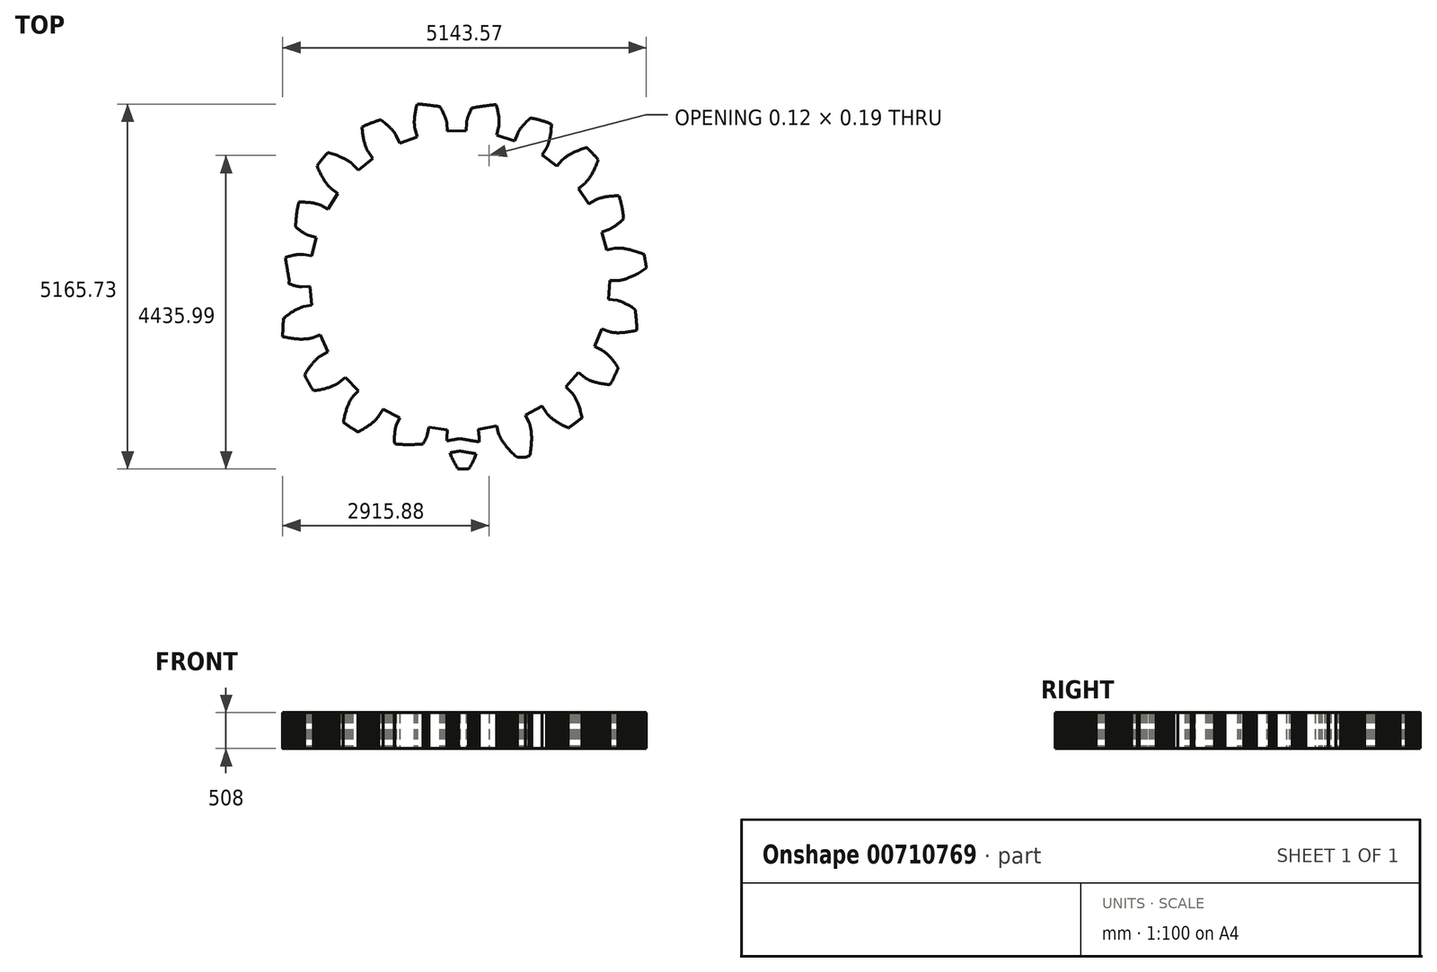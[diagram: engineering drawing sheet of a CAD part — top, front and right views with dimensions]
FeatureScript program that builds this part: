
annotation { "Feature Type Name" : "Feature", "Feature Type Description" : "" }
export const myFeature = defineFeature(function(context is Context, id is Id, definition is map)
    precondition{}
    {
        {
            var Q0;
            Q0=qCreatedBy(makeId("Top.planeOp"),FACE);
            var sketch = newSketch(context, id + "F0", { "sketchPlane" : qUnion([Q0])});
            skLineSegment(sketch, "E0", {"start": v(-9485.18, 1999.38) * mm, "end": v(-9483.34, 1999.46) * mm});
            skLineSegment(sketch, "E1", {"start": v(-9483.34, 1999.46) * mm, "end": v(-9480.74, 1999.63) * mm});
            skLineSegment(sketch, "E2", {"start": v(-9480.74, 1999.63) * mm, "end": v(-9477.39, 1999.9) * mm});
            skLineSegment(sketch, "E3", {"start": v(-9477.39, 1999.9) * mm, "end": v(-9473.3, 2000.32) * mm});
            skLineSegment(sketch, "E4", {"start": v(-9473.3, 2000.32) * mm, "end": v(-9468.45, 2000.9) * mm});
            skLineSegment(sketch, "E5", {"start": v(-9468.45, 2000.9) * mm, "end": v(-9462.88, 2001.66) * mm});
            skLineSegment(sketch, "E6", {"start": v(-9462.88, 2001.66) * mm, "end": v(-9456.58, 2002.65) * mm});
            skLineSegment(sketch, "E7", {"start": v(-9456.58, 2002.65) * mm, "end": v(-9449.55, 2003.88) * mm});
            skLineSegment(sketch, "E8", {"start": v(-9449.55, 2003.88) * mm, "end": v(-9441.8, 2005.4) * mm});
            skLineSegment(sketch, "E9", {"start": v(-9441.8, 2005.4) * mm, "end": v(-9433.35, 2007.2) * mm});
            skLineSegment(sketch, "E10", {"start": v(-9433.35, 2007.2) * mm, "end": v(-9424.2, 2009.33) * mm});
            skLineSegment(sketch, "E11", {"start": v(-9424.2, 2009.33) * mm, "end": v(-9414.34, 2011.82) * mm});
            skLineSegment(sketch, "E12", {"start": v(-9414.34, 2011.82) * mm, "end": v(-9403.81, 2014.68) * mm});
            skLineSegment(sketch, "E13", {"start": v(-9403.81, 2014.68) * mm, "end": v(-9392.62, 2017.95) * mm});
            skLineSegment(sketch, "E14", {"start": v(-9392.62, 2017.95) * mm, "end": v(-9380.76, 2021.65) * mm});
            skLineSegment(sketch, "E15", {"start": v(-9380.76, 2021.65) * mm, "end": v(-9368.25, 2025.8) * mm});
            skLineSegment(sketch, "E16", {"start": v(-9368.25, 2025.8) * mm, "end": v(-9355.11, 2030.43) * mm});
            skLineSegment(sketch, "E17", {"start": v(-9355.11, 2030.43) * mm, "end": v(-9341.35, 2035.57) * mm});
            skLineSegment(sketch, "E18", {"start": v(-9341.35, 2035.57) * mm, "end": v(-9326.99, 2041.24) * mm});
            skLineSegment(sketch, "E19", {"start": v(-9326.99, 2041.24) * mm, "end": v(-9312.03, 2047.46) * mm});
            skLineSegment(sketch, "E20", {"start": v(-9312.03, 2047.46) * mm, "end": v(-9296.5, 2054.26) * mm});
            skLineSegment(sketch, "E21", {"start": v(-9296.5, 2054.26) * mm, "end": v(-9280.41, 2061.65) * mm});
            skLineSegment(sketch, "E22", {"start": v(-9280.41, 2061.65) * mm, "end": v(-9263.78, 2069.67) * mm});
            skLineSegment(sketch, "E23", {"start": v(-9263.78, 2069.67) * mm, "end": v(-9246.63, 2078.33) * mm});
            skLineSegment(sketch, "E24", {"start": v(-9246.63, 2078.33) * mm, "end": v(-9228.97, 2087.66) * mm});
            skLineSegment(sketch, "E25", {"start": v(-9228.97, 2087.66) * mm, "end": v(-9210.82, 2097.68) * mm});
            skLineSegment(sketch, "E26", {"start": v(-9210.82, 2097.68) * mm, "end": v(-9192.2, 2108.4) * mm});
            skLineSegment(sketch, "E27", {"start": v(-9192.2, 2108.4) * mm, "end": v(-9173.14, 2119.86) * mm});
            skLineSegment(sketch, "E28", {"start": v(-9173.14, 2119.86) * mm, "end": v(-9153.66, 2132.06) * mm});
            skLineSegment(sketch, "E29", {"start": v(-9153.66, 2132.06) * mm, "end": v(-9133.76, 2145.04) * mm});
            skLineSegment(sketch, "E30", {"start": v(-9133.76, 2145.04) * mm, "end": v(-9113.48, 2158.8) * mm});
            skLineSegment(sketch, "E31", {"start": v(-9113.48, 2158.8) * mm, "end": v(-9092.85, 2173.36) * mm});
            skLineSegment(sketch, "E32", {"start": v(-9092.85, 2173.36) * mm, "end": v(-9071.87, 2188.75) * mm});
            skLineSegment(sketch, "E33", {"start": v(-9071.87, 2188.75) * mm, "end": v(-9064.77, 2203.89) * mm});
            skLineSegment(sketch, "E34", {"start": v(-9064.77, 2203.89) * mm, "end": v(-9078.9, 2341.03) * mm});
            skLineSegment(sketch, "E35", {"start": v(-9078.9, 2341.03) * mm, "end": v(-9088.93, 2354.4) * mm});
            skLineSegment(sketch, "E36", {"start": v(-9088.93, 2354.4) * mm, "end": v(-9112.6, 2365.2) * mm});
            skLineSegment(sketch, "E37", {"start": v(-9112.6, 2365.2) * mm, "end": v(-9135.78, 2375.25) * mm});
            skLineSegment(sketch, "E38", {"start": v(-9135.78, 2375.25) * mm, "end": v(-9158.43, 2384.59) * mm});
            skLineSegment(sketch, "E39", {"start": v(-9158.43, 2384.59) * mm, "end": v(-9180.55, 2393.23) * mm});
            skLineSegment(sketch, "E40", {"start": v(-9180.55, 2393.23) * mm, "end": v(-9202.12, 2401.2) * mm});
            skLineSegment(sketch, "E41", {"start": v(-9202.12, 2401.2) * mm, "end": v(-9223.11, 2408.54) * mm});
            skLineSegment(sketch, "E42", {"start": v(-9223.11, 2408.54) * mm, "end": v(-9243.52, 2415.25) * mm});
            skLineSegment(sketch, "E43", {"start": v(-9243.52, 2415.25) * mm, "end": v(-9263.33, 2421.35) * mm});
            skLineSegment(sketch, "E44", {"start": v(-9263.33, 2421.35) * mm, "end": v(-9282.52, 2426.89) * mm});
            skLineSegment(sketch, "E45", {"start": v(-9282.52, 2426.89) * mm, "end": v(-9301.08, 2431.87) * mm});
            skLineSegment(sketch, "E46", {"start": v(-9301.08, 2431.87) * mm, "end": v(-9319, 2436.33) * mm});
            skLineSegment(sketch, "E47", {"start": v(-9319, 2436.33) * mm, "end": v(-9336.26, 2440.3) * mm});
            skLineSegment(sketch, "E48", {"start": v(-9336.26, 2440.3) * mm, "end": v(-9352.85, 2443.79) * mm});
            skLineSegment(sketch, "E49", {"start": v(-9352.85, 2443.79) * mm, "end": v(-9368.76, 2446.83) * mm});
            skLineSegment(sketch, "E50", {"start": v(-9368.76, 2446.83) * mm, "end": v(-9383.98, 2449.45) * mm});
            skLineSegment(sketch, "E51", {"start": v(-9383.98, 2449.45) * mm, "end": v(-9398.5, 2451.67) * mm});
            skLineSegment(sketch, "E52", {"start": v(-9398.5, 2451.67) * mm, "end": v(-9412.3, 2453.53) * mm});
            skLineSegment(sketch, "E53", {"start": v(-9412.3, 2453.53) * mm, "end": v(-9425.4, 2455.05) * mm});
            skLineSegment(sketch, "E54", {"start": v(-9425.4, 2455.05) * mm, "end": v(-9437.75, 2456.25) * mm});
            skLineSegment(sketch, "E55", {"start": v(-9437.75, 2456.25) * mm, "end": v(-9449.38, 2457.17) * mm});
            skLineSegment(sketch, "E56", {"start": v(-9449.38, 2457.17) * mm, "end": v(-9460.28, 2457.83) * mm});
            skLineSegment(sketch, "E57", {"start": v(-9460.28, 2457.83) * mm, "end": v(-9470.42, 2458.26) * mm});
            skLineSegment(sketch, "E58", {"start": v(-9470.42, 2458.26) * mm, "end": v(-9479.82, 2458.48) * mm});
            skLineSegment(sketch, "E59", {"start": v(-9479.82, 2458.48) * mm, "end": v(-9488.47, 2458.52) * mm});
            skLineSegment(sketch, "E60", {"start": v(-9488.47, 2458.52) * mm, "end": v(-9496.36, 2458.42) * mm});
            skLineSegment(sketch, "E61", {"start": v(-9496.36, 2458.42) * mm, "end": v(-9503.5, 2458.2) * mm});
            skLineSegment(sketch, "E62", {"start": v(-9503.5, 2458.2) * mm, "end": v(-9509.86, 2457.88) * mm});
            skLineSegment(sketch, "E63", {"start": v(-9509.86, 2457.88) * mm, "end": v(-9515.48, 2457.5) * mm});
            skLineSegment(sketch, "E64", {"start": v(-9515.48, 2457.5) * mm, "end": v(-9520.33, 2457.07) * mm});
            skLineSegment(sketch, "E65", {"start": v(-9520.33, 2457.07) * mm, "end": v(-9524.42, 2456.64) * mm});
            skLineSegment(sketch, "E66", {"start": v(-9524.42, 2456.64) * mm, "end": v(-9527.76, 2456.23) * mm});
            skLineSegment(sketch, "E67", {"start": v(-9527.76, 2456.23) * mm, "end": v(-9530.34, 2455.86) * mm});
            skLineSegment(sketch, "E68", {"start": v(-9530.34, 2455.86) * mm, "end": v(-9532.16, 2455.57) * mm});
            skLineSegment(sketch, "E69", {"start": v(-9532.16, 2455.57) * mm, "end": v(-9533.24, 2455.37) * mm});
            skLineSegment(sketch, "E70", {"start": v(-9533.24, 2455.37) * mm, "end": v(-9647.53, 2431.59) * mm});
            skLineSegment(sketch, "E71", {"start": v(-9647.53, 2431.59) * mm, "end": v(-9717.93, 2688) * mm});
            skLineSegment(sketch, "E72", {"start": v(-9717.93, 2688) * mm, "end": v(-9607.52, 2725.9) * mm});
            skLineSegment(sketch, "E73", {"start": v(-9607.52, 2725.9) * mm, "end": v(-9606.5, 2726.29) * mm});
            skLineSegment(sketch, "E74", {"start": v(-9606.5, 2726.29) * mm, "end": v(-9604.78, 2726.97) * mm});
            skLineSegment(sketch, "E75", {"start": v(-9604.78, 2726.97) * mm, "end": v(-9602.37, 2727.97) * mm});
            skLineSegment(sketch, "E76", {"start": v(-9602.37, 2727.97) * mm, "end": v(-9599.3, 2729.32) * mm});
            skLineSegment(sketch, "E77", {"start": v(-9599.3, 2729.32) * mm, "end": v(-9595.55, 2731.04) * mm});
            skLineSegment(sketch, "E78", {"start": v(-9595.55, 2731.04) * mm, "end": v(-9591.17, 2733.15) * mm});
            skLineSegment(sketch, "E79", {"start": v(-9591.17, 2733.15) * mm, "end": v(-9586.14, 2735.7) * mm});
            skLineSegment(sketch, "E80", {"start": v(-9586.14, 2735.7) * mm, "end": v(-9580.5, 2738.67) * mm});
            skLineSegment(sketch, "E81", {"start": v(-9580.5, 2738.67) * mm, "end": v(-9574.25, 2742.12) * mm});
            skLineSegment(sketch, "E82", {"start": v(-9574.25, 2742.12) * mm, "end": v(-9567.42, 2746.06) * mm});
            skLineSegment(sketch, "E83", {"start": v(-9567.42, 2746.06) * mm, "end": v(-9560, 2750.52) * mm});
            skLineSegment(sketch, "E84", {"start": v(-9560, 2750.52) * mm, "end": v(-9552.04, 2755.5) * mm});
            skLineSegment(sketch, "E85", {"start": v(-9552.04, 2755.5) * mm, "end": v(-9543.53, 2761.05) * mm});
            skLineSegment(sketch, "E86", {"start": v(-9543.53, 2761.05) * mm, "end": v(-9534.5, 2767.18) * mm});
            skLineSegment(sketch, "E87", {"start": v(-9534.5, 2767.18) * mm, "end": v(-9524.97, 2773.91) * mm});
            skLineSegment(sketch, "E88", {"start": v(-9524.97, 2773.91) * mm, "end": v(-9514.96, 2781.26) * mm});
            skLineSegment(sketch, "E89", {"start": v(-9514.96, 2781.26) * mm, "end": v(-9504.48, 2789.25) * mm});
            skLineSegment(sketch, "E90", {"start": v(-9504.48, 2789.25) * mm, "end": v(-9493.56, 2797.9) * mm});
            skLineSegment(sketch, "E91", {"start": v(-9493.56, 2797.9) * mm, "end": v(-9482.21, 2807.22) * mm});
            skLineSegment(sketch, "E92", {"start": v(-9482.21, 2807.22) * mm, "end": v(-9470.46, 2817.25) * mm});
            skLineSegment(sketch, "E93", {"start": v(-9470.46, 2817.25) * mm, "end": v(-9458.34, 2827.99) * mm});
            skLineSegment(sketch, "E94", {"start": v(-9458.34, 2827.99) * mm, "end": v(-9445.86, 2839.46) * mm});
            skLineSegment(sketch, "E95", {"start": v(-9445.86, 2839.46) * mm, "end": v(-9433.04, 2851.68) * mm});
            skLineSegment(sketch, "E96", {"start": v(-9433.04, 2851.68) * mm, "end": v(-9419.91, 2864.66) * mm});
            skLineSegment(sketch, "E97", {"start": v(-9419.91, 2864.66) * mm, "end": v(-9406.5, 2878.43) * mm});
            skLineSegment(sketch, "E98", {"start": v(-9406.5, 2878.43) * mm, "end": v(-9392.83, 2892.98) * mm});
            skLineSegment(sketch, "E99", {"start": v(-9392.83, 2892.98) * mm, "end": v(-9378.91, 2908.35) * mm});
            skLineSegment(sketch, "E100", {"start": v(-9378.91, 2908.35) * mm, "end": v(-9364.8, 2924.54) * mm});
            skLineSegment(sketch, "E101", {"start": v(-9364.8, 2924.54) * mm, "end": v(-9350.48, 2941.56) * mm});
            skLineSegment(sketch, "E102", {"start": v(-9350.48, 2941.56) * mm, "end": v(-9336.01, 2959.43) * mm});
            skLineSegment(sketch, "E103", {"start": v(-9336.01, 2959.43) * mm, "end": v(-9321.4, 2978.16) * mm});
            skLineSegment(sketch, "E104", {"start": v(-9321.4, 2978.16) * mm, "end": v(-9306.7, 2997.76) * mm});
            skLineSegment(sketch, "E105", {"start": v(-9306.7, 2997.76) * mm, "end": v(-9291.91, 3018.24) * mm});
            skLineSegment(sketch, "E106", {"start": v(-9291.91, 3018.24) * mm, "end": v(-9277.07, 3039.6) * mm});
            skLineSegment(sketch, "E107", {"start": v(-9277.07, 3039.6) * mm, "end": v(-9275.26, 3056.23) * mm});
            skLineSegment(sketch, "E108", {"start": v(-9275.26, 3056.23) * mm, "end": v(-9333.15, 3181.36) * mm});
            skLineSegment(sketch, "E109", {"start": v(-9333.15, 3181.36) * mm, "end": v(-9347, 3190.75) * mm});
            skLineSegment(sketch, "E110", {"start": v(-9347, 3190.75) * mm, "end": v(-9372.88, 3193.26) * mm});
            skLineSegment(sketch, "E111", {"start": v(-9372.88, 3193.26) * mm, "end": v(-9398.07, 3195.25) * mm});
            skLineSegment(sketch, "E112", {"start": v(-9398.07, 3195.25) * mm, "end": v(-9422.53, 3196.73) * mm});
            skLineSegment(sketch, "E113", {"start": v(-9422.53, 3196.73) * mm, "end": v(-9446.25, 3197.72) * mm});
            skLineSegment(sketch, "E114", {"start": v(-9446.25, 3197.72) * mm, "end": v(-9469.24, 3198.26) * mm});
            skLineSegment(sketch, "E115", {"start": v(-9469.24, 3198.26) * mm, "end": v(-9491.48, 3198.38) * mm});
            skLineSegment(sketch, "E116", {"start": v(-9491.48, 3198.38) * mm, "end": v(-9512.96, 3198.1) * mm});
            skLineSegment(sketch, "E117", {"start": v(-9512.96, 3198.1) * mm, "end": v(-9533.68, 3197.44) * mm});
            skLineSegment(sketch, "E118", {"start": v(-9533.68, 3197.44) * mm, "end": v(-9553.63, 3196.44) * mm});
            skLineSegment(sketch, "E119", {"start": v(-9553.63, 3196.44) * mm, "end": v(-9572.8, 3195.13) * mm});
            skLineSegment(sketch, "E120", {"start": v(-9572.8, 3195.13) * mm, "end": v(-9591.2, 3193.53) * mm});
            skLineSegment(sketch, "E121", {"start": v(-9591.2, 3193.53) * mm, "end": v(-9608.8, 3191.68) * mm});
            skLineSegment(sketch, "E122", {"start": v(-9608.8, 3191.68) * mm, "end": v(-9625.63, 3189.59) * mm});
            skLineSegment(sketch, "E123", {"start": v(-9625.63, 3189.59) * mm, "end": v(-9641.66, 3187.3) * mm});
            skLineSegment(sketch, "E124", {"start": v(-9641.66, 3187.3) * mm, "end": v(-9656.9, 3184.84) * mm});
            skLineSegment(sketch, "E125", {"start": v(-9656.9, 3184.84) * mm, "end": v(-9671.36, 3182.23) * mm});
            skLineSegment(sketch, "E126", {"start": v(-9671.36, 3182.23) * mm, "end": v(-9685.03, 3179.5) * mm});
            skLineSegment(sketch, "E127", {"start": v(-9685.03, 3179.5) * mm, "end": v(-9697.9, 3176.69) * mm});
            skLineSegment(sketch, "E128", {"start": v(-9697.9, 3176.69) * mm, "end": v(-9709.98, 3173.81) * mm});
            skLineSegment(sketch, "E129", {"start": v(-9709.98, 3173.81) * mm, "end": v(-9721.28, 3170.9) * mm});
            skLineSegment(sketch, "E130", {"start": v(-9721.28, 3170.9) * mm, "end": v(-9731.8, 3167.99) * mm});
            skLineSegment(sketch, "E131", {"start": v(-9731.8, 3167.99) * mm, "end": v(-9741.53, 3165.1) * mm});
            skLineSegment(sketch, "E132", {"start": v(-9741.53, 3165.1) * mm, "end": v(-9750.5, 3162.26) * mm});
            skLineSegment(sketch, "E133", {"start": v(-9750.5, 3162.26) * mm, "end": v(-9758.69, 3159.5) * mm});
            skLineSegment(sketch, "E134", {"start": v(-9758.69, 3159.5) * mm, "end": v(-9766.12, 3156.83) * mm});
            skLineSegment(sketch, "E135", {"start": v(-9766.12, 3156.83) * mm, "end": v(-9772.79, 3154.3) * mm});
            skLineSegment(sketch, "E136", {"start": v(-9772.79, 3154.3) * mm, "end": v(-9778.71, 3151.93) * mm});
            skLineSegment(sketch, "E137", {"start": v(-9778.71, 3151.93) * mm, "end": v(-9783.9, 3149.75) * mm});
            skLineSegment(sketch, "E138", {"start": v(-9783.9, 3149.75) * mm, "end": v(-9788.35, 3147.77) * mm});
            skLineSegment(sketch, "E139", {"start": v(-9788.35, 3147.77) * mm, "end": v(-9792.08, 3146.04) * mm});
            skLineSegment(sketch, "E140", {"start": v(-9792.08, 3146.04) * mm, "end": v(-9795.1, 3144.57) * mm});
            skLineSegment(sketch, "E141", {"start": v(-9795.1, 3144.57) * mm, "end": v(-9797.42, 3143.38) * mm});
            skLineSegment(sketch, "E142", {"start": v(-9797.42, 3143.38) * mm, "end": v(-9799.06, 3142.5) * mm});
            skLineSegment(sketch, "E143", {"start": v(-9799.06, 3142.5) * mm, "end": v(-9800.01, 3141.98) * mm});
            skLineSegment(sketch, "E144", {"start": v(-9800.01, 3141.98) * mm, "end": v(-9900.38, 3082.37) * mm});
            skLineSegment(sketch, "E145", {"start": v(-9900.38, 3082.37) * mm, "end": v(-10050.23, 3302.03) * mm});
            skLineSegment(sketch, "E146", {"start": v(-10050.23, 3302.03) * mm, "end": v(-9958.1, 3373.73) * mm});
            skLineSegment(sketch, "E147", {"start": v(-9958.1, 3373.73) * mm, "end": v(-9957.26, 3374.43) * mm});
            skLineSegment(sketch, "E148", {"start": v(-9957.26, 3374.43) * mm, "end": v(-9955.86, 3375.63) * mm});
            skLineSegment(sketch, "E149", {"start": v(-9955.86, 3375.63) * mm, "end": v(-9953.9, 3377.36) * mm});
            skLineSegment(sketch, "E150", {"start": v(-9953.9, 3377.36) * mm, "end": v(-9951.43, 3379.63) * mm});
            skLineSegment(sketch, "E151", {"start": v(-9951.43, 3379.63) * mm, "end": v(-9948.45, 3382.47) * mm});
            skLineSegment(sketch, "E152", {"start": v(-9948.45, 3382.47) * mm, "end": v(-9945, 3385.9) * mm});
            skLineSegment(sketch, "E153", {"start": v(-9945, 3385.9) * mm, "end": v(-9941.07, 3389.93) * mm});
            skLineSegment(sketch, "E154", {"start": v(-9941.07, 3389.93) * mm, "end": v(-9936.7, 3394.58) * mm});
            skLineSegment(sketch, "E155", {"start": v(-9936.7, 3394.58) * mm, "end": v(-9931.9, 3399.87) * mm});
            skLineSegment(sketch, "E156", {"start": v(-9931.9, 3399.87) * mm, "end": v(-9926.72, 3405.82) * mm});
            skLineSegment(sketch, "E157", {"start": v(-9926.72, 3405.82) * mm, "end": v(-9921.16, 3412.43) * mm});
            skLineSegment(sketch, "E158", {"start": v(-9921.16, 3412.43) * mm, "end": v(-9915.24, 3419.74) * mm});
            skLineSegment(sketch, "E159", {"start": v(-9915.24, 3419.74) * mm, "end": v(-9909, 3427.75) * mm});
            skLineSegment(sketch, "E160", {"start": v(-9909, 3427.75) * mm, "end": v(-9902.45, 3436.48) * mm});
            skLineSegment(sketch, "E161", {"start": v(-9902.45, 3436.48) * mm, "end": v(-9895.62, 3445.94) * mm});
            skLineSegment(sketch, "E162", {"start": v(-9895.62, 3445.94) * mm, "end": v(-9888.53, 3456.14) * mm});
            skLineSegment(sketch, "E163", {"start": v(-9888.53, 3456.14) * mm, "end": v(-9881.21, 3467.1) * mm});
            skLineSegment(sketch, "E164", {"start": v(-9881.21, 3467.1) * mm, "end": v(-9873.7, 3478.83) * mm});
            skLineSegment(sketch, "E165", {"start": v(-9873.7, 3478.83) * mm, "end": v(-9866, 3491.33) * mm});
            skLineSegment(sketch, "E166", {"start": v(-9866, 3491.33) * mm, "end": v(-9858.14, 3504.63) * mm});
            skLineSegment(sketch, "E167", {"start": v(-9858.14, 3504.63) * mm, "end": v(-9850.15, 3518.72) * mm});
            skLineSegment(sketch, "E168", {"start": v(-9850.15, 3518.72) * mm, "end": v(-9842.07, 3533.62) * mm});
            skLineSegment(sketch, "E169", {"start": v(-9842.07, 3533.62) * mm, "end": v(-9833.92, 3549.34) * mm});
            skLineSegment(sketch, "E170", {"start": v(-9833.92, 3549.34) * mm, "end": v(-9825.72, 3565.88) * mm});
            skLineSegment(sketch, "E171", {"start": v(-9825.72, 3565.88) * mm, "end": v(-9817.5, 3583.26) * mm});
            skLineSegment(sketch, "E172", {"start": v(-9817.5, 3583.26) * mm, "end": v(-9809.3, 3601.47) * mm});
            skLineSegment(sketch, "E173", {"start": v(-9809.3, 3601.47) * mm, "end": v(-9801.13, 3620.52) * mm});
            skLineSegment(sketch, "E174", {"start": v(-9801.13, 3620.52) * mm, "end": v(-9793.03, 3640.42) * mm});
            skLineSegment(sketch, "E175", {"start": v(-9793.03, 3640.42) * mm, "end": v(-9785.02, 3661.16) * mm});
            skLineSegment(sketch, "E176", {"start": v(-9785.02, 3661.16) * mm, "end": v(-9777.14, 3682.76) * mm});
            skLineSegment(sketch, "E177", {"start": v(-9777.14, 3682.76) * mm, "end": v(-9769.4, 3705.22) * mm});
            skLineSegment(sketch, "E178", {"start": v(-9769.4, 3705.22) * mm, "end": v(-9761.86, 3728.53) * mm});
            skLineSegment(sketch, "E179", {"start": v(-9761.86, 3728.53) * mm, "end": v(-9754.52, 3752.7) * mm});
            skLineSegment(sketch, "E180", {"start": v(-9754.52, 3752.7) * mm, "end": v(-9747.42, 3777.73) * mm});
            skLineSegment(sketch, "E181", {"start": v(-9747.42, 3777.73) * mm, "end": v(-9751.1, 3794.04) * mm});
            skLineSegment(sketch, "E182", {"start": v(-9751.1, 3794.04) * mm, "end": v(-9846.5, 3893.6) * mm});
            skLineSegment(sketch, "E183", {"start": v(-9846.5, 3893.6) * mm, "end": v(-9862.63, 3897.98) * mm});
            skLineSegment(sketch, "E184", {"start": v(-9862.63, 3897.98) * mm, "end": v(-9887.93, 3891.95) * mm});
            skLineSegment(sketch, "E185", {"start": v(-9887.93, 3891.95) * mm, "end": v(-9912.4, 3885.65) * mm});
            skLineSegment(sketch, "E186", {"start": v(-9912.4, 3885.65) * mm, "end": v(-9936, 3879.1) * mm});
            skLineSegment(sketch, "E187", {"start": v(-9936, 3879.1) * mm, "end": v(-9958.78, 3872.34) * mm});
            skLineSegment(sketch, "E188", {"start": v(-9958.78, 3872.34) * mm, "end": v(-9980.7, 3865.4) * mm});
            skLineSegment(sketch, "E189", {"start": v(-9980.7, 3865.4) * mm, "end": v(-10001.76, 3858.28) * mm});
            skLineSegment(sketch, "E190", {"start": v(-10001.76, 3858.28) * mm, "end": v(-10021.99, 3851.04) * mm});
            skLineSegment(sketch, "E191", {"start": v(-10021.99, 3851.04) * mm, "end": v(-10041.37, 3843.7) * mm});
            skLineSegment(sketch, "E192", {"start": v(-10041.37, 3843.7) * mm, "end": v(-10059.92, 3836.27) * mm});
            skLineSegment(sketch, "E193", {"start": v(-10059.92, 3836.27) * mm, "end": v(-10077.63, 3828.8) * mm});
            skLineSegment(sketch, "E194", {"start": v(-10077.63, 3828.8) * mm, "end": v(-10094.5, 3821.32) * mm});
            skLineSegment(sketch, "E195", {"start": v(-10094.5, 3821.32) * mm, "end": v(-10110.56, 3813.85) * mm});
            skLineSegment(sketch, "E196", {"start": v(-10110.56, 3813.85) * mm, "end": v(-10125.8, 3806.4) * mm});
            skLineSegment(sketch, "E197", {"start": v(-10125.8, 3806.4) * mm, "end": v(-10140.21, 3799.04) * mm});
            skLineSegment(sketch, "E198", {"start": v(-10140.21, 3799.04) * mm, "end": v(-10153.83, 3791.76) * mm});
            skLineSegment(sketch, "E199", {"start": v(-10153.83, 3791.76) * mm, "end": v(-10166.66, 3784.6) * mm});
            skLineSegment(sketch, "E200", {"start": v(-10166.66, 3784.6) * mm, "end": v(-10178.7, 3777.58) * mm});
            skLineSegment(sketch, "E201", {"start": v(-10178.7, 3777.58) * mm, "end": v(-10189.96, 3770.74) * mm});
            skLineSegment(sketch, "E202", {"start": v(-10189.96, 3770.74) * mm, "end": v(-10200.45, 3764.1) * mm});
            skLineSegment(sketch, "E203", {"start": v(-10200.45, 3764.1) * mm, "end": v(-10210.2, 3757.68) * mm});
            skLineSegment(sketch, "E204", {"start": v(-10210.2, 3757.68) * mm, "end": v(-10219.2, 3751.5) * mm});
            skLineSegment(sketch, "E205", {"start": v(-10219.2, 3751.5) * mm, "end": v(-10227.46, 3745.61) * mm});
            skLineSegment(sketch, "E206", {"start": v(-10227.46, 3745.61) * mm, "end": v(-10235.02, 3740.01) * mm});
            skLineSegment(sketch, "E207", {"start": v(-10235.02, 3740.01) * mm, "end": v(-10241.87, 3734.74) * mm});
            skLineSegment(sketch, "E208", {"start": v(-10241.87, 3734.74) * mm, "end": v(-10248.03, 3729.81) * mm});
            skLineSegment(sketch, "E209", {"start": v(-10248.03, 3729.81) * mm, "end": v(-10253.52, 3725.25) * mm});
            skLineSegment(sketch, "E210", {"start": v(-10253.52, 3725.25) * mm, "end": v(-10258.36, 3721.09) * mm});
            skLineSegment(sketch, "E211", {"start": v(-10258.36, 3721.09) * mm, "end": v(-10262.55, 3717.34) * mm});
            skLineSegment(sketch, "E212", {"start": v(-10262.55, 3717.34) * mm, "end": v(-10266.12, 3714.03) * mm});
            skLineSegment(sketch, "E213", {"start": v(-10266.12, 3714.03) * mm, "end": v(-10269.09, 3711.17) * mm});
            skLineSegment(sketch, "E214", {"start": v(-10269.09, 3711.17) * mm, "end": v(-10271.46, 3708.8) * mm});
            skLineSegment(sketch, "E215", {"start": v(-10271.46, 3708.8) * mm, "end": v(-10273.27, 3706.92) * mm});
            skLineSegment(sketch, "E216", {"start": v(-10273.27, 3706.92) * mm, "end": v(-10274.54, 3705.57) * mm});
            skLineSegment(sketch, "E217", {"start": v(-10274.54, 3705.57) * mm, "end": v(-10275.27, 3704.76) * mm});
            skLineSegment(sketch, "E218", {"start": v(-10275.27, 3704.76) * mm, "end": v(-10350.84, 3615.79) * mm});
            skLineSegment(sketch, "E219", {"start": v(-10350.84, 3615.79) * mm, "end": v(-10563.9, 3774.9) * mm});
            skLineSegment(sketch, "E220", {"start": v(-10563.9, 3774.9) * mm, "end": v(-10500.05, 3872.62) * mm});
            skLineSegment(sketch, "E221", {"start": v(-10500.05, 3872.62) * mm, "end": v(-10499.47, 3873.55) * mm});
            skLineSegment(sketch, "E222", {"start": v(-10499.47, 3873.55) * mm, "end": v(-10498.53, 3875.15) * mm});
            skLineSegment(sketch, "E223", {"start": v(-10498.53, 3875.15) * mm, "end": v(-10497.25, 3877.41) * mm});
            skLineSegment(sketch, "E224", {"start": v(-10497.25, 3877.41) * mm, "end": v(-10495.65, 3880.37) * mm});
            skLineSegment(sketch, "E225", {"start": v(-10495.65, 3880.37) * mm, "end": v(-10493.76, 3884.02) * mm});
            skLineSegment(sketch, "E226", {"start": v(-10493.76, 3884.02) * mm, "end": v(-10491.6, 3888.38) * mm});
            skLineSegment(sketch, "E227", {"start": v(-10491.6, 3888.38) * mm, "end": v(-10489.19, 3893.47) * mm});
            skLineSegment(sketch, "E228", {"start": v(-10489.19, 3893.47) * mm, "end": v(-10486.57, 3899.29) * mm});
            skLineSegment(sketch, "E229", {"start": v(-10486.57, 3899.29) * mm, "end": v(-10483.76, 3905.85) * mm});
            skLineSegment(sketch, "E230", {"start": v(-10483.76, 3905.85) * mm, "end": v(-10480.78, 3913.16) * mm});
            skLineSegment(sketch, "E231", {"start": v(-10480.78, 3913.16) * mm, "end": v(-10477.67, 3921.22) * mm});
            skLineSegment(sketch, "E232", {"start": v(-10477.67, 3921.22) * mm, "end": v(-10474.45, 3930.05) * mm});
            skLineSegment(sketch, "E233", {"start": v(-10474.45, 3930.05) * mm, "end": v(-10471.14, 3939.66) * mm});
            skLineSegment(sketch, "E234", {"start": v(-10471.14, 3939.66) * mm, "end": v(-10467.78, 3950.04) * mm});
            skLineSegment(sketch, "E235", {"start": v(-10467.78, 3950.04) * mm, "end": v(-10464.39, 3961.2) * mm});
            skLineSegment(sketch, "E236", {"start": v(-10464.39, 3961.2) * mm, "end": v(-10461, 3973.15) * mm});
            skLineSegment(sketch, "E237", {"start": v(-10461, 3973.15) * mm, "end": v(-10457.64, 3985.9) * mm});
            skLineSegment(sketch, "E238", {"start": v(-10457.64, 3985.9) * mm, "end": v(-10454.33, 3999.43) * mm});
            skLineSegment(sketch, "E239", {"start": v(-10454.33, 3999.43) * mm, "end": v(-10451.1, 4013.76) * mm});
            skLineSegment(sketch, "E240", {"start": v(-10451.1, 4013.76) * mm, "end": v(-10448, 4028.88) * mm});
            skLineSegment(sketch, "E241", {"start": v(-10448, 4028.88) * mm, "end": v(-10445.02, 4044.8) * mm});
            skLineSegment(sketch, "E242", {"start": v(-10445.02, 4044.8) * mm, "end": v(-10442.22, 4061.52) * mm});
            skLineSegment(sketch, "E243", {"start": v(-10442.22, 4061.52) * mm, "end": v(-10439.6, 4079.04) * mm});
            skLineSegment(sketch, "E244", {"start": v(-10439.6, 4079.04) * mm, "end": v(-10437.23, 4097.35) * mm});
            skLineSegment(sketch, "E245", {"start": v(-10437.23, 4097.35) * mm, "end": v(-10435.1, 4116.45) * mm});
            skLineSegment(sketch, "E246", {"start": v(-10435.1, 4116.45) * mm, "end": v(-10433.24, 4136.34) * mm});
            skLineSegment(sketch, "E247", {"start": v(-10433.24, 4136.34) * mm, "end": v(-10431.7, 4157) * mm});
            skLineSegment(sketch, "E248", {"start": v(-10431.7, 4157) * mm, "end": v(-10430.5, 4178.46) * mm});
            skLineSegment(sketch, "E249", {"start": v(-10430.5, 4178.46) * mm, "end": v(-10429.67, 4200.68) * mm});
            skLineSegment(sketch, "E250", {"start": v(-10429.67, 4200.68) * mm, "end": v(-10429.23, 4223.67) * mm});
            skLineSegment(sketch, "E251", {"start": v(-10429.23, 4223.67) * mm, "end": v(-10429.2, 4247.42) * mm});
            skLineSegment(sketch, "E252", {"start": v(-10429.2, 4247.42) * mm, "end": v(-10429.63, 4271.92) * mm});
            skLineSegment(sketch, "E253", {"start": v(-10429.63, 4271.92) * mm, "end": v(-10430.54, 4297.16) * mm});
            skLineSegment(sketch, "E254", {"start": v(-10430.54, 4297.16) * mm, "end": v(-10431.95, 4323.14) * mm});
            skLineSegment(sketch, "E255", {"start": v(-10431.95, 4323.14) * mm, "end": v(-10440.74, 4337.36) * mm});
            skLineSegment(sketch, "E256", {"start": v(-10440.74, 4337.36) * mm, "end": v(-10563.28, 4400.55) * mm});
            skLineSegment(sketch, "E257", {"start": v(-10563.28, 4400.55) * mm, "end": v(-10579.96, 4399.46) * mm});
            skLineSegment(sketch, "E258", {"start": v(-10579.96, 4399.46) * mm, "end": v(-10601.94, 4385.55) * mm});
            skLineSegment(sketch, "E259", {"start": v(-10601.94, 4385.55) * mm, "end": v(-10623.03, 4371.65) * mm});
            skLineSegment(sketch, "E260", {"start": v(-10623.03, 4371.65) * mm, "end": v(-10643.24, 4357.79) * mm});
            skLineSegment(sketch, "E261", {"start": v(-10643.24, 4357.79) * mm, "end": v(-10662.58, 4344) * mm});
            skLineSegment(sketch, "E262", {"start": v(-10662.58, 4344) * mm, "end": v(-10681.05, 4330.3) * mm});
            skLineSegment(sketch, "E263", {"start": v(-10681.05, 4330.3) * mm, "end": v(-10698.67, 4316.74) * mm});
            skLineSegment(sketch, "E264", {"start": v(-10698.67, 4316.74) * mm, "end": v(-10715.45, 4303.32) * mm});
            skLineSegment(sketch, "E265", {"start": v(-10715.45, 4303.32) * mm, "end": v(-10731.4, 4290.08) * mm});
            skLineSegment(sketch, "E266", {"start": v(-10731.4, 4290.08) * mm, "end": v(-10746.53, 4277.04) * mm});
            skLineSegment(sketch, "E267", {"start": v(-10746.53, 4277.04) * mm, "end": v(-10760.85, 4264.23) * mm});
            skLineSegment(sketch, "E268", {"start": v(-10760.85, 4264.23) * mm, "end": v(-10774.38, 4251.67) * mm});
            skLineSegment(sketch, "E269", {"start": v(-10774.38, 4251.67) * mm, "end": v(-10787.14, 4239.39) * mm});
            skLineSegment(sketch, "E270", {"start": v(-10787.14, 4239.39) * mm, "end": v(-10799.14, 4227.4) * mm});
            skLineSegment(sketch, "E271", {"start": v(-10799.14, 4227.4) * mm, "end": v(-10810.38, 4215.75) * mm});
            skLineSegment(sketch, "E272", {"start": v(-10810.38, 4215.75) * mm, "end": v(-10820.9, 4204.44) * mm});
            skLineSegment(sketch, "E273", {"start": v(-10820.9, 4204.44) * mm, "end": v(-10830.7, 4193.5) * mm});
            skLineSegment(sketch, "E274", {"start": v(-10830.7, 4193.5) * mm, "end": v(-10839.81, 4182.97) * mm});
            skLineSegment(sketch, "E275", {"start": v(-10839.81, 4182.97) * mm, "end": v(-10848.24, 4172.84) * mm});
            skLineSegment(sketch, "E276", {"start": v(-10848.24, 4172.84) * mm, "end": v(-10856.01, 4163.15) * mm});
            skLineSegment(sketch, "E277", {"start": v(-10856.01, 4163.15) * mm, "end": v(-10863.14, 4153.91) * mm});
            skLineSegment(sketch, "E278", {"start": v(-10863.14, 4153.91) * mm, "end": v(-10869.65, 4145.15) * mm});
            skLineSegment(sketch, "E279", {"start": v(-10869.65, 4145.15) * mm, "end": v(-10875.56, 4136.9) * mm});
            skLineSegment(sketch, "E280", {"start": v(-10875.56, 4136.9) * mm, "end": v(-10880.88, 4129.14) * mm});
            skLineSegment(sketch, "E281", {"start": v(-10880.88, 4129.14) * mm, "end": v(-10885.65, 4121.93) * mm});
            skLineSegment(sketch, "E282", {"start": v(-10885.65, 4121.93) * mm, "end": v(-10889.88, 4115.27) * mm});
            skLineSegment(sketch, "E283", {"start": v(-10889.88, 4115.27) * mm, "end": v(-10893.6, 4109.17) * mm});
            skLineSegment(sketch, "E284", {"start": v(-10893.6, 4109.17) * mm, "end": v(-10896.81, 4103.67) * mm});
            skLineSegment(sketch, "E285", {"start": v(-10896.81, 4103.67) * mm, "end": v(-10899.56, 4098.76) * mm});
            skLineSegment(sketch, "E286", {"start": v(-10899.56, 4098.76) * mm, "end": v(-10901.86, 4094.46) * mm});
            skLineSegment(sketch, "E287", {"start": v(-10901.86, 4094.46) * mm, "end": v(-10903.74, 4090.8) * mm});
            skLineSegment(sketch, "E288", {"start": v(-10903.74, 4090.8) * mm, "end": v(-10905.22, 4087.78) * mm});
            skLineSegment(sketch, "E289", {"start": v(-10905.22, 4087.78) * mm, "end": v(-10906.32, 4085.42) * mm});
            skLineSegment(sketch, "E290", {"start": v(-10906.32, 4085.42) * mm, "end": v(-10907.08, 4083.73) * mm});
            skLineSegment(sketch, "E291", {"start": v(-10907.08, 4083.73) * mm, "end": v(-10907.5, 4082.73) * mm});
            skLineSegment(sketch, "E292", {"start": v(-10907.5, 4082.73) * mm, "end": v(-10950.1, 3974.04) * mm});
            skLineSegment(sketch, "E293", {"start": v(-10950.1, 3974.04) * mm, "end": v(-11203.26, 4055.34) * mm});
            skLineSegment(sketch, "E294", {"start": v(-11203.26, 4055.34) * mm, "end": v(-11174.61, 4168.5) * mm});
            skLineSegment(sketch, "E295", {"start": v(-11174.61, 4168.5) * mm, "end": v(-11174.37, 4169.58) * mm});
            skLineSegment(sketch, "E296", {"start": v(-11174.37, 4169.58) * mm, "end": v(-11174, 4171.39) * mm});
            skLineSegment(sketch, "E297", {"start": v(-11174, 4171.39) * mm, "end": v(-11173.52, 4173.95) * mm});
            skLineSegment(sketch, "E298", {"start": v(-11173.52, 4173.95) * mm, "end": v(-11172.97, 4177.26) * mm});
            skLineSegment(sketch, "E299", {"start": v(-11172.97, 4177.26) * mm, "end": v(-11172.36, 4181.33) * mm});
            skLineSegment(sketch, "E300", {"start": v(-11172.36, 4181.33) * mm, "end": v(-11171.73, 4186.16) * mm});
            skLineSegment(sketch, "E301", {"start": v(-11171.73, 4186.16) * mm, "end": v(-11171.11, 4191.76) * mm});
            skLineSegment(sketch, "E302", {"start": v(-11171.11, 4191.76) * mm, "end": v(-11170.52, 4198.1) * mm});
            skLineSegment(sketch, "E303", {"start": v(-11170.52, 4198.1) * mm, "end": v(-11170, 4205.23) * mm});
            skLineSegment(sketch, "E304", {"start": v(-11170, 4205.23) * mm, "end": v(-11169.55, 4213.1) * mm});
            skLineSegment(sketch, "E305", {"start": v(-11169.55, 4213.1) * mm, "end": v(-11169.23, 4221.75) * mm});
            skLineSegment(sketch, "E306", {"start": v(-11169.23, 4221.75) * mm, "end": v(-11169.05, 4231.15) * mm});
            skLineSegment(sketch, "E307", {"start": v(-11169.05, 4231.15) * mm, "end": v(-11169.04, 4241.3) * mm});
            skLineSegment(sketch, "E308", {"start": v(-11169.04, 4241.3) * mm, "end": v(-11169.23, 4252.21) * mm});
            skLineSegment(sketch, "E309", {"start": v(-11169.23, 4252.21) * mm, "end": v(-11169.65, 4263.87) * mm});
            skLineSegment(sketch, "E310", {"start": v(-11169.65, 4263.87) * mm, "end": v(-11170.32, 4276.27) * mm});
            skLineSegment(sketch, "E311", {"start": v(-11170.32, 4276.27) * mm, "end": v(-11171.28, 4289.42) * mm});
            skLineSegment(sketch, "E312", {"start": v(-11171.28, 4289.42) * mm, "end": v(-11172.55, 4303.3) * mm});
            skLineSegment(sketch, "E313", {"start": v(-11172.55, 4303.3) * mm, "end": v(-11174.15, 4317.9) * mm});
            skLineSegment(sketch, "E314", {"start": v(-11174.15, 4317.9) * mm, "end": v(-11176.12, 4333.2) * mm});
            skLineSegment(sketch, "E315", {"start": v(-11176.12, 4333.2) * mm, "end": v(-11178.48, 4349.23) * mm});
            skLineSegment(sketch, "E316", {"start": v(-11178.48, 4349.23) * mm, "end": v(-11181.25, 4365.96) * mm});
            skLineSegment(sketch, "E317", {"start": v(-11181.25, 4365.96) * mm, "end": v(-11184.47, 4383.37) * mm});
            skLineSegment(sketch, "E318", {"start": v(-11184.47, 4383.37) * mm, "end": v(-11188.16, 4401.46) * mm});
            skLineSegment(sketch, "E319", {"start": v(-11188.16, 4401.46) * mm, "end": v(-11192.35, 4420.22) * mm});
            skLineSegment(sketch, "E320", {"start": v(-11192.35, 4420.22) * mm, "end": v(-11197.06, 4439.63) * mm});
            skLineSegment(sketch, "E321", {"start": v(-11197.06, 4439.63) * mm, "end": v(-11202.31, 4459.68) * mm});
            skLineSegment(sketch, "E322", {"start": v(-11202.31, 4459.68) * mm, "end": v(-11208.14, 4480.36) * mm});
            skLineSegment(sketch, "E323", {"start": v(-11208.14, 4480.36) * mm, "end": v(-11214.56, 4501.65) * mm});
            skLineSegment(sketch, "E324", {"start": v(-11214.56, 4501.65) * mm, "end": v(-11221.61, 4523.53) * mm});
            skLineSegment(sketch, "E325", {"start": v(-11221.61, 4523.53) * mm, "end": v(-11229.3, 4546) * mm});
            skLineSegment(sketch, "E326", {"start": v(-11229.3, 4546) * mm, "end": v(-11237.66, 4569.04) * mm});
            skLineSegment(sketch, "E327", {"start": v(-11237.66, 4569.04) * mm, "end": v(-11246.72, 4592.62) * mm});
            skLineSegment(sketch, "E328", {"start": v(-11246.72, 4592.62) * mm, "end": v(-11256.49, 4616.73) * mm});
            skLineSegment(sketch, "E329", {"start": v(-11256.49, 4616.73) * mm, "end": v(-11269.42, 4627.33) * mm});
            skLineSegment(sketch, "E330", {"start": v(-11269.42, 4627.33) * mm, "end": v(-11405.83, 4647.3) * mm});
            skLineSegment(sketch, "E331", {"start": v(-11405.83, 4647.3) * mm, "end": v(-11421.26, 4640.86) * mm});
            skLineSegment(sketch, "E332", {"start": v(-11421.26, 4640.86) * mm, "end": v(-11437.53, 4620.56) * mm});
            skLineSegment(sketch, "E333", {"start": v(-11437.53, 4620.56) * mm, "end": v(-11452.97, 4600.56) * mm});
            skLineSegment(sketch, "E334", {"start": v(-11452.97, 4600.56) * mm, "end": v(-11467.58, 4580.9) * mm});
            skLineSegment(sketch, "E335", {"start": v(-11467.58, 4580.9) * mm, "end": v(-11481.4, 4561.57) * mm});
            skLineSegment(sketch, "E336", {"start": v(-11481.4, 4561.57) * mm, "end": v(-11494.42, 4542.63) * mm});
            skLineSegment(sketch, "E337", {"start": v(-11494.42, 4542.63) * mm, "end": v(-11506.68, 4524.07) * mm});
            skLineSegment(sketch, "E338", {"start": v(-11506.68, 4524.07) * mm, "end": v(-11518.2, 4505.93) * mm});
            skLineSegment(sketch, "E339", {"start": v(-11518.2, 4505.93) * mm, "end": v(-11528.97, 4488.23) * mm});
            skLineSegment(sketch, "E340", {"start": v(-11528.97, 4488.23) * mm, "end": v(-11539.05, 4470.98) * mm});
            skLineSegment(sketch, "E341", {"start": v(-11539.05, 4470.98) * mm, "end": v(-11548.44, 4454.22) * mm});
            skLineSegment(sketch, "E342", {"start": v(-11548.44, 4454.22) * mm, "end": v(-11557.16, 4437.94) * mm});
            skLineSegment(sketch, "E343", {"start": v(-11557.16, 4437.94) * mm, "end": v(-11565.24, 4422.19) * mm});
            skLineSegment(sketch, "E344", {"start": v(-11565.24, 4422.19) * mm, "end": v(-11572.7, 4406.96) * mm});
            skLineSegment(sketch, "E345", {"start": v(-11572.7, 4406.96) * mm, "end": v(-11579.55, 4392.28) * mm});
            skLineSegment(sketch, "E346", {"start": v(-11579.55, 4392.28) * mm, "end": v(-11585.83, 4378.17) * mm});
            skLineSegment(sketch, "E347", {"start": v(-11585.83, 4378.17) * mm, "end": v(-11591.55, 4364.65) * mm});
            skLineSegment(sketch, "E348", {"start": v(-11591.55, 4364.65) * mm, "end": v(-11596.74, 4351.72) * mm});
            skLineSegment(sketch, "E349", {"start": v(-11596.74, 4351.72) * mm, "end": v(-11601.42, 4339.4) * mm});
            skLineSegment(sketch, "E350", {"start": v(-11601.42, 4339.4) * mm, "end": v(-11605.63, 4327.71) * mm});
            skLineSegment(sketch, "E351", {"start": v(-11605.63, 4327.71) * mm, "end": v(-11609.37, 4316.66) * mm});
            skLineSegment(sketch, "E352", {"start": v(-11609.37, 4316.66) * mm, "end": v(-11612.68, 4306.27) * mm});
            skLineSegment(sketch, "E353", {"start": v(-11612.68, 4306.27) * mm, "end": v(-11615.59, 4296.53) * mm});
            skLineSegment(sketch, "E354", {"start": v(-11615.59, 4296.53) * mm, "end": v(-11618.1, 4287.48) * mm});
            skLineSegment(sketch, "E355", {"start": v(-11618.1, 4287.48) * mm, "end": v(-11620.27, 4279.1) * mm});
            skLineSegment(sketch, "E356", {"start": v(-11620.27, 4279.1) * mm, "end": v(-11622.11, 4271.43) * mm});
            skLineSegment(sketch, "E357", {"start": v(-11622.11, 4271.43) * mm, "end": v(-11623.64, 4264.46) * mm});
            skLineSegment(sketch, "E358", {"start": v(-11623.64, 4264.46) * mm, "end": v(-11624.9, 4258.2) * mm});
            skLineSegment(sketch, "E359", {"start": v(-11624.9, 4258.2) * mm, "end": v(-11625.9, 4252.67) * mm});
            skLineSegment(sketch, "E360", {"start": v(-11625.9, 4252.67) * mm, "end": v(-11626.7, 4247.86) * mm});
            skLineSegment(sketch, "E361", {"start": v(-11626.7, 4247.86) * mm, "end": v(-11627.28, 4243.8) * mm});
            skLineSegment(sketch, "E362", {"start": v(-11627.28, 4243.8) * mm, "end": v(-11627.7, 4240.46) * mm});
            skLineSegment(sketch, "E363", {"start": v(-11627.7, 4240.46) * mm, "end": v(-11627.97, 4237.87) * mm});
            skLineSegment(sketch, "E364", {"start": v(-11627.97, 4237.87) * mm, "end": v(-11628.14, 4236.02) * mm});
            skLineSegment(sketch, "E365", {"start": v(-11628.14, 4236.02) * mm, "end": v(-11628.21, 4234.93) * mm});
            skLineSegment(sketch, "E366", {"start": v(-11628.21, 4234.93) * mm, "end": v(-11633.2, 4118.3) * mm});
            skLineSegment(sketch, "E367", {"start": v(-11633.2, 4118.3) * mm, "end": v(-11899.06, 4113) * mm});
            skLineSegment(sketch, "E368", {"start": v(-11899.06, 4113) * mm, "end": v(-11908.7, 4229.33) * mm});
            skLineSegment(sketch, "E369", {"start": v(-11908.7, 4229.33) * mm, "end": v(-11908.82, 4230.42) * mm});
            skLineSegment(sketch, "E370", {"start": v(-11908.82, 4230.42) * mm, "end": v(-11909.06, 4232.26) * mm});
            skLineSegment(sketch, "E371", {"start": v(-11909.06, 4232.26) * mm, "end": v(-11909.44, 4234.84) * mm});
            skLineSegment(sketch, "E372", {"start": v(-11909.44, 4234.84) * mm, "end": v(-11909.99, 4238.15) * mm});
            skLineSegment(sketch, "E373", {"start": v(-11909.99, 4238.15) * mm, "end": v(-11910.74, 4242.2) * mm});
            skLineSegment(sketch, "E374", {"start": v(-11910.74, 4242.2) * mm, "end": v(-11911.71, 4246.97) * mm});
            skLineSegment(sketch, "E375", {"start": v(-11911.71, 4246.97) * mm, "end": v(-11912.94, 4252.46) * mm});
            skLineSegment(sketch, "E376", {"start": v(-11912.94, 4252.46) * mm, "end": v(-11914.44, 4258.66) * mm});
            skLineSegment(sketch, "E377", {"start": v(-11914.44, 4258.66) * mm, "end": v(-11916.25, 4265.56) * mm});
            skLineSegment(sketch, "E378", {"start": v(-11916.25, 4265.56) * mm, "end": v(-11918.4, 4273.16) * mm});
            skLineSegment(sketch, "E379", {"start": v(-11918.4, 4273.16) * mm, "end": v(-11920.9, 4281.44) * mm});
            skLineSegment(sketch, "E380", {"start": v(-11920.9, 4281.44) * mm, "end": v(-11923.78, 4290.38) * mm});
            skLineSegment(sketch, "E381", {"start": v(-11923.78, 4290.38) * mm, "end": v(-11927.07, 4300) * mm});
            skLineSegment(sketch, "E382", {"start": v(-11927.07, 4300) * mm, "end": v(-11930.79, 4310.25) * mm});
            skLineSegment(sketch, "E383", {"start": v(-11930.79, 4310.25) * mm, "end": v(-11934.97, 4321.14) * mm});
            skLineSegment(sketch, "E384", {"start": v(-11934.97, 4321.14) * mm, "end": v(-11939.64, 4332.65) * mm});
            skLineSegment(sketch, "E385", {"start": v(-11939.64, 4332.65) * mm, "end": v(-11944.8, 4344.77) * mm});
            skLineSegment(sketch, "E386", {"start": v(-11944.8, 4344.77) * mm, "end": v(-11950.51, 4357.48) * mm});
            skLineSegment(sketch, "E387", {"start": v(-11950.51, 4357.48) * mm, "end": v(-11956.77, 4370.77) * mm});
            skLineSegment(sketch, "E388", {"start": v(-11956.77, 4370.77) * mm, "end": v(-11963.6, 4384.62) * mm});
            skLineSegment(sketch, "E389", {"start": v(-11963.6, 4384.62) * mm, "end": v(-11971.04, 4399.01) * mm});
            skLineSegment(sketch, "E390", {"start": v(-11971.04, 4399.01) * mm, "end": v(-11979.1, 4413.93) * mm});
            skLineSegment(sketch, "E391", {"start": v(-11979.1, 4413.93) * mm, "end": v(-11987.8, 4429.35) * mm});
            skLineSegment(sketch, "E392", {"start": v(-11987.8, 4429.35) * mm, "end": v(-11997.16, 4445.27) * mm});
            skLineSegment(sketch, "E393", {"start": v(-11997.16, 4445.27) * mm, "end": v(-12007.2, 4461.65) * mm});
            skLineSegment(sketch, "E394", {"start": v(-12007.2, 4461.65) * mm, "end": v(-12017.96, 4478.48) * mm});
            skLineSegment(sketch, "E395", {"start": v(-12017.96, 4478.48) * mm, "end": v(-12029.44, 4495.73) * mm});
            skLineSegment(sketch, "E396", {"start": v(-12029.44, 4495.73) * mm, "end": v(-12041.67, 4513.4) * mm});
            skLineSegment(sketch, "E397", {"start": v(-12041.67, 4513.4) * mm, "end": v(-12054.66, 4531.45) * mm});
            skLineSegment(sketch, "E398", {"start": v(-12054.66, 4531.45) * mm, "end": v(-12068.43, 4549.86) * mm});
            skLineSegment(sketch, "E399", {"start": v(-12068.43, 4549.86) * mm, "end": v(-12083, 4568.62) * mm});
            skLineSegment(sketch, "E400", {"start": v(-12083, 4568.62) * mm, "end": v(-12098.39, 4587.69) * mm});
            skLineSegment(sketch, "E401", {"start": v(-12098.39, 4587.69) * mm, "end": v(-12114.6, 4607.05) * mm});
            skLineSegment(sketch, "E402", {"start": v(-12114.6, 4607.05) * mm, "end": v(-12131.68, 4626.68) * mm});
            skLineSegment(sketch, "E403", {"start": v(-12131.68, 4626.68) * mm, "end": v(-12147.35, 4632.51) * mm});
            skLineSegment(sketch, "E404", {"start": v(-12147.35, 4632.51) * mm, "end": v(-12282.86, 4607.11) * mm});
            skLineSegment(sketch, "E405", {"start": v(-12282.86, 4607.11) * mm, "end": v(-12295.36, 4596) * mm});
            skLineSegment(sketch, "E406", {"start": v(-12295.36, 4596) * mm, "end": v(-12304.16, 4571.52) * mm});
            skLineSegment(sketch, "E407", {"start": v(-12304.16, 4571.52) * mm, "end": v(-12312.26, 4547.6) * mm});
            skLineSegment(sketch, "E408", {"start": v(-12312.26, 4547.6) * mm, "end": v(-12319.7, 4524.25) * mm});
            skLineSegment(sketch, "E409", {"start": v(-12319.7, 4524.25) * mm, "end": v(-12326.49, 4501.5) * mm});
            skLineSegment(sketch, "E410", {"start": v(-12326.49, 4501.5) * mm, "end": v(-12332.66, 4479.34) * mm});
            skLineSegment(sketch, "E411", {"start": v(-12332.66, 4479.34) * mm, "end": v(-12338.23, 4457.81) * mm});
            skLineSegment(sketch, "E412", {"start": v(-12338.23, 4457.81) * mm, "end": v(-12343.22, 4436.92) * mm});
            skLineSegment(sketch, "E413", {"start": v(-12343.22, 4436.92) * mm, "end": v(-12347.68, 4416.67) * mm});
            skLineSegment(sketch, "E414", {"start": v(-12347.68, 4416.67) * mm, "end": v(-12351.6, 4397.09) * mm});
            skLineSegment(sketch, "E415", {"start": v(-12351.6, 4397.09) * mm, "end": v(-12355.04, 4378.18) * mm});
            skLineSegment(sketch, "E416", {"start": v(-12355.04, 4378.18) * mm, "end": v(-12358, 4359.96) * mm});
            skLineSegment(sketch, "E417", {"start": v(-12358, 4359.96) * mm, "end": v(-12360.53, 4342.43) * mm});
            skLineSegment(sketch, "E418", {"start": v(-12360.53, 4342.43) * mm, "end": v(-12362.64, 4325.6) * mm});
            skLineSegment(sketch, "E419", {"start": v(-12362.64, 4325.6) * mm, "end": v(-12364.36, 4309.5) * mm});
            skLineSegment(sketch, "E420", {"start": v(-12364.36, 4309.5) * mm, "end": v(-12365.71, 4294.12) * mm});
            skLineSegment(sketch, "E421", {"start": v(-12365.71, 4294.12) * mm, "end": v(-12366.73, 4279.47) * mm});
            skLineSegment(sketch, "E422", {"start": v(-12366.73, 4279.47) * mm, "end": v(-12367.44, 4265.55) * mm});
            skLineSegment(sketch, "E423", {"start": v(-12367.44, 4265.55) * mm, "end": v(-12367.87, 4252.38) * mm});
            skLineSegment(sketch, "E424", {"start": v(-12367.87, 4252.38) * mm, "end": v(-12368.05, 4239.96) * mm});
            skLineSegment(sketch, "E425", {"start": v(-12368.05, 4239.96) * mm, "end": v(-12368, 4228.3) * mm});
            skLineSegment(sketch, "E426", {"start": v(-12368, 4228.3) * mm, "end": v(-12367.76, 4217.39) * mm});
            skLineSegment(sketch, "E427", {"start": v(-12367.76, 4217.39) * mm, "end": v(-12367.35, 4207.24) * mm});
            skLineSegment(sketch, "E428", {"start": v(-12367.35, 4207.24) * mm, "end": v(-12366.8, 4197.86) * mm});
            skLineSegment(sketch, "E429", {"start": v(-12366.8, 4197.86) * mm, "end": v(-12366.13, 4189.23) * mm});
            skLineSegment(sketch, "E430", {"start": v(-12366.13, 4189.23) * mm, "end": v(-12365.37, 4181.38) * mm});
            skLineSegment(sketch, "E431", {"start": v(-12365.37, 4181.38) * mm, "end": v(-12364.56, 4174.29) * mm});
            skLineSegment(sketch, "E432", {"start": v(-12364.56, 4174.29) * mm, "end": v(-12363.72, 4167.96) * mm});
            skLineSegment(sketch, "E433", {"start": v(-12363.72, 4167.96) * mm, "end": v(-12362.87, 4162.4) * mm});
            skLineSegment(sketch, "E434", {"start": v(-12362.87, 4162.4) * mm, "end": v(-12362.05, 4157.6) * mm});
            skLineSegment(sketch, "E435", {"start": v(-12362.05, 4157.6) * mm, "end": v(-12361.29, 4153.56) * mm});
            skLineSegment(sketch, "E436", {"start": v(-12361.29, 4153.56) * mm, "end": v(-12360.6, 4150.27) * mm});
            skLineSegment(sketch, "E437", {"start": v(-12360.6, 4150.27) * mm, "end": v(-12360.02, 4147.73) * mm});
            skLineSegment(sketch, "E438", {"start": v(-12360.02, 4147.73) * mm, "end": v(-12359.57, 4145.93) * mm});
            skLineSegment(sketch, "E439", {"start": v(-12359.57, 4145.93) * mm, "end": v(-12359.3, 4144.87) * mm});
            skLineSegment(sketch, "E440", {"start": v(-12359.3, 4144.87) * mm, "end": v(-12326.15, 4032.94) * mm});
            skLineSegment(sketch, "E441", {"start": v(-12326.15, 4032.94) * mm, "end": v(-12575.87, 3941.6) * mm});
            skLineSegment(sketch, "E442", {"start": v(-12575.87, 3941.6) * mm, "end": v(-12622.77, 4048.5) * mm});
            skLineSegment(sketch, "E443", {"start": v(-12622.77, 4048.5) * mm, "end": v(-12623.23, 4049.5) * mm});
            skLineSegment(sketch, "E444", {"start": v(-12623.23, 4049.5) * mm, "end": v(-12624.05, 4051.16) * mm});
            skLineSegment(sketch, "E445", {"start": v(-12624.05, 4051.16) * mm, "end": v(-12625.25, 4053.47) * mm});
            skLineSegment(sketch, "E446", {"start": v(-12625.25, 4053.47) * mm, "end": v(-12626.85, 4056.43) * mm});
            skLineSegment(sketch, "E447", {"start": v(-12626.85, 4056.43) * mm, "end": v(-12628.87, 4060.01) * mm});
            skLineSegment(sketch, "E448", {"start": v(-12628.87, 4060.01) * mm, "end": v(-12631.34, 4064.2) * mm});
            skLineSegment(sketch, "E449", {"start": v(-12631.34, 4064.2) * mm, "end": v(-12634.28, 4069) * mm});
            skLineSegment(sketch, "E450", {"start": v(-12634.28, 4069) * mm, "end": v(-12637.72, 4074.38) * mm});
            skLineSegment(sketch, "E451", {"start": v(-12637.72, 4074.38) * mm, "end": v(-12641.67, 4080.32) * mm});
            skLineSegment(sketch, "E452", {"start": v(-12641.67, 4080.32) * mm, "end": v(-12646.17, 4086.8) * mm});
            skLineSegment(sketch, "E453", {"start": v(-12646.17, 4086.8) * mm, "end": v(-12651.22, 4093.83) * mm});
            skLineSegment(sketch, "E454", {"start": v(-12651.22, 4093.83) * mm, "end": v(-12656.85, 4101.36) * mm});
            skLineSegment(sketch, "E455", {"start": v(-12656.85, 4101.36) * mm, "end": v(-12663.08, 4109.38) * mm});
            skLineSegment(sketch, "E456", {"start": v(-12663.08, 4109.38) * mm, "end": v(-12669.93, 4117.87) * mm});
            skLineSegment(sketch, "E457", {"start": v(-12669.93, 4117.87) * mm, "end": v(-12677.42, 4126.81) * mm});
            skLineSegment(sketch, "E458", {"start": v(-12677.42, 4126.81) * mm, "end": v(-12685.57, 4136.18) * mm});
            skLineSegment(sketch, "E459", {"start": v(-12685.57, 4136.18) * mm, "end": v(-12694.4, 4145.97) * mm});
            skLineSegment(sketch, "E460", {"start": v(-12694.4, 4145.97) * mm, "end": v(-12703.92, 4156.14) * mm});
            skLineSegment(sketch, "E461", {"start": v(-12703.92, 4156.14) * mm, "end": v(-12714.15, 4166.68) * mm});
            skLineSegment(sketch, "E462", {"start": v(-12714.15, 4166.68) * mm, "end": v(-12725.11, 4177.55) * mm});
            skLineSegment(sketch, "E463", {"start": v(-12725.11, 4177.55) * mm, "end": v(-12736.82, 4188.75) * mm});
            skLineSegment(sketch, "E464", {"start": v(-12736.82, 4188.75) * mm, "end": v(-12749.28, 4200.24) * mm});
            skLineSegment(sketch, "E465", {"start": v(-12749.28, 4200.24) * mm, "end": v(-12762.52, 4212) * mm});
            skLineSegment(sketch, "E466", {"start": v(-12762.52, 4212) * mm, "end": v(-12776.54, 4224.02) * mm});
            skLineSegment(sketch, "E467", {"start": v(-12776.54, 4224.02) * mm, "end": v(-12791.37, 4236.25) * mm});
            skLineSegment(sketch, "E468", {"start": v(-12791.37, 4236.25) * mm, "end": v(-12807, 4248.67) * mm});
            skLineSegment(sketch, "E469", {"start": v(-12807, 4248.67) * mm, "end": v(-12823.47, 4261.27) * mm});
            skLineSegment(sketch, "E470", {"start": v(-12823.47, 4261.27) * mm, "end": v(-12840.77, 4274) * mm});
            skLineSegment(sketch, "E471", {"start": v(-12840.77, 4274) * mm, "end": v(-12858.91, 4286.86) * mm});
            skLineSegment(sketch, "E472", {"start": v(-12858.91, 4286.86) * mm, "end": v(-12877.92, 4299.8) * mm});
            skLineSegment(sketch, "E473", {"start": v(-12877.92, 4299.8) * mm, "end": v(-12897.79, 4312.81) * mm});
            skLineSegment(sketch, "E474", {"start": v(-12897.79, 4312.81) * mm, "end": v(-12918.53, 4325.85) * mm});
            skLineSegment(sketch, "E475", {"start": v(-12918.53, 4325.85) * mm, "end": v(-12940.16, 4338.9) * mm});
            skLineSegment(sketch, "E476", {"start": v(-12940.16, 4338.9) * mm, "end": v(-12962.68, 4351.93) * mm});
            skLineSegment(sketch, "E477", {"start": v(-12962.68, 4351.93) * mm, "end": v(-12979.4, 4352.35) * mm});
            skLineSegment(sketch, "E478", {"start": v(-12979.4, 4352.35) * mm, "end": v(-13099.32, 4284.33) * mm});
            skLineSegment(sketch, "E479", {"start": v(-13099.32, 4284.33) * mm, "end": v(-13107.53, 4269.76) * mm});
            skLineSegment(sketch, "E480", {"start": v(-13107.53, 4269.76) * mm, "end": v(-13107.9, 4243.75) * mm});
            skLineSegment(sketch, "E481", {"start": v(-13107.9, 4243.75) * mm, "end": v(-13107.8, 4218.5) * mm});
            skLineSegment(sketch, "E482", {"start": v(-13107.8, 4218.5) * mm, "end": v(-13107.25, 4194) * mm});
            skLineSegment(sketch, "E483", {"start": v(-13107.25, 4194) * mm, "end": v(-13106.29, 4170.26) * mm});
            skLineSegment(sketch, "E484", {"start": v(-13106.29, 4170.26) * mm, "end": v(-13104.93, 4147.3) * mm});
            skLineSegment(sketch, "E485", {"start": v(-13104.93, 4147.3) * mm, "end": v(-13103.2, 4125.14) * mm});
            skLineSegment(sketch, "E486", {"start": v(-13103.2, 4125.14) * mm, "end": v(-13101.15, 4103.75) * mm});
            skLineSegment(sketch, "E487", {"start": v(-13101.15, 4103.75) * mm, "end": v(-13098.79, 4083.16) * mm});
            skLineSegment(sketch, "E488", {"start": v(-13098.79, 4083.16) * mm, "end": v(-13096.15, 4063.36) * mm});
            skLineSegment(sketch, "E489", {"start": v(-13096.15, 4063.36) * mm, "end": v(-13093.25, 4044.36) * mm});
            skLineSegment(sketch, "E490", {"start": v(-13093.25, 4044.36) * mm, "end": v(-13090.14, 4026.16) * mm});
            skLineSegment(sketch, "E491", {"start": v(-13090.14, 4026.16) * mm, "end": v(-13086.84, 4008.77) * mm});
            skLineSegment(sketch, "E492", {"start": v(-13086.84, 4008.77) * mm, "end": v(-13083.37, 3992.17) * mm});
            skLineSegment(sketch, "E493", {"start": v(-13083.37, 3992.17) * mm, "end": v(-13079.76, 3976.38) * mm});
            skLineSegment(sketch, "E494", {"start": v(-13079.76, 3976.38) * mm, "end": v(-13076.05, 3961.4) * mm});
            skLineSegment(sketch, "E495", {"start": v(-13076.05, 3961.4) * mm, "end": v(-13072.26, 3947.2) * mm});
            skLineSegment(sketch, "E496", {"start": v(-13072.26, 3947.2) * mm, "end": v(-13068.41, 3933.81) * mm});
            skLineSegment(sketch, "E497", {"start": v(-13068.41, 3933.81) * mm, "end": v(-13064.54, 3921.21) * mm});
            skLineSegment(sketch, "E498", {"start": v(-13064.54, 3921.21) * mm, "end": v(-13060.68, 3909.4) * mm});
            skLineSegment(sketch, "E499", {"start": v(-13060.68, 3909.4) * mm, "end": v(-13056.85, 3898.39) * mm});
            skLineSegment(sketch, "E500", {"start": v(-13056.85, 3898.39) * mm, "end": v(-13053.08, 3888.15) * mm});
            skLineSegment(sketch, "E501", {"start": v(-13053.08, 3888.15) * mm, "end": v(-13049.4, 3878.68) * mm});
            skLineSegment(sketch, "E502", {"start": v(-13049.4, 3878.68) * mm, "end": v(-13045.82, 3869.99) * mm});
            skLineSegment(sketch, "E503", {"start": v(-13045.82, 3869.99) * mm, "end": v(-13042.39, 3862.05) * mm});
            skLineSegment(sketch, "E504", {"start": v(-13042.39, 3862.05) * mm, "end": v(-13039.12, 3854.87) * mm});
            skLineSegment(sketch, "E505", {"start": v(-13039.12, 3854.87) * mm, "end": v(-13036.05, 3848.43) * mm});
            skLineSegment(sketch, "E506", {"start": v(-13036.05, 3848.43) * mm, "end": v(-13033.2, 3842.72) * mm});
            skLineSegment(sketch, "E507", {"start": v(-13033.2, 3842.72) * mm, "end": v(-13030.6, 3837.73) * mm});
            skLineSegment(sketch, "E508", {"start": v(-13030.6, 3837.73) * mm, "end": v(-13028.26, 3833.46) * mm});
            skLineSegment(sketch, "E509", {"start": v(-13028.26, 3833.46) * mm, "end": v(-13026.22, 3829.88) * mm});
            skLineSegment(sketch, "E510", {"start": v(-13026.22, 3829.88) * mm, "end": v(-13024.5, 3827) * mm});
            skLineSegment(sketch, "E511", {"start": v(-13024.5, 3827) * mm, "end": v(-13023.13, 3824.78) * mm});
            skLineSegment(sketch, "E512", {"start": v(-13023.13, 3824.78) * mm, "end": v(-13022.13, 3823.23) * mm});
            skLineSegment(sketch, "E513", {"start": v(-13022.13, 3823.23) * mm, "end": v(-13021.52, 3822.32) * mm});
            skLineSegment(sketch, "E514", {"start": v(-13021.52, 3822.32) * mm, "end": v(-12953.83, 3727.21) * mm});
            skLineSegment(sketch, "E515", {"start": v(-12953.83, 3727.21) * mm, "end": v(-13160.36, 3559.74) * mm});
            skLineSegment(sketch, "E516", {"start": v(-13160.36, 3559.74) * mm, "end": v(-13239.43, 3645.62) * mm});
            skLineSegment(sketch, "E517", {"start": v(-13239.43, 3645.62) * mm, "end": v(-13240.2, 3646.4) * mm});
            skLineSegment(sketch, "E518", {"start": v(-13240.2, 3646.4) * mm, "end": v(-13241.5, 3647.7) * mm});
            skLineSegment(sketch, "E519", {"start": v(-13241.5, 3647.7) * mm, "end": v(-13243.39, 3649.5) * mm});
            skLineSegment(sketch, "E520", {"start": v(-13243.39, 3649.5) * mm, "end": v(-13245.86, 3651.79) * mm});
            skLineSegment(sketch, "E521", {"start": v(-13245.86, 3651.79) * mm, "end": v(-13248.93, 3654.52) * mm});
            skLineSegment(sketch, "E522", {"start": v(-13248.93, 3654.52) * mm, "end": v(-13252.63, 3657.69) * mm});
            skLineSegment(sketch, "E523", {"start": v(-13252.63, 3657.69) * mm, "end": v(-13256.97, 3661.27) * mm});
            skLineSegment(sketch, "E524", {"start": v(-13256.97, 3661.27) * mm, "end": v(-13261.97, 3665.24) * mm});
            skLineSegment(sketch, "E525", {"start": v(-13261.97, 3665.24) * mm, "end": v(-13267.64, 3669.57) * mm});
            skLineSegment(sketch, "E526", {"start": v(-13267.64, 3669.57) * mm, "end": v(-13274, 3674.25) * mm});
            skLineSegment(sketch, "E527", {"start": v(-13274, 3674.25) * mm, "end": v(-13281.05, 3679.25) * mm});
            skLineSegment(sketch, "E528", {"start": v(-13281.05, 3679.25) * mm, "end": v(-13288.82, 3684.54) * mm});
            skLineSegment(sketch, "E529", {"start": v(-13288.82, 3684.54) * mm, "end": v(-13297.32, 3690.1) * mm});
            skLineSegment(sketch, "E530", {"start": v(-13297.32, 3690.1) * mm, "end": v(-13306.56, 3695.9) * mm});
            skLineSegment(sketch, "E531", {"start": v(-13306.56, 3695.9) * mm, "end": v(-13316.55, 3701.93) * mm});
            skLineSegment(sketch, "E532", {"start": v(-13316.55, 3701.93) * mm, "end": v(-13327.3, 3708.15) * mm});
            skLineSegment(sketch, "E533", {"start": v(-13327.3, 3708.15) * mm, "end": v(-13338.83, 3714.54) * mm});
            skLineSegment(sketch, "E534", {"start": v(-13338.83, 3714.54) * mm, "end": v(-13351.13, 3721.07) * mm});
            skLineSegment(sketch, "E535", {"start": v(-13351.13, 3721.07) * mm, "end": v(-13364.23, 3727.71) * mm});
            skLineSegment(sketch, "E536", {"start": v(-13364.23, 3727.71) * mm, "end": v(-13378.13, 3734.44) * mm});
            skLineSegment(sketch, "E537", {"start": v(-13378.13, 3734.44) * mm, "end": v(-13392.84, 3741.23) * mm});
            skLineSegment(sketch, "E538", {"start": v(-13392.84, 3741.23) * mm, "end": v(-13408.35, 3748.06) * mm});
            skLineSegment(sketch, "E539", {"start": v(-13408.35, 3748.06) * mm, "end": v(-13424.7, 3754.89) * mm});
            skLineSegment(sketch, "E540", {"start": v(-13424.7, 3754.89) * mm, "end": v(-13441.86, 3761.7) * mm});
            skLineSegment(sketch, "E541", {"start": v(-13441.86, 3761.7) * mm, "end": v(-13459.85, 3768.44) * mm});
            skLineSegment(sketch, "E542", {"start": v(-13459.85, 3768.44) * mm, "end": v(-13478.67, 3775.12) * mm});
            skLineSegment(sketch, "E543", {"start": v(-13478.67, 3775.12) * mm, "end": v(-13498.34, 3781.69) * mm});
            skLineSegment(sketch, "E544", {"start": v(-13498.34, 3781.69) * mm, "end": v(-13518.83, 3788.12) * mm});
            skLineSegment(sketch, "E545", {"start": v(-13518.83, 3788.12) * mm, "end": v(-13540.17, 3794.38) * mm});
            skLineSegment(sketch, "E546", {"start": v(-13540.17, 3794.38) * mm, "end": v(-13562.35, 3800.45) * mm});
            skLineSegment(sketch, "E547", {"start": v(-13562.35, 3800.45) * mm, "end": v(-13585.37, 3806.3) * mm});
            skLineSegment(sketch, "E548", {"start": v(-13585.37, 3806.3) * mm, "end": v(-13609.22, 3811.9) * mm});
            skLineSegment(sketch, "E549", {"start": v(-13609.22, 3811.9) * mm, "end": v(-13633.91, 3817.22) * mm});
            skLineSegment(sketch, "E550", {"start": v(-13633.91, 3817.22) * mm, "end": v(-13659.44, 3822.23) * mm});
            skLineSegment(sketch, "E551", {"start": v(-13659.44, 3822.23) * mm, "end": v(-13675.4, 3817.2) * mm});
            skLineSegment(sketch, "E552", {"start": v(-13675.4, 3817.2) * mm, "end": v(-13766.73, 3713.93) * mm});
            skLineSegment(sketch, "E553", {"start": v(-13766.73, 3713.93) * mm, "end": v(-13769.77, 3697.48) * mm});
            skLineSegment(sketch, "E554", {"start": v(-13769.77, 3697.48) * mm, "end": v(-13761.67, 3672.76) * mm});
            skLineSegment(sketch, "E555", {"start": v(-13761.67, 3672.76) * mm, "end": v(-13753.38, 3648.9) * mm});
            skLineSegment(sketch, "E556", {"start": v(-13753.38, 3648.9) * mm, "end": v(-13744.9, 3625.91) * mm});
            skLineSegment(sketch, "E557", {"start": v(-13744.9, 3625.91) * mm, "end": v(-13736.28, 3603.78) * mm});
            skLineSegment(sketch, "E558", {"start": v(-13736.28, 3603.78) * mm, "end": v(-13727.54, 3582.51) * mm});
            skLineSegment(sketch, "E559", {"start": v(-13727.54, 3582.51) * mm, "end": v(-13718.72, 3562.1) * mm});
            skLineSegment(sketch, "E560", {"start": v(-13718.72, 3562.1) * mm, "end": v(-13709.83, 3542.54) * mm});
            skLineSegment(sketch, "E561", {"start": v(-13709.83, 3542.54) * mm, "end": v(-13700.9, 3523.83) * mm});
            skLineSegment(sketch, "E562", {"start": v(-13700.9, 3523.83) * mm, "end": v(-13691.98, 3505.97) * mm});
            skLineSegment(sketch, "E563", {"start": v(-13691.98, 3505.97) * mm, "end": v(-13683.08, 3488.93) * mm});
            skLineSegment(sketch, "E564", {"start": v(-13683.08, 3488.93) * mm, "end": v(-13674.22, 3472.73) * mm});
            skLineSegment(sketch, "E565", {"start": v(-13674.22, 3472.73) * mm, "end": v(-13665.45, 3457.35) * mm});
            skLineSegment(sketch, "E566", {"start": v(-13665.45, 3457.35) * mm, "end": v(-13656.78, 3442.78) * mm});
            skLineSegment(sketch, "E567", {"start": v(-13656.78, 3442.78) * mm, "end": v(-13648.24, 3429.02) * mm});
            skLineSegment(sketch, "E568", {"start": v(-13648.24, 3429.02) * mm, "end": v(-13639.86, 3416.04) * mm});
            skLineSegment(sketch, "E569", {"start": v(-13639.86, 3416.04) * mm, "end": v(-13631.67, 3403.86) * mm});
            skLineSegment(sketch, "E570", {"start": v(-13631.67, 3403.86) * mm, "end": v(-13623.69, 3392.44) * mm});
            skLineSegment(sketch, "E571", {"start": v(-13623.69, 3392.44) * mm, "end": v(-13615.94, 3381.78) * mm});
            skLineSegment(sketch, "E572", {"start": v(-13615.94, 3381.78) * mm, "end": v(-13608.45, 3371.87) * mm});
            skLineSegment(sketch, "E573", {"start": v(-13608.45, 3371.87) * mm, "end": v(-13601.25, 3362.69) * mm});
            skLineSegment(sketch, "E574", {"start": v(-13601.25, 3362.69) * mm, "end": v(-13594.35, 3354.23) * mm});
            skLineSegment(sketch, "E575", {"start": v(-13594.35, 3354.23) * mm, "end": v(-13587.8, 3346.48) * mm});
            skLineSegment(sketch, "E576", {"start": v(-13587.8, 3346.48) * mm, "end": v(-13581.6, 3339.41) * mm});
            skLineSegment(sketch, "E577", {"start": v(-13581.6, 3339.41) * mm, "end": v(-13575.77, 3333.02) * mm});
            skLineSegment(sketch, "E578", {"start": v(-13575.77, 3333.02) * mm, "end": v(-13570.35, 3327.28) * mm});
            skLineSegment(sketch, "E579", {"start": v(-13570.35, 3327.28) * mm, "end": v(-13565.35, 3322.19) * mm});
            skLineSegment(sketch, "E580", {"start": v(-13565.35, 3322.19) * mm, "end": v(-13560.8, 3317.71) * mm});
            skLineSegment(sketch, "E581", {"start": v(-13560.8, 3317.71) * mm, "end": v(-13556.72, 3313.85) * mm});
            skLineSegment(sketch, "E582", {"start": v(-13556.72, 3313.85) * mm, "end": v(-13553.12, 3310.56) * mm});
            skLineSegment(sketch, "E583", {"start": v(-13553.12, 3310.56) * mm, "end": v(-13550.04, 3307.84) * mm});
            skLineSegment(sketch, "E584", {"start": v(-13550.04, 3307.84) * mm, "end": v(-13547.47, 3305.67) * mm});
            skLineSegment(sketch, "E585", {"start": v(-13547.47, 3305.67) * mm, "end": v(-13545.46, 3304.02) * mm});
            skLineSegment(sketch, "E586", {"start": v(-13545.46, 3304.02) * mm, "end": v(-13544, 3302.87) * mm});
            skLineSegment(sketch, "E587", {"start": v(-13544, 3302.87) * mm, "end": v(-13543.13, 3302.21) * mm});
            skLineSegment(sketch, "E588", {"start": v(-13543.13, 3302.21) * mm, "end": v(-13448.23, 3234.24) * mm});
            skLineSegment(sketch, "E589", {"start": v(-13448.23, 3234.24) * mm, "end": v(-13589.2, 3008.78) * mm});
            skLineSegment(sketch, "E590", {"start": v(-13589.2, 3008.78) * mm, "end": v(-13691.86, 3064.34) * mm});
            skLineSegment(sketch, "E591", {"start": v(-13691.86, 3064.34) * mm, "end": v(-13692.83, 3064.83) * mm});
            skLineSegment(sketch, "E592", {"start": v(-13692.83, 3064.83) * mm, "end": v(-13694.5, 3065.63) * mm});
            skLineSegment(sketch, "E593", {"start": v(-13694.5, 3065.63) * mm, "end": v(-13696.87, 3066.73) * mm});
            skLineSegment(sketch, "E594", {"start": v(-13696.87, 3066.73) * mm, "end": v(-13699.94, 3068.08) * mm});
            skLineSegment(sketch, "E595", {"start": v(-13699.94, 3068.08) * mm, "end": v(-13703.74, 3069.66) * mm});
            skLineSegment(sketch, "E596", {"start": v(-13703.74, 3069.66) * mm, "end": v(-13708.27, 3071.46) * mm});
            skLineSegment(sketch, "E597", {"start": v(-13708.27, 3071.46) * mm, "end": v(-13713.53, 3073.44) * mm});
            skLineSegment(sketch, "E598", {"start": v(-13713.53, 3073.44) * mm, "end": v(-13719.55, 3075.57) * mm});
            skLineSegment(sketch, "E599", {"start": v(-13719.55, 3075.57) * mm, "end": v(-13726.32, 3077.83) * mm});
            skLineSegment(sketch, "E600", {"start": v(-13726.32, 3077.83) * mm, "end": v(-13733.85, 3080.19) * mm});
            skLineSegment(sketch, "E601", {"start": v(-13733.85, 3080.19) * mm, "end": v(-13742.14, 3082.62) * mm});
            skLineSegment(sketch, "E602", {"start": v(-13742.14, 3082.62) * mm, "end": v(-13751.21, 3085.1) * mm});
            skLineSegment(sketch, "E603", {"start": v(-13751.21, 3085.1) * mm, "end": v(-13761.05, 3087.6) * mm});
            skLineSegment(sketch, "E604", {"start": v(-13761.05, 3087.6) * mm, "end": v(-13771.68, 3090.1) * mm});
            skLineSegment(sketch, "E605", {"start": v(-13771.68, 3090.1) * mm, "end": v(-13783.08, 3092.56) * mm});
            skLineSegment(sketch, "E606", {"start": v(-13783.08, 3092.56) * mm, "end": v(-13795.27, 3094.95) * mm});
            skLineSegment(sketch, "E607", {"start": v(-13795.27, 3094.95) * mm, "end": v(-13808.25, 3097.25) * mm});
            skLineSegment(sketch, "E608", {"start": v(-13808.25, 3097.25) * mm, "end": v(-13822, 3099.42) * mm});
            skLineSegment(sketch, "E609", {"start": v(-13822, 3099.42) * mm, "end": v(-13836.56, 3101.45) * mm});
            skLineSegment(sketch, "E610", {"start": v(-13836.56, 3101.45) * mm, "end": v(-13851.89, 3103.3) * mm});
            skLineSegment(sketch, "E611", {"start": v(-13851.89, 3103.3) * mm, "end": v(-13868, 3104.95) * mm});
            skLineSegment(sketch, "E612", {"start": v(-13868, 3104.95) * mm, "end": v(-13884.9, 3106.37) * mm});
            skLineSegment(sketch, "E613", {"start": v(-13884.9, 3106.37) * mm, "end": v(-13902.57, 3107.52) * mm});
            skLineSegment(sketch, "E614", {"start": v(-13902.57, 3107.52) * mm, "end": v(-13921, 3108.39) * mm});
            skLineSegment(sketch, "E615", {"start": v(-13921, 3108.39) * mm, "end": v(-13940.22, 3108.93) * mm});
            skLineSegment(sketch, "E616", {"start": v(-13940.22, 3108.93) * mm, "end": v(-13960.2, 3109.13) * mm});
            skLineSegment(sketch, "E617", {"start": v(-13960.2, 3109.13) * mm, "end": v(-13980.92, 3108.96) * mm});
            skLineSegment(sketch, "E618", {"start": v(-13980.92, 3108.96) * mm, "end": v(-14002.4, 3108.39) * mm});
            skLineSegment(sketch, "E619", {"start": v(-14002.4, 3108.39) * mm, "end": v(-14024.6, 3107.38) * mm});
            skLineSegment(sketch, "E620", {"start": v(-14024.6, 3107.38) * mm, "end": v(-14047.56, 3105.93) * mm});
            skLineSegment(sketch, "E621", {"start": v(-14047.56, 3105.93) * mm, "end": v(-14071.23, 3103.99) * mm});
            skLineSegment(sketch, "E622", {"start": v(-14071.23, 3103.99) * mm, "end": v(-14095.6, 3101.54) * mm});
            skLineSegment(sketch, "E623", {"start": v(-14095.6, 3101.54) * mm, "end": v(-14120.7, 3098.55) * mm});
            skLineSegment(sketch, "E624", {"start": v(-14120.7, 3098.55) * mm, "end": v(-14146.46, 3095) * mm});
            skLineSegment(sketch, "E625", {"start": v(-14146.46, 3095) * mm, "end": v(-14159.91, 3085.06) * mm});
            skLineSegment(sketch, "E626", {"start": v(-14159.91, 3085.06) * mm, "end": v(-14212.77, 2957.73) * mm});
            skLineSegment(sketch, "E627", {"start": v(-14212.77, 2957.73) * mm, "end": v(-14210.3, 2941.19) * mm});
            skLineSegment(sketch, "E628", {"start": v(-14210.3, 2941.19) * mm, "end": v(-14194.62, 2920.43) * mm});
            skLineSegment(sketch, "E629", {"start": v(-14194.62, 2920.43) * mm, "end": v(-14179.03, 2900.56) * mm});
            skLineSegment(sketch, "E630", {"start": v(-14179.03, 2900.56) * mm, "end": v(-14163.55, 2881.56) * mm});
            skLineSegment(sketch, "E631", {"start": v(-14163.55, 2881.56) * mm, "end": v(-14148.2, 2863.43) * mm});
            skLineSegment(sketch, "E632", {"start": v(-14148.2, 2863.43) * mm, "end": v(-14133.04, 2846.15) * mm});
            skLineSegment(sketch, "E633", {"start": v(-14133.04, 2846.15) * mm, "end": v(-14118.06, 2829.72) * mm});
            skLineSegment(sketch, "E634", {"start": v(-14118.06, 2829.72) * mm, "end": v(-14103.3, 2814.1) * mm});
            skLineSegment(sketch, "E635", {"start": v(-14103.3, 2814.1) * mm, "end": v(-14088.79, 2799.3) * mm});
            skLineSegment(sketch, "E636", {"start": v(-14088.79, 2799.3) * mm, "end": v(-14074.54, 2785.3) * mm});
            skLineSegment(sketch, "E637", {"start": v(-14074.54, 2785.3) * mm, "end": v(-14060.6, 2772.08) * mm});
            skLineSegment(sketch, "E638", {"start": v(-14060.6, 2772.08) * mm, "end": v(-14046.96, 2759.63) * mm});
            skLineSegment(sketch, "E639", {"start": v(-14046.96, 2759.63) * mm, "end": v(-14033.67, 2747.94) * mm});
            skLineSegment(sketch, "E640", {"start": v(-14033.67, 2747.94) * mm, "end": v(-14020.74, 2736.97) * mm});
            skLineSegment(sketch, "E641", {"start": v(-14020.74, 2736.97) * mm, "end": v(-14008.2, 2726.72) * mm});
            skLineSegment(sketch, "E642", {"start": v(-14008.2, 2726.72) * mm, "end": v(-13996.05, 2717.18) * mm});
            skLineSegment(sketch, "E643", {"start": v(-13996.05, 2717.18) * mm, "end": v(-13984.35, 2708.3) * mm});
            skLineSegment(sketch, "E644", {"start": v(-13984.35, 2708.3) * mm, "end": v(-13973.09, 2700.1) * mm});
            skLineSegment(sketch, "E645", {"start": v(-13973.09, 2700.1) * mm, "end": v(-13962.3, 2692.54) * mm});
            skLineSegment(sketch, "E646", {"start": v(-13962.3, 2692.54) * mm, "end": v(-13952, 2685.6) * mm});
            skLineSegment(sketch, "E647", {"start": v(-13952, 2685.6) * mm, "end": v(-13942.2, 2679.25) * mm});
            skLineSegment(sketch, "E648", {"start": v(-13942.2, 2679.25) * mm, "end": v(-13932.94, 2673.49) * mm});
            skLineSegment(sketch, "E649", {"start": v(-13932.94, 2673.49) * mm, "end": v(-13924.22, 2668.28) * mm});
            skLineSegment(sketch, "E650", {"start": v(-13924.22, 2668.28) * mm, "end": v(-13916.06, 2663.62) * mm});
            skLineSegment(sketch, "E651", {"start": v(-13916.06, 2663.62) * mm, "end": v(-13908.47, 2659.46) * mm});
            skLineSegment(sketch, "E652", {"start": v(-13908.47, 2659.46) * mm, "end": v(-13901.49, 2655.8) * mm});
            skLineSegment(sketch, "E653", {"start": v(-13901.49, 2655.8) * mm, "end": v(-13895.1, 2652.6) * mm});
            skLineSegment(sketch, "E654", {"start": v(-13895.1, 2652.6) * mm, "end": v(-13889.35, 2649.84) * mm});
            skLineSegment(sketch, "E655", {"start": v(-13889.35, 2649.84) * mm, "end": v(-13884.23, 2647.51) * mm});
            skLineSegment(sketch, "E656", {"start": v(-13884.23, 2647.51) * mm, "end": v(-13879.76, 2645.57) * mm});
            skLineSegment(sketch, "E657", {"start": v(-13879.76, 2645.57) * mm, "end": v(-13875.96, 2644) * mm});
            skLineSegment(sketch, "E658", {"start": v(-13875.96, 2644) * mm, "end": v(-13872.83, 2642.78) * mm});
            skLineSegment(sketch, "E659", {"start": v(-13872.83, 2642.78) * mm, "end": v(-13870.39, 2641.87) * mm});
            skLineSegment(sketch, "E660", {"start": v(-13870.39, 2641.87) * mm, "end": v(-13868.64, 2641.26) * mm});
            skLineSegment(sketch, "E661", {"start": v(-13868.64, 2641.26) * mm, "end": v(-13867.6, 2640.92) * mm});
            skLineSegment(sketch, "E662", {"start": v(-13867.6, 2640.92) * mm, "end": v(-13755.77, 2607.45) * mm});
            skLineSegment(sketch, "E663", {"start": v(-13755.77, 2607.45) * mm, "end": v(-13815.89, 2348.43) * mm});
            skLineSegment(sketch, "E664", {"start": v(-13815.89, 2348.43) * mm, "end": v(-13931.03, 2367.64) * mm});
            skLineSegment(sketch, "E665", {"start": v(-13931.03, 2367.64) * mm, "end": v(-13932.12, 2367.8) * mm});
            skLineSegment(sketch, "E666", {"start": v(-13932.12, 2367.8) * mm, "end": v(-13933.95, 2368.01) * mm});
            skLineSegment(sketch, "E667", {"start": v(-13933.95, 2368.01) * mm, "end": v(-13936.54, 2368.28) * mm});
            skLineSegment(sketch, "E668", {"start": v(-13936.54, 2368.28) * mm, "end": v(-13939.9, 2368.56) * mm});
            skLineSegment(sketch, "E669", {"start": v(-13939.9, 2368.56) * mm, "end": v(-13944, 2368.82) * mm});
            skLineSegment(sketch, "E670", {"start": v(-13944, 2368.82) * mm, "end": v(-13948.87, 2369.05) * mm});
            skLineSegment(sketch, "E671", {"start": v(-13948.87, 2369.05) * mm, "end": v(-13954.49, 2369.2) * mm});
            skLineSegment(sketch, "E672", {"start": v(-13954.49, 2369.2) * mm, "end": v(-13960.87, 2369.27) * mm});
            skLineSegment(sketch, "E673", {"start": v(-13960.87, 2369.27) * mm, "end": v(-13968, 2369.21) * mm});
            skLineSegment(sketch, "E674", {"start": v(-13968, 2369.21) * mm, "end": v(-13975.9, 2369) * mm});
            skLineSegment(sketch, "E675", {"start": v(-13975.9, 2369) * mm, "end": v(-13984.53, 2368.61) * mm});
            skLineSegment(sketch, "E676", {"start": v(-13984.53, 2368.61) * mm, "end": v(-13993.91, 2368.01) * mm});
            skLineSegment(sketch, "E677", {"start": v(-13993.91, 2368.01) * mm, "end": v(-14004.04, 2367.18) * mm});
            skLineSegment(sketch, "E678", {"start": v(-14004.04, 2367.18) * mm, "end": v(-14014.9, 2366.1) * mm});
            skLineSegment(sketch, "E679", {"start": v(-14014.9, 2366.1) * mm, "end": v(-14026.48, 2364.71) * mm});
            skLineSegment(sketch, "E680", {"start": v(-14026.48, 2364.71) * mm, "end": v(-14038.78, 2363.02) * mm});
            skLineSegment(sketch, "E681", {"start": v(-14038.78, 2363.02) * mm, "end": v(-14051.8, 2360.98) * mm});
            skLineSegment(sketch, "E682", {"start": v(-14051.8, 2360.98) * mm, "end": v(-14065.53, 2358.57) * mm});
            skLineSegment(sketch, "E683", {"start": v(-14065.53, 2358.57) * mm, "end": v(-14079.94, 2355.77) * mm});
            skLineSegment(sketch, "E684", {"start": v(-14079.94, 2355.77) * mm, "end": v(-14095.04, 2352.54) * mm});
            skLineSegment(sketch, "E685", {"start": v(-14095.04, 2352.54) * mm, "end": v(-14110.82, 2348.87) * mm});
            skLineSegment(sketch, "E686", {"start": v(-14110.82, 2348.87) * mm, "end": v(-14127.26, 2344.72) * mm});
            skLineSegment(sketch, "E687", {"start": v(-14127.26, 2344.72) * mm, "end": v(-14144.34, 2340.07) * mm});
            skLineSegment(sketch, "E688", {"start": v(-14144.34, 2340.07) * mm, "end": v(-14162.07, 2334.9) * mm});
            skLineSegment(sketch, "E689", {"start": v(-14162.07, 2334.9) * mm, "end": v(-14180.41, 2329.18) * mm});
            skLineSegment(sketch, "E690", {"start": v(-14180.41, 2329.18) * mm, "end": v(-14199.37, 2322.88) * mm});
            skLineSegment(sketch, "E691", {"start": v(-14199.37, 2322.88) * mm, "end": v(-14218.92, 2315.99) * mm});
            skLineSegment(sketch, "E692", {"start": v(-14218.92, 2315.99) * mm, "end": v(-14239.04, 2308.47) * mm});
            skLineSegment(sketch, "E693", {"start": v(-14239.04, 2308.47) * mm, "end": v(-14259.73, 2300.31) * mm});
            skLineSegment(sketch, "E694", {"start": v(-14259.73, 2300.31) * mm, "end": v(-14280.96, 2291.48) * mm});
            skLineSegment(sketch, "E695", {"start": v(-14280.96, 2291.48) * mm, "end": v(-14302.72, 2281.96) * mm});
            skLineSegment(sketch, "E696", {"start": v(-14302.72, 2281.96) * mm, "end": v(-14324.99, 2271.73) * mm});
            skLineSegment(sketch, "E697", {"start": v(-14324.99, 2271.73) * mm, "end": v(-14347.74, 2260.76) * mm});
            skLineSegment(sketch, "E698", {"start": v(-14347.74, 2260.76) * mm, "end": v(-14370.96, 2249.03) * mm});
            skLineSegment(sketch, "E699", {"start": v(-14370.96, 2249.03) * mm, "end": v(-14380.46, 2235.27) * mm});
            skLineSegment(sketch, "E700", {"start": v(-14380.46, 2235.27) * mm, "end": v(-14389.1, 2097.67) * mm});
            skLineSegment(sketch, "E701", {"start": v(-14389.1, 2097.67) * mm, "end": v(-14381.4, 2082.83) * mm});
            skLineSegment(sketch, "E702", {"start": v(-14381.4, 2082.83) * mm, "end": v(-14359.83, 2068.29) * mm});
            skLineSegment(sketch, "E703", {"start": v(-14359.83, 2068.29) * mm, "end": v(-14338.62, 2054.56) * mm});
            skLineSegment(sketch, "E704", {"start": v(-14338.62, 2054.56) * mm, "end": v(-14317.82, 2041.62) * mm});
            skLineSegment(sketch, "E705", {"start": v(-14317.82, 2041.62) * mm, "end": v(-14297.42, 2029.45) * mm});
            skLineSegment(sketch, "E706", {"start": v(-14297.42, 2029.45) * mm, "end": v(-14277.46, 2018.03) * mm});
            skLineSegment(sketch, "E707", {"start": v(-14277.46, 2018.03) * mm, "end": v(-14257.96, 2007.34) * mm});
            skLineSegment(sketch, "E708", {"start": v(-14257.96, 2007.34) * mm, "end": v(-14238.93, 1997.37) * mm});
            skLineSegment(sketch, "E709", {"start": v(-14238.93, 1997.37) * mm, "end": v(-14220.4, 1988.09) * mm});
            skLineSegment(sketch, "E710", {"start": v(-14220.4, 1988.09) * mm, "end": v(-14202.38, 1979.47) * mm});
            skLineSegment(sketch, "E711", {"start": v(-14202.38, 1979.47) * mm, "end": v(-14184.9, 1971.5) * mm});
            skLineSegment(sketch, "E712", {"start": v(-14184.9, 1971.5) * mm, "end": v(-14167.95, 1964.15) * mm});
            skLineSegment(sketch, "E713", {"start": v(-14167.95, 1964.15) * mm, "end": v(-14151.58, 1957.4) * mm});
            skLineSegment(sketch, "E714", {"start": v(-14151.58, 1957.4) * mm, "end": v(-14135.8, 1951.23) * mm});
            skLineSegment(sketch, "E715", {"start": v(-14135.8, 1951.23) * mm, "end": v(-14120.6, 1945.6) * mm});
            skLineSegment(sketch, "E716", {"start": v(-14120.6, 1945.6) * mm, "end": v(-14106.02, 1940.52) * mm});
            skLineSegment(sketch, "E717", {"start": v(-14106.02, 1940.52) * mm, "end": v(-14092.07, 1935.93) * mm});
            skLineSegment(sketch, "E718", {"start": v(-14092.07, 1935.93) * mm, "end": v(-14078.76, 1931.83) * mm});
            skLineSegment(sketch, "E719", {"start": v(-14078.76, 1931.83) * mm, "end": v(-14066.1, 1928.18) * mm});
            skLineSegment(sketch, "E720", {"start": v(-14066.1, 1928.18) * mm, "end": v(-14054.1, 1924.95) * mm});
            skLineSegment(sketch, "E721", {"start": v(-14054.1, 1924.95) * mm, "end": v(-14042.78, 1922.13) * mm});
            skLineSegment(sketch, "E722", {"start": v(-14042.78, 1922.13) * mm, "end": v(-14032.14, 1919.7) * mm});
            skLineSegment(sketch, "E723", {"start": v(-14032.14, 1919.7) * mm, "end": v(-14022.2, 1917.6) * mm});
            skLineSegment(sketch, "E724", {"start": v(-14022.2, 1917.6) * mm, "end": v(-14012.97, 1915.84) * mm});
            skLineSegment(sketch, "E725", {"start": v(-14012.97, 1915.84) * mm, "end": v(-14004.45, 1914.37) * mm});
            skLineSegment(sketch, "E726", {"start": v(-14004.45, 1914.37) * mm, "end": v(-13996.65, 1913.17) * mm});
            skLineSegment(sketch, "E727", {"start": v(-13996.65, 1913.17) * mm, "end": v(-13989.58, 1912.22) * mm});
            skLineSegment(sketch, "E728", {"start": v(-13989.58, 1912.22) * mm, "end": v(-13983.24, 1911.48) * mm});
            skLineSegment(sketch, "E729", {"start": v(-13983.24, 1911.48) * mm, "end": v(-13977.64, 1910.94) * mm});
            skLineSegment(sketch, "E730", {"start": v(-13977.64, 1910.94) * mm, "end": v(-13972.78, 1910.55) * mm});
            skLineSegment(sketch, "E731", {"start": v(-13972.78, 1910.55) * mm, "end": v(-13968.68, 1910.3) * mm});
            skLineSegment(sketch, "E732", {"start": v(-13968.68, 1910.3) * mm, "end": v(-13965.32, 1910.16) * mm});
            skLineSegment(sketch, "E733", {"start": v(-13965.32, 1910.16) * mm, "end": v(-13962.71, 1910.1) * mm});
            skLineSegment(sketch, "E734", {"start": v(-13962.71, 1910.1) * mm, "end": v(-13960.86, 1910.09) * mm});
            skLineSegment(sketch, "E735", {"start": v(-13960.86, 1910.09) * mm, "end": v(-13959.77, 1910.1) * mm});
            skLineSegment(sketch, "E736", {"start": v(-13959.77, 1910.1) * mm, "end": v(-13843.13, 1914.75) * mm});
            skLineSegment(sketch, "E737", {"start": v(-13843.13, 1914.75) * mm, "end": v(-13815.89, 1650.25) * mm});
            skLineSegment(sketch, "E738", {"start": v(-13815.89, 1650.25) * mm, "end": v(-13931.03, 1631.04) * mm});
            skLineSegment(sketch, "E739", {"start": v(-13931.03, 1631.04) * mm, "end": v(-13932.1, 1630.83) * mm});
            skLineSegment(sketch, "E740", {"start": v(-13932.1, 1630.83) * mm, "end": v(-13933.91, 1630.44) * mm});
            skLineSegment(sketch, "E741", {"start": v(-13933.91, 1630.44) * mm, "end": v(-13936.45, 1629.85) * mm});
            skLineSegment(sketch, "E742", {"start": v(-13936.45, 1629.85) * mm, "end": v(-13939.7, 1629.02) * mm});
            skLineSegment(sketch, "E743", {"start": v(-13939.7, 1629.02) * mm, "end": v(-13943.68, 1627.94) * mm});
            skLineSegment(sketch, "E744", {"start": v(-13943.68, 1627.94) * mm, "end": v(-13948.35, 1626.58) * mm});
            skLineSegment(sketch, "E745", {"start": v(-13948.35, 1626.58) * mm, "end": v(-13953.73, 1624.9) * mm});
            skLineSegment(sketch, "E746", {"start": v(-13953.73, 1624.9) * mm, "end": v(-13959.78, 1622.9) * mm});
            skLineSegment(sketch, "E747", {"start": v(-13959.78, 1622.9) * mm, "end": v(-13966.51, 1620.52) * mm});
            skLineSegment(sketch, "E748", {"start": v(-13966.51, 1620.52) * mm, "end": v(-13973.9, 1617.76) * mm});
            skLineSegment(sketch, "E749", {"start": v(-13973.9, 1617.76) * mm, "end": v(-13981.95, 1614.58) * mm});
            skLineSegment(sketch, "E750", {"start": v(-13981.95, 1614.58) * mm, "end": v(-13990.63, 1610.97) * mm});
            skLineSegment(sketch, "E751", {"start": v(-13990.63, 1610.97) * mm, "end": v(-13999.93, 1606.9) * mm});
            skLineSegment(sketch, "E752", {"start": v(-13999.93, 1606.9) * mm, "end": v(-14009.84, 1602.34) * mm});
            skLineSegment(sketch, "E753", {"start": v(-14009.84, 1602.34) * mm, "end": v(-14020.35, 1597.27) * mm});
            skLineSegment(sketch, "E754", {"start": v(-14020.35, 1597.27) * mm, "end": v(-14031.44, 1591.67) * mm});
            skLineSegment(sketch, "E755", {"start": v(-14031.44, 1591.67) * mm, "end": v(-14043.1, 1585.52) * mm});
            skLineSegment(sketch, "E756", {"start": v(-14043.1, 1585.52) * mm, "end": v(-14055.3, 1578.79) * mm});
            skLineSegment(sketch, "E757", {"start": v(-14055.3, 1578.79) * mm, "end": v(-14068.02, 1571.45) * mm});
            skLineSegment(sketch, "E758", {"start": v(-14068.02, 1571.45) * mm, "end": v(-14081.25, 1563.5) * mm});
            skLineSegment(sketch, "E759", {"start": v(-14081.25, 1563.5) * mm, "end": v(-14094.98, 1554.9) * mm});
            skLineSegment(sketch, "E760", {"start": v(-14094.98, 1554.9) * mm, "end": v(-14109.18, 1545.64) * mm});
            skLineSegment(sketch, "E761", {"start": v(-14109.18, 1545.64) * mm, "end": v(-14123.83, 1535.7) * mm});
            skLineSegment(sketch, "E762", {"start": v(-14123.83, 1535.7) * mm, "end": v(-14138.92, 1525.05) * mm});
            skLineSegment(sketch, "E763", {"start": v(-14138.92, 1525.05) * mm, "end": v(-14154.41, 1513.68) * mm});
            skLineSegment(sketch, "E764", {"start": v(-14154.41, 1513.68) * mm, "end": v(-14170.3, 1501.57) * mm});
            skLineSegment(sketch, "E765", {"start": v(-14170.3, 1501.57) * mm, "end": v(-14186.55, 1488.7) * mm});
            skLineSegment(sketch, "E766", {"start": v(-14186.55, 1488.7) * mm, "end": v(-14203.14, 1475.06) * mm});
            skLineSegment(sketch, "E767", {"start": v(-14203.14, 1475.06) * mm, "end": v(-14220.06, 1460.63) * mm});
            skLineSegment(sketch, "E768", {"start": v(-14220.06, 1460.63) * mm, "end": v(-14237.27, 1445.38) * mm});
            skLineSegment(sketch, "E769", {"start": v(-14237.27, 1445.38) * mm, "end": v(-14254.76, 1429.31) * mm});
            skLineSegment(sketch, "E770", {"start": v(-14254.76, 1429.31) * mm, "end": v(-14272.5, 1412.4) * mm});
            skLineSegment(sketch, "E771", {"start": v(-14272.5, 1412.4) * mm, "end": v(-14290.45, 1394.64) * mm});
            skLineSegment(sketch, "E772", {"start": v(-14290.45, 1394.64) * mm, "end": v(-14308.6, 1376) * mm});
            skLineSegment(sketch, "E773", {"start": v(-14308.6, 1376) * mm, "end": v(-14313.12, 1359.9) * mm});
            skLineSegment(sketch, "E774", {"start": v(-14313.12, 1359.9) * mm, "end": v(-14276.62, 1226.96) * mm});
            skLineSegment(sketch, "E775", {"start": v(-14276.62, 1226.96) * mm, "end": v(-14264.52, 1215.42) * mm});
            skLineSegment(sketch, "E776", {"start": v(-14264.52, 1215.42) * mm, "end": v(-14239.4, 1208.67) * mm});
            skLineSegment(sketch, "E777", {"start": v(-14239.4, 1208.67) * mm, "end": v(-14214.88, 1202.57) * mm});
            skLineSegment(sketch, "E778", {"start": v(-14214.88, 1202.57) * mm, "end": v(-14191, 1197.09) * mm});
            skLineSegment(sketch, "E779", {"start": v(-14191, 1197.09) * mm, "end": v(-14167.76, 1192.2) * mm});
            skLineSegment(sketch, "E780", {"start": v(-14167.76, 1192.2) * mm, "end": v(-14145.17, 1187.88) * mm});
            skLineSegment(sketch, "E781", {"start": v(-14145.17, 1187.88) * mm, "end": v(-14123.25, 1184.1) * mm});
            skLineSegment(sketch, "E782", {"start": v(-14123.25, 1184.1) * mm, "end": v(-14102.02, 1180.85) * mm});
            skLineSegment(sketch, "E783", {"start": v(-14102.02, 1180.85) * mm, "end": v(-14081.48, 1178.09) * mm});
            skLineSegment(sketch, "E784", {"start": v(-14081.48, 1178.09) * mm, "end": v(-14061.64, 1175.79) * mm});
            skLineSegment(sketch, "E785", {"start": v(-14061.64, 1175.79) * mm, "end": v(-14042.5, 1173.93) * mm});
            skLineSegment(sketch, "E786", {"start": v(-14042.5, 1173.93) * mm, "end": v(-14024.1, 1172.48) * mm});
            skLineSegment(sketch, "E787", {"start": v(-14024.1, 1172.48) * mm, "end": v(-14006.43, 1171.4) * mm});
            skLineSegment(sketch, "E788", {"start": v(-14006.43, 1171.4) * mm, "end": v(-13989.5, 1170.7) * mm});
            skLineSegment(sketch, "E789", {"start": v(-13989.5, 1170.7) * mm, "end": v(-13973.3, 1170.32) * mm});
            skLineSegment(sketch, "E790", {"start": v(-13973.3, 1170.32) * mm, "end": v(-13957.85, 1170.24) * mm});
            skLineSegment(sketch, "E791", {"start": v(-13957.85, 1170.24) * mm, "end": v(-13943.17, 1170.43) * mm});
            skLineSegment(sketch, "E792", {"start": v(-13943.17, 1170.43) * mm, "end": v(-13929.24, 1170.87) * mm});
            skLineSegment(sketch, "E793", {"start": v(-13929.24, 1170.87) * mm, "end": v(-13916.08, 1171.53) * mm});
            skLineSegment(sketch, "E794", {"start": v(-13916.08, 1171.53) * mm, "end": v(-13903.69, 1172.37) * mm});
            skLineSegment(sketch, "E795", {"start": v(-13903.69, 1172.37) * mm, "end": v(-13892.07, 1173.38) * mm});
            skLineSegment(sketch, "E796", {"start": v(-13892.07, 1173.38) * mm, "end": v(-13881.21, 1174.53) * mm});
            skLineSegment(sketch, "E797", {"start": v(-13881.21, 1174.53) * mm, "end": v(-13871.13, 1175.78) * mm});
            skLineSegment(sketch, "E798", {"start": v(-13871.13, 1175.78) * mm, "end": v(-13861.83, 1177.1) * mm});
            skLineSegment(sketch, "E799", {"start": v(-13861.83, 1177.1) * mm, "end": v(-13853.3, 1178.48) * mm});
            skLineSegment(sketch, "E800", {"start": v(-13853.3, 1178.48) * mm, "end": v(-13845.53, 1179.88) * mm});
            skLineSegment(sketch, "E801", {"start": v(-13845.53, 1179.88) * mm, "end": v(-13838.53, 1181.28) * mm});
            skLineSegment(sketch, "E802", {"start": v(-13838.53, 1181.28) * mm, "end": v(-13832.3, 1182.64) * mm});
            skLineSegment(sketch, "E803", {"start": v(-13832.3, 1182.64) * mm, "end": v(-13826.82, 1183.94) * mm});
            skLineSegment(sketch, "E804", {"start": v(-13826.82, 1183.94) * mm, "end": v(-13822.1, 1185.16) * mm});
            skLineSegment(sketch, "E805", {"start": v(-13822.1, 1185.16) * mm, "end": v(-13818.14, 1186.26) * mm});
            skLineSegment(sketch, "E806", {"start": v(-13818.14, 1186.26) * mm, "end": v(-13814.92, 1187.21) * mm});
            skLineSegment(sketch, "E807", {"start": v(-13814.92, 1187.21) * mm, "end": v(-13812.43, 1188) * mm});
            skLineSegment(sketch, "E808", {"start": v(-13812.43, 1188) * mm, "end": v(-13810.68, 1188.59) * mm});
            skLineSegment(sketch, "E809", {"start": v(-13810.68, 1188.59) * mm, "end": v(-13809.65, 1188.96) * mm});
            skLineSegment(sketch, "E810", {"start": v(-13809.65, 1188.96) * mm, "end": v(-13700.84, 1231.23) * mm});
            skLineSegment(sketch, "E811", {"start": v(-13700.84, 1231.23) * mm, "end": v(-13589.2, 989.9) * mm});
            skLineSegment(sketch, "E812", {"start": v(-13589.2, 989.9) * mm, "end": v(-13691.85, 934.34) * mm});
            skLineSegment(sketch, "E813", {"start": v(-13691.85, 934.34) * mm, "end": v(-13692.8, 933.8) * mm});
            skLineSegment(sketch, "E814", {"start": v(-13692.8, 933.8) * mm, "end": v(-13694.39, 932.84) * mm});
            skLineSegment(sketch, "E815", {"start": v(-13694.39, 932.84) * mm, "end": v(-13696.6, 931.46) * mm});
            skLineSegment(sketch, "E816", {"start": v(-13696.6, 931.46) * mm, "end": v(-13699.4, 929.62) * mm});
            skLineSegment(sketch, "E817", {"start": v(-13699.4, 929.62) * mm, "end": v(-13702.81, 927.31) * mm});
            skLineSegment(sketch, "E818", {"start": v(-13702.81, 927.31) * mm, "end": v(-13706.8, 924.5) * mm});
            skLineSegment(sketch, "E819", {"start": v(-13706.8, 924.5) * mm, "end": v(-13711.33, 921.17) * mm});
            skLineSegment(sketch, "E820", {"start": v(-13711.33, 921.17) * mm, "end": v(-13716.4, 917.3) * mm});
            skLineSegment(sketch, "E821", {"start": v(-13716.4, 917.3) * mm, "end": v(-13722, 912.87) * mm});
            skLineSegment(sketch, "E822", {"start": v(-13722, 912.87) * mm, "end": v(-13728.1, 907.86) * mm});
            skLineSegment(sketch, "E823", {"start": v(-13728.1, 907.86) * mm, "end": v(-13734.67, 902.25) * mm});
            skLineSegment(sketch, "E824", {"start": v(-13734.67, 902.25) * mm, "end": v(-13741.7, 896.01) * mm});
            skLineSegment(sketch, "E825", {"start": v(-13741.7, 896.01) * mm, "end": v(-13749.18, 889.14) * mm});
            skLineSegment(sketch, "E826", {"start": v(-13749.18, 889.14) * mm, "end": v(-13757.08, 881.61) * mm});
            skLineSegment(sketch, "E827", {"start": v(-13757.08, 881.61) * mm, "end": v(-13765.37, 873.4) * mm});
            skLineSegment(sketch, "E828", {"start": v(-13765.37, 873.4) * mm, "end": v(-13774.04, 864.5) * mm});
            skLineSegment(sketch, "E829", {"start": v(-13774.04, 864.5) * mm, "end": v(-13783.07, 854.9) * mm});
            skLineSegment(sketch, "E830", {"start": v(-13783.07, 854.9) * mm, "end": v(-13792.41, 844.58) * mm});
            skLineSegment(sketch, "E831", {"start": v(-13792.41, 844.58) * mm, "end": v(-13802.07, 833.5) * mm});
            skLineSegment(sketch, "E832", {"start": v(-13802.07, 833.5) * mm, "end": v(-13812, 821.69) * mm});
            skLineSegment(sketch, "E833", {"start": v(-13812, 821.69) * mm, "end": v(-13822.2, 809.1) * mm});
            skLineSegment(sketch, "E834", {"start": v(-13822.2, 809.1) * mm, "end": v(-13832.62, 795.73) * mm});
            skLineSegment(sketch, "E835", {"start": v(-13832.62, 795.73) * mm, "end": v(-13843.25, 781.57) * mm});
            skLineSegment(sketch, "E836", {"start": v(-13843.25, 781.57) * mm, "end": v(-13854.06, 766.6) * mm});
            skLineSegment(sketch, "E837", {"start": v(-13854.06, 766.6) * mm, "end": v(-13865.03, 750.81) * mm});
            skLineSegment(sketch, "E838", {"start": v(-13865.03, 750.81) * mm, "end": v(-13876.12, 734.2) * mm});
            skLineSegment(sketch, "E839", {"start": v(-13876.12, 734.2) * mm, "end": v(-13887.31, 716.76) * mm});
            skLineSegment(sketch, "E840", {"start": v(-13887.31, 716.76) * mm, "end": v(-13898.58, 698.46) * mm});
            skLineSegment(sketch, "E841", {"start": v(-13898.58, 698.46) * mm, "end": v(-13909.9, 679.32) * mm});
            skLineSegment(sketch, "E842", {"start": v(-13909.9, 679.32) * mm, "end": v(-13921.22, 659.3) * mm});
            skLineSegment(sketch, "E843", {"start": v(-13921.22, 659.3) * mm, "end": v(-13932.54, 638.43) * mm});
            skLineSegment(sketch, "E844", {"start": v(-13932.54, 638.43) * mm, "end": v(-13943.83, 616.68) * mm});
            skLineSegment(sketch, "E845", {"start": v(-13943.83, 616.68) * mm, "end": v(-13955.04, 594.05) * mm});
            skLineSegment(sketch, "E846", {"start": v(-13955.04, 594.05) * mm, "end": v(-13966.17, 570.53) * mm});
            skLineSegment(sketch, "E847", {"start": v(-13966.17, 570.53) * mm, "end": v(-13965.2, 553.84) * mm});
            skLineSegment(sketch, "E848", {"start": v(-13965.2, 553.84) * mm, "end": v(-13887.51, 439.94) * mm});
            skLineSegment(sketch, "E849", {"start": v(-13887.51, 439.94) * mm, "end": v(-13872.32, 432.96) * mm});
            skLineSegment(sketch, "E850", {"start": v(-13872.32, 432.96) * mm, "end": v(-13846.37, 434.74) * mm});
            skLineSegment(sketch, "E851", {"start": v(-13846.37, 434.74) * mm, "end": v(-13821.2, 436.93) * mm});
            skLineSegment(sketch, "E852", {"start": v(-13821.2, 436.93) * mm, "end": v(-13796.83, 439.5) * mm});
            skLineSegment(sketch, "E853", {"start": v(-13796.83, 439.5) * mm, "end": v(-13773.26, 442.42) * mm});
            skLineSegment(sketch, "E854", {"start": v(-13773.26, 442.42) * mm, "end": v(-13750.5, 445.67) * mm});
            skLineSegment(sketch, "E855", {"start": v(-13750.5, 445.67) * mm, "end": v(-13728.55, 449.22) * mm});
            skLineSegment(sketch, "E856", {"start": v(-13728.55, 449.22) * mm, "end": v(-13707.4, 453.03) * mm});
            skLineSegment(sketch, "E857", {"start": v(-13707.4, 453.03) * mm, "end": v(-13687.08, 457.09) * mm});
            skLineSegment(sketch, "E858", {"start": v(-13687.08, 457.09) * mm, "end": v(-13667.56, 461.35) * mm});
            skLineSegment(sketch, "E859", {"start": v(-13667.56, 461.35) * mm, "end": v(-13648.87, 465.8) * mm});
            skLineSegment(sketch, "E860", {"start": v(-13648.87, 465.8) * mm, "end": v(-13630.99, 470.4) * mm});
            skLineSegment(sketch, "E861", {"start": v(-13630.99, 470.4) * mm, "end": v(-13613.92, 475.14) * mm});
            skLineSegment(sketch, "E862", {"start": v(-13613.92, 475.14) * mm, "end": v(-13597.67, 479.97) * mm});
            skLineSegment(sketch, "E863", {"start": v(-13597.67, 479.97) * mm, "end": v(-13582.23, 484.86) * mm});
            skLineSegment(sketch, "E864", {"start": v(-13582.23, 484.86) * mm, "end": v(-13567.6, 489.8) * mm});
            skLineSegment(sketch, "E865", {"start": v(-13567.6, 489.8) * mm, "end": v(-13553.77, 494.75) * mm});
            skLineSegment(sketch, "E866", {"start": v(-13553.77, 494.75) * mm, "end": v(-13540.75, 499.69) * mm});
            skLineSegment(sketch, "E867", {"start": v(-13540.75, 499.69) * mm, "end": v(-13528.51, 504.58) * mm});
            skLineSegment(sketch, "E868", {"start": v(-13528.51, 504.58) * mm, "end": v(-13517.07, 509.4) * mm});
            skLineSegment(sketch, "E869", {"start": v(-13517.07, 509.4) * mm, "end": v(-13506.4, 514.14) * mm});
            skLineSegment(sketch, "E870", {"start": v(-13506.4, 514.14) * mm, "end": v(-13496.5, 518.74) * mm});
            skLineSegment(sketch, "E871", {"start": v(-13496.5, 518.74) * mm, "end": v(-13487.38, 523.2) * mm});
            skLineSegment(sketch, "E872", {"start": v(-13487.38, 523.2) * mm, "end": v(-13479, 527.48) * mm});
            skLineSegment(sketch, "E873", {"start": v(-13479, 527.48) * mm, "end": v(-13471.38, 531.55) * mm});
            skLineSegment(sketch, "E874", {"start": v(-13471.38, 531.55) * mm, "end": v(-13464.5, 535.4) * mm});
            skLineSegment(sketch, "E875", {"start": v(-13464.5, 535.4) * mm, "end": v(-13458.33, 539) * mm});
            skLineSegment(sketch, "E876", {"start": v(-13458.33, 539) * mm, "end": v(-13452.87, 542.3) * mm});
            skLineSegment(sketch, "E877", {"start": v(-13452.87, 542.3) * mm, "end": v(-13448.12, 545.31) * mm});
            skLineSegment(sketch, "E878", {"start": v(-13448.12, 545.31) * mm, "end": v(-13444.05, 548) * mm});
            skLineSegment(sketch, "E879", {"start": v(-13444.05, 548) * mm, "end": v(-13440.66, 550.32) * mm});
            skLineSegment(sketch, "E880", {"start": v(-13440.66, 550.32) * mm, "end": v(-13437.92, 552.27) * mm});
            skLineSegment(sketch, "E881", {"start": v(-13437.92, 552.27) * mm, "end": v(-13435.83, 553.82) * mm});
            skLineSegment(sketch, "E882", {"start": v(-13435.83, 553.82) * mm, "end": v(-13434.36, 554.95) * mm});
            skLineSegment(sketch, "E883", {"start": v(-13434.36, 554.95) * mm, "end": v(-13433.5, 555.63) * mm});
            skLineSegment(sketch, "E884", {"start": v(-13433.5, 555.63) * mm, "end": v(-13344.32, 630.94) * mm});
            skLineSegment(sketch, "E885", {"start": v(-13344.32, 630.94) * mm, "end": v(-13160.36, 438.95) * mm});
            skLineSegment(sketch, "E886", {"start": v(-13160.36, 438.95) * mm, "end": v(-13239.42, 353.06) * mm});
            skLineSegment(sketch, "E887", {"start": v(-13239.42, 353.06) * mm, "end": v(-13240.14, 352.23) * mm});
            skLineSegment(sketch, "E888", {"start": v(-13240.14, 352.23) * mm, "end": v(-13241.33, 350.82) * mm});
            skLineSegment(sketch, "E889", {"start": v(-13241.33, 350.82) * mm, "end": v(-13242.97, 348.79) * mm});
            skLineSegment(sketch, "E890", {"start": v(-13242.97, 348.79) * mm, "end": v(-13245.03, 346.14) * mm});
            skLineSegment(sketch, "E891", {"start": v(-13245.03, 346.14) * mm, "end": v(-13247.5, 342.85) * mm});
            skLineSegment(sketch, "E892", {"start": v(-13247.5, 342.85) * mm, "end": v(-13250.35, 338.9) * mm});
            skLineSegment(sketch, "E893", {"start": v(-13250.35, 338.9) * mm, "end": v(-13253.56, 334.28) * mm});
            skLineSegment(sketch, "E894", {"start": v(-13253.56, 334.28) * mm, "end": v(-13257.1, 328.97) * mm});
            skLineSegment(sketch, "E895", {"start": v(-13257.1, 328.97) * mm, "end": v(-13260.96, 322.96) * mm});
            skLineSegment(sketch, "E896", {"start": v(-13260.96, 322.96) * mm, "end": v(-13265.1, 316.25) * mm});
            skLineSegment(sketch, "E897", {"start": v(-13265.1, 316.25) * mm, "end": v(-13269.5, 308.8) * mm});
            skLineSegment(sketch, "E898", {"start": v(-13269.5, 308.8) * mm, "end": v(-13274.12, 300.62) * mm});
            skLineSegment(sketch, "E899", {"start": v(-13274.12, 300.62) * mm, "end": v(-13278.97, 291.7) * mm});
            skLineSegment(sketch, "E900", {"start": v(-13278.97, 291.7) * mm, "end": v(-13283.99, 282) * mm});
            skLineSegment(sketch, "E901", {"start": v(-13283.99, 282) * mm, "end": v(-13289.17, 271.55) * mm});
            skLineSegment(sketch, "E902", {"start": v(-13289.17, 271.55) * mm, "end": v(-13294.48, 260.32) * mm});
            skLineSegment(sketch, "E903", {"start": v(-13294.48, 260.32) * mm, "end": v(-13299.9, 248.3) * mm});
            skLineSegment(sketch, "E904", {"start": v(-13299.9, 248.3) * mm, "end": v(-13305.38, 235.5) * mm});
            skLineSegment(sketch, "E905", {"start": v(-13305.38, 235.5) * mm, "end": v(-13310.92, 221.9) * mm});
            skLineSegment(sketch, "E906", {"start": v(-13310.92, 221.9) * mm, "end": v(-13316.48, 207.5) * mm});
            skLineSegment(sketch, "E907", {"start": v(-13316.48, 207.5) * mm, "end": v(-13322.04, 192.28) * mm});
            skLineSegment(sketch, "E908", {"start": v(-13322.04, 192.28) * mm, "end": v(-13327.55, 176.25) * mm});
            skLineSegment(sketch, "E909", {"start": v(-13327.55, 176.25) * mm, "end": v(-13333, 159.4) * mm});
            skLineSegment(sketch, "E910", {"start": v(-13333, 159.4) * mm, "end": v(-13338.37, 141.73) * mm});
            skLineSegment(sketch, "E911", {"start": v(-13338.37, 141.73) * mm, "end": v(-13343.62, 123.25) * mm});
            skLineSegment(sketch, "E912", {"start": v(-13343.62, 123.25) * mm, "end": v(-13348.72, 103.93) * mm});
            skLineSegment(sketch, "E913", {"start": v(-13348.72, 103.93) * mm, "end": v(-13353.64, 83.8) * mm});
            skLineSegment(sketch, "E914", {"start": v(-13353.64, 83.8) * mm, "end": v(-13358.36, 62.84) * mm});
            skLineSegment(sketch, "E915", {"start": v(-13358.36, 62.84) * mm, "end": v(-13362.84, 41.06) * mm});
            skLineSegment(sketch, "E916", {"start": v(-13362.84, 41.06) * mm, "end": v(-13367.06, 18.45) * mm});
            skLineSegment(sketch, "E917", {"start": v(-13367.06, 18.45) * mm, "end": v(-13370.99, -4.97) * mm});
            skLineSegment(sketch, "E918", {"start": v(-13370.99, -4.97) * mm, "end": v(-13374.6, -29.2) * mm});
            skLineSegment(sketch, "E919", {"start": v(-13374.6, -29.2) * mm, "end": v(-13377.86, -54.25) * mm});
            skLineSegment(sketch, "E920", {"start": v(-13377.86, -54.25) * mm, "end": v(-13380.74, -80.1) * mm});
            skLineSegment(sketch, "E921", {"start": v(-13380.74, -80.1) * mm, "end": v(-13374.42, -95.59) * mm});
            skLineSegment(sketch, "E922", {"start": v(-13374.42, -95.59) * mm, "end": v(-13263.95, -178.08) * mm});
            skLineSegment(sketch, "E923", {"start": v(-13263.95, -178.08) * mm, "end": v(-13247.31, -179.75) * mm});
            skLineSegment(sketch, "E924", {"start": v(-13247.31, -179.75) * mm, "end": v(-13223.34, -169.65) * mm});
            skLineSegment(sketch, "E925", {"start": v(-13223.34, -169.65) * mm, "end": v(-13200.25, -159.4) * mm});
            skLineSegment(sketch, "E926", {"start": v(-13200.25, -159.4) * mm, "end": v(-13178.03, -149.06) * mm});
            skLineSegment(sketch, "E927", {"start": v(-13178.03, -149.06) * mm, "end": v(-13156.7, -138.65) * mm});
            skLineSegment(sketch, "E928", {"start": v(-13156.7, -138.65) * mm, "end": v(-13136.22, -128.18) * mm});
            skLineSegment(sketch, "E929", {"start": v(-13136.22, -128.18) * mm, "end": v(-13116.6, -117.7) * mm});
            skLineSegment(sketch, "E930", {"start": v(-13116.6, -117.7) * mm, "end": v(-13097.85, -107.22) * mm});
            skLineSegment(sketch, "E931", {"start": v(-13097.85, -107.22) * mm, "end": v(-13079.94, -96.79) * mm});
            skLineSegment(sketch, "E932", {"start": v(-13079.94, -96.79) * mm, "end": v(-13062.87, -86.42) * mm});
            skLineSegment(sketch, "E933", {"start": v(-13062.87, -86.42) * mm, "end": v(-13046.63, -76.14) * mm});
            skLineSegment(sketch, "E934", {"start": v(-13046.63, -76.14) * mm, "end": v(-13031.21, -65.98) * mm});
            skLineSegment(sketch, "E935", {"start": v(-13031.21, -65.98) * mm, "end": v(-13016.6, -55.96) * mm});
            skLineSegment(sketch, "E936", {"start": v(-13016.6, -55.96) * mm, "end": v(-13002.8, -46.12) * mm});
            skLineSegment(sketch, "E937", {"start": v(-13002.8, -46.12) * mm, "end": v(-12989.8, -36.48) * mm});
            skLineSegment(sketch, "E938", {"start": v(-12989.8, -36.48) * mm, "end": v(-12977.56, -27.05) * mm});
            skLineSegment(sketch, "E939", {"start": v(-12977.56, -27.05) * mm, "end": v(-12966.09, -17.88) * mm});
            skLineSegment(sketch, "E940", {"start": v(-12966.09, -17.88) * mm, "end": v(-12955.37, -8.98) * mm});
            skLineSegment(sketch, "E941", {"start": v(-12955.37, -8.98) * mm, "end": v(-12945.39, -0.38) * mm});
            skLineSegment(sketch, "E942", {"start": v(-12945.39, -0.38) * mm, "end": v(-12936.13, 7.9) * mm});
            skLineSegment(sketch, "E943", {"start": v(-12936.13, 7.9) * mm, "end": v(-12927.58, 15.84) * mm});
            skLineSegment(sketch, "E944", {"start": v(-12927.58, 15.84) * mm, "end": v(-12919.71, 23.4) * mm});
            skLineSegment(sketch, "E945", {"start": v(-12919.71, 23.4) * mm, "end": v(-12912.53, 30.58) * mm});
            skLineSegment(sketch, "E946", {"start": v(-12912.53, 30.58) * mm, "end": v(-12906, 37.35) * mm});
            skLineSegment(sketch, "E947", {"start": v(-12906, 37.35) * mm, "end": v(-12900.11, 43.68) * mm});
            skLineSegment(sketch, "E948", {"start": v(-12900.11, 43.68) * mm, "end": v(-12894.84, 49.55) * mm});
            skLineSegment(sketch, "E949", {"start": v(-12894.84, 49.55) * mm, "end": v(-12890.18, 54.95) * mm});
            skLineSegment(sketch, "E950", {"start": v(-12890.18, 54.95) * mm, "end": v(-12886.1, 59.86) * mm});
            skLineSegment(sketch, "E951", {"start": v(-12886.1, 59.86) * mm, "end": v(-12882.57, 64.25) * mm});
            skLineSegment(sketch, "E952", {"start": v(-12882.57, 64.25) * mm, "end": v(-12879.6, 68.1) * mm});
            skLineSegment(sketch, "E953", {"start": v(-12879.6, 68.1) * mm, "end": v(-12877.14, 71.4) * mm});
            skLineSegment(sketch, "E954", {"start": v(-12877.14, 71.4) * mm, "end": v(-12875.19, 74.14) * mm});
            skLineSegment(sketch, "E955", {"start": v(-12875.19, 74.14) * mm, "end": v(-12873.71, 76.28) * mm});
            skLineSegment(sketch, "E956", {"start": v(-12873.71, 76.28) * mm, "end": v(-12872.69, 77.83) * mm});
            skLineSegment(sketch, "E957", {"start": v(-12872.69, 77.83) * mm, "end": v(-12872.1, 78.75) * mm});
            skLineSegment(sketch, "E958", {"start": v(-12872.1, 78.75) * mm, "end": v(-12812.2, 178.94) * mm});
            skLineSegment(sketch, "E959", {"start": v(-12812.2, 178.94) * mm, "end": v(-12575.87, 57.08) * mm});
            skLineSegment(sketch, "E960", {"start": v(-12575.87, 57.08) * mm, "end": v(-12622.76, -49.83) * mm});
            skLineSegment(sketch, "E961", {"start": v(-12622.76, -49.83) * mm, "end": v(-12623.17, -50.84) * mm});
            skLineSegment(sketch, "E962", {"start": v(-12623.17, -50.84) * mm, "end": v(-12623.84, -52.57) * mm});
            skLineSegment(sketch, "E963", {"start": v(-12623.84, -52.57) * mm, "end": v(-12624.73, -55.01) * mm});
            skLineSegment(sketch, "E964", {"start": v(-12624.73, -55.01) * mm, "end": v(-12625.82, -58.2) * mm});
            skLineSegment(sketch, "E965", {"start": v(-12625.82, -58.2) * mm, "end": v(-12627.09, -62.1) * mm});
            skLineSegment(sketch, "E966", {"start": v(-12627.09, -62.1) * mm, "end": v(-12628.5, -66.77) * mm});
            skLineSegment(sketch, "E967", {"start": v(-12628.5, -66.77) * mm, "end": v(-12630.04, -72.18) * mm});
            skLineSegment(sketch, "E968", {"start": v(-12630.04, -72.18) * mm, "end": v(-12631.66, -78.35) * mm});
            skLineSegment(sketch, "E969", {"start": v(-12631.66, -78.35) * mm, "end": v(-12633.36, -85.28) * mm});
            skLineSegment(sketch, "E970", {"start": v(-12633.36, -85.28) * mm, "end": v(-12635.09, -92.98) * mm});
            skLineSegment(sketch, "E971", {"start": v(-12635.09, -92.98) * mm, "end": v(-12636.83, -101.45) * mm});
            skLineSegment(sketch, "E972", {"start": v(-12636.83, -101.45) * mm, "end": v(-12638.56, -110.7) * mm});
            skLineSegment(sketch, "E973", {"start": v(-12638.56, -110.7) * mm, "end": v(-12640.24, -120.7) * mm});
            skLineSegment(sketch, "E974", {"start": v(-12640.24, -120.7) * mm, "end": v(-12641.84, -131.5) * mm});
            skLineSegment(sketch, "E975", {"start": v(-12641.84, -131.5) * mm, "end": v(-12643.35, -143.07) * mm});
            skLineSegment(sketch, "E976", {"start": v(-12643.35, -143.07) * mm, "end": v(-12644.72, -155.42) * mm});
            skLineSegment(sketch, "E977", {"start": v(-12644.72, -155.42) * mm, "end": v(-12645.94, -168.54) * mm});
            skLineSegment(sketch, "E978", {"start": v(-12645.94, -168.54) * mm, "end": v(-12646.98, -182.43) * mm});
            skLineSegment(sketch, "E979", {"start": v(-12646.98, -182.43) * mm, "end": v(-12647.8, -197.1) * mm});
            skLineSegment(sketch, "E980", {"start": v(-12647.8, -197.1) * mm, "end": v(-12648.38, -212.53) * mm});
            skLineSegment(sketch, "E981", {"start": v(-12648.38, -212.53) * mm, "end": v(-12648.7, -228.72) * mm});
            skLineSegment(sketch, "E982", {"start": v(-12648.7, -228.72) * mm, "end": v(-12648.7, -245.67) * mm});
            skLineSegment(sketch, "E983", {"start": v(-12648.7, -245.67) * mm, "end": v(-12648.4, -263.38) * mm});
            skLineSegment(sketch, "E984", {"start": v(-12648.4, -263.38) * mm, "end": v(-12647.73, -281.83) * mm});
            skLineSegment(sketch, "E985", {"start": v(-12647.73, -281.83) * mm, "end": v(-12646.7, -301.02) * mm});
            skLineSegment(sketch, "E986", {"start": v(-12646.7, -301.02) * mm, "end": v(-12645.24, -320.94) * mm});
            skLineSegment(sketch, "E987", {"start": v(-12645.24, -320.94) * mm, "end": v(-12643.36, -341.58) * mm});
            skLineSegment(sketch, "E988", {"start": v(-12643.36, -341.58) * mm, "end": v(-12641.01, -362.94) * mm});
            skLineSegment(sketch, "E989", {"start": v(-12641.01, -362.94) * mm, "end": v(-12638.18, -385) * mm});
            skLineSegment(sketch, "E990", {"start": v(-12638.18, -385) * mm, "end": v(-12634.83, -407.75) * mm});
            skLineSegment(sketch, "E991", {"start": v(-12634.83, -407.75) * mm, "end": v(-12630.94, -431.17) * mm});
            skLineSegment(sketch, "E992", {"start": v(-12630.94, -431.17) * mm, "end": v(-12626.49, -455.27) * mm});
            skLineSegment(sketch, "E993", {"start": v(-12626.49, -455.27) * mm, "end": v(-12621.44, -480.02) * mm});
            skLineSegment(sketch, "E994", {"start": v(-12621.44, -480.02) * mm, "end": v(-12615.77, -505.4) * mm});
            skLineSegment(sketch, "E995", {"start": v(-12615.77, -505.4) * mm, "end": v(-12604.77, -518) * mm});
            skLineSegment(sketch, "E996", {"start": v(-12604.77, -518) * mm, "end": v(-12473.5, -560.15) * mm});
            skLineSegment(sketch, "E997", {"start": v(-12473.5, -560.15) * mm, "end": v(-12457.22, -556.33) * mm});
            skLineSegment(sketch, "E998", {"start": v(-12457.22, -556.33) * mm, "end": v(-12437.83, -538.99) * mm});
            skLineSegment(sketch, "E999", {"start": v(-12437.83, -538.99) * mm, "end": v(-12419.31, -521.8) * mm});
            skLineSegment(sketch, "E1000", {"start": v(-12419.31, -521.8) * mm, "end": v(-12401.66, -504.8) * mm});
            skLineSegment(sketch, "E1001", {"start": v(-12401.66, -504.8) * mm, "end": v(-12384.86, -488.03) * mm});
            skLineSegment(sketch, "E1002", {"start": v(-12384.86, -488.03) * mm, "end": v(-12368.89, -471.48) * mm});
            skLineSegment(sketch, "E1003", {"start": v(-12368.89, -471.48) * mm, "end": v(-12353.74, -455.2) * mm});
            skLineSegment(sketch, "E1004", {"start": v(-12353.74, -455.2) * mm, "end": v(-12339.4, -439.2) * mm});
            skLineSegment(sketch, "E1005", {"start": v(-12339.4, -439.2) * mm, "end": v(-12325.85, -423.51) * mm});
            skLineSegment(sketch, "E1006", {"start": v(-12325.85, -423.51) * mm, "end": v(-12313.07, -408.16) * mm});
            skLineSegment(sketch, "E1007", {"start": v(-12313.07, -408.16) * mm, "end": v(-12301.05, -393.17) * mm});
            skLineSegment(sketch, "E1008", {"start": v(-12301.05, -393.17) * mm, "end": v(-12289.77, -378.55) * mm});
            skLineSegment(sketch, "E1009", {"start": v(-12289.77, -378.55) * mm, "end": v(-12279.21, -364.34) * mm});
            skLineSegment(sketch, "E1010", {"start": v(-12279.21, -364.34) * mm, "end": v(-12269.35, -350.55) * mm});
            skLineSegment(sketch, "E1011", {"start": v(-12269.35, -350.55) * mm, "end": v(-12260.17, -337.2) * mm});
            skLineSegment(sketch, "E1012", {"start": v(-12260.17, -337.2) * mm, "end": v(-12251.66, -324.32) * mm});
            skLineSegment(sketch, "E1013", {"start": v(-12251.66, -324.32) * mm, "end": v(-12243.8, -311.91) * mm});
            skLineSegment(sketch, "E1014", {"start": v(-12243.8, -311.91) * mm, "end": v(-12236.54, -300.02) * mm});
            skLineSegment(sketch, "E1015", {"start": v(-12236.54, -300.02) * mm, "end": v(-12229.9, -288.64) * mm});
            skLineSegment(sketch, "E1016", {"start": v(-12229.9, -288.64) * mm, "end": v(-12223.83, -277.8) * mm});
            skLineSegment(sketch, "E1017", {"start": v(-12223.83, -277.8) * mm, "end": v(-12218.32, -267.52) * mm});
            skLineSegment(sketch, "E1018", {"start": v(-12218.32, -267.52) * mm, "end": v(-12213.34, -257.8) * mm});
            skLineSegment(sketch, "E1019", {"start": v(-12213.34, -257.8) * mm, "end": v(-12208.87, -248.69) * mm});
            skLineSegment(sketch, "E1020", {"start": v(-12208.87, -248.69) * mm, "end": v(-12204.9, -240.17) * mm});
            skLineSegment(sketch, "E1021", {"start": v(-12204.9, -240.17) * mm, "end": v(-12201.38, -232.27) * mm});
            skLineSegment(sketch, "E1022", {"start": v(-12201.38, -232.27) * mm, "end": v(-12198.3, -225) * mm});
            skLineSegment(sketch, "E1023", {"start": v(-12198.3, -225) * mm, "end": v(-12195.64, -218.38) * mm});
            skLineSegment(sketch, "E1024", {"start": v(-12195.64, -218.38) * mm, "end": v(-12193.37, -212.42) * mm});
            skLineSegment(sketch, "E1025", {"start": v(-12193.37, -212.42) * mm, "end": v(-12191.47, -207.12) * mm});
            skLineSegment(sketch, "E1026", {"start": v(-12191.47, -207.12) * mm, "end": v(-12189.9, -202.5) * mm});
            skLineSegment(sketch, "E1027", {"start": v(-12189.9, -202.5) * mm, "end": v(-12188.66, -198.59) * mm});
            skLineSegment(sketch, "E1028", {"start": v(-12188.66, -198.59) * mm, "end": v(-12187.7, -195.37) * mm});
            skLineSegment(sketch, "E1029", {"start": v(-12187.7, -195.37) * mm, "end": v(-12187, -192.86) * mm});
            skLineSegment(sketch, "E1030", {"start": v(-12187, -192.86) * mm, "end": v(-12186.53, -191.07) * mm});
            skLineSegment(sketch, "E1031", {"start": v(-12186.53, -191.07) * mm, "end": v(-12186.28, -190) * mm});
            skLineSegment(sketch, "E1032", {"start": v(-12186.28, -190) * mm, "end": v(-12162.15, -75.79) * mm});
            skLineSegment(sketch, "E1033", {"start": v(-12162.15, -75.79) * mm, "end": v(-11899.06, -114.31) * mm});
            skLineSegment(sketch, "E1034", {"start": v(-11899.06, -114.31) * mm, "end": v(-11908.7, -230.65) * mm});
            skLineSegment(sketch, "E1035", {"start": v(-11908.7, -230.65) * mm, "end": v(-11908.75, -231.74) * mm});
            skLineSegment(sketch, "E1036", {"start": v(-11908.75, -231.74) * mm, "end": v(-11908.82, -233.6) * mm});
            skLineSegment(sketch, "E1037", {"start": v(-11908.82, -233.6) * mm, "end": v(-11908.87, -236.2) * mm});
            skLineSegment(sketch, "E1038", {"start": v(-11908.87, -236.2) * mm, "end": v(-11908.87, -239.56) * mm});
            skLineSegment(sketch, "E1039", {"start": v(-11908.87, -239.56) * mm, "end": v(-11908.8, -243.67) * mm});
            skLineSegment(sketch, "E1040", {"start": v(-11908.8, -243.67) * mm, "end": v(-11908.62, -248.54) * mm});
            skLineSegment(sketch, "E1041", {"start": v(-11908.62, -248.54) * mm, "end": v(-11908.32, -254.16) * mm});
            skLineSegment(sketch, "E1042", {"start": v(-11908.32, -254.16) * mm, "end": v(-11907.85, -260.52) * mm});
            skLineSegment(sketch, "E1043", {"start": v(-11907.85, -260.52) * mm, "end": v(-11907.2, -267.63) * mm});
            skLineSegment(sketch, "E1044", {"start": v(-11907.2, -267.63) * mm, "end": v(-11906.34, -275.47) * mm});
            skLineSegment(sketch, "E1045", {"start": v(-11906.34, -275.47) * mm, "end": v(-11905.24, -284.05) * mm});
            skLineSegment(sketch, "E1046", {"start": v(-11905.24, -284.05) * mm, "end": v(-11903.87, -293.35) * mm});
            skLineSegment(sketch, "E1047", {"start": v(-11903.87, -293.35) * mm, "end": v(-11902.2, -303.37) * mm});
            skLineSegment(sketch, "E1048", {"start": v(-11902.2, -303.37) * mm, "end": v(-11900.22, -314.1) * mm});
            skLineSegment(sketch, "E1049", {"start": v(-11900.22, -314.1) * mm, "end": v(-11897.89, -325.53) * mm});
            skLineSegment(sketch, "E1050", {"start": v(-11897.89, -325.53) * mm, "end": v(-11895.18, -337.65) * mm});
            skLineSegment(sketch, "E1051", {"start": v(-11895.18, -337.65) * mm, "end": v(-11892.08, -350.46) * mm});
            skLineSegment(sketch, "E1052", {"start": v(-11892.08, -350.46) * mm, "end": v(-11888.54, -363.93) * mm});
            skLineSegment(sketch, "E1053", {"start": v(-11888.54, -363.93) * mm, "end": v(-11884.56, -378.07) * mm});
            skLineSegment(sketch, "E1054", {"start": v(-11884.56, -378.07) * mm, "end": v(-11880.1, -392.86) * mm});
            skLineSegment(sketch, "E1055", {"start": v(-11880.1, -392.86) * mm, "end": v(-11875.13, -408.27) * mm});
            skLineSegment(sketch, "E1056", {"start": v(-11875.13, -408.27) * mm, "end": v(-11869.64, -424.31) * mm});
            skLineSegment(sketch, "E1057", {"start": v(-11869.64, -424.31) * mm, "end": v(-11863.6, -440.96) * mm});
            skLineSegment(sketch, "E1058", {"start": v(-11863.6, -440.96) * mm, "end": v(-11856.98, -458.2) * mm});
            skLineSegment(sketch, "E1059", {"start": v(-11856.98, -458.2) * mm, "end": v(-11849.77, -476) * mm});
            skLineSegment(sketch, "E1060", {"start": v(-11849.77, -476) * mm, "end": v(-11841.93, -494.38) * mm});
            skLineSegment(sketch, "E1061", {"start": v(-11841.93, -494.38) * mm, "end": v(-11833.44, -513.29) * mm});
            skLineSegment(sketch, "E1062", {"start": v(-11833.44, -513.29) * mm, "end": v(-11824.3, -532.73) * mm});
            skLineSegment(sketch, "E1063", {"start": v(-11824.3, -532.73) * mm, "end": v(-11814.45, -552.67) * mm});
            skLineSegment(sketch, "E1064", {"start": v(-11814.45, -552.67) * mm, "end": v(-11803.9, -573.1) * mm});
            skLineSegment(sketch, "E1065", {"start": v(-11803.9, -573.1) * mm, "end": v(-11792.61, -594) * mm});
            skLineSegment(sketch, "E1066", {"start": v(-11792.61, -594) * mm, "end": v(-11780.57, -615.34) * mm});
            skLineSegment(sketch, "E1067", {"start": v(-11780.57, -615.34) * mm, "end": v(-11767.76, -637.1) * mm});
            skLineSegment(sketch, "E1068", {"start": v(-11767.76, -637.1) * mm, "end": v(-11754.16, -659.28) * mm});
            skLineSegment(sketch, "E1069", {"start": v(-11754.16, -659.28) * mm, "end": v(-11739.66, -667.61) * mm});
            skLineSegment(sketch, "E1070", {"start": v(-11739.66, -667.61) * mm, "end": v(-11601.82, -664.86) * mm});
            skLineSegment(sketch, "E1071", {"start": v(-11601.82, -664.86) * mm, "end": v(-11587.66, -655.96) * mm});
            skLineSegment(sketch, "E1072", {"start": v(-11587.66, -655.96) * mm, "end": v(-11574.95, -633.26) * mm});
            skLineSegment(sketch, "E1073", {"start": v(-11574.95, -633.26) * mm, "end": v(-11563.02, -611) * mm});
            skLineSegment(sketch, "E1074", {"start": v(-11563.02, -611) * mm, "end": v(-11551.84, -589.2) * mm});
            skLineSegment(sketch, "E1075", {"start": v(-11551.84, -589.2) * mm, "end": v(-11541.4, -567.86) * mm});
            skLineSegment(sketch, "E1076", {"start": v(-11541.4, -567.86) * mm, "end": v(-11531.67, -547.03) * mm});
            skLineSegment(sketch, "E1077", {"start": v(-11531.67, -547.03) * mm, "end": v(-11522.63, -526.7) * mm});
            skLineSegment(sketch, "E1078", {"start": v(-11522.63, -526.7) * mm, "end": v(-11514.26, -506.92) * mm});
            skLineSegment(sketch, "E1079", {"start": v(-11514.26, -506.92) * mm, "end": v(-11506.54, -487.68) * mm});
            skLineSegment(sketch, "E1080", {"start": v(-11506.54, -487.68) * mm, "end": v(-11499.44, -469.02) * mm});
            skLineSegment(sketch, "E1081", {"start": v(-11499.44, -469.02) * mm, "end": v(-11492.94, -450.93) * mm});
            skLineSegment(sketch, "E1082", {"start": v(-11492.94, -450.93) * mm, "end": v(-11487.01, -433.44) * mm});
            skLineSegment(sketch, "E1083", {"start": v(-11487.01, -433.44) * mm, "end": v(-11481.64, -416.57) * mm});
            skLineSegment(sketch, "E1084", {"start": v(-11481.64, -416.57) * mm, "end": v(-11476.8, -400.33) * mm});
            skLineSegment(sketch, "E1085", {"start": v(-11476.8, -400.33) * mm, "end": v(-11472.45, -384.72) * mm});
            skLineSegment(sketch, "E1086", {"start": v(-11472.45, -384.72) * mm, "end": v(-11468.58, -369.77) * mm});
            skLineSegment(sketch, "E1087", {"start": v(-11468.58, -369.77) * mm, "end": v(-11465.16, -355.49) * mm});
            skLineSegment(sketch, "E1088", {"start": v(-11465.16, -355.49) * mm, "end": v(-11462.17, -341.88) * mm});
            skLineSegment(sketch, "E1089", {"start": v(-11462.17, -341.88) * mm, "end": v(-11459.57, -328.96) * mm});
            skLineSegment(sketch, "E1090", {"start": v(-11459.57, -328.96) * mm, "end": v(-11457.35, -316.74) * mm});
            skLineSegment(sketch, "E1091", {"start": v(-11457.35, -316.74) * mm, "end": v(-11455.48, -305.23) * mm});
            skLineSegment(sketch, "E1092", {"start": v(-11455.48, -305.23) * mm, "end": v(-11453.92, -294.43) * mm});
            skLineSegment(sketch, "E1093", {"start": v(-11453.92, -294.43) * mm, "end": v(-11452.66, -284.35) * mm});
            skLineSegment(sketch, "E1094", {"start": v(-11452.66, -284.35) * mm, "end": v(-11451.66, -275) * mm});
            skLineSegment(sketch, "E1095", {"start": v(-11451.66, -275) * mm, "end": v(-11450.9, -266.39) * mm});
            skLineSegment(sketch, "E1096", {"start": v(-11450.9, -266.39) * mm, "end": v(-11450.36, -258.51) * mm});
            skLineSegment(sketch, "E1097", {"start": v(-11450.36, -258.51) * mm, "end": v(-11450, -251.39) * mm});
            skLineSegment(sketch, "E1098", {"start": v(-11450, -251.39) * mm, "end": v(-11449.78, -245) * mm});
            skLineSegment(sketch, "E1099", {"start": v(-11449.78, -245) * mm, "end": v(-11449.7, -239.38) * mm});
            skLineSegment(sketch, "E1100", {"start": v(-11449.7, -239.38) * mm, "end": v(-11449.72, -234.51) * mm});
            skLineSegment(sketch, "E1101", {"start": v(-11449.72, -234.51) * mm, "end": v(-11449.8, -230.4) * mm});
            skLineSegment(sketch, "E1102", {"start": v(-11449.8, -230.4) * mm, "end": v(-11449.95, -227.04) * mm});
            skLineSegment(sketch, "E1103", {"start": v(-11449.95, -227.04) * mm, "end": v(-11450.1, -224.44) * mm});
            skLineSegment(sketch, "E1104", {"start": v(-11450.1, -224.44) * mm, "end": v(-11450.24, -222.6) * mm});
            skLineSegment(sketch, "E1105", {"start": v(-11450.24, -222.6) * mm, "end": v(-11450.34, -221.5) * mm});
            skLineSegment(sketch, "E1106", {"start": v(-11450.34, -221.5) * mm, "end": v(-11464.61, -105.65) * mm});
            skLineSegment(sketch, "E1107", {"start": v(-11464.61, -105.65) * mm, "end": v(-11203.26, -56.66) * mm});
            skLineSegment(sketch, "E1108", {"start": v(-11203.26, -56.66) * mm, "end": v(-11174.6, -169.82) * mm});
            skLineSegment(sketch, "E1109", {"start": v(-11174.6, -169.82) * mm, "end": v(-11174.3, -170.87) * mm});
            skLineSegment(sketch, "E1110", {"start": v(-11174.3, -170.87) * mm, "end": v(-11173.77, -172.65) * mm});
            skLineSegment(sketch, "E1111", {"start": v(-11173.77, -172.65) * mm, "end": v(-11172.97, -175.12) * mm});
            skLineSegment(sketch, "E1112", {"start": v(-11172.97, -175.12) * mm, "end": v(-11171.88, -178.3) * mm});
            skLineSegment(sketch, "E1113", {"start": v(-11171.88, -178.3) * mm, "end": v(-11170.48, -182.17) * mm});
            skLineSegment(sketch, "E1114", {"start": v(-11170.48, -182.17) * mm, "end": v(-11168.73, -186.72) * mm});
            skLineSegment(sketch, "E1115", {"start": v(-11168.73, -186.72) * mm, "end": v(-11166.62, -191.93) * mm});
            skLineSegment(sketch, "E1116", {"start": v(-11166.62, -191.93) * mm, "end": v(-11164.11, -197.8) * mm});
            skLineSegment(sketch, "E1117", {"start": v(-11164.11, -197.8) * mm, "end": v(-11161.2, -204.31) * mm});
            skLineSegment(sketch, "E1118", {"start": v(-11161.2, -204.31) * mm, "end": v(-11157.83, -211.45) * mm});
            skLineSegment(sketch, "E1119", {"start": v(-11157.83, -211.45) * mm, "end": v(-11154, -219.2) * mm});
            skLineSegment(sketch, "E1120", {"start": v(-11154, -219.2) * mm, "end": v(-11149.68, -227.56) * mm});
            skLineSegment(sketch, "E1121", {"start": v(-11149.68, -227.56) * mm, "end": v(-11144.86, -236.5) * mm});
            skLineSegment(sketch, "E1122", {"start": v(-11144.86, -236.5) * mm, "end": v(-11139.5, -246) * mm});
            skLineSegment(sketch, "E1123", {"start": v(-11139.5, -246) * mm, "end": v(-11133.58, -256.05) * mm});
            skLineSegment(sketch, "E1124", {"start": v(-11133.58, -256.05) * mm, "end": v(-11127.08, -266.64) * mm});
            skLineSegment(sketch, "E1125", {"start": v(-11127.08, -266.64) * mm, "end": v(-11119.99, -277.74) * mm});
            skLineSegment(sketch, "E1126", {"start": v(-11119.99, -277.74) * mm, "end": v(-11112.27, -289.34) * mm});
            skLineSegment(sketch, "E1127", {"start": v(-11112.27, -289.34) * mm, "end": v(-11103.91, -301.42) * mm});
            skLineSegment(sketch, "E1128", {"start": v(-11103.91, -301.42) * mm, "end": v(-11094.89, -313.95) * mm});
            skLineSegment(sketch, "E1129", {"start": v(-11094.89, -313.95) * mm, "end": v(-11085.19, -326.92) * mm});
            skLineSegment(sketch, "E1130", {"start": v(-11085.19, -326.92) * mm, "end": v(-11074.79, -340.31) * mm});
            skLineSegment(sketch, "E1131", {"start": v(-11074.79, -340.31) * mm, "end": v(-11063.67, -354.1) * mm});
            skLineSegment(sketch, "E1132", {"start": v(-11063.67, -354.1) * mm, "end": v(-11051.81, -368.25) * mm});
            skLineSegment(sketch, "E1133", {"start": v(-11051.81, -368.25) * mm, "end": v(-11039.2, -382.75) * mm});
            skLineSegment(sketch, "E1134", {"start": v(-11039.2, -382.75) * mm, "end": v(-11025.82, -397.58) * mm});
            skLineSegment(sketch, "E1135", {"start": v(-11025.82, -397.58) * mm, "end": v(-11011.66, -412.71) * mm});
            skLineSegment(sketch, "E1136", {"start": v(-11011.66, -412.71) * mm, "end": v(-10996.7, -428.12) * mm});
            skLineSegment(sketch, "E1137", {"start": v(-10996.7, -428.12) * mm, "end": v(-10980.9, -443.79) * mm});
            skLineSegment(sketch, "E1138", {"start": v(-10980.9, -443.79) * mm, "end": v(-10964.3, -459.69) * mm});
            skLineSegment(sketch, "E1139", {"start": v(-10964.3, -459.69) * mm, "end": v(-10946.83, -475.79) * mm});
            skLineSegment(sketch, "E1140", {"start": v(-10946.83, -475.79) * mm, "end": v(-10928.52, -492.06) * mm});
            skLineSegment(sketch, "E1141", {"start": v(-10928.52, -492.06) * mm, "end": v(-10909.33, -508.5) * mm});
            skLineSegment(sketch, "E1142", {"start": v(-10909.33, -508.5) * mm, "end": v(-10889.27, -525.05) * mm});
            skLineSegment(sketch, "E1143", {"start": v(-10889.27, -525.05) * mm, "end": v(-10872.85, -528.22) * mm});
            skLineSegment(sketch, "E1144", {"start": v(-10872.85, -528.22) * mm, "end": v(-10743.36, -480.86) * mm});
            skLineSegment(sketch, "E1145", {"start": v(-10743.36, -480.86) * mm, "end": v(-10732.87, -467.85) * mm});
            skLineSegment(sketch, "E1146", {"start": v(-10732.87, -467.85) * mm, "end": v(-10728.22, -442.25) * mm});
            skLineSegment(sketch, "E1147", {"start": v(-10728.22, -442.25) * mm, "end": v(-10724.16, -417.32) * mm});
            skLineSegment(sketch, "E1148", {"start": v(-10724.16, -417.32) * mm, "end": v(-10720.67, -393.06) * mm});
            skLineSegment(sketch, "E1149", {"start": v(-10720.67, -393.06) * mm, "end": v(-10717.72, -369.5) * mm});
            skLineSegment(sketch, "E1150", {"start": v(-10717.72, -369.5) * mm, "end": v(-10715.28, -346.64) * mm});
            skLineSegment(sketch, "E1151", {"start": v(-10715.28, -346.64) * mm, "end": v(-10713.33, -324.48) * mm});
            skLineSegment(sketch, "E1152", {"start": v(-10713.33, -324.48) * mm, "end": v(-10711.84, -303.05) * mm});
            skLineSegment(sketch, "E1153", {"start": v(-10711.84, -303.05) * mm, "end": v(-10710.78, -282.35) * mm});
            skLineSegment(sketch, "E1154", {"start": v(-10710.78, -282.35) * mm, "end": v(-10710.12, -262.39) * mm});
            skLineSegment(sketch, "E1155", {"start": v(-10710.12, -262.39) * mm, "end": v(-10709.85, -243.17) * mm});
            skLineSegment(sketch, "E1156", {"start": v(-10709.85, -243.17) * mm, "end": v(-10709.92, -224.7) * mm});
            skLineSegment(sketch, "E1157", {"start": v(-10709.92, -224.7) * mm, "end": v(-10710.32, -207) * mm});
            skLineSegment(sketch, "E1158", {"start": v(-10710.32, -207) * mm, "end": v(-10711, -190.07) * mm});
            skLineSegment(sketch, "E1159", {"start": v(-10711, -190.07) * mm, "end": v(-10711.97, -173.9) * mm});
            skLineSegment(sketch, "E1160", {"start": v(-10711.97, -173.9) * mm, "end": v(-10713.16, -158.5) * mm});
            skLineSegment(sketch, "E1161", {"start": v(-10713.16, -158.5) * mm, "end": v(-10714.57, -143.88) * mm});
            skLineSegment(sketch, "E1162", {"start": v(-10714.57, -143.88) * mm, "end": v(-10716.16, -130.04) * mm});
            skLineSegment(sketch, "E1163", {"start": v(-10716.16, -130.04) * mm, "end": v(-10717.9, -116.98) * mm});
            skLineSegment(sketch, "E1164", {"start": v(-10717.9, -116.98) * mm, "end": v(-10719.76, -104.7) * mm});
            skLineSegment(sketch, "E1165", {"start": v(-10719.76, -104.7) * mm, "end": v(-10721.73, -93.2) * mm});
            skLineSegment(sketch, "E1166", {"start": v(-10721.73, -93.2) * mm, "end": v(-10723.77, -82.48) * mm});
            skLineSegment(sketch, "E1167", {"start": v(-10723.77, -82.48) * mm, "end": v(-10725.84, -72.54) * mm});
            skLineSegment(sketch, "E1168", {"start": v(-10725.84, -72.54) * mm, "end": v(-10727.94, -63.37) * mm});
            skLineSegment(sketch, "E1169", {"start": v(-10727.94, -63.37) * mm, "end": v(-10730.02, -54.98) * mm});
            skLineSegment(sketch, "E1170", {"start": v(-10730.02, -54.98) * mm, "end": v(-10732.05, -47.35) * mm});
            skLineSegment(sketch, "E1171", {"start": v(-10732.05, -47.35) * mm, "end": v(-10734.02, -40.5) * mm});
            skLineSegment(sketch, "E1172", {"start": v(-10734.02, -40.5) * mm, "end": v(-10735.9, -34.4) * mm});
            skLineSegment(sketch, "E1173", {"start": v(-10735.9, -34.4) * mm, "end": v(-10737.64, -29.05) * mm});
            skLineSegment(sketch, "E1174", {"start": v(-10737.64, -29.05) * mm, "end": v(-10739.24, -24.45) * mm});
            skLineSegment(sketch, "E1175", {"start": v(-10739.24, -24.45) * mm, "end": v(-10740.66, -20.58) * mm});
            skLineSegment(sketch, "E1176", {"start": v(-10740.66, -20.58) * mm, "end": v(-10741.88, -17.45) * mm});
            skLineSegment(sketch, "E1177", {"start": v(-10741.88, -17.45) * mm, "end": v(-10742.87, -15.04) * mm});
            skLineSegment(sketch, "E1178", {"start": v(-10742.87, -15.04) * mm, "end": v(-10743.6, -13.34) * mm});
            skLineSegment(sketch, "E1179", {"start": v(-10743.6, -13.34) * mm, "end": v(-10744.06, -12.35) * mm});
            skLineSegment(sketch, "E1180", {"start": v(-10744.06, -12.35) * mm, "end": v(-10795.17, 92.6) * mm});
            skLineSegment(sketch, "E1181", {"start": v(-10795.17, 92.6) * mm, "end": v(-10563.9, 223.8) * mm});
            skLineSegment(sketch, "E1182", {"start": v(-10563.9, 223.8) * mm, "end": v(-10500.04, 126.07) * mm});
            skLineSegment(sketch, "E1183", {"start": v(-10500.04, 126.07) * mm, "end": v(-10499.42, 125.17) * mm});
            skLineSegment(sketch, "E1184", {"start": v(-10499.42, 125.17) * mm, "end": v(-10498.34, 123.67) * mm});
            skLineSegment(sketch, "E1185", {"start": v(-10498.34, 123.67) * mm, "end": v(-10496.77, 121.59) * mm});
            skLineSegment(sketch, "E1186", {"start": v(-10496.77, 121.59) * mm, "end": v(-10494.71, 118.93) * mm});
            skLineSegment(sketch, "E1187", {"start": v(-10494.71, 118.93) * mm, "end": v(-10492.13, 115.73) * mm});
            skLineSegment(sketch, "E1188", {"start": v(-10492.13, 115.73) * mm, "end": v(-10489, 112) * mm});
            skLineSegment(sketch, "E1189", {"start": v(-10489, 112) * mm, "end": v(-10485.3, 107.75) * mm});
            skLineSegment(sketch, "E1190", {"start": v(-10485.3, 107.75) * mm, "end": v(-10481.03, 103.01) * mm});
            skLineSegment(sketch, "E1191", {"start": v(-10481.03, 103.01) * mm, "end": v(-10476.15, 97.8) * mm});
            skLineSegment(sketch, "E1192", {"start": v(-10476.15, 97.8) * mm, "end": v(-10470.66, 92.14) * mm});
            skLineSegment(sketch, "E1193", {"start": v(-10470.66, 92.14) * mm, "end": v(-10464.52, 86.05) * mm});
            skLineSegment(sketch, "E1194", {"start": v(-10464.52, 86.05) * mm, "end": v(-10457.73, 79.56) * mm});
            skLineSegment(sketch, "E1195", {"start": v(-10457.73, 79.56) * mm, "end": v(-10450.26, 72.67) * mm});
            skLineSegment(sketch, "E1196", {"start": v(-10450.26, 72.67) * mm, "end": v(-10442.1, 65.42) * mm});
            skLineSegment(sketch, "E1197", {"start": v(-10442.1, 65.42) * mm, "end": v(-10433.24, 57.83) * mm});
            skLineSegment(sketch, "E1198", {"start": v(-10433.24, 57.83) * mm, "end": v(-10423.66, 49.93) * mm});
            skLineSegment(sketch, "E1199", {"start": v(-10423.66, 49.93) * mm, "end": v(-10413.34, 41.73) * mm});
            skLineSegment(sketch, "E1200", {"start": v(-10413.34, 41.73) * mm, "end": v(-10402.27, 33.27) * mm});
            skLineSegment(sketch, "E1201", {"start": v(-10402.27, 33.27) * mm, "end": v(-10390.45, 24.56) * mm});
            skLineSegment(sketch, "E1202", {"start": v(-10390.45, 24.56) * mm, "end": v(-10377.85, 15.63) * mm});
            skLineSegment(sketch, "E1203", {"start": v(-10377.85, 15.63) * mm, "end": v(-10364.46, 6.51) * mm});
            skLineSegment(sketch, "E1204", {"start": v(-10364.46, 6.51) * mm, "end": v(-10350.27, -2.77) * mm});
            skLineSegment(sketch, "E1205", {"start": v(-10350.27, -2.77) * mm, "end": v(-10335.28, -12.2) * mm});
            skLineSegment(sketch, "E1206", {"start": v(-10335.28, -12.2) * mm, "end": v(-10319.47, -21.73) * mm});
            skLineSegment(sketch, "E1207", {"start": v(-10319.47, -21.73) * mm, "end": v(-10302.84, -31.35) * mm});
            skLineSegment(sketch, "E1208", {"start": v(-10302.84, -31.35) * mm, "end": v(-10285.37, -41.04) * mm});
            skLineSegment(sketch, "E1209", {"start": v(-10285.37, -41.04) * mm, "end": v(-10267.06, -50.75) * mm});
            skLineSegment(sketch, "E1210", {"start": v(-10267.06, -50.75) * mm, "end": v(-10247.9, -60.47) * mm});
            skLineSegment(sketch, "E1211", {"start": v(-10247.9, -60.47) * mm, "end": v(-10227.88, -70.16) * mm});
            skLineSegment(sketch, "E1212", {"start": v(-10227.88, -70.16) * mm, "end": v(-10207, -79.8) * mm});
            skLineSegment(sketch, "E1213", {"start": v(-10207, -79.8) * mm, "end": v(-10185.27, -89.36) * mm});
            skLineSegment(sketch, "E1214", {"start": v(-10185.27, -89.36) * mm, "end": v(-10162.66, -98.8) * mm});
            skLineSegment(sketch, "E1215", {"start": v(-10162.66, -98.8) * mm, "end": v(-10139.18, -108.12) * mm});
            skLineSegment(sketch, "E1216", {"start": v(-10139.18, -108.12) * mm, "end": v(-10114.82, -117.26) * mm});
            skLineSegment(sketch, "E1217", {"start": v(-10114.82, -117.26) * mm, "end": v(-10098.26, -114.93) * mm});
            skLineSegment(sketch, "E1218", {"start": v(-10098.26, -114.93) * mm, "end": v(-9991.17, -28.1) * mm});
            skLineSegment(sketch, "E1219", {"start": v(-9991.17, -28.1) * mm, "end": v(-9985.47, -12.37) * mm});
            skLineSegment(sketch, "E1220", {"start": v(-9985.47, -12.37) * mm, "end": v(-9989.38, 13.35) * mm});
            skLineSegment(sketch, "E1221", {"start": v(-9989.38, 13.35) * mm, "end": v(-9993.64, 38.24) * mm});
            skLineSegment(sketch, "E1222", {"start": v(-9993.64, 38.24) * mm, "end": v(-9998.21, 62.32) * mm});
            skLineSegment(sketch, "E1223", {"start": v(-9998.21, 62.32) * mm, "end": v(-10003.07, 85.56) * mm});
            skLineSegment(sketch, "E1224", {"start": v(-10003.07, 85.56) * mm, "end": v(-10008.2, 107.98) * mm});
            skLineSegment(sketch, "E1225", {"start": v(-10008.2, 107.98) * mm, "end": v(-10013.54, 129.57) * mm});
            skLineSegment(sketch, "E1226", {"start": v(-10013.54, 129.57) * mm, "end": v(-10019.09, 150.32) * mm});
            skLineSegment(sketch, "E1227", {"start": v(-10019.09, 150.32) * mm, "end": v(-10024.8, 170.24) * mm});
            skLineSegment(sketch, "E1228", {"start": v(-10024.8, 170.24) * mm, "end": v(-10030.67, 189.34) * mm});
            skLineSegment(sketch, "E1229", {"start": v(-10030.67, 189.34) * mm, "end": v(-10036.65, 207.6) * mm});
            skLineSegment(sketch, "E1230", {"start": v(-10036.65, 207.6) * mm, "end": v(-10042.71, 225.04) * mm});
            skLineSegment(sketch, "E1231", {"start": v(-10042.71, 225.04) * mm, "end": v(-10048.84, 241.65) * mm});
            skLineSegment(sketch, "E1232", {"start": v(-10048.84, 241.65) * mm, "end": v(-10055, 257.45) * mm});
            skLineSegment(sketch, "E1233", {"start": v(-10055, 257.45) * mm, "end": v(-10061.15, 272.44) * mm});
            skLineSegment(sketch, "E1234", {"start": v(-10061.15, 272.44) * mm, "end": v(-10067.28, 286.6) * mm});
            skLineSegment(sketch, "E1235", {"start": v(-10067.28, 286.6) * mm, "end": v(-10073.35, 299.98) * mm});
            skLineSegment(sketch, "E1236", {"start": v(-10073.35, 299.98) * mm, "end": v(-10079.35, 312.56) * mm});
            skLineSegment(sketch, "E1237", {"start": v(-10079.35, 312.56) * mm, "end": v(-10085.24, 324.34) * mm});
            skLineSegment(sketch, "E1238", {"start": v(-10085.24, 324.34) * mm, "end": v(-10091, 335.35) * mm});
            skLineSegment(sketch, "E1239", {"start": v(-10091, 335.35) * mm, "end": v(-10096.58, 345.6) * mm});
            skLineSegment(sketch, "E1240", {"start": v(-10096.58, 345.6) * mm, "end": v(-10102, 355.07) * mm});
            skLineSegment(sketch, "E1241", {"start": v(-10102, 355.07) * mm, "end": v(-10107.19, 363.8) * mm});
            skLineSegment(sketch, "E1242", {"start": v(-10107.19, 363.8) * mm, "end": v(-10112.14, 371.79) * mm});
            skLineSegment(sketch, "E1243", {"start": v(-10112.14, 371.79) * mm, "end": v(-10116.83, 379.05) * mm});
            skLineSegment(sketch, "E1244", {"start": v(-10116.83, 379.05) * mm, "end": v(-10121.23, 385.6) * mm});
            skLineSegment(sketch, "E1245", {"start": v(-10121.23, 385.6) * mm, "end": v(-10125.32, 391.45) * mm});
            skLineSegment(sketch, "E1246", {"start": v(-10125.32, 391.45) * mm, "end": v(-10129.07, 396.6) * mm});
            skLineSegment(sketch, "E1247", {"start": v(-10129.07, 396.6) * mm, "end": v(-10132.47, 401.1) * mm});
            skLineSegment(sketch, "E1248", {"start": v(-10132.47, 401.1) * mm, "end": v(-10135.47, 404.93) * mm});
            skLineSegment(sketch, "E1249", {"start": v(-10135.47, 404.93) * mm, "end": v(-10138.07, 408.12) * mm});
            skLineSegment(sketch, "E1250", {"start": v(-10138.07, 408.12) * mm, "end": v(-10140.24, 410.69) * mm});
            skLineSegment(sketch, "E1251", {"start": v(-10140.24, 410.69) * mm, "end": v(-10141.96, 412.65) * mm});
            skLineSegment(sketch, "E1252", {"start": v(-10141.96, 412.65) * mm, "end": v(-10143.2, 414.02) * mm});
            skLineSegment(sketch, "E1253", {"start": v(-10143.2, 414.02) * mm, "end": v(-10143.95, 414.81) * mm});
            skLineSegment(sketch, "E1254", {"start": v(-10143.95, 414.81) * mm, "end": v(-10226.38, 497.48) * mm});
            skLineSegment(sketch, "E1255", {"start": v(-10226.38, 497.48) * mm, "end": v(-10050.23, 696.66) * mm});
            skLineSegment(sketch, "E1256", {"start": v(-10050.23, 696.66) * mm, "end": v(-9958.1, 624.96) * mm});
            skLineSegment(sketch, "E1257", {"start": v(-9958.1, 624.96) * mm, "end": v(-9957.22, 624.31) * mm});
            skLineSegment(sketch, "E1258", {"start": v(-9957.22, 624.31) * mm, "end": v(-9955.71, 623.24) * mm});
            skLineSegment(sketch, "E1259", {"start": v(-9955.71, 623.24) * mm, "end": v(-9953.56, 621.78) * mm});
            skLineSegment(sketch, "E1260", {"start": v(-9953.56, 621.78) * mm, "end": v(-9950.74, 619.94) * mm});
            skLineSegment(sketch, "E1261", {"start": v(-9950.74, 619.94) * mm, "end": v(-9947.26, 617.75) * mm});
            skLineSegment(sketch, "E1262", {"start": v(-9947.26, 617.75) * mm, "end": v(-9943.09, 615.24) * mm});
            skLineSegment(sketch, "E1263", {"start": v(-9943.09, 615.24) * mm, "end": v(-9938.22, 612.42) * mm});
            skLineSegment(sketch, "E1264", {"start": v(-9938.22, 612.42) * mm, "end": v(-9932.64, 609.33) * mm});
            skLineSegment(sketch, "E1265", {"start": v(-9932.64, 609.33) * mm, "end": v(-9926.33, 605.98) * mm});
            skLineSegment(sketch, "E1266", {"start": v(-9926.33, 605.98) * mm, "end": v(-9919.3, 602.41) * mm});
            skLineSegment(sketch, "E1267", {"start": v(-9919.3, 602.41) * mm, "end": v(-9911.51, 598.65) * mm});
            skLineSegment(sketch, "E1268", {"start": v(-9911.51, 598.65) * mm, "end": v(-9902.98, 594.7) * mm});
            skLineSegment(sketch, "E1269", {"start": v(-9902.98, 594.7) * mm, "end": v(-9893.68, 590.62) * mm});
            skLineSegment(sketch, "E1270", {"start": v(-9893.68, 590.62) * mm, "end": v(-9883.61, 586.41) * mm});
            skLineSegment(sketch, "E1271", {"start": v(-9883.61, 586.41) * mm, "end": v(-9872.77, 582.11) * mm});
            skLineSegment(sketch, "E1272", {"start": v(-9872.77, 582.11) * mm, "end": v(-9861.13, 577.75) * mm});
            skLineSegment(sketch, "E1273", {"start": v(-9861.13, 577.75) * mm, "end": v(-9848.72, 573.34) * mm});
            skLineSegment(sketch, "E1274", {"start": v(-9848.72, 573.34) * mm, "end": v(-9835.5, 568.93) * mm});
            skLineSegment(sketch, "E1275", {"start": v(-9835.5, 568.93) * mm, "end": v(-9821.49, 564.53) * mm});
            skLineSegment(sketch, "E1276", {"start": v(-9821.49, 564.53) * mm, "end": v(-9806.67, 560.18) * mm});
            skLineSegment(sketch, "E1277", {"start": v(-9806.67, 560.18) * mm, "end": v(-9791.05, 555.9) * mm});
            skLineSegment(sketch, "E1278", {"start": v(-9791.05, 555.9) * mm, "end": v(-9774.62, 551.73) * mm});
            skLineSegment(sketch, "E1279", {"start": v(-9774.62, 551.73) * mm, "end": v(-9757.38, 547.68) * mm});
            skLineSegment(sketch, "E1280", {"start": v(-9757.38, 547.68) * mm, "end": v(-9739.33, 543.8) * mm});
            skLineSegment(sketch, "E1281", {"start": v(-9739.33, 543.8) * mm, "end": v(-9720.47, 540.1) * mm});
            skLineSegment(sketch, "E1282", {"start": v(-9720.47, 540.1) * mm, "end": v(-9700.8, 536.6) * mm});
            skLineSegment(sketch, "E1283", {"start": v(-9700.8, 536.6) * mm, "end": v(-9680.33, 533.37) * mm});
            skLineSegment(sketch, "E1284", {"start": v(-9680.33, 533.37) * mm, "end": v(-9659.05, 530.4) * mm});
            skLineSegment(sketch, "E1285", {"start": v(-9659.05, 530.4) * mm, "end": v(-9636.97, 527.73) * mm});
            skLineSegment(sketch, "E1286", {"start": v(-9636.97, 527.73) * mm, "end": v(-9614.1, 525.4) * mm});
            skLineSegment(sketch, "E1287", {"start": v(-9614.1, 525.4) * mm, "end": v(-9590.43, 523.4) * mm});
            skLineSegment(sketch, "E1288", {"start": v(-9590.43, 523.4) * mm, "end": v(-9565.98, 521.81) * mm});
            skLineSegment(sketch, "E1289", {"start": v(-9565.98, 521.81) * mm, "end": v(-9540.75, 520.63) * mm});
            skLineSegment(sketch, "E1290", {"start": v(-9540.75, 520.63) * mm, "end": v(-9514.75, 519.9) * mm});
            skLineSegment(sketch, "E1291", {"start": v(-9514.75, 519.9) * mm, "end": v(-9499.84, 527.48) * mm});
            skLineSegment(sketch, "E1292", {"start": v(-9499.84, 527.48) * mm, "end": v(-9426.75, 644.38) * mm});
            skLineSegment(sketch, "E1293", {"start": v(-9426.75, 644.38) * mm, "end": v(-9426.46, 661.1) * mm});
            skLineSegment(sketch, "E1294", {"start": v(-9426.46, 661.1) * mm, "end": v(-9438.51, 684.15) * mm});
            skLineSegment(sketch, "E1295", {"start": v(-9438.51, 684.15) * mm, "end": v(-9450.62, 706.32) * mm});
            skLineSegment(sketch, "E1296", {"start": v(-9450.62, 706.32) * mm, "end": v(-9462.77, 727.6) * mm});
            skLineSegment(sketch, "E1297", {"start": v(-9462.77, 727.6) * mm, "end": v(-9474.91, 748.01) * mm});
            skLineSegment(sketch, "E1298", {"start": v(-9474.91, 748.01) * mm, "end": v(-9487.03, 767.55) * mm});
            skLineSegment(sketch, "E1299", {"start": v(-9487.03, 767.55) * mm, "end": v(-9499.1, 786.23) * mm});
            skLineSegment(sketch, "E1300", {"start": v(-9499.1, 786.23) * mm, "end": v(-9511.08, 804.06) * mm});
            skLineSegment(sketch, "E1301", {"start": v(-9511.08, 804.06) * mm, "end": v(-9522.96, 821.05) * mm});
            skLineSegment(sketch, "E1302", {"start": v(-9522.96, 821.05) * mm, "end": v(-9534.7, 837.2) * mm});
            skLineSegment(sketch, "E1303", {"start": v(-9534.7, 837.2) * mm, "end": v(-9546.3, 852.54) * mm});
            skLineSegment(sketch, "E1304", {"start": v(-9546.3, 852.54) * mm, "end": v(-9557.7, 867.06) * mm});
            skLineSegment(sketch, "E1305", {"start": v(-9557.7, 867.06) * mm, "end": v(-9568.88, 880.79) * mm});
            skLineSegment(sketch, "E1306", {"start": v(-9568.88, 880.79) * mm, "end": v(-9579.83, 893.73) * mm});
            skLineSegment(sketch, "E1307", {"start": v(-9579.83, 893.73) * mm, "end": v(-9590.51, 905.9) * mm});
            skLineSegment(sketch, "E1308", {"start": v(-9590.51, 905.9) * mm, "end": v(-9600.91, 917.32) * mm});
            skLineSegment(sketch, "E1309", {"start": v(-9600.91, 917.32) * mm, "end": v(-9611, 928) * mm});
            skLineSegment(sketch, "E1310", {"start": v(-9611, 928) * mm, "end": v(-9620.76, 937.94) * mm});
            skLineSegment(sketch, "E1311", {"start": v(-9620.76, 937.94) * mm, "end": v(-9630.16, 947.18) * mm});
            skLineSegment(sketch, "E1312", {"start": v(-9630.16, 947.18) * mm, "end": v(-9639.17, 955.72) * mm});
            skLineSegment(sketch, "E1313", {"start": v(-9639.17, 955.72) * mm, "end": v(-9647.79, 963.59) * mm});
            skLineSegment(sketch, "E1314", {"start": v(-9647.79, 963.59) * mm, "end": v(-9655.98, 970.8) * mm});
            skLineSegment(sketch, "E1315", {"start": v(-9655.98, 970.8) * mm, "end": v(-9663.72, 977.37) * mm});
            skLineSegment(sketch, "E1316", {"start": v(-9663.72, 977.37) * mm, "end": v(-9671, 983.31) * mm});
            skLineSegment(sketch, "E1317", {"start": v(-9671, 983.31) * mm, "end": v(-9677.8, 988.66) * mm});
            skLineSegment(sketch, "E1318", {"start": v(-9677.8, 988.66) * mm, "end": v(-9684.09, 993.43) * mm});
            skLineSegment(sketch, "E1319", {"start": v(-9684.09, 993.43) * mm, "end": v(-9689.86, 997.63) * mm});
            skLineSegment(sketch, "E1320", {"start": v(-9689.86, 997.63) * mm, "end": v(-9695.08, 1001.3) * mm});
            skLineSegment(sketch, "E1321", {"start": v(-9695.08, 1001.3) * mm, "end": v(-9699.75, 1004.44) * mm});
            skLineSegment(sketch, "E1322", {"start": v(-9699.75, 1004.44) * mm, "end": v(-9703.83, 1007.09) * mm});
            skLineSegment(sketch, "E1323", {"start": v(-9703.83, 1007.09) * mm, "end": v(-9707.33, 1009.26) * mm});
            skLineSegment(sketch, "E1324", {"start": v(-9707.33, 1009.26) * mm, "end": v(-9710.21, 1010.98) * mm});
            skLineSegment(sketch, "E1325", {"start": v(-9710.21, 1010.98) * mm, "end": v(-9712.47, 1012.28) * mm});
            skLineSegment(sketch, "E1326", {"start": v(-9712.47, 1012.28) * mm, "end": v(-9714.1, 1013.17) * mm});
            skLineSegment(sketch, "E1327", {"start": v(-9714.1, 1013.17) * mm, "end": v(-9715.06, 1013.68) * mm});
            skLineSegment(sketch, "E1328", {"start": v(-9715.06, 1013.68) * mm, "end": v(-9819.86, 1065.1) * mm});
            skLineSegment(sketch, "E1329", {"start": v(-9819.86, 1065.1) * mm, "end": v(-9717.93, 1310.69) * mm});
            skLineSegment(sketch, "E1330", {"start": v(-9717.93, 1310.69) * mm, "end": v(-9607.52, 1272.79) * mm});
            skLineSegment(sketch, "E1331", {"start": v(-9607.52, 1272.79) * mm, "end": v(-9606.47, 1272.46) * mm});
            skLineSegment(sketch, "E1332", {"start": v(-9606.47, 1272.46) * mm, "end": v(-9604.7, 1271.94) * mm});
            skLineSegment(sketch, "E1333", {"start": v(-9604.7, 1271.94) * mm, "end": v(-9602.18, 1271.25) * mm});
            skLineSegment(sketch, "E1334", {"start": v(-9602.18, 1271.25) * mm, "end": v(-9598.93, 1270.43) * mm});
            skLineSegment(sketch, "E1335", {"start": v(-9598.93, 1270.43) * mm, "end": v(-9594.92, 1269.49) * mm});
            skLineSegment(sketch, "E1336", {"start": v(-9594.92, 1269.49) * mm, "end": v(-9590.16, 1268.46) * mm});
            skLineSegment(sketch, "E1337", {"start": v(-9590.16, 1268.46) * mm, "end": v(-9584.64, 1267.38) * mm});
            skLineSegment(sketch, "E1338", {"start": v(-9584.64, 1267.38) * mm, "end": v(-9578.36, 1266.27) * mm});
            skLineSegment(sketch, "E1339", {"start": v(-9578.36, 1266.27) * mm, "end": v(-9571.3, 1265.15) * mm});
            skLineSegment(sketch, "E1340", {"start": v(-9571.3, 1265.15) * mm, "end": v(-9563.5, 1264.06) * mm});
            skLineSegment(sketch, "E1341", {"start": v(-9563.5, 1264.06) * mm, "end": v(-9554.9, 1263.03) * mm});
            skLineSegment(sketch, "E1342", {"start": v(-9554.9, 1263.03) * mm, "end": v(-9545.56, 1262.07) * mm});
            skLineSegment(sketch, "E1343", {"start": v(-9545.56, 1262.07) * mm, "end": v(-9535.43, 1261.22) * mm});
            skLineSegment(sketch, "E1344", {"start": v(-9535.43, 1261.22) * mm, "end": v(-9524.55, 1260.51) * mm});
            skLineSegment(sketch, "E1345", {"start": v(-9524.55, 1260.51) * mm, "end": v(-9512.9, 1259.97) * mm});
            skLineSegment(sketch, "E1346", {"start": v(-9512.9, 1259.97) * mm, "end": v(-9500.48, 1259.62) * mm});
            skLineSegment(sketch, "E1347", {"start": v(-9500.48, 1259.62) * mm, "end": v(-9487.3, 1259.48) * mm});
            skLineSegment(sketch, "E1348", {"start": v(-9487.3, 1259.48) * mm, "end": v(-9473.37, 1259.6) * mm});
            skLineSegment(sketch, "E1349", {"start": v(-9473.37, 1259.6) * mm, "end": v(-9458.68, 1260) * mm});
            skLineSegment(sketch, "E1350", {"start": v(-9458.68, 1260) * mm, "end": v(-9443.26, 1260.69) * mm});
            skLineSegment(sketch, "E1351", {"start": v(-9443.26, 1260.69) * mm, "end": v(-9427.1, 1261.71) * mm});
            skLineSegment(sketch, "E1352", {"start": v(-9427.1, 1261.71) * mm, "end": v(-9410.2, 1263.1) * mm});
            skLineSegment(sketch, "E1353", {"start": v(-9410.2, 1263.1) * mm, "end": v(-9392.58, 1264.87) * mm});
            skLineSegment(sketch, "E1354", {"start": v(-9392.58, 1264.87) * mm, "end": v(-9374.24, 1267.06) * mm});
            skLineSegment(sketch, "E1355", {"start": v(-9374.24, 1267.06) * mm, "end": v(-9355.2, 1269.68) * mm});
            skLineSegment(sketch, "E1356", {"start": v(-9355.2, 1269.68) * mm, "end": v(-9335.47, 1272.77) * mm});
            skLineSegment(sketch, "E1357", {"start": v(-9335.47, 1272.77) * mm, "end": v(-9315.06, 1276.35) * mm});
            skLineSegment(sketch, "E1358", {"start": v(-9315.06, 1276.35) * mm, "end": v(-9293.97, 1280.45) * mm});
            skLineSegment(sketch, "E1359", {"start": v(-9293.97, 1280.45) * mm, "end": v(-9272.22, 1285.1) * mm});
            skLineSegment(sketch, "E1360", {"start": v(-9272.22, 1285.1) * mm, "end": v(-9249.82, 1290.31) * mm});
            skLineSegment(sketch, "E1361", {"start": v(-9249.82, 1290.31) * mm, "end": v(-9226.8, 1296.12) * mm});
            skLineSegment(sketch, "E1362", {"start": v(-9226.8, 1296.12) * mm, "end": v(-9203.15, 1302.55) * mm});
            skLineSegment(sketch, "E1363", {"start": v(-9203.15, 1302.55) * mm, "end": v(-9178.9, 1309.63) * mm});
            skLineSegment(sketch, "E1364", {"start": v(-9178.9, 1309.63) * mm, "end": v(-9154.07, 1317.37) * mm});
            skLineSegment(sketch, "E1365", {"start": v(-9154.07, 1317.37) * mm, "end": v(-9142.43, 1329.38) * mm});
            skLineSegment(sketch, "E1366", {"start": v(-9142.43, 1329.38) * mm, "end": v(-9111.26, 1463.68) * mm});
            skLineSegment(sketch, "E1367", {"start": v(-9111.26, 1463.68) * mm, "end": v(-9116.41, 1479.59) * mm});
            skLineSegment(sketch, "E1368", {"start": v(-9116.41, 1479.59) * mm, "end": v(-9135.3, 1497.48) * mm});
            skLineSegment(sketch, "E1369", {"start": v(-9135.3, 1497.48) * mm, "end": v(-9153.95, 1514.52) * mm});
            skLineSegment(sketch, "E1370", {"start": v(-9153.95, 1514.52) * mm, "end": v(-9172.35, 1530.7) * mm});
            skLineSegment(sketch, "E1371", {"start": v(-9172.35, 1530.7) * mm, "end": v(-9190.46, 1546.06) * mm});
            skLineSegment(sketch, "E1372", {"start": v(-9190.46, 1546.06) * mm, "end": v(-9208.27, 1560.6) * mm});
            skLineSegment(sketch, "E1373", {"start": v(-9208.27, 1560.6) * mm, "end": v(-9225.75, 1574.36) * mm});
            skLineSegment(sketch, "E1374", {"start": v(-9225.75, 1574.36) * mm, "end": v(-9242.87, 1587.33) * mm});
            skLineSegment(sketch, "E1375", {"start": v(-9242.87, 1587.33) * mm, "end": v(-9259.62, 1599.54) * mm});
            skLineSegment(sketch, "E1376", {"start": v(-9259.62, 1599.54) * mm, "end": v(-9275.98, 1611) * mm});
            skLineSegment(sketch, "E1377", {"start": v(-9275.98, 1611) * mm, "end": v(-9291.91, 1621.75) * mm});
            skLineSegment(sketch, "E1378", {"start": v(-9291.91, 1621.75) * mm, "end": v(-9307.41, 1631.78) * mm});
            skLineSegment(sketch, "E1379", {"start": v(-9307.41, 1631.78) * mm, "end": v(-9322.45, 1641.13) * mm});
            skLineSegment(sketch, "E1380", {"start": v(-9322.45, 1641.13) * mm, "end": v(-9337, 1649.82) * mm});
            skLineSegment(sketch, "E1381", {"start": v(-9337, 1649.82) * mm, "end": v(-9351.07, 1657.86) * mm});
            skLineSegment(sketch, "E1382", {"start": v(-9351.07, 1657.86) * mm, "end": v(-9364.61, 1665.28) * mm});
            skLineSegment(sketch, "E1383", {"start": v(-9364.61, 1665.28) * mm, "end": v(-9377.62, 1672.1) * mm});
            skLineSegment(sketch, "E1384", {"start": v(-9377.62, 1672.1) * mm, "end": v(-9390.07, 1678.34) * mm});
            skLineSegment(sketch, "E1385", {"start": v(-9390.07, 1678.34) * mm, "end": v(-9401.96, 1684.03) * mm});
            skLineSegment(sketch, "E1386", {"start": v(-9401.96, 1684.03) * mm, "end": v(-9413.27, 1689.18) * mm});
            skLineSegment(sketch, "E1387", {"start": v(-9413.27, 1689.18) * mm, "end": v(-9423.97, 1693.83) * mm});
            skLineSegment(sketch, "E1388", {"start": v(-9423.97, 1693.83) * mm, "end": v(-9434.06, 1697.99) * mm});
            skLineSegment(sketch, "E1389", {"start": v(-9434.06, 1697.99) * mm, "end": v(-9443.52, 1701.68) * mm});
            skLineSegment(sketch, "E1390", {"start": v(-9443.52, 1701.68) * mm, "end": v(-9452.33, 1704.94) * mm});
            skLineSegment(sketch, "E1391", {"start": v(-9452.33, 1704.94) * mm, "end": v(-9460.5, 1707.8) * mm});
            skLineSegment(sketch, "E1392", {"start": v(-9460.5, 1707.8) * mm, "end": v(-9468, 1710.26) * mm});
            skLineSegment(sketch, "E1393", {"start": v(-9468, 1710.26) * mm, "end": v(-9474.81, 1712.36) * mm});
            skLineSegment(sketch, "E1394", {"start": v(-9474.81, 1712.36) * mm, "end": v(-9480.94, 1714.13) * mm});
            skLineSegment(sketch, "E1395", {"start": v(-9480.94, 1714.13) * mm, "end": v(-9486.38, 1715.6) * mm});
            skLineSegment(sketch, "E1396", {"start": v(-9486.38, 1715.6) * mm, "end": v(-9491.1, 1716.77) * mm});
            skLineSegment(sketch, "E1397", {"start": v(-9491.1, 1716.77) * mm, "end": v(-9495.11, 1717.7) * mm});
            skLineSegment(sketch, "E1398", {"start": v(-9495.11, 1717.7) * mm, "end": v(-9498.4, 1718.38) * mm});
            skLineSegment(sketch, "E1399", {"start": v(-9498.4, 1718.38) * mm, "end": v(-9500.96, 1718.87) * mm});
            skLineSegment(sketch, "E1400", {"start": v(-9500.96, 1718.87) * mm, "end": v(-9502.78, 1719.19) * mm});
            skLineSegment(sketch, "E1401", {"start": v(-9502.78, 1719.19) * mm, "end": v(-9503.86, 1719.36) * mm});
            skLineSegment(sketch, "E1402", {"start": v(-9503.86, 1719.36) * mm, "end": v(-9619.68, 1733.97) * mm});
            skLineSegment(sketch, "E1403", {"start": v(-9619.68, 1733.97) * mm, "end": v(-9603.01, 1999.34) * mm});
            skLineSegment(sketch, "E1404", {"start": v(-9603.01, 1999.34) * mm, "end": v(-9486.28, 1999.35) * mm});
            skLineSegment(sketch, "E1405", {"start": v(-9486.28, 1999.35) * mm, "end": v(-9485.18, 1999.38) * mm});
            skLineSegment(sketch, "E1406", {"start": v(-11520.71, 1999.34) * mm, "end": v(-11927.11, 1999.34) * mm});
            skFitSpline(sketch, "E1407", {"points": [v(-9223.91, 2246.53) * mm, v(-9223.91, 2191.47) * mm, v(-9268.55, 2146.84) * mm, v(-9323.6, 2146.84) * mm]});
            skFitSpline(sketch, "E1408", {"points": [v(-9323.6, 2146.84) * mm, v(-9378.67, 2146.84) * mm, v(-9423.3, 2191.47) * mm, v(-9423.3, 2246.53) * mm]});
            skFitSpline(sketch, "E1409", {"points": [v(-9423.3, 2246.53) * mm, v(-9423.3, 2301.6) * mm, v(-9378.67, 2346.23) * mm, v(-9323.6, 2346.23) * mm]});
            skFitSpline(sketch, "E1410", {"points": [v(-9323.6, 2346.23) * mm, v(-9268.55, 2346.23) * mm, v(-9223.91, 2301.6) * mm, v(-9223.91, 2246.53) * mm]});
            skLineSegment(sketch, "E1411", {"start": v(-11723.91, 1796.14) * mm, "end": v(-11723.91, 2202.54) * mm});
            skLineSegment(sketch, "E1412", {"start": v(-11254.12, 3753.57) * mm, "end": v(-11283.58, 3761.3) * mm});
            skLineSegment(sketch, "E1413", {"start": v(-11283.58, 3761.3) * mm, "end": v(-11313.25, 3768.4) * mm});
            skLineSegment(sketch, "E1414", {"start": v(-11313.25, 3768.4) * mm, "end": v(-11342.91, 3775.1) * mm});
            skLineSegment(sketch, "E1415", {"start": v(-11342.91, 3775.1) * mm, "end": v(-11372.78, 3781.2) * mm});
            skLineSegment(sketch, "E1416", {"start": v(-11326.86, 3709.07) * mm, "end": v(-11299.43, 3827.74) * mm});
            skLineSegment(sketch, "E1417", {"start": v(-11238.27, 3812.5) * mm, "end": v(-11276.06, 3790.75) * mm});
            skLineSegment(sketch, "E1418", {"start": v(-11276.06, 3790.75) * mm, "end": v(-11313.25, 3768.4) * mm});
            skLineSegment(sketch, "E1419", {"start": v(-11313.25, 3768.4) * mm, "end": v(-11349.42, 3745.24) * mm});
            skLineSegment(sketch, "E1420", {"start": v(-11349.42, 3745.24) * mm, "end": v(-11384.57, 3721.46) * mm});
            skLineSegment(sketch, "E1421", {"start": v(-11269.76, 3694.64) * mm, "end": v(-11290.9, 3731.62) * mm});
            skLineSegment(sketch, "E1422", {"start": v(-11290.9, 3731.62) * mm, "end": v(-11313.25, 3768.4) * mm});
            skLineSegment(sketch, "E1423", {"start": v(-11313.25, 3768.4) * mm, "end": v(-11336.61, 3804.77) * mm});
            skLineSegment(sketch, "E1424", {"start": v(-11336.61, 3804.77) * mm, "end": v(-11361, 3840.94) * mm});
            skLineSegment(sketch, "E1425", {"start": v(-11168.77, 3824.28) * mm, "end": v(-11138.3, 3814.73) * mm});
            skLineSegment(sketch, "E1426", {"start": v(-11138.3, 3814.73) * mm, "end": v(-11107.81, 3804.77) * mm});
            skLineSegment(sketch, "E1427", {"start": v(-11107.81, 3804.77) * mm, "end": v(-11077.74, 3794) * mm});
            skLineSegment(sketch, "E1428", {"start": v(-11077.74, 3794) * mm, "end": v(-11047.66, 3783.03) * mm});
            skLineSegment(sketch, "E1429", {"start": v(-11047.66, 3783.03) * mm, "end": v(-11108.62, 3708.05) * mm});
            skLineSegment(sketch, "E1430", {"start": v(-11108.62, 3708.05) * mm, "end": v(-11166.94, 3631.65) * mm});
            skLineSegment(sketch, "E1431", {"start": v(-10731.69, 3628.6) * mm, "end": v(-10826.79, 3472.34) * mm});
            skLineSegment(sketch, "E1432", {"start": v(-10826.79, 3472.34) * mm, "end": v(-10828.61, 3526.6) * mm});
            skLineSegment(sketch, "E1433", {"start": v(-10828.61, 3526.6) * mm, "end": v(-10831.87, 3581.25) * mm});
            skLineSegment(sketch, "E1434", {"start": v(-10831.87, 3581.25) * mm, "end": v(-10836.74, 3636.12) * mm});
            skLineSegment(sketch, "E1435", {"start": v(-10836.74, 3636.12) * mm, "end": v(-10843.25, 3691.39) * mm});
            skLineSegment(sketch, "E1436", {"start": v(-10843.25, 3691.39) * mm, "end": v(-10927.57, 3529.24) * mm});
            skLineSegment(sketch, "E1437", {"start": v(-10609.77, 3471.93) * mm, "end": v(-10634.56, 3490.42) * mm});
            skLineSegment(sketch, "E1438", {"start": v(-10634.56, 3490.42) * mm, "end": v(-10659.76, 3508.5) * mm});
            skLineSegment(sketch, "E1439", {"start": v(-10659.76, 3508.5) * mm, "end": v(-10685.36, 3526.19) * mm});
            skLineSegment(sketch, "E1440", {"start": v(-10685.36, 3526.19) * mm, "end": v(-10710.96, 3543.26) * mm});
            skLineSegment(sketch, "E1441", {"start": v(-10646.55, 3423.37) * mm, "end": v(-10670.53, 3441.25) * mm});
            skLineSegment(sketch, "E1442", {"start": v(-10670.53, 3441.25) * mm, "end": v(-10694.9, 3458.73) * mm});
            skLineSegment(sketch, "E1443", {"start": v(-10694.9, 3458.73) * mm, "end": v(-10719.5, 3475.8) * mm});
            skLineSegment(sketch, "E1444", {"start": v(-10719.5, 3475.8) * mm, "end": v(-10744.49, 3492.46) * mm});
            skLineSegment(sketch, "E1445", {"start": v(-10541.7, 3457.3) * mm, "end": v(-10497.8, 3460.76) * mm});
            skLineSegment(sketch, "E1446", {"start": v(-10497.8, 3460.76) * mm, "end": v(-10615.46, 3320.55) * mm});
            skLineSegment(sketch, "E1447", {"start": v(-10593.3, 3301.85) * mm, "end": v(-10615.46, 3320.55) * mm});
            skLineSegment(sketch, "E1448", {"start": v(-10615.46, 3320.55) * mm, "end": v(-10637.8, 3339.04) * mm});
            skLineSegment(sketch, "E1449", {"start": v(-10401.7, 3244.15) * mm, "end": v(-10422.62, 3266.3) * mm});
            skLineSegment(sketch, "E1450", {"start": v(-10422.62, 3266.3) * mm, "end": v(-10444.16, 3287.83) * mm});
            skLineSegment(sketch, "E1451", {"start": v(-10444.16, 3287.83) * mm, "end": v(-10465.9, 3309.17) * mm});
            skLineSegment(sketch, "E1452", {"start": v(-10465.9, 3309.17) * mm, "end": v(-10467.33, 3352.45) * mm});
            skLineSegment(sketch, "E1453", {"start": v(-10467.33, 3352.45) * mm, "end": v(-10446.6, 3374.8) * mm});
            skLineSegment(sketch, "E1454", {"start": v(-10446.6, 3374.8) * mm, "end": v(-10402.5, 3375.21) * mm});
            skLineSegment(sketch, "E1455", {"start": v(-10402.5, 3375.21) * mm, "end": v(-10379.75, 3352.86) * mm});
            skLineSegment(sketch, "E1456", {"start": v(-10379.75, 3352.86) * mm, "end": v(-10357.2, 3330.1) * mm});
            skLineSegment(sketch, "E1457", {"start": v(-10357.2, 3330.1) * mm, "end": v(-10357.2, 3286) * mm});
            skLineSegment(sketch, "E1458", {"start": v(-10357.2, 3286) * mm, "end": v(-10423.84, 3223.42) * mm});
            skLineSegment(sketch, "E1459", {"start": v(-10423.84, 3223.42) * mm, "end": v(-10466.3, 3223.62) * mm});
            skLineSegment(sketch, "E1460", {"start": v(-10466.3, 3223.62) * mm, "end": v(-10508.57, 3223.01) * mm});
            skLineSegment(sketch, "E1461", {"start": v(-10508.57, 3223.01) * mm, "end": v(-10529.3, 3243.33) * mm});
            skLineSegment(sketch, "E1462", {"start": v(-10264.73, 3080.57) * mm, "end": v(-10246.85, 3055.98) * mm});
            skLineSegment(sketch, "E1463", {"start": v(-10246.85, 3055.98) * mm, "end": v(-10229.38, 3030.99) * mm});
            skLineSegment(sketch, "E1464", {"start": v(-10229.38, 3030.99) * mm, "end": v(-10212.3, 3005.8) * mm});
            skLineSegment(sketch, "E1465", {"start": v(-10212.3, 3005.8) * mm, "end": v(-10169.84, 2996.85) * mm});
            skLineSegment(sketch, "E1466", {"start": v(-10169.84, 2996.85) * mm, "end": v(-10144.24, 3013.31) * mm});
            skLineSegment(sketch, "E1467", {"start": v(-10144.24, 3013.31) * mm, "end": v(-10136.1, 3056.6) * mm});
            skLineSegment(sketch, "E1468", {"start": v(-10136.1, 3056.6) * mm, "end": v(-10154, 3083) * mm});
            skLineSegment(sketch, "E1469", {"start": v(-10154, 3083) * mm, "end": v(-10172.48, 3109.22) * mm});
            skLineSegment(sketch, "E1470", {"start": v(-10172.48, 3109.22) * mm, "end": v(-10191.38, 3135.03) * mm});
            skLineSegment(sketch, "E1471", {"start": v(-10191.38, 3135.03) * mm, "end": v(-10338.3, 3026.11) * mm});
            skLineSegment(sketch, "E1472", {"start": v(-10241.98, 2881.64) * mm, "end": v(-10137.33, 2944.02) * mm});
            skLineSegment(sketch, "E1473", {"start": v(-10111.12, 2959.67) * mm, "end": v(-10084.9, 2975.31) * mm});
            skLineSegment(sketch, "E1474", {"start": v(-10133.26, 2741.23) * mm, "end": v(-10173.3, 2754.43) * mm});
            skLineSegment(sketch, "E1475", {"start": v(-10173.3, 2754.43) * mm, "end": v(-10159.07, 2794.06) * mm});
            skLineSegment(sketch, "E1476", {"start": v(-10159.07, 2794.06) * mm, "end": v(-10023.13, 2863.15) * mm});
            skLineSegment(sketch, "E1477", {"start": v(-10050.36, 2779.83) * mm, "end": v(-10063.77, 2807.67) * mm});
            skLineSegment(sketch, "E1478", {"start": v(-10063.77, 2807.67) * mm, "end": v(-10077.59, 2835.51) * mm});
            skLineSegment(sketch, "E1479", {"start": v(-10077.59, 2835.51) * mm, "end": v(-10091.81, 2862.94) * mm});
            skLineSegment(sketch, "E1480", {"start": v(-10091.81, 2862.94) * mm, "end": v(-10106.44, 2890.37) * mm});
            skLineSegment(sketch, "E1481", {"start": v(-10095.47, 2567.5) * mm, "end": v(-10105.22, 2594.72) * mm});
            skLineSegment(sketch, "E1482", {"start": v(-10105.22, 2594.72) * mm, "end": v(-10115.59, 2621.74) * mm});
            skLineSegment(sketch, "E1483", {"start": v(-10115.59, 2621.74) * mm, "end": v(-10126.15, 2648.77) * mm});
            skLineSegment(sketch, "E1484", {"start": v(-10126.15, 2648.77) * mm, "end": v(-10109.29, 2687.38) * mm});
            skLineSegment(sketch, "E1485", {"start": v(-10109.29, 2687.38) * mm, "end": v(-10053.2, 2711.15) * mm});
            skLineSegment(sketch, "E1486", {"start": v(-10053.2, 2711.15) * mm, "end": v(-10013.17, 2694.5) * mm});
            skLineSegment(sketch, "E1487", {"start": v(-10013.17, 2694.5) * mm, "end": v(-10001.8, 2665.84) * mm});
            skLineSegment(sketch, "E1488", {"start": v(-10001.8, 2665.84) * mm, "end": v(-9990.82, 2636.78) * mm});
            skLineSegment(sketch, "E1489", {"start": v(-9990.82, 2636.78) * mm, "end": v(-9980.46, 2607.52) * mm});
            skLineSegment(sketch, "E1490", {"start": v(-10019.07, 2530.5) * mm, "end": v(-9981.27, 2510.6) * mm});
            skLineSegment(sketch, "E1491", {"start": v(-9981.27, 2510.6) * mm, "end": v(-9943.48, 2489.26) * mm});
            skLineSegment(sketch, "E1492", {"start": v(-9943.48, 2489.26) * mm, "end": v(-9935.55, 2459.39) * mm});
            skLineSegment(sketch, "E1493", {"start": v(-9935.55, 2459.39) * mm, "end": v(-9957.7, 2422.2) * mm});
            skLineSegment(sketch, "E1494", {"start": v(-9957.7, 2422.2) * mm, "end": v(-10046.7, 2400.87) * mm});
            skLineSegment(sketch, "E1495", {"start": v(-10077.38, 2512.42) * mm, "end": v(-9902.84, 2566.88) * mm});
            skLineSegment(sketch, "E1496", {"start": v(-10011.14, 2201.53) * mm, "end": v(-10007.89, 2172.67) * mm});
            skLineSegment(sketch, "E1497", {"start": v(-10007.89, 2172.67) * mm, "end": v(-10005.25, 2143.82) * mm});
            skLineSegment(sketch, "E1498", {"start": v(-10005.25, 2143.82) * mm, "end": v(-10003.22, 2114.96) * mm});
            skLineSegment(sketch, "E1499", {"start": v(-10003.22, 2114.96) * mm, "end": v(-9970.9, 2087.73) * mm});
            skLineSegment(sketch, "E1500", {"start": v(-9970.9, 2087.73) * mm, "end": v(-9849.2, 2093.83) * mm});
            skLineSegment(sketch, "E1501", {"start": v(-9849.2, 2093.83) * mm, "end": v(-9820.74, 2127.36) * mm});
            skLineSegment(sketch, "E1502", {"start": v(-9820.74, 2127.36) * mm, "end": v(-9823.18, 2159.26) * mm});
            skLineSegment(sketch, "E1503", {"start": v(-9823.18, 2159.26) * mm, "end": v(-9826.03, 2191.16) * mm});
            skLineSegment(sketch, "E1504", {"start": v(-9826.03, 2191.16) * mm, "end": v(-9829.48, 2222.86) * mm});
            skLineSegment(sketch, "E1505", {"start": v(-9826.03, 2191.16) * mm, "end": v(-10007.89, 2172.67) * mm});
            skLineSegment(sketch, "E1506", {"start": v(-9879.67, 1906.48) * mm, "end": v(-9878.45, 1937.37) * mm});
            skLineSegment(sketch, "E1507", {"start": v(-9878.45, 1937.37) * mm, "end": v(-9877.64, 1968.25) * mm});
            skLineSegment(sketch, "E1508", {"start": v(-9877.64, 1968.25) * mm, "end": v(-9877.23, 1999.34) * mm});
            skLineSegment(sketch, "E1509", {"start": v(-9877.23, 1999.34) * mm, "end": v(-9877.64, 2030.43) * mm});
            skLineSegment(sketch, "E1510", {"start": v(-9940.63, 1909.53) * mm, "end": v(-9939.2, 1939.4) * mm});
            skLineSegment(sketch, "E1511", {"start": v(-9939.2, 1939.4) * mm, "end": v(-9938.6, 1969.47) * mm});
            skLineSegment(sketch, "E1512", {"start": v(-9938.6, 1969.47) * mm, "end": v(-9938.4, 1999.34) * mm});
            skLineSegment(sketch, "E1513", {"start": v(-9938.4, 1999.34) * mm, "end": v(-9938.6, 2029.21) * mm});
            skLineSegment(sketch, "E1514", {"start": v(-9958.72, 1730.71) * mm, "end": v(-9954.45, 1760.38) * mm});
            skLineSegment(sketch, "E1515", {"start": v(-9954.45, 1760.38) * mm, "end": v(-9950.59, 1790.05) * mm});
            skLineSegment(sketch, "E1516", {"start": v(-9950.59, 1790.05) * mm, "end": v(-9947.34, 1819.92) * mm});
            skLineSegment(sketch, "E1517", {"start": v(-9947.34, 1819.92) * mm, "end": v(-9944.5, 1849.58) * mm});
            skLineSegment(sketch, "E1518", {"start": v(-9944.5, 1849.58) * mm, "end": v(-9906.9, 1815.65) * mm});
            skLineSegment(sketch, "E1519", {"start": v(-9906.9, 1815.65) * mm, "end": v(-9869.92, 1780.5) * mm});
            skLineSegment(sketch, "E1520", {"start": v(-9869.92, 1780.5) * mm, "end": v(-9833.54, 1743.92) * mm});
            skLineSegment(sketch, "E1521", {"start": v(-9833.54, 1743.92) * mm, "end": v(-10014.8, 1768.5) * mm});
            skLineSegment(sketch, "E1522", {"start": v(-9998.54, 1677.07) * mm, "end": v(-10028.62, 1682.76) * mm});
            skLineSegment(sketch, "E1523", {"start": v(-9861.59, 1586.44) * mm, "end": v(-9868.7, 1555.35) * mm});
            skLineSegment(sketch, "E1524", {"start": v(-9868.7, 1555.35) * mm, "end": v(-9876.42, 1524.26) * mm});
            skLineSegment(sketch, "E1525", {"start": v(-9876.42, 1524.26) * mm, "end": v(-9884.75, 1493.17) * mm});
            skLineSegment(sketch, "E1526", {"start": v(-9884.75, 1493.17) * mm, "end": v(-9893.49, 1462.49) * mm});
            skLineSegment(sketch, "E1527", {"start": v(-9893.49, 1462.49) * mm, "end": v(-9972.94, 1517.56) * mm});
            skLineSegment(sketch, "E1528", {"start": v(-9972.94, 1517.56) * mm, "end": v(-10053.6, 1569.78) * mm});
            skLineSegment(sketch, "E1529", {"start": v(-9956.68, 1281.23) * mm, "end": v(-9944.9, 1310.9) * mm});
            skLineSegment(sketch, "E1530", {"start": v(-9944.9, 1310.9) * mm, "end": v(-9933.72, 1340.77) * mm});
            skLineSegment(sketch, "E1531", {"start": v(-9933.72, 1340.77) * mm, "end": v(-9922.75, 1371.05) * mm});
            skLineSegment(sketch, "E1532", {"start": v(-9922.75, 1371.05) * mm, "end": v(-9912.59, 1401.33) * mm});
            skLineSegment(sketch, "E1533", {"start": v(-9912.59, 1401.33) * mm, "end": v(-9970.5, 1420.43) * mm});
            skLineSegment(sketch, "E1534", {"start": v(-9970.5, 1420.43) * mm, "end": v(-9980.46, 1391.17) * mm});
            skLineSegment(sketch, "E1535", {"start": v(-9980.46, 1391.17) * mm, "end": v(-9990.82, 1361.9) * mm});
            skLineSegment(sketch, "E1536", {"start": v(-9990.82, 1361.9) * mm, "end": v(-10001.8, 1332.85) * mm});
            skLineSegment(sketch, "E1537", {"start": v(-10001.8, 1332.85) * mm, "end": v(-10041.42, 1315.57) * mm});
            skLineSegment(sketch, "E1538", {"start": v(-10041.42, 1315.57) * mm, "end": v(-10097.9, 1338.54) * mm});
            skLineSegment(sketch, "E1539", {"start": v(-10097.9, 1338.54) * mm, "end": v(-10115.59, 1376.94) * mm});
            skLineSegment(sketch, "E1540", {"start": v(-10115.59, 1376.94) * mm, "end": v(-10105.22, 1403.97) * mm});
            skLineSegment(sketch, "E1541", {"start": v(-10105.22, 1403.97) * mm, "end": v(-10095.47, 1431.2) * mm});
            skLineSegment(sketch, "E1542", {"start": v(-10095.47, 1431.2) * mm, "end": v(-10057.27, 1449.08) * mm});
            skLineSegment(sketch, "E1543", {"start": v(-10133.26, 1123.14) * mm, "end": v(-10148.1, 1096.53) * mm});
            skLineSegment(sketch, "E1544", {"start": v(-10148.1, 1096.53) * mm, "end": v(-10163.54, 1070.1) * mm});
            skLineSegment(sketch, "E1545", {"start": v(-10163.54, 1070.1) * mm, "end": v(-10179.4, 1044.1) * mm});
            skLineSegment(sketch, "E1546", {"start": v(-10179.4, 1044.1) * mm, "end": v(-10169.84, 1001.83) * mm});
            skLineSegment(sketch, "E1547", {"start": v(-10169.84, 1001.83) * mm, "end": v(-10144.24, 985.37) * mm});
            skLineSegment(sketch, "E1548", {"start": v(-10144.24, 985.37) * mm, "end": v(-10101.57, 996.14) * mm});
            skLineSegment(sketch, "E1549", {"start": v(-10101.57, 996.14) * mm, "end": v(-10084.9, 1023.37) * mm});
            skLineSegment(sketch, "E1550", {"start": v(-10084.9, 1023.37) * mm, "end": v(-10068.85, 1051) * mm});
            skLineSegment(sketch, "E1551", {"start": v(-10068.85, 1051) * mm, "end": v(-10053, 1079.05) * mm});
            skLineSegment(sketch, "E1552", {"start": v(-10053, 1079.05) * mm, "end": v(-10213.33, 1167.24) * mm});
            skLineSegment(sketch, "E1553", {"start": v(-10278.15, 850.65) * mm, "end": v(-10259.05, 875.24) * mm});
            skLineSegment(sketch, "E1554", {"start": v(-10259.05, 875.24) * mm, "end": v(-10240.35, 899.83) * mm});
            skLineSegment(sketch, "E1555", {"start": v(-10240.35, 899.83) * mm, "end": v(-10222.06, 925.02) * mm});
            skLineSegment(sketch, "E1556", {"start": v(-10222.06, 925.02) * mm, "end": v(-10204.18, 950.22) * mm});
            skLineSegment(sketch, "E1557", {"start": v(-10325.7, 888.65) * mm, "end": v(-10307.4, 912.22) * mm});
            skLineSegment(sketch, "E1558", {"start": v(-10307.4, 912.22) * mm, "end": v(-10289.32, 936.2) * mm});
            skLineSegment(sketch, "E1559", {"start": v(-10289.32, 936.2) * mm, "end": v(-10271.64, 960.38) * mm});
            skLineSegment(sketch, "E1560", {"start": v(-10271.64, 960.38) * mm, "end": v(-10254.37, 984.97) * mm});
            skLineSegment(sketch, "E1561", {"start": v(-10444.57, 753.73) * mm, "end": v(-10423.84, 775.27) * mm});
            skLineSegment(sketch, "E1562", {"start": v(-10423.84, 775.27) * mm, "end": v(-10403.52, 797.41) * mm});
            skLineSegment(sketch, "E1563", {"start": v(-10403.52, 797.41) * mm, "end": v(-10383.4, 819.77) * mm});
            skLineSegment(sketch, "E1564", {"start": v(-10383.4, 819.77) * mm, "end": v(-10363.9, 842.32) * mm});
            skLineSegment(sketch, "E1565", {"start": v(-10363.9, 842.32) * mm, "end": v(-10352.92, 792.74) * mm});
            skLineSegment(sketch, "E1566", {"start": v(-10352.92, 792.74) * mm, "end": v(-10343.37, 742.55) * mm});
            skLineSegment(sketch, "E1567", {"start": v(-10343.37, 742.55) * mm, "end": v(-10335.04, 691.75) * mm});
            skLineSegment(sketch, "E1568", {"start": v(-10335.04, 691.75) * mm, "end": v(-10468.14, 817.13) * mm});
            skLineSegment(sketch, "E1569", {"start": v(-10580.1, 588.73) * mm, "end": v(-10604.08, 569.63) * mm});
            skLineSegment(sketch, "E1570", {"start": v(-10604.08, 569.63) * mm, "end": v(-10628.06, 551.14) * mm});
            skLineSegment(sketch, "E1571", {"start": v(-10628.06, 551.14) * mm, "end": v(-10652.64, 532.85) * mm});
            skLineSegment(sketch, "E1572", {"start": v(-10652.64, 532.85) * mm, "end": v(-10659.76, 490.18) * mm});
            skLineSegment(sketch, "E1573", {"start": v(-10659.76, 490.18) * mm, "end": v(-10642.28, 465.39) * mm});
            skLineSegment(sketch, "E1574", {"start": v(-10642.28, 465.39) * mm, "end": v(-10598.6, 459.09) * mm});
            skLineSegment(sketch, "E1575", {"start": v(-10598.6, 459.09) * mm, "end": v(-10572.99, 478.19) * mm});
            skLineSegment(sketch, "E1576", {"start": v(-10572.99, 478.19) * mm, "end": v(-10547.59, 497.7) * mm});
            skLineSegment(sketch, "E1577", {"start": v(-10547.59, 497.7) * mm, "end": v(-10522.6, 517.6) * mm});
            skLineSegment(sketch, "E1578", {"start": v(-10522.6, 517.6) * mm, "end": v(-10637.8, 659.65) * mm});
            skLineSegment(sketch, "E1579", {"start": v(-10777.81, 557.23) * mm, "end": v(-10744.49, 506.23) * mm});
            skLineSegment(sketch, "E1580", {"start": v(-10744.49, 506.23) * mm, "end": v(-10737.17, 438.56) * mm});
            skLineSegment(sketch, "E1581", {"start": v(-10737.17, 438.56) * mm, "end": v(-10731.69, 370.09) * mm});
            skLineSegment(sketch, "E1582", {"start": v(-10731.69, 370.09) * mm, "end": v(-10790, 406.25) * mm});
            skLineSegment(sketch, "E1583", {"start": v(-10790, 406.25) * mm, "end": v(-10846.9, 444.05) * mm});
            skLineSegment(sketch, "E1584", {"start": v(-10846.9, 444.05) * mm, "end": v(-10876.77, 497.09) * mm});
            skLineSegment(sketch, "E1585", {"start": v(-10744.49, 506.23) * mm, "end": v(-10769.69, 490.18) * mm});
            skLineSegment(sketch, "E1586", {"start": v(-10769.69, 490.18) * mm, "end": v(-10795.09, 474.33) * mm});
            skLineSegment(sketch, "E1587", {"start": v(-10795.09, 474.33) * mm, "end": v(-10820.9, 458.88) * mm});
            skLineSegment(sketch, "E1588", {"start": v(-10820.9, 458.88) * mm, "end": v(-10846.9, 444.05) * mm});
            skLineSegment(sketch, "E1589", {"start": v(-10983.25, 307.9) * mm, "end": v(-10955, 320.5) * mm});
            skLineSegment(sketch, "E1590", {"start": v(-10955, 320.5) * mm, "end": v(-10926.76, 333.71) * mm});
            skLineSegment(sketch, "E1591", {"start": v(-10926.76, 333.71) * mm, "end": v(-10898.92, 347.33) * mm});
            skLineSegment(sketch, "E1592", {"start": v(-10898.92, 347.33) * mm, "end": v(-10871.29, 361.35) * mm});
            skLineSegment(sketch, "E1593", {"start": v(-11007.63, 363.58) * mm, "end": v(-10980.2, 375.98) * mm});
            skLineSegment(sketch, "E1594", {"start": v(-10980.2, 375.98) * mm, "end": v(-10953.18, 388.58) * mm});
            skLineSegment(sketch, "E1595", {"start": v(-10953.18, 388.58) * mm, "end": v(-10926.15, 401.78) * mm});
            skLineSegment(sketch, "E1596", {"start": v(-10926.15, 401.78) * mm, "end": v(-10899.53, 415.4) * mm});
            skLineSegment(sketch, "E1597", {"start": v(-11194.37, 357.9) * mm, "end": v(-11166.94, 367.04) * mm});
            skLineSegment(sketch, "E1598", {"start": v(-11166.94, 367.04) * mm, "end": v(-11139.71, 376.59) * mm});
            skLineSegment(sketch, "E1599", {"start": v(-11139.71, 376.59) * mm, "end": v(-11112.49, 386.75) * mm});
            skLineSegment(sketch, "E1600", {"start": v(-11112.49, 386.75) * mm, "end": v(-11085.46, 397.11) * mm});
            skLineSegment(sketch, "E1601", {"start": v(-11085.46, 397.11) * mm, "end": v(-11062.9, 340.62) * mm});
            skLineSegment(sketch, "E1602", {"start": v(-11062.9, 340.62) * mm, "end": v(-11079.97, 301.2) * mm});
            skLineSegment(sketch, "E1603", {"start": v(-11079.97, 301.2) * mm, "end": v(-11108.62, 290.63) * mm});
            skLineSegment(sketch, "E1604", {"start": v(-11108.62, 290.63) * mm, "end": v(-11137.48, 280.47) * mm});
            skLineSegment(sketch, "E1605", {"start": v(-11137.48, 280.47) * mm, "end": v(-11156.99, 241.87) * mm});
            skLineSegment(sketch, "E1606", {"start": v(-11156.99, 241.87) * mm, "end": v(-11147.64, 213.01) * mm});
            skLineSegment(sketch, "E1607", {"start": v(-11147.64, 213.01) * mm, "end": v(-11107.81, 193.91) * mm});
            skLineSegment(sketch, "E1608", {"start": v(-11107.81, 193.91) * mm, "end": v(-11077.74, 204.68) * mm});
            skLineSegment(sketch, "E1609", {"start": v(-11077.74, 204.68) * mm, "end": v(-11047.66, 215.65) * mm});
            skLineSegment(sketch, "E1610", {"start": v(-11047.66, 215.65) * mm, "end": v(-11029.17, 255.68) * mm});
            skFitSpline(sketch, "E1611", {"points": [v(-9310.91, 1999.34) * mm, v(-9310.91, 666.68) * mm, v(-10391.25, -413.66) * mm, v(-11723.91, -413.66) * mm]});
            skFitSpline(sketch, "E1612", {"points": [v(-11723.91, -413.66) * mm, v(-13056.58, -413.66) * mm, v(-14136.91, 666.68) * mm, v(-14136.91, 1999.34) * mm]});
            skFitSpline(sketch, "E1613", {"points": [v(-14136.91, 1999.34) * mm, v(-14136.91, 3332) * mm, v(-13056.58, 4412.34) * mm, v(-11723.91, 4412.34) * mm]});
            skFitSpline(sketch, "E1614", {"points": [v(-11723.91, 4412.34) * mm, v(-10391.25, 4412.34) * mm, v(-9310.91, 3332) * mm, v(-9310.91, 1999.34) * mm]});
            skLineSegment(sketch, "E1615", {"start": v(-11362.01, 312.99) * mm, "end": v(-11333.77, 319.29) * mm});
            skLineSegment(sketch, "E1616", {"start": v(-11333.77, 319.29) * mm, "end": v(-11305.73, 326.2) * mm});
            skLineSegment(sketch, "E1617", {"start": v(-11305.73, 326.2) * mm, "end": v(-11277.69, 333.3) * mm});
            skLineSegment(sketch, "E1618", {"start": v(-11277.69, 333.3) * mm, "end": v(-11249.85, 341.23) * mm});
            skLineSegment(sketch, "E1619", {"start": v(-11249.85, 341.23) * mm, "end": v(-11232.98, 282.5) * mm});
            skLineSegment(sketch, "E1620", {"start": v(-11232.98, 282.5) * mm, "end": v(-11254.12, 245.12) * mm});
            skLineSegment(sketch, "E1621", {"start": v(-11254.12, 245.12) * mm, "end": v(-11283.58, 237.4) * mm});
            skLineSegment(sketch, "E1622", {"start": v(-11283.58, 237.4) * mm, "end": v(-11313.25, 230.28) * mm});
            skLineSegment(sketch, "E1623", {"start": v(-11313.25, 230.28) * mm, "end": v(-11336.61, 193.91) * mm});
            skLineSegment(sketch, "E1624", {"start": v(-11336.61, 193.91) * mm, "end": v(-11330.11, 164.04) * mm});
            skLineSegment(sketch, "E1625", {"start": v(-11330.11, 164.04) * mm, "end": v(-11292.52, 141.28) * mm});
            skLineSegment(sketch, "E1626", {"start": v(-11292.52, 141.28) * mm, "end": v(-11261.43, 148.8) * mm});
            skLineSegment(sketch, "E1627", {"start": v(-11261.43, 148.8) * mm, "end": v(-11230.34, 156.73) * mm});
            skLineSegment(sketch, "E1628", {"start": v(-11230.34, 156.73) * mm, "end": v(-11207.99, 194.52) * mm});
            skFitSpline(sketch, "E1629", {"points": [v(-9056.91, 1999.34) * mm, v(-9056.91, 526.4) * mm, v(-10250.97, -667.66) * mm, v(-11723.91, -667.66) * mm]});
            skFitSpline(sketch, "E1630", {"points": [v(-11723.91, -667.66) * mm, v(-13196.86, -667.66) * mm, v(-14390.91, 526.4) * mm, v(-14390.91, 1999.34) * mm]});
            skFitSpline(sketch, "E1631", {"points": [v(-14390.91, 1999.34) * mm, v(-14390.91, 3472.29) * mm, v(-13196.86, 4666.34) * mm, v(-11723.91, 4666.34) * mm]});
            skFitSpline(sketch, "E1632", {"points": [v(-11723.91, 4666.34) * mm, v(-10250.97, 4666.34) * mm, v(-9056.91, 3472.29) * mm, v(-9056.91, 1999.34) * mm]});
            skFitSpline(sketch, "E1633", {"points": [v(-9486.68, 1999.34) * mm, v(-9486.68, 763.75) * mm, v(-10488.32, -237.89) * mm, v(-11723.91, -237.89) * mm]});
            skFitSpline(sketch, "E1634", {"points": [v(-11723.91, -237.89) * mm, v(-12959.5, -237.89) * mm, v(-13961.15, 763.75) * mm, v(-13961.15, 1999.34) * mm]});
            skFitSpline(sketch, "E1635", {"points": [v(-13961.15, 1999.34) * mm, v(-13961.15, 3234.93) * mm, v(-12959.5, 4236.57) * mm, v(-11723.91, 4236.57) * mm]});
            skFitSpline(sketch, "E1636", {"points": [v(-11723.91, 4236.57) * mm, v(-10488.32, 4236.57) * mm, v(-9486.68, 3234.93) * mm, v(-9486.68, 1999.34) * mm]});
            skLineSegment(sketch, "E1637", {"start": v(-5135.27, 2057.55) * mm, "end": v(-5132.17, 2057.8) * mm});
            skLineSegment(sketch, "E1638", {"start": v(-5132.17, 2057.8) * mm, "end": v(-5128.13, 2058.2) * mm});
            skLineSegment(sketch, "E1639", {"start": v(-5128.13, 2058.2) * mm, "end": v(-5123.14, 2058.8) * mm});
            skLineSegment(sketch, "E1640", {"start": v(-5123.14, 2058.8) * mm, "end": v(-5117.23, 2059.68) * mm});
            skLineSegment(sketch, "E1641", {"start": v(-5117.23, 2059.68) * mm, "end": v(-5110.4, 2060.84) * mm});
            skLineSegment(sketch, "E1642", {"start": v(-5110.4, 2060.84) * mm, "end": v(-5102.65, 2062.35) * mm});
            skLineSegment(sketch, "E1643", {"start": v(-5102.65, 2062.35) * mm, "end": v(-5094, 2064.24) * mm});
            skLineSegment(sketch, "E1644", {"start": v(-5094, 2064.24) * mm, "end": v(-5084.48, 2066.56) * mm});
            skLineSegment(sketch, "E1645", {"start": v(-5084.48, 2066.56) * mm, "end": v(-5074.09, 2069.35) * mm});
            skLineSegment(sketch, "E1646", {"start": v(-5074.09, 2069.35) * mm, "end": v(-5062.84, 2072.64) * mm});
            skLineSegment(sketch, "E1647", {"start": v(-5062.84, 2072.64) * mm, "end": v(-5050.77, 2076.5) * mm});
            skLineSegment(sketch, "E1648", {"start": v(-5050.77, 2076.5) * mm, "end": v(-5037.88, 2080.93) * mm});
            skLineSegment(sketch, "E1649", {"start": v(-5037.88, 2080.93) * mm, "end": v(-5024.2, 2086) * mm});
            skLineSegment(sketch, "E1650", {"start": v(-5024.2, 2086) * mm, "end": v(-5009.76, 2091.74) * mm});
            skLineSegment(sketch, "E1651", {"start": v(-5009.76, 2091.74) * mm, "end": v(-4994.57, 2098.2) * mm});
            skLineSegment(sketch, "E1652", {"start": v(-4994.57, 2098.2) * mm, "end": v(-4978.67, 2105.38) * mm});
            skLineSegment(sketch, "E1653", {"start": v(-4978.67, 2105.38) * mm, "end": v(-4962.07, 2113.36) * mm});
            skLineSegment(sketch, "E1654", {"start": v(-4962.07, 2113.36) * mm, "end": v(-4944.82, 2122.16) * mm});
            skLineSegment(sketch, "E1655", {"start": v(-4944.82, 2122.16) * mm, "end": v(-4926.93, 2131.8) * mm});
            skLineSegment(sketch, "E1656", {"start": v(-4926.93, 2131.8) * mm, "end": v(-4908.43, 2142.34) * mm});
            skLineSegment(sketch, "E1657", {"start": v(-4908.43, 2142.34) * mm, "end": v(-4889.37, 2153.8) * mm});
            skLineSegment(sketch, "E1658", {"start": v(-4889.37, 2153.8) * mm, "end": v(-4869.77, 2166.2) * mm});
            skLineSegment(sketch, "E1659", {"start": v(-4869.77, 2166.2) * mm, "end": v(-4849.68, 2179.6) * mm});
            skLineSegment(sketch, "E1660", {"start": v(-4849.68, 2179.6) * mm, "end": v(-4829.1, 2194) * mm});
            skLineSegment(sketch, "E1661", {"start": v(-4829.1, 2194) * mm, "end": v(-4808.11, 2209.44) * mm});
            skLineSegment(sketch, "E1662", {"start": v(-4808.11, 2209.44) * mm, "end": v(-4786.72, 2225.95) * mm});
            skLineSegment(sketch, "E1663", {"start": v(-4786.72, 2225.95) * mm, "end": v(-4764.98, 2243.56) * mm});
            skLineSegment(sketch, "E1664", {"start": v(-4764.98, 2243.56) * mm, "end": v(-4755.8, 2261.07) * mm});
            skLineSegment(sketch, "E1665", {"start": v(-4755.8, 2261.07) * mm, "end": v(-4770.8, 2382.6) * mm});
            skLineSegment(sketch, "E1666", {"start": v(-4770.8, 2382.6) * mm, "end": v(-4783.97, 2397.34) * mm});
            skLineSegment(sketch, "E1667", {"start": v(-4783.97, 2397.34) * mm, "end": v(-4809.34, 2409.13) * mm});
            skLineSegment(sketch, "E1668", {"start": v(-4809.34, 2409.13) * mm, "end": v(-4834.1, 2419.95) * mm});
            skLineSegment(sketch, "E1669", {"start": v(-4834.1, 2419.95) * mm, "end": v(-4858.22, 2429.82) * mm});
            skLineSegment(sketch, "E1670", {"start": v(-4858.22, 2429.82) * mm, "end": v(-4881.68, 2438.8) * mm});
            skLineSegment(sketch, "E1671", {"start": v(-4881.68, 2438.8) * mm, "end": v(-4904.43, 2446.89) * mm});
            skLineSegment(sketch, "E1672", {"start": v(-4904.43, 2446.89) * mm, "end": v(-4926.45, 2454.16) * mm});
            skLineSegment(sketch, "E1673", {"start": v(-4926.45, 2454.16) * mm, "end": v(-4947.73, 2460.63) * mm});
            skLineSegment(sketch, "E1674", {"start": v(-4947.73, 2460.63) * mm, "end": v(-4968.23, 2466.36) * mm});
            skLineSegment(sketch, "E1675", {"start": v(-4968.23, 2466.36) * mm, "end": v(-4987.93, 2471.36) * mm});
            skLineSegment(sketch, "E1676", {"start": v(-4987.93, 2471.36) * mm, "end": v(-5006.8, 2475.7) * mm});
            skLineSegment(sketch, "E1677", {"start": v(-5006.8, 2475.7) * mm, "end": v(-5024.84, 2479.4) * mm});
            skLineSegment(sketch, "E1678", {"start": v(-5024.84, 2479.4) * mm, "end": v(-5042.02, 2482.5) * mm});
            skLineSegment(sketch, "E1679", {"start": v(-5042.02, 2482.5) * mm, "end": v(-5058.32, 2485.07) * mm});
            skLineSegment(sketch, "E1680", {"start": v(-5058.32, 2485.07) * mm, "end": v(-5073.72, 2487.13) * mm});
            skLineSegment(sketch, "E1681", {"start": v(-5073.72, 2487.13) * mm, "end": v(-5088.22, 2488.72) * mm});
            skLineSegment(sketch, "E1682", {"start": v(-5088.22, 2488.72) * mm, "end": v(-5101.8, 2489.89) * mm});
            skLineSegment(sketch, "E1683", {"start": v(-5101.8, 2489.89) * mm, "end": v(-5114.45, 2490.68) * mm});
            skLineSegment(sketch, "E1684", {"start": v(-5114.45, 2490.68) * mm, "end": v(-5126.16, 2491.15) * mm});
            skLineSegment(sketch, "E1685", {"start": v(-5126.16, 2491.15) * mm, "end": v(-5136.92, 2491.32) * mm});
            skLineSegment(sketch, "E1686", {"start": v(-5136.92, 2491.32) * mm, "end": v(-5146.72, 2491.25) * mm});
            skLineSegment(sketch, "E1687", {"start": v(-5146.72, 2491.25) * mm, "end": v(-5155.57, 2490.99) * mm});
            skLineSegment(sketch, "E1688", {"start": v(-5155.57, 2490.99) * mm, "end": v(-5163.45, 2490.57) * mm});
            skLineSegment(sketch, "E1689", {"start": v(-5163.45, 2490.57) * mm, "end": v(-5170.36, 2490.03) * mm});
            skLineSegment(sketch, "E1690", {"start": v(-5170.36, 2490.03) * mm, "end": v(-5176.3, 2489.44) * mm});
            skLineSegment(sketch, "E1691", {"start": v(-5176.3, 2489.44) * mm, "end": v(-5181.3, 2488.82) * mm});
            skLineSegment(sketch, "E1692", {"start": v(-5181.3, 2488.82) * mm, "end": v(-5185.31, 2488.23) * mm});
            skLineSegment(sketch, "E1693", {"start": v(-5185.31, 2488.23) * mm, "end": v(-5188.38, 2487.7) * mm});
            skLineSegment(sketch, "E1694", {"start": v(-5188.38, 2487.7) * mm, "end": v(-5190.5, 2487.3) * mm});
            skLineSegment(sketch, "E1695", {"start": v(-5190.5, 2487.3) * mm, "end": v(-5191.66, 2487.04) * mm});
            skLineSegment(sketch, "E1696", {"start": v(-5191.66, 2487.04) * mm, "end": v(-5340.7, 2449.67) * mm});
            skLineSegment(sketch, "E1697", {"start": v(-5340.7, 2449.67) * mm, "end": v(-5431.71, 2713.43) * mm});
            skLineSegment(sketch, "E1698", {"start": v(-5431.71, 2713.43) * mm, "end": v(-5291.34, 2775.93) * mm});
            skLineSegment(sketch, "E1699", {"start": v(-5291.34, 2775.93) * mm, "end": v(-5290.27, 2776.45) * mm});
            skLineSegment(sketch, "E1700", {"start": v(-5290.27, 2776.45) * mm, "end": v(-5288.35, 2777.42) * mm});
            skLineSegment(sketch, "E1701", {"start": v(-5288.35, 2777.42) * mm, "end": v(-5285.62, 2778.9) * mm});
            skLineSegment(sketch, "E1702", {"start": v(-5285.62, 2778.9) * mm, "end": v(-5282.08, 2780.91) * mm});
            skLineSegment(sketch, "E1703", {"start": v(-5282.08, 2780.91) * mm, "end": v(-5277.78, 2783.5) * mm});
            skLineSegment(sketch, "E1704", {"start": v(-5277.78, 2783.5) * mm, "end": v(-5272.73, 2786.7) * mm});
            skLineSegment(sketch, "E1705", {"start": v(-5272.73, 2786.7) * mm, "end": v(-5266.96, 2790.55) * mm});
            skLineSegment(sketch, "E1706", {"start": v(-5266.96, 2790.55) * mm, "end": v(-5260.5, 2795.07) * mm});
            skLineSegment(sketch, "E1707", {"start": v(-5260.5, 2795.07) * mm, "end": v(-5253.37, 2800.32) * mm});
            skLineSegment(sketch, "E1708", {"start": v(-5253.37, 2800.32) * mm, "end": v(-5245.61, 2806.3) * mm});
            skLineSegment(sketch, "E1709", {"start": v(-5245.61, 2806.3) * mm, "end": v(-5237.25, 2813.08) * mm});
            skLineSegment(sketch, "E1710", {"start": v(-5237.25, 2813.08) * mm, "end": v(-5228.32, 2820.67) * mm});
            skLineSegment(sketch, "E1711", {"start": v(-5228.32, 2820.67) * mm, "end": v(-5218.85, 2829.1) * mm});
            skLineSegment(sketch, "E1712", {"start": v(-5218.85, 2829.1) * mm, "end": v(-5208.89, 2838.4) * mm});
            skLineSegment(sketch, "E1713", {"start": v(-5208.89, 2838.4) * mm, "end": v(-5198.45, 2848.59) * mm});
            skLineSegment(sketch, "E1714", {"start": v(-5198.45, 2848.59) * mm, "end": v(-5187.6, 2859.7) * mm});
            skLineSegment(sketch, "E1715", {"start": v(-5187.6, 2859.7) * mm, "end": v(-5176.34, 2871.77) * mm});
            skLineSegment(sketch, "E1716", {"start": v(-5176.34, 2871.77) * mm, "end": v(-5164.74, 2884.82) * mm});
            skLineSegment(sketch, "E1717", {"start": v(-5164.74, 2884.82) * mm, "end": v(-5152.82, 2898.85) * mm});
            skLineSegment(sketch, "E1718", {"start": v(-5152.82, 2898.85) * mm, "end": v(-5140.64, 2913.9) * mm});
            skLineSegment(sketch, "E1719", {"start": v(-5140.64, 2913.9) * mm, "end": v(-5128.22, 2930) * mm});
            skLineSegment(sketch, "E1720", {"start": v(-5128.22, 2930) * mm, "end": v(-5115.6, 2947.14) * mm});
            skLineSegment(sketch, "E1721", {"start": v(-5115.6, 2947.14) * mm, "end": v(-5102.85, 2965.36) * mm});
            skLineSegment(sketch, "E1722", {"start": v(-5102.85, 2965.36) * mm, "end": v(-5090, 2984.67) * mm});
            skLineSegment(sketch, "E1723", {"start": v(-5090, 2984.67) * mm, "end": v(-5077.08, 3005.07) * mm});
            skLineSegment(sketch, "E1724", {"start": v(-5077.08, 3005.07) * mm, "end": v(-5064.15, 3026.6) * mm});
            skLineSegment(sketch, "E1725", {"start": v(-5064.15, 3026.6) * mm, "end": v(-5051.25, 3049.25) * mm});
            skLineSegment(sketch, "E1726", {"start": v(-5051.25, 3049.25) * mm, "end": v(-5038.43, 3073.03) * mm});
            skLineSegment(sketch, "E1727", {"start": v(-5038.43, 3073.03) * mm, "end": v(-5025.73, 3097.96) * mm});
            skLineSegment(sketch, "E1728", {"start": v(-5025.73, 3097.96) * mm, "end": v(-5024.46, 3117.69) * mm});
            skLineSegment(sketch, "E1729", {"start": v(-5024.46, 3117.69) * mm, "end": v(-5087.6, 3222.6) * mm});
            skLineSegment(sketch, "E1730", {"start": v(-5087.6, 3222.6) * mm, "end": v(-5105.62, 3230.72) * mm});
            skLineSegment(sketch, "E1731", {"start": v(-5105.62, 3230.72) * mm, "end": v(-5133.6, 3231.17) * mm});
            skLineSegment(sketch, "E1732", {"start": v(-5133.6, 3231.17) * mm, "end": v(-5160.62, 3230.98) * mm});
            skLineSegment(sketch, "E1733", {"start": v(-5160.62, 3230.98) * mm, "end": v(-5186.67, 3230.2) * mm});
            skLineSegment(sketch, "E1734", {"start": v(-5186.67, 3230.2) * mm, "end": v(-5211.74, 3228.85) * mm});
            skLineSegment(sketch, "E1735", {"start": v(-5211.74, 3228.85) * mm, "end": v(-5235.82, 3227) * mm});
            skLineSegment(sketch, "E1736", {"start": v(-5235.82, 3227) * mm, "end": v(-5258.9, 3224.67) * mm});
            skLineSegment(sketch, "E1737", {"start": v(-5258.9, 3224.67) * mm, "end": v(-5280.97, 3221.94) * mm});
            skLineSegment(sketch, "E1738", {"start": v(-5280.97, 3221.94) * mm, "end": v(-5302.02, 3218.83) * mm});
            skLineSegment(sketch, "E1739", {"start": v(-5302.02, 3218.83) * mm, "end": v(-5322.05, 3215.39) * mm});
            skLineSegment(sketch, "E1740", {"start": v(-5322.05, 3215.39) * mm, "end": v(-5341.06, 3211.67) * mm});
            skLineSegment(sketch, "E1741", {"start": v(-5341.06, 3211.67) * mm, "end": v(-5359.05, 3207.71) * mm});
            skLineSegment(sketch, "E1742", {"start": v(-5359.05, 3207.71) * mm, "end": v(-5376, 3203.57) * mm});
            skLineSegment(sketch, "E1743", {"start": v(-5376, 3203.57) * mm, "end": v(-5391.93, 3199.28) * mm});
            skLineSegment(sketch, "E1744", {"start": v(-5391.93, 3199.28) * mm, "end": v(-5406.85, 3194.89) * mm});
            skLineSegment(sketch, "E1745", {"start": v(-5406.85, 3194.89) * mm, "end": v(-5420.74, 3190.45) * mm});
            skLineSegment(sketch, "E1746", {"start": v(-5420.74, 3190.45) * mm, "end": v(-5433.62, 3186) * mm});
            skLineSegment(sketch, "E1747", {"start": v(-5433.62, 3186) * mm, "end": v(-5445.5, 3181.58) * mm});
            skLineSegment(sketch, "E1748", {"start": v(-5445.5, 3181.58) * mm, "end": v(-5456.38, 3177.24) * mm});
            skLineSegment(sketch, "E1749", {"start": v(-5456.38, 3177.24) * mm, "end": v(-5466.29, 3173.02) * mm});
            skLineSegment(sketch, "E1750", {"start": v(-5466.29, 3173.02) * mm, "end": v(-5475.21, 3168.97) * mm});
            skLineSegment(sketch, "E1751", {"start": v(-5475.21, 3168.97) * mm, "end": v(-5483.18, 3165.13) * mm});
            skLineSegment(sketch, "E1752", {"start": v(-5483.18, 3165.13) * mm, "end": v(-5490.21, 3161.54) * mm});
            skLineSegment(sketch, "E1753", {"start": v(-5490.21, 3161.54) * mm, "end": v(-5496.31, 3158.24) * mm});
            skLineSegment(sketch, "E1754", {"start": v(-5496.31, 3158.24) * mm, "end": v(-5501.5, 3155.28) * mm});
            skLineSegment(sketch, "E1755", {"start": v(-5501.5, 3155.28) * mm, "end": v(-5505.8, 3152.69) * mm});
            skLineSegment(sketch, "E1756", {"start": v(-5505.8, 3152.69) * mm, "end": v(-5509.24, 3150.51) * mm});
            skLineSegment(sketch, "E1757", {"start": v(-5509.24, 3150.51) * mm, "end": v(-5511.82, 3148.79) * mm});
            skLineSegment(sketch, "E1758", {"start": v(-5511.82, 3148.79) * mm, "end": v(-5513.59, 3147.55) * mm});
            skLineSegment(sketch, "E1759", {"start": v(-5513.59, 3147.55) * mm, "end": v(-5514.55, 3146.84) * mm});
            skLineSegment(sketch, "E1760", {"start": v(-5514.55, 3146.84) * mm, "end": v(-5635.5, 3052.08) * mm});
            skLineSegment(sketch, "E1761", {"start": v(-5635.5, 3052.08) * mm, "end": v(-5825.93, 3256.02) * mm});
            skLineSegment(sketch, "E1762", {"start": v(-5825.93, 3256.02) * mm, "end": v(-5723.12, 3370.2) * mm});
            skLineSegment(sketch, "E1763", {"start": v(-5723.12, 3370.2) * mm, "end": v(-5722.35, 3371.12) * mm});
            skLineSegment(sketch, "E1764", {"start": v(-5722.35, 3371.12) * mm, "end": v(-5721, 3372.8) * mm});
            skLineSegment(sketch, "E1765", {"start": v(-5721, 3372.8) * mm, "end": v(-5719.1, 3375.26) * mm});
            skLineSegment(sketch, "E1766", {"start": v(-5719.1, 3375.26) * mm, "end": v(-5716.69, 3378.53) * mm});
            skLineSegment(sketch, "E1767", {"start": v(-5716.69, 3378.53) * mm, "end": v(-5713.8, 3382.65) * mm});
            skLineSegment(sketch, "E1768", {"start": v(-5713.8, 3382.65) * mm, "end": v(-5710.5, 3387.62) * mm});
            skLineSegment(sketch, "E1769", {"start": v(-5710.5, 3387.62) * mm, "end": v(-5706.79, 3393.48) * mm});
            skLineSegment(sketch, "E1770", {"start": v(-5706.79, 3393.48) * mm, "end": v(-5702.73, 3400.25) * mm});
            skLineSegment(sketch, "E1771", {"start": v(-5702.73, 3400.25) * mm, "end": v(-5698.35, 3407.94) * mm});
            skLineSegment(sketch, "E1772", {"start": v(-5698.35, 3407.94) * mm, "end": v(-5693.7, 3416.57) * mm});
            skLineSegment(sketch, "E1773", {"start": v(-5693.7, 3416.57) * mm, "end": v(-5688.81, 3426.16) * mm});
            skLineSegment(sketch, "E1774", {"start": v(-5688.81, 3426.16) * mm, "end": v(-5683.74, 3436.72) * mm});
            skLineSegment(sketch, "E1775", {"start": v(-5683.74, 3436.72) * mm, "end": v(-5678.52, 3448.27) * mm});
            skLineSegment(sketch, "E1776", {"start": v(-5678.52, 3448.27) * mm, "end": v(-5673.2, 3460.81) * mm});
            skLineSegment(sketch, "E1777", {"start": v(-5673.2, 3460.81) * mm, "end": v(-5667.81, 3474.37) * mm});
            skLineSegment(sketch, "E1778", {"start": v(-5667.81, 3474.37) * mm, "end": v(-5662.41, 3488.95) * mm});
            skLineSegment(sketch, "E1779", {"start": v(-5662.41, 3488.95) * mm, "end": v(-5657.04, 3504.55) * mm});
            skLineSegment(sketch, "E1780", {"start": v(-5657.04, 3504.55) * mm, "end": v(-5651.75, 3521.18) * mm});
            skLineSegment(sketch, "E1781", {"start": v(-5651.75, 3521.18) * mm, "end": v(-5646.57, 3538.85) * mm});
            skLineSegment(sketch, "E1782", {"start": v(-5646.57, 3538.85) * mm, "end": v(-5641.56, 3557.56) * mm});
            skLineSegment(sketch, "E1783", {"start": v(-5641.56, 3557.56) * mm, "end": v(-5636.76, 3577.3) * mm});
            skLineSegment(sketch, "E1784", {"start": v(-5636.76, 3577.3) * mm, "end": v(-5632.21, 3598.1) * mm});
            skLineSegment(sketch, "E1785", {"start": v(-5632.21, 3598.1) * mm, "end": v(-5627.97, 3619.93) * mm});
            skLineSegment(sketch, "E1786", {"start": v(-5627.97, 3619.93) * mm, "end": v(-5624.08, 3642.8) * mm});
            skLineSegment(sketch, "E1787", {"start": v(-5624.08, 3642.8) * mm, "end": v(-5620.58, 3666.7) * mm});
            skLineSegment(sketch, "E1788", {"start": v(-5620.58, 3666.7) * mm, "end": v(-5617.52, 3691.62) * mm});
            skLineSegment(sketch, "E1789", {"start": v(-5617.52, 3691.62) * mm, "end": v(-5614.95, 3717.55) * mm});
            skLineSegment(sketch, "E1790", {"start": v(-5614.95, 3717.55) * mm, "end": v(-5612.91, 3744.5) * mm});
            skLineSegment(sketch, "E1791", {"start": v(-5612.91, 3744.5) * mm, "end": v(-5611.45, 3772.44) * mm});
            skLineSegment(sketch, "E1792", {"start": v(-5611.45, 3772.44) * mm, "end": v(-5618.32, 3790.98) * mm});
            skLineSegment(sketch, "E1793", {"start": v(-5618.32, 3790.98) * mm, "end": v(-5718.66, 3861.14) * mm});
            skLineSegment(sketch, "E1794", {"start": v(-5718.66, 3861.14) * mm, "end": v(-5738.43, 3861.22) * mm});
            skLineSegment(sketch, "E1795", {"start": v(-5738.43, 3861.22) * mm, "end": v(-5764.17, 3850.26) * mm});
            skLineSegment(sketch, "E1796", {"start": v(-5764.17, 3850.26) * mm, "end": v(-5788.78, 3839.1) * mm});
            skLineSegment(sketch, "E1797", {"start": v(-5788.78, 3839.1) * mm, "end": v(-5812.26, 3827.78) * mm});
            skLineSegment(sketch, "E1798", {"start": v(-5812.26, 3827.78) * mm, "end": v(-5834.62, 3816.35) * mm});
            skLineSegment(sketch, "E1799", {"start": v(-5834.62, 3816.35) * mm, "end": v(-5855.86, 3804.86) * mm});
            skLineSegment(sketch, "E1800", {"start": v(-5855.86, 3804.86) * mm, "end": v(-5876, 3793.36) * mm});
            skLineSegment(sketch, "E1801", {"start": v(-5876, 3793.36) * mm, "end": v(-5895.05, 3781.88) * mm});
            skLineSegment(sketch, "E1802", {"start": v(-5895.05, 3781.88) * mm, "end": v(-5913.02, 3770.47) * mm});
            skLineSegment(sketch, "E1803", {"start": v(-5913.02, 3770.47) * mm, "end": v(-5929.92, 3759.19) * mm});
            skLineSegment(sketch, "E1804", {"start": v(-5929.92, 3759.19) * mm, "end": v(-5945.77, 3748.06) * mm});
            skLineSegment(sketch, "E1805", {"start": v(-5945.77, 3748.06) * mm, "end": v(-5960.59, 3737.13) * mm});
            skLineSegment(sketch, "E1806", {"start": v(-5960.59, 3737.13) * mm, "end": v(-5974.4, 3726.45) * mm});
            skLineSegment(sketch, "E1807", {"start": v(-5974.4, 3726.45) * mm, "end": v(-5987.2, 3716.05) * mm});
            skLineSegment(sketch, "E1808", {"start": v(-5987.2, 3716.05) * mm, "end": v(-5999.04, 3705.97) * mm});
            skLineSegment(sketch, "E1809", {"start": v(-5999.04, 3705.97) * mm, "end": v(-6009.93, 3696.26) * mm});
            skLineSegment(sketch, "E1810", {"start": v(-6009.93, 3696.26) * mm, "end": v(-6019.88, 3686.95) * mm});
            skLineSegment(sketch, "E1811", {"start": v(-6019.88, 3686.95) * mm, "end": v(-6028.94, 3678.09) * mm});
            skLineSegment(sketch, "E1812", {"start": v(-6028.94, 3678.09) * mm, "end": v(-6037.12, 3669.7) * mm});
            skLineSegment(sketch, "E1813", {"start": v(-6037.12, 3669.7) * mm, "end": v(-6044.45, 3661.82) * mm});
            skLineSegment(sketch, "E1814", {"start": v(-6044.45, 3661.82) * mm, "end": v(-6050.96, 3654.49) * mm});
            skLineSegment(sketch, "E1815", {"start": v(-6050.96, 3654.49) * mm, "end": v(-6056.68, 3647.74) * mm});
            skLineSegment(sketch, "E1816", {"start": v(-6056.68, 3647.74) * mm, "end": v(-6061.64, 3641.6) * mm});
            skLineSegment(sketch, "E1817", {"start": v(-6061.64, 3641.6) * mm, "end": v(-6065.87, 3636.1) * mm});
            skLineSegment(sketch, "E1818", {"start": v(-6065.87, 3636.1) * mm, "end": v(-6069.4, 3631.29) * mm});
            skLineSegment(sketch, "E1819", {"start": v(-6069.4, 3631.29) * mm, "end": v(-6072.28, 3627.17) * mm});
            skLineSegment(sketch, "E1820", {"start": v(-6072.28, 3627.17) * mm, "end": v(-6074.53, 3623.78) * mm});
            skLineSegment(sketch, "E1821", {"start": v(-6074.53, 3623.78) * mm, "end": v(-6076.2, 3621.16) * mm});
            skLineSegment(sketch, "E1822", {"start": v(-6076.2, 3621.16) * mm, "end": v(-6077.3, 3619.31) * mm});
            skLineSegment(sketch, "E1823", {"start": v(-6077.3, 3619.31) * mm, "end": v(-6077.9, 3618.27) * mm});
            skLineSegment(sketch, "E1824", {"start": v(-6077.9, 3618.27) * mm, "end": v(-6149.85, 3482.5) * mm});
            skLineSegment(sketch, "E1825", {"start": v(-6149.85, 3482.5) * mm, "end": v(-6406.76, 3591.36) * mm});
            skLineSegment(sketch, "E1826", {"start": v(-6406.76, 3591.36) * mm, "end": v(-6359.28, 3737.5) * mm});
            skLineSegment(sketch, "E1827", {"start": v(-6359.28, 3737.5) * mm, "end": v(-6358.95, 3738.64) * mm});
            skLineSegment(sketch, "E1828", {"start": v(-6358.95, 3738.64) * mm, "end": v(-6358.39, 3740.72) * mm});
            skLineSegment(sketch, "E1829", {"start": v(-6358.39, 3740.72) * mm, "end": v(-6357.66, 3743.74) * mm});
            skLineSegment(sketch, "E1830", {"start": v(-6357.66, 3743.74) * mm, "end": v(-6356.79, 3747.71) * mm});
            skLineSegment(sketch, "E1831", {"start": v(-6356.79, 3747.71) * mm, "end": v(-6355.83, 3752.64) * mm});
            skLineSegment(sketch, "E1832", {"start": v(-6355.83, 3752.64) * mm, "end": v(-6354.83, 3758.54) * mm});
            skLineSegment(sketch, "E1833", {"start": v(-6354.83, 3758.54) * mm, "end": v(-6353.83, 3765.4) * mm});
            skLineSegment(sketch, "E1834", {"start": v(-6353.83, 3765.4) * mm, "end": v(-6352.87, 3773.23) * mm});
            skLineSegment(sketch, "E1835", {"start": v(-6352.87, 3773.23) * mm, "end": v(-6352, 3782.04) * mm});
            skLineSegment(sketch, "E1836", {"start": v(-6352, 3782.04) * mm, "end": v(-6351.26, 3791.81) * mm});
            skLineSegment(sketch, "E1837", {"start": v(-6351.26, 3791.81) * mm, "end": v(-6350.7, 3802.56) * mm});
            skLineSegment(sketch, "E1838", {"start": v(-6350.7, 3802.56) * mm, "end": v(-6350.36, 3814.27) * mm});
            skLineSegment(sketch, "E1839", {"start": v(-6350.36, 3814.27) * mm, "end": v(-6350.28, 3826.94) * mm});
            skLineSegment(sketch, "E1840", {"start": v(-6350.28, 3826.94) * mm, "end": v(-6350.52, 3840.57) * mm});
            skLineSegment(sketch, "E1841", {"start": v(-6350.52, 3840.57) * mm, "end": v(-6351.12, 3855.14) * mm});
            skLineSegment(sketch, "E1842", {"start": v(-6351.12, 3855.14) * mm, "end": v(-6352.12, 3870.66) * mm});
            skLineSegment(sketch, "E1843", {"start": v(-6352.12, 3870.66) * mm, "end": v(-6353.56, 3887.1) * mm});
            skLineSegment(sketch, "E1844", {"start": v(-6353.56, 3887.1) * mm, "end": v(-6355.48, 3904.44) * mm});
            skLineSegment(sketch, "E1845", {"start": v(-6355.48, 3904.44) * mm, "end": v(-6357.94, 3922.7) * mm});
            skLineSegment(sketch, "E1846", {"start": v(-6357.94, 3922.7) * mm, "end": v(-6360.98, 3941.82) * mm});
            skLineSegment(sketch, "E1847", {"start": v(-6360.98, 3941.82) * mm, "end": v(-6364.62, 3961.82) * mm});
            skLineSegment(sketch, "E1848", {"start": v(-6364.62, 3961.82) * mm, "end": v(-6368.93, 3982.66) * mm});
            skLineSegment(sketch, "E1849", {"start": v(-6368.93, 3982.66) * mm, "end": v(-6373.93, 4004.33) * mm});
            skLineSegment(sketch, "E1850", {"start": v(-6373.93, 4004.33) * mm, "end": v(-6379.68, 4026.8) * mm});
            skLineSegment(sketch, "E1851", {"start": v(-6379.68, 4026.8) * mm, "end": v(-6386.2, 4050.05) * mm});
            skLineSegment(sketch, "E1852", {"start": v(-6386.2, 4050.05) * mm, "end": v(-6393.54, 4074.06) * mm});
            skLineSegment(sketch, "E1853", {"start": v(-6393.54, 4074.06) * mm, "end": v(-6401.74, 4098.8) * mm});
            skLineSegment(sketch, "E1854", {"start": v(-6401.74, 4098.8) * mm, "end": v(-6410.84, 4124.25) * mm});
            skLineSegment(sketch, "E1855", {"start": v(-6410.84, 4124.25) * mm, "end": v(-6420.87, 4150.37) * mm});
            skLineSegment(sketch, "E1856", {"start": v(-6420.87, 4150.37) * mm, "end": v(-6434.68, 4164.51) * mm});
            skLineSegment(sketch, "E1857", {"start": v(-6434.68, 4164.51) * mm, "end": v(-6554.89, 4187.8) * mm});
            skLineSegment(sketch, "E1858", {"start": v(-6554.89, 4187.8) * mm, "end": v(-6572.99, 4179.83) * mm});
            skLineSegment(sketch, "E1859", {"start": v(-6572.99, 4179.83) * mm, "end": v(-6592.04, 4159.35) * mm});
            skLineSegment(sketch, "E1860", {"start": v(-6592.04, 4159.35) * mm, "end": v(-6609.98, 4139.14) * mm});
            skLineSegment(sketch, "E1861", {"start": v(-6609.98, 4139.14) * mm, "end": v(-6626.82, 4119.25) * mm});
            skLineSegment(sketch, "E1862", {"start": v(-6626.82, 4119.25) * mm, "end": v(-6642.6, 4099.72) * mm});
            skLineSegment(sketch, "E1863", {"start": v(-6642.6, 4099.72) * mm, "end": v(-6657.33, 4080.58) * mm});
            skLineSegment(sketch, "E1864", {"start": v(-6657.33, 4080.58) * mm, "end": v(-6671.05, 4061.88) * mm});
            skLineSegment(sketch, "E1865", {"start": v(-6671.05, 4061.88) * mm, "end": v(-6683.79, 4043.64) * mm});
            skLineSegment(sketch, "E1866", {"start": v(-6683.79, 4043.64) * mm, "end": v(-6695.56, 4025.92) * mm});
            skLineSegment(sketch, "E1867", {"start": v(-6695.56, 4025.92) * mm, "end": v(-6706.41, 4008.73) * mm});
            skLineSegment(sketch, "E1868", {"start": v(-6706.41, 4008.73) * mm, "end": v(-6716.37, 3992.11) * mm});
            skLineSegment(sketch, "E1869", {"start": v(-6716.37, 3992.11) * mm, "end": v(-6725.46, 3976.1) * mm});
            skLineSegment(sketch, "E1870", {"start": v(-6725.46, 3976.1) * mm, "end": v(-6733.73, 3960.73) * mm});
            skLineSegment(sketch, "E1871", {"start": v(-6733.73, 3960.73) * mm, "end": v(-6741.2, 3946.02) * mm});
            skLineSegment(sketch, "E1872", {"start": v(-6741.2, 3946.02) * mm, "end": v(-6747.91, 3932) * mm});
            skLineSegment(sketch, "E1873", {"start": v(-6747.91, 3932) * mm, "end": v(-6753.9, 3918.7) * mm});
            skLineSegment(sketch, "E1874", {"start": v(-6753.9, 3918.7) * mm, "end": v(-6759.22, 3906.15) * mm});
            skLineSegment(sketch, "E1875", {"start": v(-6759.22, 3906.15) * mm, "end": v(-6763.89, 3894.37) * mm});
            skLineSegment(sketch, "E1876", {"start": v(-6763.89, 3894.37) * mm, "end": v(-6767.94, 3883.38) * mm});
            skLineSegment(sketch, "E1877", {"start": v(-6767.94, 3883.38) * mm, "end": v(-6771.44, 3873.2) * mm});
            skLineSegment(sketch, "E1878", {"start": v(-6771.44, 3873.2) * mm, "end": v(-6774.4, 3863.85) * mm});
            skLineSegment(sketch, "E1879", {"start": v(-6774.4, 3863.85) * mm, "end": v(-6776.88, 3855.36) * mm});
            skLineSegment(sketch, "E1880", {"start": v(-6776.88, 3855.36) * mm, "end": v(-6778.91, 3847.73) * mm});
            skLineSegment(sketch, "E1881", {"start": v(-6778.91, 3847.73) * mm, "end": v(-6780.54, 3841) * mm});
            skLineSegment(sketch, "E1882", {"start": v(-6780.54, 3841) * mm, "end": v(-6781.82, 3835.15) * mm});
            skLineSegment(sketch, "E1883", {"start": v(-6781.82, 3835.15) * mm, "end": v(-6782.77, 3830.22) * mm});
            skLineSegment(sketch, "E1884", {"start": v(-6782.77, 3830.22) * mm, "end": v(-6783.45, 3826.22) * mm});
            skLineSegment(sketch, "E1885", {"start": v(-6783.45, 3826.22) * mm, "end": v(-6783.9, 3823.14) * mm});
            skLineSegment(sketch, "E1886", {"start": v(-6783.9, 3823.14) * mm, "end": v(-6784.16, 3821) * mm});
            skLineSegment(sketch, "E1887", {"start": v(-6784.16, 3821) * mm, "end": v(-6784.28, 3819.81) * mm});
            skLineSegment(sketch, "E1888", {"start": v(-6784.28, 3819.81) * mm, "end": v(-6794.8, 3666.52) * mm});
            skLineSegment(sketch, "E1889", {"start": v(-6794.8, 3666.52) * mm, "end": v(-7073.76, 3661.46) * mm});
            skLineSegment(sketch, "E1890", {"start": v(-7073.76, 3661.46) * mm, "end": v(-7089.83, 3814.28) * mm});
            skLineSegment(sketch, "E1891", {"start": v(-7089.83, 3814.28) * mm, "end": v(-7090, 3815.46) * mm});
            skLineSegment(sketch, "E1892", {"start": v(-7090, 3815.46) * mm, "end": v(-7090.33, 3817.59) * mm});
            skLineSegment(sketch, "E1893", {"start": v(-7090.33, 3817.59) * mm, "end": v(-7090.89, 3820.64) * mm});
            skLineSegment(sketch, "E1894", {"start": v(-7090.89, 3820.64) * mm, "end": v(-7091.71, 3824.62) * mm});
            skLineSegment(sketch, "E1895", {"start": v(-7091.71, 3824.62) * mm, "end": v(-7092.84, 3829.52) * mm});
            skLineSegment(sketch, "E1896", {"start": v(-7092.84, 3829.52) * mm, "end": v(-7094.33, 3835.3) * mm});
            skLineSegment(sketch, "E1897", {"start": v(-7094.33, 3835.3) * mm, "end": v(-7096.2, 3841.99) * mm});
            skLineSegment(sketch, "E1898", {"start": v(-7096.2, 3841.99) * mm, "end": v(-7098.5, 3849.53) * mm});
            skLineSegment(sketch, "E1899", {"start": v(-7098.5, 3849.53) * mm, "end": v(-7101.3, 3857.93) * mm});
            skLineSegment(sketch, "E1900", {"start": v(-7101.3, 3857.93) * mm, "end": v(-7104.6, 3867.16) * mm});
            skLineSegment(sketch, "E1901", {"start": v(-7104.6, 3867.16) * mm, "end": v(-7108.45, 3877.2) * mm});
            skLineSegment(sketch, "E1902", {"start": v(-7108.45, 3877.2) * mm, "end": v(-7112.9, 3888.04) * mm});
            skLineSegment(sketch, "E1903", {"start": v(-7112.9, 3888.04) * mm, "end": v(-7118, 3899.65) * mm});
            skLineSegment(sketch, "E1904", {"start": v(-7118, 3899.65) * mm, "end": v(-7123.76, 3912) * mm});
            skLineSegment(sketch, "E1905", {"start": v(-7123.76, 3912) * mm, "end": v(-7130.23, 3925.07) * mm});
            skLineSegment(sketch, "E1906", {"start": v(-7130.23, 3925.07) * mm, "end": v(-7137.45, 3938.84) * mm});
            skLineSegment(sketch, "E1907", {"start": v(-7137.45, 3938.84) * mm, "end": v(-7145.45, 3953.27) * mm});
            skLineSegment(sketch, "E1908", {"start": v(-7145.45, 3953.27) * mm, "end": v(-7154.27, 3968.34) * mm});
            skLineSegment(sketch, "E1909", {"start": v(-7154.27, 3968.34) * mm, "end": v(-7163.93, 3984) * mm});
            skLineSegment(sketch, "E1910", {"start": v(-7163.93, 3984) * mm, "end": v(-7174.49, 4000.25) * mm});
            skLineSegment(sketch, "E1911", {"start": v(-7174.49, 4000.25) * mm, "end": v(-7185.95, 4017.03) * mm});
            skLineSegment(sketch, "E1912", {"start": v(-7185.95, 4017.03) * mm, "end": v(-7198.36, 4034.32) * mm});
            skLineSegment(sketch, "E1913", {"start": v(-7198.36, 4034.32) * mm, "end": v(-7211.75, 4052.08) * mm});
            skLineSegment(sketch, "E1914", {"start": v(-7211.75, 4052.08) * mm, "end": v(-7226.13, 4070.27) * mm});
            skLineSegment(sketch, "E1915", {"start": v(-7226.13, 4070.27) * mm, "end": v(-7241.55, 4088.86) * mm});
            skLineSegment(sketch, "E1916", {"start": v(-7241.55, 4088.86) * mm, "end": v(-7258.03, 4107.81) * mm});
            skLineSegment(sketch, "E1917", {"start": v(-7258.03, 4107.81) * mm, "end": v(-7275.58, 4127.08) * mm});
            skLineSegment(sketch, "E1918", {"start": v(-7275.58, 4127.08) * mm, "end": v(-7294.24, 4146.62) * mm});
            skLineSegment(sketch, "E1919", {"start": v(-7294.24, 4146.62) * mm, "end": v(-7314.02, 4166.4) * mm});
            skLineSegment(sketch, "E1920", {"start": v(-7314.02, 4166.4) * mm, "end": v(-7332.4, 4173.7) * mm});
            skLineSegment(sketch, "E1921", {"start": v(-7332.4, 4173.7) * mm, "end": v(-7451.68, 4146.08) * mm});
            skLineSegment(sketch, "E1922", {"start": v(-7451.68, 4146.08) * mm, "end": v(-7464.97, 4131.45) * mm});
            skLineSegment(sketch, "E1923", {"start": v(-7464.97, 4131.45) * mm, "end": v(-7474.05, 4104.99) * mm});
            skLineSegment(sketch, "E1924", {"start": v(-7474.05, 4104.99) * mm, "end": v(-7482.22, 4079.23) * mm});
            skLineSegment(sketch, "E1925", {"start": v(-7482.22, 4079.23) * mm, "end": v(-7489.52, 4054.2) * mm});
            skLineSegment(sketch, "E1926", {"start": v(-7489.52, 4054.2) * mm, "end": v(-7495.99, 4029.95) * mm});
            skLineSegment(sketch, "E1927", {"start": v(-7495.99, 4029.95) * mm, "end": v(-7501.66, 4006.47) * mm});
            skLineSegment(sketch, "E1928", {"start": v(-7501.66, 4006.47) * mm, "end": v(-7506.59, 3983.8) * mm});
            skLineSegment(sketch, "E1929", {"start": v(-7506.59, 3983.8) * mm, "end": v(-7510.8, 3961.97) * mm});
            skLineSegment(sketch, "E1930", {"start": v(-7510.8, 3961.97) * mm, "end": v(-7514.35, 3940.98) * mm});
            skLineSegment(sketch, "E1931", {"start": v(-7514.35, 3940.98) * mm, "end": v(-7517.27, 3920.87) * mm});
            skLineSegment(sketch, "E1932", {"start": v(-7517.27, 3920.87) * mm, "end": v(-7519.6, 3901.64) * mm});
            skLineSegment(sketch, "E1933", {"start": v(-7519.6, 3901.64) * mm, "end": v(-7521.4, 3883.32) * mm});
            skLineSegment(sketch, "E1934", {"start": v(-7521.4, 3883.32) * mm, "end": v(-7522.7, 3865.91) * mm});
            skLineSegment(sketch, "E1935", {"start": v(-7522.7, 3865.91) * mm, "end": v(-7523.55, 3849.43) * mm});
            skLineSegment(sketch, "E1936", {"start": v(-7523.55, 3849.43) * mm, "end": v(-7523.98, 3833.9) * mm});
            skLineSegment(sketch, "E1937", {"start": v(-7523.98, 3833.9) * mm, "end": v(-7524.05, 3819.3) * mm});
            skLineSegment(sketch, "E1938", {"start": v(-7524.05, 3819.3) * mm, "end": v(-7523.8, 3805.68) * mm});
            skLineSegment(sketch, "E1939", {"start": v(-7523.8, 3805.68) * mm, "end": v(-7523.26, 3793.02) * mm});
            skLineSegment(sketch, "E1940", {"start": v(-7523.26, 3793.02) * mm, "end": v(-7522.5, 3781.33) * mm});
            skLineSegment(sketch, "E1941", {"start": v(-7522.5, 3781.33) * mm, "end": v(-7521.55, 3770.6) * mm});
            skLineSegment(sketch, "E1942", {"start": v(-7521.55, 3770.6) * mm, "end": v(-7520.46, 3760.87) * mm});
            skLineSegment(sketch, "E1943", {"start": v(-7520.46, 3760.87) * mm, "end": v(-7519.27, 3752.1) * mm});
            skLineSegment(sketch, "E1944", {"start": v(-7519.27, 3752.1) * mm, "end": v(-7518.02, 3744.3) * mm});
            skLineSegment(sketch, "E1945", {"start": v(-7518.02, 3744.3) * mm, "end": v(-7516.77, 3737.48) * mm});
            skLineSegment(sketch, "E1946", {"start": v(-7516.77, 3737.48) * mm, "end": v(-7515.56, 3731.63) * mm});
            skLineSegment(sketch, "E1947", {"start": v(-7515.56, 3731.63) * mm, "end": v(-7514.42, 3726.74) * mm});
            skLineSegment(sketch, "E1948", {"start": v(-7514.42, 3726.74) * mm, "end": v(-7513.41, 3722.8) * mm});
            skLineSegment(sketch, "E1949", {"start": v(-7513.41, 3722.8) * mm, "end": v(-7512.57, 3719.8) * mm});
            skLineSegment(sketch, "E1950", {"start": v(-7512.57, 3719.8) * mm, "end": v(-7511.94, 3717.75) * mm});
            skLineSegment(sketch, "E1951", {"start": v(-7511.94, 3717.75) * mm, "end": v(-7511.57, 3716.62) * mm});
            skLineSegment(sketch, "E1952", {"start": v(-7511.57, 3716.62) * mm, "end": v(-7458.82, 3572.3) * mm});
            skLineSegment(sketch, "E1953", {"start": v(-7458.82, 3572.3) * mm, "end": v(-7711.62, 3454.21) * mm});
            skLineSegment(sketch, "E1954", {"start": v(-7711.62, 3454.21) * mm, "end": v(-7788.45, 3587.28) * mm});
            skLineSegment(sketch, "E1955", {"start": v(-7788.45, 3587.28) * mm, "end": v(-7789.08, 3588.3) * mm});
            skLineSegment(sketch, "E1956", {"start": v(-7789.08, 3588.3) * mm, "end": v(-7790.25, 3590.1) * mm});
            skLineSegment(sketch, "E1957", {"start": v(-7790.25, 3590.1) * mm, "end": v(-7792, 3592.67) * mm});
            skLineSegment(sketch, "E1958", {"start": v(-7792, 3592.67) * mm, "end": v(-7794.38, 3595.97) * mm});
            skLineSegment(sketch, "E1959", {"start": v(-7794.38, 3595.97) * mm, "end": v(-7797.4, 3599.98) * mm});
            skLineSegment(sketch, "E1960", {"start": v(-7797.4, 3599.98) * mm, "end": v(-7801.11, 3604.66) * mm});
            skLineSegment(sketch, "E1961", {"start": v(-7801.11, 3604.66) * mm, "end": v(-7805.54, 3610) * mm});
            skLineSegment(sketch, "E1962", {"start": v(-7805.54, 3610) * mm, "end": v(-7810.72, 3615.96) * mm});
            skLineSegment(sketch, "E1963", {"start": v(-7810.72, 3615.96) * mm, "end": v(-7816.68, 3622.5) * mm});
            skLineSegment(sketch, "E1964", {"start": v(-7816.68, 3622.5) * mm, "end": v(-7823.45, 3629.59) * mm});
            skLineSegment(sketch, "E1965", {"start": v(-7823.45, 3629.59) * mm, "end": v(-7831.06, 3637.2) * mm});
            skLineSegment(sketch, "E1966", {"start": v(-7831.06, 3637.2) * mm, "end": v(-7839.54, 3645.28) * mm});
            skLineSegment(sketch, "E1967", {"start": v(-7839.54, 3645.28) * mm, "end": v(-7848.9, 3653.82) * mm});
            skLineSegment(sketch, "E1968", {"start": v(-7848.9, 3653.82) * mm, "end": v(-7859.2, 3662.76) * mm});
            skLineSegment(sketch, "E1969", {"start": v(-7859.2, 3662.76) * mm, "end": v(-7870.42, 3672.07) * mm});
            skLineSegment(sketch, "E1970", {"start": v(-7870.42, 3672.07) * mm, "end": v(-7882.62, 3681.7) * mm});
            skLineSegment(sketch, "E1971", {"start": v(-7882.62, 3681.7) * mm, "end": v(-7895.8, 3691.63) * mm});
            skLineSegment(sketch, "E1972", {"start": v(-7895.8, 3691.63) * mm, "end": v(-7909.98, 3701.81) * mm});
            skLineSegment(sketch, "E1973", {"start": v(-7909.98, 3701.81) * mm, "end": v(-7925.18, 3712.2) * mm});
            skLineSegment(sketch, "E1974", {"start": v(-7925.18, 3712.2) * mm, "end": v(-7941.43, 3722.74) * mm});
            skLineSegment(sketch, "E1975", {"start": v(-7941.43, 3722.74) * mm, "end": v(-7958.73, 3733.4) * mm});
            skLineSegment(sketch, "E1976", {"start": v(-7958.73, 3733.4) * mm, "end": v(-7977.1, 3744.15) * mm});
            skLineSegment(sketch, "E1977", {"start": v(-7977.1, 3744.15) * mm, "end": v(-7996.55, 3754.93) * mm});
            skLineSegment(sketch, "E1978", {"start": v(-7996.55, 3754.93) * mm, "end": v(-8017.1, 3765.7) * mm});
            skLineSegment(sketch, "E1979", {"start": v(-8017.1, 3765.7) * mm, "end": v(-8038.74, 3776.42) * mm});
            skLineSegment(sketch, "E1980", {"start": v(-8038.74, 3776.42) * mm, "end": v(-8061.5, 3787.03) * mm});
            skLineSegment(sketch, "E1981", {"start": v(-8061.5, 3787.03) * mm, "end": v(-8085.37, 3797.49) * mm});
            skLineSegment(sketch, "E1982", {"start": v(-8085.37, 3797.49) * mm, "end": v(-8110.36, 3807.75) * mm});
            skLineSegment(sketch, "E1983", {"start": v(-8110.36, 3807.75) * mm, "end": v(-8136.49, 3817.78) * mm});
            skLineSegment(sketch, "E1984", {"start": v(-8136.49, 3817.78) * mm, "end": v(-8156.24, 3816.98) * mm});
            skLineSegment(sketch, "E1985", {"start": v(-8156.24, 3816.98) * mm, "end": v(-8253.98, 3743.22) * mm});
            skLineSegment(sketch, "E1986", {"start": v(-8253.98, 3743.22) * mm, "end": v(-8260.17, 3724.45) * mm});
            skLineSegment(sketch, "E1987", {"start": v(-8260.17, 3724.45) * mm, "end": v(-8257.7, 3696.58) * mm});
            skLineSegment(sketch, "E1988", {"start": v(-8257.7, 3696.58) * mm, "end": v(-8254.68, 3669.72) * mm});
            skLineSegment(sketch, "E1989", {"start": v(-8254.68, 3669.72) * mm, "end": v(-8251.17, 3643.9) * mm});
            skLineSegment(sketch, "E1990", {"start": v(-8251.17, 3643.9) * mm, "end": v(-8247.21, 3619.1) * mm});
            skLineSegment(sketch, "E1991", {"start": v(-8247.21, 3619.1) * mm, "end": v(-8242.85, 3595.35) * mm});
            skLineSegment(sketch, "E1992", {"start": v(-8242.85, 3595.35) * mm, "end": v(-8238.13, 3572.64) * mm});
            skLineSegment(sketch, "E1993", {"start": v(-8238.13, 3572.64) * mm, "end": v(-8233.1, 3550.98) * mm});
            skLineSegment(sketch, "E1994", {"start": v(-8233.1, 3550.98) * mm, "end": v(-8227.8, 3530.36) * mm});
            skLineSegment(sketch, "E1995", {"start": v(-8227.8, 3530.36) * mm, "end": v(-8222.3, 3510.8) * mm});
            skLineSegment(sketch, "E1996", {"start": v(-8222.3, 3510.8) * mm, "end": v(-8216.6, 3492.28) * mm});
            skLineSegment(sketch, "E1997", {"start": v(-8216.6, 3492.28) * mm, "end": v(-8210.8, 3474.81) * mm});
            skLineSegment(sketch, "E1998", {"start": v(-8210.8, 3474.81) * mm, "end": v(-8204.9, 3458.38) * mm});
            skLineSegment(sketch, "E1999", {"start": v(-8204.9, 3458.38) * mm, "end": v(-8198.97, 3442.99) * mm});
            skLineSegment(sketch, "E2000", {"start": v(-8198.97, 3442.99) * mm, "end": v(-8193.05, 3428.62) * mm});
            skLineSegment(sketch, "E2001", {"start": v(-8193.05, 3428.62) * mm, "end": v(-8187.18, 3415.26) * mm});
            skLineSegment(sketch, "E2002", {"start": v(-8187.18, 3415.26) * mm, "end": v(-8181.4, 3402.92) * mm});
            skLineSegment(sketch, "E2003", {"start": v(-8181.4, 3402.92) * mm, "end": v(-8175.76, 3391.57) * mm});
            skLineSegment(sketch, "E2004", {"start": v(-8175.76, 3391.57) * mm, "end": v(-8170.31, 3381.2) * mm});
            skLineSegment(sketch, "E2005", {"start": v(-8170.31, 3381.2) * mm, "end": v(-8165.08, 3371.8) * mm});
            skLineSegment(sketch, "E2006", {"start": v(-8165.08, 3371.8) * mm, "end": v(-8160.12, 3363.33) * mm});
            skLineSegment(sketch, "E2007", {"start": v(-8160.12, 3363.33) * mm, "end": v(-8155.47, 3355.8) * mm});
            skLineSegment(sketch, "E2008", {"start": v(-8155.47, 3355.8) * mm, "end": v(-8151.17, 3349.2) * mm});
            skLineSegment(sketch, "E2009", {"start": v(-8151.17, 3349.2) * mm, "end": v(-8147.25, 3343.47) * mm});
            skLineSegment(sketch, "E2010", {"start": v(-8147.25, 3343.47) * mm, "end": v(-8143.76, 3338.62) * mm});
            skLineSegment(sketch, "E2011", {"start": v(-8143.76, 3338.62) * mm, "end": v(-8140.73, 3334.61) * mm});
            skLineSegment(sketch, "E2012", {"start": v(-8140.73, 3334.61) * mm, "end": v(-8138.2, 3331.43) * mm});
            skLineSegment(sketch, "E2013", {"start": v(-8138.2, 3331.43) * mm, "end": v(-8136.22, 3329.03) * mm});
            skLineSegment(sketch, "E2014", {"start": v(-8136.22, 3329.03) * mm, "end": v(-8134.8, 3327.41) * mm});
            skLineSegment(sketch, "E2015", {"start": v(-8134.8, 3327.41) * mm, "end": v(-8134, 3326.53) * mm});
            skLineSegment(sketch, "E2016", {"start": v(-8134, 3326.53) * mm, "end": v(-8027.12, 3216.14) * mm});
            skLineSegment(sketch, "E2017", {"start": v(-8027.12, 3216.14) * mm, "end": v(-8210.03, 3005.44) * mm});
            skLineSegment(sketch, "E2018", {"start": v(-8210.03, 3005.44) * mm, "end": v(-8334.35, 3095.75) * mm});
            skLineSegment(sketch, "E2019", {"start": v(-8334.35, 3095.75) * mm, "end": v(-8335.33, 3096.42) * mm});
            skLineSegment(sketch, "E2020", {"start": v(-8335.33, 3096.42) * mm, "end": v(-8337.14, 3097.6) * mm});
            skLineSegment(sketch, "E2021", {"start": v(-8337.14, 3097.6) * mm, "end": v(-8339.79, 3099.23) * mm});
            skLineSegment(sketch, "E2022", {"start": v(-8339.79, 3099.23) * mm, "end": v(-8343.3, 3101.28) * mm});
            skLineSegment(sketch, "E2023", {"start": v(-8343.3, 3101.28) * mm, "end": v(-8347.69, 3103.7) * mm});
            skLineSegment(sketch, "E2024", {"start": v(-8347.69, 3103.7) * mm, "end": v(-8352.98, 3106.48) * mm});
            skLineSegment(sketch, "E2025", {"start": v(-8352.98, 3106.48) * mm, "end": v(-8359.2, 3109.56) * mm});
            skLineSegment(sketch, "E2026", {"start": v(-8359.2, 3109.56) * mm, "end": v(-8366.35, 3112.9) * mm});
            skLineSegment(sketch, "E2027", {"start": v(-8366.35, 3112.9) * mm, "end": v(-8374.46, 3116.44) * mm});
            skLineSegment(sketch, "E2028", {"start": v(-8374.46, 3116.44) * mm, "end": v(-8383.53, 3120.17) * mm});
            skLineSegment(sketch, "E2029", {"start": v(-8383.53, 3120.17) * mm, "end": v(-8393.57, 3124.02) * mm});
            skLineSegment(sketch, "E2030", {"start": v(-8393.57, 3124.02) * mm, "end": v(-8404.6, 3127.96) * mm});
            skLineSegment(sketch, "E2031", {"start": v(-8404.6, 3127.96) * mm, "end": v(-8416.64, 3131.95) * mm});
            skLineSegment(sketch, "E2032", {"start": v(-8416.64, 3131.95) * mm, "end": v(-8429.67, 3135.93) * mm});
            skLineSegment(sketch, "E2033", {"start": v(-8429.67, 3135.93) * mm, "end": v(-8443.72, 3139.87) * mm});
            skLineSegment(sketch, "E2034", {"start": v(-8443.72, 3139.87) * mm, "end": v(-8458.78, 3143.71) * mm});
            skLineSegment(sketch, "E2035", {"start": v(-8458.78, 3143.71) * mm, "end": v(-8474.85, 3147.42) * mm});
            skLineSegment(sketch, "E2036", {"start": v(-8474.85, 3147.42) * mm, "end": v(-8491.95, 3150.95) * mm});
            skLineSegment(sketch, "E2037", {"start": v(-8491.95, 3150.95) * mm, "end": v(-8510.07, 3154.25) * mm});
            skLineSegment(sketch, "E2038", {"start": v(-8510.07, 3154.25) * mm, "end": v(-8529.2, 3157.28) * mm});
            skLineSegment(sketch, "E2039", {"start": v(-8529.2, 3157.28) * mm, "end": v(-8549.34, 3159.99) * mm});
            skLineSegment(sketch, "E2040", {"start": v(-8549.34, 3159.99) * mm, "end": v(-8570.5, 3162.33) * mm});
            skLineSegment(sketch, "E2041", {"start": v(-8570.5, 3162.33) * mm, "end": v(-8592.65, 3164.27) * mm});
            skLineSegment(sketch, "E2042", {"start": v(-8592.65, 3164.27) * mm, "end": v(-8615.8, 3165.75) * mm});
            skLineSegment(sketch, "E2043", {"start": v(-8615.8, 3165.75) * mm, "end": v(-8639.93, 3166.73) * mm});
            skLineSegment(sketch, "E2044", {"start": v(-8639.93, 3166.73) * mm, "end": v(-8665.03, 3167.17) * mm});
            skLineSegment(sketch, "E2045", {"start": v(-8665.03, 3167.17) * mm, "end": v(-8691.1, 3167.02) * mm});
            skLineSegment(sketch, "E2046", {"start": v(-8691.1, 3167.02) * mm, "end": v(-8718.1, 3166.23) * mm});
            skLineSegment(sketch, "E2047", {"start": v(-8718.1, 3166.23) * mm, "end": v(-8746.04, 3164.76) * mm});
            skLineSegment(sketch, "E2048", {"start": v(-8746.04, 3164.76) * mm, "end": v(-8763.76, 3156) * mm});
            skLineSegment(sketch, "E2049", {"start": v(-8763.76, 3156) * mm, "end": v(-8823.05, 3048.87) * mm});
            skLineSegment(sketch, "E2050", {"start": v(-8823.05, 3048.87) * mm, "end": v(-8821.07, 3029.2) * mm});
            skLineSegment(sketch, "E2051", {"start": v(-8821.07, 3029.2) * mm, "end": v(-8807.48, 3004.74) * mm});
            skLineSegment(sketch, "E2052", {"start": v(-8807.48, 3004.74) * mm, "end": v(-8793.8, 2981.44) * mm});
            skLineSegment(sketch, "E2053", {"start": v(-8793.8, 2981.44) * mm, "end": v(-8780.1, 2959.27) * mm});
            skLineSegment(sketch, "E2054", {"start": v(-8780.1, 2959.27) * mm, "end": v(-8766.39, 2938.23) * mm});
            skLineSegment(sketch, "E2055", {"start": v(-8766.39, 2938.23) * mm, "end": v(-8752.74, 2918.3) * mm});
            skLineSegment(sketch, "E2056", {"start": v(-8752.74, 2918.3) * mm, "end": v(-8739.2, 2899.48) * mm});
            skLineSegment(sketch, "E2057", {"start": v(-8739.2, 2899.48) * mm, "end": v(-8725.8, 2881.73) * mm});
            skLineSegment(sketch, "E2058", {"start": v(-8725.8, 2881.73) * mm, "end": v(-8712.57, 2865.05) * mm});
            skLineSegment(sketch, "E2059", {"start": v(-8712.57, 2865.05) * mm, "end": v(-8699.58, 2849.42) * mm});
            skLineSegment(sketch, "E2060", {"start": v(-8699.58, 2849.42) * mm, "end": v(-8686.85, 2834.82) * mm});
            skLineSegment(sketch, "E2061", {"start": v(-8686.85, 2834.82) * mm, "end": v(-8674.43, 2821.23) * mm});
            skLineSegment(sketch, "E2062", {"start": v(-8674.43, 2821.23) * mm, "end": v(-8662.37, 2808.61) * mm});
            skLineSegment(sketch, "E2063", {"start": v(-8662.37, 2808.61) * mm, "end": v(-8650.69, 2796.96) * mm});
            skLineSegment(sketch, "E2064", {"start": v(-8650.69, 2796.96) * mm, "end": v(-8639.43, 2786.24) * mm});
            skLineSegment(sketch, "E2065", {"start": v(-8639.43, 2786.24) * mm, "end": v(-8628.63, 2776.43) * mm});
            skLineSegment(sketch, "E2066", {"start": v(-8628.63, 2776.43) * mm, "end": v(-8618.34, 2767.5) * mm});
            skLineSegment(sketch, "E2067", {"start": v(-8618.34, 2767.5) * mm, "end": v(-8608.57, 2759.43) * mm});
            skLineSegment(sketch, "E2068", {"start": v(-8608.57, 2759.43) * mm, "end": v(-8599.37, 2752.17) * mm});
            skLineSegment(sketch, "E2069", {"start": v(-8599.37, 2752.17) * mm, "end": v(-8590.77, 2745.7) * mm});
            skLineSegment(sketch, "E2070", {"start": v(-8590.77, 2745.7) * mm, "end": v(-8582.8, 2740) * mm});
            skLineSegment(sketch, "E2071", {"start": v(-8582.8, 2740) * mm, "end": v(-8575.49, 2735.01) * mm});
            skLineSegment(sketch, "E2072", {"start": v(-8575.49, 2735.01) * mm, "end": v(-8568.87, 2730.72) * mm});
            skLineSegment(sketch, "E2073", {"start": v(-8568.87, 2730.72) * mm, "end": v(-8562.96, 2727.09) * mm});
            skLineSegment(sketch, "E2074", {"start": v(-8562.96, 2727.09) * mm, "end": v(-8557.8, 2724.07) * mm});
            skLineSegment(sketch, "E2075", {"start": v(-8557.8, 2724.07) * mm, "end": v(-8553.4, 2721.64) * mm});
            skLineSegment(sketch, "E2076", {"start": v(-8553.4, 2721.64) * mm, "end": v(-8549.8, 2719.76) * mm});
            skLineSegment(sketch, "E2077", {"start": v(-8549.8, 2719.76) * mm, "end": v(-8547.01, 2718.38) * mm});
            skLineSegment(sketch, "E2078", {"start": v(-8547.01, 2718.38) * mm, "end": v(-8545.06, 2717.47) * mm});
            skLineSegment(sketch, "E2079", {"start": v(-8545.06, 2717.47) * mm, "end": v(-8543.97, 2717) * mm});
            skLineSegment(sketch, "E2080", {"start": v(-8543.97, 2717) * mm, "end": v(-8401.43, 2659.62) * mm});
            skLineSegment(sketch, "E2081", {"start": v(-8401.43, 2659.62) * mm, "end": v(-8482.83, 2392.74) * mm});
            skLineSegment(sketch, "E2082", {"start": v(-8482.83, 2392.74) * mm, "end": v(-8633.12, 2424.68) * mm});
            skLineSegment(sketch, "E2083", {"start": v(-8633.12, 2424.68) * mm, "end": v(-8634.3, 2424.9) * mm});
            skLineSegment(sketch, "E2084", {"start": v(-8634.3, 2424.9) * mm, "end": v(-8636.42, 2425.23) * mm});
            skLineSegment(sketch, "E2085", {"start": v(-8636.42, 2425.23) * mm, "end": v(-8639.5, 2425.65) * mm});
            skLineSegment(sketch, "E2086", {"start": v(-8639.5, 2425.65) * mm, "end": v(-8643.55, 2426.1) * mm});
            skLineSegment(sketch, "E2087", {"start": v(-8643.55, 2426.1) * mm, "end": v(-8648.55, 2426.53) * mm});
            skLineSegment(sketch, "E2088", {"start": v(-8648.55, 2426.53) * mm, "end": v(-8654.52, 2426.9) * mm});
            skLineSegment(sketch, "E2089", {"start": v(-8654.52, 2426.9) * mm, "end": v(-8661.45, 2427.19) * mm});
            skLineSegment(sketch, "E2090", {"start": v(-8661.45, 2427.19) * mm, "end": v(-8669.33, 2427.32) * mm});
            skLineSegment(sketch, "E2091", {"start": v(-8669.33, 2427.32) * mm, "end": v(-8678.18, 2427.27) * mm});
            skLineSegment(sketch, "E2092", {"start": v(-8678.18, 2427.27) * mm, "end": v(-8687.98, 2426.98) * mm});
            skLineSegment(sketch, "E2093", {"start": v(-8687.98, 2426.98) * mm, "end": v(-8698.73, 2426.42) * mm});
            skLineSegment(sketch, "E2094", {"start": v(-8698.73, 2426.42) * mm, "end": v(-8710.41, 2425.53) * mm});
            skLineSegment(sketch, "E2095", {"start": v(-8710.41, 2425.53) * mm, "end": v(-8723.02, 2424.28) * mm});
            skLineSegment(sketch, "E2096", {"start": v(-8723.02, 2424.28) * mm, "end": v(-8736.55, 2422.62) * mm});
            skLineSegment(sketch, "E2097", {"start": v(-8736.55, 2422.62) * mm, "end": v(-8750.98, 2420.5) * mm});
            skLineSegment(sketch, "E2098", {"start": v(-8750.98, 2420.5) * mm, "end": v(-8766.3, 2417.89) * mm});
            skLineSegment(sketch, "E2099", {"start": v(-8766.3, 2417.89) * mm, "end": v(-8782.5, 2414.74) * mm});
            skLineSegment(sketch, "E2100", {"start": v(-8782.5, 2414.74) * mm, "end": v(-8799.55, 2411) * mm});
            skLineSegment(sketch, "E2101", {"start": v(-8799.55, 2411) * mm, "end": v(-8817.44, 2406.65) * mm});
            skLineSegment(sketch, "E2102", {"start": v(-8817.44, 2406.65) * mm, "end": v(-8836.15, 2401.64) * mm});
            skLineSegment(sketch, "E2103", {"start": v(-8836.15, 2401.64) * mm, "end": v(-8855.66, 2395.92) * mm});
            skLineSegment(sketch, "E2104", {"start": v(-8855.66, 2395.92) * mm, "end": v(-8875.93, 2389.46) * mm});
            skLineSegment(sketch, "E2105", {"start": v(-8875.93, 2389.46) * mm, "end": v(-8896.96, 2382.22) * mm});
            skLineSegment(sketch, "E2106", {"start": v(-8896.96, 2382.22) * mm, "end": v(-8918.71, 2374.16) * mm});
            skLineSegment(sketch, "E2107", {"start": v(-8918.71, 2374.16) * mm, "end": v(-8941.16, 2365.24) * mm});
            skLineSegment(sketch, "E2108", {"start": v(-8941.16, 2365.24) * mm, "end": v(-8964.27, 2355.43) * mm});
            skLineSegment(sketch, "E2109", {"start": v(-8964.27, 2355.43) * mm, "end": v(-8988.02, 2344.69) * mm});
            skLineSegment(sketch, "E2110", {"start": v(-8988.02, 2344.69) * mm, "end": v(-9012.37, 2332.98) * mm});
            skLineSegment(sketch, "E2111", {"start": v(-9012.37, 2332.98) * mm, "end": v(-9037.3, 2320.28) * mm});
            skLineSegment(sketch, "E2112", {"start": v(-9037.3, 2320.28) * mm, "end": v(-9049.92, 2305.06) * mm});
            skLineSegment(sketch, "E2113", {"start": v(-9049.92, 2305.06) * mm, "end": v(-9060.5, 2183.08) * mm});
            skLineSegment(sketch, "E2114", {"start": v(-9060.5, 2183.08) * mm, "end": v(-9050.7, 2165.91) * mm});
            skLineSegment(sketch, "E2115", {"start": v(-9050.7, 2165.91) * mm, "end": v(-9028.33, 2149.1) * mm});
            skLineSegment(sketch, "E2116", {"start": v(-9028.33, 2149.1) * mm, "end": v(-9006.36, 2133.37) * mm});
            skLineSegment(sketch, "E2117", {"start": v(-9006.36, 2133.37) * mm, "end": v(-8984.82, 2118.7) * mm});
            skLineSegment(sketch, "E2118", {"start": v(-8984.82, 2118.7) * mm, "end": v(-8963.75, 2105.05) * mm});
            skLineSegment(sketch, "E2119", {"start": v(-8963.75, 2105.05) * mm, "end": v(-8943.17, 2092.4) * mm});
            skLineSegment(sketch, "E2120", {"start": v(-8943.17, 2092.4) * mm, "end": v(-8923.14, 2080.71) * mm});
            skLineSegment(sketch, "E2121", {"start": v(-8923.14, 2080.71) * mm, "end": v(-8903.68, 2069.95) * mm});
            skLineSegment(sketch, "E2122", {"start": v(-8903.68, 2069.95) * mm, "end": v(-8884.81, 2060.1) * mm});
            skLineSegment(sketch, "E2123", {"start": v(-8884.81, 2060.1) * mm, "end": v(-8866.59, 2051.1) * mm});
            skLineSegment(sketch, "E2124", {"start": v(-8866.59, 2051.1) * mm, "end": v(-8849.02, 2042.94) * mm});
            skLineSegment(sketch, "E2125", {"start": v(-8849.02, 2042.94) * mm, "end": v(-8832.15, 2035.57) * mm});
            skLineSegment(sketch, "E2126", {"start": v(-8832.15, 2035.57) * mm, "end": v(-8816, 2028.95) * mm});
            skLineSegment(sketch, "E2127", {"start": v(-8816, 2028.95) * mm, "end": v(-8800.58, 2023.06) * mm});
            skLineSegment(sketch, "E2128", {"start": v(-8800.58, 2023.06) * mm, "end": v(-8785.94, 2017.84) * mm});
            skLineSegment(sketch, "E2129", {"start": v(-8785.94, 2017.84) * mm, "end": v(-8772.09, 2013.27) * mm});
            skLineSegment(sketch, "E2130", {"start": v(-8772.09, 2013.27) * mm, "end": v(-8759.05, 2009.3) * mm});
            skLineSegment(sketch, "E2131", {"start": v(-8759.05, 2009.3) * mm, "end": v(-8746.84, 2005.9) * mm});
            skLineSegment(sketch, "E2132", {"start": v(-8746.84, 2005.9) * mm, "end": v(-8735.49, 2003) * mm});
            skLineSegment(sketch, "E2133", {"start": v(-8735.49, 2003) * mm, "end": v(-8725, 2000.6) * mm});
            skLineSegment(sketch, "E2134", {"start": v(-8725, 2000.6) * mm, "end": v(-8715.4, 1998.63) * mm});
            skLineSegment(sketch, "E2135", {"start": v(-8715.4, 1998.63) * mm, "end": v(-8706.7, 1997.05) * mm});
            skLineSegment(sketch, "E2136", {"start": v(-8706.7, 1997.05) * mm, "end": v(-8698.9, 1995.82) * mm});
            skLineSegment(sketch, "E2137", {"start": v(-8698.9, 1995.82) * mm, "end": v(-8692.02, 1994.9) * mm});
            skLineSegment(sketch, "E2138", {"start": v(-8692.02, 1994.9) * mm, "end": v(-8686.08, 1994.25) * mm});
            skLineSegment(sketch, "E2139", {"start": v(-8686.08, 1994.25) * mm, "end": v(-8681.08, 1993.82) * mm});
            skLineSegment(sketch, "E2140", {"start": v(-8681.08, 1993.82) * mm, "end": v(-8677.02, 1993.56) * mm});
            skLineSegment(sketch, "E2141", {"start": v(-8677.02, 1993.56) * mm, "end": v(-8673.91, 1993.44) * mm});
            skLineSegment(sketch, "E2142", {"start": v(-8673.91, 1993.44) * mm, "end": v(-8671.76, 1993.4) * mm});
            skLineSegment(sketch, "E2143", {"start": v(-8671.76, 1993.4) * mm, "end": v(-8670.57, 1993.41) * mm});
            skLineSegment(sketch, "E2144", {"start": v(-8670.57, 1993.41) * mm, "end": v(-8517.01, 1998.97) * mm});
            skLineSegment(sketch, "E2145", {"start": v(-8517.01, 1998.97) * mm, "end": v(-8482.83, 1722.06) * mm});
            skLineSegment(sketch, "E2146", {"start": v(-8482.83, 1722.06) * mm, "end": v(-8633.12, 1690.1) * mm});
            skLineSegment(sketch, "E2147", {"start": v(-8633.12, 1690.1) * mm, "end": v(-8634.28, 1689.83) * mm});
            skLineSegment(sketch, "E2148", {"start": v(-8634.28, 1689.83) * mm, "end": v(-8636.36, 1689.27) * mm});
            skLineSegment(sketch, "E2149", {"start": v(-8636.36, 1689.27) * mm, "end": v(-8639.34, 1688.4) * mm});
            skLineSegment(sketch, "E2150", {"start": v(-8639.34, 1688.4) * mm, "end": v(-8643.22, 1687.16) * mm});
            skLineSegment(sketch, "E2151", {"start": v(-8643.22, 1687.16) * mm, "end": v(-8647.96, 1685.52) * mm});
            skLineSegment(sketch, "E2152", {"start": v(-8647.96, 1685.52) * mm, "end": v(-8653.57, 1683.44) * mm});
            skLineSegment(sketch, "E2153", {"start": v(-8653.57, 1683.44) * mm, "end": v(-8660.01, 1680.88) * mm});
            skLineSegment(sketch, "E2154", {"start": v(-8660.01, 1680.88) * mm, "end": v(-8667.27, 1677.8) * mm});
            skLineSegment(sketch, "E2155", {"start": v(-8667.27, 1677.8) * mm, "end": v(-8675.34, 1674.14) * mm});
            skLineSegment(sketch, "E2156", {"start": v(-8675.34, 1674.14) * mm, "end": v(-8684.17, 1669.9) * mm});
            skLineSegment(sketch, "E2157", {"start": v(-8684.17, 1669.9) * mm, "end": v(-8693.76, 1665.01) * mm});
            skLineSegment(sketch, "E2158", {"start": v(-8693.76, 1665.01) * mm, "end": v(-8704.07, 1659.45) * mm});
            skLineSegment(sketch, "E2159", {"start": v(-8704.07, 1659.45) * mm, "end": v(-8715.08, 1653.17) * mm});
            skLineSegment(sketch, "E2160", {"start": v(-8715.08, 1653.17) * mm, "end": v(-8726.77, 1646.15) * mm});
            skLineSegment(sketch, "E2161", {"start": v(-8726.77, 1646.15) * mm, "end": v(-8739.09, 1638.35) * mm});
            skLineSegment(sketch, "E2162", {"start": v(-8739.09, 1638.35) * mm, "end": v(-8752.03, 1629.73) * mm});
            skLineSegment(sketch, "E2163", {"start": v(-8752.03, 1629.73) * mm, "end": v(-8765.54, 1620.27) * mm});
            skLineSegment(sketch, "E2164", {"start": v(-8765.54, 1620.27) * mm, "end": v(-8779.6, 1609.92) * mm});
            skLineSegment(sketch, "E2165", {"start": v(-8779.6, 1609.92) * mm, "end": v(-8794.18, 1598.67) * mm});
            skLineSegment(sketch, "E2166", {"start": v(-8794.18, 1598.67) * mm, "end": v(-8809.23, 1586.48) * mm});
            skLineSegment(sketch, "E2167", {"start": v(-8809.23, 1586.48) * mm, "end": v(-8824.72, 1573.32) * mm});
            skLineSegment(sketch, "E2168", {"start": v(-8824.72, 1573.32) * mm, "end": v(-8840.61, 1559.17) * mm});
            skLineSegment(sketch, "E2169", {"start": v(-8840.61, 1559.17) * mm, "end": v(-8856.88, 1544) * mm});
            skLineSegment(sketch, "E2170", {"start": v(-8856.88, 1544) * mm, "end": v(-8873.47, 1527.8) * mm});
            skLineSegment(sketch, "E2171", {"start": v(-8873.47, 1527.8) * mm, "end": v(-8890.35, 1510.52) * mm});
            skLineSegment(sketch, "E2172", {"start": v(-8890.35, 1510.52) * mm, "end": v(-8907.47, 1492.15) * mm});
            skLineSegment(sketch, "E2173", {"start": v(-8907.47, 1492.15) * mm, "end": v(-8924.8, 1472.68) * mm});
            skLineSegment(sketch, "E2174", {"start": v(-8924.8, 1472.68) * mm, "end": v(-8942.28, 1452.08) * mm});
            skLineSegment(sketch, "E2175", {"start": v(-8942.28, 1452.08) * mm, "end": v(-8959.89, 1430.34) * mm});
            skLineSegment(sketch, "E2176", {"start": v(-8959.89, 1430.34) * mm, "end": v(-8965.23, 1411.3) * mm});
            skLineSegment(sketch, "E2177", {"start": v(-8965.23, 1411.3) * mm, "end": v(-8925.29, 1295.55) * mm});
            skLineSegment(sketch, "E2178", {"start": v(-8925.29, 1295.55) * mm, "end": v(-8909.34, 1283.87) * mm});
            skLineSegment(sketch, "E2179", {"start": v(-8909.34, 1283.87) * mm, "end": v(-8882.08, 1277.6) * mm});
            skLineSegment(sketch, "E2180", {"start": v(-8882.08, 1277.6) * mm, "end": v(-8855.6, 1272.18) * mm});
            skLineSegment(sketch, "E2181", {"start": v(-8855.6, 1272.18) * mm, "end": v(-8829.96, 1267.53) * mm});
            skLineSegment(sketch, "E2182", {"start": v(-8829.96, 1267.53) * mm, "end": v(-8805.15, 1263.64) * mm});
            skLineSegment(sketch, "E2183", {"start": v(-8805.15, 1263.64) * mm, "end": v(-8781.22, 1260.44) * mm});
            skLineSegment(sketch, "E2184", {"start": v(-8781.22, 1260.44) * mm, "end": v(-8758.16, 1257.91) * mm});
            skLineSegment(sketch, "E2185", {"start": v(-8758.16, 1257.91) * mm, "end": v(-8736, 1256) * mm});
            skLineSegment(sketch, "E2186", {"start": v(-8736, 1256) * mm, "end": v(-8714.76, 1254.67) * mm});
            skLineSegment(sketch, "E2187", {"start": v(-8714.76, 1254.67) * mm, "end": v(-8694.45, 1253.87) * mm});
            skLineSegment(sketch, "E2188", {"start": v(-8694.45, 1253.87) * mm, "end": v(-8675.09, 1253.55) * mm});
            skLineSegment(sketch, "E2189", {"start": v(-8675.09, 1253.55) * mm, "end": v(-8656.67, 1253.68) * mm});
            skLineSegment(sketch, "E2190", {"start": v(-8656.67, 1253.68) * mm, "end": v(-8639.23, 1254.2) * mm});
            skLineSegment(sketch, "E2191", {"start": v(-8639.23, 1254.2) * mm, "end": v(-8622.75, 1255.1) * mm});
            skLineSegment(sketch, "E2192", {"start": v(-8622.75, 1255.1) * mm, "end": v(-8607.25, 1256.29) * mm});
            skLineSegment(sketch, "E2193", {"start": v(-8607.25, 1256.29) * mm, "end": v(-8592.74, 1257.74) * mm});
            skLineSegment(sketch, "E2194", {"start": v(-8592.74, 1257.74) * mm, "end": v(-8579.21, 1259.42) * mm});
            skLineSegment(sketch, "E2195", {"start": v(-8579.21, 1259.42) * mm, "end": v(-8566.67, 1261.27) * mm});
            skLineSegment(sketch, "E2196", {"start": v(-8566.67, 1261.27) * mm, "end": v(-8555.13, 1263.25) * mm});
            skLineSegment(sketch, "E2197", {"start": v(-8555.13, 1263.25) * mm, "end": v(-8544.56, 1265.32) * mm});
            skLineSegment(sketch, "E2198", {"start": v(-8544.56, 1265.32) * mm, "end": v(-8534.99, 1267.43) * mm});
            skLineSegment(sketch, "E2199", {"start": v(-8534.99, 1267.43) * mm, "end": v(-8526.4, 1269.52) * mm});
            skLineSegment(sketch, "E2200", {"start": v(-8526.4, 1269.52) * mm, "end": v(-8518.77, 1271.57) * mm});
            skLineSegment(sketch, "E2201", {"start": v(-8518.77, 1271.57) * mm, "end": v(-8512.12, 1273.53) * mm});
            skLineSegment(sketch, "E2202", {"start": v(-8512.12, 1273.53) * mm, "end": v(-8506.43, 1275.35) * mm});
            skLineSegment(sketch, "E2203", {"start": v(-8506.43, 1275.35) * mm, "end": v(-8501.68, 1277) * mm});
            skLineSegment(sketch, "E2204", {"start": v(-8501.68, 1277) * mm, "end": v(-8497.87, 1278.4) * mm});
            skLineSegment(sketch, "E2205", {"start": v(-8497.87, 1278.4) * mm, "end": v(-8494.98, 1279.56) * mm});
            skLineSegment(sketch, "E2206", {"start": v(-8494.98, 1279.56) * mm, "end": v(-8493, 1280.4) * mm});
            skLineSegment(sketch, "E2207", {"start": v(-8493, 1280.4) * mm, "end": v(-8491.91, 1280.9) * mm});
            skLineSegment(sketch, "E2208", {"start": v(-8491.91, 1280.9) * mm, "end": v(-8353.9, 1348.43) * mm});
            skLineSegment(sketch, "E2209", {"start": v(-8353.9, 1348.43) * mm, "end": v(-8210.03, 1109.36) * mm});
            skLineSegment(sketch, "E2210", {"start": v(-8210.03, 1109.36) * mm, "end": v(-8334.34, 1019.04) * mm});
            skLineSegment(sketch, "E2211", {"start": v(-8334.34, 1019.04) * mm, "end": v(-8335.29, 1018.31) * mm});
            skLineSegment(sketch, "E2212", {"start": v(-8335.29, 1018.31) * mm, "end": v(-8336.96, 1016.95) * mm});
            skLineSegment(sketch, "E2213", {"start": v(-8336.96, 1016.95) * mm, "end": v(-8339.33, 1014.94) * mm});
            skLineSegment(sketch, "E2214", {"start": v(-8339.33, 1014.94) * mm, "end": v(-8342.36, 1012.24) * mm});
            skLineSegment(sketch, "E2215", {"start": v(-8342.36, 1012.24) * mm, "end": v(-8346.03, 1008.81) * mm});
            skLineSegment(sketch, "E2216", {"start": v(-8346.03, 1008.81) * mm, "end": v(-8350.3, 1004.63) * mm});
            skLineSegment(sketch, "E2217", {"start": v(-8350.3, 1004.63) * mm, "end": v(-8355.15, 999.67) * mm});
            skLineSegment(sketch, "E2218", {"start": v(-8355.15, 999.67) * mm, "end": v(-8360.53, 993.9) * mm});
            skLineSegment(sketch, "E2219", {"start": v(-8360.53, 993.9) * mm, "end": v(-8366.41, 987.29) * mm});
            skLineSegment(sketch, "E2220", {"start": v(-8366.41, 987.29) * mm, "end": v(-8372.76, 979.81) * mm});
            skLineSegment(sketch, "E2221", {"start": v(-8372.76, 979.81) * mm, "end": v(-8379.53, 971.45) * mm});
            skLineSegment(sketch, "E2222", {"start": v(-8379.53, 971.45) * mm, "end": v(-8386.69, 962.17) * mm});
            skLineSegment(sketch, "E2223", {"start": v(-8386.69, 962.17) * mm, "end": v(-8394.2, 951.96) * mm});
            skLineSegment(sketch, "E2224", {"start": v(-8394.2, 951.96) * mm, "end": v(-8402.01, 940.8) * mm});
            skLineSegment(sketch, "E2225", {"start": v(-8402.01, 940.8) * mm, "end": v(-8410.1, 928.66) * mm});
            skLineSegment(sketch, "E2226", {"start": v(-8410.1, 928.66) * mm, "end": v(-8418.4, 915.52) * mm});
            skLineSegment(sketch, "E2227", {"start": v(-8418.4, 915.52) * mm, "end": v(-8426.9, 901.38) * mm});
            skLineSegment(sketch, "E2228", {"start": v(-8426.9, 901.38) * mm, "end": v(-8435.54, 886.2) * mm});
            skLineSegment(sketch, "E2229", {"start": v(-8435.54, 886.2) * mm, "end": v(-8444.28, 870) * mm});
            skLineSegment(sketch, "E2230", {"start": v(-8444.28, 870) * mm, "end": v(-8453.07, 852.74) * mm});
            skLineSegment(sketch, "E2231", {"start": v(-8453.07, 852.74) * mm, "end": v(-8461.87, 834.42) * mm});
            skLineSegment(sketch, "E2232", {"start": v(-8461.87, 834.42) * mm, "end": v(-8470.64, 815.03) * mm});
            skLineSegment(sketch, "E2233", {"start": v(-8470.64, 815.03) * mm, "end": v(-8479.33, 794.56) * mm});
            skLineSegment(sketch, "E2234", {"start": v(-8479.33, 794.56) * mm, "end": v(-8487.89, 773) * mm});
            skLineSegment(sketch, "E2235", {"start": v(-8487.89, 773) * mm, "end": v(-8496.28, 750.35) * mm});
            skLineSegment(sketch, "E2236", {"start": v(-8496.28, 750.35) * mm, "end": v(-8504.45, 726.61) * mm});
            skLineSegment(sketch, "E2237", {"start": v(-8504.45, 726.61) * mm, "end": v(-8512.36, 701.78) * mm});
            skLineSegment(sketch, "E2238", {"start": v(-8512.36, 701.78) * mm, "end": v(-8519.96, 675.85) * mm});
            skLineSegment(sketch, "E2239", {"start": v(-8519.96, 675.85) * mm, "end": v(-8527.2, 648.82) * mm});
            skLineSegment(sketch, "E2240", {"start": v(-8527.2, 648.82) * mm, "end": v(-8524.34, 629.26) * mm});
            skLineSegment(sketch, "E2241", {"start": v(-8524.34, 629.26) * mm, "end": v(-8440.77, 539.76) * mm});
            skLineSegment(sketch, "E2242", {"start": v(-8440.77, 539.76) * mm, "end": v(-8421.45, 535.57) * mm});
            skLineSegment(sketch, "E2243", {"start": v(-8421.45, 535.57) * mm, "end": v(-8394, 540.94) * mm});
            skLineSegment(sketch, "E2244", {"start": v(-8394, 540.94) * mm, "end": v(-8367.6, 546.75) * mm});
            skLineSegment(sketch, "E2245", {"start": v(-8367.6, 546.75) * mm, "end": v(-8342.28, 552.94) * mm});
            skLineSegment(sketch, "E2246", {"start": v(-8342.28, 552.94) * mm, "end": v(-8318.04, 559.47) * mm});
            skLineSegment(sketch, "E2247", {"start": v(-8318.04, 559.47) * mm, "end": v(-8294.87, 566.29) * mm});
            skLineSegment(sketch, "E2248", {"start": v(-8294.87, 566.29) * mm, "end": v(-8272.78, 573.36) * mm});
            skLineSegment(sketch, "E2249", {"start": v(-8272.78, 573.36) * mm, "end": v(-8251.76, 580.62) * mm});
            skLineSegment(sketch, "E2250", {"start": v(-8251.76, 580.62) * mm, "end": v(-8231.81, 588.04) * mm});
            skLineSegment(sketch, "E2251", {"start": v(-8231.81, 588.04) * mm, "end": v(-8212.93, 595.57) * mm});
            skLineSegment(sketch, "E2252", {"start": v(-8212.93, 595.57) * mm, "end": v(-8195.11, 603.16) * mm});
            skLineSegment(sketch, "E2253", {"start": v(-8195.11, 603.16) * mm, "end": v(-8178.35, 610.77) * mm});
            skLineSegment(sketch, "E2254", {"start": v(-8178.35, 610.77) * mm, "end": v(-8162.62, 618.35) * mm});
            skLineSegment(sketch, "E2255", {"start": v(-8162.62, 618.35) * mm, "end": v(-8147.93, 625.85) * mm});
            skLineSegment(sketch, "E2256", {"start": v(-8147.93, 625.85) * mm, "end": v(-8134.26, 633.25) * mm});
            skLineSegment(sketch, "E2257", {"start": v(-8134.26, 633.25) * mm, "end": v(-8121.6, 640.48) * mm});
            skLineSegment(sketch, "E2258", {"start": v(-8121.6, 640.48) * mm, "end": v(-8109.92, 647.52) * mm});
            skLineSegment(sketch, "E2259", {"start": v(-8109.92, 647.52) * mm, "end": v(-8099.21, 654.3) * mm});
            skLineSegment(sketch, "E2260", {"start": v(-8099.21, 654.3) * mm, "end": v(-8089.47, 660.81) * mm});
            skLineSegment(sketch, "E2261", {"start": v(-8089.47, 660.81) * mm, "end": v(-8080.66, 667) * mm});
            skLineSegment(sketch, "E2262", {"start": v(-8080.66, 667) * mm, "end": v(-8072.77, 672.82) * mm});
            skLineSegment(sketch, "E2263", {"start": v(-8072.77, 672.82) * mm, "end": v(-8065.77, 678.23) * mm});
            skLineSegment(sketch, "E2264", {"start": v(-8065.77, 678.23) * mm, "end": v(-8059.65, 683.2) * mm});
            skLineSegment(sketch, "E2265", {"start": v(-8059.65, 683.2) * mm, "end": v(-8054.37, 687.7) * mm});
            skLineSegment(sketch, "E2266", {"start": v(-8054.37, 687.7) * mm, "end": v(-8049.9, 691.67) * mm});
            skLineSegment(sketch, "E2267", {"start": v(-8049.9, 691.67) * mm, "end": v(-8046.23, 695.1) * mm});
            skLineSegment(sketch, "E2268", {"start": v(-8046.23, 695.1) * mm, "end": v(-8043.33, 697.95) * mm});
            skLineSegment(sketch, "E2269", {"start": v(-8043.33, 697.95) * mm, "end": v(-8041.16, 700.17) * mm});
            skLineSegment(sketch, "E2270", {"start": v(-8041.16, 700.17) * mm, "end": v(-8039.7, 701.75) * mm});
            skLineSegment(sketch, "E2271", {"start": v(-8039.7, 701.75) * mm, "end": v(-8038.9, 702.64) * mm});
            skLineSegment(sketch, "E2272", {"start": v(-8038.9, 702.64) * mm, "end": v(-7940.28, 820.47) * mm});
            skLineSegment(sketch, "E2273", {"start": v(-7940.28, 820.47) * mm, "end": v(-7711.62, 660.59) * mm});
            skLineSegment(sketch, "E2274", {"start": v(-7711.62, 660.59) * mm, "end": v(-7788.44, 527.52) * mm});
            skLineSegment(sketch, "E2275", {"start": v(-7788.44, 527.52) * mm, "end": v(-7789.01, 526.46) * mm});
            skLineSegment(sketch, "E2276", {"start": v(-7789.01, 526.46) * mm, "end": v(-7789.99, 524.55) * mm});
            skLineSegment(sketch, "E2277", {"start": v(-7789.99, 524.55) * mm, "end": v(-7791.33, 521.74) * mm});
            skLineSegment(sketch, "E2278", {"start": v(-7791.33, 521.74) * mm, "end": v(-7793, 518.04) * mm});
            skLineSegment(sketch, "E2279", {"start": v(-7793, 518.04) * mm, "end": v(-7794.97, 513.42) * mm});
            skLineSegment(sketch, "E2280", {"start": v(-7794.97, 513.42) * mm, "end": v(-7797.17, 507.86) * mm});
            skLineSegment(sketch, "E2281", {"start": v(-7797.17, 507.86) * mm, "end": v(-7799.58, 501.36) * mm});
            skLineSegment(sketch, "E2282", {"start": v(-7799.58, 501.36) * mm, "end": v(-7802.15, 493.9) * mm});
            skLineSegment(sketch, "E2283", {"start": v(-7802.15, 493.9) * mm, "end": v(-7804.83, 485.46) * mm});
            skLineSegment(sketch, "E2284", {"start": v(-7804.83, 485.46) * mm, "end": v(-7807.58, 476.05) * mm});
            skLineSegment(sketch, "E2285", {"start": v(-7807.58, 476.05) * mm, "end": v(-7810.37, 465.66) * mm});
            skLineSegment(sketch, "E2286", {"start": v(-7810.37, 465.66) * mm, "end": v(-7813.13, 454.27) * mm});
            skLineSegment(sketch, "E2287", {"start": v(-7813.13, 454.27) * mm, "end": v(-7815.84, 441.9) * mm});
            skLineSegment(sketch, "E2288", {"start": v(-7815.84, 441.9) * mm, "end": v(-7818.44, 428.51) * mm});
            skLineSegment(sketch, "E2289", {"start": v(-7818.44, 428.51) * mm, "end": v(-7820.89, 414.13) * mm});
            skLineSegment(sketch, "E2290", {"start": v(-7820.89, 414.13) * mm, "end": v(-7823.14, 398.75) * mm});
            skLineSegment(sketch, "E2291", {"start": v(-7823.14, 398.75) * mm, "end": v(-7825.14, 382.38) * mm});
            skLineSegment(sketch, "E2292", {"start": v(-7825.14, 382.38) * mm, "end": v(-7826.87, 365) * mm});
            skLineSegment(sketch, "E2293", {"start": v(-7826.87, 365) * mm, "end": v(-7828.26, 346.64) * mm});
            skLineSegment(sketch, "E2294", {"start": v(-7828.26, 346.64) * mm, "end": v(-7829.27, 327.3) * mm});
            skLineSegment(sketch, "E2295", {"start": v(-7829.27, 327.3) * mm, "end": v(-7829.86, 306.99) * mm});
            skLineSegment(sketch, "E2296", {"start": v(-7829.86, 306.99) * mm, "end": v(-7829.98, 285.7) * mm});
            skLineSegment(sketch, "E2297", {"start": v(-7829.98, 285.7) * mm, "end": v(-7829.6, 263.47) * mm});
            skLineSegment(sketch, "E2298", {"start": v(-7829.6, 263.47) * mm, "end": v(-7828.64, 240.3) * mm});
            skLineSegment(sketch, "E2299", {"start": v(-7828.64, 240.3) * mm, "end": v(-7827.1, 216.2) * mm});
            skLineSegment(sketch, "E2300", {"start": v(-7827.1, 216.2) * mm, "end": v(-7824.9, 191.18) * mm});
            skLineSegment(sketch, "E2301", {"start": v(-7824.9, 191.18) * mm, "end": v(-7822.03, 165.27) * mm});
            skLineSegment(sketch, "E2302", {"start": v(-7822.03, 165.27) * mm, "end": v(-7818.42, 138.5) * mm});
            skLineSegment(sketch, "E2303", {"start": v(-7818.42, 138.5) * mm, "end": v(-7814.05, 110.86) * mm});
            skLineSegment(sketch, "E2304", {"start": v(-7814.05, 110.86) * mm, "end": v(-7803.47, 94.15) * mm});
            skLineSegment(sketch, "E2305", {"start": v(-7803.47, 94.15) * mm, "end": v(-7690.73, 46.39) * mm});
            skLineSegment(sketch, "E2306", {"start": v(-7690.73, 46.39) * mm, "end": v(-7671.38, 50.41) * mm});
            skLineSegment(sketch, "E2307", {"start": v(-7671.38, 50.41) * mm, "end": v(-7648.48, 66.5) * mm});
            skLineSegment(sketch, "E2308", {"start": v(-7648.48, 66.5) * mm, "end": v(-7626.73, 82.53) * mm});
            skLineSegment(sketch, "E2309", {"start": v(-7626.73, 82.53) * mm, "end": v(-7606.12, 98.48) * mm});
            skLineSegment(sketch, "E2310", {"start": v(-7606.12, 98.48) * mm, "end": v(-7586.63, 114.3) * mm});
            skLineSegment(sketch, "E2311", {"start": v(-7586.63, 114.3) * mm, "end": v(-7568.24, 129.96) * mm});
            skLineSegment(sketch, "E2312", {"start": v(-7568.24, 129.96) * mm, "end": v(-7550.93, 145.4) * mm});
            skLineSegment(sketch, "E2313", {"start": v(-7550.93, 145.4) * mm, "end": v(-7534.68, 160.59) * mm});
            skLineSegment(sketch, "E2314", {"start": v(-7534.68, 160.59) * mm, "end": v(-7519.48, 175.48) * mm});
            skLineSegment(sketch, "E2315", {"start": v(-7519.48, 175.48) * mm, "end": v(-7505.3, 190.04) * mm});
            skLineSegment(sketch, "E2316", {"start": v(-7505.3, 190.04) * mm, "end": v(-7492.1, 204.22) * mm});
            skLineSegment(sketch, "E2317", {"start": v(-7492.1, 204.22) * mm, "end": v(-7479.88, 217.99) * mm});
            skLineSegment(sketch, "E2318", {"start": v(-7479.88, 217.99) * mm, "end": v(-7468.6, 231.3) * mm});
            skLineSegment(sketch, "E2319", {"start": v(-7468.6, 231.3) * mm, "end": v(-7458.22, 244.14) * mm});
            skLineSegment(sketch, "E2320", {"start": v(-7458.22, 244.14) * mm, "end": v(-7448.74, 256.46) * mm});
            skLineSegment(sketch, "E2321", {"start": v(-7448.74, 256.46) * mm, "end": v(-7440.11, 268.22) * mm});
            skLineSegment(sketch, "E2322", {"start": v(-7440.11, 268.22) * mm, "end": v(-7432.3, 279.4) * mm});
            skLineSegment(sketch, "E2323", {"start": v(-7432.3, 279.4) * mm, "end": v(-7425.3, 289.95) * mm});
            skLineSegment(sketch, "E2324", {"start": v(-7425.3, 289.95) * mm, "end": v(-7419.04, 299.86) * mm});
            skLineSegment(sketch, "E2325", {"start": v(-7419.04, 299.86) * mm, "end": v(-7413.5, 309.09) * mm});
            skLineSegment(sketch, "E2326", {"start": v(-7413.5, 309.09) * mm, "end": v(-7408.67, 317.61) * mm});
            skLineSegment(sketch, "E2327", {"start": v(-7408.67, 317.61) * mm, "end": v(-7404.48, 325.4) * mm});
            skLineSegment(sketch, "E2328", {"start": v(-7404.48, 325.4) * mm, "end": v(-7400.9, 332.44) * mm});
            skLineSegment(sketch, "E2329", {"start": v(-7400.9, 332.44) * mm, "end": v(-7397.9, 338.7) * mm});
            skLineSegment(sketch, "E2330", {"start": v(-7397.9, 338.7) * mm, "end": v(-7395.45, 344.14) * mm});
            skLineSegment(sketch, "E2331", {"start": v(-7395.45, 344.14) * mm, "end": v(-7393.49, 348.77) * mm});
            skLineSegment(sketch, "E2332", {"start": v(-7393.49, 348.77) * mm, "end": v(-7392, 352.55) * mm});
            skLineSegment(sketch, "E2333", {"start": v(-7392, 352.55) * mm, "end": v(-7390.91, 355.46) * mm});
            skLineSegment(sketch, "E2334", {"start": v(-7390.91, 355.46) * mm, "end": v(-7390.21, 357.5) * mm});
            skLineSegment(sketch, "E2335", {"start": v(-7390.21, 357.5) * mm, "end": v(-7389.85, 358.64) * mm});
            skLineSegment(sketch, "E2336", {"start": v(-7389.85, 358.64) * mm, "end": v(-7347.69, 506.4) * mm});
            skLineSegment(sketch, "E2337", {"start": v(-7347.69, 506.4) * mm, "end": v(-7073.76, 453.34) * mm});
            skLineSegment(sketch, "E2338", {"start": v(-7073.76, 453.34) * mm, "end": v(-7089.82, 300.52) * mm});
            skLineSegment(sketch, "E2339", {"start": v(-7089.82, 300.52) * mm, "end": v(-7089.91, 299.33) * mm});
            skLineSegment(sketch, "E2340", {"start": v(-7089.91, 299.33) * mm, "end": v(-7090.02, 297.18) * mm});
            skLineSegment(sketch, "E2341", {"start": v(-7090.02, 297.18) * mm, "end": v(-7090.11, 294.07) * mm});
            skLineSegment(sketch, "E2342", {"start": v(-7090.11, 294.07) * mm, "end": v(-7090.13, 290) * mm});
            skLineSegment(sketch, "E2343", {"start": v(-7090.13, 290) * mm, "end": v(-7090.04, 284.99) * mm});
            skLineSegment(sketch, "E2344", {"start": v(-7090.04, 284.99) * mm, "end": v(-7089.8, 279.01) * mm});
            skLineSegment(sketch, "E2345", {"start": v(-7089.8, 279.01) * mm, "end": v(-7089.35, 272.1) * mm});
            skLineSegment(sketch, "E2346", {"start": v(-7089.35, 272.1) * mm, "end": v(-7088.66, 264.23) * mm});
            skLineSegment(sketch, "E2347", {"start": v(-7088.66, 264.23) * mm, "end": v(-7087.69, 255.44) * mm});
            skLineSegment(sketch, "E2348", {"start": v(-7087.69, 255.44) * mm, "end": v(-7086.37, 245.72) * mm});
            skLineSegment(sketch, "E2349", {"start": v(-7086.37, 245.72) * mm, "end": v(-7084.7, 235.1) * mm});
            skLineSegment(sketch, "E2350", {"start": v(-7084.7, 235.1) * mm, "end": v(-7082.59, 223.57) * mm});
            skLineSegment(sketch, "E2351", {"start": v(-7082.59, 223.57) * mm, "end": v(-7080.02, 211.16) * mm});
            skLineSegment(sketch, "E2352", {"start": v(-7080.02, 211.16) * mm, "end": v(-7076.95, 197.88) * mm});
            skLineSegment(sketch, "E2353", {"start": v(-7076.95, 197.88) * mm, "end": v(-7073.34, 183.75) * mm});
            skLineSegment(sketch, "E2354", {"start": v(-7073.34, 183.75) * mm, "end": v(-7069.14, 168.78) * mm});
            skLineSegment(sketch, "E2355", {"start": v(-7069.14, 168.78) * mm, "end": v(-7064.32, 153) * mm});
            skLineSegment(sketch, "E2356", {"start": v(-7064.32, 153) * mm, "end": v(-7058.82, 136.43) * mm});
            skLineSegment(sketch, "E2357", {"start": v(-7058.82, 136.43) * mm, "end": v(-7052.63, 119.1) * mm});
            skLineSegment(sketch, "E2358", {"start": v(-7052.63, 119.1) * mm, "end": v(-7045.68, 101.01) * mm});
            skLineSegment(sketch, "E2359", {"start": v(-7045.68, 101.01) * mm, "end": v(-7037.96, 82.21) * mm});
            skLineSegment(sketch, "E2360", {"start": v(-7037.96, 82.21) * mm, "end": v(-7029.41, 62.72) * mm});
            skLineSegment(sketch, "E2361", {"start": v(-7029.41, 62.72) * mm, "end": v(-7020.01, 42.57) * mm});
            skLineSegment(sketch, "E2362", {"start": v(-7020.01, 42.57) * mm, "end": v(-7009.72, 21.78) * mm});
            skLineSegment(sketch, "E2363", {"start": v(-7009.72, 21.78) * mm, "end": v(-6998.5, 0.4) * mm});
            skLineSegment(sketch, "E2364", {"start": v(-6998.5, 0.4) * mm, "end": v(-6986.33, -21.57) * mm});
            skLineSegment(sketch, "E2365", {"start": v(-6986.33, -21.57) * mm, "end": v(-6973.17, -44.06) * mm});
            skLineSegment(sketch, "E2366", {"start": v(-6973.17, -44.06) * mm, "end": v(-6958.98, -67.06) * mm});
            skLineSegment(sketch, "E2367", {"start": v(-6958.98, -67.06) * mm, "end": v(-6943.74, -90.52) * mm});
            skLineSegment(sketch, "E2368", {"start": v(-6943.74, -90.52) * mm, "end": v(-6927.29, -101.49) * mm});
            skLineSegment(sketch, "E2369", {"start": v(-6927.29, -101.49) * mm, "end": v(-6804.86, -99.27) * mm});
            skLineSegment(sketch, "E2370", {"start": v(-6804.86, -99.27) * mm, "end": v(-6788.82, -87.72) * mm});
            skLineSegment(sketch, "E2371", {"start": v(-6788.82, -87.72) * mm, "end": v(-6774.44, -63.72) * mm});
            skLineSegment(sketch, "E2372", {"start": v(-6774.44, -63.72) * mm, "end": v(-6761.1, -40.22) * mm});
            skLineSegment(sketch, "E2373", {"start": v(-6761.1, -40.22) * mm, "end": v(-6748.75, -17.26) * mm});
            skLineSegment(sketch, "E2374", {"start": v(-6748.75, -17.26) * mm, "end": v(-6737.38, 5.12) * mm});
            skLineSegment(sketch, "E2375", {"start": v(-6737.38, 5.12) * mm, "end": v(-6726.95, 26.9) * mm});
            skLineSegment(sketch, "E2376", {"start": v(-6726.95, 26.9) * mm, "end": v(-6717.42, 48.05) * mm});
            skLineSegment(sketch, "E2377", {"start": v(-6717.42, 48.05) * mm, "end": v(-6708.75, 68.53) * mm});
            skLineSegment(sketch, "E2378", {"start": v(-6708.75, 68.53) * mm, "end": v(-6700.92, 88.32) * mm});
            skLineSegment(sketch, "E2379", {"start": v(-6700.92, 88.32) * mm, "end": v(-6693.88, 107.39) * mm});
            skLineSegment(sketch, "E2380", {"start": v(-6693.88, 107.39) * mm, "end": v(-6687.6, 125.7) * mm});
            skLineSegment(sketch, "E2381", {"start": v(-6687.6, 125.7) * mm, "end": v(-6682.03, 143.26) * mm});
            skLineSegment(sketch, "E2382", {"start": v(-6682.03, 143.26) * mm, "end": v(-6677.14, 160.02) * mm});
            skLineSegment(sketch, "E2383", {"start": v(-6677.14, 160.02) * mm, "end": v(-6672.9, 175.96) * mm});
            skLineSegment(sketch, "E2384", {"start": v(-6672.9, 175.96) * mm, "end": v(-6669.24, 191.07) * mm});
            skLineSegment(sketch, "E2385", {"start": v(-6669.24, 191.07) * mm, "end": v(-6666.14, 205.32) * mm});
            skLineSegment(sketch, "E2386", {"start": v(-6666.14, 205.32) * mm, "end": v(-6663.56, 218.7) * mm});
            skLineSegment(sketch, "E2387", {"start": v(-6663.56, 218.7) * mm, "end": v(-6661.44, 231.2) * mm});
            skLineSegment(sketch, "E2388", {"start": v(-6661.44, 231.2) * mm, "end": v(-6659.76, 242.8) * mm});
            skLineSegment(sketch, "E2389", {"start": v(-6659.76, 242.8) * mm, "end": v(-6658.46, 253.48) * mm});
            skLineSegment(sketch, "E2390", {"start": v(-6658.46, 253.48) * mm, "end": v(-6657.5, 263.24) * mm});
            skLineSegment(sketch, "E2391", {"start": v(-6657.5, 263.24) * mm, "end": v(-6656.84, 272.06) * mm});
            skLineSegment(sketch, "E2392", {"start": v(-6656.84, 272.06) * mm, "end": v(-6656.44, 279.94) * mm});
            skLineSegment(sketch, "E2393", {"start": v(-6656.44, 279.94) * mm, "end": v(-6656.25, 286.87) * mm});
            skLineSegment(sketch, "E2394", {"start": v(-6656.25, 286.87) * mm, "end": v(-6656.21, 292.85) * mm});
            skLineSegment(sketch, "E2395", {"start": v(-6656.21, 292.85) * mm, "end": v(-6656.3, 297.87) * mm});
            skLineSegment(sketch, "E2396", {"start": v(-6656.3, 297.87) * mm, "end": v(-6656.48, 301.93) * mm});
            skLineSegment(sketch, "E2397", {"start": v(-6656.48, 301.93) * mm, "end": v(-6656.68, 305.03) * mm});
            skLineSegment(sketch, "E2398", {"start": v(-6656.68, 305.03) * mm, "end": v(-6656.87, 307.18) * mm});
            skLineSegment(sketch, "E2399", {"start": v(-6656.87, 307.18) * mm, "end": v(-6657, 308.36) * mm});
            skLineSegment(sketch, "E2400", {"start": v(-6657, 308.36) * mm, "end": v(-6678.58, 460.5) * mm});
            skLineSegment(sketch, "E2401", {"start": v(-6678.58, 460.5) * mm, "end": v(-6406.76, 523.44) * mm});
            skLineSegment(sketch, "E2402", {"start": v(-6406.76, 523.44) * mm, "end": v(-6359.27, 377.3) * mm});
            skLineSegment(sketch, "E2403", {"start": v(-6359.27, 377.3) * mm, "end": v(-6358.87, 376.18) * mm});
            skLineSegment(sketch, "E2404", {"start": v(-6358.87, 376.18) * mm, "end": v(-6358.1, 374.17) * mm});
            skLineSegment(sketch, "E2405", {"start": v(-6358.1, 374.17) * mm, "end": v(-6356.91, 371.3) * mm});
            skLineSegment(sketch, "E2406", {"start": v(-6356.91, 371.3) * mm, "end": v(-6355.28, 367.58) * mm});
            skLineSegment(sketch, "E2407", {"start": v(-6355.28, 367.58) * mm, "end": v(-6353.16, 363.03) * mm});
            skLineSegment(sketch, "E2408", {"start": v(-6353.16, 363.03) * mm, "end": v(-6350.5, 357.67) * mm});
            skLineSegment(sketch, "E2409", {"start": v(-6350.5, 357.67) * mm, "end": v(-6347.28, 351.53) * mm});
            skLineSegment(sketch, "E2410", {"start": v(-6347.28, 351.53) * mm, "end": v(-6343.45, 344.63) * mm});
            skLineSegment(sketch, "E2411", {"start": v(-6343.45, 344.63) * mm, "end": v(-6338.98, 337) * mm});
            skLineSegment(sketch, "E2412", {"start": v(-6338.98, 337) * mm, "end": v(-6333.83, 328.65) * mm});
            skLineSegment(sketch, "E2413", {"start": v(-6333.83, 328.65) * mm, "end": v(-6327.97, 319.63) * mm});
            skLineSegment(sketch, "E2414", {"start": v(-6327.97, 319.63) * mm, "end": v(-6321.36, 309.95) * mm});
            skLineSegment(sketch, "E2415", {"start": v(-6321.36, 309.95) * mm, "end": v(-6313.97, 299.65) * mm});
            skLineSegment(sketch, "E2416", {"start": v(-6313.97, 299.65) * mm, "end": v(-6305.77, 288.77) * mm});
            skLineSegment(sketch, "E2417", {"start": v(-6305.77, 288.77) * mm, "end": v(-6296.72, 277.33) * mm});
            skLineSegment(sketch, "E2418", {"start": v(-6296.72, 277.33) * mm, "end": v(-6286.8, 265.37) * mm});
            skLineSegment(sketch, "E2419", {"start": v(-6286.8, 265.37) * mm, "end": v(-6275.97, 252.92) * mm});
            skLineSegment(sketch, "E2420", {"start": v(-6275.97, 252.92) * mm, "end": v(-6264.21, 240.01) * mm});
            skLineSegment(sketch, "E2421", {"start": v(-6264.21, 240.01) * mm, "end": v(-6251.5, 226.7) * mm});
            skLineSegment(sketch, "E2422", {"start": v(-6251.5, 226.7) * mm, "end": v(-6237.8, 213) * mm});
            skLineSegment(sketch, "E2423", {"start": v(-6237.8, 213) * mm, "end": v(-6223.1, 198.97) * mm});
            skLineSegment(sketch, "E2424", {"start": v(-6223.1, 198.97) * mm, "end": v(-6207.36, 184.64) * mm});
            skLineSegment(sketch, "E2425", {"start": v(-6207.36, 184.64) * mm, "end": v(-6190.58, 170.05) * mm});
            skLineSegment(sketch, "E2426", {"start": v(-6190.58, 170.05) * mm, "end": v(-6172.72, 155.24) * mm});
            skLineSegment(sketch, "E2427", {"start": v(-6172.72, 155.24) * mm, "end": v(-6153.78, 140.27) * mm});
            skLineSegment(sketch, "E2428", {"start": v(-6153.78, 140.27) * mm, "end": v(-6133.72, 125.16) * mm});
            skLineSegment(sketch, "E2429", {"start": v(-6133.72, 125.16) * mm, "end": v(-6112.55, 109.96) * mm});
            skLineSegment(sketch, "E2430", {"start": v(-6112.55, 109.96) * mm, "end": v(-6090.23, 94.72) * mm});
            skLineSegment(sketch, "E2431", {"start": v(-6090.23, 94.72) * mm, "end": v(-6066.77, 79.49) * mm});
            skLineSegment(sketch, "E2432", {"start": v(-6066.77, 79.49) * mm, "end": v(-6047.28, 76.16) * mm});
            skLineSegment(sketch, "E2433", {"start": v(-6047.28, 76.16) * mm, "end": v(-5936.34, 127.98) * mm});
            skLineSegment(sketch, "E2434", {"start": v(-5936.34, 127.98) * mm, "end": v(-5926.38, 145.06) * mm});
            skLineSegment(sketch, "E2435", {"start": v(-5926.38, 145.06) * mm, "end": v(-5923, 172.84) * mm});
            skLineSegment(sketch, "E2436", {"start": v(-5923, 172.84) * mm, "end": v(-5920.37, 199.73) * mm});
            skLineSegment(sketch, "E2437", {"start": v(-5920.37, 199.73) * mm, "end": v(-5918.44, 225.72) * mm});
            skLineSegment(sketch, "E2438", {"start": v(-5918.44, 225.72) * mm, "end": v(-5917.15, 250.8) * mm});
            skLineSegment(sketch, "E2439", {"start": v(-5917.15, 250.8) * mm, "end": v(-5916.48, 274.94) * mm});
            skLineSegment(sketch, "E2440", {"start": v(-5916.48, 274.94) * mm, "end": v(-5916.37, 298.13) * mm});
            skLineSegment(sketch, "E2441", {"start": v(-5916.37, 298.13) * mm, "end": v(-5916.8, 320.37) * mm});
            skLineSegment(sketch, "E2442", {"start": v(-5916.8, 320.37) * mm, "end": v(-5917.68, 341.63) * mm});
            skLineSegment(sketch, "E2443", {"start": v(-5917.68, 341.63) * mm, "end": v(-5919, 361.91) * mm});
            skLineSegment(sketch, "E2444", {"start": v(-5919, 361.91) * mm, "end": v(-5920.72, 381.2) * mm});
            skLineSegment(sketch, "E2445", {"start": v(-5920.72, 381.2) * mm, "end": v(-5922.77, 399.5) * mm});
            skLineSegment(sketch, "E2446", {"start": v(-5922.77, 399.5) * mm, "end": v(-5925.12, 416.8) * mm});
            skLineSegment(sketch, "E2447", {"start": v(-5925.12, 416.8) * mm, "end": v(-5927.72, 433.1) * mm});
            skLineSegment(sketch, "E2448", {"start": v(-5927.72, 433.1) * mm, "end": v(-5930.53, 448.38) * mm});
            skLineSegment(sketch, "E2449", {"start": v(-5930.53, 448.38) * mm, "end": v(-5933.5, 462.66) * mm});
            skLineSegment(sketch, "E2450", {"start": v(-5933.5, 462.66) * mm, "end": v(-5936.58, 475.94) * mm});
            skLineSegment(sketch, "E2451", {"start": v(-5936.58, 475.94) * mm, "end": v(-5939.73, 488.22) * mm});
            skLineSegment(sketch, "E2452", {"start": v(-5939.73, 488.22) * mm, "end": v(-5942.9, 499.5) * mm});
            skLineSegment(sketch, "E2453", {"start": v(-5942.9, 499.5) * mm, "end": v(-5946.07, 509.78) * mm});
            skLineSegment(sketch, "E2454", {"start": v(-5946.07, 509.78) * mm, "end": v(-5949.16, 519.08) * mm});
            skLineSegment(sketch, "E2455", {"start": v(-5949.16, 519.08) * mm, "end": v(-5952.15, 527.41) * mm});
            skLineSegment(sketch, "E2456", {"start": v(-5952.15, 527.41) * mm, "end": v(-5954.98, 534.78) * mm});
            skLineSegment(sketch, "E2457", {"start": v(-5954.98, 534.78) * mm, "end": v(-5957.63, 541.19) * mm});
            skLineSegment(sketch, "E2458", {"start": v(-5957.63, 541.19) * mm, "end": v(-5960.03, 546.66) * mm});
            skLineSegment(sketch, "E2459", {"start": v(-5960.03, 546.66) * mm, "end": v(-5962.16, 551.21) * mm});
            skLineSegment(sketch, "E2460", {"start": v(-5962.16, 551.21) * mm, "end": v(-5963.96, 554.85) * mm});
            skLineSegment(sketch, "E2461", {"start": v(-5963.96, 554.85) * mm, "end": v(-5965.4, 557.6) * mm});
            skLineSegment(sketch, "E2462", {"start": v(-5965.4, 557.6) * mm, "end": v(-5966.45, 559.49) * mm});
            skLineSegment(sketch, "E2463", {"start": v(-5966.45, 559.49) * mm, "end": v(-5967.06, 560.52) * mm});
            skLineSegment(sketch, "E2464", {"start": v(-5967.06, 560.52) * mm, "end": v(-6048.65, 690.72) * mm});
            skLineSegment(sketch, "E2465", {"start": v(-6048.65, 690.72) * mm, "end": v(-5825.93, 858.78) * mm});
            skLineSegment(sketch, "E2466", {"start": v(-5825.93, 858.78) * mm, "end": v(-5723.11, 744.6) * mm});
            skLineSegment(sketch, "E2467", {"start": v(-5723.11, 744.6) * mm, "end": v(-5722.29, 743.73) * mm});
            skLineSegment(sketch, "E2468", {"start": v(-5722.29, 743.73) * mm, "end": v(-5720.76, 742.21) * mm});
            skLineSegment(sketch, "E2469", {"start": v(-5720.76, 742.21) * mm, "end": v(-5718.51, 740.07) * mm});
            skLineSegment(sketch, "E2470", {"start": v(-5718.51, 740.07) * mm, "end": v(-5715.5, 737.33) * mm});
            skLineSegment(sketch, "E2471", {"start": v(-5715.5, 737.33) * mm, "end": v(-5711.72, 734.04) * mm});
            skLineSegment(sketch, "E2472", {"start": v(-5711.72, 734.04) * mm, "end": v(-5707.11, 730.22) * mm});
            skLineSegment(sketch, "E2473", {"start": v(-5707.11, 730.22) * mm, "end": v(-5701.67, 725.92) * mm});
            skLineSegment(sketch, "E2474", {"start": v(-5701.67, 725.92) * mm, "end": v(-5695.37, 721.18) * mm});
            skLineSegment(sketch, "E2475", {"start": v(-5695.37, 721.18) * mm, "end": v(-5688.18, 716.02) * mm});
            skLineSegment(sketch, "E2476", {"start": v(-5688.18, 716.02) * mm, "end": v(-5680.08, 710.5) * mm});
            skLineSegment(sketch, "E2477", {"start": v(-5680.08, 710.5) * mm, "end": v(-5671.06, 704.63) * mm});
            skLineSegment(sketch, "E2478", {"start": v(-5671.06, 704.63) * mm, "end": v(-5661.08, 698.48) * mm});
            skLineSegment(sketch, "E2479", {"start": v(-5661.08, 698.48) * mm, "end": v(-5650.14, 692.08) * mm});
            skLineSegment(sketch, "E2480", {"start": v(-5650.14, 692.08) * mm, "end": v(-5638.22, 685.48) * mm});
            skLineSegment(sketch, "E2481", {"start": v(-5638.22, 685.48) * mm, "end": v(-5625.3, 678.7) * mm});
            skLineSegment(sketch, "E2482", {"start": v(-5625.3, 678.7) * mm, "end": v(-5611.37, 671.81) * mm});
            skLineSegment(sketch, "E2483", {"start": v(-5611.37, 671.81) * mm, "end": v(-5596.42, 664.84) * mm});
            skLineSegment(sketch, "E2484", {"start": v(-5596.42, 664.84) * mm, "end": v(-5580.43, 657.84) * mm});
            skLineSegment(sketch, "E2485", {"start": v(-5580.43, 657.84) * mm, "end": v(-5563.4, 650.84) * mm});
            skLineSegment(sketch, "E2486", {"start": v(-5563.4, 650.84) * mm, "end": v(-5545.31, 643.9) * mm});
            skLineSegment(sketch, "E2487", {"start": v(-5545.31, 643.9) * mm, "end": v(-5526.17, 637.06) * mm});
            skLineSegment(sketch, "E2488", {"start": v(-5526.17, 637.06) * mm, "end": v(-5505.97, 630.37) * mm});
            skLineSegment(sketch, "E2489", {"start": v(-5505.97, 630.37) * mm, "end": v(-5484.7, 623.87) * mm});
            skLineSegment(sketch, "E2490", {"start": v(-5484.7, 623.87) * mm, "end": v(-5462.37, 617.6) * mm});
            skLineSegment(sketch, "E2491", {"start": v(-5462.37, 617.6) * mm, "end": v(-5438.97, 611.63) * mm});
            skLineSegment(sketch, "E2492", {"start": v(-5438.97, 611.63) * mm, "end": v(-5414.5, 605.98) * mm});
            skLineSegment(sketch, "E2493", {"start": v(-5414.5, 605.98) * mm, "end": v(-5388.98, 600.72) * mm});
            skLineSegment(sketch, "E2494", {"start": v(-5388.98, 600.72) * mm, "end": v(-5362.4, 595.87) * mm});
            skLineSegment(sketch, "E2495", {"start": v(-5362.4, 595.87) * mm, "end": v(-5334.76, 591.5) * mm});
            skLineSegment(sketch, "E2496", {"start": v(-5334.76, 591.5) * mm, "end": v(-5315.6, 596.39) * mm});
            skLineSegment(sketch, "E2497", {"start": v(-5315.6, 596.39) * mm, "end": v(-5235.34, 688.85) * mm});
            skLineSegment(sketch, "E2498", {"start": v(-5235.34, 688.85) * mm, "end": v(-5233.18, 708.5) * mm});
            skLineSegment(sketch, "E2499", {"start": v(-5233.18, 708.5) * mm, "end": v(-5241.4, 735.25) * mm});
            skLineSegment(sketch, "E2500", {"start": v(-5241.4, 735.25) * mm, "end": v(-5249.93, 760.89) * mm});
            skLineSegment(sketch, "E2501", {"start": v(-5249.93, 760.89) * mm, "end": v(-5258.73, 785.42) * mm});
            skLineSegment(sketch, "E2502", {"start": v(-5258.73, 785.42) * mm, "end": v(-5267.76, 808.85) * mm});
            skLineSegment(sketch, "E2503", {"start": v(-5267.76, 808.85) * mm, "end": v(-5276.96, 831.18) * mm});
            skLineSegment(sketch, "E2504", {"start": v(-5276.96, 831.18) * mm, "end": v(-5286.3, 852.4) * mm});
            skLineSegment(sketch, "E2505", {"start": v(-5286.3, 852.4) * mm, "end": v(-5295.73, 872.55) * mm});
            skLineSegment(sketch, "E2506", {"start": v(-5295.73, 872.55) * mm, "end": v(-5305.2, 891.62) * mm});
            skLineSegment(sketch, "E2507", {"start": v(-5305.2, 891.62) * mm, "end": v(-5314.65, 909.6) * mm});
            skLineSegment(sketch, "E2508", {"start": v(-5314.65, 909.6) * mm, "end": v(-5324.06, 926.53) * mm});
            skLineSegment(sketch, "E2509", {"start": v(-5324.06, 926.53) * mm, "end": v(-5333.38, 942.42) * mm});
            skLineSegment(sketch, "E2510", {"start": v(-5333.38, 942.42) * mm, "end": v(-5342.56, 957.26) * mm});
            skLineSegment(sketch, "E2511", {"start": v(-5342.56, 957.26) * mm, "end": v(-5351.56, 971.09) * mm});
            skLineSegment(sketch, "E2512", {"start": v(-5351.56, 971.09) * mm, "end": v(-5360.35, 983.91) * mm});
            skLineSegment(sketch, "E2513", {"start": v(-5360.35, 983.91) * mm, "end": v(-5368.87, 995.75) * mm});
            skLineSegment(sketch, "E2514", {"start": v(-5368.87, 995.75) * mm, "end": v(-5377.08, 1006.63) * mm});
            skLineSegment(sketch, "E2515", {"start": v(-5377.08, 1006.63) * mm, "end": v(-5384.95, 1016.56) * mm});
            skLineSegment(sketch, "E2516", {"start": v(-5384.95, 1016.56) * mm, "end": v(-5392.44, 1025.57) * mm});
            skLineSegment(sketch, "E2517", {"start": v(-5392.44, 1025.57) * mm, "end": v(-5399.51, 1033.68) * mm});
            skLineSegment(sketch, "E2518", {"start": v(-5399.51, 1033.68) * mm, "end": v(-5406.12, 1040.92) * mm});
            skLineSegment(sketch, "E2519", {"start": v(-5406.12, 1040.92) * mm, "end": v(-5412.24, 1047.32) * mm});
            skLineSegment(sketch, "E2520", {"start": v(-5412.24, 1047.32) * mm, "end": v(-5417.82, 1052.9) * mm});
            skLineSegment(sketch, "E2521", {"start": v(-5417.82, 1052.9) * mm, "end": v(-5422.85, 1057.67) * mm});
            skLineSegment(sketch, "E2522", {"start": v(-5422.85, 1057.67) * mm, "end": v(-5427.27, 1061.7) * mm});
            skLineSegment(sketch, "E2523", {"start": v(-5427.27, 1061.7) * mm, "end": v(-5431.06, 1064.99) * mm});
            skLineSegment(sketch, "E2524", {"start": v(-5431.06, 1064.99) * mm, "end": v(-5434.2, 1067.58) * mm});
            skLineSegment(sketch, "E2525", {"start": v(-5434.2, 1067.58) * mm, "end": v(-5436.63, 1069.5) * mm});
            skLineSegment(sketch, "E2526", {"start": v(-5436.63, 1069.5) * mm, "end": v(-5438.35, 1070.8) * mm});
            skLineSegment(sketch, "E2527", {"start": v(-5438.35, 1070.8) * mm, "end": v(-5439.32, 1071.5) * mm});
            skLineSegment(sketch, "E2528", {"start": v(-5439.32, 1071.5) * mm, "end": v(-5566.82, 1157.25) * mm});
            skLineSegment(sketch, "E2529", {"start": v(-5566.82, 1157.25) * mm, "end": v(-5431.71, 1401.37) * mm});
            skLineSegment(sketch, "E2530", {"start": v(-5431.71, 1401.37) * mm, "end": v(-5291.34, 1338.88) * mm});
            skLineSegment(sketch, "E2531", {"start": v(-5291.34, 1338.88) * mm, "end": v(-5290.24, 1338.43) * mm});
            skLineSegment(sketch, "E2532", {"start": v(-5290.24, 1338.43) * mm, "end": v(-5288.23, 1337.66) * mm});
            skLineSegment(sketch, "E2533", {"start": v(-5288.23, 1337.66) * mm, "end": v(-5285.3, 1336.61) * mm});
            skLineSegment(sketch, "E2534", {"start": v(-5285.3, 1336.61) * mm, "end": v(-5281.44, 1335.34) * mm});
            skLineSegment(sketch, "E2535", {"start": v(-5281.44, 1335.34) * mm, "end": v(-5276.63, 1333.87) * mm});
            skLineSegment(sketch, "E2536", {"start": v(-5276.63, 1333.87) * mm, "end": v(-5270.88, 1332.26) * mm});
            skLineSegment(sketch, "E2537", {"start": v(-5270.88, 1332.26) * mm, "end": v(-5264.16, 1330.54) * mm});
            skLineSegment(sketch, "E2538", {"start": v(-5264.16, 1330.54) * mm, "end": v(-5256.47, 1328.77) * mm});
            skLineSegment(sketch, "E2539", {"start": v(-5256.47, 1328.77) * mm, "end": v(-5247.8, 1326.98) * mm});
            skLineSegment(sketch, "E2540", {"start": v(-5247.8, 1326.98) * mm, "end": v(-5238.16, 1325.23) * mm});
            skLineSegment(sketch, "E2541", {"start": v(-5238.16, 1325.23) * mm, "end": v(-5227.53, 1323.55) * mm});
            skLineSegment(sketch, "E2542", {"start": v(-5227.53, 1323.55) * mm, "end": v(-5215.92, 1321.98) * mm});
            skLineSegment(sketch, "E2543", {"start": v(-5215.92, 1321.98) * mm, "end": v(-5203.32, 1320.59) * mm});
            skLineSegment(sketch, "E2544", {"start": v(-5203.32, 1320.59) * mm, "end": v(-5189.74, 1319.4) * mm});
            skLineSegment(sketch, "E2545", {"start": v(-5189.74, 1319.4) * mm, "end": v(-5175.19, 1318.47) * mm});
            skLineSegment(sketch, "E2546", {"start": v(-5175.19, 1318.47) * mm, "end": v(-5159.66, 1317.84) * mm});
            skLineSegment(sketch, "E2547", {"start": v(-5159.66, 1317.84) * mm, "end": v(-5143.16, 1317.55) * mm});
            skLineSegment(sketch, "E2548", {"start": v(-5143.16, 1317.55) * mm, "end": v(-5125.7, 1317.66) * mm});
            skLineSegment(sketch, "E2549", {"start": v(-5125.7, 1317.66) * mm, "end": v(-5107.3, 1318.2) * mm});
            skLineSegment(sketch, "E2550", {"start": v(-5107.3, 1318.2) * mm, "end": v(-5087.96, 1319.2) * mm});
            skLineSegment(sketch, "E2551", {"start": v(-5087.96, 1319.2) * mm, "end": v(-5067.7, 1320.75) * mm});
            skLineSegment(sketch, "E2552", {"start": v(-5067.7, 1320.75) * mm, "end": v(-5046.51, 1322.85) * mm});
            skLineSegment(sketch, "E2553", {"start": v(-5046.51, 1322.85) * mm, "end": v(-5024.44, 1325.56) * mm});
            skLineSegment(sketch, "E2554", {"start": v(-5024.44, 1325.56) * mm, "end": v(-5001.49, 1328.93) * mm});
            skLineSegment(sketch, "E2555", {"start": v(-5001.49, 1328.93) * mm, "end": v(-4977.68, 1332.98) * mm});
            skLineSegment(sketch, "E2556", {"start": v(-4977.68, 1332.98) * mm, "end": v(-4953.03, 1337.78) * mm});
            skLineSegment(sketch, "E2557", {"start": v(-4953.03, 1337.78) * mm, "end": v(-4927.57, 1343.34) * mm});
            skLineSegment(sketch, "E2558", {"start": v(-4927.57, 1343.34) * mm, "end": v(-4901.32, 1349.73) * mm});
            skLineSegment(sketch, "E2559", {"start": v(-4901.32, 1349.73) * mm, "end": v(-4874.3, 1356.97) * mm});
            skLineSegment(sketch, "E2560", {"start": v(-4874.3, 1356.97) * mm, "end": v(-4858.78, 1369.23) * mm});
            skLineSegment(sketch, "E2561", {"start": v(-4858.78, 1369.23) * mm, "end": v(-4823.06, 1486.35) * mm});
            skLineSegment(sketch, "E2562", {"start": v(-4823.06, 1486.35) * mm, "end": v(-4829.09, 1505.18) * mm});
            skLineSegment(sketch, "E2563", {"start": v(-4829.09, 1505.18) * mm, "end": v(-4847.47, 1526.27) * mm});
            skLineSegment(sketch, "E2564", {"start": v(-4847.47, 1526.27) * mm, "end": v(-4865.7, 1546.22) * mm});
            skLineSegment(sketch, "E2565", {"start": v(-4865.7, 1546.22) * mm, "end": v(-4883.71, 1565.05) * mm});
            skLineSegment(sketch, "E2566", {"start": v(-4883.71, 1565.05) * mm, "end": v(-4901.49, 1582.79) * mm});
            skLineSegment(sketch, "E2567", {"start": v(-4901.49, 1582.79) * mm, "end": v(-4918.98, 1599.44) * mm});
            skLineSegment(sketch, "E2568", {"start": v(-4918.98, 1599.44) * mm, "end": v(-4936.15, 1615.04) * mm});
            skLineSegment(sketch, "E2569", {"start": v(-4936.15, 1615.04) * mm, "end": v(-4952.95, 1629.6) * mm});
            skLineSegment(sketch, "E2570", {"start": v(-4952.95, 1629.6) * mm, "end": v(-4969.35, 1643.17) * mm});
            skLineSegment(sketch, "E2571", {"start": v(-4969.35, 1643.17) * mm, "end": v(-4985.3, 1655.76) * mm});
            skLineSegment(sketch, "E2572", {"start": v(-4985.3, 1655.76) * mm, "end": v(-5000.8, 1667.4) * mm});
            skLineSegment(sketch, "E2573", {"start": v(-5000.8, 1667.4) * mm, "end": v(-5015.76, 1678.11) * mm});
            skLineSegment(sketch, "E2574", {"start": v(-5015.76, 1678.11) * mm, "end": v(-5030.19, 1687.94) * mm});
            skLineSegment(sketch, "E2575", {"start": v(-5030.19, 1687.94) * mm, "end": v(-5044.04, 1696.91) * mm});
            skLineSegment(sketch, "E2576", {"start": v(-5044.04, 1696.91) * mm, "end": v(-5057.28, 1705.06) * mm});
            skLineSegment(sketch, "E2577", {"start": v(-5057.28, 1705.06) * mm, "end": v(-5069.87, 1712.4) * mm});
            skLineSegment(sketch, "E2578", {"start": v(-5069.87, 1712.4) * mm, "end": v(-5081.8, 1719) * mm});
            skLineSegment(sketch, "E2579", {"start": v(-5081.8, 1719) * mm, "end": v(-5093.04, 1724.87) * mm});
            skLineSegment(sketch, "E2580", {"start": v(-5093.04, 1724.87) * mm, "end": v(-5103.54, 1730.06) * mm});
            skLineSegment(sketch, "E2581", {"start": v(-5103.54, 1730.06) * mm, "end": v(-5113.3, 1734.6) * mm});
            skLineSegment(sketch, "E2582", {"start": v(-5113.3, 1734.6) * mm, "end": v(-5122.28, 1738.52) * mm});
            skLineSegment(sketch, "E2583", {"start": v(-5122.28, 1738.52) * mm, "end": v(-5130.47, 1741.87) * mm});
            skLineSegment(sketch, "E2584", {"start": v(-5130.47, 1741.87) * mm, "end": v(-5137.84, 1744.7) * mm});
            skLineSegment(sketch, "E2585", {"start": v(-5137.84, 1744.7) * mm, "end": v(-5144.37, 1747.02) * mm});
            skLineSegment(sketch, "E2586", {"start": v(-5144.37, 1747.02) * mm, "end": v(-5150.05, 1748.9) * mm});
            skLineSegment(sketch, "E2587", {"start": v(-5150.05, 1748.9) * mm, "end": v(-5154.86, 1750.36) * mm});
            skLineSegment(sketch, "E2588", {"start": v(-5154.86, 1750.36) * mm, "end": v(-5158.77, 1751.45) * mm});
            skLineSegment(sketch, "E2589", {"start": v(-5158.77, 1751.45) * mm, "end": v(-5161.78, 1752.22) * mm});
            skLineSegment(sketch, "E2590", {"start": v(-5161.78, 1752.22) * mm, "end": v(-5163.88, 1752.7) * mm});
            skLineSegment(sketch, "E2591", {"start": v(-5163.88, 1752.7) * mm, "end": v(-5165.05, 1752.95) * mm});
            skLineSegment(sketch, "E2592", {"start": v(-5165.05, 1752.95) * mm, "end": v(-5316.4, 1779.43) * mm});
            skLineSegment(sketch, "E2593", {"start": v(-5316.4, 1779.43) * mm, "end": v(-5292.27, 2057.4) * mm});
            skLineSegment(sketch, "E2594", {"start": v(-5292.27, 2057.4) * mm, "end": v(-5138.62, 2057.4) * mm});
            skLineSegment(sketch, "E2595", {"start": v(-5138.62, 2057.4) * mm, "end": v(-5137.42, 2057.44) * mm});
            skLineSegment(sketch, "E2596", {"start": v(-5137.42, 2057.44) * mm, "end": v(-5135.27, 2057.55) * mm});
            skLineSegment(sketch, "E2597", {"start": v(-6701.97, 2057.4) * mm, "end": v(-7108.37, 2057.4) * mm});
            skFitSpline(sketch, "E2598", {"points": [v(-4914.83, 2290.81) * mm, v(-4914.83, 2235.75) * mm, v(-4959.46, 2191.12) * mm, v(-5014.53, 2191.12) * mm]});
            skFitSpline(sketch, "E2599", {"points": [v(-5014.53, 2191.12) * mm, v(-5069.59, 2191.12) * mm, v(-5114.22, 2235.75) * mm, v(-5114.22, 2290.81) * mm]});
            skFitSpline(sketch, "E2600", {"points": [v(-5114.22, 2290.81) * mm, v(-5114.22, 2345.87) * mm, v(-5069.59, 2390.5) * mm, v(-5014.53, 2390.5) * mm]});
            skFitSpline(sketch, "E2601", {"points": [v(-5014.53, 2390.5) * mm, v(-4959.46, 2390.5) * mm, v(-4914.83, 2345.87) * mm, v(-4914.83, 2290.81) * mm]});
            skLineSegment(sketch, "E2602", {"start": v(-6905.17, 1854.2) * mm, "end": v(-6905.17, 2260.6) * mm});
            skLineSegment(sketch, "E2603", {"start": v(-7224.6, 3325.98) * mm, "end": v(-7254.07, 3318.05) * mm});
            skLineSegment(sketch, "E2604", {"start": v(-7254.07, 3318.05) * mm, "end": v(-7283.33, 3309.72) * mm});
            skLineSegment(sketch, "E2605", {"start": v(-7283.33, 3309.72) * mm, "end": v(-7312.38, 3300.58) * mm});
            skLineSegment(sketch, "E2606", {"start": v(-7312.38, 3300.58) * mm, "end": v(-7341.24, 3290.62) * mm});
            skLineSegment(sketch, "E2607", {"start": v(-7265.65, 3251.2) * mm, "end": v(-7301, 3368.04) * mm});
            skLineSegment(sketch, "E2608", {"start": v(-7239.44, 3385.1) * mm, "end": v(-7262.2, 3347.52) * mm});
            skLineSegment(sketch, "E2609", {"start": v(-7262.2, 3347.52) * mm, "end": v(-7283.33, 3309.72) * mm});
            skLineSegment(sketch, "E2610", {"start": v(-7283.33, 3309.72) * mm, "end": v(-7302.83, 3271.52) * mm});
            skLineSegment(sketch, "E2611", {"start": v(-7302.83, 3271.52) * mm, "end": v(-7320.92, 3233.12) * mm});
            skLineSegment(sketch, "E2612", {"start": v(-7209.77, 3266.85) * mm, "end": v(-7245.94, 3288.8) * mm});
            skLineSegment(sketch, "E2613", {"start": v(-7245.94, 3288.8) * mm, "end": v(-7283.33, 3309.72) * mm});
            skLineSegment(sketch, "E2614", {"start": v(-7283.33, 3309.72) * mm, "end": v(-7321.93, 3329.43) * mm});
            skLineSegment(sketch, "E2615", {"start": v(-7321.93, 3329.43) * mm, "end": v(-7361.56, 3348.13) * mm});
            skLineSegment(sketch, "E2616", {"start": v(-7165.06, 3339.39) * mm, "end": v(-7135.2, 3345.08) * mm});
            skLineSegment(sketch, "E2617", {"start": v(-7135.2, 3345.08) * mm, "end": v(-7105.12, 3350.16) * mm});
            skLineSegment(sketch, "E2618", {"start": v(-7105.12, 3350.16) * mm, "end": v(-7075.05, 3354.43) * mm});
            skLineSegment(sketch, "E2619", {"start": v(-7075.05, 3354.43) * mm, "end": v(-7041.52, 3327.8) * mm});
            skLineSegment(sketch, "E2620", {"start": v(-7041.52, 3327.8) * mm, "end": v(-7038.27, 3297.33) * mm});
            skLineSegment(sketch, "E2621", {"start": v(-7038.27, 3297.33) * mm, "end": v(-7063.06, 3263.8) * mm});
            skLineSegment(sketch, "E2622", {"start": v(-7063.06, 3263.8) * mm, "end": v(-7091.1, 3259.73) * mm});
            skLineSegment(sketch, "E2623", {"start": v(-7091.1, 3259.73) * mm, "end": v(-7119.14, 3255.06) * mm});
            skLineSegment(sketch, "E2624", {"start": v(-7119.14, 3255.06) * mm, "end": v(-7153.08, 3279.65) * mm});
            skLineSegment(sketch, "E2625", {"start": v(-7153.08, 3279.65) * mm, "end": v(-7171.16, 3369.26) * mm});
            skLineSegment(sketch, "E2626", {"start": v(-7171.16, 3369.26) * mm, "end": v(-7145.96, 3405.23) * mm});
            skLineSegment(sketch, "E2627", {"start": v(-7145.96, 3405.23) * mm, "end": v(-7119.14, 3440.58) * mm});
            skLineSegment(sketch, "E2628", {"start": v(-7119.14, 3440.58) * mm, "end": v(-7086.83, 3445.05) * mm});
            skLineSegment(sketch, "E2629", {"start": v(-6696.9, 3441.4) * mm, "end": v(-6724.12, 3260.55) * mm});
            skLineSegment(sketch, "E2630", {"start": v(-6724.12, 3260.55) * mm, "end": v(-6746.27, 3309.72) * mm});
            skLineSegment(sketch, "E2631", {"start": v(-6746.27, 3309.72) * mm, "end": v(-6770.86, 3358.49) * mm});
            skLineSegment(sketch, "E2632", {"start": v(-6770.86, 3358.49) * mm, "end": v(-6797.68, 3406.85) * mm});
            skLineSegment(sketch, "E2633", {"start": v(-6797.68, 3406.85) * mm, "end": v(-6826.53, 3454.8) * mm});
            skLineSegment(sketch, "E2634", {"start": v(-6826.53, 3454.8) * mm, "end": v(-6836.7, 3272.13) * mm});
            skLineSegment(sketch, "E2635", {"start": v(-6523.36, 3340.4) * mm, "end": v(-6553.43, 3348.94) * mm});
            skLineSegment(sketch, "E2636", {"start": v(-6553.43, 3348.94) * mm, "end": v(-6583.5, 3356.86) * mm});
            skLineSegment(sketch, "E2637", {"start": v(-6583.5, 3356.86) * mm, "end": v(-6613.99, 3363.98) * mm});
            skLineSegment(sketch, "E2638", {"start": v(-6613.99, 3363.98) * mm, "end": v(-6644.47, 3370.28) * mm});
            skLineSegment(sketch, "E2639", {"start": v(-6540.83, 3281.88) * mm, "end": v(-6569.48, 3290.01) * mm});
            skLineSegment(sketch, "E2640", {"start": v(-6569.48, 3290.01) * mm, "end": v(-6598.14, 3297.53) * mm});
            skLineSegment(sketch, "E2641", {"start": v(-6598.14, 3297.53) * mm, "end": v(-6627.2, 3304.44) * mm});
            skLineSegment(sketch, "E2642", {"start": v(-6627.2, 3304.44) * mm, "end": v(-6656.25, 3310.53) * mm});
            skLineSegment(sketch, "E2643", {"start": v(-6454.07, 3349.96) * mm, "end": v(-6413.22, 3367.63) * mm});
            skLineSegment(sketch, "E2644", {"start": v(-6413.22, 3367.63) * mm, "end": v(-6477.64, 3196.34) * mm});
            skLineSegment(sketch, "E2645", {"start": v(-6451.22, 3186.18) * mm, "end": v(-6477.64, 3196.34) * mm});
            skLineSegment(sketch, "E2646", {"start": v(-6477.64, 3196.34) * mm, "end": v(-6504.26, 3206.09) * mm});
            skLineSegment(sketch, "E2647", {"start": v(-6206.98, 3270.3) * mm, "end": v(-6235.42, 3286.35) * mm});
            skLineSegment(sketch, "E2648", {"start": v(-6235.42, 3286.35) * mm, "end": v(-6264.28, 3301.6) * mm});
            skLineSegment(sketch, "E2649", {"start": v(-6264.28, 3301.6) * mm, "end": v(-6293.54, 3316.22) * mm});
            skLineSegment(sketch, "E2650", {"start": v(-6293.54, 3316.22) * mm, "end": v(-6323, 3330.04) * mm});
            skLineSegment(sketch, "E2651", {"start": v(-6323, 3330.04) * mm, "end": v(-6348.4, 3274.57) * mm});
            skLineSegment(sketch, "E2652", {"start": v(-6348.4, 3274.57) * mm, "end": v(-6320.16, 3261.36) * mm});
            skLineSegment(sketch, "E2653", {"start": v(-6320.16, 3261.36) * mm, "end": v(-6292.12, 3247.34) * mm});
            skLineSegment(sketch, "E2654", {"start": v(-6292.12, 3247.34) * mm, "end": v(-6264.68, 3232.7) * mm});
            skLineSegment(sketch, "E2655", {"start": v(-6264.68, 3232.7) * mm, "end": v(-6252.7, 3191.05) * mm});
            skLineSegment(sketch, "E2656", {"start": v(-6252.7, 3191.05) * mm, "end": v(-6282.97, 3138.22) * mm});
            skLineSegment(sketch, "E2657", {"start": v(-6282.97, 3138.22) * mm, "end": v(-6323, 3125.83) * mm});
            skLineSegment(sketch, "E2658", {"start": v(-6323, 3125.83) * mm, "end": v(-6348, 3139.03) * mm});
            skLineSegment(sketch, "E2659", {"start": v(-6348, 3139.03) * mm, "end": v(-6373.4, 3151.63) * mm});
            skLineSegment(sketch, "E2660", {"start": v(-6373.4, 3151.63) * mm, "end": v(-6386.4, 3191.46) * mm});
            skLineSegment(sketch, "E2661", {"start": v(-6077.13, 3070.15) * mm, "end": v(-6053.76, 3050.64) * mm});
            skLineSegment(sketch, "E2662", {"start": v(-6053.76, 3050.64) * mm, "end": v(-6031, 3030.52) * mm});
            skLineSegment(sketch, "E2663", {"start": v(-6031, 3030.52) * mm, "end": v(-6008.45, 3009.8) * mm});
            skLineSegment(sketch, "E2664", {"start": v(-6008.45, 3009.8) * mm, "end": v(-5965.17, 3010.4) * mm});
            skLineSegment(sketch, "E2665", {"start": v(-5965.17, 3010.4) * mm, "end": v(-5943.83, 3032.15) * mm});
            skLineSegment(sketch, "E2666", {"start": v(-5943.83, 3032.15) * mm, "end": v(-5945.86, 3076.45) * mm});
            skLineSegment(sketch, "E2667", {"start": v(-5945.86, 3076.45) * mm, "end": v(-5969.84, 3098.4) * mm});
            skLineSegment(sketch, "E2668", {"start": v(-5969.84, 3098.4) * mm, "end": v(-5994.23, 3119.93) * mm});
            skLineSegment(sketch, "E2669", {"start": v(-5994.23, 3119.93) * mm, "end": v(-6019.42, 3140.86) * mm});
            skLineSegment(sketch, "E2670", {"start": v(-6019.42, 3140.86) * mm, "end": v(-6135.04, 2999.23) * mm});
            skLineSegment(sketch, "E2671", {"start": v(-6011.3, 2882.8) * mm, "end": v(-5921.68, 2965.5) * mm});
            skLineSegment(sketch, "E2672", {"start": v(-5899.33, 2986.23) * mm, "end": v(-5876.98, 3006.95) * mm});
            skLineSegment(sketch, "E2673", {"start": v(-5880.03, 2767.58) * mm, "end": v(-5921.48, 2773.27) * mm});
            skLineSegment(sketch, "E2674", {"start": v(-5921.48, 2773.27) * mm, "end": v(-5914.16, 2814.52) * mm});
            skLineSegment(sketch, "E2675", {"start": v(-5914.16, 2814.52) * mm, "end": v(-5793.06, 2907.18) * mm});
            skLineSegment(sketch, "E2676", {"start": v(-5804.84, 2819.6) * mm, "end": v(-5822.93, 2845) * mm});
            skLineSegment(sketch, "E2677", {"start": v(-5822.93, 2845) * mm, "end": v(-5841.42, 2870) * mm});
            skLineSegment(sketch, "E2678", {"start": v(-5841.42, 2870) * mm, "end": v(-5860.72, 2894.58) * mm});
            skLineSegment(sketch, "E2679", {"start": v(-5860.72, 2894.58) * mm, "end": v(-5880.43, 2918.76) * mm});
            skLineSegment(sketch, "E2680", {"start": v(-5818.25, 2604) * mm, "end": v(-5831.26, 2629.2) * mm});
            skLineSegment(sketch, "E2681", {"start": v(-5831.26, 2629.2) * mm, "end": v(-5844.87, 2654.2) * mm});
            skLineSegment(sketch, "E2682", {"start": v(-5844.87, 2654.2) * mm, "end": v(-5859.1, 2678.58) * mm});
            skLineSegment(sketch, "E2683", {"start": v(-5859.1, 2678.58) * mm, "end": v(-5847.92, 2719.02) * mm});
            skLineSegment(sketch, "E2684", {"start": v(-5847.92, 2719.02) * mm, "end": v(-5796.3, 2751.33) * mm});
            skLineSegment(sketch, "E2685", {"start": v(-5796.3, 2751.33) * mm, "end": v(-5754.25, 2740.96) * mm});
            skLineSegment(sketch, "E2686", {"start": v(-5754.25, 2740.96) * mm, "end": v(-5738.6, 2713.94) * mm});
            skLineSegment(sketch, "E2687", {"start": v(-5738.6, 2713.94) * mm, "end": v(-5723.77, 2686.5) * mm});
            skLineSegment(sketch, "E2688", {"start": v(-5723.77, 2686.5) * mm, "end": v(-5709.34, 2658.87) * mm});
            skLineSegment(sketch, "E2689", {"start": v(-5738.2, 2577.6) * mm, "end": v(-5698.37, 2562.15) * mm});
            skLineSegment(sketch, "E2690", {"start": v(-5698.37, 2562.15) * mm, "end": v(-5658.54, 2544.88) * mm});
            skLineSegment(sketch, "E2691", {"start": v(-5658.54, 2544.88) * mm, "end": v(-5647.57, 2515.82) * mm});
            skLineSegment(sketch, "E2692", {"start": v(-5647.57, 2515.82) * mm, "end": v(-5666.06, 2476.6) * mm});
            skLineSegment(sketch, "E2693", {"start": v(-5666.06, 2476.6) * mm, "end": v(-5752.62, 2447.34) * mm});
            skLineSegment(sketch, "E2694", {"start": v(-5793.87, 2552.8) * mm, "end": v(-5626.84, 2627.38) * mm});
            skLineSegment(sketch, "E2695", {"start": v(-5704.67, 2254.91) * mm, "end": v(-5700.4, 2226.87) * mm});
            skLineSegment(sketch, "E2696", {"start": v(-5700.4, 2226.87) * mm, "end": v(-5696.74, 2198.83) * mm});
            skLineSegment(sketch, "E2697", {"start": v(-5696.74, 2198.83) * mm, "end": v(-5693.7, 2170.58) * mm});
            skLineSegment(sketch, "E2698", {"start": v(-5693.7, 2170.58) * mm, "end": v(-5660.98, 2144.57) * mm});
            skLineSegment(sketch, "E2699", {"start": v(-5660.98, 2144.57) * mm, "end": v(-5539.46, 2153.1) * mm});
            skLineSegment(sketch, "E2700", {"start": v(-5539.46, 2153.1) * mm, "end": v(-5511.63, 2187.65) * mm});
            skLineSegment(sketch, "E2701", {"start": v(-5511.63, 2187.65) * mm, "end": v(-5515.08, 2220.16) * mm});
            skLineSegment(sketch, "E2702", {"start": v(-5515.08, 2220.16) * mm, "end": v(-5519.35, 2252.47) * mm});
            skLineSegment(sketch, "E2703", {"start": v(-5519.35, 2252.47) * mm, "end": v(-5524.22, 2284.58) * mm});
            skLineSegment(sketch, "E2704", {"start": v(-5519.35, 2252.47) * mm, "end": v(-5700.4, 2226.87) * mm});
            skLineSegment(sketch, "E2705", {"start": v(-5569.94, 1963.93) * mm, "end": v(-5568.12, 1995.02) * mm});
            skLineSegment(sketch, "E2706", {"start": v(-5568.12, 1995.02) * mm, "end": v(-5566.9, 2026.31) * mm});
            skLineSegment(sketch, "E2707", {"start": v(-5566.9, 2026.31) * mm, "end": v(-5566.49, 2057.4) * mm});
            skLineSegment(sketch, "E2708", {"start": v(-5566.49, 2057.4) * mm, "end": v(-5566.9, 2088.49) * mm});
            skLineSegment(sketch, "E2709", {"start": v(-5630.7, 1968.2) * mm, "end": v(-5628.87, 1997.86) * mm});
            skLineSegment(sketch, "E2710", {"start": v(-5628.87, 1997.86) * mm, "end": v(-5627.86, 2027.73) * mm});
            skLineSegment(sketch, "E2711", {"start": v(-5627.86, 2027.73) * mm, "end": v(-5627.65, 2057.4) * mm});
            skLineSegment(sketch, "E2712", {"start": v(-5627.65, 2057.4) * mm, "end": v(-5627.86, 2087.07) * mm});
            skLineSegment(sketch, "E2713", {"start": v(-5545.36, 1898.3) * mm, "end": v(-5519.35, 1862.33) * mm});
            skLineSegment(sketch, "E2714", {"start": v(-5519.35, 1862.33) * mm, "end": v(-5524.22, 1830.22) * mm});
            skLineSegment(sketch, "E2715", {"start": v(-5524.22, 1830.22) * mm, "end": v(-5529.91, 1798.12) * mm});
            skLineSegment(sketch, "E2716", {"start": v(-5529.91, 1798.12) * mm, "end": v(-5566.08, 1772.31) * mm});
            skLineSegment(sketch, "E2717", {"start": v(-5566.08, 1772.31) * mm, "end": v(-5595.95, 1778.81) * mm});
            skLineSegment(sketch, "E2718", {"start": v(-5595.95, 1778.81) * mm, "end": v(-5619.73, 1814.98) * mm});
            skLineSegment(sketch, "E2719", {"start": v(-5619.73, 1814.98) * mm, "end": v(-5655.5, 1791.41) * mm});
            skLineSegment(sketch, "E2720", {"start": v(-5655.5, 1791.41) * mm, "end": v(-5685.36, 1797.71) * mm});
            skLineSegment(sketch, "E2721", {"start": v(-5685.36, 1797.71) * mm, "end": v(-5709.54, 1831.85) * mm});
            skLineSegment(sketch, "E2722", {"start": v(-5709.54, 1831.85) * mm, "end": v(-5704.67, 1859.89) * mm});
            skLineSegment(sketch, "E2723", {"start": v(-5704.67, 1859.89) * mm, "end": v(-5700.4, 1887.93) * mm});
            skLineSegment(sketch, "E2724", {"start": v(-5700.4, 1887.93) * mm, "end": v(-5666.46, 1912.52) * mm});
            skLineSegment(sketch, "E2725", {"start": v(-5614.44, 1845.06) * mm, "end": v(-5619.73, 1814.98) * mm});
            skLineSegment(sketch, "E2726", {"start": v(-5698.77, 1741.22) * mm, "end": v(-5728.24, 1748.94) * mm});
            skLineSegment(sketch, "E2727", {"start": v(-5569.33, 1639.82) * mm, "end": v(-5579.5, 1608.94) * mm});
            skLineSegment(sketch, "E2728", {"start": v(-5579.5, 1608.94) * mm, "end": v(-5590.26, 1578.05) * mm});
            skLineSegment(sketch, "E2729", {"start": v(-5590.26, 1578.05) * mm, "end": v(-5601.85, 1547.57) * mm});
            skLineSegment(sketch, "E2730", {"start": v(-5601.85, 1547.57) * mm, "end": v(-5614.04, 1517.5) * mm});
            skLineSegment(sketch, "E2731", {"start": v(-5614.04, 1517.5) * mm, "end": v(-5686.99, 1580.9) * mm});
            skLineSegment(sketch, "E2732", {"start": v(-5686.99, 1580.9) * mm, "end": v(-5762.17, 1640.84) * mm});
            skLineSegment(sketch, "E2733", {"start": v(-5701.82, 1342.75) * mm, "end": v(-5685.56, 1371) * mm});
            skLineSegment(sketch, "E2734", {"start": v(-5685.56, 1371) * mm, "end": v(-5669.92, 1399.64) * mm});
            skLineSegment(sketch, "E2735", {"start": v(-5669.92, 1399.64) * mm, "end": v(-5654.88, 1428.5) * mm});
            skLineSegment(sketch, "E2736", {"start": v(-5654.88, 1428.5) * mm, "end": v(-5640.66, 1457.76) * mm});
            skLineSegment(sketch, "E2737", {"start": v(-5640.66, 1457.76) * mm, "end": v(-5695.72, 1483.97) * mm});
            skLineSegment(sketch, "E2738", {"start": v(-5695.72, 1483.97) * mm, "end": v(-5709.34, 1455.93) * mm});
            skLineSegment(sketch, "E2739", {"start": v(-5709.34, 1455.93) * mm, "end": v(-5723.77, 1428.3) * mm});
            skLineSegment(sketch, "E2740", {"start": v(-5723.77, 1428.3) * mm, "end": v(-5738.6, 1400.86) * mm});
            skLineSegment(sketch, "E2741", {"start": v(-5738.6, 1400.86) * mm, "end": v(-5780.46, 1389.48) * mm});
            skLineSegment(sketch, "E2742", {"start": v(-5780.46, 1389.48) * mm, "end": v(-5832.88, 1420.57) * mm});
            skLineSegment(sketch, "E2743", {"start": v(-5832.88, 1420.57) * mm, "end": v(-5844.87, 1460.6) * mm});
            skLineSegment(sketch, "E2744", {"start": v(-5844.87, 1460.6) * mm, "end": v(-5831.26, 1485.6) * mm});
            skLineSegment(sketch, "E2745", {"start": v(-5831.26, 1485.6) * mm, "end": v(-5818.25, 1510.8) * mm});
            skLineSegment(sketch, "E2746", {"start": v(-5818.25, 1510.8) * mm, "end": v(-5778.22, 1523.19) * mm});
            skLineSegment(sketch, "E2747", {"start": v(-5903.8, 1215.75) * mm, "end": v(-5923.72, 1192.58) * mm});
            skLineSegment(sketch, "E2748", {"start": v(-5923.72, 1192.58) * mm, "end": v(-5944.24, 1170.03) * mm});
            skLineSegment(sketch, "E2749", {"start": v(-5944.24, 1170.03) * mm, "end": v(-5965.17, 1147.88) * mm});
            skLineSegment(sketch, "E2750", {"start": v(-5965.17, 1147.88) * mm, "end": v(-5965.17, 1104.4) * mm});
            skLineSegment(sketch, "E2751", {"start": v(-5965.17, 1104.4) * mm, "end": v(-5943.83, 1082.65) * mm});
            skLineSegment(sketch, "E2752", {"start": v(-5943.83, 1082.65) * mm, "end": v(-5899.33, 1084.28) * mm});
            skLineSegment(sketch, "E2753", {"start": v(-5899.33, 1084.28) * mm, "end": v(-5876.98, 1107.85) * mm});
            skLineSegment(sketch, "E2754", {"start": v(-5876.98, 1107.85) * mm, "end": v(-5855.24, 1132.03) * mm});
            skLineSegment(sketch, "E2755", {"start": v(-5855.24, 1132.03) * mm, "end": v(-5833.9, 1156.82) * mm});
            skLineSegment(sketch, "E2756", {"start": v(-5833.9, 1156.82) * mm, "end": v(-5973.9, 1274.47) * mm});
            skLineSegment(sketch, "E2757", {"start": v(-6107.2, 982.68) * mm, "end": v(-6082.21, 1001.57) * mm});
            skLineSegment(sketch, "E2758", {"start": v(-6082.21, 1001.57) * mm, "end": v(-6057.83, 1021.08) * mm});
            skLineSegment(sketch, "E2759", {"start": v(-6057.83, 1021.08) * mm, "end": v(-6034.05, 1041.2) * mm});
            skLineSegment(sketch, "E2760", {"start": v(-6034.05, 1041.2) * mm, "end": v(-6010.48, 1061.72) * mm});
            skLineSegment(sketch, "E2761", {"start": v(-6143.37, 1031.65) * mm, "end": v(-6119.8, 1049.73) * mm});
            skLineSegment(sketch, "E2762", {"start": v(-6119.8, 1049.73) * mm, "end": v(-6096.44, 1068.22) * mm});
            skLineSegment(sketch, "E2763", {"start": v(-6096.44, 1068.22) * mm, "end": v(-6073.68, 1087.32) * mm});
            skLineSegment(sketch, "E2764", {"start": v(-6073.68, 1087.32) * mm, "end": v(-6051.32, 1107.03) * mm});
            skLineSegment(sketch, "E2765", {"start": v(-6293.74, 935.53) * mm, "end": v(-6267.94, 950.16) * mm});
            skLineSegment(sketch, "E2766", {"start": v(-6267.94, 950.16) * mm, "end": v(-6242.13, 965.2) * mm});
            skLineSegment(sketch, "E2767", {"start": v(-6242.13, 965.2) * mm, "end": v(-6216.93, 981.05) * mm});
            skLineSegment(sketch, "E2768", {"start": v(-6216.93, 981.05) * mm, "end": v(-6192.14, 997.3) * mm});
            skLineSegment(sketch, "E2769", {"start": v(-6192.14, 997.3) * mm, "end": v(-6194.99, 946.7) * mm});
            skLineSegment(sketch, "E2770", {"start": v(-6194.99, 946.7) * mm, "end": v(-6200.07, 895.7) * mm});
            skLineSegment(sketch, "E2771", {"start": v(-6200.07, 895.7) * mm, "end": v(-6206.98, 844.5) * mm});
            skLineSegment(sketch, "E2772", {"start": v(-6206.98, 844.5) * mm, "end": v(-6298.21, 1003) * mm});
            skLineSegment(sketch, "E2773", {"start": v(-6473.98, 822.35) * mm, "end": v(-6503.04, 812.6) * mm});
            skLineSegment(sketch, "E2774", {"start": v(-6503.04, 812.6) * mm, "end": v(-6532.1, 803.66) * mm});
            skLineSegment(sketch, "E2775", {"start": v(-6532.1, 803.66) * mm, "end": v(-6561.36, 795.32) * mm});
            skLineSegment(sketch, "E2776", {"start": v(-6561.36, 795.32) * mm, "end": v(-6583.5, 757.94) * mm});
            skLineSegment(sketch, "E2777", {"start": v(-6583.5, 757.94) * mm, "end": v(-6576.2, 728.47) * mm});
            skLineSegment(sketch, "E2778", {"start": v(-6576.2, 728.47) * mm, "end": v(-6537.38, 707.14) * mm});
            skLineSegment(sketch, "E2779", {"start": v(-6537.38, 707.14) * mm, "end": v(-6506.09, 716.08) * mm});
            skLineSegment(sketch, "E2780", {"start": v(-6506.09, 716.08) * mm, "end": v(-6474.8, 725.63) * mm});
            skLineSegment(sketch, "E2781", {"start": v(-6474.8, 725.63) * mm, "end": v(-6443.9, 736) * mm});
            skLineSegment(sketch, "E2782", {"start": v(-6443.9, 736) * mm, "end": v(-6504.26, 908.71) * mm});
            skLineSegment(sketch, "E2783", {"start": v(-6668.24, 864) * mm, "end": v(-6656.25, 804.27) * mm});
            skLineSegment(sketch, "E2784", {"start": v(-6656.25, 804.27) * mm, "end": v(-6675.15, 738.84) * mm});
            skLineSegment(sketch, "E2785", {"start": v(-6675.15, 738.84) * mm, "end": v(-6696.9, 673.4) * mm});
            skLineSegment(sketch, "E2786", {"start": v(-6696.9, 673.4) * mm, "end": v(-6736.72, 729.49) * mm});
            skLineSegment(sketch, "E2787", {"start": v(-6736.72, 729.49) * mm, "end": v(-6774.1, 786.59) * mm});
            skLineSegment(sketch, "E2788", {"start": v(-6774.1, 786.59) * mm, "end": v(-6780.2, 847.14) * mm});
            skLineSegment(sketch, "E2789", {"start": v(-6656.25, 804.27) * mm, "end": v(-6685.51, 798.78) * mm});
            skLineSegment(sketch, "E2790", {"start": v(-6685.51, 798.78) * mm, "end": v(-6714.98, 794.1) * mm});
            skLineSegment(sketch, "E2791", {"start": v(-6714.98, 794.1) * mm, "end": v(-6744.44, 789.84) * mm});
            skLineSegment(sketch, "E2792", {"start": v(-6744.44, 789.84) * mm, "end": v(-6774.1, 786.59) * mm});
            skLineSegment(sketch, "E2793", {"start": v(-6954.55, 719.73) * mm, "end": v(-6923.46, 718.92) * mm});
            skLineSegment(sketch, "E2794", {"start": v(-6923.46, 718.92) * mm, "end": v(-6892.37, 718.92) * mm});
            skLineSegment(sketch, "E2795", {"start": v(-6892.37, 718.92) * mm, "end": v(-6861.08, 719.53) * mm});
            skLineSegment(sketch, "E2796", {"start": v(-6861.08, 719.53) * mm, "end": v(-6829.99, 720.95) * mm});
            skLineSegment(sketch, "E2797", {"start": v(-6952.31, 780.7) * mm, "end": v(-6922.65, 779.88) * mm});
            skLineSegment(sketch, "E2798", {"start": v(-6922.65, 779.88) * mm, "end": v(-6892.78, 779.88) * mm});
            skLineSegment(sketch, "E2799", {"start": v(-6892.78, 779.88) * mm, "end": v(-6863.1, 780.5) * mm});
            skLineSegment(sketch, "E2800", {"start": v(-6863.1, 780.5) * mm, "end": v(-6833.44, 781.71) * mm});
            skLineSegment(sketch, "E2801", {"start": v(-7119.14, 859.74) * mm, "end": v(-7091.1, 855.07) * mm});
            skLineSegment(sketch, "E2802", {"start": v(-7091.1, 855.07) * mm, "end": v(-7063.06, 851) * mm});
            skLineSegment(sketch, "E2803", {"start": v(-7063.06, 851) * mm, "end": v(-7035.02, 847.75) * mm});
            skLineSegment(sketch, "E2804", {"start": v(-7035.02, 847.75) * mm, "end": v(-7006.77, 844.9) * mm});
            skLineSegment(sketch, "E2805", {"start": v(-7006.77, 844.9) * mm, "end": v(-7011.85, 784.15) * mm});
            skLineSegment(sketch, "E2806", {"start": v(-7011.85, 784.15) * mm, "end": v(-7044.77, 756.72) * mm});
            skLineSegment(sketch, "E2807", {"start": v(-7044.77, 756.72) * mm, "end": v(-7075.05, 760.37) * mm});
            skLineSegment(sketch, "E2808", {"start": v(-7075.05, 760.37) * mm, "end": v(-7105.12, 764.64) * mm});
            skLineSegment(sketch, "E2809", {"start": v(-7105.12, 764.64) * mm, "end": v(-7140.48, 739.65) * mm});
            skLineSegment(sketch, "E2810", {"start": v(-7140.48, 739.65) * mm, "end": v(-7145.96, 709.57) * mm});
            skLineSegment(sketch, "E2811", {"start": v(-7145.96, 709.57) * mm, "end": v(-7119.14, 674.22) * mm});
            skLineSegment(sketch, "E2812", {"start": v(-7119.14, 674.22) * mm, "end": v(-7086.83, 669.75) * mm});
            skLineSegment(sketch, "E2813", {"start": v(-7086.83, 669.75) * mm, "end": v(-7054.52, 665.89) * mm});
            skLineSegment(sketch, "E2814", {"start": v(-7054.52, 665.89) * mm, "end": v(-7019.37, 693.12) * mm});
            skFitSpline(sketch, "E2815", {"points": [v(-5000.17, 2057.4) * mm, v(-5000.17, 1005.3) * mm, v(-5853.07, 152.4) * mm, v(-6905.17, 152.4) * mm]});
            skFitSpline(sketch, "E2816", {"points": [v(-6905.17, 152.4) * mm, v(-7957.27, 152.4) * mm, v(-8810.17, 1005.3) * mm, v(-8810.17, 2057.4) * mm]});
            skFitSpline(sketch, "E2817", {"points": [v(-8810.17, 2057.4) * mm, v(-8810.17, 3109.5) * mm, v(-7957.27, 3962.4) * mm, v(-6905.17, 3962.4) * mm]});
            skFitSpline(sketch, "E2818", {"points": [v(-6905.17, 3962.4) * mm, v(-5853.07, 3962.4) * mm, v(-5000.17, 3109.5) * mm, v(-5000.17, 2057.4) * mm]});
            skLineSegment(sketch, "E2819", {"start": v(-7283.94, 901.2) * mm, "end": v(-7256.91, 892.66) * mm});
            skLineSegment(sketch, "E2820", {"start": v(-7256.91, 892.66) * mm, "end": v(-7229.68, 884.73) * mm});
            skLineSegment(sketch, "E2821", {"start": v(-7229.68, 884.73) * mm, "end": v(-7202.25, 877.62) * mm});
            skLineSegment(sketch, "E2822", {"start": v(-7202.25, 877.62) * mm, "end": v(-7174.61, 870.92) * mm});
            skLineSegment(sketch, "E2823", {"start": v(-7174.61, 870.92) * mm, "end": v(-7188.23, 811.58) * mm});
            skLineSegment(sketch, "E2824", {"start": v(-7188.23, 811.58) * mm, "end": v(-7224.6, 788.82) * mm});
            skLineSegment(sketch, "E2825", {"start": v(-7224.6, 788.82) * mm, "end": v(-7254.07, 796.75) * mm});
            skLineSegment(sketch, "E2826", {"start": v(-7254.07, 796.75) * mm, "end": v(-7283.33, 805.08) * mm});
            skLineSegment(sketch, "E2827", {"start": v(-7283.33, 805.08) * mm, "end": v(-7321.93, 785.37) * mm});
            skLineSegment(sketch, "E2828", {"start": v(-7321.93, 785.37) * mm, "end": v(-7331.48, 756.31) * mm});
            skLineSegment(sketch, "E2829", {"start": v(-7331.48, 756.31) * mm, "end": v(-7309.74, 717.7) * mm});
            skLineSegment(sketch, "E2830", {"start": v(-7309.74, 717.7) * mm, "end": v(-7278.45, 708.56) * mm});
            skLineSegment(sketch, "E2831", {"start": v(-7278.45, 708.56) * mm, "end": v(-7246.95, 700.23) * mm});
            skLineSegment(sketch, "E2832", {"start": v(-7246.95, 700.23) * mm, "end": v(-7208.55, 722.38) * mm});
            skFitSpline(sketch, "E2833", {"points": [v(-4746.17, 2057.4) * mm, v(-4746.17, 865.02) * mm, v(-5712.79, -101.6) * mm, v(-6905.17, -101.6) * mm]});
            skFitSpline(sketch, "E2834", {"points": [v(-6905.17, -101.6) * mm, v(-8097.55, -101.6) * mm, v(-9064.17, 865.02) * mm, v(-9064.17, 2057.4) * mm]});
            skFitSpline(sketch, "E2835", {"points": [v(-9064.17, 2057.4) * mm, v(-9064.17, 3249.78) * mm, v(-8097.55, 4216.4) * mm, v(-6905.17, 4216.4) * mm]});
            skFitSpline(sketch, "E2836", {"points": [v(-6905.17, 4216.4) * mm, v(-5712.79, 4216.4) * mm, v(-4746.17, 3249.78) * mm, v(-4746.17, 2057.4) * mm]});
            skFitSpline(sketch, "E2837", {"points": [v(-5138.96, 2057.4) * mm, v(-5138.96, 1081.95) * mm, v(-5929.72, 291.19) * mm, v(-6905.17, 291.19) * mm]});
            skFitSpline(sketch, "E2838", {"points": [v(-6905.17, 291.19) * mm, v(-7880.62, 291.19) * mm, v(-8671.39, 1081.95) * mm, v(-8671.39, 2057.4) * mm]});
            skFitSpline(sketch, "E2839", {"points": [v(-8671.39, 2057.4) * mm, v(-8671.39, 3032.85) * mm, v(-7880.62, 3823.61) * mm, v(-6905.17, 3823.61) * mm]});
            skFitSpline(sketch, "E2840", {"points": [v(-6905.17, 3823.61) * mm, v(-5929.72, 3823.61) * mm, v(-5138.96, 3032.85) * mm, v(-5138.96, 2057.4) * mm]});
            skLineSegment(sketch, "E2841", {"start": v(-1190.4, 2231.75) * mm, "end": v(-1186.94, 2232.05) * mm});
            skLineSegment(sketch, "E2842", {"start": v(-1186.94, 2232.05) * mm, "end": v(-1182.4, 2232.56) * mm});
            skLineSegment(sketch, "E2843", {"start": v(-1182.4, 2232.56) * mm, "end": v(-1176.76, 2233.35) * mm});
            skLineSegment(sketch, "E2844", {"start": v(-1176.76, 2233.35) * mm, "end": v(-1170.07, 2234.47) * mm});
            skLineSegment(sketch, "E2845", {"start": v(-1170.07, 2234.47) * mm, "end": v(-1162.32, 2235.97) * mm});
            skLineSegment(sketch, "E2846", {"start": v(-1162.32, 2235.97) * mm, "end": v(-1153.54, 2237.93) * mm});
            skLineSegment(sketch, "E2847", {"start": v(-1153.54, 2237.93) * mm, "end": v(-1143.75, 2240.39) * mm});
            skLineSegment(sketch, "E2848", {"start": v(-1143.75, 2240.39) * mm, "end": v(-1132.96, 2243.4) * mm});
            skLineSegment(sketch, "E2849", {"start": v(-1132.96, 2243.4) * mm, "end": v(-1121.2, 2247.04) * mm});
            skLineSegment(sketch, "E2850", {"start": v(-1121.2, 2247.04) * mm, "end": v(-1108.5, 2251.34) * mm});
            skLineSegment(sketch, "E2851", {"start": v(-1108.5, 2251.34) * mm, "end": v(-1094.88, 2256.36) * mm});
            skLineSegment(sketch, "E2852", {"start": v(-1094.88, 2256.36) * mm, "end": v(-1080.38, 2262.15) * mm});
            skLineSegment(sketch, "E2853", {"start": v(-1080.38, 2262.15) * mm, "end": v(-1065.03, 2268.77) * mm});
            skLineSegment(sketch, "E2854", {"start": v(-1065.03, 2268.77) * mm, "end": v(-1048.85, 2276.26) * mm});
            skLineSegment(sketch, "E2855", {"start": v(-1048.85, 2276.26) * mm, "end": v(-1031.9, 2284.68) * mm});
            skLineSegment(sketch, "E2856", {"start": v(-1031.9, 2284.68) * mm, "end": v(-1014.2, 2294.06) * mm});
            skLineSegment(sketch, "E2857", {"start": v(-1014.2, 2294.06) * mm, "end": v(-995.8, 2304.46) * mm});
            skLineSegment(sketch, "E2858", {"start": v(-995.8, 2304.46) * mm, "end": v(-976.74, 2315.91) * mm});
            skLineSegment(sketch, "E2859", {"start": v(-976.74, 2315.91) * mm, "end": v(-957.06, 2328.47) * mm});
            skLineSegment(sketch, "E2860", {"start": v(-957.06, 2328.47) * mm, "end": v(-936.82, 2342.17) * mm});
            skLineSegment(sketch, "E2861", {"start": v(-936.82, 2342.17) * mm, "end": v(-916.05, 2357.05) * mm});
            skLineSegment(sketch, "E2862", {"start": v(-916.05, 2357.05) * mm, "end": v(-894.8, 2373.15) * mm});
            skLineSegment(sketch, "E2863", {"start": v(-894.8, 2373.15) * mm, "end": v(-873.14, 2390.5) * mm});
            skLineSegment(sketch, "E2864", {"start": v(-873.14, 2390.5) * mm, "end": v(-851.11, 2409.14) * mm});
            skLineSegment(sketch, "E2865", {"start": v(-851.11, 2409.14) * mm, "end": v(-830.3, 2428.94) * mm});
            skLineSegment(sketch, "E2866", {"start": v(-830.3, 2428.94) * mm, "end": v(-849.17, 2563.34) * mm});
            skLineSegment(sketch, "E2867", {"start": v(-849.17, 2563.34) * mm, "end": v(-874.62, 2576.66) * mm});
            skLineSegment(sketch, "E2868", {"start": v(-874.62, 2576.66) * mm, "end": v(-900.93, 2588.51) * mm});
            skLineSegment(sketch, "E2869", {"start": v(-900.93, 2588.51) * mm, "end": v(-926.54, 2599.23) * mm});
            skLineSegment(sketch, "E2870", {"start": v(-926.54, 2599.23) * mm, "end": v(-951.39, 2608.86) * mm});
            skLineSegment(sketch, "E2871", {"start": v(-951.39, 2608.86) * mm, "end": v(-975.45, 2617.45) * mm});
            skLineSegment(sketch, "E2872", {"start": v(-975.45, 2617.45) * mm, "end": v(-998.68, 2625.05) * mm});
            skLineSegment(sketch, "E2873", {"start": v(-998.68, 2625.05) * mm, "end": v(-1021.06, 2631.7) * mm});
            skLineSegment(sketch, "E2874", {"start": v(-1021.06, 2631.7) * mm, "end": v(-1042.53, 2637.47) * mm});
            skLineSegment(sketch, "E2875", {"start": v(-1042.53, 2637.47) * mm, "end": v(-1063.09, 2642.4) * mm});
            skLineSegment(sketch, "E2876", {"start": v(-1063.09, 2642.4) * mm, "end": v(-1082.68, 2646.55) * mm});
            skLineSegment(sketch, "E2877", {"start": v(-1082.68, 2646.55) * mm, "end": v(-1101.3, 2649.97) * mm});
            skLineSegment(sketch, "E2878", {"start": v(-1101.3, 2649.97) * mm, "end": v(-1118.9, 2652.73) * mm});
            skLineSegment(sketch, "E2879", {"start": v(-1118.9, 2652.73) * mm, "end": v(-1135.5, 2654.86) * mm});
            skLineSegment(sketch, "E2880", {"start": v(-1135.5, 2654.86) * mm, "end": v(-1151.03, 2656.44) * mm});
            skLineSegment(sketch, "E2881", {"start": v(-1151.03, 2656.44) * mm, "end": v(-1165.5, 2657.52) * mm});
            skLineSegment(sketch, "E2882", {"start": v(-1165.5, 2657.52) * mm, "end": v(-1178.9, 2658.16) * mm});
            skLineSegment(sketch, "E2883", {"start": v(-1178.9, 2658.16) * mm, "end": v(-1191.2, 2658.41) * mm});
            skLineSegment(sketch, "E2884", {"start": v(-1191.2, 2658.41) * mm, "end": v(-1202.4, 2658.34) * mm});
            skLineSegment(sketch, "E2885", {"start": v(-1202.4, 2658.34) * mm, "end": v(-1212.5, 2658.01) * mm});
            skLineSegment(sketch, "E2886", {"start": v(-1212.5, 2658.01) * mm, "end": v(-1221.47, 2657.47) * mm});
            skLineSegment(sketch, "E2887", {"start": v(-1221.47, 2657.47) * mm, "end": v(-1229.33, 2656.8) * mm});
            skLineSegment(sketch, "E2888", {"start": v(-1229.33, 2656.8) * mm, "end": v(-1236.08, 2656.02) * mm});
            skLineSegment(sketch, "E2889", {"start": v(-1236.08, 2656.02) * mm, "end": v(-1241.7, 2655.23) * mm});
            skLineSegment(sketch, "E2890", {"start": v(-1241.7, 2655.23) * mm, "end": v(-1246.22, 2654.47) * mm});
            skLineSegment(sketch, "E2891", {"start": v(-1246.22, 2654.47) * mm, "end": v(-1249.63, 2653.8) * mm});
            skLineSegment(sketch, "E2892", {"start": v(-1249.63, 2653.8) * mm, "end": v(-1251.95, 2653.28) * mm});
            skLineSegment(sketch, "E2893", {"start": v(-1251.95, 2653.28) * mm, "end": v(-1253.18, 2652.97) * mm});
            skLineSegment(sketch, "E2894", {"start": v(-1253.18, 2652.97) * mm, "end": v(-1418.65, 2605.6) * mm});
            skLineSegment(sketch, "E2895", {"start": v(-1418.65, 2605.6) * mm, "end": v(-1521.81, 2863.08) * mm});
            skLineSegment(sketch, "E2896", {"start": v(-1521.81, 2863.08) * mm, "end": v(-1369.41, 2943.07) * mm});
            skLineSegment(sketch, "E2897", {"start": v(-1369.41, 2943.07) * mm, "end": v(-1368.3, 2943.7) * mm});
            skLineSegment(sketch, "E2898", {"start": v(-1368.3, 2943.7) * mm, "end": v(-1366.28, 2944.92) * mm});
            skLineSegment(sketch, "E2899", {"start": v(-1366.28, 2944.92) * mm, "end": v(-1363.35, 2946.8) * mm});
            skLineSegment(sketch, "E2900", {"start": v(-1363.35, 2946.8) * mm, "end": v(-1359.55, 2949.36) * mm});
            skLineSegment(sketch, "E2901", {"start": v(-1359.55, 2949.36) * mm, "end": v(-1354.94, 2952.67) * mm});
            skLineSegment(sketch, "E2902", {"start": v(-1354.94, 2952.67) * mm, "end": v(-1349.53, 2956.78) * mm});
            skLineSegment(sketch, "E2903", {"start": v(-1349.53, 2956.78) * mm, "end": v(-1343.37, 2961.7) * mm});
            skLineSegment(sketch, "E2904", {"start": v(-1343.37, 2961.7) * mm, "end": v(-1336.5, 2967.52) * mm});
            skLineSegment(sketch, "E2905", {"start": v(-1336.5, 2967.52) * mm, "end": v(-1328.98, 2974.25) * mm});
            skLineSegment(sketch, "E2906", {"start": v(-1328.98, 2974.25) * mm, "end": v(-1320.82, 2981.94) * mm});
            skLineSegment(sketch, "E2907", {"start": v(-1320.82, 2981.94) * mm, "end": v(-1312.1, 2990.61) * mm});
            skLineSegment(sketch, "E2908", {"start": v(-1312.1, 2990.61) * mm, "end": v(-1302.85, 3000.33) * mm});
            skLineSegment(sketch, "E2909", {"start": v(-1302.85, 3000.33) * mm, "end": v(-1293.13, 3011.1) * mm});
            skLineSegment(sketch, "E2910", {"start": v(-1293.13, 3011.1) * mm, "end": v(-1282.98, 3022.97) * mm});
            skLineSegment(sketch, "E2911", {"start": v(-1282.98, 3022.97) * mm, "end": v(-1272.46, 3035.96) * mm});
            skLineSegment(sketch, "E2912", {"start": v(-1272.46, 3035.96) * mm, "end": v(-1261.62, 3050.11) * mm});
            skLineSegment(sketch, "E2913", {"start": v(-1261.62, 3050.11) * mm, "end": v(-1250.52, 3065.44) * mm});
            skLineSegment(sketch, "E2914", {"start": v(-1250.52, 3065.44) * mm, "end": v(-1239.2, 3081.98) * mm});
            skLineSegment(sketch, "E2915", {"start": v(-1239.2, 3081.98) * mm, "end": v(-1227.75, 3099.73) * mm});
            skLineSegment(sketch, "E2916", {"start": v(-1227.75, 3099.73) * mm, "end": v(-1216.2, 3118.73) * mm});
            skLineSegment(sketch, "E2917", {"start": v(-1216.2, 3118.73) * mm, "end": v(-1204.6, 3139) * mm});
            skLineSegment(sketch, "E2918", {"start": v(-1204.6, 3139) * mm, "end": v(-1193.05, 3160.53) * mm});
            skLineSegment(sketch, "E2919", {"start": v(-1193.05, 3160.53) * mm, "end": v(-1181.57, 3183.36) * mm});
            skLineSegment(sketch, "E2920", {"start": v(-1181.57, 3183.36) * mm, "end": v(-1170.25, 3207.5) * mm});
            skLineSegment(sketch, "E2921", {"start": v(-1170.25, 3207.5) * mm, "end": v(-1159.13, 3232.92) * mm});
            skLineSegment(sketch, "E2922", {"start": v(-1159.13, 3232.92) * mm, "end": v(-1148.28, 3259.67) * mm});
            skLineSegment(sketch, "E2923", {"start": v(-1148.28, 3259.67) * mm, "end": v(-1139.06, 3286.87) * mm});
            skLineSegment(sketch, "E2924", {"start": v(-1139.06, 3286.87) * mm, "end": v(-1218.23, 3397.11) * mm});
            skLineSegment(sketch, "E2925", {"start": v(-1218.23, 3397.11) * mm, "end": v(-1246.95, 3397.07) * mm});
            skLineSegment(sketch, "E2926", {"start": v(-1246.95, 3397.07) * mm, "end": v(-1275.75, 3395.34) * mm});
            skLineSegment(sketch, "E2927", {"start": v(-1275.75, 3395.34) * mm, "end": v(-1303.4, 3392.93) * mm});
            skLineSegment(sketch, "E2928", {"start": v(-1303.4, 3392.93) * mm, "end": v(-1329.89, 3389.91) * mm});
            skLineSegment(sketch, "E2929", {"start": v(-1329.89, 3389.91) * mm, "end": v(-1355.18, 3386.34) * mm});
            skLineSegment(sketch, "E2930", {"start": v(-1355.18, 3386.34) * mm, "end": v(-1379.29, 3382.26) * mm});
            skLineSegment(sketch, "E2931", {"start": v(-1379.29, 3382.26) * mm, "end": v(-1402.2, 3377.76) * mm});
            skLineSegment(sketch, "E2932", {"start": v(-1402.2, 3377.76) * mm, "end": v(-1423.89, 3372.89) * mm});
            skLineSegment(sketch, "E2933", {"start": v(-1423.89, 3372.89) * mm, "end": v(-1444.38, 3367.7) * mm});
            skLineSegment(sketch, "E2934", {"start": v(-1444.38, 3367.7) * mm, "end": v(-1463.66, 3362.27) * mm});
            skLineSegment(sketch, "E2935", {"start": v(-1463.66, 3362.27) * mm, "end": v(-1481.73, 3356.65) * mm});
            skLineSegment(sketch, "E2936", {"start": v(-1481.73, 3356.65) * mm, "end": v(-1498.6, 3350.9) * mm});
            skLineSegment(sketch, "E2937", {"start": v(-1498.6, 3350.9) * mm, "end": v(-1514.28, 3345.08) * mm});
            skLineSegment(sketch, "E2938", {"start": v(-1514.28, 3345.08) * mm, "end": v(-1528.77, 3339.26) * mm});
            skLineSegment(sketch, "E2939", {"start": v(-1528.77, 3339.26) * mm, "end": v(-1542.09, 3333.5) * mm});
            skLineSegment(sketch, "E2940", {"start": v(-1542.09, 3333.5) * mm, "end": v(-1554.24, 3327.83) * mm});
            skLineSegment(sketch, "E2941", {"start": v(-1554.24, 3327.83) * mm, "end": v(-1565.25, 3322.34) * mm});
            skLineSegment(sketch, "E2942", {"start": v(-1565.25, 3322.34) * mm, "end": v(-1575.14, 3317.07) * mm});
            skLineSegment(sketch, "E2943", {"start": v(-1575.14, 3317.07) * mm, "end": v(-1583.92, 3312.09) * mm});
            skLineSegment(sketch, "E2944", {"start": v(-1583.92, 3312.09) * mm, "end": v(-1591.63, 3307.44) * mm});
            skLineSegment(sketch, "E2945", {"start": v(-1591.63, 3307.44) * mm, "end": v(-1598.27, 3303.18) * mm});
            skLineSegment(sketch, "E2946", {"start": v(-1598.27, 3303.18) * mm, "end": v(-1603.88, 3299.37) * mm});
            skLineSegment(sketch, "E2947", {"start": v(-1603.88, 3299.37) * mm, "end": v(-1608.5, 3296.05) * mm});
            skLineSegment(sketch, "E2948", {"start": v(-1608.5, 3296.05) * mm, "end": v(-1612.14, 3293.28) * mm});
            skLineSegment(sketch, "E2949", {"start": v(-1612.14, 3293.28) * mm, "end": v(-1614.85, 3291.1) * mm});
            skLineSegment(sketch, "E2950", {"start": v(-1614.85, 3291.1) * mm, "end": v(-1616.66, 3289.57) * mm});
            skLineSegment(sketch, "E2951", {"start": v(-1616.66, 3289.57) * mm, "end": v(-1617.61, 3288.72) * mm});
            skLineSegment(sketch, "E2952", {"start": v(-1617.61, 3288.72) * mm, "end": v(-1742.1, 3169.88) * mm});
            skLineSegment(sketch, "E2953", {"start": v(-1742.1, 3169.88) * mm, "end": v(-1953.11, 3349.92) * mm});
            skLineSegment(sketch, "E2954", {"start": v(-1953.11, 3349.92) * mm, "end": v(-1855.34, 3491.57) * mm});
            skLineSegment(sketch, "E2955", {"start": v(-1855.34, 3491.57) * mm, "end": v(-1854.66, 3492.64) * mm});
            skLineSegment(sketch, "E2956", {"start": v(-1854.66, 3492.64) * mm, "end": v(-1853.43, 3494.67) * mm});
            skLineSegment(sketch, "E2957", {"start": v(-1853.43, 3494.67) * mm, "end": v(-1851.7, 3497.69) * mm});
            skLineSegment(sketch, "E2958", {"start": v(-1851.7, 3497.69) * mm, "end": v(-1849.54, 3501.72) * mm});
            skLineSegment(sketch, "E2959", {"start": v(-1849.54, 3501.72) * mm, "end": v(-1846.99, 3506.8) * mm});
            skLineSegment(sketch, "E2960", {"start": v(-1846.99, 3506.8) * mm, "end": v(-1844.1, 3512.95) * mm});
            skLineSegment(sketch, "E2961", {"start": v(-1844.1, 3512.95) * mm, "end": v(-1840.95, 3520.18) * mm});
            skLineSegment(sketch, "E2962", {"start": v(-1840.95, 3520.18) * mm, "end": v(-1837.57, 3528.52) * mm});
            skLineSegment(sketch, "E2963", {"start": v(-1837.57, 3528.52) * mm, "end": v(-1834.03, 3537.97) * mm});
            skLineSegment(sketch, "E2964", {"start": v(-1834.03, 3537.97) * mm, "end": v(-1830.38, 3548.57) * mm});
            skLineSegment(sketch, "E2965", {"start": v(-1830.38, 3548.57) * mm, "end": v(-1826.7, 3560.3) * mm});
            skLineSegment(sketch, "E2966", {"start": v(-1826.7, 3560.3) * mm, "end": v(-1823.02, 3573.2) * mm});
            skLineSegment(sketch, "E2967", {"start": v(-1823.02, 3573.2) * mm, "end": v(-1819.41, 3587.26) * mm});
            skLineSegment(sketch, "E2968", {"start": v(-1819.41, 3587.26) * mm, "end": v(-1815.94, 3602.48) * mm});
            skLineSegment(sketch, "E2969", {"start": v(-1815.94, 3602.48) * mm, "end": v(-1812.67, 3618.88) * mm});
            skLineSegment(sketch, "E2970", {"start": v(-1812.67, 3618.88) * mm, "end": v(-1809.64, 3636.45) * mm});
            skLineSegment(sketch, "E2971", {"start": v(-1809.64, 3636.45) * mm, "end": v(-1806.94, 3655.18) * mm});
            skLineSegment(sketch, "E2972", {"start": v(-1806.94, 3655.18) * mm, "end": v(-1804.6, 3675.07) * mm});
            skLineSegment(sketch, "E2973", {"start": v(-1804.6, 3675.07) * mm, "end": v(-1802.7, 3696.12) * mm});
            skLineSegment(sketch, "E2974", {"start": v(-1802.7, 3696.12) * mm, "end": v(-1801.3, 3718.32) * mm});
            skLineSegment(sketch, "E2975", {"start": v(-1801.3, 3718.32) * mm, "end": v(-1800.47, 3741.64) * mm});
            skLineSegment(sketch, "E2976", {"start": v(-1800.47, 3741.64) * mm, "end": v(-1800.24, 3766.09) * mm});
            skLineSegment(sketch, "E2977", {"start": v(-1800.24, 3766.09) * mm, "end": v(-1800.69, 3791.64) * mm});
            skLineSegment(sketch, "E2978", {"start": v(-1800.69, 3791.64) * mm, "end": v(-1801.87, 3818.26) * mm});
            skLineSegment(sketch, "E2979", {"start": v(-1801.87, 3818.26) * mm, "end": v(-1803.85, 3845.95) * mm});
            skLineSegment(sketch, "E2980", {"start": v(-1803.85, 3845.95) * mm, "end": v(-1806.67, 3874.67) * mm});
            skLineSegment(sketch, "E2981", {"start": v(-1806.67, 3874.67) * mm, "end": v(-1811.15, 3903.04) * mm});
            skLineSegment(sketch, "E2982", {"start": v(-1811.15, 3903.04) * mm, "end": v(-1932.48, 3963.87) * mm});
            skLineSegment(sketch, "E2983", {"start": v(-1932.48, 3963.87) * mm, "end": v(-1957.89, 3950.48) * mm});
            skLineSegment(sketch, "E2984", {"start": v(-1957.89, 3950.48) * mm, "end": v(-1982.6, 3935.56) * mm});
            skLineSegment(sketch, "E2985", {"start": v(-1982.6, 3935.56) * mm, "end": v(-2005.96, 3920.58) * mm});
            skLineSegment(sketch, "E2986", {"start": v(-2005.96, 3920.58) * mm, "end": v(-2028, 3905.6) * mm});
            skLineSegment(sketch, "E2987", {"start": v(-2028, 3905.6) * mm, "end": v(-2048.74, 3890.68) * mm});
            skLineSegment(sketch, "E2988", {"start": v(-2048.74, 3890.68) * mm, "end": v(-2068.2, 3875.87) * mm});
            skLineSegment(sketch, "E2989", {"start": v(-2068.2, 3875.87) * mm, "end": v(-2086.38, 3861.24) * mm});
            skLineSegment(sketch, "E2990", {"start": v(-2086.38, 3861.24) * mm, "end": v(-2103.33, 3846.84) * mm});
            skLineSegment(sketch, "E2991", {"start": v(-2103.33, 3846.84) * mm, "end": v(-2119.06, 3832.73) * mm});
            skLineSegment(sketch, "E2992", {"start": v(-2119.06, 3832.73) * mm, "end": v(-2133.6, 3818.96) * mm});
            skLineSegment(sketch, "E2993", {"start": v(-2133.6, 3818.96) * mm, "end": v(-2147, 3805.58) * mm});
            skLineSegment(sketch, "E2994", {"start": v(-2147, 3805.58) * mm, "end": v(-2159.26, 3792.65) * mm});
            skLineSegment(sketch, "E2995", {"start": v(-2159.26, 3792.65) * mm, "end": v(-2170.44, 3780.21) * mm});
            skLineSegment(sketch, "E2996", {"start": v(-2170.44, 3780.21) * mm, "end": v(-2180.57, 3768.32) * mm});
            skLineSegment(sketch, "E2997", {"start": v(-2180.57, 3768.32) * mm, "end": v(-2189.68, 3757.03) * mm});
            skLineSegment(sketch, "E2998", {"start": v(-2189.68, 3757.03) * mm, "end": v(-2197.8, 3746.36) * mm});
            skLineSegment(sketch, "E2999", {"start": v(-2197.8, 3746.36) * mm, "end": v(-2205, 3736.39) * mm});
            skLineSegment(sketch, "E3000", {"start": v(-2205, 3736.39) * mm, "end": v(-2211.32, 3727.13) * mm});
            skLineSegment(sketch, "E3001", {"start": v(-2211.32, 3727.13) * mm, "end": v(-2216.78, 3718.63) * mm});
            skLineSegment(sketch, "E3002", {"start": v(-2216.78, 3718.63) * mm, "end": v(-2221.43, 3710.94) * mm});
            skLineSegment(sketch, "E3003", {"start": v(-2221.43, 3710.94) * mm, "end": v(-2225.34, 3704.08) * mm});
            skLineSegment(sketch, "E3004", {"start": v(-2225.34, 3704.08) * mm, "end": v(-2228.54, 3698.1) * mm});
            skLineSegment(sketch, "E3005", {"start": v(-2228.54, 3698.1) * mm, "end": v(-2231.08, 3693.01) * mm});
            skLineSegment(sketch, "E3006", {"start": v(-2231.08, 3693.01) * mm, "end": v(-2233.02, 3688.86) * mm});
            skLineSegment(sketch, "E3007", {"start": v(-2233.02, 3688.86) * mm, "end": v(-2234.4, 3685.67) * mm});
            skLineSegment(sketch, "E3008", {"start": v(-2234.4, 3685.67) * mm, "end": v(-2235.3, 3683.48) * mm});
            skLineSegment(sketch, "E3009", {"start": v(-2235.3, 3683.48) * mm, "end": v(-2235.74, 3682.29) * mm});
            skLineSegment(sketch, "E3010", {"start": v(-2235.74, 3682.29) * mm, "end": v(-2290.75, 3519.2) * mm});
            skLineSegment(sketch, "E3011", {"start": v(-2290.75, 3519.2) * mm, "end": v(-2561.26, 3580.56) * mm});
            skLineSegment(sketch, "E3012", {"start": v(-2561.26, 3580.56) * mm, "end": v(-2540.52, 3751.42) * mm});
            skLineSegment(sketch, "E3013", {"start": v(-2540.52, 3751.42) * mm, "end": v(-2540.4, 3752.69) * mm});
            skLineSegment(sketch, "E3014", {"start": v(-2540.4, 3752.69) * mm, "end": v(-2540.26, 3755.06) * mm});
            skLineSegment(sketch, "E3015", {"start": v(-2540.26, 3755.06) * mm, "end": v(-2540.13, 3758.53) * mm});
            skLineSegment(sketch, "E3016", {"start": v(-2540.13, 3758.53) * mm, "end": v(-2540.1, 3763.11) * mm});
            skLineSegment(sketch, "E3017", {"start": v(-2540.1, 3763.11) * mm, "end": v(-2540.2, 3768.8) * mm});
            skLineSegment(sketch, "E3018", {"start": v(-2540.2, 3768.8) * mm, "end": v(-2540.5, 3775.57) * mm});
            skLineSegment(sketch, "E3019", {"start": v(-2540.5, 3775.57) * mm, "end": v(-2541.06, 3783.44) * mm});
            skLineSegment(sketch, "E3020", {"start": v(-2541.06, 3783.44) * mm, "end": v(-2541.95, 3792.4) * mm});
            skLineSegment(sketch, "E3021", {"start": v(-2541.95, 3792.4) * mm, "end": v(-2543.2, 3802.42) * mm});
            skLineSegment(sketch, "E3022", {"start": v(-2543.2, 3802.42) * mm, "end": v(-2544.9, 3813.49) * mm});
            skLineSegment(sketch, "E3023", {"start": v(-2544.9, 3813.49) * mm, "end": v(-2547.09, 3825.6) * mm});
            skLineSegment(sketch, "E3024", {"start": v(-2547.09, 3825.6) * mm, "end": v(-2549.83, 3838.72) * mm});
            skLineSegment(sketch, "E3025", {"start": v(-2549.83, 3838.72) * mm, "end": v(-2553.17, 3852.85) * mm});
            skLineSegment(sketch, "E3026", {"start": v(-2553.17, 3852.85) * mm, "end": v(-2557.17, 3867.94) * mm});
            skLineSegment(sketch, "E3027", {"start": v(-2557.17, 3867.94) * mm, "end": v(-2561.9, 3883.98) * mm});
            skLineSegment(sketch, "E3028", {"start": v(-2561.9, 3883.98) * mm, "end": v(-2567.38, 3900.94) * mm});
            skLineSegment(sketch, "E3029", {"start": v(-2567.38, 3900.94) * mm, "end": v(-2573.69, 3918.78) * mm});
            skLineSegment(sketch, "E3030", {"start": v(-2573.69, 3918.78) * mm, "end": v(-2580.87, 3937.48) * mm});
            skLineSegment(sketch, "E3031", {"start": v(-2580.87, 3937.48) * mm, "end": v(-2588.97, 3957) * mm});
            skLineSegment(sketch, "E3032", {"start": v(-2588.97, 3957) * mm, "end": v(-2598.04, 3977.3) * mm});
            skLineSegment(sketch, "E3033", {"start": v(-2598.04, 3977.3) * mm, "end": v(-2608.14, 3998.35) * mm});
            skLineSegment(sketch, "E3034", {"start": v(-2608.14, 3998.35) * mm, "end": v(-2619.3, 4020.1) * mm});
            skLineSegment(sketch, "E3035", {"start": v(-2619.3, 4020.1) * mm, "end": v(-2631.57, 4042.51) * mm});
            skLineSegment(sketch, "E3036", {"start": v(-2631.57, 4042.51) * mm, "end": v(-2644.99, 4065.54) * mm});
            skLineSegment(sketch, "E3037", {"start": v(-2644.99, 4065.54) * mm, "end": v(-2659.6, 4089.14) * mm});
            skLineSegment(sketch, "E3038", {"start": v(-2659.6, 4089.14) * mm, "end": v(-2675.45, 4113.26) * mm});
            skLineSegment(sketch, "E3039", {"start": v(-2675.45, 4113.26) * mm, "end": v(-2692.6, 4136.3) * mm});
            skLineSegment(sketch, "E3040", {"start": v(-2692.6, 4136.3) * mm, "end": v(-2828.3, 4133.77) * mm});
            skLineSegment(sketch, "E3041", {"start": v(-2828.3, 4133.77) * mm, "end": v(-2844.58, 4110.11) * mm});
            skLineSegment(sketch, "E3042", {"start": v(-2844.58, 4110.11) * mm, "end": v(-2859.52, 4085.42) * mm});
            skLineSegment(sketch, "E3043", {"start": v(-2859.52, 4085.42) * mm, "end": v(-2873.25, 4061.3) * mm});
            skLineSegment(sketch, "E3044", {"start": v(-2873.25, 4061.3) * mm, "end": v(-2885.8, 4037.79) * mm});
            skLineSegment(sketch, "E3045", {"start": v(-2885.8, 4037.79) * mm, "end": v(-2897.23, 4014.94) * mm});
            skLineSegment(sketch, "E3046", {"start": v(-2897.23, 4014.94) * mm, "end": v(-2907.58, 3992.79) * mm});
            skLineSegment(sketch, "E3047", {"start": v(-2907.58, 3992.79) * mm, "end": v(-2916.88, 3971.38) * mm});
            skLineSegment(sketch, "E3048", {"start": v(-2916.88, 3971.38) * mm, "end": v(-2925.2, 3950.75) * mm});
            skLineSegment(sketch, "E3049", {"start": v(-2925.2, 3950.75) * mm, "end": v(-2932.56, 3930.95) * mm});
            skLineSegment(sketch, "E3050", {"start": v(-2932.56, 3930.95) * mm, "end": v(-2939.05, 3912) * mm});
            skLineSegment(sketch, "E3051", {"start": v(-2939.05, 3912) * mm, "end": v(-2944.69, 3893.92) * mm});
            skLineSegment(sketch, "E3052", {"start": v(-2944.69, 3893.92) * mm, "end": v(-2949.54, 3876.77) * mm});
            skLineSegment(sketch, "E3053", {"start": v(-2949.54, 3876.77) * mm, "end": v(-2953.66, 3860.57) * mm});
            skLineSegment(sketch, "E3054", {"start": v(-2953.66, 3860.57) * mm, "end": v(-2957.1, 3845.33) * mm});
            skLineSegment(sketch, "E3055", {"start": v(-2957.1, 3845.33) * mm, "end": v(-2959.92, 3831.1) * mm});
            skLineSegment(sketch, "E3056", {"start": v(-2959.92, 3831.1) * mm, "end": v(-2962.16, 3817.88) * mm});
            skLineSegment(sketch, "E3057", {"start": v(-2962.16, 3817.88) * mm, "end": v(-2963.9, 3805.7) * mm});
            skLineSegment(sketch, "E3058", {"start": v(-2963.9, 3805.7) * mm, "end": v(-2965.18, 3794.57) * mm});
            skLineSegment(sketch, "E3059", {"start": v(-2965.18, 3794.57) * mm, "end": v(-2966.07, 3784.5) * mm});
            skLineSegment(sketch, "E3060", {"start": v(-2966.07, 3784.5) * mm, "end": v(-2966.62, 3775.53) * mm});
            skLineSegment(sketch, "E3061", {"start": v(-2966.62, 3775.53) * mm, "end": v(-2966.89, 3767.64) * mm});
            skLineSegment(sketch, "E3062", {"start": v(-2966.89, 3767.64) * mm, "end": v(-2966.94, 3760.86) * mm});
            skLineSegment(sketch, "E3063", {"start": v(-2966.94, 3760.86) * mm, "end": v(-2966.83, 3755.18) * mm});
            skLineSegment(sketch, "E3064", {"start": v(-2966.83, 3755.18) * mm, "end": v(-2966.62, 3750.6) * mm});
            skLineSegment(sketch, "E3065", {"start": v(-2966.62, 3750.6) * mm, "end": v(-2966.36, 3747.13) * mm});
            skLineSegment(sketch, "E3066", {"start": v(-2966.36, 3747.13) * mm, "end": v(-2966.13, 3744.77) * mm});
            skLineSegment(sketch, "E3067", {"start": v(-2966.13, 3744.77) * mm, "end": v(-2965.97, 3743.51) * mm});
            skLineSegment(sketch, "E3068", {"start": v(-2965.97, 3743.51) * mm, "end": v(-2938.9, 3573.54) * mm});
            skLineSegment(sketch, "E3069", {"start": v(-2938.9, 3573.54) * mm, "end": v(-3206.93, 3502.16) * mm});
            skLineSegment(sketch, "E3070", {"start": v(-3206.93, 3502.16) * mm, "end": v(-3267.96, 3663.1) * mm});
            skLineSegment(sketch, "E3071", {"start": v(-3267.96, 3663.1) * mm, "end": v(-3268.45, 3664.26) * mm});
            skLineSegment(sketch, "E3072", {"start": v(-3268.45, 3664.26) * mm, "end": v(-3269.42, 3666.43) * mm});
            skLineSegment(sketch, "E3073", {"start": v(-3269.42, 3666.43) * mm, "end": v(-3270.93, 3669.56) * mm});
            skLineSegment(sketch, "E3074", {"start": v(-3270.93, 3669.56) * mm, "end": v(-3273.02, 3673.64) * mm});
            skLineSegment(sketch, "E3075", {"start": v(-3273.02, 3673.64) * mm, "end": v(-3275.75, 3678.62) * mm});
            skLineSegment(sketch, "E3076", {"start": v(-3275.75, 3678.62) * mm, "end": v(-3279.17, 3684.49) * mm});
            skLineSegment(sketch, "E3077", {"start": v(-3279.17, 3684.49) * mm, "end": v(-3283.33, 3691.2) * mm});
            skLineSegment(sketch, "E3078", {"start": v(-3283.33, 3691.2) * mm, "end": v(-3288.27, 3698.7) * mm});
            skLineSegment(sketch, "E3079", {"start": v(-3288.27, 3698.7) * mm, "end": v(-3294.04, 3707) * mm});
            skLineSegment(sketch, "E3080", {"start": v(-3294.04, 3707) * mm, "end": v(-3300.69, 3716.01) * mm});
            skLineSegment(sketch, "E3081", {"start": v(-3300.69, 3716.01) * mm, "end": v(-3308.25, 3725.72) * mm});
            skLineSegment(sketch, "E3082", {"start": v(-3308.25, 3725.72) * mm, "end": v(-3316.78, 3736.07) * mm});
            skLineSegment(sketch, "E3083", {"start": v(-3316.78, 3736.07) * mm, "end": v(-3326.3, 3747.02) * mm});
            skLineSegment(sketch, "E3084", {"start": v(-3326.3, 3747.02) * mm, "end": v(-3336.86, 3758.52) * mm});
            skLineSegment(sketch, "E3085", {"start": v(-3336.86, 3758.52) * mm, "end": v(-3348.5, 3770.54) * mm});
            skLineSegment(sketch, "E3086", {"start": v(-3348.5, 3770.54) * mm, "end": v(-3361.23, 3783) * mm});
            skLineSegment(sketch, "E3087", {"start": v(-3361.23, 3783) * mm, "end": v(-3375.11, 3795.87) * mm});
            skLineSegment(sketch, "E3088", {"start": v(-3375.11, 3795.87) * mm, "end": v(-3390.16, 3809.1) * mm});
            skLineSegment(sketch, "E3089", {"start": v(-3390.16, 3809.1) * mm, "end": v(-3406.4, 3822.6) * mm});
            skLineSegment(sketch, "E3090", {"start": v(-3406.4, 3822.6) * mm, "end": v(-3423.88, 3836.37) * mm});
            skLineSegment(sketch, "E3091", {"start": v(-3423.88, 3836.37) * mm, "end": v(-3442.6, 3850.31) * mm});
            skLineSegment(sketch, "E3092", {"start": v(-3442.6, 3850.31) * mm, "end": v(-3462.58, 3864.39) * mm});
            skLineSegment(sketch, "E3093", {"start": v(-3462.58, 3864.39) * mm, "end": v(-3483.86, 3878.53) * mm});
            skLineSegment(sketch, "E3094", {"start": v(-3483.86, 3878.53) * mm, "end": v(-3506.45, 3892.68) * mm});
            skLineSegment(sketch, "E3095", {"start": v(-3506.45, 3892.68) * mm, "end": v(-3530.35, 3906.78) * mm});
            skLineSegment(sketch, "E3096", {"start": v(-3530.35, 3906.78) * mm, "end": v(-3555.6, 3920.77) * mm});
            skLineSegment(sketch, "E3097", {"start": v(-3555.6, 3920.77) * mm, "end": v(-3581.49, 3933.2) * mm});
            skLineSegment(sketch, "E3098", {"start": v(-3581.49, 3933.2) * mm, "end": v(-3700.47, 3867.9) * mm});
            skLineSegment(sketch, "E3099", {"start": v(-3700.47, 3867.9) * mm, "end": v(-3703.89, 3839.4) * mm});
            skLineSegment(sketch, "E3100", {"start": v(-3703.89, 3839.4) * mm, "end": v(-3705.65, 3810.58) * mm});
            skLineSegment(sketch, "E3101", {"start": v(-3705.65, 3810.58) * mm, "end": v(-3706.6, 3782.84) * mm});
            skLineSegment(sketch, "E3102", {"start": v(-3706.6, 3782.84) * mm, "end": v(-3706.78, 3756.2) * mm});
            skLineSegment(sketch, "E3103", {"start": v(-3706.78, 3756.2) * mm, "end": v(-3706.28, 3730.65) * mm});
            skLineSegment(sketch, "E3104", {"start": v(-3706.28, 3730.65) * mm, "end": v(-3705.15, 3706.23) * mm});
            skLineSegment(sketch, "E3105", {"start": v(-3705.15, 3706.23) * mm, "end": v(-3703.44, 3682.95) * mm});
            skLineSegment(sketch, "E3106", {"start": v(-3703.44, 3682.95) * mm, "end": v(-3701.21, 3660.82) * mm});
            skLineSegment(sketch, "E3107", {"start": v(-3701.21, 3660.82) * mm, "end": v(-3698.54, 3639.86) * mm});
            skLineSegment(sketch, "E3108", {"start": v(-3698.54, 3639.86) * mm, "end": v(-3695.46, 3620.06) * mm});
            skLineSegment(sketch, "E3109", {"start": v(-3695.46, 3620.06) * mm, "end": v(-3692.06, 3601.44) * mm});
            skLineSegment(sketch, "E3110", {"start": v(-3692.06, 3601.44) * mm, "end": v(-3688.39, 3584) * mm});
            skLineSegment(sketch, "E3111", {"start": v(-3688.39, 3584) * mm, "end": v(-3684.5, 3567.74) * mm});
            skLineSegment(sketch, "E3112", {"start": v(-3684.5, 3567.74) * mm, "end": v(-3680.47, 3552.65) * mm});
            skLineSegment(sketch, "E3113", {"start": v(-3680.47, 3552.65) * mm, "end": v(-3676.35, 3538.74) * mm});
            skLineSegment(sketch, "E3114", {"start": v(-3676.35, 3538.74) * mm, "end": v(-3672.2, 3525.99) * mm});
            skLineSegment(sketch, "E3115", {"start": v(-3672.2, 3525.99) * mm, "end": v(-3668.07, 3514.4) * mm});
            skLineSegment(sketch, "E3116", {"start": v(-3668.07, 3514.4) * mm, "end": v(-3664.04, 3503.94) * mm});
            skLineSegment(sketch, "E3117", {"start": v(-3664.04, 3503.94) * mm, "end": v(-3660.15, 3494.63) * mm});
            skLineSegment(sketch, "E3118", {"start": v(-3660.15, 3494.63) * mm, "end": v(-3656.46, 3486.42) * mm});
            skLineSegment(sketch, "E3119", {"start": v(-3656.46, 3486.42) * mm, "end": v(-3653.04, 3479.31) * mm});
            skLineSegment(sketch, "E3120", {"start": v(-3653.04, 3479.31) * mm, "end": v(-3649.93, 3473.28) * mm});
            skLineSegment(sketch, "E3121", {"start": v(-3649.93, 3473.28) * mm, "end": v(-3647.19, 3468.3) * mm});
            skLineSegment(sketch, "E3122", {"start": v(-3647.19, 3468.3) * mm, "end": v(-3644.88, 3464.35) * mm});
            skLineSegment(sketch, "E3123", {"start": v(-3644.88, 3464.35) * mm, "end": v(-3643.04, 3461.4) * mm});
            skLineSegment(sketch, "E3124", {"start": v(-3643.04, 3461.4) * mm, "end": v(-3641.73, 3459.41) * mm});
            skLineSegment(sketch, "E3125", {"start": v(-3641.73, 3459.41) * mm, "end": v(-3641, 3458.37) * mm});
            skLineSegment(sketch, "E3126", {"start": v(-3641, 3458.37) * mm, "end": v(-3538.04, 3320.45) * mm});
            skLineSegment(sketch, "E3127", {"start": v(-3538.04, 3320.45) * mm, "end": v(-3742.2, 3132.69) * mm});
            skLineSegment(sketch, "E3128", {"start": v(-3742.2, 3132.69) * mm, "end": v(-3871.04, 3246.82) * mm});
            skLineSegment(sketch, "E3129", {"start": v(-3871.04, 3246.82) * mm, "end": v(-3872.02, 3247.63) * mm});
            skLineSegment(sketch, "E3130", {"start": v(-3872.02, 3247.63) * mm, "end": v(-3873.88, 3249.1) * mm});
            skLineSegment(sketch, "E3131", {"start": v(-3873.88, 3249.1) * mm, "end": v(-3876.67, 3251.17) * mm});
            skLineSegment(sketch, "E3132", {"start": v(-3876.67, 3251.17) * mm, "end": v(-3880.42, 3253.8) * mm});
            skLineSegment(sketch, "E3133", {"start": v(-3880.42, 3253.8) * mm, "end": v(-3885.15, 3256.95) * mm});
            skLineSegment(sketch, "E3134", {"start": v(-3885.15, 3256.95) * mm, "end": v(-3890.9, 3260.55) * mm});
            skLineSegment(sketch, "E3135", {"start": v(-3890.9, 3260.55) * mm, "end": v(-3897.7, 3264.56) * mm});
            skLineSegment(sketch, "E3136", {"start": v(-3897.7, 3264.56) * mm, "end": v(-3905.57, 3268.92) * mm});
            skLineSegment(sketch, "E3137", {"start": v(-3905.57, 3268.92) * mm, "end": v(-3914.53, 3273.57) * mm});
            skLineSegment(sketch, "E3138", {"start": v(-3914.53, 3273.57) * mm, "end": v(-3924.6, 3278.47) * mm});
            skLineSegment(sketch, "E3139", {"start": v(-3924.6, 3278.47) * mm, "end": v(-3935.82, 3283.55) * mm});
            skLineSegment(sketch, "E3140", {"start": v(-3935.82, 3283.55) * mm, "end": v(-3948.17, 3288.75) * mm});
            skLineSegment(sketch, "E3141", {"start": v(-3948.17, 3288.75) * mm, "end": v(-3961.7, 3294.02) * mm});
            skLineSegment(sketch, "E3142", {"start": v(-3961.7, 3294.02) * mm, "end": v(-3976.4, 3299.3) * mm});
            skLineSegment(sketch, "E3143", {"start": v(-3976.4, 3299.3) * mm, "end": v(-3992.27, 3304.53) * mm});
            skLineSegment(sketch, "E3144", {"start": v(-3992.27, 3304.53) * mm, "end": v(-4009.35, 3309.65) * mm});
            skLineSegment(sketch, "E3145", {"start": v(-4009.35, 3309.65) * mm, "end": v(-4027.62, 3314.6) * mm});
            skLineSegment(sketch, "E3146", {"start": v(-4027.62, 3314.6) * mm, "end": v(-4047.09, 3319.3) * mm});
            skLineSegment(sketch, "E3147", {"start": v(-4047.09, 3319.3) * mm, "end": v(-4067.75, 3323.72) * mm});
            skLineSegment(sketch, "E3148", {"start": v(-4067.75, 3323.72) * mm, "end": v(-4089.62, 3327.8) * mm});
            skLineSegment(sketch, "E3149", {"start": v(-4089.62, 3327.8) * mm, "end": v(-4112.67, 3331.44) * mm});
            skLineSegment(sketch, "E3150", {"start": v(-4112.67, 3331.44) * mm, "end": v(-4136.91, 3334.61) * mm});
            skLineSegment(sketch, "E3151", {"start": v(-4136.91, 3334.61) * mm, "end": v(-4162.32, 3337.25) * mm});
            skLineSegment(sketch, "E3152", {"start": v(-4162.32, 3337.25) * mm, "end": v(-4188.9, 3339.28) * mm});
            skLineSegment(sketch, "E3153", {"start": v(-4188.9, 3339.28) * mm, "end": v(-4216.62, 3340.66) * mm});
            skLineSegment(sketch, "E3154", {"start": v(-4216.62, 3340.66) * mm, "end": v(-4245.47, 3341.31) * mm});
            skLineSegment(sketch, "E3155", {"start": v(-4245.47, 3341.31) * mm, "end": v(-4274.18, 3340.29) * mm});
            skLineSegment(sketch, "E3156", {"start": v(-4274.18, 3340.29) * mm, "end": v(-4349.19, 3227.18) * mm});
            skLineSegment(sketch, "E3157", {"start": v(-4349.19, 3227.18) * mm, "end": v(-4338.96, 3200.34) * mm});
            skLineSegment(sketch, "E3158", {"start": v(-4338.96, 3200.34) * mm, "end": v(-4327.13, 3174.01) * mm});
            skLineSegment(sketch, "E3159", {"start": v(-4327.13, 3174.01) * mm, "end": v(-4315.07, 3149.01) * mm});
            skLineSegment(sketch, "E3160", {"start": v(-4315.07, 3149.01) * mm, "end": v(-4302.86, 3125.32) * mm});
            skLineSegment(sketch, "E3161", {"start": v(-4302.86, 3125.32) * mm, "end": v(-4290.54, 3102.94) * mm});
            skLineSegment(sketch, "E3162", {"start": v(-4290.54, 3102.94) * mm, "end": v(-4278.19, 3081.85) * mm});
            skLineSegment(sketch, "E3163", {"start": v(-4278.19, 3081.85) * mm, "end": v(-4265.86, 3062.03) * mm});
            skLineSegment(sketch, "E3164", {"start": v(-4265.86, 3062.03) * mm, "end": v(-4253.6, 3043.47) * mm});
            skLineSegment(sketch, "E3165", {"start": v(-4253.6, 3043.47) * mm, "end": v(-4241.5, 3026.15) * mm});
            skLineSegment(sketch, "E3166", {"start": v(-4241.5, 3026.15) * mm, "end": v(-4229.57, 3010.05) * mm});
            skLineSegment(sketch, "E3167", {"start": v(-4229.57, 3010.05) * mm, "end": v(-4217.91, 2995.14) * mm});
            skLineSegment(sketch, "E3168", {"start": v(-4217.91, 2995.14) * mm, "end": v(-4206.55, 2981.4) * mm});
            skLineSegment(sketch, "E3169", {"start": v(-4206.55, 2981.4) * mm, "end": v(-4195.56, 2968.81) * mm});
            skLineSegment(sketch, "E3170", {"start": v(-4195.56, 2968.81) * mm, "end": v(-4184.97, 2957.33) * mm});
            skLineSegment(sketch, "E3171", {"start": v(-4184.97, 2957.33) * mm, "end": v(-4174.86, 2946.92) * mm});
            skLineSegment(sketch, "E3172", {"start": v(-4174.86, 2946.92) * mm, "end": v(-4165.25, 2937.56) * mm});
            skLineSegment(sketch, "E3173", {"start": v(-4165.25, 2937.56) * mm, "end": v(-4156.21, 2929.21) * mm});
            skLineSegment(sketch, "E3174", {"start": v(-4156.21, 2929.21) * mm, "end": v(-4147.78, 2921.84) * mm});
            skLineSegment(sketch, "E3175", {"start": v(-4147.78, 2921.84) * mm, "end": v(-4140, 2915.4) * mm});
            skLineSegment(sketch, "E3176", {"start": v(-4140, 2915.4) * mm, "end": v(-4132.93, 2909.84) * mm});
            skLineSegment(sketch, "E3177", {"start": v(-4132.93, 2909.84) * mm, "end": v(-4126.6, 2905.14) * mm});
            skLineSegment(sketch, "E3178", {"start": v(-4126.6, 2905.14) * mm, "end": v(-4121.04, 2901.24) * mm});
            skLineSegment(sketch, "E3179", {"start": v(-4121.04, 2901.24) * mm, "end": v(-4116.3, 2898.1) * mm});
            skLineSegment(sketch, "E3180", {"start": v(-4116.3, 2898.1) * mm, "end": v(-4112.41, 2895.68) * mm});
            skLineSegment(sketch, "E3181", {"start": v(-4112.41, 2895.68) * mm, "end": v(-4109.42, 2893.91) * mm});
            skLineSegment(sketch, "E3182", {"start": v(-4109.42, 2893.91) * mm, "end": v(-4107.34, 2892.77) * mm});
            skLineSegment(sketch, "E3183", {"start": v(-4107.34, 2892.77) * mm, "end": v(-4106.22, 2892.18) * mm});
            skLineSegment(sketch, "E3184", {"start": v(-4106.22, 2892.18) * mm, "end": v(-3950.95, 2817.92) * mm});
            skLineSegment(sketch, "E3185", {"start": v(-3950.95, 2817.92) * mm, "end": v(-4044.47, 2556.78) * mm});
            skLineSegment(sketch, "E3186", {"start": v(-4044.47, 2556.78) * mm, "end": v(-4211.58, 2597.96) * mm});
            skLineSegment(sketch, "E3187", {"start": v(-4211.58, 2597.96) * mm, "end": v(-4212.82, 2598.23) * mm});
            skLineSegment(sketch, "E3188", {"start": v(-4212.82, 2598.23) * mm, "end": v(-4215.16, 2598.66) * mm});
            skLineSegment(sketch, "E3189", {"start": v(-4215.16, 2598.66) * mm, "end": v(-4218.6, 2599.2) * mm});
            skLineSegment(sketch, "E3190", {"start": v(-4218.6, 2599.2) * mm, "end": v(-4223.13, 2599.8) * mm});
            skLineSegment(sketch, "E3191", {"start": v(-4223.13, 2599.8) * mm, "end": v(-4228.79, 2600.38) * mm});
            skLineSegment(sketch, "E3192", {"start": v(-4228.79, 2600.38) * mm, "end": v(-4235.55, 2600.9) * mm});
            skLineSegment(sketch, "E3193", {"start": v(-4235.55, 2600.9) * mm, "end": v(-4243.44, 2601.28) * mm});
            skLineSegment(sketch, "E3194", {"start": v(-4243.44, 2601.28) * mm, "end": v(-4252.43, 2601.48) * mm});
            skLineSegment(sketch, "E3195", {"start": v(-4252.43, 2601.48) * mm, "end": v(-4262.53, 2601.44) * mm});
            skLineSegment(sketch, "E3196", {"start": v(-4262.53, 2601.44) * mm, "end": v(-4273.72, 2601.1) * mm});
            skLineSegment(sketch, "E3197", {"start": v(-4273.72, 2601.1) * mm, "end": v(-4286, 2600.38) * mm});
            skLineSegment(sketch, "E3198", {"start": v(-4286, 2600.38) * mm, "end": v(-4299.37, 2599.25) * mm});
            skLineSegment(sketch, "E3199", {"start": v(-4299.37, 2599.25) * mm, "end": v(-4313.8, 2597.63) * mm});
            skLineSegment(sketch, "E3200", {"start": v(-4313.8, 2597.63) * mm, "end": v(-4329.26, 2595.47) * mm});
            skLineSegment(sketch, "E3201", {"start": v(-4329.26, 2595.47) * mm, "end": v(-4345.75, 2592.72) * mm});
            skLineSegment(sketch, "E3202", {"start": v(-4345.75, 2592.72) * mm, "end": v(-4363.25, 2589.32) * mm});
            skLineSegment(sketch, "E3203", {"start": v(-4363.25, 2589.32) * mm, "end": v(-4381.72, 2585.2) * mm});
            skLineSegment(sketch, "E3204", {"start": v(-4381.72, 2585.2) * mm, "end": v(-4401.15, 2580.33) * mm});
            skLineSegment(sketch, "E3205", {"start": v(-4401.15, 2580.33) * mm, "end": v(-4421.5, 2574.64) * mm});
            skLineSegment(sketch, "E3206", {"start": v(-4421.5, 2574.64) * mm, "end": v(-4442.75, 2568.08) * mm});
            skLineSegment(sketch, "E3207", {"start": v(-4442.75, 2568.08) * mm, "end": v(-4464.86, 2560.6) * mm});
            skLineSegment(sketch, "E3208", {"start": v(-4464.86, 2560.6) * mm, "end": v(-4487.8, 2552.14) * mm});
            skLineSegment(sketch, "E3209", {"start": v(-4487.8, 2552.14) * mm, "end": v(-4511.53, 2542.66) * mm});
            skLineSegment(sketch, "E3210", {"start": v(-4511.53, 2542.66) * mm, "end": v(-4536, 2532.12) * mm});
            skLineSegment(sketch, "E3211", {"start": v(-4536, 2532.12) * mm, "end": v(-4561.2, 2520.45) * mm});
            skLineSegment(sketch, "E3212", {"start": v(-4561.2, 2520.45) * mm, "end": v(-4587.04, 2507.62) * mm});
            skLineSegment(sketch, "E3213", {"start": v(-4587.04, 2507.62) * mm, "end": v(-4611.98, 2493.38) * mm});
            skLineSegment(sketch, "E3214", {"start": v(-4611.98, 2493.38) * mm, "end": v(-4625.83, 2358.37) * mm});
            skLineSegment(sketch, "E3215", {"start": v(-4625.83, 2358.37) * mm, "end": v(-4604.3, 2339.35) * mm});
            skLineSegment(sketch, "E3216", {"start": v(-4604.3, 2339.35) * mm, "end": v(-4581.6, 2321.54) * mm});
            skLineSegment(sketch, "E3217", {"start": v(-4581.6, 2321.54) * mm, "end": v(-4559.3, 2305) * mm});
            skLineSegment(sketch, "E3218", {"start": v(-4559.3, 2305) * mm, "end": v(-4537.48, 2289.7) * mm});
            skLineSegment(sketch, "E3219", {"start": v(-4537.48, 2289.7) * mm, "end": v(-4516.17, 2275.61) * mm});
            skLineSegment(sketch, "E3220", {"start": v(-4516.17, 2275.61) * mm, "end": v(-4495.43, 2262.68) * mm});
            skLineSegment(sketch, "E3221", {"start": v(-4495.43, 2262.68) * mm, "end": v(-4475.3, 2250.86) * mm});
            skLineSegment(sketch, "E3222", {"start": v(-4475.3, 2250.86) * mm, "end": v(-4455.83, 2240.12) * mm});
            skLineSegment(sketch, "E3223", {"start": v(-4455.83, 2240.12) * mm, "end": v(-4437.05, 2230.41) * mm});
            skLineSegment(sketch, "E3224", {"start": v(-4437.05, 2230.41) * mm, "end": v(-4419.02, 2221.7) * mm});
            skLineSegment(sketch, "E3225", {"start": v(-4419.02, 2221.7) * mm, "end": v(-4401.76, 2213.92) * mm});
            skLineSegment(sketch, "E3226", {"start": v(-4401.76, 2213.92) * mm, "end": v(-4385.32, 2207.03) * mm});
            skLineSegment(sketch, "E3227", {"start": v(-4385.32, 2207.03) * mm, "end": v(-4369.73, 2200.99) * mm});
            skLineSegment(sketch, "E3228", {"start": v(-4369.73, 2200.99) * mm, "end": v(-4355.02, 2195.74) * mm});
            skLineSegment(sketch, "E3229", {"start": v(-4355.02, 2195.74) * mm, "end": v(-4341.23, 2191.23) * mm});
            skLineSegment(sketch, "E3230", {"start": v(-4341.23, 2191.23) * mm, "end": v(-4328.38, 2187.4) * mm});
            skLineSegment(sketch, "E3231", {"start": v(-4328.38, 2187.4) * mm, "end": v(-4316.5, 2184.21) * mm});
            skLineSegment(sketch, "E3232", {"start": v(-4316.5, 2184.21) * mm, "end": v(-4305.6, 2181.6) * mm});
            skLineSegment(sketch, "E3233", {"start": v(-4305.6, 2181.6) * mm, "end": v(-4295.72, 2179.5) * mm});
            skLineSegment(sketch, "E3234", {"start": v(-4295.72, 2179.5) * mm, "end": v(-4286.88, 2177.88) * mm});
            skLineSegment(sketch, "E3235", {"start": v(-4286.88, 2177.88) * mm, "end": v(-4279.08, 2176.66) * mm});
            skLineSegment(sketch, "E3236", {"start": v(-4279.08, 2176.66) * mm, "end": v(-4272.35, 2175.79) * mm});
            skLineSegment(sketch, "E3237", {"start": v(-4272.35, 2175.79) * mm, "end": v(-4266.7, 2175.21) * mm});
            skLineSegment(sketch, "E3238", {"start": v(-4266.7, 2175.21) * mm, "end": v(-4262.13, 2174.87) * mm});
            skLineSegment(sketch, "E3239", {"start": v(-4262.13, 2174.87) * mm, "end": v(-4258.65, 2174.7) * mm});
            skLineSegment(sketch, "E3240", {"start": v(-4258.65, 2174.7) * mm, "end": v(-4256.28, 2174.65) * mm});
            skLineSegment(sketch, "E3241", {"start": v(-4256.28, 2174.65) * mm, "end": v(-4255.01, 2174.66) * mm});
            skLineSegment(sketch, "E3242", {"start": v(-4255.01, 2174.66) * mm, "end": v(-4083.02, 2181.05) * mm});
            skLineSegment(sketch, "E3243", {"start": v(-4083.02, 2181.05) * mm, "end": v(-4044.47, 1906.37) * mm});
            skLineSegment(sketch, "E3244", {"start": v(-4044.47, 1906.37) * mm, "end": v(-4211.58, 1865.17) * mm});
            skLineSegment(sketch, "E3245", {"start": v(-4211.58, 1865.17) * mm, "end": v(-4212.8, 1864.83) * mm});
            skLineSegment(sketch, "E3246", {"start": v(-4212.8, 1864.83) * mm, "end": v(-4215.07, 1864.13) * mm});
            skLineSegment(sketch, "E3247", {"start": v(-4215.07, 1864.13) * mm, "end": v(-4218.36, 1863.01) * mm});
            skLineSegment(sketch, "E3248", {"start": v(-4218.36, 1863.01) * mm, "end": v(-4222.66, 1861.42) * mm});
            skLineSegment(sketch, "E3249", {"start": v(-4222.66, 1861.42) * mm, "end": v(-4227.94, 1859.32) * mm});
            skLineSegment(sketch, "E3250", {"start": v(-4227.94, 1859.32) * mm, "end": v(-4234.17, 1856.63) * mm});
            skLineSegment(sketch, "E3251", {"start": v(-4234.17, 1856.63) * mm, "end": v(-4241.33, 1853.3) * mm});
            skLineSegment(sketch, "E3252", {"start": v(-4241.33, 1853.3) * mm, "end": v(-4249.38, 1849.3) * mm});
            skLineSegment(sketch, "E3253", {"start": v(-4249.38, 1849.3) * mm, "end": v(-4258.3, 1844.58) * mm});
            skLineSegment(sketch, "E3254", {"start": v(-4258.3, 1844.58) * mm, "end": v(-4268.06, 1839.07) * mm});
            skLineSegment(sketch, "E3255", {"start": v(-4268.06, 1839.07) * mm, "end": v(-4278.6, 1832.73) * mm});
            skLineSegment(sketch, "E3256", {"start": v(-4278.6, 1832.73) * mm, "end": v(-4289.9, 1825.51) * mm});
            skLineSegment(sketch, "E3257", {"start": v(-4289.9, 1825.51) * mm, "end": v(-4301.93, 1817.38) * mm});
            skLineSegment(sketch, "E3258", {"start": v(-4301.93, 1817.38) * mm, "end": v(-4314.62, 1808.28) * mm});
            skLineSegment(sketch, "E3259", {"start": v(-4314.62, 1808.28) * mm, "end": v(-4327.95, 1798.18) * mm});
            skLineSegment(sketch, "E3260", {"start": v(-4327.95, 1798.18) * mm, "end": v(-4341.86, 1787.04) * mm});
            skLineSegment(sketch, "E3261", {"start": v(-4341.86, 1787.04) * mm, "end": v(-4356.3, 1774.81) * mm});
            skLineSegment(sketch, "E3262", {"start": v(-4356.3, 1774.81) * mm, "end": v(-4371.24, 1761.47) * mm});
            skLineSegment(sketch, "E3263", {"start": v(-4371.24, 1761.47) * mm, "end": v(-4386.62, 1746.97) * mm});
            skLineSegment(sketch, "E3264", {"start": v(-4386.62, 1746.97) * mm, "end": v(-4402.39, 1731.28) * mm});
            skLineSegment(sketch, "E3265", {"start": v(-4402.39, 1731.28) * mm, "end": v(-4418.49, 1714.38) * mm});
            skLineSegment(sketch, "E3266", {"start": v(-4418.49, 1714.38) * mm, "end": v(-4434.87, 1696.23) * mm});
            skLineSegment(sketch, "E3267", {"start": v(-4434.87, 1696.23) * mm, "end": v(-4451.47, 1676.82) * mm});
            skLineSegment(sketch, "E3268", {"start": v(-4451.47, 1676.82) * mm, "end": v(-4468.24, 1656.1) * mm});
            skLineSegment(sketch, "E3269", {"start": v(-4468.24, 1656.1) * mm, "end": v(-4485.12, 1634.07) * mm});
            skLineSegment(sketch, "E3270", {"start": v(-4485.12, 1634.07) * mm, "end": v(-4502.05, 1610.7) * mm});
            skLineSegment(sketch, "E3271", {"start": v(-4502.05, 1610.7) * mm, "end": v(-4517.51, 1586.5) * mm});
            skLineSegment(sketch, "E3272", {"start": v(-4517.51, 1586.5) * mm, "end": v(-4467.04, 1460.5) * mm});
            skLineSegment(sketch, "E3273", {"start": v(-4467.04, 1460.5) * mm, "end": v(-4439.14, 1453.68) * mm});
            skLineSegment(sketch, "E3274", {"start": v(-4439.14, 1453.68) * mm, "end": v(-4410.76, 1448.46) * mm});
            skLineSegment(sketch, "E3275", {"start": v(-4410.76, 1448.46) * mm, "end": v(-4383.33, 1444.18) * mm});
            skLineSegment(sketch, "E3276", {"start": v(-4383.33, 1444.18) * mm, "end": v(-4356.9, 1440.78) * mm});
            skLineSegment(sketch, "E3277", {"start": v(-4356.9, 1440.78) * mm, "end": v(-4331.48, 1438.2) * mm});
            skLineSegment(sketch, "E3278", {"start": v(-4331.48, 1438.2) * mm, "end": v(-4307.1, 1436.38) * mm});
            skLineSegment(sketch, "E3279", {"start": v(-4307.1, 1436.38) * mm, "end": v(-4283.78, 1435.27) * mm});
            skLineSegment(sketch, "E3280", {"start": v(-4283.78, 1435.27) * mm, "end": v(-4261.55, 1434.8) * mm});
            skLineSegment(sketch, "E3281", {"start": v(-4261.55, 1434.8) * mm, "end": v(-4240.41, 1434.94) * mm});
            skLineSegment(sketch, "E3282", {"start": v(-4240.41, 1434.94) * mm, "end": v(-4220.4, 1435.6) * mm});
            skLineSegment(sketch, "E3283", {"start": v(-4220.4, 1435.6) * mm, "end": v(-4201.5, 1436.74) * mm});
            skLineSegment(sketch, "E3284", {"start": v(-4201.5, 1436.74) * mm, "end": v(-4183.74, 1438.28) * mm});
            skLineSegment(sketch, "E3285", {"start": v(-4183.74, 1438.28) * mm, "end": v(-4167.13, 1440.17) * mm});
            skLineSegment(sketch, "E3286", {"start": v(-4167.13, 1440.17) * mm, "end": v(-4151.67, 1442.36) * mm});
            skLineSegment(sketch, "E3287", {"start": v(-4151.67, 1442.36) * mm, "end": v(-4137.36, 1444.77) * mm});
            skLineSegment(sketch, "E3288", {"start": v(-4137.36, 1444.77) * mm, "end": v(-4124.2, 1447.36) * mm});
            skLineSegment(sketch, "E3289", {"start": v(-4124.2, 1447.36) * mm, "end": v(-4112.2, 1450.06) * mm});
            skLineSegment(sketch, "E3290", {"start": v(-4112.2, 1450.06) * mm, "end": v(-4101.33, 1452.8) * mm});
            skLineSegment(sketch, "E3291", {"start": v(-4101.33, 1452.8) * mm, "end": v(-4091.62, 1455.54) * mm});
            skLineSegment(sketch, "E3292", {"start": v(-4091.62, 1455.54) * mm, "end": v(-4083.03, 1458.21) * mm});
            skLineSegment(sketch, "E3293", {"start": v(-4083.03, 1458.21) * mm, "end": v(-4075.56, 1460.76) * mm});
            skLineSegment(sketch, "E3294", {"start": v(-4075.56, 1460.76) * mm, "end": v(-4069.2, 1463.12) * mm});
            skLineSegment(sketch, "E3295", {"start": v(-4069.2, 1463.12) * mm, "end": v(-4063.92, 1465.23) * mm});
            skLineSegment(sketch, "E3296", {"start": v(-4063.92, 1465.23) * mm, "end": v(-4059.71, 1467.05) * mm});
            skLineSegment(sketch, "E3297", {"start": v(-4059.71, 1467.05) * mm, "end": v(-4056.56, 1468.52) * mm});
            skLineSegment(sketch, "E3298", {"start": v(-4056.56, 1468.52) * mm, "end": v(-4054.44, 1469.58) * mm});
            skLineSegment(sketch, "E3299", {"start": v(-4054.44, 1469.58) * mm, "end": v(-4053.32, 1470.17) * mm});
            skLineSegment(sketch, "E3300", {"start": v(-4053.32, 1470.17) * mm, "end": v(-3904, 1555.76) * mm});
            skLineSegment(sketch, "E3301", {"start": v(-3904, 1555.76) * mm, "end": v(-3742.2, 1330.45) * mm});
            skLineSegment(sketch, "E3302", {"start": v(-3742.2, 1330.45) * mm, "end": v(-3871.04, 1216.32) * mm});
            skLineSegment(sketch, "E3303", {"start": v(-3871.04, 1216.32) * mm, "end": v(-3871.96, 1215.45) * mm});
            skLineSegment(sketch, "E3304", {"start": v(-3871.96, 1215.45) * mm, "end": v(-3873.64, 1213.77) * mm});
            skLineSegment(sketch, "E3305", {"start": v(-3873.64, 1213.77) * mm, "end": v(-3876.03, 1211.25) * mm});
            skLineSegment(sketch, "E3306", {"start": v(-3876.03, 1211.25) * mm, "end": v(-3879.1, 1207.85) * mm});
            skLineSegment(sketch, "E3307", {"start": v(-3879.1, 1207.85) * mm, "end": v(-3882.8, 1203.53) * mm});
            skLineSegment(sketch, "E3308", {"start": v(-3882.8, 1203.53) * mm, "end": v(-3887.06, 1198.25) * mm});
            skLineSegment(sketch, "E3309", {"start": v(-3887.06, 1198.25) * mm, "end": v(-3891.86, 1191.99) * mm});
            skLineSegment(sketch, "E3310", {"start": v(-3891.86, 1191.99) * mm, "end": v(-3897.14, 1184.7) * mm});
            skLineSegment(sketch, "E3311", {"start": v(-3897.14, 1184.7) * mm, "end": v(-3902.84, 1176.37) * mm});
            skLineSegment(sketch, "E3312", {"start": v(-3902.84, 1176.37) * mm, "end": v(-3908.91, 1166.96) * mm});
            skLineSegment(sketch, "E3313", {"start": v(-3908.91, 1166.96) * mm, "end": v(-3915.3, 1156.44) * mm});
            skLineSegment(sketch, "E3314", {"start": v(-3915.3, 1156.44) * mm, "end": v(-3921.96, 1144.8) * mm});
            skLineSegment(sketch, "E3315", {"start": v(-3921.96, 1144.8) * mm, "end": v(-3928.82, 1132.01) * mm});
            skLineSegment(sketch, "E3316", {"start": v(-3928.82, 1132.01) * mm, "end": v(-3935.83, 1118.06) * mm});
            skLineSegment(sketch, "E3317", {"start": v(-3935.83, 1118.06) * mm, "end": v(-3942.94, 1102.92) * mm});
            skLineSegment(sketch, "E3318", {"start": v(-3942.94, 1102.92) * mm, "end": v(-3950.08, 1086.6) * mm});
            skLineSegment(sketch, "E3319", {"start": v(-3950.08, 1086.6) * mm, "end": v(-3957.19, 1069.05) * mm});
            skLineSegment(sketch, "E3320", {"start": v(-3957.19, 1069.05) * mm, "end": v(-3964.21, 1050.3) * mm});
            skLineSegment(sketch, "E3321", {"start": v(-3964.21, 1050.3) * mm, "end": v(-3971.1, 1030.3) * mm});
            skLineSegment(sketch, "E3322", {"start": v(-3971.1, 1030.3) * mm, "end": v(-3977.76, 1009.1) * mm});
            skLineSegment(sketch, "E3323", {"start": v(-3977.76, 1009.1) * mm, "end": v(-3984.16, 986.65) * mm});
            skLineSegment(sketch, "E3324", {"start": v(-3984.16, 986.65) * mm, "end": v(-3990.23, 962.97) * mm});
            skLineSegment(sketch, "E3325", {"start": v(-3990.23, 962.97) * mm, "end": v(-3995.91, 938.06) * mm});
            skLineSegment(sketch, "E3326", {"start": v(-3995.91, 938.06) * mm, "end": v(-4001.14, 911.92) * mm});
            skLineSegment(sketch, "E3327", {"start": v(-4001.14, 911.92) * mm, "end": v(-4005.84, 884.57) * mm});
            skLineSegment(sketch, "E3328", {"start": v(-4005.84, 884.57) * mm, "end": v(-4009.97, 856) * mm});
            skLineSegment(sketch, "E3329", {"start": v(-4009.97, 856) * mm, "end": v(-4012.41, 827.39) * mm});
            skLineSegment(sketch, "E3330", {"start": v(-4012.41, 827.39) * mm, "end": v(-3909.17, 739.3) * mm});
            skLineSegment(sketch, "E3331", {"start": v(-3909.17, 739.3) * mm, "end": v(-3881.3, 746.2) * mm});
            skLineSegment(sketch, "E3332", {"start": v(-3881.3, 746.2) * mm, "end": v(-3853.74, 754.78) * mm});
            skLineSegment(sketch, "E3333", {"start": v(-3853.74, 754.78) * mm, "end": v(-3827.47, 763.73) * mm});
            skLineSegment(sketch, "E3334", {"start": v(-3827.47, 763.73) * mm, "end": v(-3802.48, 773) * mm});
            skLineSegment(sketch, "E3335", {"start": v(-3802.48, 773) * mm, "end": v(-3778.77, 782.53) * mm});
            skLineSegment(sketch, "E3336", {"start": v(-3778.77, 782.53) * mm, "end": v(-3756.34, 792.25) * mm});
            skLineSegment(sketch, "E3337", {"start": v(-3756.34, 792.25) * mm, "end": v(-3735.18, 802.1) * mm});
            skLineSegment(sketch, "E3338", {"start": v(-3735.18, 802.1) * mm, "end": v(-3715.28, 812.03) * mm});
            skLineSegment(sketch, "E3339", {"start": v(-3715.28, 812.03) * mm, "end": v(-3696.63, 821.97) * mm});
            skLineSegment(sketch, "E3340", {"start": v(-3696.63, 821.97) * mm, "end": v(-3679.2, 831.86) * mm});
            skLineSegment(sketch, "E3341", {"start": v(-3679.2, 831.86) * mm, "end": v(-3663, 841.64) * mm});
            skLineSegment(sketch, "E3342", {"start": v(-3663, 841.64) * mm, "end": v(-3648, 851.26) * mm});
            skLineSegment(sketch, "E3343", {"start": v(-3648, 851.26) * mm, "end": v(-3634.17, 860.66) * mm});
            skLineSegment(sketch, "E3344", {"start": v(-3634.17, 860.66) * mm, "end": v(-3621.5, 869.78) * mm});
            skLineSegment(sketch, "E3345", {"start": v(-3621.5, 869.78) * mm, "end": v(-3609.95, 878.57) * mm});
            skLineSegment(sketch, "E3346", {"start": v(-3609.95, 878.57) * mm, "end": v(-3599.5, 886.97) * mm});
            skLineSegment(sketch, "E3347", {"start": v(-3599.5, 886.97) * mm, "end": v(-3590.12, 894.94) * mm});
            skLineSegment(sketch, "E3348", {"start": v(-3590.12, 894.94) * mm, "end": v(-3581.78, 902.42) * mm});
            skLineSegment(sketch, "E3349", {"start": v(-3581.78, 902.42) * mm, "end": v(-3574.44, 909.36) * mm});
            skLineSegment(sketch, "E3350", {"start": v(-3574.44, 909.36) * mm, "end": v(-3568.08, 915.72) * mm});
            skLineSegment(sketch, "E3351", {"start": v(-3568.08, 915.72) * mm, "end": v(-3562.65, 921.44) * mm});
            skLineSegment(sketch, "E3352", {"start": v(-3562.65, 921.44) * mm, "end": v(-3558.1, 926.49) * mm});
            skLineSegment(sketch, "E3353", {"start": v(-3558.1, 926.49) * mm, "end": v(-3554.42, 930.81) * mm});
            skLineSegment(sketch, "E3354", {"start": v(-3554.42, 930.81) * mm, "end": v(-3551.55, 934.38) * mm});
            skLineSegment(sketch, "E3355", {"start": v(-3551.55, 934.38) * mm, "end": v(-3549.44, 937.14) * mm});
            skLineSegment(sketch, "E3356", {"start": v(-3549.44, 937.14) * mm, "end": v(-3548.05, 939.06) * mm});
            skLineSegment(sketch, "E3357", {"start": v(-3548.05, 939.06) * mm, "end": v(-3547.33, 940.11) * mm});
            skLineSegment(sketch, "E3358", {"start": v(-3547.33, 940.11) * mm, "end": v(-3454.9, 1085.3) * mm});
            skLineSegment(sketch, "E3359", {"start": v(-3454.9, 1085.3) * mm, "end": v(-3206.93, 960.98) * mm});
            skLineSegment(sketch, "E3360", {"start": v(-3206.93, 960.98) * mm, "end": v(-3267.96, 800.05) * mm});
            skLineSegment(sketch, "E3361", {"start": v(-3267.96, 800.05) * mm, "end": v(-3268.37, 798.85) * mm});
            skLineSegment(sketch, "E3362", {"start": v(-3268.37, 798.85) * mm, "end": v(-3269.08, 796.58) * mm});
            skLineSegment(sketch, "E3363", {"start": v(-3269.08, 796.58) * mm, "end": v(-3270.03, 793.24) * mm});
            skLineSegment(sketch, "E3364", {"start": v(-3270.03, 793.24) * mm, "end": v(-3271.17, 788.8) * mm});
            skLineSegment(sketch, "E3365", {"start": v(-3271.17, 788.8) * mm, "end": v(-3272.43, 783.26) * mm});
            skLineSegment(sketch, "E3366", {"start": v(-3272.43, 783.26) * mm, "end": v(-3273.76, 776.6) * mm});
            skLineSegment(sketch, "E3367", {"start": v(-3273.76, 776.6) * mm, "end": v(-3275.1, 768.83) * mm});
            skLineSegment(sketch, "E3368", {"start": v(-3275.1, 768.83) * mm, "end": v(-3276.38, 759.92) * mm});
            skLineSegment(sketch, "E3369", {"start": v(-3276.38, 759.92) * mm, "end": v(-3277.55, 749.9) * mm});
            skLineSegment(sketch, "E3370", {"start": v(-3277.55, 749.9) * mm, "end": v(-3278.56, 738.74) * mm});
            skLineSegment(sketch, "E3371", {"start": v(-3278.56, 738.74) * mm, "end": v(-3279.33, 726.46) * mm});
            skLineSegment(sketch, "E3372", {"start": v(-3279.33, 726.46) * mm, "end": v(-3279.81, 713.06) * mm});
            skLineSegment(sketch, "E3373", {"start": v(-3279.81, 713.06) * mm, "end": v(-3279.95, 698.54) * mm});
            skLineSegment(sketch, "E3374", {"start": v(-3279.95, 698.54) * mm, "end": v(-3279.67, 682.93) * mm});
            skLineSegment(sketch, "E3375", {"start": v(-3279.67, 682.93) * mm, "end": v(-3278.93, 666.23) * mm});
            skLineSegment(sketch, "E3376", {"start": v(-3278.93, 666.23) * mm, "end": v(-3277.66, 648.45) * mm});
            skLineSegment(sketch, "E3377", {"start": v(-3277.66, 648.45) * mm, "end": v(-3275.8, 629.61) * mm});
            skLineSegment(sketch, "E3378", {"start": v(-3275.8, 629.61) * mm, "end": v(-3273.3, 609.74) * mm});
            skLineSegment(sketch, "E3379", {"start": v(-3273.3, 609.74) * mm, "end": v(-3270.11, 588.84) * mm});
            skLineSegment(sketch, "E3380", {"start": v(-3270.11, 588.84) * mm, "end": v(-3266.16, 566.96) * mm});
            skLineSegment(sketch, "E3381", {"start": v(-3266.16, 566.96) * mm, "end": v(-3261.4, 544.1) * mm});
            skLineSegment(sketch, "E3382", {"start": v(-3261.4, 544.1) * mm, "end": v(-3255.77, 520.32) * mm});
            skLineSegment(sketch, "E3383", {"start": v(-3255.77, 520.32) * mm, "end": v(-3249.22, 495.63) * mm});
            skLineSegment(sketch, "E3384", {"start": v(-3249.22, 495.63) * mm, "end": v(-3241.7, 470.05) * mm});
            skLineSegment(sketch, "E3385", {"start": v(-3241.7, 470.05) * mm, "end": v(-3233.15, 443.65) * mm});
            skLineSegment(sketch, "E3386", {"start": v(-3233.15, 443.65) * mm, "end": v(-3223.53, 416.44) * mm});
            skLineSegment(sketch, "E3387", {"start": v(-3223.53, 416.44) * mm, "end": v(-3212.4, 389.96) * mm});
            skLineSegment(sketch, "E3388", {"start": v(-3212.4, 389.96) * mm, "end": v(-3080.04, 359.94) * mm});
            skLineSegment(sketch, "E3389", {"start": v(-3080.04, 359.94) * mm, "end": v(-3058.57, 379.02) * mm});
            skLineSegment(sketch, "E3390", {"start": v(-3058.57, 379.02) * mm, "end": v(-3038.16, 399.41) * mm});
            skLineSegment(sketch, "E3391", {"start": v(-3038.16, 399.41) * mm, "end": v(-3019.05, 419.55) * mm});
            skLineSegment(sketch, "E3392", {"start": v(-3019.05, 419.55) * mm, "end": v(-3001.23, 439.37) * mm});
            skLineSegment(sketch, "E3393", {"start": v(-3001.23, 439.37) * mm, "end": v(-2984.67, 458.82) * mm});
            skLineSegment(sketch, "E3394", {"start": v(-2984.67, 458.82) * mm, "end": v(-2969.33, 477.86) * mm});
            skLineSegment(sketch, "E3395", {"start": v(-2969.33, 477.86) * mm, "end": v(-2955.17, 496.41) * mm});
            skLineSegment(sketch, "E3396", {"start": v(-2955.17, 496.41) * mm, "end": v(-2942.16, 514.45) * mm});
            skLineSegment(sketch, "E3397", {"start": v(-2942.16, 514.45) * mm, "end": v(-2930.26, 531.92) * mm});
            skLineSegment(sketch, "E3398", {"start": v(-2930.26, 531.92) * mm, "end": v(-2919.44, 548.77) * mm});
            skLineSegment(sketch, "E3399", {"start": v(-2919.44, 548.77) * mm, "end": v(-2909.64, 564.96) * mm});
            skLineSegment(sketch, "E3400", {"start": v(-2909.64, 564.96) * mm, "end": v(-2900.82, 580.45) * mm});
            skLineSegment(sketch, "E3401", {"start": v(-2900.82, 580.45) * mm, "end": v(-2892.94, 595.2) * mm});
            skLineSegment(sketch, "E3402", {"start": v(-2892.94, 595.2) * mm, "end": v(-2885.96, 609.17) * mm});
            skLineSegment(sketch, "E3403", {"start": v(-2885.96, 609.17) * mm, "end": v(-2879.82, 622.32) * mm});
            skLineSegment(sketch, "E3404", {"start": v(-2879.82, 622.32) * mm, "end": v(-2874.47, 634.62) * mm});
            skLineSegment(sketch, "E3405", {"start": v(-2874.47, 634.62) * mm, "end": v(-2869.87, 646.03) * mm});
            skLineSegment(sketch, "E3406", {"start": v(-2869.87, 646.03) * mm, "end": v(-2865.96, 656.53) * mm});
            skLineSegment(sketch, "E3407", {"start": v(-2865.96, 656.53) * mm, "end": v(-2862.7, 666.08) * mm});
            skLineSegment(sketch, "E3408", {"start": v(-2862.7, 666.08) * mm, "end": v(-2860.01, 674.67) * mm});
            skLineSegment(sketch, "E3409", {"start": v(-2860.01, 674.67) * mm, "end": v(-2857.86, 682.26) * mm});
            skLineSegment(sketch, "E3410", {"start": v(-2857.86, 682.26) * mm, "end": v(-2856.19, 688.84) * mm});
            skLineSegment(sketch, "E3411", {"start": v(-2856.19, 688.84) * mm, "end": v(-2854.93, 694.38) * mm});
            skLineSegment(sketch, "E3412", {"start": v(-2854.93, 694.38) * mm, "end": v(-2854.04, 698.87) * mm});
            skLineSegment(sketch, "E3413", {"start": v(-2854.04, 698.87) * mm, "end": v(-2853.46, 702.3) * mm});
            skLineSegment(sketch, "E3414", {"start": v(-2853.46, 702.3) * mm, "end": v(-2853.12, 704.65) * mm});
            skLineSegment(sketch, "E3415", {"start": v(-2853.12, 704.65) * mm, "end": v(-2852.97, 705.91) * mm});
            skLineSegment(sketch, "E3416", {"start": v(-2852.97, 705.91) * mm, "end": v(-2838.6, 877.42) * mm});
            skLineSegment(sketch, "E3417", {"start": v(-2838.6, 877.42) * mm, "end": v(-2561.26, 882.58) * mm});
            skLineSegment(sketch, "E3418", {"start": v(-2561.26, 882.58) * mm, "end": v(-2540.51, 711.72) * mm});
            skLineSegment(sketch, "E3419", {"start": v(-2540.51, 711.72) * mm, "end": v(-2540.32, 710.47) * mm});
            skLineSegment(sketch, "E3420", {"start": v(-2540.32, 710.47) * mm, "end": v(-2539.9, 708.13) * mm});
            skLineSegment(sketch, "E3421", {"start": v(-2539.9, 708.13) * mm, "end": v(-2539.18, 704.73) * mm});
            skLineSegment(sketch, "E3422", {"start": v(-2539.18, 704.73) * mm, "end": v(-2538.12, 700.27) * mm});
            skLineSegment(sketch, "E3423", {"start": v(-2538.12, 700.27) * mm, "end": v(-2536.67, 694.78) * mm});
            skLineSegment(sketch, "E3424", {"start": v(-2536.67, 694.78) * mm, "end": v(-2534.75, 688.27) * mm});
            skLineSegment(sketch, "E3425", {"start": v(-2534.75, 688.27) * mm, "end": v(-2532.32, 680.76) * mm});
            skLineSegment(sketch, "E3426", {"start": v(-2532.32, 680.76) * mm, "end": v(-2529.32, 672.28) * mm});
            skLineSegment(sketch, "E3427", {"start": v(-2529.32, 672.28) * mm, "end": v(-2525.7, 662.85) * mm});
            skLineSegment(sketch, "E3428", {"start": v(-2525.7, 662.85) * mm, "end": v(-2521.4, 652.5) * mm});
            skLineSegment(sketch, "E3429", {"start": v(-2521.4, 652.5) * mm, "end": v(-2516.38, 641.28) * mm});
            skLineSegment(sketch, "E3430", {"start": v(-2516.38, 641.28) * mm, "end": v(-2510.58, 629.18) * mm});
            skLineSegment(sketch, "E3431", {"start": v(-2510.58, 629.18) * mm, "end": v(-2503.95, 616.27) * mm});
            skLineSegment(sketch, "E3432", {"start": v(-2503.95, 616.27) * mm, "end": v(-2496.45, 602.57) * mm});
            skLineSegment(sketch, "E3433", {"start": v(-2496.45, 602.57) * mm, "end": v(-2488.03, 588.13) * mm});
            skLineSegment(sketch, "E3434", {"start": v(-2488.03, 588.13) * mm, "end": v(-2478.65, 572.98) * mm});
            skLineSegment(sketch, "E3435", {"start": v(-2478.65, 572.98) * mm, "end": v(-2468.25, 557.16) * mm});
            skLineSegment(sketch, "E3436", {"start": v(-2468.25, 557.16) * mm, "end": v(-2456.8, 540.72) * mm});
            skLineSegment(sketch, "E3437", {"start": v(-2456.8, 540.72) * mm, "end": v(-2444.26, 523.7) * mm});
            skLineSegment(sketch, "E3438", {"start": v(-2444.26, 523.7) * mm, "end": v(-2430.6, 506.17) * mm});
            skLineSegment(sketch, "E3439", {"start": v(-2430.6, 506.17) * mm, "end": v(-2415.76, 488.15) * mm});
            skLineSegment(sketch, "E3440", {"start": v(-2415.76, 488.15) * mm, "end": v(-2399.72, 469.7) * mm});
            skLineSegment(sketch, "E3441", {"start": v(-2399.72, 469.7) * mm, "end": v(-2382.44, 450.88) * mm});
            skLineSegment(sketch, "E3442", {"start": v(-2382.44, 450.88) * mm, "end": v(-2363.9, 431.73) * mm});
            skLineSegment(sketch, "E3443", {"start": v(-2363.9, 431.73) * mm, "end": v(-2344.06, 412.32) * mm});
            skLineSegment(sketch, "E3444", {"start": v(-2344.06, 412.32) * mm, "end": v(-2322.9, 392.7) * mm});
            skLineSegment(sketch, "E3445", {"start": v(-2322.9, 392.7) * mm, "end": v(-2300.74, 374.43) * mm});
            skLineSegment(sketch, "E3446", {"start": v(-2300.74, 374.43) * mm, "end": v(-2169.59, 409.35) * mm});
            skLineSegment(sketch, "E3447", {"start": v(-2169.59, 409.35) * mm, "end": v(-2159.44, 436.22) * mm});
            skLineSegment(sketch, "E3448", {"start": v(-2159.44, 436.22) * mm, "end": v(-2150.84, 463.77) * mm});
            skLineSegment(sketch, "E3449", {"start": v(-2150.84, 463.77) * mm, "end": v(-2143.29, 490.48) * mm});
            skLineSegment(sketch, "E3450", {"start": v(-2143.29, 490.48) * mm, "end": v(-2136.72, 516.31) * mm});
            skLineSegment(sketch, "E3451", {"start": v(-2136.72, 516.31) * mm, "end": v(-2131.1, 541.23) * mm});
            skLineSegment(sketch, "E3452", {"start": v(-2131.1, 541.23) * mm, "end": v(-2126.36, 565.22) * mm});
            skLineSegment(sketch, "E3453", {"start": v(-2126.36, 565.22) * mm, "end": v(-2122.44, 588.23) * mm});
            skLineSegment(sketch, "E3454", {"start": v(-2122.44, 588.23) * mm, "end": v(-2119.3, 610.24) * mm});
            skLineSegment(sketch, "E3455", {"start": v(-2119.3, 610.24) * mm, "end": v(-2116.9, 631.24) * mm});
            skLineSegment(sketch, "E3456", {"start": v(-2116.9, 631.24) * mm, "end": v(-2115.14, 651.2) * mm});
            skLineSegment(sketch, "E3457", {"start": v(-2115.14, 651.2) * mm, "end": v(-2113.98, 670.09) * mm});
            skLineSegment(sketch, "E3458", {"start": v(-2113.98, 670.09) * mm, "end": v(-2113.37, 687.9) * mm});
            skLineSegment(sketch, "E3459", {"start": v(-2113.37, 687.9) * mm, "end": v(-2113.25, 704.62) * mm});
            skLineSegment(sketch, "E3460", {"start": v(-2113.25, 704.62) * mm, "end": v(-2113.56, 720.23) * mm});
            skLineSegment(sketch, "E3461", {"start": v(-2113.56, 720.23) * mm, "end": v(-2114.23, 734.73) * mm});
            skLineSegment(sketch, "E3462", {"start": v(-2114.23, 734.73) * mm, "end": v(-2115.21, 748.1) * mm});
            skLineSegment(sketch, "E3463", {"start": v(-2115.21, 748.1) * mm, "end": v(-2116.44, 760.35) * mm});
            skLineSegment(sketch, "E3464", {"start": v(-2116.44, 760.35) * mm, "end": v(-2117.86, 771.46) * mm});
            skLineSegment(sketch, "E3465", {"start": v(-2117.86, 771.46) * mm, "end": v(-2119.4, 781.44) * mm});
            skLineSegment(sketch, "E3466", {"start": v(-2119.4, 781.44) * mm, "end": v(-2121.02, 790.29) * mm});
            skLineSegment(sketch, "E3467", {"start": v(-2121.02, 790.29) * mm, "end": v(-2122.65, 798) * mm});
            skLineSegment(sketch, "E3468", {"start": v(-2122.65, 798) * mm, "end": v(-2124.22, 804.6) * mm});
            skLineSegment(sketch, "E3469", {"start": v(-2124.22, 804.6) * mm, "end": v(-2125.69, 810.1) * mm});
            skLineSegment(sketch, "E3470", {"start": v(-2125.69, 810.1) * mm, "end": v(-2126.99, 814.5) * mm});
            skLineSegment(sketch, "E3471", {"start": v(-2126.99, 814.5) * mm, "end": v(-2128.06, 817.8) * mm});
            skLineSegment(sketch, "E3472", {"start": v(-2128.06, 817.8) * mm, "end": v(-2128.86, 820.03) * mm});
            skLineSegment(sketch, "E3473", {"start": v(-2128.86, 820.03) * mm, "end": v(-2129.31, 821.22) * mm});
            skLineSegment(sketch, "E3474", {"start": v(-2129.31, 821.22) * mm, "end": v(-2196.28, 979.77) * mm});
            skLineSegment(sketch, "E3475", {"start": v(-2196.28, 979.77) * mm, "end": v(-1953.11, 1113.22) * mm});
            skLineSegment(sketch, "E3476", {"start": v(-1953.11, 1113.22) * mm, "end": v(-1855.34, 971.57) * mm});
            skLineSegment(sketch, "E3477", {"start": v(-1855.34, 971.57) * mm, "end": v(-1854.58, 970.55) * mm});
            skLineSegment(sketch, "E3478", {"start": v(-1854.58, 970.55) * mm, "end": v(-1853.12, 968.68) * mm});
            skLineSegment(sketch, "E3479", {"start": v(-1853.12, 968.68) * mm, "end": v(-1850.91, 966) * mm});
            skLineSegment(sketch, "E3480", {"start": v(-1850.91, 966) * mm, "end": v(-1847.9, 962.54) * mm});
            skLineSegment(sketch, "E3481", {"start": v(-1847.9, 962.54) * mm, "end": v(-1844.06, 958.36) * mm});
            skLineSegment(sketch, "E3482", {"start": v(-1844.06, 958.36) * mm, "end": v(-1839.34, 953.48) * mm});
            skLineSegment(sketch, "E3483", {"start": v(-1839.34, 953.48) * mm, "end": v(-1833.7, 947.97) * mm});
            skLineSegment(sketch, "E3484", {"start": v(-1833.7, 947.97) * mm, "end": v(-1827.1, 941.85) * mm});
            skLineSegment(sketch, "E3485", {"start": v(-1827.1, 941.85) * mm, "end": v(-1819.51, 935.19) * mm});
            skLineSegment(sketch, "E3486", {"start": v(-1819.51, 935.19) * mm, "end": v(-1810.9, 928.02) * mm});
            skLineSegment(sketch, "E3487", {"start": v(-1810.9, 928.02) * mm, "end": v(-1801.23, 920.41) * mm});
            skLineSegment(sketch, "E3488", {"start": v(-1801.23, 920.41) * mm, "end": v(-1790.48, 912.4) * mm});
            skLineSegment(sketch, "E3489", {"start": v(-1790.48, 912.4) * mm, "end": v(-1778.61, 904.05) * mm});
            skLineSegment(sketch, "E3490", {"start": v(-1778.61, 904.05) * mm, "end": v(-1765.6, 895.4) * mm});
            skLineSegment(sketch, "E3491", {"start": v(-1765.6, 895.4) * mm, "end": v(-1751.44, 886.53) * mm});
            skLineSegment(sketch, "E3492", {"start": v(-1751.44, 886.53) * mm, "end": v(-1736.08, 877.47) * mm});
            skLineSegment(sketch, "E3493", {"start": v(-1736.08, 877.47) * mm, "end": v(-1719.53, 868.3) * mm});
            skLineSegment(sketch, "E3494", {"start": v(-1719.53, 868.3) * mm, "end": v(-1701.75, 859.06) * mm});
            skLineSegment(sketch, "E3495", {"start": v(-1701.75, 859.06) * mm, "end": v(-1682.74, 849.83) * mm});
            skLineSegment(sketch, "E3496", {"start": v(-1682.74, 849.83) * mm, "end": v(-1662.49, 840.65) * mm});
            skLineSegment(sketch, "E3497", {"start": v(-1662.49, 840.65) * mm, "end": v(-1640.98, 831.59) * mm});
            skLineSegment(sketch, "E3498", {"start": v(-1640.98, 831.59) * mm, "end": v(-1618.2, 822.7) * mm});
            skLineSegment(sketch, "E3499", {"start": v(-1618.2, 822.7) * mm, "end": v(-1594.16, 814.06) * mm});
            skLineSegment(sketch, "E3500", {"start": v(-1594.16, 814.06) * mm, "end": v(-1568.84, 805.73) * mm});
            skLineSegment(sketch, "E3501", {"start": v(-1568.84, 805.73) * mm, "end": v(-1542.25, 797.76) * mm});
            skLineSegment(sketch, "E3502", {"start": v(-1542.25, 797.76) * mm, "end": v(-1514.4, 790.22) * mm});
            skLineSegment(sketch, "E3503", {"start": v(-1514.4, 790.22) * mm, "end": v(-1486.28, 784.34) * mm});
            skLineSegment(sketch, "E3504", {"start": v(-1486.28, 784.34) * mm, "end": v(-1386.39, 876.22) * mm});
            skLineSegment(sketch, "E3505", {"start": v(-1386.39, 876.22) * mm, "end": v(-1389.9, 904.72) * mm});
            skLineSegment(sketch, "E3506", {"start": v(-1389.9, 904.72) * mm, "end": v(-1395.08, 933.11) * mm});
            skLineSegment(sketch, "E3507", {"start": v(-1395.08, 933.11) * mm, "end": v(-1400.8, 960.27) * mm});
            skLineSegment(sketch, "E3508", {"start": v(-1400.8, 960.27) * mm, "end": v(-1407, 986.2) * mm});
            skLineSegment(sketch, "E3509", {"start": v(-1407, 986.2) * mm, "end": v(-1413.6, 1010.88) * mm});
            skLineSegment(sketch, "E3510", {"start": v(-1413.6, 1010.88) * mm, "end": v(-1420.54, 1034.31) * mm});
            skLineSegment(sketch, "E3511", {"start": v(-1420.54, 1034.31) * mm, "end": v(-1427.77, 1056.51) * mm});
            skLineSegment(sketch, "E3512", {"start": v(-1427.77, 1056.51) * mm, "end": v(-1435.22, 1077.46) * mm});
            skLineSegment(sketch, "E3513", {"start": v(-1435.22, 1077.46) * mm, "end": v(-1442.84, 1097.17) * mm});
            skLineSegment(sketch, "E3514", {"start": v(-1442.84, 1097.17) * mm, "end": v(-1450.56, 1115.66) * mm});
            skLineSegment(sketch, "E3515", {"start": v(-1450.56, 1115.66) * mm, "end": v(-1458.32, 1132.92) * mm});
            skLineSegment(sketch, "E3516", {"start": v(-1458.32, 1132.92) * mm, "end": v(-1466.06, 1148.98) * mm});
            skLineSegment(sketch, "E3517", {"start": v(-1466.06, 1148.98) * mm, "end": v(-1473.72, 1163.84) * mm});
            skLineSegment(sketch, "E3518", {"start": v(-1473.72, 1163.84) * mm, "end": v(-1481.25, 1177.52) * mm});
            skLineSegment(sketch, "E3519", {"start": v(-1481.25, 1177.52) * mm, "end": v(-1488.58, 1190.05) * mm});
            skLineSegment(sketch, "E3520", {"start": v(-1488.58, 1190.05) * mm, "end": v(-1495.66, 1201.43) * mm});
            skLineSegment(sketch, "E3521", {"start": v(-1495.66, 1201.43) * mm, "end": v(-1502.44, 1211.7) * mm});
            skLineSegment(sketch, "E3522", {"start": v(-1502.44, 1211.7) * mm, "end": v(-1508.86, 1220.88) * mm});
            skLineSegment(sketch, "E3523", {"start": v(-1508.86, 1220.88) * mm, "end": v(-1514.87, 1229) * mm});
            skLineSegment(sketch, "E3524", {"start": v(-1514.87, 1229) * mm, "end": v(-1520.41, 1236.08) * mm});
            skLineSegment(sketch, "E3525", {"start": v(-1520.41, 1236.08) * mm, "end": v(-1525.44, 1242.17) * mm});
            skLineSegment(sketch, "E3526", {"start": v(-1525.44, 1242.17) * mm, "end": v(-1529.9, 1247.28) * mm});
            skLineSegment(sketch, "E3527", {"start": v(-1529.9, 1247.28) * mm, "end": v(-1533.75, 1251.46) * mm});
            skLineSegment(sketch, "E3528", {"start": v(-1533.75, 1251.46) * mm, "end": v(-1536.94, 1254.75) * mm});
            skLineSegment(sketch, "E3529", {"start": v(-1536.94, 1254.75) * mm, "end": v(-1539.43, 1257.17) * mm});
            skLineSegment(sketch, "E3530", {"start": v(-1539.43, 1257.17) * mm, "end": v(-1541.17, 1258.79) * mm});
            skLineSegment(sketch, "E3531", {"start": v(-1541.17, 1258.79) * mm, "end": v(-1542.13, 1259.62) * mm});
            skLineSegment(sketch, "E3532", {"start": v(-1542.13, 1259.62) * mm, "end": v(-1675.1, 1368.89) * mm});
            skLineSegment(sketch, "E3533", {"start": v(-1675.1, 1368.89) * mm, "end": v(-1521.81, 1600.06) * mm});
            skLineSegment(sketch, "E3534", {"start": v(-1521.81, 1600.06) * mm, "end": v(-1369.41, 1520.08) * mm});
            skLineSegment(sketch, "E3535", {"start": v(-1369.41, 1520.08) * mm, "end": v(-1368.27, 1519.52) * mm});
            skLineSegment(sketch, "E3536", {"start": v(-1368.27, 1519.52) * mm, "end": v(-1366.1, 1518.55) * mm});
            skLineSegment(sketch, "E3537", {"start": v(-1366.1, 1518.55) * mm, "end": v(-1362.9, 1517.2) * mm});
            skLineSegment(sketch, "E3538", {"start": v(-1362.9, 1517.2) * mm, "end": v(-1358.63, 1515.54) * mm});
            skLineSegment(sketch, "E3539", {"start": v(-1358.63, 1515.54) * mm, "end": v(-1353.28, 1513.62) * mm});
            skLineSegment(sketch, "E3540", {"start": v(-1353.28, 1513.62) * mm, "end": v(-1346.84, 1511.5) * mm});
            skLineSegment(sketch, "E3541", {"start": v(-1346.84, 1511.5) * mm, "end": v(-1339.28, 1509.23) * mm});
            skLineSegment(sketch, "E3542", {"start": v(-1339.28, 1509.23) * mm, "end": v(-1330.6, 1506.88) * mm});
            skLineSegment(sketch, "E3543", {"start": v(-1330.6, 1506.88) * mm, "end": v(-1320.78, 1504.5) * mm});
            skLineSegment(sketch, "E3544", {"start": v(-1320.78, 1504.5) * mm, "end": v(-1309.82, 1502.17) * mm});
            skLineSegment(sketch, "E3545", {"start": v(-1309.82, 1502.17) * mm, "end": v(-1297.73, 1499.92) * mm});
            skLineSegment(sketch, "E3546", {"start": v(-1297.73, 1499.92) * mm, "end": v(-1284.48, 1497.82) * mm});
            skLineSegment(sketch, "E3547", {"start": v(-1284.48, 1497.82) * mm, "end": v(-1270.1, 1495.94) * mm});
            skLineSegment(sketch, "E3548", {"start": v(-1270.1, 1495.94) * mm, "end": v(-1254.56, 1494.33) * mm});
            skLineSegment(sketch, "E3549", {"start": v(-1254.56, 1494.33) * mm, "end": v(-1237.89, 1493.06) * mm});
            skLineSegment(sketch, "E3550", {"start": v(-1237.89, 1493.06) * mm, "end": v(-1220.08, 1492.17) * mm});
            skLineSegment(sketch, "E3551", {"start": v(-1220.08, 1492.17) * mm, "end": v(-1201.16, 1491.74) * mm});
            skLineSegment(sketch, "E3552", {"start": v(-1201.16, 1491.74) * mm, "end": v(-1181.13, 1491.83) * mm});
            skLineSegment(sketch, "E3553", {"start": v(-1181.13, 1491.83) * mm, "end": v(-1160, 1492.48) * mm});
            skLineSegment(sketch, "E3554", {"start": v(-1160, 1492.48) * mm, "end": v(-1137.8, 1493.77) * mm});
            skLineSegment(sketch, "E3555", {"start": v(-1137.8, 1493.77) * mm, "end": v(-1114.55, 1495.74) * mm});
            skLineSegment(sketch, "E3556", {"start": v(-1114.55, 1495.74) * mm, "end": v(-1090.25, 1498.46) * mm});
            skLineSegment(sketch, "E3557", {"start": v(-1090.25, 1498.46) * mm, "end": v(-1064.95, 1501.99) * mm});
            skLineSegment(sketch, "E3558", {"start": v(-1064.95, 1501.99) * mm, "end": v(-1038.66, 1506.37) * mm});
            skLineSegment(sketch, "E3559", {"start": v(-1038.66, 1506.37) * mm, "end": v(-1011.41, 1511.67) * mm});
            skLineSegment(sketch, "E3560", {"start": v(-1011.41, 1511.67) * mm, "end": v(-983.24, 1517.94) * mm});
            skLineSegment(sketch, "E3561", {"start": v(-983.24, 1517.94) * mm, "end": v(-955.62, 1525.8) * mm});
            skLineSegment(sketch, "E3562", {"start": v(-955.62, 1525.8) * mm, "end": v(-909.86, 1653.57) * mm});
            skLineSegment(sketch, "E3563", {"start": v(-909.86, 1653.57) * mm, "end": v(-926.2, 1677.19) * mm});
            skLineSegment(sketch, "E3564", {"start": v(-926.2, 1677.19) * mm, "end": v(-944, 1699.91) * mm});
            skLineSegment(sketch, "E3565", {"start": v(-944, 1699.91) * mm, "end": v(-961.68, 1721.3) * mm});
            skLineSegment(sketch, "E3566", {"start": v(-961.68, 1721.3) * mm, "end": v(-979.21, 1741.38) * mm});
            skLineSegment(sketch, "E3567", {"start": v(-979.21, 1741.38) * mm, "end": v(-996.53, 1760.17) * mm});
            skLineSegment(sketch, "E3568", {"start": v(-996.53, 1760.17) * mm, "end": v(-1013.57, 1777.7) * mm});
            skLineSegment(sketch, "E3569", {"start": v(-1013.57, 1777.7) * mm, "end": v(-1030.29, 1793.98) * mm});
            skLineSegment(sketch, "E3570", {"start": v(-1030.29, 1793.98) * mm, "end": v(-1046.62, 1809.07) * mm});
            skLineSegment(sketch, "E3571", {"start": v(-1046.62, 1809.07) * mm, "end": v(-1062.53, 1822.99) * mm});
            skLineSegment(sketch, "E3572", {"start": v(-1062.53, 1822.99) * mm, "end": v(-1077.96, 1835.77) * mm});
            skLineSegment(sketch, "E3573", {"start": v(-1077.96, 1835.77) * mm, "end": v(-1092.85, 1847.45) * mm});
            skLineSegment(sketch, "E3574", {"start": v(-1092.85, 1847.45) * mm, "end": v(-1107.16, 1858.07) * mm});
            skLineSegment(sketch, "E3575", {"start": v(-1107.16, 1858.07) * mm, "end": v(-1120.85, 1867.67) * mm});
            skLineSegment(sketch, "E3576", {"start": v(-1120.85, 1867.67) * mm, "end": v(-1133.88, 1876.29) * mm});
            skLineSegment(sketch, "E3577", {"start": v(-1133.88, 1876.29) * mm, "end": v(-1146.2, 1883.97) * mm});
            skLineSegment(sketch, "E3578", {"start": v(-1146.2, 1883.97) * mm, "end": v(-1157.75, 1890.76) * mm});
            skLineSegment(sketch, "E3579", {"start": v(-1157.75, 1890.76) * mm, "end": v(-1168.53, 1896.7) * mm});
            skLineSegment(sketch, "E3580", {"start": v(-1168.53, 1896.7) * mm, "end": v(-1178.48, 1901.84) * mm});
            skLineSegment(sketch, "E3581", {"start": v(-1178.48, 1901.84) * mm, "end": v(-1187.57, 1906.24) * mm});
            skLineSegment(sketch, "E3582", {"start": v(-1187.57, 1906.24) * mm, "end": v(-1195.77, 1909.94) * mm});
            skLineSegment(sketch, "E3583", {"start": v(-1195.77, 1909.94) * mm, "end": v(-1203.05, 1912.99) * mm});
            skLineSegment(sketch, "E3584", {"start": v(-1203.05, 1912.99) * mm, "end": v(-1209.38, 1915.44) * mm});
            skLineSegment(sketch, "E3585", {"start": v(-1209.38, 1915.44) * mm, "end": v(-1214.73, 1917.36) * mm});
            skLineSegment(sketch, "E3586", {"start": v(-1214.73, 1917.36) * mm, "end": v(-1219.08, 1918.78) * mm});
            skLineSegment(sketch, "E3587", {"start": v(-1219.08, 1918.78) * mm, "end": v(-1222.41, 1919.77) * mm});
            skLineSegment(sketch, "E3588", {"start": v(-1222.41, 1919.77) * mm, "end": v(-1224.7, 1920.4) * mm});
            skLineSegment(sketch, "E3589", {"start": v(-1224.7, 1920.4) * mm, "end": v(-1225.94, 1920.69) * mm});
            skLineSegment(sketch, "E3590", {"start": v(-1225.94, 1920.69) * mm, "end": v(-1394.47, 1955.64) * mm});
            skLineSegment(sketch, "E3591", {"start": v(-1394.47, 1955.64) * mm, "end": v(-1366.16, 2231.57) * mm});
            skLineSegment(sketch, "E3592", {"start": v(-1366.16, 2231.57) * mm, "end": v(-1194.04, 2231.57) * mm});
            skLineSegment(sketch, "E3593", {"start": v(-1194.04, 2231.57) * mm, "end": v(-1192.77, 2231.62) * mm});
            skLineSegment(sketch, "E3594", {"start": v(-1192.77, 2231.62) * mm, "end": v(-1190.4, 2231.75) * mm});
            skLineSegment(sketch, "E3595", {"start": v(-2521.86, 2231.57) * mm, "end": v(-2928.26, 2231.57) * mm});
            skFitSpline(sketch, "E3596", {"points": [v(-990.38, 2461.01) * mm, v(-990.38, 2405.95) * mm, v(-1035.02, 2361.32) * mm, v(-1090.08, 2361.32) * mm]});
            skFitSpline(sketch, "E3597", {"points": [v(-1090.08, 2361.32) * mm, v(-1145.14, 2361.32) * mm, v(-1189.77, 2405.95) * mm, v(-1189.77, 2461.01) * mm]});
            skFitSpline(sketch, "E3598", {"points": [v(-1189.77, 2461.01) * mm, v(-1189.77, 2516.07) * mm, v(-1145.14, 2560.7) * mm, v(-1090.08, 2560.7) * mm]});
            skFitSpline(sketch, "E3599", {"points": [v(-1090.08, 2560.7) * mm, v(-1035.02, 2560.7) * mm, v(-990.38, 2516.07) * mm, v(-990.38, 2461.01) * mm]});
            skLineSegment(sketch, "E3600", {"start": v(-2725.06, 2028.37) * mm, "end": v(-2725.06, 2434.77) * mm});
            skLineSegment(sketch, "E3601", {"start": v(-3391.55, 3048.23) * mm, "end": v(-3414.92, 3028.52) * mm});
            skLineSegment(sketch, "E3602", {"start": v(-3414.92, 3028.52) * mm, "end": v(-3437.68, 3008.2) * mm});
            skLineSegment(sketch, "E3603", {"start": v(-3437.68, 3008.2) * mm, "end": v(-3459.83, 2987.27) * mm});
            skLineSegment(sketch, "E3604", {"start": v(-3459.83, 2987.27) * mm, "end": v(-3481.37, 2965.73) * mm});
            skLineSegment(sketch, "E3605", {"start": v(-3396.43, 2963.3) * mm, "end": v(-3478.93, 3053.1) * mm});
            skLineSegment(sketch, "E3606", {"start": v(-3430.16, 3095.37) * mm, "end": v(-3434.83, 3051.48) * mm});
            skLineSegment(sketch, "E3607", {"start": v(-3434.83, 3051.48) * mm, "end": v(-3437.68, 3008.2) * mm});
            skLineSegment(sketch, "E3608", {"start": v(-3437.68, 3008.2) * mm, "end": v(-3438.7, 2965.53) * mm});
            skLineSegment(sketch, "E3609", {"start": v(-3438.7, 2965.53) * mm, "end": v(-3437.68, 2923.26) * mm});
            skLineSegment(sketch, "E3610", {"start": v(-3353.15, 3000.89) * mm, "end": v(-3395, 3005.56) * mm});
            skLineSegment(sketch, "E3611", {"start": v(-3395, 3005.56) * mm, "end": v(-3437.68, 3008.2) * mm});
            skLineSegment(sketch, "E3612", {"start": v(-3437.68, 3008.2) * mm, "end": v(-3481.16, 3009.22) * mm});
            skLineSegment(sketch, "E3613", {"start": v(-3481.16, 3009.22) * mm, "end": v(-3525.26, 3008.2) * mm});
            skLineSegment(sketch, "E3614", {"start": v(-3285.48, 3230.7) * mm, "end": v(-3314.13, 3214.04) * mm});
            skLineSegment(sketch, "E3615", {"start": v(-3314.13, 3214.04) * mm, "end": v(-3342.18, 3196.57) * mm});
            skLineSegment(sketch, "E3616", {"start": v(-3342.18, 3196.57) * mm, "end": v(-3369.81, 3178.48) * mm});
            skLineSegment(sketch, "E3617", {"start": v(-3369.81, 3178.48) * mm, "end": v(-3397.04, 3159.38) * mm});
            skLineSegment(sketch, "E3618", {"start": v(-3397.04, 3159.38) * mm, "end": v(-3361.28, 3110) * mm});
            skLineSegment(sketch, "E3619", {"start": v(-3361.28, 3110) * mm, "end": v(-3335.47, 3128.09) * mm});
            skLineSegment(sketch, "E3620", {"start": v(-3335.47, 3128.09) * mm, "end": v(-3309.46, 3145.36) * mm});
            skLineSegment(sketch, "E3621", {"start": v(-3309.46, 3145.36) * mm, "end": v(-3282.64, 3161.82) * mm});
            skLineSegment(sketch, "E3622", {"start": v(-3282.64, 3161.82) * mm, "end": v(-3240.78, 3150.85) * mm});
            skLineSegment(sketch, "E3623", {"start": v(-3240.78, 3150.85) * mm, "end": v(-3210.9, 3097.81) * mm});
            skLineSegment(sketch, "E3624", {"start": v(-3210.9, 3097.81) * mm, "end": v(-3220.05, 3057.17) * mm});
            skLineSegment(sketch, "E3625", {"start": v(-3220.05, 3057.17) * mm, "end": v(-3243.62, 3042.54) * mm});
            skLineSegment(sketch, "E3626", {"start": v(-3243.62, 3042.54) * mm, "end": v(-3267, 3027.3) * mm});
            skLineSegment(sketch, "E3627", {"start": v(-3267, 3027.3) * mm, "end": v(-3307.63, 3035.84) * mm});
            skLineSegment(sketch, "E3628", {"start": v(-2944.92, 3355.88) * mm, "end": v(-2909.77, 3176.25) * mm});
            skLineSegment(sketch, "E3629", {"start": v(-2909.77, 3176.25) * mm, "end": v(-2947.15, 3215.26) * mm});
            skLineSegment(sketch, "E3630", {"start": v(-2947.15, 3215.26) * mm, "end": v(-2986.78, 3252.65) * mm});
            skLineSegment(sketch, "E3631", {"start": v(-2986.78, 3252.65) * mm, "end": v(-3028.84, 3288.62) * mm});
            skLineSegment(sketch, "E3632", {"start": v(-3028.84, 3288.62) * mm, "end": v(-3073.14, 3322.96) * mm});
            skLineSegment(sketch, "E3633", {"start": v(-3073.14, 3322.96) * mm, "end": v(-3017.46, 3148.82) * mm});
            skLineSegment(sketch, "E3634", {"start": v(-2746.19, 3315.85) * mm, "end": v(-2777.69, 3314.83) * mm});
            skLineSegment(sketch, "E3635", {"start": v(-2777.69, 3314.83) * mm, "end": v(-2808.98, 3313) * mm});
            skLineSegment(sketch, "E3636", {"start": v(-2808.98, 3313) * mm, "end": v(-2840.07, 3309.95) * mm});
            skLineSegment(sketch, "E3637", {"start": v(-2840.07, 3309.95) * mm, "end": v(-2871.36, 3306.3) * mm});
            skLineSegment(sketch, "E3638", {"start": v(-2745.17, 3255.09) * mm, "end": v(-2774.64, 3254.07) * mm});
            skLineSegment(sketch, "E3639", {"start": v(-2774.64, 3254.07) * mm, "end": v(-2804.1, 3252.04) * mm});
            skLineSegment(sketch, "E3640", {"start": v(-2804.1, 3252.04) * mm, "end": v(-2833.77, 3249.4) * mm});
            skLineSegment(sketch, "E3641", {"start": v(-2833.77, 3249.4) * mm, "end": v(-2863.03, 3245.95) * mm});
            skLineSegment(sketch, "E3642", {"start": v(-2682.38, 3345.72) * mm, "end": v(-2648.25, 3374.57) * mm});
            skLineSegment(sketch, "E3643", {"start": v(-2648.25, 3374.57) * mm, "end": v(-2660.44, 3192.1) * mm});
            skLineSegment(sketch, "E3644", {"start": v(-2632.6, 3189.86) * mm, "end": v(-2660.44, 3192.1) * mm});
            skLineSegment(sketch, "E3645", {"start": v(-2660.44, 3192.1) * mm, "end": v(-2688.28, 3193.52) * mm});
            skLineSegment(sketch, "E3646", {"start": v(-2554.17, 3333.52) * mm, "end": v(-2516.78, 3358.11) * mm});
            skLineSegment(sketch, "E3647", {"start": v(-2516.78, 3358.11) * mm, "end": v(-2484.26, 3351.6) * mm});
            skLineSegment(sketch, "E3648", {"start": v(-2484.26, 3351.6) * mm, "end": v(-2451.96, 3344.1) * mm});
            skLineSegment(sketch, "E3649", {"start": v(-2451.96, 3344.1) * mm, "end": v(-2427.98, 3306.3) * mm});
            skLineSegment(sketch, "E3650", {"start": v(-2427.98, 3306.3) * mm, "end": v(-2436.1, 3277.04) * mm});
            skLineSegment(sketch, "E3651", {"start": v(-2436.1, 3277.04) * mm, "end": v(-2473.9, 3255.3) * mm});
            skLineSegment(sketch, "E3652", {"start": v(-2473.9, 3255.3) * mm, "end": v(-2452.36, 3218.31) * mm});
            skLineSegment(sketch, "E3653", {"start": v(-2452.36, 3218.31) * mm, "end": v(-2460.5, 3188.85) * mm});
            skLineSegment(sketch, "E3654", {"start": v(-2460.5, 3188.85) * mm, "end": v(-2495.64, 3166.5) * mm});
            skLineSegment(sketch, "E3655", {"start": v(-2495.64, 3166.5) * mm, "end": v(-2522.67, 3172.8) * mm});
            skLineSegment(sketch, "E3656", {"start": v(-2522.67, 3172.8) * mm, "end": v(-2550.1, 3178.28) * mm});
            skLineSegment(sketch, "E3657", {"start": v(-2550.1, 3178.28) * mm, "end": v(-2572.86, 3213.03) * mm});
            skLineSegment(sketch, "E3658", {"start": v(-2503.57, 3262.2) * mm, "end": v(-2473.9, 3255.3) * mm});
            skLineSegment(sketch, "E3659", {"start": v(-2245.7, 3170.36) * mm, "end": v(-2218.89, 3156.13) * mm});
            skLineSegment(sketch, "E3660", {"start": v(-2218.89, 3156.13) * mm, "end": v(-2192.27, 3141.1) * mm});
            skLineSegment(sketch, "E3661", {"start": v(-2192.27, 3141.1) * mm, "end": v(-2166.26, 3125.45) * mm});
            skLineSegment(sketch, "E3662", {"start": v(-2166.26, 3125.45) * mm, "end": v(-2123.79, 3134.19) * mm});
            skLineSegment(sketch, "E3663", {"start": v(-2123.79, 3134.19) * mm, "end": v(-2106.92, 3159.59) * mm});
            skLineSegment(sketch, "E3664", {"start": v(-2106.92, 3159.59) * mm, "end": v(-2117.7, 3202.87) * mm});
            skLineSegment(sketch, "E3665", {"start": v(-2117.7, 3202.87) * mm, "end": v(-2146.14, 3220.14) * mm});
            skLineSegment(sketch, "E3666", {"start": v(-2146.14, 3220.14) * mm, "end": v(-2175, 3236.4) * mm});
            skLineSegment(sketch, "E3667", {"start": v(-2175, 3236.4) * mm, "end": v(-2204.26, 3251.84) * mm});
            skLineSegment(sketch, "E3668", {"start": v(-2204.26, 3251.84) * mm, "end": v(-2287.36, 3089.08) * mm});
            skLineSegment(sketch, "E3669", {"start": v(-2145.94, 3000.48) * mm, "end": v(-2072.58, 3098.02) * mm});
            skLineSegment(sketch, "E3670", {"start": v(-2054.3, 3122.2) * mm, "end": v(-2036, 3146.58) * mm});
            skLineSegment(sketch, "E3671", {"start": v(-1999.63, 2909.85) * mm, "end": v(-2041.09, 2909.04) * mm});
            skLineSegment(sketch, "E3672", {"start": v(-2041.09, 2909.04) * mm, "end": v(-2040.07, 2950.7) * mm});
            skLineSegment(sketch, "E3673", {"start": v(-2040.07, 2950.7) * mm, "end": v(-1934.81, 3061.03) * mm});
            skLineSegment(sketch, "E3674", {"start": v(-1932.78, 2972.24) * mm, "end": v(-1954.52, 2994.8) * mm});
            skLineSegment(sketch, "E3675", {"start": v(-1954.52, 2994.8) * mm, "end": v(-1976.87, 3016.94) * mm});
            skLineSegment(sketch, "E3676", {"start": v(-1976.87, 3016.94) * mm, "end": v(-2000.04, 3038.07) * mm});
            skLineSegment(sketch, "E3677", {"start": v(-2000.04, 3038.07) * mm, "end": v(-2023.61, 3058.8) * mm});
            skLineSegment(sketch, "E3678", {"start": v(-1918.96, 2757.86) * mm, "end": v(-1934.4, 2780.82) * mm});
            skLineSegment(sketch, "E3679", {"start": v(-1934.4, 2780.82) * mm, "end": v(-1950.66, 2803.58) * mm});
            skLineSegment(sketch, "E3680", {"start": v(-1950.66, 2803.58) * mm, "end": v(-1967.53, 2825.73) * mm});
            skLineSegment(sketch, "E3681", {"start": v(-1967.53, 2825.73) * mm, "end": v(-1961.63, 2866.77) * mm});
            skLineSegment(sketch, "E3682", {"start": v(-1961.63, 2866.77) * mm, "end": v(-1914.7, 2905.79) * mm});
            skLineSegment(sketch, "E3683", {"start": v(-1914.7, 2905.79) * mm, "end": v(-1871.62, 2900.91) * mm});
            skLineSegment(sketch, "E3684", {"start": v(-1871.62, 2900.91) * mm, "end": v(-1852.72, 2875.92) * mm});
            skLineSegment(sketch, "E3685", {"start": v(-1852.72, 2875.92) * mm, "end": v(-1834.43, 2850.52) * mm});
            skLineSegment(sketch, "E3686", {"start": v(-1834.43, 2850.52) * mm, "end": v(-1816.75, 2824.5) * mm});
            skLineSegment(sketch, "E3687", {"start": v(-1837.07, 2740.59) * mm, "end": v(-1795.82, 2729.2) * mm});
            skLineSegment(sketch, "E3688", {"start": v(-1795.82, 2729.2) * mm, "end": v(-1754.57, 2715.6) * mm});
            skLineSegment(sketch, "E3689", {"start": v(-1754.57, 2715.6) * mm, "end": v(-1740.96, 2687.35) * mm});
            skLineSegment(sketch, "E3690", {"start": v(-1740.96, 2687.35) * mm, "end": v(-1756.2, 2646.7) * mm});
            skLineSegment(sketch, "E3691", {"start": v(-1756.2, 2646.7) * mm, "end": v(-1840.12, 2610.74) * mm});
            skLineSegment(sketch, "E3692", {"start": v(-1889.9, 2710.31) * mm, "end": v(-1731.2, 2801.34) * mm});
            skLineSegment(sketch, "E3693", {"start": v(-1782, 2425.02) * mm, "end": v(-1776.93, 2397.79) * mm});
            skLineSegment(sketch, "E3694", {"start": v(-1776.93, 2397.79) * mm, "end": v(-1772.46, 2370.36) * mm});
            skLineSegment(sketch, "E3695", {"start": v(-1772.46, 2370.36) * mm, "end": v(-1768.8, 2342.72) * mm});
            skLineSegment(sketch, "E3696", {"start": v(-1768.8, 2342.72) * mm, "end": v(-1735.68, 2317.52) * mm});
            skLineSegment(sketch, "E3697", {"start": v(-1735.68, 2317.52) * mm, "end": v(-1614.16, 2328.1) * mm});
            skLineSegment(sketch, "E3698", {"start": v(-1614.16, 2328.1) * mm, "end": v(-1587.14, 2363.85) * mm});
            skLineSegment(sketch, "E3699", {"start": v(-1587.14, 2363.85) * mm, "end": v(-1591.4, 2396.57) * mm});
            skLineSegment(sketch, "E3700", {"start": v(-1591.4, 2396.57) * mm, "end": v(-1596.69, 2429.28) * mm});
            skLineSegment(sketch, "E3701", {"start": v(-1596.69, 2429.28) * mm, "end": v(-1602.99, 2461.8) * mm});
            skLineSegment(sketch, "E3702", {"start": v(-1596.69, 2429.28) * mm, "end": v(-1776.93, 2397.79) * mm});
            skLineSegment(sketch, "E3703", {"start": v(-1644.64, 2137.7) * mm, "end": v(-1642.2, 2168.78) * mm});
            skLineSegment(sketch, "E3704", {"start": v(-1642.2, 2168.78) * mm, "end": v(-1640.98, 2200.28) * mm});
            skLineSegment(sketch, "E3705", {"start": v(-1640.98, 2200.28) * mm, "end": v(-1640.58, 2231.57) * mm});
            skLineSegment(sketch, "E3706", {"start": v(-1640.58, 2231.57) * mm, "end": v(-1640.98, 2262.86) * mm});
            skLineSegment(sketch, "E3707", {"start": v(-1705.2, 2142.98) * mm, "end": v(-1703.16, 2172.44) * mm});
            skLineSegment(sketch, "E3708", {"start": v(-1703.16, 2172.44) * mm, "end": v(-1701.94, 2201.9) * mm});
            skLineSegment(sketch, "E3709", {"start": v(-1701.94, 2201.9) * mm, "end": v(-1701.54, 2231.57) * mm});
            skLineSegment(sketch, "E3710", {"start": v(-1701.54, 2231.57) * mm, "end": v(-1701.94, 2261.24) * mm});
            skLineSegment(sketch, "E3711", {"start": v(-1621.68, 2070.84) * mm, "end": v(-1596.69, 2033.86) * mm});
            skLineSegment(sketch, "E3712", {"start": v(-1596.69, 2033.86) * mm, "end": v(-1602.99, 2001.35) * mm});
            skLineSegment(sketch, "E3713", {"start": v(-1602.99, 2001.35) * mm, "end": v(-1610.1, 1969.04) * mm});
            skLineSegment(sketch, "E3714", {"start": v(-1610.1, 1969.04) * mm, "end": v(-1647.49, 1944.65) * mm});
            skLineSegment(sketch, "E3715", {"start": v(-1647.49, 1944.65) * mm, "end": v(-1676.95, 1952.58) * mm});
            skLineSegment(sketch, "E3716", {"start": v(-1676.95, 1952.58) * mm, "end": v(-1699.1, 1989.97) * mm});
            skLineSegment(sketch, "E3717", {"start": v(-1699.1, 1989.97) * mm, "end": v(-1735.88, 1968.22) * mm});
            skLineSegment(sketch, "E3718", {"start": v(-1735.88, 1968.22) * mm, "end": v(-1765.34, 1975.95) * mm});
            skLineSegment(sketch, "E3719", {"start": v(-1765.34, 1975.95) * mm, "end": v(-1788.1, 2010.9) * mm});
            skLineSegment(sketch, "E3720", {"start": v(-1788.1, 2010.9) * mm, "end": v(-1782, 2038.12) * mm});
            skLineSegment(sketch, "E3721", {"start": v(-1782, 2038.12) * mm, "end": v(-1776.93, 2065.35) * mm});
            skLineSegment(sketch, "E3722", {"start": v(-1776.93, 2065.35) * mm, "end": v(-1742.18, 2088.52) * mm});
            skLineSegment(sketch, "E3723", {"start": v(-1692.4, 2019.63) * mm, "end": v(-1699.1, 1989.97) * mm});
            skLineSegment(sketch, "E3724", {"start": v(-1781.8, 1921.08) * mm, "end": v(-1810.66, 1930.43) * mm});
            skLineSegment(sketch, "E3725", {"start": v(-1876.3, 1777.22) * mm, "end": v(-1863.7, 1802) * mm});
            skLineSegment(sketch, "E3726", {"start": v(-1863.7, 1802) * mm, "end": v(-1851.5, 1827) * mm});
            skLineSegment(sketch, "E3727", {"start": v(-1851.5, 1827) * mm, "end": v(-1840.12, 1852.4) * mm});
            skLineSegment(sketch, "E3728", {"start": v(-1840.12, 1852.4) * mm, "end": v(-1829.55, 1878.2) * mm});
            skLineSegment(sketch, "E3729", {"start": v(-1829.55, 1878.2) * mm, "end": v(-1772.86, 1855.85) * mm});
            skLineSegment(sketch, "E3730", {"start": v(-1772.86, 1855.85) * mm, "end": v(-1756.2, 1816.43) * mm});
            skLineSegment(sketch, "E3731", {"start": v(-1756.2, 1816.43) * mm, "end": v(-1768.6, 1788.6) * mm});
            skLineSegment(sketch, "E3732", {"start": v(-1768.6, 1788.6) * mm, "end": v(-1781.8, 1761.16) * mm});
            skLineSegment(sketch, "E3733", {"start": v(-1781.8, 1761.16) * mm, "end": v(-1768.8, 1719.71) * mm});
            skLineSegment(sketch, "E3734", {"start": v(-1768.8, 1719.71) * mm, "end": v(-1741.98, 1705.28) * mm});
            skLineSegment(sketch, "E3735", {"start": v(-1741.98, 1705.28) * mm, "end": v(-1699.91, 1720.32) * mm});
            skLineSegment(sketch, "E3736", {"start": v(-1699.91, 1720.32) * mm, "end": v(-1685.69, 1750.2) * mm});
            skLineSegment(sketch, "E3737", {"start": v(-1685.69, 1750.2) * mm, "end": v(-1672.07, 1780.47) * mm});
            skLineSegment(sketch, "E3738", {"start": v(-1672.07, 1780.47) * mm, "end": v(-1687.92, 1822.12) * mm});
            skLineSegment(sketch, "E3739", {"start": v(-1823.66, 1524.64) * mm, "end": v(-1803.54, 1551.05) * mm});
            skLineSegment(sketch, "E3740", {"start": v(-1803.54, 1551.05) * mm, "end": v(-1784.24, 1577.88) * mm});
            skLineSegment(sketch, "E3741", {"start": v(-1784.24, 1577.88) * mm, "end": v(-1765.75, 1605.3) * mm});
            skLineSegment(sketch, "E3742", {"start": v(-1765.75, 1605.3) * mm, "end": v(-1748.07, 1633.35) * mm});
            skLineSegment(sketch, "E3743", {"start": v(-1748.07, 1633.35) * mm, "end": v(-1800.1, 1665.25) * mm});
            skLineSegment(sketch, "E3744", {"start": v(-1800.1, 1665.25) * mm, "end": v(-1816.75, 1638.63) * mm});
            skLineSegment(sketch, "E3745", {"start": v(-1816.75, 1638.63) * mm, "end": v(-1834.43, 1612.62) * mm});
            skLineSegment(sketch, "E3746", {"start": v(-1834.43, 1612.62) * mm, "end": v(-1852.72, 1587.22) * mm});
            skLineSegment(sketch, "E3747", {"start": v(-1852.72, 1587.22) * mm, "end": v(-1895.6, 1581.13) * mm});
            skLineSegment(sketch, "E3748", {"start": v(-1895.6, 1581.13) * mm, "end": v(-1943.55, 1618.72) * mm});
            skLineSegment(sketch, "E3749", {"start": v(-1943.55, 1618.72) * mm, "end": v(-1950.66, 1659.56) * mm});
            skLineSegment(sketch, "E3750", {"start": v(-1950.66, 1659.56) * mm, "end": v(-1934.4, 1682.32) * mm});
            skLineSegment(sketch, "E3751", {"start": v(-1934.4, 1682.32) * mm, "end": v(-1918.96, 1705.28) * mm});
            skLineSegment(sketch, "E3752", {"start": v(-1918.96, 1705.28) * mm, "end": v(-1878.12, 1713) * mm});
            skLineSegment(sketch, "E3753", {"start": v(-2043.32, 1427.71) * mm, "end": v(-2066.9, 1408.2) * mm});
            skLineSegment(sketch, "E3754", {"start": v(-2066.9, 1408.2) * mm, "end": v(-2090.87, 1389.51) * mm});
            skLineSegment(sketch, "E3755", {"start": v(-2090.87, 1389.51) * mm, "end": v(-2115.46, 1371.63) * mm});
            skLineSegment(sketch, "E3756", {"start": v(-2115.46, 1371.63) * mm, "end": v(-2123.79, 1328.96) * mm});
            skLineSegment(sketch, "E3757", {"start": v(-2123.79, 1328.96) * mm, "end": v(-2106.92, 1303.56) * mm});
            skLineSegment(sketch, "E3758", {"start": v(-2106.92, 1303.56) * mm, "end": v(-2062.62, 1297.05) * mm});
            skLineSegment(sketch, "E3759", {"start": v(-2062.62, 1297.05) * mm, "end": v(-2036, 1316.56) * mm});
            skLineSegment(sketch, "E3760", {"start": v(-2036, 1316.56) * mm, "end": v(-2009.8, 1336.88) * mm});
            skLineSegment(sketch, "E3761", {"start": v(-2009.8, 1336.88) * mm, "end": v(-1984.19, 1357.81) * mm});
            skLineSegment(sketch, "E3762", {"start": v(-1984.19, 1357.81) * mm, "end": v(-2102.45, 1497.4) * mm});
            skLineSegment(sketch, "E3763", {"start": v(-2288.58, 1238.74) * mm, "end": v(-2260.14, 1251.74) * mm});
            skLineSegment(sketch, "E3764", {"start": v(-2260.14, 1251.74) * mm, "end": v(-2231.9, 1265.56) * mm});
            skLineSegment(sketch, "E3765", {"start": v(-2231.9, 1265.56) * mm, "end": v(-2204.26, 1280.19) * mm});
            skLineSegment(sketch, "E3766", {"start": v(-2204.26, 1280.19) * mm, "end": v(-2176.82, 1295.63) * mm});
            skLineSegment(sketch, "E3767", {"start": v(-2313.17, 1294.41) * mm, "end": v(-2286.14, 1306.8) * mm});
            skLineSegment(sketch, "E3768", {"start": v(-2286.14, 1306.8) * mm, "end": v(-2259.73, 1319.81) * mm});
            skLineSegment(sketch, "E3769", {"start": v(-2259.73, 1319.81) * mm, "end": v(-2233.52, 1333.63) * mm});
            skLineSegment(sketch, "E3770", {"start": v(-2233.52, 1333.63) * mm, "end": v(-2207.7, 1348.26) * mm});
            skLineSegment(sketch, "E3771", {"start": v(-2481.01, 1237.52) * mm, "end": v(-2452.36, 1244.83) * mm});
            skLineSegment(sketch, "E3772", {"start": v(-2452.36, 1244.83) * mm, "end": v(-2424.12, 1253.16) * mm});
            skLineSegment(sketch, "E3773", {"start": v(-2424.12, 1253.16) * mm, "end": v(-2395.87, 1262.3) * mm});
            skLineSegment(sketch, "E3774", {"start": v(-2395.87, 1262.3) * mm, "end": v(-2368.03, 1272.26) * mm});
            skLineSegment(sketch, "E3775", {"start": v(-2368.03, 1272.26) * mm, "end": v(-2382.87, 1223.9) * mm});
            skLineSegment(sketch, "E3776", {"start": v(-2382.87, 1223.9) * mm, "end": v(-2400.14, 1175.54) * mm});
            skLineSegment(sketch, "E3777", {"start": v(-2400.14, 1175.54) * mm, "end": v(-2420.05, 1127.38) * mm});
            skLineSegment(sketch, "E3778", {"start": v(-2420.05, 1127.38) * mm, "end": v(-2468.62, 1303.76) * mm});
            skLineSegment(sketch, "E3779", {"start": v(-2684.82, 1178.18) * mm, "end": v(-2715.1, 1177.57) * mm});
            skLineSegment(sketch, "E3780", {"start": v(-2715.1, 1177.57) * mm, "end": v(-2745.58, 1177.57) * mm});
            skLineSegment(sketch, "E3781", {"start": v(-2745.58, 1177.57) * mm, "end": v(-2776.06, 1178.8) * mm});
            skLineSegment(sketch, "E3782", {"start": v(-2776.06, 1178.8) * mm, "end": v(-2808.98, 1150.14) * mm});
            skLineSegment(sketch, "E3783", {"start": v(-2808.98, 1150.14) * mm, "end": v(-2811.21, 1119.86) * mm});
            skLineSegment(sketch, "E3784", {"start": v(-2811.21, 1119.86) * mm, "end": v(-2780.53, 1087.35) * mm});
            skLineSegment(sketch, "E3785", {"start": v(-2780.53, 1087.35) * mm, "end": v(-2747.4, 1086.34) * mm});
            skLineSegment(sketch, "E3786", {"start": v(-2747.4, 1086.34) * mm, "end": v(-2714.29, 1086.13) * mm});
            skLineSegment(sketch, "E3787", {"start": v(-2714.29, 1086.13) * mm, "end": v(-2681.17, 1086.95) * mm});
            skLineSegment(sketch, "E3788", {"start": v(-2681.17, 1086.95) * mm, "end": v(-2688.28, 1269.62) * mm});
            skLineSegment(sketch, "E3789", {"start": v(-2854.9, 1277.75) * mm, "end": v(-2863.03, 1217.2) * mm});
            skLineSegment(sketch, "E3790", {"start": v(-2863.03, 1217.2) * mm, "end": v(-2902.25, 1161.52) * mm});
            skLineSegment(sketch, "E3791", {"start": v(-2902.25, 1161.52) * mm, "end": v(-2944.92, 1107.27) * mm});
            skLineSegment(sketch, "E3792", {"start": v(-2944.92, 1107.27) * mm, "end": v(-2963.82, 1173.5) * mm});
            skLineSegment(sketch, "E3793", {"start": v(-2963.82, 1173.5) * mm, "end": v(-2979.26, 1239.96) * mm});
            skLineSegment(sketch, "E3794", {"start": v(-2979.26, 1239.96) * mm, "end": v(-2964.02, 1299.09) * mm});
            skLineSegment(sketch, "E3795", {"start": v(-2863.03, 1217.2) * mm, "end": v(-2892.3, 1221.67) * mm});
            skLineSegment(sketch, "E3796", {"start": v(-2892.3, 1221.67) * mm, "end": v(-2921.55, 1226.95) * mm});
            skLineSegment(sketch, "E3797", {"start": v(-2921.55, 1226.95) * mm, "end": v(-2950.4, 1233.05) * mm});
            skLineSegment(sketch, "E3798", {"start": v(-2950.4, 1233.05) * mm, "end": v(-2979.26, 1239.96) * mm});
            skLineSegment(sketch, "E3799", {"start": v(-3171.7, 1243.2) * mm, "end": v(-3142.84, 1230.6) * mm});
            skLineSegment(sketch, "E3800", {"start": v(-3142.84, 1230.6) * mm, "end": v(-3113.78, 1219.03) * mm});
            skLineSegment(sketch, "E3801", {"start": v(-3113.78, 1219.03) * mm, "end": v(-3084.31, 1208.26) * mm});
            skLineSegment(sketch, "E3802", {"start": v(-3084.31, 1208.26) * mm, "end": v(-3054.65, 1198.3) * mm});
            skLineSegment(sketch, "E3803", {"start": v(-3146.5, 1298.68) * mm, "end": v(-3119.47, 1286.9) * mm});
            skLineSegment(sketch, "E3804", {"start": v(-3119.47, 1286.9) * mm, "end": v(-3091.83, 1275.92) * mm});
            skLineSegment(sketch, "E3805", {"start": v(-3091.83, 1275.92) * mm, "end": v(-3064.2, 1265.76) * mm});
            skLineSegment(sketch, "E3806", {"start": v(-3064.2, 1265.76) * mm, "end": v(-3036.16, 1256.41) * mm});
            skLineSegment(sketch, "E3807", {"start": v(-3267, 1435.84) * mm, "end": v(-3243.62, 1420.6) * mm});
            skLineSegment(sketch, "E3808", {"start": v(-3243.62, 1420.6) * mm, "end": v(-3220.05, 1405.97) * mm});
            skLineSegment(sketch, "E3809", {"start": v(-3220.05, 1405.97) * mm, "end": v(-3195.87, 1391.95) * mm});
            skLineSegment(sketch, "E3810", {"start": v(-3195.87, 1391.95) * mm, "end": v(-3171.49, 1378.74) * mm});
            skLineSegment(sketch, "E3811", {"start": v(-3171.49, 1378.74) * mm, "end": v(-3199.73, 1324.69) * mm});
            skLineSegment(sketch, "E3812", {"start": v(-3199.73, 1324.69) * mm, "end": v(-3240.78, 1312.3) * mm});
            skLineSegment(sketch, "E3813", {"start": v(-3240.78, 1312.3) * mm, "end": v(-3267, 1327.53) * mm});
            skLineSegment(sketch, "E3814", {"start": v(-3267, 1327.53) * mm, "end": v(-3293, 1343.59) * mm});
            skLineSegment(sketch, "E3815", {"start": v(-3293, 1343.59) * mm, "end": v(-3335.47, 1335.05) * mm});
            skLineSegment(sketch, "E3816", {"start": v(-3335.47, 1335.05) * mm, "end": v(-3352.74, 1309.86) * mm});
            skLineSegment(sketch, "E3817", {"start": v(-3352.74, 1309.86) * mm, "end": v(-3342.18, 1266.57) * mm});
            skLineSegment(sketch, "E3818", {"start": v(-3342.18, 1266.57) * mm, "end": v(-3314.13, 1249.1) * mm});
            skLineSegment(sketch, "E3819", {"start": v(-3314.13, 1249.1) * mm, "end": v(-3285.48, 1232.44) * mm});
            skLineSegment(sketch, "E3820", {"start": v(-3285.48, 1232.44) * mm, "end": v(-3242.2, 1243.61) * mm});
            skFitSpline(sketch, "E3821", {"points": [v(-1074.06, 2231.57) * mm, v(-1074.06, 1319.75) * mm, v(-1813.23, 580.57) * mm, v(-2725.06, 580.57) * mm]});
            skFitSpline(sketch, "E3822", {"points": [v(-2725.06, 580.57) * mm, v(-3636.88, 580.57) * mm, v(-4376.06, 1319.75) * mm, v(-4376.06, 2231.57) * mm]});
            skFitSpline(sketch, "E3823", {"points": [v(-4376.06, 2231.57) * mm, v(-4376.06, 3143.4) * mm, v(-3636.88, 3882.57) * mm, v(-2725.06, 3882.57) * mm]});
            skFitSpline(sketch, "E3824", {"points": [v(-2725.06, 3882.57) * mm, v(-1813.23, 3882.57) * mm, v(-1074.06, 3143.4) * mm, v(-1074.06, 2231.57) * mm]});
            skLineSegment(sketch, "E3825", {"start": v(-3396.23, 1541.3) * mm, "end": v(-3375.9, 1522.2) * mm});
            skLineSegment(sketch, "E3826", {"start": v(-3375.9, 1522.2) * mm, "end": v(-3355.18, 1503.7) * mm});
            skLineSegment(sketch, "E3827", {"start": v(-3355.18, 1503.7) * mm, "end": v(-3333.84, 1485.83) * mm});
            skLineSegment(sketch, "E3828", {"start": v(-3333.84, 1485.83) * mm, "end": v(-3312.1, 1468.56) * mm});
            skLineSegment(sketch, "E3829", {"start": v(-3312.1, 1468.56) * mm, "end": v(-3349.08, 1420.2) * mm});
            skLineSegment(sketch, "E3830", {"start": v(-3349.08, 1420.2) * mm, "end": v(-3391.55, 1414.91) * mm});
            skLineSegment(sketch, "E3831", {"start": v(-3391.55, 1414.91) * mm, "end": v(-3414.92, 1434.62) * mm});
            skLineSegment(sketch, "E3832", {"start": v(-3414.92, 1434.62) * mm, "end": v(-3437.68, 1454.94) * mm});
            skLineSegment(sketch, "E3833", {"start": v(-3437.68, 1454.94) * mm, "end": v(-3481.16, 1453.92) * mm});
            skLineSegment(sketch, "E3834", {"start": v(-3481.16, 1453.92) * mm, "end": v(-3502.3, 1432.18) * mm});
            skLineSegment(sketch, "E3835", {"start": v(-3502.3, 1432.18) * mm, "end": v(-3499.66, 1387.48) * mm});
            skLineSegment(sketch, "E3836", {"start": v(-3499.66, 1387.48) * mm, "end": v(-3474.86, 1365.53) * mm});
            skLineSegment(sketch, "E3837", {"start": v(-3474.86, 1365.53) * mm, "end": v(-3449.46, 1344.2) * mm});
            skLineSegment(sketch, "E3838", {"start": v(-3449.46, 1344.2) * mm, "end": v(-3404.96, 1347.85) * mm});
            skFitSpline(sketch, "E3839", {"points": [v(-820.06, 2231.57) * mm, v(-820.06, 1179.47) * mm, v(-1672.95, 326.57) * mm, v(-2725.06, 326.57) * mm]});
            skFitSpline(sketch, "E3840", {"points": [v(-2725.06, 326.57) * mm, v(-3777.16, 326.57) * mm, v(-4630.06, 1179.47) * mm, v(-4630.06, 2231.57) * mm]});
            skFitSpline(sketch, "E3841", {"points": [v(-4630.06, 2231.57) * mm, v(-4630.06, 3283.67) * mm, v(-3777.16, 4136.57) * mm, v(-2725.06, 4136.57) * mm]});
            skFitSpline(sketch, "E3842", {"points": [v(-2725.06, 4136.57) * mm, v(-1672.95, 4136.57) * mm, v(-820.06, 3283.67) * mm, v(-820.06, 2231.57) * mm]});
            skFitSpline(sketch, "E3843", {"points": [v(-1194.35, 2231.57) * mm, v(-1194.35, 1386.19) * mm, v(-1879.67, 700.87) * mm, v(-2725.06, 700.87) * mm]});
            skFitSpline(sketch, "E3844", {"points": [v(-2725.06, 700.87) * mm, v(-3570.44, 700.87) * mm, v(-4255.76, 1386.19) * mm, v(-4255.76, 2231.57) * mm]});
            skFitSpline(sketch, "E3845", {"points": [v(-4255.76, 2231.57) * mm, v(-4255.76, 3076.96) * mm, v(-3570.44, 3762.28) * mm, v(-2725.06, 3762.28) * mm]});
            skFitSpline(sketch, "E3846", {"points": [v(-2725.06, 3762.28) * mm, v(-1879.67, 3762.28) * mm, v(-1194.35, 3076.96) * mm, v(-1194.35, 2231.57) * mm]});
            skLineSegment(sketch, "E3847", {"start": v(1766.2, 2115.72) * mm, "end": v(1770.48, 2116.17) * mm});
            skLineSegment(sketch, "E3848", {"start": v(1770.48, 2116.17) * mm, "end": v(1776.16, 2116.97) * mm});
            skLineSegment(sketch, "E3849", {"start": v(1776.16, 2116.97) * mm, "end": v(1783.22, 2118.22) * mm});
            skLineSegment(sketch, "E3850", {"start": v(1783.22, 2118.22) * mm, "end": v(1791.65, 2120.02) * mm});
            skLineSegment(sketch, "E3851", {"start": v(1791.65, 2120.02) * mm, "end": v(1801.39, 2122.45) * mm});
            skLineSegment(sketch, "E3852", {"start": v(1801.39, 2122.45) * mm, "end": v(1812.42, 2125.62) * mm});
            skLineSegment(sketch, "E3853", {"start": v(1812.42, 2125.62) * mm, "end": v(1824.7, 2129.61) * mm});
            skLineSegment(sketch, "E3854", {"start": v(1824.7, 2129.61) * mm, "end": v(1838.18, 2134.53) * mm});
            skLineSegment(sketch, "E3855", {"start": v(1838.18, 2134.53) * mm, "end": v(1852.81, 2140.44) * mm});
            skLineSegment(sketch, "E3856", {"start": v(1852.81, 2140.44) * mm, "end": v(1868.54, 2147.45) * mm});
            skLineSegment(sketch, "E3857", {"start": v(1868.54, 2147.45) * mm, "end": v(1885.3, 2155.63) * mm});
            skLineSegment(sketch, "E3858", {"start": v(1885.3, 2155.63) * mm, "end": v(1903.03, 2165.06) * mm});
            skLineSegment(sketch, "E3859", {"start": v(1903.03, 2165.06) * mm, "end": v(1921.67, 2175.82) * mm});
            skLineSegment(sketch, "E3860", {"start": v(1921.67, 2175.82) * mm, "end": v(1941.13, 2188) * mm});
            skLineSegment(sketch, "E3861", {"start": v(1941.13, 2188) * mm, "end": v(1961.35, 2201.63) * mm});
            skLineSegment(sketch, "E3862", {"start": v(1961.35, 2201.63) * mm, "end": v(1982.24, 2216.82) * mm});
            skLineSegment(sketch, "E3863", {"start": v(1982.24, 2216.82) * mm, "end": v(2003.72, 2233.6) * mm});
            skLineSegment(sketch, "E3864", {"start": v(2003.72, 2233.6) * mm, "end": v(2025.7, 2252.05) * mm});
            skLineSegment(sketch, "E3865", {"start": v(2025.7, 2252.05) * mm, "end": v(2048.08, 2272.21) * mm});
            skLineSegment(sketch, "E3866", {"start": v(2048.08, 2272.21) * mm, "end": v(2070.79, 2294.14) * mm});
            skLineSegment(sketch, "E3867", {"start": v(2070.79, 2294.14) * mm, "end": v(2093.7, 2317.88) * mm});
            skLineSegment(sketch, "E3868", {"start": v(2093.7, 2317.88) * mm, "end": v(2091.6, 2339.73) * mm});
            skLineSegment(sketch, "E3869", {"start": v(2091.6, 2339.73) * mm, "end": v(2076.03, 2426.95) * mm});
            skLineSegment(sketch, "E3870", {"start": v(2076.03, 2426.95) * mm, "end": v(2070.43, 2448.17) * mm});
            skLineSegment(sketch, "E3871", {"start": v(2070.43, 2448.17) * mm, "end": v(2040.7, 2462.51) * mm});
            skLineSegment(sketch, "E3872", {"start": v(2040.7, 2462.51) * mm, "end": v(2011.82, 2475.22) * mm});
            skLineSegment(sketch, "E3873", {"start": v(2011.82, 2475.22) * mm, "end": v(1983.83, 2486.39) * mm});
            skLineSegment(sketch, "E3874", {"start": v(1983.83, 2486.39) * mm, "end": v(1956.83, 2496.09) * mm});
            skLineSegment(sketch, "E3875", {"start": v(1956.83, 2496.09) * mm, "end": v(1930.87, 2504.4) * mm});
            skLineSegment(sketch, "E3876", {"start": v(1930.87, 2504.4) * mm, "end": v(1906.01, 2511.4) * mm});
            skLineSegment(sketch, "E3877", {"start": v(1906.01, 2511.4) * mm, "end": v(1882.32, 2517.2) * mm});
            skLineSegment(sketch, "E3878", {"start": v(1882.32, 2517.2) * mm, "end": v(1859.85, 2521.88) * mm});
            skLineSegment(sketch, "E3879", {"start": v(1859.85, 2521.88) * mm, "end": v(1838.64, 2525.53) * mm});
            skLineSegment(sketch, "E3880", {"start": v(1838.64, 2525.53) * mm, "end": v(1818.74, 2528.24) * mm});
            skLineSegment(sketch, "E3881", {"start": v(1818.74, 2528.24) * mm, "end": v(1800.18, 2530.11) * mm});
            skLineSegment(sketch, "E3882", {"start": v(1800.18, 2530.11) * mm, "end": v(1783, 2531.24) * mm});
            skLineSegment(sketch, "E3883", {"start": v(1783, 2531.24) * mm, "end": v(1767.23, 2531.72) * mm});
            skLineSegment(sketch, "E3884", {"start": v(1767.23, 2531.72) * mm, "end": v(1752.88, 2531.66) * mm});
            skLineSegment(sketch, "E3885", {"start": v(1752.88, 2531.66) * mm, "end": v(1739.98, 2531.16) * mm});
            skLineSegment(sketch, "E3886", {"start": v(1739.98, 2531.16) * mm, "end": v(1728.53, 2530.31) * mm});
            skLineSegment(sketch, "E3887", {"start": v(1728.53, 2530.31) * mm, "end": v(1718.55, 2529.22) * mm});
            skLineSegment(sketch, "E3888", {"start": v(1718.55, 2529.22) * mm, "end": v(1710.03, 2527.99) * mm});
            skLineSegment(sketch, "E3889", {"start": v(1710.03, 2527.99) * mm, "end": v(1702.97, 2526.72) * mm});
            skLineSegment(sketch, "E3890", {"start": v(1702.97, 2526.72) * mm, "end": v(1697.36, 2525.5) * mm});
            skLineSegment(sketch, "E3891", {"start": v(1697.36, 2525.5) * mm, "end": v(1693.19, 2524.45) * mm});
            skLineSegment(sketch, "E3892", {"start": v(1693.19, 2524.45) * mm, "end": v(1690.43, 2523.65) * mm});
            skLineSegment(sketch, "E3893", {"start": v(1690.43, 2523.65) * mm, "end": v(1689.07, 2523.2) * mm});
            skLineSegment(sketch, "E3894", {"start": v(1689.07, 2523.2) * mm, "end": v(1501.62, 2454.03) * mm});
            skLineSegment(sketch, "E3895", {"start": v(1501.62, 2454.03) * mm, "end": v(1375.34, 2690.25) * mm});
            skLineSegment(sketch, "E3896", {"start": v(1375.34, 2690.25) * mm, "end": v(1536.98, 2807.7) * mm});
            skLineSegment(sketch, "E3897", {"start": v(1536.98, 2807.7) * mm, "end": v(1538.1, 2808.58) * mm});
            skLineSegment(sketch, "E3898", {"start": v(1538.1, 2808.58) * mm, "end": v(1540.3, 2810.43) * mm});
            skLineSegment(sketch, "E3899", {"start": v(1540.3, 2810.43) * mm, "end": v(1543.5, 2813.31) * mm});
            skLineSegment(sketch, "E3900", {"start": v(1543.5, 2813.31) * mm, "end": v(1547.62, 2817.3) * mm});
            skLineSegment(sketch, "E3901", {"start": v(1547.62, 2817.3) * mm, "end": v(1552.6, 2822.46) * mm});
            skLineSegment(sketch, "E3902", {"start": v(1552.6, 2822.46) * mm, "end": v(1558.36, 2828.87) * mm});
            skLineSegment(sketch, "E3903", {"start": v(1558.36, 2828.87) * mm, "end": v(1564.82, 2836.56) * mm});
            skLineSegment(sketch, "E3904", {"start": v(1564.82, 2836.56) * mm, "end": v(1571.88, 2845.6) * mm});
            skLineSegment(sketch, "E3905", {"start": v(1571.88, 2845.6) * mm, "end": v(1579.46, 2856.06) * mm});
            skLineSegment(sketch, "E3906", {"start": v(1579.46, 2856.06) * mm, "end": v(1587.48, 2867.95) * mm});
            skLineSegment(sketch, "E3907", {"start": v(1587.48, 2867.95) * mm, "end": v(1595.84, 2881.34) * mm});
            skLineSegment(sketch, "E3908", {"start": v(1595.84, 2881.34) * mm, "end": v(1604.45, 2896.25) * mm});
            skLineSegment(sketch, "E3909", {"start": v(1604.45, 2896.25) * mm, "end": v(1613.2, 2912.72) * mm});
            skLineSegment(sketch, "E3910", {"start": v(1613.2, 2912.72) * mm, "end": v(1622, 2930.78) * mm});
            skLineSegment(sketch, "E3911", {"start": v(1622, 2930.78) * mm, "end": v(1630.75, 2950.44) * mm});
            skLineSegment(sketch, "E3912", {"start": v(1630.75, 2950.44) * mm, "end": v(1639.34, 2971.72) * mm});
            skLineSegment(sketch, "E3913", {"start": v(1639.34, 2971.72) * mm, "end": v(1647.68, 2994.64) * mm});
            skLineSegment(sketch, "E3914", {"start": v(1647.68, 2994.64) * mm, "end": v(1655.66, 3019.2) * mm});
            skLineSegment(sketch, "E3915", {"start": v(1655.66, 3019.2) * mm, "end": v(1663.17, 3045.4) * mm});
            skLineSegment(sketch, "E3916", {"start": v(1663.17, 3045.4) * mm, "end": v(1670.1, 3073.25) * mm});
            skLineSegment(sketch, "E3917", {"start": v(1670.1, 3073.25) * mm, "end": v(1676.37, 3102.72) * mm});
            skLineSegment(sketch, "E3918", {"start": v(1676.37, 3102.72) * mm, "end": v(1681.84, 3133.8) * mm});
            skLineSegment(sketch, "E3919", {"start": v(1681.84, 3133.8) * mm, "end": v(1686.43, 3166.49) * mm});
            skLineSegment(sketch, "E3920", {"start": v(1686.43, 3166.49) * mm, "end": v(1671.9, 3182.93) * mm});
            skLineSegment(sketch, "E3921", {"start": v(1671.9, 3182.93) * mm, "end": v(1608.02, 3244.33) * mm});
            skLineSegment(sketch, "E3922", {"start": v(1608.02, 3244.33) * mm, "end": v(1591.02, 3258.22) * mm});
            skLineSegment(sketch, "E3923", {"start": v(1591.02, 3258.22) * mm, "end": v(1558.55, 3252.34) * mm});
            skLineSegment(sketch, "E3924", {"start": v(1558.55, 3252.34) * mm, "end": v(1527.7, 3245.65) * mm});
            skLineSegment(sketch, "E3925", {"start": v(1527.7, 3245.65) * mm, "end": v(1498.5, 3238.23) * mm});
            skLineSegment(sketch, "E3926", {"start": v(1498.5, 3238.23) * mm, "end": v(1470.95, 3230.2) * mm});
            skLineSegment(sketch, "E3927", {"start": v(1470.95, 3230.2) * mm, "end": v(1445.06, 3221.67) * mm});
            skLineSegment(sketch, "E3928", {"start": v(1445.06, 3221.67) * mm, "end": v(1420.83, 3212.73) * mm});
            skLineSegment(sketch, "E3929", {"start": v(1420.83, 3212.73) * mm, "end": v(1398.26, 3203.5) * mm});
            skLineSegment(sketch, "E3930", {"start": v(1398.26, 3203.5) * mm, "end": v(1377.33, 3194.07) * mm});
            skLineSegment(sketch, "E3931", {"start": v(1377.33, 3194.07) * mm, "end": v(1358.03, 3184.55) * mm});
            skLineSegment(sketch, "E3932", {"start": v(1358.03, 3184.55) * mm, "end": v(1340.33, 3175.05) * mm});
            skLineSegment(sketch, "E3933", {"start": v(1340.33, 3175.05) * mm, "end": v(1324.22, 3165.65) * mm});
            skLineSegment(sketch, "E3934", {"start": v(1324.22, 3165.65) * mm, "end": v(1309.66, 3156.47) * mm});
            skLineSegment(sketch, "E3935", {"start": v(1309.66, 3156.47) * mm, "end": v(1296.61, 3147.59) * mm});
            skLineSegment(sketch, "E3936", {"start": v(1296.61, 3147.59) * mm, "end": v(1285.04, 3139.1) * mm});
            skLineSegment(sketch, "E3937", {"start": v(1285.04, 3139.1) * mm, "end": v(1274.9, 3131.12) * mm});
            skLineSegment(sketch, "E3938", {"start": v(1274.9, 3131.12) * mm, "end": v(1266.14, 3123.7) * mm});
            skLineSegment(sketch, "E3939", {"start": v(1266.14, 3123.7) * mm, "end": v(1258.7, 3116.95) * mm});
            skLineSegment(sketch, "E3940", {"start": v(1258.7, 3116.95) * mm, "end": v(1252.53, 3110.95) * mm});
            skLineSegment(sketch, "E3941", {"start": v(1252.53, 3110.95) * mm, "end": v(1247.57, 3105.77) * mm});
            skLineSegment(sketch, "E3942", {"start": v(1247.57, 3105.77) * mm, "end": v(1243.75, 3101.49) * mm});
            skLineSegment(sketch, "E3943", {"start": v(1243.75, 3101.49) * mm, "end": v(1240.99, 3098.18) * mm});
            skLineSegment(sketch, "E3944", {"start": v(1240.99, 3098.18) * mm, "end": v(1239.23, 3095.92) * mm});
            skLineSegment(sketch, "E3945", {"start": v(1239.23, 3095.92) * mm, "end": v(1238.39, 3094.75) * mm});
            skLineSegment(sketch, "E3946", {"start": v(1238.39, 3094.75) * mm, "end": v(1127.4, 2928.61) * mm});
            skLineSegment(sketch, "E3947", {"start": v(1127.4, 2928.61) * mm, "end": v(886.39, 3045.5) * mm});
            skLineSegment(sketch, "E3948", {"start": v(886.39, 3045.5) * mm, "end": v(948.13, 3235.52) * mm});
            skLineSegment(sketch, "E3949", {"start": v(948.13, 3235.52) * mm, "end": v(948.52, 3236.9) * mm});
            skLineSegment(sketch, "E3950", {"start": v(948.52, 3236.9) * mm, "end": v(949.21, 3239.69) * mm});
            skLineSegment(sketch, "E3951", {"start": v(949.21, 3239.69) * mm, "end": v(950.1, 3243.9) * mm});
            skLineSegment(sketch, "E3952", {"start": v(950.1, 3243.9) * mm, "end": v(951.1, 3249.55) * mm});
            skLineSegment(sketch, "E3953", {"start": v(951.1, 3249.55) * mm, "end": v(952.09, 3256.65) * mm});
            skLineSegment(sketch, "E3954", {"start": v(952.09, 3256.65) * mm, "end": v(952.98, 3265.21) * mm});
            skLineSegment(sketch, "E3955", {"start": v(952.98, 3265.21) * mm, "end": v(953.68, 3275.23) * mm});
            skLineSegment(sketch, "E3956", {"start": v(953.68, 3275.23) * mm, "end": v(954.08, 3286.7) * mm});
            skLineSegment(sketch, "E3957", {"start": v(954.08, 3286.7) * mm, "end": v(954.07, 3299.62) * mm});
            skLineSegment(sketch, "E3958", {"start": v(954.07, 3299.62) * mm, "end": v(953.57, 3313.95) * mm});
            skLineSegment(sketch, "E3959", {"start": v(953.57, 3313.95) * mm, "end": v(952.46, 3329.7) * mm});
            skLineSegment(sketch, "E3960", {"start": v(952.46, 3329.7) * mm, "end": v(950.66, 3346.82) * mm});
            skLineSegment(sketch, "E3961", {"start": v(950.66, 3346.82) * mm, "end": v(948.06, 3365.29) * mm});
            skLineSegment(sketch, "E3962", {"start": v(948.06, 3365.29) * mm, "end": v(944.57, 3385.07) * mm});
            skLineSegment(sketch, "E3963", {"start": v(944.57, 3385.07) * mm, "end": v(940.09, 3406.12) * mm});
            skLineSegment(sketch, "E3964", {"start": v(940.09, 3406.12) * mm, "end": v(934.53, 3428.39) * mm});
            skLineSegment(sketch, "E3965", {"start": v(934.53, 3428.39) * mm, "end": v(927.8, 3451.83) * mm});
            skLineSegment(sketch, "E3966", {"start": v(927.8, 3451.83) * mm, "end": v(919.82, 3476.4) * mm});
            skLineSegment(sketch, "E3967", {"start": v(919.82, 3476.4) * mm, "end": v(910.5, 3502) * mm});
            skLineSegment(sketch, "E3968", {"start": v(910.5, 3502) * mm, "end": v(899.74, 3528.6) * mm});
            skLineSegment(sketch, "E3969", {"start": v(899.74, 3528.6) * mm, "end": v(887.48, 3556.13) * mm});
            skLineSegment(sketch, "E3970", {"start": v(887.48, 3556.13) * mm, "end": v(873.64, 3584.5) * mm});
            skLineSegment(sketch, "E3971", {"start": v(873.64, 3584.5) * mm, "end": v(858.14, 3613.63) * mm});
            skLineSegment(sketch, "E3972", {"start": v(858.14, 3613.63) * mm, "end": v(836.72, 3618.4) * mm});
            skLineSegment(sketch, "E3973", {"start": v(836.72, 3618.4) * mm, "end": v(748.96, 3630.53) * mm});
            skLineSegment(sketch, "E3974", {"start": v(748.96, 3630.53) * mm, "end": v(727.04, 3631.76) * mm});
            skLineSegment(sketch, "E3975", {"start": v(727.04, 3631.76) * mm, "end": v(704.22, 3607.92) * mm});
            skLineSegment(sketch, "E3976", {"start": v(704.22, 3607.92) * mm, "end": v(683.2, 3584.38) * mm});
            skLineSegment(sketch, "E3977", {"start": v(683.2, 3584.38) * mm, "end": v(663.93, 3561.21) * mm});
            skLineSegment(sketch, "E3978", {"start": v(663.93, 3561.21) * mm, "end": v(646.37, 3538.53) * mm});
            skLineSegment(sketch, "E3979", {"start": v(646.37, 3538.53) * mm, "end": v(630.44, 3516.4) * mm});
            skLineSegment(sketch, "E3980", {"start": v(630.44, 3516.4) * mm, "end": v(616.1, 3494.93) * mm});
            skLineSegment(sketch, "E3981", {"start": v(616.1, 3494.93) * mm, "end": v(603.25, 3474.2) * mm});
            skLineSegment(sketch, "E3982", {"start": v(603.25, 3474.2) * mm, "end": v(591.86, 3454.26) * mm});
            skLineSegment(sketch, "E3983", {"start": v(591.86, 3454.26) * mm, "end": v(581.84, 3435.22) * mm});
            skLineSegment(sketch, "E3984", {"start": v(581.84, 3435.22) * mm, "end": v(573.11, 3417.13) * mm});
            skLineSegment(sketch, "E3985", {"start": v(573.11, 3417.13) * mm, "end": v(565.6, 3400.06) * mm});
            skLineSegment(sketch, "E3986", {"start": v(565.6, 3400.06) * mm, "end": v(559.22, 3384.07) * mm});
            skLineSegment(sketch, "E3987", {"start": v(559.22, 3384.07) * mm, "end": v(553.88, 3369.22) * mm});
            skLineSegment(sketch, "E3988", {"start": v(553.88, 3369.22) * mm, "end": v(549.5, 3355.55) * mm});
            skLineSegment(sketch, "E3989", {"start": v(549.5, 3355.55) * mm, "end": v(546, 3343.12) * mm});
            skLineSegment(sketch, "E3990", {"start": v(546, 3343.12) * mm, "end": v(543.27, 3331.98) * mm});
            skLineSegment(sketch, "E3991", {"start": v(543.27, 3331.98) * mm, "end": v(541.22, 3322.14) * mm});
            skLineSegment(sketch, "E3992", {"start": v(541.22, 3322.14) * mm, "end": v(539.76, 3313.66) * mm});
            skLineSegment(sketch, "E3993", {"start": v(539.76, 3313.66) * mm, "end": v(538.79, 3306.55) * mm});
            skLineSegment(sketch, "E3994", {"start": v(538.79, 3306.55) * mm, "end": v(538.2, 3300.84) * mm});
            skLineSegment(sketch, "E3995", {"start": v(538.2, 3300.84) * mm, "end": v(537.92, 3296.55) * mm});
            skLineSegment(sketch, "E3996", {"start": v(537.92, 3296.55) * mm, "end": v(537.83, 3293.68) * mm});
            skLineSegment(sketch, "E3997", {"start": v(537.83, 3293.68) * mm, "end": v(537.83, 3292.25) * mm});
            skLineSegment(sketch, "E3998", {"start": v(537.83, 3292.25) * mm, "end": v(545.7, 3092.6) * mm});
            skLineSegment(sketch, "E3999", {"start": v(545.7, 3092.6) * mm, "end": v(282.01, 3045.5) * mm});
            skLineSegment(sketch, "E4000", {"start": v(282.01, 3045.5) * mm, "end": v(220.27, 3235.52) * mm});
            skLineSegment(sketch, "E4001", {"start": v(220.27, 3235.52) * mm, "end": v(219.77, 3236.86) * mm});
            skLineSegment(sketch, "E4002", {"start": v(219.77, 3236.86) * mm, "end": v(218.7, 3239.52) * mm});
            skLineSegment(sketch, "E4003", {"start": v(218.7, 3239.52) * mm, "end": v(216.94, 3243.45) * mm});
            skLineSegment(sketch, "E4004", {"start": v(216.94, 3243.45) * mm, "end": v(214.42, 3248.6) * mm});
            skLineSegment(sketch, "E4005", {"start": v(214.42, 3248.6) * mm, "end": v(211.05, 3254.94) * mm});
            skLineSegment(sketch, "E4006", {"start": v(211.05, 3254.94) * mm, "end": v(206.74, 3262.4) * mm});
            skLineSegment(sketch, "E4007", {"start": v(206.74, 3262.4) * mm, "end": v(201.42, 3270.9) * mm});
            skLineSegment(sketch, "E4008", {"start": v(201.42, 3270.9) * mm, "end": v(195, 3280.42) * mm});
            skLineSegment(sketch, "E4009", {"start": v(195, 3280.42) * mm, "end": v(187.4, 3290.87) * mm});
            skLineSegment(sketch, "E4010", {"start": v(187.4, 3290.87) * mm, "end": v(178.56, 3302.17) * mm});
            skLineSegment(sketch, "E4011", {"start": v(178.56, 3302.17) * mm, "end": v(168.42, 3314.26) * mm});
            skLineSegment(sketch, "E4012", {"start": v(168.42, 3314.26) * mm, "end": v(156.9, 3327.05) * mm});
            skLineSegment(sketch, "E4013", {"start": v(156.9, 3327.05) * mm, "end": v(143.94, 3340.46) * mm});
            skLineSegment(sketch, "E4014", {"start": v(143.94, 3340.46) * mm, "end": v(129.48, 3354.41) * mm});
            skLineSegment(sketch, "E4015", {"start": v(129.48, 3354.41) * mm, "end": v(113.49, 3368.8) * mm});
            skLineSegment(sketch, "E4016", {"start": v(113.49, 3368.8) * mm, "end": v(95.9, 3383.56) * mm});
            skLineSegment(sketch, "E4017", {"start": v(95.9, 3383.56) * mm, "end": v(76.68, 3398.57) * mm});
            skLineSegment(sketch, "E4018", {"start": v(76.68, 3398.57) * mm, "end": v(55.78, 3413.75) * mm});
            skLineSegment(sketch, "E4019", {"start": v(55.78, 3413.75) * mm, "end": v(33.18, 3428.99) * mm});
            skLineSegment(sketch, "E4020", {"start": v(33.18, 3428.99) * mm, "end": v(8.85, 3444.2) * mm});
            skLineSegment(sketch, "E4021", {"start": v(8.85, 3444.2) * mm, "end": v(-17.25, 3459.25) * mm});
            skLineSegment(sketch, "E4022", {"start": v(-17.25, 3459.25) * mm, "end": v(-45.12, 3474.07) * mm});
            skLineSegment(sketch, "E4023", {"start": v(-45.12, 3474.07) * mm, "end": v(-74.78, 3488.53) * mm});
            skLineSegment(sketch, "E4024", {"start": v(-74.78, 3488.53) * mm, "end": v(-94.91, 3479.78) * mm});
            skLineSegment(sketch, "E4025", {"start": v(-94.91, 3479.78) * mm, "end": v(-173.05, 3438.01) * mm});
            skLineSegment(sketch, "E4026", {"start": v(-173.05, 3438.01) * mm, "end": v(-191.5, 3426.13) * mm});
            skLineSegment(sketch, "E4027", {"start": v(-191.5, 3426.13) * mm, "end": v(-195.95, 3393.43) * mm});
            skLineSegment(sketch, "E4028", {"start": v(-195.95, 3393.43) * mm, "end": v(-199.12, 3362.03) * mm});
            skLineSegment(sketch, "E4029", {"start": v(-199.12, 3362.03) * mm, "end": v(-201.09, 3331.96) * mm});
            skLineSegment(sketch, "E4030", {"start": v(-201.09, 3331.96) * mm, "end": v(-201.97, 3303.28) * mm});
            skLineSegment(sketch, "E4031", {"start": v(-201.97, 3303.28) * mm, "end": v(-201.85, 3276.02) * mm});
            skLineSegment(sketch, "E4032", {"start": v(-201.85, 3276.02) * mm, "end": v(-200.83, 3250.22) * mm});
            skLineSegment(sketch, "E4033", {"start": v(-200.83, 3250.22) * mm, "end": v(-199.03, 3225.9) * mm});
            skLineSegment(sketch, "E4034", {"start": v(-199.03, 3225.9) * mm, "end": v(-196.53, 3203.08) * mm});
            skLineSegment(sketch, "E4035", {"start": v(-196.53, 3203.08) * mm, "end": v(-193.45, 3181.78) * mm});
            skLineSegment(sketch, "E4036", {"start": v(-193.45, 3181.78) * mm, "end": v(-189.87, 3162.01) * mm});
            skLineSegment(sketch, "E4037", {"start": v(-189.87, 3162.01) * mm, "end": v(-185.92, 3143.79) * mm});
            skLineSegment(sketch, "E4038", {"start": v(-185.92, 3143.79) * mm, "end": v(-181.68, 3127.1) * mm});
            skLineSegment(sketch, "E4039", {"start": v(-181.68, 3127.1) * mm, "end": v(-177.27, 3111.95) * mm});
            skLineSegment(sketch, "E4040", {"start": v(-177.27, 3111.95) * mm, "end": v(-172.78, 3098.32) * mm});
            skLineSegment(sketch, "E4041", {"start": v(-172.78, 3098.32) * mm, "end": v(-168.31, 3086.2) * mm});
            skLineSegment(sketch, "E4042", {"start": v(-168.31, 3086.2) * mm, "end": v(-163.97, 3075.58) * mm});
            skLineSegment(sketch, "E4043", {"start": v(-163.97, 3075.58) * mm, "end": v(-159.84, 3066.42) * mm});
            skLineSegment(sketch, "E4044", {"start": v(-159.84, 3066.42) * mm, "end": v(-156.04, 3058.7) * mm});
            skLineSegment(sketch, "E4045", {"start": v(-156.04, 3058.7) * mm, "end": v(-152.65, 3052.38) * mm});
            skLineSegment(sketch, "E4046", {"start": v(-152.65, 3052.38) * mm, "end": v(-149.76, 3047.42) * mm});
            skLineSegment(sketch, "E4047", {"start": v(-149.76, 3047.42) * mm, "end": v(-147.47, 3043.78) * mm});
            skLineSegment(sketch, "E4048", {"start": v(-147.47, 3043.78) * mm, "end": v(-145.85, 3041.4) * mm});
            skLineSegment(sketch, "E4049", {"start": v(-145.85, 3041.4) * mm, "end": v(-145, 3040.25) * mm});
            skLineSegment(sketch, "E4050", {"start": v(-145, 3040.25) * mm, "end": v(-21.3, 2883.35) * mm});
            skLineSegment(sketch, "E4051", {"start": v(-21.3, 2883.35) * mm, "end": v(-206.94, 2690.25) * mm});
            skLineSegment(sketch, "E4052", {"start": v(-206.94, 2690.25) * mm, "end": v(-368.58, 2807.7) * mm});
            skLineSegment(sketch, "E4053", {"start": v(-368.58, 2807.7) * mm, "end": v(-369.77, 2808.5) * mm});
            skLineSegment(sketch, "E4054", {"start": v(-369.77, 2808.5) * mm, "end": v(-372.2, 2810) * mm});
            skLineSegment(sketch, "E4055", {"start": v(-372.2, 2810) * mm, "end": v(-375.94, 2812.16) * mm});
            skLineSegment(sketch, "E4056", {"start": v(-375.94, 2812.16) * mm, "end": v(-381, 2814.85) * mm});
            skLineSegment(sketch, "E4057", {"start": v(-381, 2814.85) * mm, "end": v(-387.46, 2817.99) * mm});
            skLineSegment(sketch, "E4058", {"start": v(-387.46, 2817.99) * mm, "end": v(-395.32, 2821.49) * mm});
            skLineSegment(sketch, "E4059", {"start": v(-395.32, 2821.49) * mm, "end": v(-404.64, 2825.24) * mm});
            skLineSegment(sketch, "E4060", {"start": v(-404.64, 2825.24) * mm, "end": v(-415.42, 2829.16) * mm});
            skLineSegment(sketch, "E4061", {"start": v(-415.42, 2829.16) * mm, "end": v(-427.7, 2833.15) * mm});
            skLineSegment(sketch, "E4062", {"start": v(-427.7, 2833.15) * mm, "end": v(-441.5, 2837.1) * mm});
            skLineSegment(sketch, "E4063", {"start": v(-441.5, 2837.1) * mm, "end": v(-456.81, 2840.92) * mm});
            skLineSegment(sketch, "E4064", {"start": v(-456.81, 2840.92) * mm, "end": v(-473.65, 2844.49) * mm});
            skLineSegment(sketch, "E4065", {"start": v(-473.65, 2844.49) * mm, "end": v(-492.02, 2847.72) * mm});
            skLineSegment(sketch, "E4066", {"start": v(-492.02, 2847.72) * mm, "end": v(-511.91, 2850.52) * mm});
            skLineSegment(sketch, "E4067", {"start": v(-511.91, 2850.52) * mm, "end": v(-533.31, 2852.76) * mm});
            skLineSegment(sketch, "E4068", {"start": v(-533.31, 2852.76) * mm, "end": v(-556.21, 2854.36) * mm});
            skLineSegment(sketch, "E4069", {"start": v(-556.21, 2854.36) * mm, "end": v(-580.6, 2855.2) * mm});
            skLineSegment(sketch, "E4070", {"start": v(-580.6, 2855.2) * mm, "end": v(-606.42, 2855.2) * mm});
            skLineSegment(sketch, "E4071", {"start": v(-606.42, 2855.2) * mm, "end": v(-633.66, 2854.25) * mm});
            skLineSegment(sketch, "E4072", {"start": v(-633.66, 2854.25) * mm, "end": v(-662.28, 2852.24) * mm});
            skLineSegment(sketch, "E4073", {"start": v(-662.28, 2852.24) * mm, "end": v(-692.24, 2849.09) * mm});
            skLineSegment(sketch, "E4074", {"start": v(-692.24, 2849.09) * mm, "end": v(-723.5, 2844.7) * mm});
            skLineSegment(sketch, "E4075", {"start": v(-723.5, 2844.7) * mm, "end": v(-756, 2838.96) * mm});
            skLineSegment(sketch, "E4076", {"start": v(-756, 2838.96) * mm, "end": v(-767.14, 2820.04) * mm});
            skLineSegment(sketch, "E4077", {"start": v(-767.14, 2820.04) * mm, "end": v(-805.8, 2740.33) * mm});
            skLineSegment(sketch, "E4078", {"start": v(-805.8, 2740.33) * mm, "end": v(-813.75, 2719.87) * mm});
            skLineSegment(sketch, "E4079", {"start": v(-813.75, 2719.87) * mm, "end": v(-798.13, 2690.8) * mm});
            skLineSegment(sketch, "E4080", {"start": v(-798.13, 2690.8) * mm, "end": v(-782.23, 2663.53) * mm});
            skLineSegment(sketch, "E4081", {"start": v(-782.23, 2663.53) * mm, "end": v(-766.16, 2638.05) * mm});
            skLineSegment(sketch, "E4082", {"start": v(-766.16, 2638.05) * mm, "end": v(-750, 2614.33) * mm});
            skLineSegment(sketch, "E4083", {"start": v(-750, 2614.33) * mm, "end": v(-733.89, 2592.35) * mm});
            skLineSegment(sketch, "E4084", {"start": v(-733.89, 2592.35) * mm, "end": v(-717.9, 2572.07) * mm});
            skLineSegment(sketch, "E4085", {"start": v(-717.9, 2572.07) * mm, "end": v(-702.14, 2553.45) * mm});
            skLineSegment(sketch, "E4086", {"start": v(-702.14, 2553.45) * mm, "end": v(-686.71, 2536.46) * mm});
            skLineSegment(sketch, "E4087", {"start": v(-686.71, 2536.46) * mm, "end": v(-671.7, 2521.04) * mm});
            skLineSegment(sketch, "E4088", {"start": v(-671.7, 2521.04) * mm, "end": v(-657.19, 2507.15) * mm});
            skLineSegment(sketch, "E4089", {"start": v(-657.19, 2507.15) * mm, "end": v(-643.28, 2494.73) * mm});
            skLineSegment(sketch, "E4090", {"start": v(-643.28, 2494.73) * mm, "end": v(-630.04, 2483.72) * mm});
            skLineSegment(sketch, "E4091", {"start": v(-630.04, 2483.72) * mm, "end": v(-617.56, 2474.05) * mm});
            skLineSegment(sketch, "E4092", {"start": v(-617.56, 2474.05) * mm, "end": v(-605.92, 2465.67) * mm});
            skLineSegment(sketch, "E4093", {"start": v(-605.92, 2465.67) * mm, "end": v(-595.19, 2458.5) * mm});
            skLineSegment(sketch, "E4094", {"start": v(-595.19, 2458.5) * mm, "end": v(-585.43, 2452.45) * mm});
            skLineSegment(sketch, "E4095", {"start": v(-585.43, 2452.45) * mm, "end": v(-576.7, 2447.47) * mm});
            skLineSegment(sketch, "E4096", {"start": v(-576.7, 2447.47) * mm, "end": v(-569.1, 2443.45) * mm});
            skLineSegment(sketch, "E4097", {"start": v(-569.1, 2443.45) * mm, "end": v(-562.63, 2440.34) * mm});
            skLineSegment(sketch, "E4098", {"start": v(-562.63, 2440.34) * mm, "end": v(-557.38, 2438.02) * mm});
            skLineSegment(sketch, "E4099", {"start": v(-557.38, 2438.02) * mm, "end": v(-553.39, 2436.42) * mm});
            skLineSegment(sketch, "E4100", {"start": v(-553.39, 2436.42) * mm, "end": v(-550.69, 2435.45) * mm});
            skLineSegment(sketch, "E4101", {"start": v(-550.69, 2435.45) * mm, "end": v(-549.32, 2435) * mm});
            skLineSegment(sketch, "E4102", {"start": v(-549.32, 2435) * mm, "end": v(-357.01, 2380.8) * mm});
            skLineSegment(sketch, "E4103", {"start": v(-357.01, 2380.8) * mm, "end": v(-393.7, 2115.46) * mm});
            skLineSegment(sketch, "E4104", {"start": v(-393.7, 2115.46) * mm, "end": v(-593.5, 2115.45) * mm});
            skLineSegment(sketch, "E4105", {"start": v(-593.5, 2115.45) * mm, "end": v(-594.94, 2115.4) * mm});
            skLineSegment(sketch, "E4106", {"start": v(-594.94, 2115.4) * mm, "end": v(-597.8, 2115.2) * mm});
            skLineSegment(sketch, "E4107", {"start": v(-597.8, 2115.2) * mm, "end": v(-602.08, 2114.74) * mm});
            skLineSegment(sketch, "E4108", {"start": v(-602.08, 2114.74) * mm, "end": v(-607.76, 2113.94) * mm});
            skLineSegment(sketch, "E4109", {"start": v(-607.76, 2113.94) * mm, "end": v(-614.82, 2112.69) * mm});
            skLineSegment(sketch, "E4110", {"start": v(-614.82, 2112.69) * mm, "end": v(-623.24, 2110.9) * mm});
            skLineSegment(sketch, "E4111", {"start": v(-623.24, 2110.9) * mm, "end": v(-632.99, 2108.46) * mm});
            skLineSegment(sketch, "E4112", {"start": v(-632.99, 2108.46) * mm, "end": v(-644.02, 2105.3) * mm});
            skLineSegment(sketch, "E4113", {"start": v(-644.02, 2105.3) * mm, "end": v(-656.3, 2101.3) * mm});
            skLineSegment(sketch, "E4114", {"start": v(-656.3, 2101.3) * mm, "end": v(-669.78, 2096.39) * mm});
            skLineSegment(sketch, "E4115", {"start": v(-669.78, 2096.39) * mm, "end": v(-684.4, 2090.47) * mm});
            skLineSegment(sketch, "E4116", {"start": v(-684.4, 2090.47) * mm, "end": v(-700.14, 2083.47) * mm});
            skLineSegment(sketch, "E4117", {"start": v(-700.14, 2083.47) * mm, "end": v(-716.9, 2075.29) * mm});
            skLineSegment(sketch, "E4118", {"start": v(-716.9, 2075.29) * mm, "end": v(-734.63, 2065.85) * mm});
            skLineSegment(sketch, "E4119", {"start": v(-734.63, 2065.85) * mm, "end": v(-753.27, 2055.1) * mm});
            skLineSegment(sketch, "E4120", {"start": v(-753.27, 2055.1) * mm, "end": v(-772.73, 2042.92) * mm});
            skLineSegment(sketch, "E4121", {"start": v(-772.73, 2042.92) * mm, "end": v(-792.95, 2029.28) * mm});
            skLineSegment(sketch, "E4122", {"start": v(-792.95, 2029.28) * mm, "end": v(-813.84, 2014.1) * mm});
            skLineSegment(sketch, "E4123", {"start": v(-813.84, 2014.1) * mm, "end": v(-835.32, 1997.31) * mm});
            skLineSegment(sketch, "E4124", {"start": v(-835.32, 1997.31) * mm, "end": v(-857.3, 1978.86) * mm});
            skLineSegment(sketch, "E4125", {"start": v(-857.3, 1978.86) * mm, "end": v(-879.68, 1958.7) * mm});
            skLineSegment(sketch, "E4126", {"start": v(-879.68, 1958.7) * mm, "end": v(-902.38, 1936.77) * mm});
            skLineSegment(sketch, "E4127", {"start": v(-902.38, 1936.77) * mm, "end": v(-925.3, 1913.03) * mm});
            skLineSegment(sketch, "E4128", {"start": v(-925.3, 1913.03) * mm, "end": v(-923.2, 1891.18) * mm});
            skLineSegment(sketch, "E4129", {"start": v(-923.2, 1891.18) * mm, "end": v(-907.63, 1803.97) * mm});
            skLineSegment(sketch, "E4130", {"start": v(-907.63, 1803.97) * mm, "end": v(-902.03, 1782.74) * mm});
            skLineSegment(sketch, "E4131", {"start": v(-902.03, 1782.74) * mm, "end": v(-872.3, 1768.4) * mm});
            skLineSegment(sketch, "E4132", {"start": v(-872.3, 1768.4) * mm, "end": v(-843.42, 1755.69) * mm});
            skLineSegment(sketch, "E4133", {"start": v(-843.42, 1755.69) * mm, "end": v(-815.43, 1744.53) * mm});
            skLineSegment(sketch, "E4134", {"start": v(-815.43, 1744.53) * mm, "end": v(-788.43, 1734.83) * mm});
            skLineSegment(sketch, "E4135", {"start": v(-788.43, 1734.83) * mm, "end": v(-762.47, 1726.52) * mm});
            skLineSegment(sketch, "E4136", {"start": v(-762.47, 1726.52) * mm, "end": v(-737.61, 1719.5) * mm});
            skLineSegment(sketch, "E4137", {"start": v(-737.61, 1719.5) * mm, "end": v(-713.92, 1713.7) * mm});
            skLineSegment(sketch, "E4138", {"start": v(-713.92, 1713.7) * mm, "end": v(-691.45, 1709.03) * mm});
            skLineSegment(sketch, "E4139", {"start": v(-691.45, 1709.03) * mm, "end": v(-670.24, 1705.38) * mm});
            skLineSegment(sketch, "E4140", {"start": v(-670.24, 1705.38) * mm, "end": v(-650.33, 1702.67) * mm});
            skLineSegment(sketch, "E4141", {"start": v(-650.33, 1702.67) * mm, "end": v(-631.78, 1700.8) * mm});
            skLineSegment(sketch, "E4142", {"start": v(-631.78, 1700.8) * mm, "end": v(-614.6, 1699.68) * mm});
            skLineSegment(sketch, "E4143", {"start": v(-614.6, 1699.68) * mm, "end": v(-598.83, 1699.19) * mm});
            skLineSegment(sketch, "E4144", {"start": v(-598.83, 1699.19) * mm, "end": v(-584.48, 1699.25) * mm});
            skLineSegment(sketch, "E4145", {"start": v(-584.48, 1699.25) * mm, "end": v(-571.57, 1699.75) * mm});
            skLineSegment(sketch, "E4146", {"start": v(-571.57, 1699.75) * mm, "end": v(-560.13, 1700.6) * mm});
            skLineSegment(sketch, "E4147", {"start": v(-560.13, 1700.6) * mm, "end": v(-550.15, 1701.7) * mm});
            skLineSegment(sketch, "E4148", {"start": v(-550.15, 1701.7) * mm, "end": v(-541.63, 1702.92) * mm});
            skLineSegment(sketch, "E4149", {"start": v(-541.63, 1702.92) * mm, "end": v(-534.57, 1704.2) * mm});
            skLineSegment(sketch, "E4150", {"start": v(-534.57, 1704.2) * mm, "end": v(-528.96, 1705.41) * mm});
            skLineSegment(sketch, "E4151", {"start": v(-528.96, 1705.41) * mm, "end": v(-524.79, 1706.47) * mm});
            skLineSegment(sketch, "E4152", {"start": v(-524.79, 1706.47) * mm, "end": v(-522.03, 1707.27) * mm});
            skLineSegment(sketch, "E4153", {"start": v(-522.03, 1707.27) * mm, "end": v(-520.66, 1707.71) * mm});
            skLineSegment(sketch, "E4154", {"start": v(-520.66, 1707.71) * mm, "end": v(-333.22, 1776.89) * mm});
            skLineSegment(sketch, "E4155", {"start": v(-333.22, 1776.89) * mm, "end": v(-206.94, 1540.66) * mm});
            skLineSegment(sketch, "E4156", {"start": v(-206.94, 1540.66) * mm, "end": v(-368.58, 1423.22) * mm});
            skLineSegment(sketch, "E4157", {"start": v(-368.58, 1423.22) * mm, "end": v(-369.7, 1422.33) * mm});
            skLineSegment(sketch, "E4158", {"start": v(-369.7, 1422.33) * mm, "end": v(-371.9, 1420.48) * mm});
            skLineSegment(sketch, "E4159", {"start": v(-371.9, 1420.48) * mm, "end": v(-375.1, 1417.6) * mm});
            skLineSegment(sketch, "E4160", {"start": v(-375.1, 1417.6) * mm, "end": v(-379.22, 1413.61) * mm});
            skLineSegment(sketch, "E4161", {"start": v(-379.22, 1413.61) * mm, "end": v(-384.2, 1408.45) * mm});
            skLineSegment(sketch, "E4162", {"start": v(-384.2, 1408.45) * mm, "end": v(-389.96, 1402.05) * mm});
            skLineSegment(sketch, "E4163", {"start": v(-389.96, 1402.05) * mm, "end": v(-396.41, 1394.35) * mm});
            skLineSegment(sketch, "E4164", {"start": v(-396.41, 1394.35) * mm, "end": v(-403.48, 1385.3) * mm});
            skLineSegment(sketch, "E4165", {"start": v(-403.48, 1385.3) * mm, "end": v(-411.06, 1374.86) * mm});
            skLineSegment(sketch, "E4166", {"start": v(-411.06, 1374.86) * mm, "end": v(-419.08, 1362.96) * mm});
            skLineSegment(sketch, "E4167", {"start": v(-419.08, 1362.96) * mm, "end": v(-427.44, 1349.57) * mm});
            skLineSegment(sketch, "E4168", {"start": v(-427.44, 1349.57) * mm, "end": v(-436.05, 1334.66) * mm});
            skLineSegment(sketch, "E4169", {"start": v(-436.05, 1334.66) * mm, "end": v(-444.8, 1318.2) * mm});
            skLineSegment(sketch, "E4170", {"start": v(-444.8, 1318.2) * mm, "end": v(-453.6, 1300.14) * mm});
            skLineSegment(sketch, "E4171", {"start": v(-453.6, 1300.14) * mm, "end": v(-462.35, 1280.48) * mm});
            skLineSegment(sketch, "E4172", {"start": v(-462.35, 1280.48) * mm, "end": v(-470.94, 1259.2) * mm});
            skLineSegment(sketch, "E4173", {"start": v(-470.94, 1259.2) * mm, "end": v(-479.28, 1236.27) * mm});
            skLineSegment(sketch, "E4174", {"start": v(-479.28, 1236.27) * mm, "end": v(-487.26, 1211.7) * mm});
            skLineSegment(sketch, "E4175", {"start": v(-487.26, 1211.7) * mm, "end": v(-494.77, 1185.5) * mm});
            skLineSegment(sketch, "E4176", {"start": v(-494.77, 1185.5) * mm, "end": v(-501.7, 1157.66) * mm});
            skLineSegment(sketch, "E4177", {"start": v(-501.7, 1157.66) * mm, "end": v(-507.97, 1128.19) * mm});
            skLineSegment(sketch, "E4178", {"start": v(-507.97, 1128.19) * mm, "end": v(-513.44, 1097.1) * mm});
            skLineSegment(sketch, "E4179", {"start": v(-513.44, 1097.1) * mm, "end": v(-518.03, 1064.43) * mm});
            skLineSegment(sketch, "E4180", {"start": v(-518.03, 1064.43) * mm, "end": v(-503.5, 1047.98) * mm});
            skLineSegment(sketch, "E4181", {"start": v(-503.5, 1047.98) * mm, "end": v(-439.62, 986.58) * mm});
            skLineSegment(sketch, "E4182", {"start": v(-439.62, 986.58) * mm, "end": v(-422.62, 972.7) * mm});
            skLineSegment(sketch, "E4183", {"start": v(-422.62, 972.7) * mm, "end": v(-390.15, 978.57) * mm});
            skLineSegment(sketch, "E4184", {"start": v(-390.15, 978.57) * mm, "end": v(-359.3, 985.27) * mm});
            skLineSegment(sketch, "E4185", {"start": v(-359.3, 985.27) * mm, "end": v(-330.1, 992.68) * mm});
            skLineSegment(sketch, "E4186", {"start": v(-330.1, 992.68) * mm, "end": v(-302.55, 1000.7) * mm});
            skLineSegment(sketch, "E4187", {"start": v(-302.55, 1000.7) * mm, "end": v(-276.66, 1009.25) * mm});
            skLineSegment(sketch, "E4188", {"start": v(-276.66, 1009.25) * mm, "end": v(-252.43, 1018.18) * mm});
            skLineSegment(sketch, "E4189", {"start": v(-252.43, 1018.18) * mm, "end": v(-229.86, 1027.42) * mm});
            skLineSegment(sketch, "E4190", {"start": v(-229.86, 1027.42) * mm, "end": v(-208.93, 1036.84) * mm});
            skLineSegment(sketch, "E4191", {"start": v(-208.93, 1036.84) * mm, "end": v(-189.63, 1046.36) * mm});
            skLineSegment(sketch, "E4192", {"start": v(-189.63, 1046.36) * mm, "end": v(-171.93, 1055.87) * mm});
            skLineSegment(sketch, "E4193", {"start": v(-171.93, 1055.87) * mm, "end": v(-155.82, 1065.26) * mm});
            skLineSegment(sketch, "E4194", {"start": v(-155.82, 1065.26) * mm, "end": v(-141.26, 1074.45) * mm});
            skLineSegment(sketch, "E4195", {"start": v(-141.26, 1074.45) * mm, "end": v(-128.21, 1083.32) * mm});
            skLineSegment(sketch, "E4196", {"start": v(-128.21, 1083.32) * mm, "end": v(-116.64, 1091.8) * mm});
            skLineSegment(sketch, "E4197", {"start": v(-116.64, 1091.8) * mm, "end": v(-106.5, 1099.8) * mm});
            skLineSegment(sketch, "E4198", {"start": v(-106.5, 1099.8) * mm, "end": v(-97.74, 1107.21) * mm});
            skLineSegment(sketch, "E4199", {"start": v(-97.74, 1107.21) * mm, "end": v(-90.3, 1113.96) * mm});
            skLineSegment(sketch, "E4200", {"start": v(-90.3, 1113.96) * mm, "end": v(-84.13, 1119.97) * mm});
            skLineSegment(sketch, "E4201", {"start": v(-84.13, 1119.97) * mm, "end": v(-79.17, 1125.15) * mm});
            skLineSegment(sketch, "E4202", {"start": v(-79.17, 1125.15) * mm, "end": v(-75.34, 1129.42) * mm});
            skLineSegment(sketch, "E4203", {"start": v(-75.34, 1129.42) * mm, "end": v(-72.59, 1132.73) * mm});
            skLineSegment(sketch, "E4204", {"start": v(-72.59, 1132.73) * mm, "end": v(-70.83, 1135) * mm});
            skLineSegment(sketch, "E4205", {"start": v(-70.83, 1135) * mm, "end": v(-69.99, 1136.16) * mm});
            skLineSegment(sketch, "E4206", {"start": v(-69.99, 1136.16) * mm, "end": v(41, 1302.3) * mm});
            skLineSegment(sketch, "E4207", {"start": v(41, 1302.3) * mm, "end": v(282.01, 1185.42) * mm});
            skLineSegment(sketch, "E4208", {"start": v(282.01, 1185.42) * mm, "end": v(220.27, 995.4) * mm});
            skLineSegment(sketch, "E4209", {"start": v(220.27, 995.4) * mm, "end": v(219.88, 994.01) * mm});
            skLineSegment(sketch, "E4210", {"start": v(219.88, 994.01) * mm, "end": v(219.2, 991.23) * mm});
            skLineSegment(sketch, "E4211", {"start": v(219.2, 991.23) * mm, "end": v(218.3, 987.02) * mm});
            skLineSegment(sketch, "E4212", {"start": v(218.3, 987.02) * mm, "end": v(217.3, 981.37) * mm});
            skLineSegment(sketch, "E4213", {"start": v(217.3, 981.37) * mm, "end": v(216.31, 974.26) * mm});
            skLineSegment(sketch, "E4214", {"start": v(216.31, 974.26) * mm, "end": v(215.42, 965.7) * mm});
            skLineSegment(sketch, "E4215", {"start": v(215.42, 965.7) * mm, "end": v(214.72, 955.68) * mm});
            skLineSegment(sketch, "E4216", {"start": v(214.72, 955.68) * mm, "end": v(214.33, 944.21) * mm});
            skLineSegment(sketch, "E4217", {"start": v(214.33, 944.21) * mm, "end": v(214.33, 931.3) * mm});
            skLineSegment(sketch, "E4218", {"start": v(214.33, 931.3) * mm, "end": v(214.83, 916.96) * mm});
            skLineSegment(sketch, "E4219", {"start": v(214.83, 916.96) * mm, "end": v(215.94, 901.22) * mm});
            skLineSegment(sketch, "E4220", {"start": v(215.94, 901.22) * mm, "end": v(217.74, 884.1) * mm});
            skLineSegment(sketch, "E4221", {"start": v(217.74, 884.1) * mm, "end": v(220.34, 865.63) * mm});
            skLineSegment(sketch, "E4222", {"start": v(220.34, 865.63) * mm, "end": v(223.84, 845.85) * mm});
            skLineSegment(sketch, "E4223", {"start": v(223.84, 845.85) * mm, "end": v(228.31, 824.8) * mm});
            skLineSegment(sketch, "E4224", {"start": v(228.31, 824.8) * mm, "end": v(233.87, 802.52) * mm});
            skLineSegment(sketch, "E4225", {"start": v(233.87, 802.52) * mm, "end": v(240.6, 779.08) * mm});
            skLineSegment(sketch, "E4226", {"start": v(240.6, 779.08) * mm, "end": v(248.58, 754.52) * mm});
            skLineSegment(sketch, "E4227", {"start": v(248.58, 754.52) * mm, "end": v(257.9, 728.9) * mm});
            skLineSegment(sketch, "E4228", {"start": v(257.9, 728.9) * mm, "end": v(268.66, 702.3) * mm});
            skLineSegment(sketch, "E4229", {"start": v(268.66, 702.3) * mm, "end": v(280.92, 674.78) * mm});
            skLineSegment(sketch, "E4230", {"start": v(280.92, 674.78) * mm, "end": v(294.76, 646.41) * mm});
            skLineSegment(sketch, "E4231", {"start": v(294.76, 646.41) * mm, "end": v(310.26, 617.28) * mm});
            skLineSegment(sketch, "E4232", {"start": v(310.26, 617.28) * mm, "end": v(331.69, 612.52) * mm});
            skLineSegment(sketch, "E4233", {"start": v(331.69, 612.52) * mm, "end": v(419.45, 600.39) * mm});
            skLineSegment(sketch, "E4234", {"start": v(419.45, 600.39) * mm, "end": v(441.37, 599.15) * mm});
            skLineSegment(sketch, "E4235", {"start": v(441.37, 599.15) * mm, "end": v(464.18, 622.99) * mm});
            skLineSegment(sketch, "E4236", {"start": v(464.18, 622.99) * mm, "end": v(485.2, 646.54) * mm});
            skLineSegment(sketch, "E4237", {"start": v(485.2, 646.54) * mm, "end": v(504.47, 669.7) * mm});
            skLineSegment(sketch, "E4238", {"start": v(504.47, 669.7) * mm, "end": v(522.04, 692.39) * mm});
            skLineSegment(sketch, "E4239", {"start": v(522.04, 692.39) * mm, "end": v(537.96, 714.51) * mm});
            skLineSegment(sketch, "E4240", {"start": v(537.96, 714.51) * mm, "end": v(552.31, 735.98) * mm});
            skLineSegment(sketch, "E4241", {"start": v(552.31, 735.98) * mm, "end": v(565.15, 756.72) * mm});
            skLineSegment(sketch, "E4242", {"start": v(565.15, 756.72) * mm, "end": v(576.54, 776.65) * mm});
            skLineSegment(sketch, "E4243", {"start": v(576.54, 776.65) * mm, "end": v(586.56, 795.7) * mm});
            skLineSegment(sketch, "E4244", {"start": v(586.56, 795.7) * mm, "end": v(595.29, 813.79) * mm});
            skLineSegment(sketch, "E4245", {"start": v(595.29, 813.79) * mm, "end": v(602.8, 830.86) * mm});
            skLineSegment(sketch, "E4246", {"start": v(602.8, 830.86) * mm, "end": v(609.18, 846.85) * mm});
            skLineSegment(sketch, "E4247", {"start": v(609.18, 846.85) * mm, "end": v(614.52, 861.7) * mm});
            skLineSegment(sketch, "E4248", {"start": v(614.52, 861.7) * mm, "end": v(618.9, 875.36) * mm});
            skLineSegment(sketch, "E4249", {"start": v(618.9, 875.36) * mm, "end": v(622.4, 887.79) * mm});
            skLineSegment(sketch, "E4250", {"start": v(622.4, 887.79) * mm, "end": v(625.13, 898.94) * mm});
            skLineSegment(sketch, "E4251", {"start": v(625.13, 898.94) * mm, "end": v(627.18, 908.77) * mm});
            skLineSegment(sketch, "E4252", {"start": v(627.18, 908.77) * mm, "end": v(628.64, 917.25) * mm});
            skLineSegment(sketch, "E4253", {"start": v(628.64, 917.25) * mm, "end": v(629.61, 924.36) * mm});
            skLineSegment(sketch, "E4254", {"start": v(629.61, 924.36) * mm, "end": v(630.2, 930.07) * mm});
            skLineSegment(sketch, "E4255", {"start": v(630.2, 930.07) * mm, "end": v(630.48, 934.37) * mm});
            skLineSegment(sketch, "E4256", {"start": v(630.48, 934.37) * mm, "end": v(630.57, 937.23) * mm});
            skLineSegment(sketch, "E4257", {"start": v(630.57, 937.23) * mm, "end": v(630.57, 938.67) * mm});
            skLineSegment(sketch, "E4258", {"start": v(630.57, 938.67) * mm, "end": v(622.7, 1138.31) * mm});
            skLineSegment(sketch, "E4259", {"start": v(622.7, 1138.31) * mm, "end": v(886.39, 1185.42) * mm});
            skLineSegment(sketch, "E4260", {"start": v(886.39, 1185.42) * mm, "end": v(948.13, 995.4) * mm});
            skLineSegment(sketch, "E4261", {"start": v(948.13, 995.4) * mm, "end": v(948.63, 994.05) * mm});
            skLineSegment(sketch, "E4262", {"start": v(948.63, 994.05) * mm, "end": v(949.7, 991.39) * mm});
            skLineSegment(sketch, "E4263", {"start": v(949.7, 991.39) * mm, "end": v(951.46, 987.46) * mm});
            skLineSegment(sketch, "E4264", {"start": v(951.46, 987.46) * mm, "end": v(953.98, 982.3) * mm});
            skLineSegment(sketch, "E4265", {"start": v(953.98, 982.3) * mm, "end": v(957.35, 975.97) * mm});
            skLineSegment(sketch, "E4266", {"start": v(957.35, 975.97) * mm, "end": v(961.66, 968.52) * mm});
            skLineSegment(sketch, "E4267", {"start": v(961.66, 968.52) * mm, "end": v(966.98, 960) * mm});
            skLineSegment(sketch, "E4268", {"start": v(966.98, 960) * mm, "end": v(973.4, 950.5) * mm});
            skLineSegment(sketch, "E4269", {"start": v(973.4, 950.5) * mm, "end": v(981, 940.05) * mm});
            skLineSegment(sketch, "E4270", {"start": v(981, 940.05) * mm, "end": v(989.84, 928.74) * mm});
            skLineSegment(sketch, "E4271", {"start": v(989.84, 928.74) * mm, "end": v(999.98, 916.66) * mm});
            skLineSegment(sketch, "E4272", {"start": v(999.98, 916.66) * mm, "end": v(1011.5, 903.87) * mm});
            skLineSegment(sketch, "E4273", {"start": v(1011.5, 903.87) * mm, "end": v(1024.47, 890.45) * mm});
            skLineSegment(sketch, "E4274", {"start": v(1024.47, 890.45) * mm, "end": v(1038.92, 876.5) * mm});
            skLineSegment(sketch, "E4275", {"start": v(1038.92, 876.5) * mm, "end": v(1054.91, 862.1) * mm});
            skLineSegment(sketch, "E4276", {"start": v(1054.91, 862.1) * mm, "end": v(1072.5, 847.35) * mm});
            skLineSegment(sketch, "E4277", {"start": v(1072.5, 847.35) * mm, "end": v(1091.72, 832.34) * mm});
            skLineSegment(sketch, "E4278", {"start": v(1091.72, 832.34) * mm, "end": v(1112.62, 817.17) * mm});
            skLineSegment(sketch, "E4279", {"start": v(1112.62, 817.17) * mm, "end": v(1135.22, 801.93) * mm});
            skLineSegment(sketch, "E4280", {"start": v(1135.22, 801.93) * mm, "end": v(1159.56, 786.72) * mm});
            skLineSegment(sketch, "E4281", {"start": v(1159.56, 786.72) * mm, "end": v(1185.65, 771.66) * mm});
            skLineSegment(sketch, "E4282", {"start": v(1185.65, 771.66) * mm, "end": v(1213.52, 756.85) * mm});
            skLineSegment(sketch, "E4283", {"start": v(1213.52, 756.85) * mm, "end": v(1243.18, 742.39) * mm});
            skLineSegment(sketch, "E4284", {"start": v(1243.18, 742.39) * mm, "end": v(1263.32, 751.13) * mm});
            skLineSegment(sketch, "E4285", {"start": v(1263.32, 751.13) * mm, "end": v(1341.45, 792.9) * mm});
            skLineSegment(sketch, "E4286", {"start": v(1341.45, 792.9) * mm, "end": v(1359.9, 804.78) * mm});
            skLineSegment(sketch, "E4287", {"start": v(1359.9, 804.78) * mm, "end": v(1364.35, 837.48) * mm});
            skLineSegment(sketch, "E4288", {"start": v(1364.35, 837.48) * mm, "end": v(1367.52, 868.89) * mm});
            skLineSegment(sketch, "E4289", {"start": v(1367.52, 868.89) * mm, "end": v(1369.49, 898.95) * mm});
            skLineSegment(sketch, "E4290", {"start": v(1369.49, 898.95) * mm, "end": v(1370.37, 927.63) * mm});
            skLineSegment(sketch, "E4291", {"start": v(1370.37, 927.63) * mm, "end": v(1370.25, 954.9) * mm});
            skLineSegment(sketch, "E4292", {"start": v(1370.25, 954.9) * mm, "end": v(1369.24, 980.7) * mm});
            skLineSegment(sketch, "E4293", {"start": v(1369.24, 980.7) * mm, "end": v(1367.43, 1005.02) * mm});
            skLineSegment(sketch, "E4294", {"start": v(1367.43, 1005.02) * mm, "end": v(1364.93, 1027.84) * mm});
            skLineSegment(sketch, "E4295", {"start": v(1364.93, 1027.84) * mm, "end": v(1361.85, 1049.13) * mm});
            skLineSegment(sketch, "E4296", {"start": v(1361.85, 1049.13) * mm, "end": v(1358.27, 1068.9) * mm});
            skLineSegment(sketch, "E4297", {"start": v(1358.27, 1068.9) * mm, "end": v(1354.32, 1087.13) * mm});
            skLineSegment(sketch, "E4298", {"start": v(1354.32, 1087.13) * mm, "end": v(1350.08, 1103.82) * mm});
            skLineSegment(sketch, "E4299", {"start": v(1350.08, 1103.82) * mm, "end": v(1345.67, 1118.97) * mm});
            skLineSegment(sketch, "E4300", {"start": v(1345.67, 1118.97) * mm, "end": v(1341.18, 1132.6) * mm});
            skLineSegment(sketch, "E4301", {"start": v(1341.18, 1132.6) * mm, "end": v(1336.71, 1144.7) * mm});
            skLineSegment(sketch, "E4302", {"start": v(1336.71, 1144.7) * mm, "end": v(1332.37, 1155.33) * mm});
            skLineSegment(sketch, "E4303", {"start": v(1332.37, 1155.33) * mm, "end": v(1328.25, 1164.49) * mm});
            skLineSegment(sketch, "E4304", {"start": v(1328.25, 1164.49) * mm, "end": v(1324.44, 1172.21) * mm});
            skLineSegment(sketch, "E4305", {"start": v(1324.44, 1172.21) * mm, "end": v(1321.05, 1178.53) * mm});
            skLineSegment(sketch, "E4306", {"start": v(1321.05, 1178.53) * mm, "end": v(1318.16, 1183.5) * mm});
            skLineSegment(sketch, "E4307", {"start": v(1318.16, 1183.5) * mm, "end": v(1315.87, 1187.13) * mm});
            skLineSegment(sketch, "E4308", {"start": v(1315.87, 1187.13) * mm, "end": v(1314.26, 1189.5) * mm});
            skLineSegment(sketch, "E4309", {"start": v(1314.26, 1189.5) * mm, "end": v(1313.41, 1190.67) * mm});
            skLineSegment(sketch, "E4310", {"start": v(1313.41, 1190.67) * mm, "end": v(1189.7, 1347.56) * mm});
            skLineSegment(sketch, "E4311", {"start": v(1189.7, 1347.56) * mm, "end": v(1375.34, 1540.66) * mm});
            skLineSegment(sketch, "E4312", {"start": v(1375.34, 1540.66) * mm, "end": v(1536.98, 1423.22) * mm});
            skLineSegment(sketch, "E4313", {"start": v(1536.98, 1423.22) * mm, "end": v(1538.18, 1422.42) * mm});
            skLineSegment(sketch, "E4314", {"start": v(1538.18, 1422.42) * mm, "end": v(1540.61, 1420.9) * mm});
            skLineSegment(sketch, "E4315", {"start": v(1540.61, 1420.9) * mm, "end": v(1544.34, 1418.76) * mm});
            skLineSegment(sketch, "E4316", {"start": v(1544.34, 1418.76) * mm, "end": v(1549.4, 1416.07) * mm});
            skLineSegment(sketch, "E4317", {"start": v(1549.4, 1416.07) * mm, "end": v(1555.86, 1412.93) * mm});
            skLineSegment(sketch, "E4318", {"start": v(1555.86, 1412.93) * mm, "end": v(1563.72, 1409.43) * mm});
            skLineSegment(sketch, "E4319", {"start": v(1563.72, 1409.43) * mm, "end": v(1573.04, 1405.67) * mm});
            skLineSegment(sketch, "E4320", {"start": v(1573.04, 1405.67) * mm, "end": v(1583.82, 1401.75) * mm});
            skLineSegment(sketch, "E4321", {"start": v(1583.82, 1401.75) * mm, "end": v(1596.1, 1397.76) * mm});
            skLineSegment(sketch, "E4322", {"start": v(1596.1, 1397.76) * mm, "end": v(1609.9, 1393.81) * mm});
            skLineSegment(sketch, "E4323", {"start": v(1609.9, 1393.81) * mm, "end": v(1625.21, 1390) * mm});
            skLineSegment(sketch, "E4324", {"start": v(1625.21, 1390) * mm, "end": v(1642.05, 1386.42) * mm});
            skLineSegment(sketch, "E4325", {"start": v(1642.05, 1386.42) * mm, "end": v(1660.42, 1383.19) * mm});
            skLineSegment(sketch, "E4326", {"start": v(1660.42, 1383.19) * mm, "end": v(1680.31, 1380.4) * mm});
            skLineSegment(sketch, "E4327", {"start": v(1680.31, 1380.4) * mm, "end": v(1701.72, 1378.15) * mm});
            skLineSegment(sketch, "E4328", {"start": v(1701.72, 1378.15) * mm, "end": v(1724.62, 1376.55) * mm});
            skLineSegment(sketch, "E4329", {"start": v(1724.62, 1376.55) * mm, "end": v(1749, 1375.7) * mm});
            skLineSegment(sketch, "E4330", {"start": v(1749, 1375.7) * mm, "end": v(1774.82, 1375.71) * mm});
            skLineSegment(sketch, "E4331", {"start": v(1774.82, 1375.71) * mm, "end": v(1802.06, 1376.67) * mm});
            skLineSegment(sketch, "E4332", {"start": v(1802.06, 1376.67) * mm, "end": v(1830.68, 1378.67) * mm});
            skLineSegment(sketch, "E4333", {"start": v(1830.68, 1378.67) * mm, "end": v(1860.65, 1381.83) * mm});
            skLineSegment(sketch, "E4334", {"start": v(1860.65, 1381.83) * mm, "end": v(1891.9, 1386.22) * mm});
            skLineSegment(sketch, "E4335", {"start": v(1891.9, 1386.22) * mm, "end": v(1924.4, 1391.96) * mm});
            skLineSegment(sketch, "E4336", {"start": v(1924.4, 1391.96) * mm, "end": v(1935.55, 1410.87) * mm});
            skLineSegment(sketch, "E4337", {"start": v(1935.55, 1410.87) * mm, "end": v(1974.2, 1490.58) * mm});
            skLineSegment(sketch, "E4338", {"start": v(1974.2, 1490.58) * mm, "end": v(1982.15, 1511.05) * mm});
            skLineSegment(sketch, "E4339", {"start": v(1982.15, 1511.05) * mm, "end": v(1966.53, 1540.12) * mm});
            skLineSegment(sketch, "E4340", {"start": v(1966.53, 1540.12) * mm, "end": v(1950.63, 1567.38) * mm});
            skLineSegment(sketch, "E4341", {"start": v(1950.63, 1567.38) * mm, "end": v(1934.56, 1592.86) * mm});
            skLineSegment(sketch, "E4342", {"start": v(1934.56, 1592.86) * mm, "end": v(1918.4, 1616.58) * mm});
            skLineSegment(sketch, "E4343", {"start": v(1918.4, 1616.58) * mm, "end": v(1902.29, 1638.56) * mm});
            skLineSegment(sketch, "E4344", {"start": v(1902.29, 1638.56) * mm, "end": v(1886.3, 1658.85) * mm});
            skLineSegment(sketch, "E4345", {"start": v(1886.3, 1658.85) * mm, "end": v(1870.55, 1677.46) * mm});
            skLineSegment(sketch, "E4346", {"start": v(1870.55, 1677.46) * mm, "end": v(1855.11, 1694.46) * mm});
            skLineSegment(sketch, "E4347", {"start": v(1855.11, 1694.46) * mm, "end": v(1840.1, 1709.87) * mm});
            skLineSegment(sketch, "E4348", {"start": v(1840.1, 1709.87) * mm, "end": v(1825.59, 1723.76) * mm});
            skLineSegment(sketch, "E4349", {"start": v(1825.59, 1723.76) * mm, "end": v(1811.68, 1736.18) * mm});
            skLineSegment(sketch, "E4350", {"start": v(1811.68, 1736.18) * mm, "end": v(1798.44, 1747.2) * mm});
            skLineSegment(sketch, "E4351", {"start": v(1798.44, 1747.2) * mm, "end": v(1785.96, 1756.86) * mm});
            skLineSegment(sketch, "E4352", {"start": v(1785.96, 1756.86) * mm, "end": v(1774.32, 1765.24) * mm});
            skLineSegment(sketch, "E4353", {"start": v(1774.32, 1765.24) * mm, "end": v(1763.59, 1772.42) * mm});
            skLineSegment(sketch, "E4354", {"start": v(1763.59, 1772.42) * mm, "end": v(1753.83, 1778.46) * mm});
            skLineSegment(sketch, "E4355", {"start": v(1753.83, 1778.46) * mm, "end": v(1745.11, 1783.45) * mm});
            skLineSegment(sketch, "E4356", {"start": v(1745.11, 1783.45) * mm, "end": v(1737.5, 1787.46) * mm});
            skLineSegment(sketch, "E4357", {"start": v(1737.5, 1787.46) * mm, "end": v(1731.03, 1790.58) * mm});
            skLineSegment(sketch, "E4358", {"start": v(1731.03, 1790.58) * mm, "end": v(1725.78, 1792.9) * mm});
            skLineSegment(sketch, "E4359", {"start": v(1725.78, 1792.9) * mm, "end": v(1721.79, 1794.5) * mm});
            skLineSegment(sketch, "E4360", {"start": v(1721.79, 1794.5) * mm, "end": v(1719.09, 1795.46) * mm});
            skLineSegment(sketch, "E4361", {"start": v(1719.09, 1795.46) * mm, "end": v(1717.72, 1795.9) * mm});
            skLineSegment(sketch, "E4362", {"start": v(1717.72, 1795.9) * mm, "end": v(1525.41, 1850.12) * mm});
            skLineSegment(sketch, "E4363", {"start": v(1525.41, 1850.12) * mm, "end": v(1562.1, 2115.46) * mm});
            skLineSegment(sketch, "E4364", {"start": v(1562.1, 2115.46) * mm, "end": v(1761.9, 2115.46) * mm});
            skLineSegment(sketch, "E4365", {"start": v(1761.9, 2115.46) * mm, "end": v(1763.34, 2115.51) * mm});
            skLineSegment(sketch, "E4366", {"start": v(1763.34, 2115.51) * mm, "end": v(1766.2, 2115.72) * mm});
            skLineSegment(sketch, "E4367", {"start": v(787.4, 2115.46) * mm, "end": v(381, 2115.46) * mm});
            skFitSpline(sketch, "E4368", {"points": [v(1934.1, 2338.79) * mm, v(1934.1, 2283.73) * mm, v(1889.47, 2239.1) * mm, v(1834.4, 2239.1) * mm]});
            skFitSpline(sketch, "E4369", {"points": [v(1834.4, 2239.1) * mm, v(1779.35, 2239.1) * mm, v(1734.71, 2283.73) * mm, v(1734.71, 2338.79) * mm]});
            skFitSpline(sketch, "E4370", {"points": [v(1734.71, 2338.79) * mm, v(1734.71, 2393.85) * mm, v(1779.35, 2438.48) * mm, v(1834.4, 2438.48) * mm]});
            skFitSpline(sketch, "E4371", {"points": [v(1834.4, 2438.48) * mm, v(1889.47, 2438.48) * mm, v(1934.1, 2393.85) * mm, v(1934.1, 2338.79) * mm]});
            skLineSegment(sketch, "E4372", {"start": v(584.2, 1912.26) * mm, "end": v(584.2, 2318.66) * mm});
            skLineSegment(sketch, "E4373", {"start": v(72.34, 2656.78) * mm, "end": v(55.68, 2640.53) * mm});
            skLineSegment(sketch, "E4374", {"start": v(55.68, 2640.53) * mm, "end": v(39.62, 2623.86) * mm});
            skLineSegment(sketch, "E4375", {"start": v(39.62, 2623.86) * mm, "end": v(23.98, 2606.6) * mm});
            skLineSegment(sketch, "E4376", {"start": v(23.98, 2606.6) * mm, "end": v(8.94, 2588.91) * mm});
            skLineSegment(sketch, "E4377", {"start": v(73.56, 2592.16) * mm, "end": v(5.49, 2655.56) * mm});
            skLineSegment(sketch, "E4378", {"start": v(40.44, 2690.72) * mm, "end": v(39.22, 2656.98) * mm});
            skLineSegment(sketch, "E4379", {"start": v(39.22, 2656.98) * mm, "end": v(39.62, 2623.86) * mm});
            skLineSegment(sketch, "E4380", {"start": v(39.62, 2623.86) * mm, "end": v(41.45, 2591.15) * mm});
            skLineSegment(sketch, "E4381", {"start": v(41.45, 2591.15) * mm, "end": v(44.7, 2559.25) * mm});
            skLineSegment(sketch, "E4382", {"start": v(104.24, 2623.05) * mm, "end": v(72.14, 2624.27) * mm});
            skLineSegment(sketch, "E4383", {"start": v(72.14, 2624.27) * mm, "end": v(39.62, 2623.86) * mm});
            skLineSegment(sketch, "E4384", {"start": v(39.62, 2623.86) * mm, "end": v(6.5, 2621.83) * mm});
            skLineSegment(sketch, "E4385", {"start": v(6.5, 2621.83) * mm, "end": v(-27.03, 2618.38) * mm});
            skLineSegment(sketch, "E4386", {"start": v(194.87, 2723.23) * mm, "end": v(175.97, 2710.63) * mm});
            skLineSegment(sketch, "E4387", {"start": v(175.97, 2710.63) * mm, "end": v(157.68, 2697.62) * mm});
            skLineSegment(sketch, "E4388", {"start": v(157.68, 2697.62) * mm, "end": v(139.6, 2684.01) * mm});
            skLineSegment(sketch, "E4389", {"start": v(139.6, 2684.01) * mm, "end": v(122.12, 2669.99) * mm});
            skLineSegment(sketch, "E4390", {"start": v(122.12, 2669.99) * mm, "end": v(120.5, 2708.6) * mm});
            skLineSegment(sketch, "E4391", {"start": v(120.5, 2708.6) * mm, "end": v(120.9, 2747.82) * mm});
            skLineSegment(sketch, "E4392", {"start": v(120.9, 2747.82) * mm, "end": v(123.34, 2787.44) * mm});
            skLineSegment(sketch, "E4393", {"start": v(123.34, 2787.44) * mm, "end": v(202.39, 2672.22) * mm});
            skLineSegment(sketch, "E4394", {"start": v(401.52, 2909.56) * mm, "end": v(432.82, 2773.42) * mm});
            skLineSegment(sketch, "E4395", {"start": v(432.82, 2773.42) * mm, "end": v(403.56, 2802.27) * mm});
            skLineSegment(sketch, "E4396", {"start": v(403.56, 2802.27) * mm, "end": v(372.26, 2829.7) * mm});
            skLineSegment(sketch, "E4397", {"start": v(372.26, 2829.7) * mm, "end": v(338.94, 2855.92) * mm});
            skLineSegment(sketch, "E4398", {"start": v(338.94, 2855.92) * mm, "end": v(303.99, 2880.7) * mm});
            skLineSegment(sketch, "E4399", {"start": v(303.99, 2880.7) * mm, "end": v(351.94, 2749.44) * mm});
            skLineSegment(sketch, "E4400", {"start": v(554.53, 2883.15) * mm, "end": v(530.56, 2881.93) * mm});
            skLineSegment(sketch, "E4401", {"start": v(530.56, 2881.93) * mm, "end": v(506.58, 2879.9) * mm});
            skLineSegment(sketch, "E4402", {"start": v(506.58, 2879.9) * mm, "end": v(482.8, 2877.05) * mm});
            skLineSegment(sketch, "E4403", {"start": v(482.8, 2877.05) * mm, "end": v(459.03, 2873.6) * mm});
            skLineSegment(sketch, "E4404", {"start": v(556.36, 2836.61) * mm, "end": v(533.8, 2835.4) * mm});
            skLineSegment(sketch, "E4405", {"start": v(533.8, 2835.4) * mm, "end": v(511.45, 2833.57) * mm});
            skLineSegment(sketch, "E4406", {"start": v(511.45, 2833.57) * mm, "end": v(488.9, 2830.92) * mm});
            skLineSegment(sketch, "E4407", {"start": v(488.9, 2830.92) * mm, "end": v(466.75, 2827.67) * mm});
            skLineSegment(sketch, "E4408", {"start": v(603.1, 2906.92) * mm, "end": v(629.1, 2929.07) * mm});
            skLineSegment(sketch, "E4409", {"start": v(629.1, 2929.07) * mm, "end": v(621.39, 2789.67) * mm});
            skLineSegment(sketch, "E4410", {"start": v(642.52, 2788.25) * mm, "end": v(621.39, 2789.67) * mm});
            skLineSegment(sketch, "E4411", {"start": v(621.39, 2789.67) * mm, "end": v(600.25, 2790.49) * mm});
            skLineSegment(sketch, "E4412", {"start": v(752.04, 2793.54) * mm, "end": v(725.83, 2775.65) * mm});
            skLineSegment(sketch, "E4413", {"start": v(725.83, 2775.65) * mm, "end": v(705.1, 2779.72) * mm});
            skLineSegment(sketch, "E4414", {"start": v(705.1, 2779.72) * mm, "end": v(687.83, 2806.13) * mm});
            skLineSegment(sketch, "E4415", {"start": v(687.83, 2806.13) * mm, "end": v(701.65, 2898.39) * mm});
            skLineSegment(sketch, "E4416", {"start": v(701.65, 2898.39) * mm, "end": v(730.3, 2917.28) * mm});
            skLineSegment(sketch, "E4417", {"start": v(730.3, 2917.28) * mm, "end": v(755.3, 2912.2) * mm});
            skLineSegment(sketch, "E4418", {"start": v(755.3, 2912.2) * mm, "end": v(774.4, 2883.96) * mm});
            skLineSegment(sketch, "E4419", {"start": v(774.4, 2883.96) * mm, "end": v(752.04, 2793.54) * mm});
            skLineSegment(sketch, "E4420", {"start": v(915.82, 2782.56) * mm, "end": v(936.55, 2772) * mm});
            skLineSegment(sketch, "E4421", {"start": v(936.55, 2772) * mm, "end": v(956.87, 2760.62) * mm});
            skLineSegment(sketch, "E4422", {"start": v(956.87, 2760.62) * mm, "end": v(976.99, 2748.63) * mm});
            skLineSegment(sketch, "E4423", {"start": v(976.99, 2748.63) * mm, "end": v(1009.3, 2755.54) * mm});
            skLineSegment(sketch, "E4424", {"start": v(1009.3, 2755.54) * mm, "end": v(1022.3, 2774.84) * mm});
            skLineSegment(sketch, "E4425", {"start": v(1022.3, 2774.84) * mm, "end": v(1013.77, 2807.96) * mm});
            skLineSegment(sketch, "E4426", {"start": v(1013.77, 2807.96) * mm, "end": v(991.82, 2820.97) * mm});
            skLineSegment(sketch, "E4427", {"start": v(991.82, 2820.97) * mm, "end": v(969.67, 2833.36) * mm});
            skLineSegment(sketch, "E4428", {"start": v(969.67, 2833.36) * mm, "end": v(947.12, 2845.15) * mm});
            skLineSegment(sketch, "E4429", {"start": v(947.12, 2845.15) * mm, "end": v(884.73, 2719.98) * mm});
            skLineSegment(sketch, "E4430", {"start": v(992.23, 2653.33) * mm, "end": v(1048.51, 2727.7) * mm});
            skLineSegment(sketch, "E4431", {"start": v(1062.53, 2746.19) * mm, "end": v(1076.76, 2764.68) * mm});
            skLineSegment(sketch, "E4432", {"start": v(1102.56, 2583.63) * mm, "end": v(1071.07, 2583.43) * mm});
            skLineSegment(sketch, "E4433", {"start": v(1071.07, 2583.43) * mm, "end": v(1072.5, 2614.92) * mm});
            skLineSegment(sketch, "E4434", {"start": v(1072.5, 2614.92) * mm, "end": v(1153.77, 2698.23) * mm});
            skLineSegment(sketch, "E4435", {"start": v(1154.58, 2630.37) * mm, "end": v(1138.12, 2647.84) * mm});
            skLineSegment(sketch, "E4436", {"start": v(1138.12, 2647.84) * mm, "end": v(1121.26, 2664.9) * mm});
            skLineSegment(sketch, "E4437", {"start": v(1121.26, 2664.9) * mm, "end": v(1103.78, 2681.57) * mm});
            skLineSegment(sketch, "E4438", {"start": v(1103.78, 2681.57) * mm, "end": v(1085.9, 2697.42) * mm});
            skLineSegment(sketch, "E4439", {"start": v(1160.88, 2466.59) * mm, "end": v(1149.7, 2484.47) * mm});
            skLineSegment(sketch, "E4440", {"start": v(1149.7, 2484.47) * mm, "end": v(1137.92, 2501.94) * mm});
            skLineSegment(sketch, "E4441", {"start": v(1137.92, 2501.94) * mm, "end": v(1125.53, 2519.01) * mm});
            skLineSegment(sketch, "E4442", {"start": v(1125.53, 2519.01) * mm, "end": v(1130.8, 2550.3) * mm});
            skLineSegment(sketch, "E4443", {"start": v(1130.8, 2550.3) * mm, "end": v(1167.38, 2579.16) * mm});
            skLineSegment(sketch, "E4444", {"start": v(1167.38, 2579.16) * mm, "end": v(1200.3, 2574.69) * mm});
            skLineSegment(sketch, "E4445", {"start": v(1200.3, 2574.69) * mm, "end": v(1214.32, 2555.18) * mm});
            skLineSegment(sketch, "E4446", {"start": v(1214.32, 2555.18) * mm, "end": v(1227.73, 2535.27) * mm});
            skLineSegment(sketch, "E4447", {"start": v(1227.73, 2535.27) * mm, "end": v(1240.54, 2514.95) * mm});
            skLineSegment(sketch, "E4448", {"start": v(1222.86, 2451.55) * mm, "end": v(1254.15, 2441.6) * mm});
            skLineSegment(sketch, "E4449", {"start": v(1254.15, 2441.6) * mm, "end": v(1285.24, 2430.01) * mm});
            skLineSegment(sketch, "E4450", {"start": v(1285.24, 2430.01) * mm, "end": v(1294.59, 2408.06) * mm});
            skLineSegment(sketch, "E4451", {"start": v(1294.59, 2408.06) * mm, "end": v(1281.58, 2377.58) * mm});
            skLineSegment(sketch, "E4452", {"start": v(1281.58, 2377.58) * mm, "end": v(1216.36, 2353) * mm});
            skLineSegment(sketch, "E4453", {"start": v(1181.81, 2429.8) * mm, "end": v(1305.36, 2494.83) * mm});
            skLineSegment(sketch, "E4454", {"start": v(1252.73, 2210.15) * mm, "end": v(1255.37, 2189.22) * mm});
            skLineSegment(sketch, "E4455", {"start": v(1255.37, 2189.22) * mm, "end": v(1257.4, 2168.09) * mm});
            skLineSegment(sketch, "E4456", {"start": v(1257.4, 2168.09) * mm, "end": v(1258.62, 2147.16) * mm});
            skLineSegment(sketch, "E4457", {"start": v(1258.62, 2147.16) * mm, "end": v(1282.6, 2126.43) * mm});
            skLineSegment(sketch, "E4458", {"start": v(1282.6, 2126.43) * mm, "end": v(1375.66, 2127.85) * mm});
            skLineSegment(sketch, "E4459", {"start": v(1375.66, 2127.85) * mm, "end": v(1398.22, 2153.66) * mm});
            skLineSegment(sketch, "E4460", {"start": v(1398.22, 2153.66) * mm, "end": v(1396.6, 2179.06) * mm});
            skLineSegment(sketch, "E4461", {"start": v(1396.6, 2179.06) * mm, "end": v(1394.16, 2204.46) * mm});
            skLineSegment(sketch, "E4462", {"start": v(1394.16, 2204.46) * mm, "end": v(1391.1, 2229.66) * mm});
            skLineSegment(sketch, "E4463", {"start": v(1394.16, 2204.46) * mm, "end": v(1255.37, 2189.22) * mm});
            skLineSegment(sketch, "E4464", {"start": v(1341.32, 1983.99) * mm, "end": v(1344.98, 2007.76) * mm});
            skLineSegment(sketch, "E4465", {"start": v(1344.98, 2007.76) * mm, "end": v(1348.03, 2031.54) * mm});
            skLineSegment(sketch, "E4466", {"start": v(1348.03, 2031.54) * mm, "end": v(1350.26, 2055.51) * mm});
            skLineSegment(sketch, "E4467", {"start": v(1350.26, 2055.51) * mm, "end": v(1351.69, 2079.5) * mm});
            skLineSegment(sketch, "E4468", {"start": v(1295.4, 1991.91) * mm, "end": v(1298.85, 2014.26) * mm});
            skLineSegment(sketch, "E4469", {"start": v(1298.85, 2014.26) * mm, "end": v(1301.7, 2036.62) * mm});
            skLineSegment(sketch, "E4470", {"start": v(1301.7, 2036.62) * mm, "end": v(1303.73, 2059.17) * mm});
            skLineSegment(sketch, "E4471", {"start": v(1303.73, 2059.17) * mm, "end": v(1305.15, 2081.73) * mm});
            skLineSegment(sketch, "E4472", {"start": v(1216.36, 1877.92) * mm, "end": v(1223.47, 1897.83) * mm});
            skLineSegment(sketch, "E4473", {"start": v(1223.47, 1897.83) * mm, "end": v(1229.97, 1917.95) * mm});
            skLineSegment(sketch, "E4474", {"start": v(1229.97, 1917.95) * mm, "end": v(1235.66, 1938.27) * mm});
            skLineSegment(sketch, "E4475", {"start": v(1235.66, 1938.27) * mm, "end": v(1240.94, 1958.59) * mm});
            skLineSegment(sketch, "E4476", {"start": v(1240.94, 1958.59) * mm, "end": v(1286.26, 1947.82) * mm});
            skLineSegment(sketch, "E4477", {"start": v(1286.26, 1947.82) * mm, "end": v(1303.12, 1919.78) * mm});
            skLineSegment(sketch, "E4478", {"start": v(1303.12, 1919.78) * mm, "end": v(1296.62, 1897.42) * mm});
            skLineSegment(sketch, "E4479", {"start": v(1296.62, 1897.42) * mm, "end": v(1289.5, 1875.27) * mm});
            skLineSegment(sketch, "E4480", {"start": v(1289.5, 1875.27) * mm, "end": v(1303.53, 1845.2) * mm});
            skLineSegment(sketch, "E4481", {"start": v(1303.53, 1845.2) * mm, "end": v(1325.27, 1837.07) * mm});
            skLineSegment(sketch, "E4482", {"start": v(1325.27, 1837.07) * mm, "end": v(1355.55, 1852.92) * mm});
            skLineSegment(sketch, "E4483", {"start": v(1355.55, 1852.92) * mm, "end": v(1363.47, 1877.1) * mm});
            skLineSegment(sketch, "E4484", {"start": v(1363.47, 1877.1) * mm, "end": v(1370.58, 1901.49) * mm});
            skLineSegment(sketch, "E4485", {"start": v(1370.58, 1901.49) * mm, "end": v(1354.13, 1931.56) * mm});
            skLineSegment(sketch, "E4486", {"start": v(1221.44, 1829.35) * mm, "end": v(1200.3, 1838.9) * mm});
            skLineSegment(sketch, "E4487", {"start": v(1252.53, 1649.11) * mm, "end": v(1266.75, 1670.04) * mm});
            skLineSegment(sketch, "E4488", {"start": v(1266.75, 1670.04) * mm, "end": v(1280.36, 1691.78) * mm});
            skLineSegment(sketch, "E4489", {"start": v(1280.36, 1691.78) * mm, "end": v(1293.17, 1713.73) * mm});
            skLineSegment(sketch, "E4490", {"start": v(1293.17, 1713.73) * mm, "end": v(1305.36, 1736.08) * mm});
            skLineSegment(sketch, "E4491", {"start": v(1305.36, 1736.08) * mm, "end": v(1264.1, 1757.62) * mm});
            skLineSegment(sketch, "E4492", {"start": v(1264.1, 1757.62) * mm, "end": v(1252.73, 1736.7) * mm});
            skLineSegment(sketch, "E4493", {"start": v(1252.73, 1736.7) * mm, "end": v(1240.54, 1715.97) * mm});
            skLineSegment(sketch, "E4494", {"start": v(1240.54, 1715.97) * mm, "end": v(1227.73, 1695.65) * mm});
            skLineSegment(sketch, "E4495", {"start": v(1227.73, 1695.65) * mm, "end": v(1195.22, 1688.94) * mm});
            skLineSegment(sketch, "E4496", {"start": v(1195.22, 1688.94) * mm, "end": v(1157.02, 1715.76) * mm});
            skLineSegment(sketch, "E4497", {"start": v(1157.02, 1715.76) * mm, "end": v(1149.7, 1746.45) * mm});
            skLineSegment(sketch, "E4498", {"start": v(1149.7, 1746.45) * mm, "end": v(1160.88, 1764.33) * mm});
            skLineSegment(sketch, "E4499", {"start": v(1160.88, 1764.33) * mm, "end": v(1171.65, 1782.62) * mm});
            skLineSegment(sketch, "E4500", {"start": v(1171.65, 1782.62) * mm, "end": v(1202.33, 1790.13) * mm});
            skLineSegment(sketch, "E4501", {"start": v(1088.14, 1566.61) * mm, "end": v(1070.66, 1551.17) * mm});
            skLineSegment(sketch, "E4502", {"start": v(1070.66, 1551.17) * mm, "end": v(1052.78, 1536.13) * mm});
            skLineSegment(sketch, "E4503", {"start": v(1052.78, 1536.13) * mm, "end": v(1034.5, 1521.9) * mm});
            skLineSegment(sketch, "E4504", {"start": v(1034.5, 1521.9) * mm, "end": v(1029.2, 1489) * mm});
            skLineSegment(sketch, "E4505", {"start": v(1029.2, 1489) * mm, "end": v(1042.62, 1470.1) * mm});
            skLineSegment(sketch, "E4506", {"start": v(1042.62, 1470.1) * mm, "end": v(1076.76, 1466.23) * mm});
            skLineSegment(sketch, "E4507", {"start": v(1076.76, 1466.23) * mm, "end": v(1096.67, 1481.88) * mm});
            skLineSegment(sketch, "E4508", {"start": v(1096.67, 1481.88) * mm, "end": v(1116.18, 1498.14) * mm});
            skLineSegment(sketch, "E4509", {"start": v(1116.18, 1498.14) * mm, "end": v(1135.28, 1515.2) * mm});
            skLineSegment(sketch, "E4510", {"start": v(1135.28, 1515.2) * mm, "end": v(1040.8, 1618.02) * mm});
            skLineSegment(sketch, "E4511", {"start": v(904.65, 1417.06) * mm, "end": v(926.19, 1427.42) * mm});
            skLineSegment(sketch, "E4512", {"start": v(926.19, 1427.42) * mm, "end": v(947.52, 1438.4) * mm});
            skLineSegment(sketch, "E4513", {"start": v(947.52, 1438.4) * mm, "end": v(968.65, 1450.18) * mm});
            skLineSegment(sketch, "E4514", {"start": v(968.65, 1450.18) * mm, "end": v(989.18, 1462.58) * mm});
            skLineSegment(sketch, "E4515", {"start": v(885.14, 1459.53) * mm, "end": v(905.46, 1469.08) * mm});
            skLineSegment(sketch, "E4516", {"start": v(905.46, 1469.08) * mm, "end": v(925.58, 1479.44) * mm});
            skLineSegment(sketch, "E4517", {"start": v(925.58, 1479.44) * mm, "end": v(945.29, 1490.41) * mm});
            skLineSegment(sketch, "E4518", {"start": v(945.29, 1490.41) * mm, "end": v(964.6, 1502) * mm});
            skLineSegment(sketch, "E4519", {"start": v(757.73, 1414.82) * mm, "end": v(779.48, 1420.51) * mm});
            skLineSegment(sketch, "E4520", {"start": v(779.48, 1420.51) * mm, "end": v(801.01, 1427.02) * mm});
            skLineSegment(sketch, "E4521", {"start": v(801.01, 1427.02) * mm, "end": v(822.55, 1434.13) * mm});
            skLineSegment(sketch, "E4522", {"start": v(822.55, 1434.13) * mm, "end": v(843.69, 1441.85) * mm});
            skLineSegment(sketch, "E4523", {"start": v(843.69, 1441.85) * mm, "end": v(832.71, 1404.87) * mm});
            skLineSegment(sketch, "E4524", {"start": v(832.71, 1404.87) * mm, "end": v(819.7, 1367.88) * mm});
            skLineSegment(sketch, "E4525", {"start": v(819.7, 1367.88) * mm, "end": v(804.67, 1330.9) * mm});
            skLineSegment(sketch, "E4526", {"start": v(804.67, 1330.9) * mm, "end": v(766.88, 1465.42) * mm});
            skLineSegment(sketch, "E4527", {"start": v(602.08, 1370.53) * mm, "end": v(578.71, 1370.32) * mm});
            skLineSegment(sketch, "E4528", {"start": v(578.71, 1370.32) * mm, "end": v(555.55, 1370.93) * mm});
            skLineSegment(sketch, "E4529", {"start": v(555.55, 1370.93) * mm, "end": v(532.18, 1372.15) * mm});
            skLineSegment(sketch, "E4530", {"start": v(532.18, 1372.15) * mm, "end": v(506.58, 1351.02) * mm});
            skLineSegment(sketch, "E4531", {"start": v(506.58, 1351.02) * mm, "end": v(504.34, 1327.85) * mm});
            skLineSegment(sketch, "E4532", {"start": v(504.34, 1327.85) * mm, "end": v(527.3, 1302.45) * mm});
            skLineSegment(sketch, "E4533", {"start": v(527.3, 1302.45) * mm, "end": v(552.7, 1301.23) * mm});
            skLineSegment(sketch, "E4534", {"start": v(552.7, 1301.23) * mm, "end": v(578.3, 1300.62) * mm});
            skLineSegment(sketch, "E4535", {"start": v(578.3, 1300.62) * mm, "end": v(603.7, 1300.83) * mm});
            skLineSegment(sketch, "E4536", {"start": v(603.7, 1300.83) * mm, "end": v(600.25, 1440.43) * mm});
            skLineSegment(sketch, "E4537", {"start": v(474.27, 1449.16) * mm, "end": v(466.75, 1403.24) * mm});
            skLineSegment(sketch, "E4538", {"start": v(466.75, 1403.24) * mm, "end": v(435.46, 1361.58) * mm});
            skLineSegment(sketch, "E4539", {"start": v(435.46, 1361.58) * mm, "end": v(401.52, 1321.35) * mm});
            skLineSegment(sketch, "E4540", {"start": v(401.52, 1321.35) * mm, "end": v(388.72, 1372.35) * mm});
            skLineSegment(sketch, "E4541", {"start": v(388.72, 1372.35) * mm, "end": v(378.77, 1423.56) * mm});
            skLineSegment(sketch, "E4542", {"start": v(378.77, 1423.56) * mm, "end": v(391.97, 1468.06) * mm});
            skLineSegment(sketch, "E4543", {"start": v(466.75, 1403.24) * mm, "end": v(444.4, 1407.3) * mm});
            skLineSegment(sketch, "E4544", {"start": v(444.4, 1407.3) * mm, "end": v(422.45, 1411.98) * mm});
            skLineSegment(sketch, "E4545", {"start": v(422.45, 1411.98) * mm, "end": v(400.5, 1417.46) * mm});
            skLineSegment(sketch, "E4546", {"start": v(400.5, 1417.46) * mm, "end": v(378.77, 1423.56) * mm});
            skLineSegment(sketch, "E4547", {"start": v(232.05, 1432.5) * mm, "end": v(253.6, 1421.94) * mm});
            skLineSegment(sketch, "E4548", {"start": v(253.6, 1421.94) * mm, "end": v(275.34, 1411.98) * mm});
            skLineSegment(sketch, "E4549", {"start": v(275.34, 1411.98) * mm, "end": v(297.49, 1402.63) * mm});
            skLineSegment(sketch, "E4550", {"start": v(297.49, 1402.63) * mm, "end": v(320.04, 1393.9) * mm});
            skLineSegment(sketch, "E4551", {"start": v(253.4, 1473.95) * mm, "end": v(273.71, 1464) * mm});
            skLineSegment(sketch, "E4552", {"start": v(273.71, 1464) * mm, "end": v(294.03, 1454.45) * mm});
            skLineSegment(sketch, "E4553", {"start": v(294.03, 1454.45) * mm, "end": v(314.96, 1445.7) * mm});
            skLineSegment(sketch, "E4554", {"start": v(314.96, 1445.7) * mm, "end": v(335.9, 1437.78) * mm});
            skLineSegment(sketch, "E4555", {"start": v(168.25, 1583.48) * mm, "end": v(185.12, 1570.88) * mm});
            skLineSegment(sketch, "E4556", {"start": v(185.12, 1570.88) * mm, "end": v(202.39, 1558.69) * mm});
            skLineSegment(sketch, "E4557", {"start": v(202.39, 1558.69) * mm, "end": v(219.86, 1546.9) * mm});
            skLineSegment(sketch, "E4558", {"start": v(219.86, 1546.9) * mm, "end": v(237.95, 1535.73) * mm});
            skLineSegment(sketch, "E4559", {"start": v(237.95, 1535.73) * mm, "end": v(213.97, 1495.9) * mm});
            skLineSegment(sketch, "E4560", {"start": v(213.97, 1495.9) * mm, "end": v(182.27, 1488.18) * mm});
            skLineSegment(sketch, "E4561", {"start": v(182.27, 1488.18) * mm, "end": v(162.76, 1500.98) * mm});
            skLineSegment(sketch, "E4562", {"start": v(162.76, 1500.98) * mm, "end": v(143.87, 1514.4) * mm});
            skLineSegment(sketch, "E4563", {"start": v(143.87, 1514.4) * mm, "end": v(110.95, 1510.12) * mm});
            skLineSegment(sketch, "E4564", {"start": v(110.95, 1510.12) * mm, "end": v(96.52, 1491.84) * mm});
            skLineSegment(sketch, "E4565", {"start": v(96.52, 1491.84) * mm, "end": v(102.62, 1458.1) * mm});
            skLineSegment(sketch, "E4566", {"start": v(102.62, 1458.1) * mm, "end": v(123.34, 1443.47) * mm});
            skLineSegment(sketch, "E4567", {"start": v(123.34, 1443.47) * mm, "end": v(144.48, 1429.25) * mm});
            skLineSegment(sketch, "E4568", {"start": v(144.48, 1429.25) * mm, "end": v(178.2, 1435.96) * mm});
            skFitSpline(sketch, "E4569", {"points": [v(1854.2, 2115.46) * mm, v(1854.2, 1414.06) * mm, v(1285.6, 845.46) * mm, v(584.2, 845.46) * mm]});
            skFitSpline(sketch, "E4570", {"points": [v(584.2, 845.46) * mm, v(-117.2, 845.46) * mm, v(-685.8, 1414.06) * mm, v(-685.8, 2115.46) * mm]});
            skFitSpline(sketch, "E4571", {"points": [v(-685.8, 2115.46) * mm, v(-685.8, 2816.86) * mm, v(-117.2, 3385.46) * mm, v(584.2, 3385.46) * mm]});
            skFitSpline(sketch, "E4572", {"points": [v(584.2, 3385.46) * mm, v(1285.6, 3385.46) * mm, v(1854.2, 2816.86) * mm, v(1854.2, 2115.46) * mm]});
            skLineSegment(sketch, "E4573", {"start": v(76.4, 1670.45) * mm, "end": v(90.63, 1654.8) * mm});
            skLineSegment(sketch, "E4574", {"start": v(90.63, 1654.8) * mm, "end": v(105.26, 1639.56) * mm});
            skLineSegment(sketch, "E4575", {"start": v(105.26, 1639.56) * mm, "end": v(120.3, 1624.73) * mm});
            skLineSegment(sketch, "E4576", {"start": v(120.3, 1624.73) * mm, "end": v(135.94, 1610.5) * mm});
            skLineSegment(sketch, "E4577", {"start": v(135.94, 1610.5) * mm, "end": v(105.05, 1575.76) * mm});
            skLineSegment(sketch, "E4578", {"start": v(105.05, 1575.76) * mm, "end": v(72.34, 1574.13) * mm});
            skLineSegment(sketch, "E4579", {"start": v(72.34, 1574.13) * mm, "end": v(55.68, 1590.39) * mm});
            skLineSegment(sketch, "E4580", {"start": v(55.68, 1590.39) * mm, "end": v(39.62, 1607.05) * mm});
            skLineSegment(sketch, "E4581", {"start": v(39.62, 1607.05) * mm, "end": v(6.5, 1609.08) * mm});
            skLineSegment(sketch, "E4582", {"start": v(6.5, 1609.08) * mm, "end": v(-11.18, 1593.64) * mm});
            skLineSegment(sketch, "E4583", {"start": v(-11.18, 1593.64) * mm, "end": v(-11.58, 1559.5) * mm});
            skLineSegment(sketch, "E4584", {"start": v(-11.58, 1559.5) * mm, "end": v(6.1, 1541.01) * mm});
            skLineSegment(sketch, "E4585", {"start": v(6.1, 1541.01) * mm, "end": v(24.38, 1523.33) * mm});
            skLineSegment(sketch, "E4586", {"start": v(24.38, 1523.33) * mm, "end": v(58.52, 1523.54) * mm});
            skFitSpline(sketch, "E4587", {"points": [v(2108.2, 2115.46) * mm, v(2108.2, 1273.78) * mm, v(1425.88, 591.46) * mm, v(584.2, 591.46) * mm]});
            skFitSpline(sketch, "E4588", {"points": [v(584.2, 591.46) * mm, v(-257.48, 591.46) * mm, v(-939.8, 1273.78) * mm, v(-939.8, 2115.46) * mm]});
            skFitSpline(sketch, "E4589", {"points": [v(-939.8, 2115.46) * mm, v(-939.8, 2957.14) * mm, v(-257.48, 3639.46) * mm, v(584.2, 3639.46) * mm]});
            skFitSpline(sketch, "E4590", {"points": [v(584.2, 3639.46) * mm, v(1425.88, 3639.46) * mm, v(2108.2, 2957.14) * mm, v(2108.2, 2115.46) * mm]});
            skFitSpline(sketch, "E4591", {"points": [v(1761.74, 2115.46) * mm, v(1761.74, 1465.12) * mm, v(1234.54, 937.91) * mm, v(584.2, 937.91) * mm]});
            skFitSpline(sketch, "E4592", {"points": [v(584.2, 937.91) * mm, v(-66.14, 937.91) * mm, v(-593.34, 1465.12) * mm, v(-593.34, 2115.46) * mm]});
            skFitSpline(sketch, "E4593", {"points": [v(-593.34, 2115.46) * mm, v(-593.34, 2765.8) * mm, v(-66.14, 3293) * mm, v(584.2, 3293) * mm]});
            skFitSpline(sketch, "E4594", {"points": [v(584.2, 3293) * mm, v(1234.54, 3293) * mm, v(1761.74, 2765.8) * mm, v(1761.74, 2115.46) * mm]});
            skLineSegment(sketch, "E4595", {"start": v(6129.35, 2057.54) * mm, "end": v(6132.3, 2057.76) * mm});
            skLineSegment(sketch, "E4596", {"start": v(6132.3, 2057.76) * mm, "end": v(6136.14, 2058.12) * mm});
            skLineSegment(sketch, "E4597", {"start": v(6136.14, 2058.12) * mm, "end": v(6140.86, 2058.67) * mm});
            skLineSegment(sketch, "E4598", {"start": v(6140.86, 2058.67) * mm, "end": v(6146.46, 2059.45) * mm});
            skLineSegment(sketch, "E4599", {"start": v(6146.46, 2059.45) * mm, "end": v(6152.92, 2060.49) * mm});
            skLineSegment(sketch, "E4600", {"start": v(6152.92, 2060.49) * mm, "end": v(6160.24, 2061.83) * mm});
            skLineSegment(sketch, "E4601", {"start": v(6160.24, 2061.83) * mm, "end": v(6168.4, 2063.51) * mm});
            skLineSegment(sketch, "E4602", {"start": v(6168.4, 2063.51) * mm, "end": v(6177.41, 2065.57) * mm});
            skLineSegment(sketch, "E4603", {"start": v(6177.41, 2065.57) * mm, "end": v(6187.24, 2068.04) * mm});
            skLineSegment(sketch, "E4604", {"start": v(6187.24, 2068.04) * mm, "end": v(6197.87, 2070.97) * mm});
            skLineSegment(sketch, "E4605", {"start": v(6197.87, 2070.97) * mm, "end": v(6209.3, 2074.38) * mm});
            skLineSegment(sketch, "E4606", {"start": v(6209.3, 2074.38) * mm, "end": v(6221.5, 2078.32) * mm});
            skLineSegment(sketch, "E4607", {"start": v(6221.5, 2078.32) * mm, "end": v(6234.47, 2082.82) * mm});
            skLineSegment(sketch, "E4608", {"start": v(6234.47, 2082.82) * mm, "end": v(6248.17, 2087.9) * mm});
            skLineSegment(sketch, "E4609", {"start": v(6248.17, 2087.9) * mm, "end": v(6262.59, 2093.63) * mm});
            skLineSegment(sketch, "E4610", {"start": v(6262.59, 2093.63) * mm, "end": v(6277.7, 2100) * mm});
            skLineSegment(sketch, "E4611", {"start": v(6277.7, 2100) * mm, "end": v(6293.5, 2107.08) * mm});
            skLineSegment(sketch, "E4612", {"start": v(6293.5, 2107.08) * mm, "end": v(6309.95, 2114.89) * mm});
            skLineSegment(sketch, "E4613", {"start": v(6309.95, 2114.89) * mm, "end": v(6327.02, 2123.45) * mm});
            skLineSegment(sketch, "E4614", {"start": v(6327.02, 2123.45) * mm, "end": v(6344.7, 2132.8) * mm});
            skLineSegment(sketch, "E4615", {"start": v(6344.7, 2132.8) * mm, "end": v(6362.95, 2142.97) * mm});
            skLineSegment(sketch, "E4616", {"start": v(6362.95, 2142.97) * mm, "end": v(6381.75, 2153.99) * mm});
            skLineSegment(sketch, "E4617", {"start": v(6381.75, 2153.99) * mm, "end": v(6401.06, 2165.88) * mm});
            skLineSegment(sketch, "E4618", {"start": v(6401.06, 2165.88) * mm, "end": v(6420.87, 2178.69) * mm});
            skLineSegment(sketch, "E4619", {"start": v(6420.87, 2178.69) * mm, "end": v(6441.13, 2192.42) * mm});
            skLineSegment(sketch, "E4620", {"start": v(6441.13, 2192.42) * mm, "end": v(6461.83, 2207.12) * mm});
            skLineSegment(sketch, "E4621", {"start": v(6461.83, 2207.12) * mm, "end": v(6482.9, 2222.8) * mm});
            skLineSegment(sketch, "E4622", {"start": v(6482.9, 2222.8) * mm, "end": v(6504.36, 2239.47) * mm});
            skLineSegment(sketch, "E4623", {"start": v(6504.36, 2239.47) * mm, "end": v(6519.1, 2256.57) * mm});
            skLineSegment(sketch, "E4624", {"start": v(6519.1, 2256.57) * mm, "end": v(6503.82, 2387.62) * mm});
            skLineSegment(sketch, "E4625", {"start": v(6503.82, 2387.62) * mm, "end": v(6485.53, 2400.87) * mm});
            skLineSegment(sketch, "E4626", {"start": v(6485.53, 2400.87) * mm, "end": v(6460.82, 2412.17) * mm});
            skLineSegment(sketch, "E4627", {"start": v(6460.82, 2412.17) * mm, "end": v(6436.7, 2422.57) * mm});
            skLineSegment(sketch, "E4628", {"start": v(6436.7, 2422.57) * mm, "end": v(6413.18, 2432.1) * mm});
            skLineSegment(sketch, "E4629", {"start": v(6413.18, 2432.1) * mm, "end": v(6390.3, 2440.81) * mm});
            skLineSegment(sketch, "E4630", {"start": v(6390.3, 2440.81) * mm, "end": v(6368.08, 2448.71) * mm});
            skLineSegment(sketch, "E4631", {"start": v(6368.08, 2448.71) * mm, "end": v(6346.54, 2455.85) * mm});
            skLineSegment(sketch, "E4632", {"start": v(6346.54, 2455.85) * mm, "end": v(6325.71, 2462.25) * mm});
            skLineSegment(sketch, "E4633", {"start": v(6325.71, 2462.25) * mm, "end": v(6305.61, 2467.94) * mm});
            skLineSegment(sketch, "E4634", {"start": v(6305.61, 2467.94) * mm, "end": v(6286.26, 2472.97) * mm});
            skLineSegment(sketch, "E4635", {"start": v(6286.26, 2472.97) * mm, "end": v(6267.67, 2477.38) * mm});
            skLineSegment(sketch, "E4636", {"start": v(6267.67, 2477.38) * mm, "end": v(6249.87, 2481.19) * mm});
            skLineSegment(sketch, "E4637", {"start": v(6249.87, 2481.19) * mm, "end": v(6232.87, 2484.44) * mm});
            skLineSegment(sketch, "E4638", {"start": v(6232.87, 2484.44) * mm, "end": v(6216.7, 2487.17) * mm});
            skLineSegment(sketch, "E4639", {"start": v(6216.7, 2487.17) * mm, "end": v(6201.34, 2489.41) * mm});
            skLineSegment(sketch, "E4640", {"start": v(6201.34, 2489.41) * mm, "end": v(6186.84, 2491.21) * mm});
            skLineSegment(sketch, "E4641", {"start": v(6186.84, 2491.21) * mm, "end": v(6173.19, 2492.6) * mm});
            skLineSegment(sketch, "E4642", {"start": v(6173.19, 2492.6) * mm, "end": v(6160.4, 2493.63) * mm});
            skLineSegment(sketch, "E4643", {"start": v(6160.4, 2493.63) * mm, "end": v(6148.5, 2494.32) * mm});
            skLineSegment(sketch, "E4644", {"start": v(6148.5, 2494.32) * mm, "end": v(6137.48, 2494.72) * mm});
            skLineSegment(sketch, "E4645", {"start": v(6137.48, 2494.72) * mm, "end": v(6127.35, 2494.87) * mm});
            skLineSegment(sketch, "E4646", {"start": v(6127.35, 2494.87) * mm, "end": v(6118.1, 2494.8) * mm});
            skLineSegment(sketch, "E4647", {"start": v(6118.1, 2494.8) * mm, "end": v(6109.77, 2494.56) * mm});
            skLineSegment(sketch, "E4648", {"start": v(6109.77, 2494.56) * mm, "end": v(6102.34, 2494.18) * mm});
            skLineSegment(sketch, "E4649", {"start": v(6102.34, 2494.18) * mm, "end": v(6095.81, 2493.7) * mm});
            skLineSegment(sketch, "E4650", {"start": v(6095.81, 2493.7) * mm, "end": v(6090.19, 2493.17) * mm});
            skLineSegment(sketch, "E4651", {"start": v(6090.19, 2493.17) * mm, "end": v(6085.47, 2492.62) * mm});
            skLineSegment(sketch, "E4652", {"start": v(6085.47, 2492.62) * mm, "end": v(6081.65, 2492.1) * mm});
            skLineSegment(sketch, "E4653", {"start": v(6081.65, 2492.1) * mm, "end": v(6078.73, 2491.62) * mm});
            skLineSegment(sketch, "E4654", {"start": v(6078.73, 2491.62) * mm, "end": v(6076.7, 2491.25) * mm});
            skLineSegment(sketch, "E4655", {"start": v(6076.7, 2491.25) * mm, "end": v(6075.55, 2491.01) * mm});
            skLineSegment(sketch, "E4656", {"start": v(6075.55, 2491.01) * mm, "end": v(5935, 2457.78) * mm});
            skLineSegment(sketch, "E4657", {"start": v(5935, 2457.78) * mm, "end": v(5849.26, 2723.23) * mm});
            skLineSegment(sketch, "E4658", {"start": v(5849.26, 2723.23) * mm, "end": v(5982.69, 2778.5) * mm});
            skLineSegment(sketch, "E4659", {"start": v(5982.69, 2778.5) * mm, "end": v(5983.75, 2778.98) * mm});
            skLineSegment(sketch, "E4660", {"start": v(5983.75, 2778.98) * mm, "end": v(5985.61, 2779.87) * mm});
            skLineSegment(sketch, "E4661", {"start": v(5985.61, 2779.87) * mm, "end": v(5988.26, 2781.2) * mm});
            skLineSegment(sketch, "E4662", {"start": v(5988.26, 2781.2) * mm, "end": v(5991.67, 2783) * mm});
            skLineSegment(sketch, "E4663", {"start": v(5991.67, 2783) * mm, "end": v(5995.82, 2785.31) * mm});
            skLineSegment(sketch, "E4664", {"start": v(5995.82, 2785.31) * mm, "end": v(6000.69, 2788.17) * mm});
            skLineSegment(sketch, "E4665", {"start": v(6000.69, 2788.17) * mm, "end": v(6006.26, 2791.6) * mm});
            skLineSegment(sketch, "E4666", {"start": v(6006.26, 2791.6) * mm, "end": v(6012.51, 2795.65) * mm});
            skLineSegment(sketch, "E4667", {"start": v(6012.51, 2795.65) * mm, "end": v(6019.42, 2800.33) * mm});
            skLineSegment(sketch, "E4668", {"start": v(6019.42, 2800.33) * mm, "end": v(6026.95, 2805.67) * mm});
            skLineSegment(sketch, "E4669", {"start": v(6026.95, 2805.67) * mm, "end": v(6035.08, 2811.72) * mm});
            skLineSegment(sketch, "E4670", {"start": v(6035.08, 2811.72) * mm, "end": v(6043.78, 2818.5) * mm});
            skLineSegment(sketch, "E4671", {"start": v(6043.78, 2818.5) * mm, "end": v(6053.03, 2826.02) * mm});
            skLineSegment(sketch, "E4672", {"start": v(6053.03, 2826.02) * mm, "end": v(6062.8, 2834.33) * mm});
            skLineSegment(sketch, "E4673", {"start": v(6062.8, 2834.33) * mm, "end": v(6073.06, 2843.44) * mm});
            skLineSegment(sketch, "E4674", {"start": v(6073.06, 2843.44) * mm, "end": v(6083.77, 2853.39) * mm});
            skLineSegment(sketch, "E4675", {"start": v(6083.77, 2853.39) * mm, "end": v(6094.9, 2864.2) * mm});
            skLineSegment(sketch, "E4676", {"start": v(6094.9, 2864.2) * mm, "end": v(6106.43, 2875.87) * mm});
            skLineSegment(sketch, "E4677", {"start": v(6106.43, 2875.87) * mm, "end": v(6118.31, 2888.45) * mm});
            skLineSegment(sketch, "E4678", {"start": v(6118.31, 2888.45) * mm, "end": v(6130.52, 2901.95) * mm});
            skLineSegment(sketch, "E4679", {"start": v(6130.52, 2901.95) * mm, "end": v(6143.02, 2916.4) * mm});
            skLineSegment(sketch, "E4680", {"start": v(6143.02, 2916.4) * mm, "end": v(6155.77, 2931.8) * mm});
            skLineSegment(sketch, "E4681", {"start": v(6155.77, 2931.8) * mm, "end": v(6168.74, 2948.18) * mm});
            skLineSegment(sketch, "E4682", {"start": v(6168.74, 2948.18) * mm, "end": v(6181.9, 2965.56) * mm});
            skLineSegment(sketch, "E4683", {"start": v(6181.9, 2965.56) * mm, "end": v(6195.18, 2983.94) * mm});
            skLineSegment(sketch, "E4684", {"start": v(6195.18, 2983.94) * mm, "end": v(6208.58, 3003.35) * mm});
            skLineSegment(sketch, "E4685", {"start": v(6208.58, 3003.35) * mm, "end": v(6222.05, 3023.8) * mm});
            skLineSegment(sketch, "E4686", {"start": v(6222.05, 3023.8) * mm, "end": v(6235.54, 3045.29) * mm});
            skLineSegment(sketch, "E4687", {"start": v(6235.54, 3045.29) * mm, "end": v(6249.02, 3067.84) * mm});
            skLineSegment(sketch, "E4688", {"start": v(6249.02, 3067.84) * mm, "end": v(6262.45, 3091.46) * mm});
            skLineSegment(sketch, "E4689", {"start": v(6262.45, 3091.46) * mm, "end": v(6269.54, 3112.9) * mm});
            skLineSegment(sketch, "E4690", {"start": v(6269.54, 3112.9) * mm, "end": v(6205.27, 3228.13) * mm});
            skLineSegment(sketch, "E4691", {"start": v(6205.27, 3228.13) * mm, "end": v(6183.3, 3233.37) * mm});
            skLineSegment(sketch, "E4692", {"start": v(6183.3, 3233.37) * mm, "end": v(6156.15, 3234.35) * mm});
            skLineSegment(sketch, "E4693", {"start": v(6156.15, 3234.35) * mm, "end": v(6129.88, 3234.73) * mm});
            skLineSegment(sketch, "E4694", {"start": v(6129.88, 3234.73) * mm, "end": v(6104.5, 3234.54) * mm});
            skLineSegment(sketch, "E4695", {"start": v(6104.5, 3234.54) * mm, "end": v(6080.03, 3233.82) * mm});
            skLineSegment(sketch, "E4696", {"start": v(6080.03, 3233.82) * mm, "end": v(6056.48, 3232.62) * mm});
            skLineSegment(sketch, "E4697", {"start": v(6056.48, 3232.62) * mm, "end": v(6033.85, 3230.97) * mm});
            skLineSegment(sketch, "E4698", {"start": v(6033.85, 3230.97) * mm, "end": v(6012.16, 3228.9) * mm});
            skLineSegment(sketch, "E4699", {"start": v(6012.16, 3228.9) * mm, "end": v(5991.4, 3226.48) * mm});
            skLineSegment(sketch, "E4700", {"start": v(5991.4, 3226.48) * mm, "end": v(5971.6, 3223.72) * mm});
            skLineSegment(sketch, "E4701", {"start": v(5971.6, 3223.72) * mm, "end": v(5952.74, 3220.68) * mm});
            skLineSegment(sketch, "E4702", {"start": v(5952.74, 3220.68) * mm, "end": v(5934.84, 3217.38) * mm});
            skLineSegment(sketch, "E4703", {"start": v(5934.84, 3217.38) * mm, "end": v(5917.9, 3213.88) * mm});
            skLineSegment(sketch, "E4704", {"start": v(5917.9, 3213.88) * mm, "end": v(5901.9, 3210.21) * mm});
            skLineSegment(sketch, "E4705", {"start": v(5901.9, 3210.21) * mm, "end": v(5886.86, 3206.41) * mm});
            skLineSegment(sketch, "E4706", {"start": v(5886.86, 3206.41) * mm, "end": v(5872.77, 3202.53) * mm});
            skLineSegment(sketch, "E4707", {"start": v(5872.77, 3202.53) * mm, "end": v(5859.62, 3198.59) * mm});
            skLineSegment(sketch, "E4708", {"start": v(5859.62, 3198.59) * mm, "end": v(5847.42, 3194.64) * mm});
            skLineSegment(sketch, "E4709", {"start": v(5847.42, 3194.64) * mm, "end": v(5836.16, 3190.73) * mm});
            skLineSegment(sketch, "E4710", {"start": v(5836.16, 3190.73) * mm, "end": v(5825.82, 3186.88) * mm});
            skLineSegment(sketch, "E4711", {"start": v(5825.82, 3186.88) * mm, "end": v(5816.4, 3183.14) * mm});
            skLineSegment(sketch, "E4712", {"start": v(5816.4, 3183.14) * mm, "end": v(5807.9, 3179.54) * mm});
            skLineSegment(sketch, "E4713", {"start": v(5807.9, 3179.54) * mm, "end": v(5800.29, 3176.13) * mm});
            skLineSegment(sketch, "E4714", {"start": v(5800.29, 3176.13) * mm, "end": v(5793.57, 3172.93) * mm});
            skLineSegment(sketch, "E4715", {"start": v(5793.57, 3172.93) * mm, "end": v(5787.72, 3170) * mm});
            skLineSegment(sketch, "E4716", {"start": v(5787.72, 3170) * mm, "end": v(5782.73, 3167.35) * mm});
            skLineSegment(sketch, "E4717", {"start": v(5782.73, 3167.35) * mm, "end": v(5778.57, 3165.03) * mm});
            skLineSegment(sketch, "E4718", {"start": v(5778.57, 3165.03) * mm, "end": v(5775.25, 3163.08) * mm});
            skLineSegment(sketch, "E4719", {"start": v(5775.25, 3163.08) * mm, "end": v(5772.73, 3161.53) * mm});
            skLineSegment(sketch, "E4720", {"start": v(5772.73, 3161.53) * mm, "end": v(5771, 3160.4) * mm});
            skLineSegment(sketch, "E4721", {"start": v(5771, 3160.4) * mm, "end": v(5770.03, 3159.76) * mm});
            skLineSegment(sketch, "E4722", {"start": v(5770.03, 3159.76) * mm, "end": v(5652.9, 3075.27) * mm});
            skLineSegment(sketch, "E4723", {"start": v(5652.9, 3075.27) * mm, "end": v(5472.1, 3287.7) * mm});
            skLineSegment(sketch, "E4724", {"start": v(5472.1, 3287.7) * mm, "end": v(5574.22, 3389.82) * mm});
            skLineSegment(sketch, "E4725", {"start": v(5574.22, 3389.82) * mm, "end": v(5575.02, 3390.67) * mm});
            skLineSegment(sketch, "E4726", {"start": v(5575.02, 3390.67) * mm, "end": v(5576.4, 3392.2) * mm});
            skLineSegment(sketch, "E4727", {"start": v(5576.4, 3392.2) * mm, "end": v(5578.33, 3394.44) * mm});
            skLineSegment(sketch, "E4728", {"start": v(5578.33, 3394.44) * mm, "end": v(5580.8, 3397.41) * mm});
            skLineSegment(sketch, "E4729", {"start": v(5580.8, 3397.41) * mm, "end": v(5583.74, 3401.14) * mm});
            skLineSegment(sketch, "E4730", {"start": v(5583.74, 3401.14) * mm, "end": v(5587.15, 3405.64) * mm});
            skLineSegment(sketch, "E4731", {"start": v(5587.15, 3405.64) * mm, "end": v(5590.98, 3410.95) * mm});
            skLineSegment(sketch, "E4732", {"start": v(5590.98, 3410.95) * mm, "end": v(5595.21, 3417.07) * mm});
            skLineSegment(sketch, "E4733", {"start": v(5595.21, 3417.07) * mm, "end": v(5599.8, 3424.04) * mm});
            skLineSegment(sketch, "E4734", {"start": v(5599.8, 3424.04) * mm, "end": v(5604.7, 3431.86) * mm});
            skLineSegment(sketch, "E4735", {"start": v(5604.7, 3431.86) * mm, "end": v(5609.9, 3440.56) * mm});
            skLineSegment(sketch, "E4736", {"start": v(5609.9, 3440.56) * mm, "end": v(5615.36, 3450.15) * mm});
            skLineSegment(sketch, "E4737", {"start": v(5615.36, 3450.15) * mm, "end": v(5621.02, 3460.64) * mm});
            skLineSegment(sketch, "E4738", {"start": v(5621.02, 3460.64) * mm, "end": v(5626.87, 3472.05) * mm});
            skLineSegment(sketch, "E4739", {"start": v(5626.87, 3472.05) * mm, "end": v(5632.85, 3484.4) * mm});
            skLineSegment(sketch, "E4740", {"start": v(5632.85, 3484.4) * mm, "end": v(5638.94, 3497.69) * mm});
            skLineSegment(sketch, "E4741", {"start": v(5638.94, 3497.69) * mm, "end": v(5645.1, 3511.93) * mm});
            skLineSegment(sketch, "E4742", {"start": v(5645.1, 3511.93) * mm, "end": v(5651.27, 3527.13) * mm});
            skLineSegment(sketch, "E4743", {"start": v(5651.27, 3527.13) * mm, "end": v(5657.44, 3543.3) * mm});
            skLineSegment(sketch, "E4744", {"start": v(5657.44, 3543.3) * mm, "end": v(5663.55, 3560.45) * mm});
            skLineSegment(sketch, "E4745", {"start": v(5663.55, 3560.45) * mm, "end": v(5669.57, 3578.58) * mm});
            skLineSegment(sketch, "E4746", {"start": v(5669.57, 3578.58) * mm, "end": v(5675.46, 3597.69) * mm});
            skLineSegment(sketch, "E4747", {"start": v(5675.46, 3597.69) * mm, "end": v(5681.17, 3617.78) * mm});
            skLineSegment(sketch, "E4748", {"start": v(5681.17, 3617.78) * mm, "end": v(5686.67, 3638.87) * mm});
            skLineSegment(sketch, "E4749", {"start": v(5686.67, 3638.87) * mm, "end": v(5691.92, 3660.94) * mm});
            skLineSegment(sketch, "E4750", {"start": v(5691.92, 3660.94) * mm, "end": v(5696.87, 3684) * mm});
            skLineSegment(sketch, "E4751", {"start": v(5696.87, 3684) * mm, "end": v(5701.49, 3708.04) * mm});
            skLineSegment(sketch, "E4752", {"start": v(5701.49, 3708.04) * mm, "end": v(5705.73, 3733.06) * mm});
            skLineSegment(sketch, "E4753", {"start": v(5705.73, 3733.06) * mm, "end": v(5709.55, 3759.05) * mm});
            skLineSegment(sketch, "E4754", {"start": v(5709.55, 3759.05) * mm, "end": v(5712.92, 3786.01) * mm});
            skLineSegment(sketch, "E4755", {"start": v(5712.92, 3786.01) * mm, "end": v(5711.26, 3808.54) * mm});
            skLineSegment(sketch, "E4756", {"start": v(5711.26, 3808.54) * mm, "end": v(5607.79, 3890.4) * mm});
            skLineSegment(sketch, "E4757", {"start": v(5607.79, 3890.4) * mm, "end": v(5585.49, 3886.83) * mm});
            skLineSegment(sketch, "E4758", {"start": v(5585.49, 3886.83) * mm, "end": v(5560.03, 3877.35) * mm});
            skLineSegment(sketch, "E4759", {"start": v(5560.03, 3877.35) * mm, "end": v(5535.61, 3867.64) * mm});
            skLineSegment(sketch, "E4760", {"start": v(5535.61, 3867.64) * mm, "end": v(5512.24, 3857.76) * mm});
            skLineSegment(sketch, "E4761", {"start": v(5512.24, 3857.76) * mm, "end": v(5489.9, 3847.73) * mm});
            skLineSegment(sketch, "E4762", {"start": v(5489.9, 3847.73) * mm, "end": v(5468.6, 3837.6) * mm});
            skLineSegment(sketch, "E4763", {"start": v(5468.6, 3837.6) * mm, "end": v(5448.33, 3827.42) * mm});
            skLineSegment(sketch, "E4764", {"start": v(5448.33, 3827.42) * mm, "end": v(5429.08, 3817.22) * mm});
            skLineSegment(sketch, "E4765", {"start": v(5429.08, 3817.22) * mm, "end": v(5410.84, 3807.03) * mm});
            skLineSegment(sketch, "E4766", {"start": v(5410.84, 3807.03) * mm, "end": v(5393.6, 3796.9) * mm});
            skLineSegment(sketch, "E4767", {"start": v(5393.6, 3796.9) * mm, "end": v(5377.34, 3786.88) * mm});
            skLineSegment(sketch, "E4768", {"start": v(5377.34, 3786.88) * mm, "end": v(5362.06, 3776.98) * mm});
            skLineSegment(sketch, "E4769", {"start": v(5362.06, 3776.98) * mm, "end": v(5347.74, 3767.26) * mm});
            skLineSegment(sketch, "E4770", {"start": v(5347.74, 3767.26) * mm, "end": v(5334.37, 3757.75) * mm});
            skLineSegment(sketch, "E4771", {"start": v(5334.37, 3757.75) * mm, "end": v(5321.93, 3748.49) * mm});
            skLineSegment(sketch, "E4772", {"start": v(5321.93, 3748.49) * mm, "end": v(5310.4, 3739.5) * mm});
            skLineSegment(sketch, "E4773", {"start": v(5310.4, 3739.5) * mm, "end": v(5299.76, 3730.84) * mm});
            skLineSegment(sketch, "E4774", {"start": v(5299.76, 3730.84) * mm, "end": v(5290, 3722.52) * mm});
            skLineSegment(sketch, "E4775", {"start": v(5290, 3722.52) * mm, "end": v(5281.09, 3714.6) * mm});
            skLineSegment(sketch, "E4776", {"start": v(5281.09, 3714.6) * mm, "end": v(5273.01, 3707.08) * mm});
            skLineSegment(sketch, "E4777", {"start": v(5273.01, 3707.08) * mm, "end": v(5265.74, 3700.02) * mm});
            skLineSegment(sketch, "E4778", {"start": v(5265.74, 3700.02) * mm, "end": v(5259.26, 3693.44) * mm});
            skLineSegment(sketch, "E4779", {"start": v(5259.26, 3693.44) * mm, "end": v(5253.54, 3687.37) * mm});
            skLineSegment(sketch, "E4780", {"start": v(5253.54, 3687.37) * mm, "end": v(5248.55, 3681.85) * mm});
            skLineSegment(sketch, "E4781", {"start": v(5248.55, 3681.85) * mm, "end": v(5244.27, 3676.9) * mm});
            skLineSegment(sketch, "E4782", {"start": v(5244.27, 3676.9) * mm, "end": v(5240.67, 3672.55) * mm});
            skLineSegment(sketch, "E4783", {"start": v(5240.67, 3672.55) * mm, "end": v(5237.72, 3668.82) * mm});
            skLineSegment(sketch, "E4784", {"start": v(5237.72, 3668.82) * mm, "end": v(5235.4, 3665.74) * mm});
            skLineSegment(sketch, "E4785", {"start": v(5235.4, 3665.74) * mm, "end": v(5233.66, 3663.34) * mm});
            skLineSegment(sketch, "E4786", {"start": v(5233.66, 3663.34) * mm, "end": v(5232.49, 3661.65) * mm});
            skLineSegment(sketch, "E4787", {"start": v(5232.49, 3661.65) * mm, "end": v(5231.85, 3660.67) * mm});
            skLineSegment(sketch, "E4788", {"start": v(5231.85, 3660.67) * mm, "end": v(5155.96, 3537.8) * mm});
            skLineSegment(sketch, "E4789", {"start": v(5155.96, 3537.8) * mm, "end": v(4907.63, 3664.86) * mm});
            skLineSegment(sketch, "E4790", {"start": v(4907.63, 3664.86) * mm, "end": v(4962.9, 3798.29) * mm});
            skLineSegment(sketch, "E4791", {"start": v(4962.9, 3798.29) * mm, "end": v(4963.31, 3799.38) * mm});
            skLineSegment(sketch, "E4792", {"start": v(4963.31, 3799.38) * mm, "end": v(4964, 3801.32) * mm});
            skLineSegment(sketch, "E4793", {"start": v(4964, 3801.32) * mm, "end": v(4964.93, 3804.13) * mm});
            skLineSegment(sketch, "E4794", {"start": v(4964.93, 3804.13) * mm, "end": v(4966.07, 3807.82) * mm});
            skLineSegment(sketch, "E4795", {"start": v(4966.07, 3807.82) * mm, "end": v(4967.37, 3812.39) * mm});
            skLineSegment(sketch, "E4796", {"start": v(4967.37, 3812.39) * mm, "end": v(4968.8, 3817.86) * mm});
            skLineSegment(sketch, "E4797", {"start": v(4968.8, 3817.86) * mm, "end": v(4970.3, 3824.22) * mm});
            skLineSegment(sketch, "E4798", {"start": v(4970.3, 3824.22) * mm, "end": v(4971.87, 3831.5) * mm});
            skLineSegment(sketch, "E4799", {"start": v(4971.87, 3831.5) * mm, "end": v(4973.44, 3839.7) * mm});
            skLineSegment(sketch, "E4800", {"start": v(4973.44, 3839.7) * mm, "end": v(4974.98, 3848.8) * mm});
            skLineSegment(sketch, "E4801", {"start": v(4974.98, 3848.8) * mm, "end": v(4976.45, 3858.82) * mm});
            skLineSegment(sketch, "E4802", {"start": v(4976.45, 3858.82) * mm, "end": v(4977.82, 3869.77) * mm});
            skLineSegment(sketch, "E4803", {"start": v(4977.82, 3869.77) * mm, "end": v(4979.04, 3881.63) * mm});
            skLineSegment(sketch, "E4804", {"start": v(4979.04, 3881.63) * mm, "end": v(4980.07, 3894.41) * mm});
            skLineSegment(sketch, "E4805", {"start": v(4980.07, 3894.41) * mm, "end": v(4980.88, 3908.1) * mm});
            skLineSegment(sketch, "E4806", {"start": v(4980.88, 3908.1) * mm, "end": v(4981.42, 3922.72) * mm});
            skLineSegment(sketch, "E4807", {"start": v(4981.42, 3922.72) * mm, "end": v(4981.65, 3938.23) * mm});
            skLineSegment(sketch, "E4808", {"start": v(4981.65, 3938.23) * mm, "end": v(4981.54, 3954.64) * mm});
            skLineSegment(sketch, "E4809", {"start": v(4981.54, 3954.64) * mm, "end": v(4981.05, 3971.94) * mm});
            skLineSegment(sketch, "E4810", {"start": v(4981.05, 3971.94) * mm, "end": v(4980.14, 3990.12) * mm});
            skLineSegment(sketch, "E4811", {"start": v(4980.14, 3990.12) * mm, "end": v(4978.76, 4009.17) * mm});
            skLineSegment(sketch, "E4812", {"start": v(4978.76, 4009.17) * mm, "end": v(4976.89, 4029.08) * mm});
            skLineSegment(sketch, "E4813", {"start": v(4976.89, 4029.08) * mm, "end": v(4974.47, 4049.83) * mm});
            skLineSegment(sketch, "E4814", {"start": v(4974.47, 4049.83) * mm, "end": v(4971.49, 4071.41) * mm});
            skLineSegment(sketch, "E4815", {"start": v(4971.49, 4071.41) * mm, "end": v(4967.89, 4093.81) * mm});
            skLineSegment(sketch, "E4816", {"start": v(4967.89, 4093.81) * mm, "end": v(4963.64, 4117.01) * mm});
            skLineSegment(sketch, "E4817", {"start": v(4963.64, 4117.01) * mm, "end": v(4958.7, 4141) * mm});
            skLineSegment(sketch, "E4818", {"start": v(4958.7, 4141) * mm, "end": v(4953.05, 4165.73) * mm});
            skLineSegment(sketch, "E4819", {"start": v(4953.05, 4165.73) * mm, "end": v(4946.63, 4191.2) * mm});
            skLineSegment(sketch, "E4820", {"start": v(4946.63, 4191.2) * mm, "end": v(4939.43, 4217.4) * mm});
            skLineSegment(sketch, "E4821", {"start": v(4939.43, 4217.4) * mm, "end": v(4929.28, 4237.58) * mm});
            skLineSegment(sketch, "E4822", {"start": v(4929.28, 4237.58) * mm, "end": v(4802.35, 4273.6) * mm});
            skLineSegment(sketch, "E4823", {"start": v(4802.35, 4273.6) * mm, "end": v(4783.12, 4261.78) * mm});
            skLineSegment(sketch, "E4824", {"start": v(4783.12, 4261.78) * mm, "end": v(4763.22, 4243.28) * mm});
            skLineSegment(sketch, "E4825", {"start": v(4763.22, 4243.28) * mm, "end": v(4744.38, 4224.96) * mm});
            skLineSegment(sketch, "E4826", {"start": v(4744.38, 4224.96) * mm, "end": v(4726.56, 4206.89) * mm});
            skLineSegment(sketch, "E4827", {"start": v(4726.56, 4206.89) * mm, "end": v(4709.77, 4189.08) * mm});
            skLineSegment(sketch, "E4828", {"start": v(4709.77, 4189.08) * mm, "end": v(4693.97, 4171.57) * mm});
            skLineSegment(sketch, "E4829", {"start": v(4693.97, 4171.57) * mm, "end": v(4679.13, 4154.4) * mm});
            skLineSegment(sketch, "E4830", {"start": v(4679.13, 4154.4) * mm, "end": v(4665.25, 4137.61) * mm});
            skLineSegment(sketch, "E4831", {"start": v(4665.25, 4137.61) * mm, "end": v(4652.3, 4121.22) * mm});
            skLineSegment(sketch, "E4832", {"start": v(4652.3, 4121.22) * mm, "end": v(4640.24, 4105.27) * mm});
            skLineSegment(sketch, "E4833", {"start": v(4640.24, 4105.27) * mm, "end": v(4629.06, 4089.78) * mm});
            skLineSegment(sketch, "E4834", {"start": v(4629.06, 4089.78) * mm, "end": v(4618.73, 4074.8) * mm});
            skLineSegment(sketch, "E4835", {"start": v(4618.73, 4074.8) * mm, "end": v(4609.22, 4060.33) * mm});
            skLineSegment(sketch, "E4836", {"start": v(4609.22, 4060.33) * mm, "end": v(4600.5, 4046.43) * mm});
            skLineSegment(sketch, "E4837", {"start": v(4600.5, 4046.43) * mm, "end": v(4592.56, 4033.1) * mm});
            skLineSegment(sketch, "E4838", {"start": v(4592.56, 4033.1) * mm, "end": v(4585.34, 4020.4) * mm});
            skLineSegment(sketch, "E4839", {"start": v(4585.34, 4020.4) * mm, "end": v(4578.83, 4008.32) * mm});
            skLineSegment(sketch, "E4840", {"start": v(4578.83, 4008.32) * mm, "end": v(4573, 3996.9) * mm});
            skLineSegment(sketch, "E4841", {"start": v(4573, 3996.9) * mm, "end": v(4567.8, 3986.16) * mm});
            skLineSegment(sketch, "E4842", {"start": v(4567.8, 3986.16) * mm, "end": v(4563.21, 3976.13) * mm});
            skLineSegment(sketch, "E4843", {"start": v(4563.21, 3976.13) * mm, "end": v(4559.2, 3966.83) * mm});
            skLineSegment(sketch, "E4844", {"start": v(4559.2, 3966.83) * mm, "end": v(4555.73, 3958.27) * mm});
            skLineSegment(sketch, "E4845", {"start": v(4555.73, 3958.27) * mm, "end": v(4552.76, 3950.48) * mm});
            skLineSegment(sketch, "E4846", {"start": v(4552.76, 3950.48) * mm, "end": v(4550.26, 3943.46) * mm});
            skLineSegment(sketch, "E4847", {"start": v(4550.26, 3943.46) * mm, "end": v(4548.2, 3937.25) * mm});
            skLineSegment(sketch, "E4848", {"start": v(4548.2, 3937.25) * mm, "end": v(4546.55, 3931.85) * mm});
            skLineSegment(sketch, "E4849", {"start": v(4546.55, 3931.85) * mm, "end": v(4545.25, 3927.28) * mm});
            skLineSegment(sketch, "E4850", {"start": v(4545.25, 3927.28) * mm, "end": v(4544.28, 3923.55) * mm});
            skLineSegment(sketch, "E4851", {"start": v(4544.28, 3923.55) * mm, "end": v(4543.6, 3920.67) * mm});
            skLineSegment(sketch, "E4852", {"start": v(4543.6, 3920.67) * mm, "end": v(4543.16, 3918.65) * mm});
            skLineSegment(sketch, "E4853", {"start": v(4543.16, 3918.65) * mm, "end": v(4542.94, 3917.5) * mm});
            skLineSegment(sketch, "E4854", {"start": v(4542.94, 3917.5) * mm, "end": v(4519.86, 3774.94) * mm});
            skLineSegment(sketch, "E4855", {"start": v(4519.86, 3774.94) * mm, "end": v(4241.8, 3797.3) * mm});
            skLineSegment(sketch, "E4856", {"start": v(4241.8, 3797.3) * mm, "end": v(4241.8, 3941.72) * mm});
            skLineSegment(sketch, "E4857", {"start": v(4241.8, 3941.72) * mm, "end": v(4241.76, 3942.89) * mm});
            skLineSegment(sketch, "E4858", {"start": v(4241.76, 3942.89) * mm, "end": v(4241.66, 3944.95) * mm});
            skLineSegment(sketch, "E4859", {"start": v(4241.66, 3944.95) * mm, "end": v(4241.44, 3947.9) * mm});
            skLineSegment(sketch, "E4860", {"start": v(4241.44, 3947.9) * mm, "end": v(4241.08, 3951.74) * mm});
            skLineSegment(sketch, "E4861", {"start": v(4241.08, 3951.74) * mm, "end": v(4240.53, 3956.46) * mm});
            skLineSegment(sketch, "E4862", {"start": v(4240.53, 3956.46) * mm, "end": v(4239.75, 3962.06) * mm});
            skLineSegment(sketch, "E4863", {"start": v(4239.75, 3962.06) * mm, "end": v(4238.71, 3968.52) * mm});
            skLineSegment(sketch, "E4864", {"start": v(4238.71, 3968.52) * mm, "end": v(4237.37, 3975.84) * mm});
            skLineSegment(sketch, "E4865", {"start": v(4237.37, 3975.84) * mm, "end": v(4235.7, 3984) * mm});
            skLineSegment(sketch, "E4866", {"start": v(4235.7, 3984) * mm, "end": v(4233.63, 3993.01) * mm});
            skLineSegment(sketch, "E4867", {"start": v(4233.63, 3993.01) * mm, "end": v(4231.16, 4002.84) * mm});
            skLineSegment(sketch, "E4868", {"start": v(4231.16, 4002.84) * mm, "end": v(4228.23, 4013.47) * mm});
            skLineSegment(sketch, "E4869", {"start": v(4228.23, 4013.47) * mm, "end": v(4224.82, 4024.9) * mm});
            skLineSegment(sketch, "E4870", {"start": v(4224.82, 4024.9) * mm, "end": v(4220.88, 4037.1) * mm});
            skLineSegment(sketch, "E4871", {"start": v(4220.88, 4037.1) * mm, "end": v(4216.38, 4050.06) * mm});
            skLineSegment(sketch, "E4872", {"start": v(4216.38, 4050.06) * mm, "end": v(4211.3, 4063.77) * mm});
            skLineSegment(sketch, "E4873", {"start": v(4211.3, 4063.77) * mm, "end": v(4205.57, 4078.19) * mm});
            skLineSegment(sketch, "E4874", {"start": v(4205.57, 4078.19) * mm, "end": v(4199.2, 4093.3) * mm});
            skLineSegment(sketch, "E4875", {"start": v(4199.2, 4093.3) * mm, "end": v(4192.12, 4109.1) * mm});
            skLineSegment(sketch, "E4876", {"start": v(4192.12, 4109.1) * mm, "end": v(4184.32, 4125.55) * mm});
            skLineSegment(sketch, "E4877", {"start": v(4184.32, 4125.55) * mm, "end": v(4175.75, 4142.62) * mm});
            skLineSegment(sketch, "E4878", {"start": v(4175.75, 4142.62) * mm, "end": v(4166.4, 4160.3) * mm});
            skLineSegment(sketch, "E4879", {"start": v(4166.4, 4160.3) * mm, "end": v(4156.23, 4178.55) * mm});
            skLineSegment(sketch, "E4880", {"start": v(4156.23, 4178.55) * mm, "end": v(4145.21, 4197.35) * mm});
            skLineSegment(sketch, "E4881", {"start": v(4145.21, 4197.35) * mm, "end": v(4133.32, 4216.66) * mm});
            skLineSegment(sketch, "E4882", {"start": v(4133.32, 4216.66) * mm, "end": v(4120.51, 4236.47) * mm});
            skLineSegment(sketch, "E4883", {"start": v(4120.51, 4236.47) * mm, "end": v(4106.78, 4256.73) * mm});
            skLineSegment(sketch, "E4884", {"start": v(4106.78, 4256.73) * mm, "end": v(4092.08, 4277.43) * mm});
            skLineSegment(sketch, "E4885", {"start": v(4092.08, 4277.43) * mm, "end": v(4076.4, 4298.5) * mm});
            skLineSegment(sketch, "E4886", {"start": v(4076.4, 4298.5) * mm, "end": v(4059.73, 4319.95) * mm});
            skLineSegment(sketch, "E4887", {"start": v(4059.73, 4319.95) * mm, "end": v(4042.63, 4334.7) * mm});
            skLineSegment(sketch, "E4888", {"start": v(4042.63, 4334.7) * mm, "end": v(3911.58, 4319.42) * mm});
            skLineSegment(sketch, "E4889", {"start": v(3911.58, 4319.42) * mm, "end": v(3898.33, 4301.13) * mm});
            skLineSegment(sketch, "E4890", {"start": v(3898.33, 4301.13) * mm, "end": v(3887.03, 4276.42) * mm});
            skLineSegment(sketch, "E4891", {"start": v(3887.03, 4276.42) * mm, "end": v(3876.63, 4252.3) * mm});
            skLineSegment(sketch, "E4892", {"start": v(3876.63, 4252.3) * mm, "end": v(3867.1, 4228.78) * mm});
            skLineSegment(sketch, "E4893", {"start": v(3867.1, 4228.78) * mm, "end": v(3858.39, 4205.9) * mm});
            skLineSegment(sketch, "E4894", {"start": v(3858.39, 4205.9) * mm, "end": v(3850.49, 4183.68) * mm});
            skLineSegment(sketch, "E4895", {"start": v(3850.49, 4183.68) * mm, "end": v(3843.35, 4162.14) * mm});
            skLineSegment(sketch, "E4896", {"start": v(3843.35, 4162.14) * mm, "end": v(3836.95, 4141.31) * mm});
            skLineSegment(sketch, "E4897", {"start": v(3836.95, 4141.31) * mm, "end": v(3831.26, 4121.21) * mm});
            skLineSegment(sketch, "E4898", {"start": v(3831.26, 4121.21) * mm, "end": v(3826.23, 4101.86) * mm});
            skLineSegment(sketch, "E4899", {"start": v(3826.23, 4101.86) * mm, "end": v(3821.82, 4083.27) * mm});
            skLineSegment(sketch, "E4900", {"start": v(3821.82, 4083.27) * mm, "end": v(3818.01, 4065.47) * mm});
            skLineSegment(sketch, "E4901", {"start": v(3818.01, 4065.47) * mm, "end": v(3814.76, 4048.47) * mm});
            skLineSegment(sketch, "E4902", {"start": v(3814.76, 4048.47) * mm, "end": v(3812.03, 4032.3) * mm});
            skLineSegment(sketch, "E4903", {"start": v(3812.03, 4032.3) * mm, "end": v(3809.79, 4016.94) * mm});
            skLineSegment(sketch, "E4904", {"start": v(3809.79, 4016.94) * mm, "end": v(3807.99, 4002.44) * mm});
            skLineSegment(sketch, "E4905", {"start": v(3807.99, 4002.44) * mm, "end": v(3806.6, 3988.79) * mm});
            skLineSegment(sketch, "E4906", {"start": v(3806.6, 3988.79) * mm, "end": v(3805.57, 3976) * mm});
            skLineSegment(sketch, "E4907", {"start": v(3805.57, 3976) * mm, "end": v(3804.88, 3964.1) * mm});
            skLineSegment(sketch, "E4908", {"start": v(3804.88, 3964.1) * mm, "end": v(3804.48, 3953.08) * mm});
            skLineSegment(sketch, "E4909", {"start": v(3804.48, 3953.08) * mm, "end": v(3804.33, 3942.95) * mm});
            skLineSegment(sketch, "E4910", {"start": v(3804.33, 3942.95) * mm, "end": v(3804.4, 3933.7) * mm});
            skLineSegment(sketch, "E4911", {"start": v(3804.4, 3933.7) * mm, "end": v(3804.64, 3925.37) * mm});
            skLineSegment(sketch, "E4912", {"start": v(3804.64, 3925.37) * mm, "end": v(3805.02, 3917.94) * mm});
            skLineSegment(sketch, "E4913", {"start": v(3805.02, 3917.94) * mm, "end": v(3805.5, 3911.41) * mm});
            skLineSegment(sketch, "E4914", {"start": v(3805.5, 3911.41) * mm, "end": v(3806.03, 3905.79) * mm});
            skLineSegment(sketch, "E4915", {"start": v(3806.03, 3905.79) * mm, "end": v(3806.58, 3901.07) * mm});
            skLineSegment(sketch, "E4916", {"start": v(3806.58, 3901.07) * mm, "end": v(3807.1, 3897.25) * mm});
            skLineSegment(sketch, "E4917", {"start": v(3807.1, 3897.25) * mm, "end": v(3807.58, 3894.33) * mm});
            skLineSegment(sketch, "E4918", {"start": v(3807.58, 3894.33) * mm, "end": v(3807.95, 3892.3) * mm});
            skLineSegment(sketch, "E4919", {"start": v(3807.95, 3892.3) * mm, "end": v(3808.19, 3891.15) * mm});
            skLineSegment(sketch, "E4920", {"start": v(3808.19, 3891.15) * mm, "end": v(3841.42, 3750.6) * mm});
            skLineSegment(sketch, "E4921", {"start": v(3841.42, 3750.6) * mm, "end": v(3575.97, 3664.86) * mm});
            skLineSegment(sketch, "E4922", {"start": v(3575.97, 3664.86) * mm, "end": v(3520.7, 3798.29) * mm});
            skLineSegment(sketch, "E4923", {"start": v(3520.7, 3798.29) * mm, "end": v(3520.22, 3799.35) * mm});
            skLineSegment(sketch, "E4924", {"start": v(3520.22, 3799.35) * mm, "end": v(3519.34, 3801.21) * mm});
            skLineSegment(sketch, "E4925", {"start": v(3519.34, 3801.21) * mm, "end": v(3518, 3803.86) * mm});
            skLineSegment(sketch, "E4926", {"start": v(3518, 3803.86) * mm, "end": v(3516.2, 3807.27) * mm});
            skLineSegment(sketch, "E4927", {"start": v(3516.2, 3807.27) * mm, "end": v(3513.89, 3811.42) * mm});
            skLineSegment(sketch, "E4928", {"start": v(3513.89, 3811.42) * mm, "end": v(3511.03, 3816.29) * mm});
            skLineSegment(sketch, "E4929", {"start": v(3511.03, 3816.29) * mm, "end": v(3507.6, 3821.86) * mm});
            skLineSegment(sketch, "E4930", {"start": v(3507.6, 3821.86) * mm, "end": v(3503.55, 3828.11) * mm});
            skLineSegment(sketch, "E4931", {"start": v(3503.55, 3828.11) * mm, "end": v(3498.87, 3835.02) * mm});
            skLineSegment(sketch, "E4932", {"start": v(3498.87, 3835.02) * mm, "end": v(3493.53, 3842.55) * mm});
            skLineSegment(sketch, "E4933", {"start": v(3493.53, 3842.55) * mm, "end": v(3487.48, 3850.68) * mm});
            skLineSegment(sketch, "E4934", {"start": v(3487.48, 3850.68) * mm, "end": v(3480.7, 3859.38) * mm});
            skLineSegment(sketch, "E4935", {"start": v(3480.7, 3859.38) * mm, "end": v(3473.18, 3868.63) * mm});
            skLineSegment(sketch, "E4936", {"start": v(3473.18, 3868.63) * mm, "end": v(3464.87, 3878.4) * mm});
            skLineSegment(sketch, "E4937", {"start": v(3464.87, 3878.4) * mm, "end": v(3455.76, 3888.65) * mm});
            skLineSegment(sketch, "E4938", {"start": v(3455.76, 3888.65) * mm, "end": v(3445.81, 3899.37) * mm});
            skLineSegment(sketch, "E4939", {"start": v(3445.81, 3899.37) * mm, "end": v(3435, 3910.5) * mm});
            skLineSegment(sketch, "E4940", {"start": v(3435, 3910.5) * mm, "end": v(3423.33, 3922.03) * mm});
            skLineSegment(sketch, "E4941", {"start": v(3423.33, 3922.03) * mm, "end": v(3410.75, 3933.91) * mm});
            skLineSegment(sketch, "E4942", {"start": v(3410.75, 3933.91) * mm, "end": v(3397.25, 3946.12) * mm});
            skLineSegment(sketch, "E4943", {"start": v(3397.25, 3946.12) * mm, "end": v(3382.8, 3958.62) * mm});
            skLineSegment(sketch, "E4944", {"start": v(3382.8, 3958.62) * mm, "end": v(3367.4, 3971.37) * mm});
            skLineSegment(sketch, "E4945", {"start": v(3367.4, 3971.37) * mm, "end": v(3351.02, 3984.34) * mm});
            skLineSegment(sketch, "E4946", {"start": v(3351.02, 3984.34) * mm, "end": v(3333.64, 3997.5) * mm});
            skLineSegment(sketch, "E4947", {"start": v(3333.64, 3997.5) * mm, "end": v(3315.26, 4010.78) * mm});
            skLineSegment(sketch, "E4948", {"start": v(3315.26, 4010.78) * mm, "end": v(3295.85, 4024.18) * mm});
            skLineSegment(sketch, "E4949", {"start": v(3295.85, 4024.18) * mm, "end": v(3275.4, 4037.65) * mm});
            skLineSegment(sketch, "E4950", {"start": v(3275.4, 4037.65) * mm, "end": v(3253.92, 4051.14) * mm});
            skLineSegment(sketch, "E4951", {"start": v(3253.92, 4051.14) * mm, "end": v(3231.36, 4064.62) * mm});
            skLineSegment(sketch, "E4952", {"start": v(3231.36, 4064.62) * mm, "end": v(3207.74, 4078.05) * mm});
            skLineSegment(sketch, "E4953", {"start": v(3207.74, 4078.05) * mm, "end": v(3186.3, 4085.14) * mm});
            skLineSegment(sketch, "E4954", {"start": v(3186.3, 4085.14) * mm, "end": v(3071.07, 4020.86) * mm});
            skLineSegment(sketch, "E4955", {"start": v(3071.07, 4020.86) * mm, "end": v(3065.84, 3998.9) * mm});
            skLineSegment(sketch, "E4956", {"start": v(3065.84, 3998.9) * mm, "end": v(3064.85, 3971.75) * mm});
            skLineSegment(sketch, "E4957", {"start": v(3064.85, 3971.75) * mm, "end": v(3064.47, 3945.48) * mm});
            skLineSegment(sketch, "E4958", {"start": v(3064.47, 3945.48) * mm, "end": v(3064.66, 3920.1) * mm});
            skLineSegment(sketch, "E4959", {"start": v(3064.66, 3920.1) * mm, "end": v(3065.38, 3895.63) * mm});
            skLineSegment(sketch, "E4960", {"start": v(3065.38, 3895.63) * mm, "end": v(3066.58, 3872.08) * mm});
            skLineSegment(sketch, "E4961", {"start": v(3066.58, 3872.08) * mm, "end": v(3068.23, 3849.45) * mm});
            skLineSegment(sketch, "E4962", {"start": v(3068.23, 3849.45) * mm, "end": v(3070.3, 3827.76) * mm});
            skLineSegment(sketch, "E4963", {"start": v(3070.3, 3827.76) * mm, "end": v(3072.72, 3807) * mm});
            skLineSegment(sketch, "E4964", {"start": v(3072.72, 3807) * mm, "end": v(3075.48, 3787.2) * mm});
            skLineSegment(sketch, "E4965", {"start": v(3075.48, 3787.2) * mm, "end": v(3078.53, 3768.34) * mm});
            skLineSegment(sketch, "E4966", {"start": v(3078.53, 3768.34) * mm, "end": v(3081.82, 3750.44) * mm});
            skLineSegment(sketch, "E4967", {"start": v(3081.82, 3750.44) * mm, "end": v(3085.32, 3733.5) * mm});
            skLineSegment(sketch, "E4968", {"start": v(3085.32, 3733.5) * mm, "end": v(3089, 3717.5) * mm});
            skLineSegment(sketch, "E4969", {"start": v(3089, 3717.5) * mm, "end": v(3092.79, 3702.46) * mm});
            skLineSegment(sketch, "E4970", {"start": v(3092.79, 3702.46) * mm, "end": v(3096.68, 3688.37) * mm});
            skLineSegment(sketch, "E4971", {"start": v(3096.68, 3688.37) * mm, "end": v(3100.61, 3675.22) * mm});
            skLineSegment(sketch, "E4972", {"start": v(3100.61, 3675.22) * mm, "end": v(3104.56, 3663.02) * mm});
            skLineSegment(sketch, "E4973", {"start": v(3104.56, 3663.02) * mm, "end": v(3108.47, 3651.76) * mm});
            skLineSegment(sketch, "E4974", {"start": v(3108.47, 3651.76) * mm, "end": v(3112.32, 3641.42) * mm});
            skLineSegment(sketch, "E4975", {"start": v(3112.32, 3641.42) * mm, "end": v(3116.06, 3632) * mm});
            skLineSegment(sketch, "E4976", {"start": v(3116.06, 3632) * mm, "end": v(3119.66, 3623.5) * mm});
            skLineSegment(sketch, "E4977", {"start": v(3119.66, 3623.5) * mm, "end": v(3123.07, 3615.89) * mm});
            skLineSegment(sketch, "E4978", {"start": v(3123.07, 3615.89) * mm, "end": v(3126.27, 3609.17) * mm});
            skLineSegment(sketch, "E4979", {"start": v(3126.27, 3609.17) * mm, "end": v(3129.2, 3603.32) * mm});
            skLineSegment(sketch, "E4980", {"start": v(3129.2, 3603.32) * mm, "end": v(3131.85, 3598.32) * mm});
            skLineSegment(sketch, "E4981", {"start": v(3131.85, 3598.32) * mm, "end": v(3134.17, 3594.17) * mm});
            skLineSegment(sketch, "E4982", {"start": v(3134.17, 3594.17) * mm, "end": v(3136.12, 3590.85) * mm});
            skLineSegment(sketch, "E4983", {"start": v(3136.12, 3590.85) * mm, "end": v(3137.67, 3588.33) * mm});
            skLineSegment(sketch, "E4984", {"start": v(3137.67, 3588.33) * mm, "end": v(3138.8, 3586.6) * mm});
            skLineSegment(sketch, "E4985", {"start": v(3138.8, 3586.6) * mm, "end": v(3139.44, 3585.63) * mm});
            skLineSegment(sketch, "E4986", {"start": v(3139.44, 3585.63) * mm, "end": v(3223.93, 3468.5) * mm});
            skLineSegment(sketch, "E4987", {"start": v(3223.93, 3468.5) * mm, "end": v(3011.5, 3287.7) * mm});
            skLineSegment(sketch, "E4988", {"start": v(3011.5, 3287.7) * mm, "end": v(2909.38, 3389.82) * mm});
            skLineSegment(sketch, "E4989", {"start": v(2909.38, 3389.82) * mm, "end": v(2908.53, 3390.62) * mm});
            skLineSegment(sketch, "E4990", {"start": v(2908.53, 3390.62) * mm, "end": v(2907, 3392) * mm});
            skLineSegment(sketch, "E4991", {"start": v(2907, 3392) * mm, "end": v(2904.76, 3393.93) * mm});
            skLineSegment(sketch, "E4992", {"start": v(2904.76, 3393.93) * mm, "end": v(2901.79, 3396.4) * mm});
            skLineSegment(sketch, "E4993", {"start": v(2901.79, 3396.4) * mm, "end": v(2898.06, 3399.34) * mm});
            skLineSegment(sketch, "E4994", {"start": v(2898.06, 3399.34) * mm, "end": v(2893.56, 3402.75) * mm});
            skLineSegment(sketch, "E4995", {"start": v(2893.56, 3402.75) * mm, "end": v(2888.25, 3406.58) * mm});
            skLineSegment(sketch, "E4996", {"start": v(2888.25, 3406.58) * mm, "end": v(2882.13, 3410.81) * mm});
            skLineSegment(sketch, "E4997", {"start": v(2882.13, 3410.81) * mm, "end": v(2875.16, 3415.4) * mm});
            skLineSegment(sketch, "E4998", {"start": v(2875.16, 3415.4) * mm, "end": v(2867.34, 3420.3) * mm});
            skLineSegment(sketch, "E4999", {"start": v(2867.34, 3420.3) * mm, "end": v(2858.64, 3425.5) * mm});
            skLineSegment(sketch, "E5000", {"start": v(2858.64, 3425.5) * mm, "end": v(2849.05, 3430.96) * mm});
            skLineSegment(sketch, "E5001", {"start": v(2849.05, 3430.96) * mm, "end": v(2838.56, 3436.62) * mm});
            skLineSegment(sketch, "E5002", {"start": v(2838.56, 3436.62) * mm, "end": v(2827.15, 3442.47) * mm});
            skLineSegment(sketch, "E5003", {"start": v(2827.15, 3442.47) * mm, "end": v(2814.8, 3448.45) * mm});
            skLineSegment(sketch, "E5004", {"start": v(2814.8, 3448.45) * mm, "end": v(2801.51, 3454.54) * mm});
            skLineSegment(sketch, "E5005", {"start": v(2801.51, 3454.54) * mm, "end": v(2787.27, 3460.7) * mm});
            skLineSegment(sketch, "E5006", {"start": v(2787.27, 3460.7) * mm, "end": v(2772.07, 3466.87) * mm});
            skLineSegment(sketch, "E5007", {"start": v(2772.07, 3466.87) * mm, "end": v(2755.9, 3473.04) * mm});
            skLineSegment(sketch, "E5008", {"start": v(2755.9, 3473.04) * mm, "end": v(2738.75, 3479.15) * mm});
            skLineSegment(sketch, "E5009", {"start": v(2738.75, 3479.15) * mm, "end": v(2720.62, 3485.17) * mm});
            skLineSegment(sketch, "E5010", {"start": v(2720.62, 3485.17) * mm, "end": v(2701.51, 3491.06) * mm});
            skLineSegment(sketch, "E5011", {"start": v(2701.51, 3491.06) * mm, "end": v(2681.42, 3496.77) * mm});
            skLineSegment(sketch, "E5012", {"start": v(2681.42, 3496.77) * mm, "end": v(2660.33, 3502.27) * mm});
            skLineSegment(sketch, "E5013", {"start": v(2660.33, 3502.27) * mm, "end": v(2638.26, 3507.52) * mm});
            skLineSegment(sketch, "E5014", {"start": v(2638.26, 3507.52) * mm, "end": v(2615.2, 3512.47) * mm});
            skLineSegment(sketch, "E5015", {"start": v(2615.2, 3512.47) * mm, "end": v(2591.16, 3517.09) * mm});
            skLineSegment(sketch, "E5016", {"start": v(2591.16, 3517.09) * mm, "end": v(2566.14, 3521.33) * mm});
            skLineSegment(sketch, "E5017", {"start": v(2566.14, 3521.33) * mm, "end": v(2540.15, 3525.15) * mm});
            skLineSegment(sketch, "E5018", {"start": v(2540.15, 3525.15) * mm, "end": v(2513.19, 3528.52) * mm});
            skLineSegment(sketch, "E5019", {"start": v(2513.19, 3528.52) * mm, "end": v(2490.67, 3526.86) * mm});
            skLineSegment(sketch, "E5020", {"start": v(2490.67, 3526.86) * mm, "end": v(2408.8, 3423.39) * mm});
            skLineSegment(sketch, "E5021", {"start": v(2408.8, 3423.39) * mm, "end": v(2412.37, 3401.09) * mm});
            skLineSegment(sketch, "E5022", {"start": v(2412.37, 3401.09) * mm, "end": v(2421.85, 3375.63) * mm});
            skLineSegment(sketch, "E5023", {"start": v(2421.85, 3375.63) * mm, "end": v(2431.56, 3351.21) * mm});
            skLineSegment(sketch, "E5024", {"start": v(2431.56, 3351.21) * mm, "end": v(2441.44, 3327.84) * mm});
            skLineSegment(sketch, "E5025", {"start": v(2441.44, 3327.84) * mm, "end": v(2451.47, 3305.5) * mm});
            skLineSegment(sketch, "E5026", {"start": v(2451.47, 3305.5) * mm, "end": v(2461.6, 3284.2) * mm});
            skLineSegment(sketch, "E5027", {"start": v(2461.6, 3284.2) * mm, "end": v(2471.78, 3263.93) * mm});
            skLineSegment(sketch, "E5028", {"start": v(2471.78, 3263.93) * mm, "end": v(2481.98, 3244.68) * mm});
            skLineSegment(sketch, "E5029", {"start": v(2481.98, 3244.68) * mm, "end": v(2492.17, 3226.44) * mm});
            skLineSegment(sketch, "E5030", {"start": v(2492.17, 3226.44) * mm, "end": v(2502.3, 3209.2) * mm});
            skLineSegment(sketch, "E5031", {"start": v(2502.3, 3209.2) * mm, "end": v(2512.32, 3192.94) * mm});
            skLineSegment(sketch, "E5032", {"start": v(2512.32, 3192.94) * mm, "end": v(2522.22, 3177.66) * mm});
            skLineSegment(sketch, "E5033", {"start": v(2522.22, 3177.66) * mm, "end": v(2531.94, 3163.34) * mm});
            skLineSegment(sketch, "E5034", {"start": v(2531.94, 3163.34) * mm, "end": v(2541.45, 3149.97) * mm});
            skLineSegment(sketch, "E5035", {"start": v(2541.45, 3149.97) * mm, "end": v(2550.72, 3137.53) * mm});
            skLineSegment(sketch, "E5036", {"start": v(2550.72, 3137.53) * mm, "end": v(2559.7, 3126) * mm});
            skLineSegment(sketch, "E5037", {"start": v(2559.7, 3126) * mm, "end": v(2568.37, 3115.36) * mm});
            skLineSegment(sketch, "E5038", {"start": v(2568.37, 3115.36) * mm, "end": v(2576.68, 3105.6) * mm});
            skLineSegment(sketch, "E5039", {"start": v(2576.68, 3105.6) * mm, "end": v(2584.6, 3096.69) * mm});
            skLineSegment(sketch, "E5040", {"start": v(2584.6, 3096.69) * mm, "end": v(2592.12, 3088.61) * mm});
            skLineSegment(sketch, "E5041", {"start": v(2592.12, 3088.61) * mm, "end": v(2599.18, 3081.34) * mm});
            skLineSegment(sketch, "E5042", {"start": v(2599.18, 3081.34) * mm, "end": v(2605.76, 3074.86) * mm});
            skLineSegment(sketch, "E5043", {"start": v(2605.76, 3074.86) * mm, "end": v(2611.83, 3069.14) * mm});
            skLineSegment(sketch, "E5044", {"start": v(2611.83, 3069.14) * mm, "end": v(2617.35, 3064.15) * mm});
            skLineSegment(sketch, "E5045", {"start": v(2617.35, 3064.15) * mm, "end": v(2622.3, 3059.87) * mm});
            skLineSegment(sketch, "E5046", {"start": v(2622.3, 3059.87) * mm, "end": v(2626.66, 3056.27) * mm});
            skLineSegment(sketch, "E5047", {"start": v(2626.66, 3056.27) * mm, "end": v(2630.38, 3053.32) * mm});
            skLineSegment(sketch, "E5048", {"start": v(2630.38, 3053.32) * mm, "end": v(2633.46, 3051) * mm});
            skLineSegment(sketch, "E5049", {"start": v(2633.46, 3051) * mm, "end": v(2635.86, 3049.26) * mm});
            skLineSegment(sketch, "E5050", {"start": v(2635.86, 3049.26) * mm, "end": v(2637.55, 3048.09) * mm});
            skLineSegment(sketch, "E5051", {"start": v(2637.55, 3048.09) * mm, "end": v(2638.53, 3047.45) * mm});
            skLineSegment(sketch, "E5052", {"start": v(2638.53, 3047.45) * mm, "end": v(2761.4, 2971.56) * mm});
            skLineSegment(sketch, "E5053", {"start": v(2761.4, 2971.56) * mm, "end": v(2634.34, 2723.23) * mm});
            skLineSegment(sketch, "E5054", {"start": v(2634.34, 2723.23) * mm, "end": v(2500.91, 2778.5) * mm});
            skLineSegment(sketch, "E5055", {"start": v(2500.91, 2778.5) * mm, "end": v(2499.82, 2778.91) * mm});
            skLineSegment(sketch, "E5056", {"start": v(2499.82, 2778.91) * mm, "end": v(2497.88, 2779.6) * mm});
            skLineSegment(sketch, "E5057", {"start": v(2497.88, 2779.6) * mm, "end": v(2495.07, 2780.53) * mm});
            skLineSegment(sketch, "E5058", {"start": v(2495.07, 2780.53) * mm, "end": v(2491.38, 2781.67) * mm});
            skLineSegment(sketch, "E5059", {"start": v(2491.38, 2781.67) * mm, "end": v(2486.81, 2782.97) * mm});
            skLineSegment(sketch, "E5060", {"start": v(2486.81, 2782.97) * mm, "end": v(2481.34, 2784.4) * mm});
            skLineSegment(sketch, "E5061", {"start": v(2481.34, 2784.4) * mm, "end": v(2474.98, 2785.9) * mm});
            skLineSegment(sketch, "E5062", {"start": v(2474.98, 2785.9) * mm, "end": v(2467.7, 2787.47) * mm});
            skLineSegment(sketch, "E5063", {"start": v(2467.7, 2787.47) * mm, "end": v(2459.5, 2789.04) * mm});
            skLineSegment(sketch, "E5064", {"start": v(2459.5, 2789.04) * mm, "end": v(2450.4, 2790.58) * mm});
            skLineSegment(sketch, "E5065", {"start": v(2450.4, 2790.58) * mm, "end": v(2440.38, 2792.05) * mm});
            skLineSegment(sketch, "E5066", {"start": v(2440.38, 2792.05) * mm, "end": v(2429.43, 2793.42) * mm});
            skLineSegment(sketch, "E5067", {"start": v(2429.43, 2793.42) * mm, "end": v(2417.57, 2794.64) * mm});
            skLineSegment(sketch, "E5068", {"start": v(2417.57, 2794.64) * mm, "end": v(2404.79, 2795.67) * mm});
            skLineSegment(sketch, "E5069", {"start": v(2404.79, 2795.67) * mm, "end": v(2391.1, 2796.48) * mm});
            skLineSegment(sketch, "E5070", {"start": v(2391.1, 2796.48) * mm, "end": v(2376.49, 2797.02) * mm});
            skLineSegment(sketch, "E5071", {"start": v(2376.49, 2797.02) * mm, "end": v(2360.97, 2797.25) * mm});
            skLineSegment(sketch, "E5072", {"start": v(2360.97, 2797.25) * mm, "end": v(2344.56, 2797.14) * mm});
            skLineSegment(sketch, "E5073", {"start": v(2344.56, 2797.14) * mm, "end": v(2327.26, 2796.65) * mm});
            skLineSegment(sketch, "E5074", {"start": v(2327.26, 2796.65) * mm, "end": v(2309.08, 2795.74) * mm});
            skLineSegment(sketch, "E5075", {"start": v(2309.08, 2795.74) * mm, "end": v(2290.03, 2794.36) * mm});
            skLineSegment(sketch, "E5076", {"start": v(2290.03, 2794.36) * mm, "end": v(2270.12, 2792.49) * mm});
            skLineSegment(sketch, "E5077", {"start": v(2270.12, 2792.49) * mm, "end": v(2249.37, 2790.07) * mm});
            skLineSegment(sketch, "E5078", {"start": v(2249.37, 2790.07) * mm, "end": v(2227.79, 2787.09) * mm});
            skLineSegment(sketch, "E5079", {"start": v(2227.79, 2787.09) * mm, "end": v(2205.39, 2783.49) * mm});
            skLineSegment(sketch, "E5080", {"start": v(2205.39, 2783.49) * mm, "end": v(2182.19, 2779.24) * mm});
            skLineSegment(sketch, "E5081", {"start": v(2182.19, 2779.24) * mm, "end": v(2158.21, 2774.3) * mm});
            skLineSegment(sketch, "E5082", {"start": v(2158.21, 2774.3) * mm, "end": v(2133.47, 2768.65) * mm});
            skLineSegment(sketch, "E5083", {"start": v(2133.47, 2768.65) * mm, "end": v(2108, 2762.23) * mm});
            skLineSegment(sketch, "E5084", {"start": v(2108, 2762.23) * mm, "end": v(2081.8, 2755.03) * mm});
            skLineSegment(sketch, "E5085", {"start": v(2081.8, 2755.03) * mm, "end": v(2061.62, 2744.88) * mm});
            skLineSegment(sketch, "E5086", {"start": v(2061.62, 2744.88) * mm, "end": v(2025.6, 2617.95) * mm});
            skLineSegment(sketch, "E5087", {"start": v(2025.6, 2617.95) * mm, "end": v(2037.42, 2598.71) * mm});
            skLineSegment(sketch, "E5088", {"start": v(2037.42, 2598.71) * mm, "end": v(2055.93, 2578.82) * mm});
            skLineSegment(sketch, "E5089", {"start": v(2055.93, 2578.82) * mm, "end": v(2074.24, 2559.98) * mm});
            skLineSegment(sketch, "E5090", {"start": v(2074.24, 2559.98) * mm, "end": v(2092.31, 2542.16) * mm});
            skLineSegment(sketch, "E5091", {"start": v(2092.31, 2542.16) * mm, "end": v(2110.12, 2525.37) * mm});
            skLineSegment(sketch, "E5092", {"start": v(2110.12, 2525.37) * mm, "end": v(2127.63, 2509.56) * mm});
            skLineSegment(sketch, "E5093", {"start": v(2127.63, 2509.56) * mm, "end": v(2144.8, 2494.73) * mm});
            skLineSegment(sketch, "E5094", {"start": v(2144.8, 2494.73) * mm, "end": v(2161.59, 2480.85) * mm});
            skLineSegment(sketch, "E5095", {"start": v(2161.59, 2480.85) * mm, "end": v(2177.98, 2467.9) * mm});
            skLineSegment(sketch, "E5096", {"start": v(2177.98, 2467.9) * mm, "end": v(2193.93, 2455.84) * mm});
            skLineSegment(sketch, "E5097", {"start": v(2193.93, 2455.84) * mm, "end": v(2209.42, 2444.66) * mm});
            skLineSegment(sketch, "E5098", {"start": v(2209.42, 2444.66) * mm, "end": v(2224.4, 2434.33) * mm});
            skLineSegment(sketch, "E5099", {"start": v(2224.4, 2434.33) * mm, "end": v(2238.87, 2424.82) * mm});
            skLineSegment(sketch, "E5100", {"start": v(2238.87, 2424.82) * mm, "end": v(2252.78, 2416.1) * mm});
            skLineSegment(sketch, "E5101", {"start": v(2252.78, 2416.1) * mm, "end": v(2266.1, 2408.16) * mm});
            skLineSegment(sketch, "E5102", {"start": v(2266.1, 2408.16) * mm, "end": v(2278.8, 2400.94) * mm});
            skLineSegment(sketch, "E5103", {"start": v(2278.8, 2400.94) * mm, "end": v(2290.89, 2394.43) * mm});
            skLineSegment(sketch, "E5104", {"start": v(2290.89, 2394.43) * mm, "end": v(2302.3, 2388.6) * mm});
            skLineSegment(sketch, "E5105", {"start": v(2302.3, 2388.6) * mm, "end": v(2313.04, 2383.4) * mm});
            skLineSegment(sketch, "E5106", {"start": v(2313.04, 2383.4) * mm, "end": v(2323.07, 2378.8) * mm});
            skLineSegment(sketch, "E5107", {"start": v(2323.07, 2378.8) * mm, "end": v(2332.37, 2374.8) * mm});
            skLineSegment(sketch, "E5108", {"start": v(2332.37, 2374.8) * mm, "end": v(2340.93, 2371.33) * mm});
            skLineSegment(sketch, "E5109", {"start": v(2340.93, 2371.33) * mm, "end": v(2348.72, 2368.36) * mm});
            skLineSegment(sketch, "E5110", {"start": v(2348.72, 2368.36) * mm, "end": v(2355.74, 2365.86) * mm});
            skLineSegment(sketch, "E5111", {"start": v(2355.74, 2365.86) * mm, "end": v(2361.95, 2363.8) * mm});
            skLineSegment(sketch, "E5112", {"start": v(2361.95, 2363.8) * mm, "end": v(2367.35, 2362.15) * mm});
            skLineSegment(sketch, "E5113", {"start": v(2367.35, 2362.15) * mm, "end": v(2371.92, 2360.85) * mm});
            skLineSegment(sketch, "E5114", {"start": v(2371.92, 2360.85) * mm, "end": v(2375.65, 2359.88) * mm});
            skLineSegment(sketch, "E5115", {"start": v(2375.65, 2359.88) * mm, "end": v(2378.53, 2359.2) * mm});
            skLineSegment(sketch, "E5116", {"start": v(2378.53, 2359.2) * mm, "end": v(2380.55, 2358.76) * mm});
            skLineSegment(sketch, "E5117", {"start": v(2380.55, 2358.76) * mm, "end": v(2381.7, 2358.54) * mm});
            skLineSegment(sketch, "E5118", {"start": v(2381.7, 2358.54) * mm, "end": v(2524.26, 2335.45) * mm});
            skLineSegment(sketch, "E5119", {"start": v(2524.26, 2335.45) * mm, "end": v(2501.9, 2057.4) * mm});
            skLineSegment(sketch, "E5120", {"start": v(2501.9, 2057.4) * mm, "end": v(2357.48, 2057.4) * mm});
            skLineSegment(sketch, "E5121", {"start": v(2357.48, 2057.4) * mm, "end": v(2356.31, 2057.36) * mm});
            skLineSegment(sketch, "E5122", {"start": v(2356.31, 2057.36) * mm, "end": v(2354.25, 2057.26) * mm});
            skLineSegment(sketch, "E5123", {"start": v(2354.25, 2057.26) * mm, "end": v(2351.3, 2057.04) * mm});
            skLineSegment(sketch, "E5124", {"start": v(2351.3, 2057.04) * mm, "end": v(2347.46, 2056.68) * mm});
            skLineSegment(sketch, "E5125", {"start": v(2347.46, 2056.68) * mm, "end": v(2342.74, 2056.13) * mm});
            skLineSegment(sketch, "E5126", {"start": v(2342.74, 2056.13) * mm, "end": v(2337.14, 2055.35) * mm});
            skLineSegment(sketch, "E5127", {"start": v(2337.14, 2055.35) * mm, "end": v(2330.68, 2054.31) * mm});
            skLineSegment(sketch, "E5128", {"start": v(2330.68, 2054.31) * mm, "end": v(2323.36, 2052.97) * mm});
            skLineSegment(sketch, "E5129", {"start": v(2323.36, 2052.97) * mm, "end": v(2315.2, 2051.29) * mm});
            skLineSegment(sketch, "E5130", {"start": v(2315.2, 2051.29) * mm, "end": v(2306.19, 2049.23) * mm});
            skLineSegment(sketch, "E5131", {"start": v(2306.19, 2049.23) * mm, "end": v(2296.36, 2046.76) * mm});
            skLineSegment(sketch, "E5132", {"start": v(2296.36, 2046.76) * mm, "end": v(2285.73, 2043.83) * mm});
            skLineSegment(sketch, "E5133", {"start": v(2285.73, 2043.83) * mm, "end": v(2274.3, 2040.42) * mm});
            skLineSegment(sketch, "E5134", {"start": v(2274.3, 2040.42) * mm, "end": v(2262.1, 2036.48) * mm});
            skLineSegment(sketch, "E5135", {"start": v(2262.1, 2036.48) * mm, "end": v(2249.14, 2031.98) * mm});
            skLineSegment(sketch, "E5136", {"start": v(2249.14, 2031.98) * mm, "end": v(2235.43, 2026.9) * mm});
            skLineSegment(sketch, "E5137", {"start": v(2235.43, 2026.9) * mm, "end": v(2221.01, 2021.17) * mm});
            skLineSegment(sketch, "E5138", {"start": v(2221.01, 2021.17) * mm, "end": v(2205.9, 2014.8) * mm});
            skLineSegment(sketch, "E5139", {"start": v(2205.9, 2014.8) * mm, "end": v(2190.1, 2007.72) * mm});
            skLineSegment(sketch, "E5140", {"start": v(2190.1, 2007.72) * mm, "end": v(2173.65, 1999.91) * mm});
            skLineSegment(sketch, "E5141", {"start": v(2173.65, 1999.91) * mm, "end": v(2156.58, 1991.35) * mm});
            skLineSegment(sketch, "E5142", {"start": v(2156.58, 1991.35) * mm, "end": v(2138.9, 1982) * mm});
            skLineSegment(sketch, "E5143", {"start": v(2138.9, 1982) * mm, "end": v(2120.65, 1971.83) * mm});
            skLineSegment(sketch, "E5144", {"start": v(2120.65, 1971.83) * mm, "end": v(2101.85, 1960.81) * mm});
            skLineSegment(sketch, "E5145", {"start": v(2101.85, 1960.81) * mm, "end": v(2082.54, 1948.92) * mm});
            skLineSegment(sketch, "E5146", {"start": v(2082.54, 1948.92) * mm, "end": v(2062.73, 1936.11) * mm});
            skLineSegment(sketch, "E5147", {"start": v(2062.73, 1936.11) * mm, "end": v(2042.47, 1922.38) * mm});
            skLineSegment(sketch, "E5148", {"start": v(2042.47, 1922.38) * mm, "end": v(2021.78, 1907.68) * mm});
            skLineSegment(sketch, "E5149", {"start": v(2021.78, 1907.68) * mm, "end": v(2000.7, 1892) * mm});
            skLineSegment(sketch, "E5150", {"start": v(2000.7, 1892) * mm, "end": v(1979.25, 1875.33) * mm});
            skLineSegment(sketch, "E5151", {"start": v(1979.25, 1875.33) * mm, "end": v(1964.5, 1858.23) * mm});
            skLineSegment(sketch, "E5152", {"start": v(1964.5, 1858.23) * mm, "end": v(1979.78, 1727.18) * mm});
            skLineSegment(sketch, "E5153", {"start": v(1979.78, 1727.18) * mm, "end": v(1998.07, 1713.93) * mm});
            skLineSegment(sketch, "E5154", {"start": v(1998.07, 1713.93) * mm, "end": v(2022.78, 1702.63) * mm});
            skLineSegment(sketch, "E5155", {"start": v(2022.78, 1702.63) * mm, "end": v(2046.9, 1692.23) * mm});
            skLineSegment(sketch, "E5156", {"start": v(2046.9, 1692.23) * mm, "end": v(2070.42, 1682.7) * mm});
            skLineSegment(sketch, "E5157", {"start": v(2070.42, 1682.7) * mm, "end": v(2093.3, 1673.99) * mm});
            skLineSegment(sketch, "E5158", {"start": v(2093.3, 1673.99) * mm, "end": v(2115.52, 1666.09) * mm});
            skLineSegment(sketch, "E5159", {"start": v(2115.52, 1666.09) * mm, "end": v(2137.06, 1658.95) * mm});
            skLineSegment(sketch, "E5160", {"start": v(2137.06, 1658.95) * mm, "end": v(2157.89, 1652.55) * mm});
            skLineSegment(sketch, "E5161", {"start": v(2157.89, 1652.55) * mm, "end": v(2177.99, 1646.86) * mm});
            skLineSegment(sketch, "E5162", {"start": v(2177.99, 1646.86) * mm, "end": v(2197.34, 1641.83) * mm});
            skLineSegment(sketch, "E5163", {"start": v(2197.34, 1641.83) * mm, "end": v(2215.93, 1637.42) * mm});
            skLineSegment(sketch, "E5164", {"start": v(2215.93, 1637.42) * mm, "end": v(2233.73, 1633.61) * mm});
            skLineSegment(sketch, "E5165", {"start": v(2233.73, 1633.61) * mm, "end": v(2250.73, 1630.36) * mm});
            skLineSegment(sketch, "E5166", {"start": v(2250.73, 1630.36) * mm, "end": v(2266.9, 1627.63) * mm});
            skLineSegment(sketch, "E5167", {"start": v(2266.9, 1627.63) * mm, "end": v(2282.26, 1625.39) * mm});
            skLineSegment(sketch, "E5168", {"start": v(2282.26, 1625.39) * mm, "end": v(2296.76, 1623.59) * mm});
            skLineSegment(sketch, "E5169", {"start": v(2296.76, 1623.59) * mm, "end": v(2310.41, 1622.2) * mm});
            skLineSegment(sketch, "E5170", {"start": v(2310.41, 1622.2) * mm, "end": v(2323.2, 1621.17) * mm});
            skLineSegment(sketch, "E5171", {"start": v(2323.2, 1621.17) * mm, "end": v(2335.1, 1620.48) * mm});
            skLineSegment(sketch, "E5172", {"start": v(2335.1, 1620.48) * mm, "end": v(2346.12, 1620.08) * mm});
            skLineSegment(sketch, "E5173", {"start": v(2346.12, 1620.08) * mm, "end": v(2356.25, 1619.93) * mm});
            skLineSegment(sketch, "E5174", {"start": v(2356.25, 1619.93) * mm, "end": v(2365.5, 1620) * mm});
            skLineSegment(sketch, "E5175", {"start": v(2365.5, 1620) * mm, "end": v(2373.83, 1620.24) * mm});
            skLineSegment(sketch, "E5176", {"start": v(2373.83, 1620.24) * mm, "end": v(2381.26, 1620.62) * mm});
            skLineSegment(sketch, "E5177", {"start": v(2381.26, 1620.62) * mm, "end": v(2387.79, 1621.1) * mm});
            skLineSegment(sketch, "E5178", {"start": v(2387.79, 1621.1) * mm, "end": v(2393.41, 1621.63) * mm});
            skLineSegment(sketch, "E5179", {"start": v(2393.41, 1621.63) * mm, "end": v(2398.13, 1622.18) * mm});
            skLineSegment(sketch, "E5180", {"start": v(2398.13, 1622.18) * mm, "end": v(2401.95, 1622.7) * mm});
            skLineSegment(sketch, "E5181", {"start": v(2401.95, 1622.7) * mm, "end": v(2404.87, 1623.18) * mm});
            skLineSegment(sketch, "E5182", {"start": v(2404.87, 1623.18) * mm, "end": v(2406.9, 1623.55) * mm});
            skLineSegment(sketch, "E5183", {"start": v(2406.9, 1623.55) * mm, "end": v(2408.05, 1623.79) * mm});
            skLineSegment(sketch, "E5184", {"start": v(2408.05, 1623.79) * mm, "end": v(2548.6, 1657.02) * mm});
            skLineSegment(sketch, "E5185", {"start": v(2548.6, 1657.02) * mm, "end": v(2634.34, 1391.57) * mm});
            skLineSegment(sketch, "E5186", {"start": v(2634.34, 1391.57) * mm, "end": v(2500.91, 1336.3) * mm});
            skLineSegment(sketch, "E5187", {"start": v(2500.91, 1336.3) * mm, "end": v(2499.85, 1335.82) * mm});
            skLineSegment(sketch, "E5188", {"start": v(2499.85, 1335.82) * mm, "end": v(2497.99, 1334.93) * mm});
            skLineSegment(sketch, "E5189", {"start": v(2497.99, 1334.93) * mm, "end": v(2495.34, 1333.6) * mm});
            skLineSegment(sketch, "E5190", {"start": v(2495.34, 1333.6) * mm, "end": v(2491.93, 1331.8) * mm});
            skLineSegment(sketch, "E5191", {"start": v(2491.93, 1331.8) * mm, "end": v(2487.78, 1329.49) * mm});
            skLineSegment(sketch, "E5192", {"start": v(2487.78, 1329.49) * mm, "end": v(2482.91, 1326.63) * mm});
            skLineSegment(sketch, "E5193", {"start": v(2482.91, 1326.63) * mm, "end": v(2477.34, 1323.2) * mm});
            skLineSegment(sketch, "E5194", {"start": v(2477.34, 1323.2) * mm, "end": v(2471.09, 1319.15) * mm});
            skLineSegment(sketch, "E5195", {"start": v(2471.09, 1319.15) * mm, "end": v(2464.18, 1314.47) * mm});
            skLineSegment(sketch, "E5196", {"start": v(2464.18, 1314.47) * mm, "end": v(2456.65, 1309.13) * mm});
            skLineSegment(sketch, "E5197", {"start": v(2456.65, 1309.13) * mm, "end": v(2448.52, 1303.08) * mm});
            skLineSegment(sketch, "E5198", {"start": v(2448.52, 1303.08) * mm, "end": v(2439.82, 1296.3) * mm});
            skLineSegment(sketch, "E5199", {"start": v(2439.82, 1296.3) * mm, "end": v(2430.57, 1288.78) * mm});
            skLineSegment(sketch, "E5200", {"start": v(2430.57, 1288.78) * mm, "end": v(2420.8, 1280.47) * mm});
            skLineSegment(sketch, "E5201", {"start": v(2420.8, 1280.47) * mm, "end": v(2410.55, 1271.36) * mm});
            skLineSegment(sketch, "E5202", {"start": v(2410.55, 1271.36) * mm, "end": v(2399.84, 1261.41) * mm});
            skLineSegment(sketch, "E5203", {"start": v(2399.84, 1261.41) * mm, "end": v(2388.7, 1250.6) * mm});
            skLineSegment(sketch, "E5204", {"start": v(2388.7, 1250.6) * mm, "end": v(2377.17, 1238.93) * mm});
            skLineSegment(sketch, "E5205", {"start": v(2377.17, 1238.93) * mm, "end": v(2365.29, 1226.35) * mm});
            skLineSegment(sketch, "E5206", {"start": v(2365.29, 1226.35) * mm, "end": v(2353.08, 1212.85) * mm});
            skLineSegment(sketch, "E5207", {"start": v(2353.08, 1212.85) * mm, "end": v(2340.58, 1198.4) * mm});
            skLineSegment(sketch, "E5208", {"start": v(2340.58, 1198.4) * mm, "end": v(2327.83, 1183) * mm});
            skLineSegment(sketch, "E5209", {"start": v(2327.83, 1183) * mm, "end": v(2314.86, 1166.62) * mm});
            skLineSegment(sketch, "E5210", {"start": v(2314.86, 1166.62) * mm, "end": v(2301.7, 1149.24) * mm});
            skLineSegment(sketch, "E5211", {"start": v(2301.7, 1149.24) * mm, "end": v(2288.42, 1130.86) * mm});
            skLineSegment(sketch, "E5212", {"start": v(2288.42, 1130.86) * mm, "end": v(2275.02, 1111.45) * mm});
            skLineSegment(sketch, "E5213", {"start": v(2275.02, 1111.45) * mm, "end": v(2261.55, 1091) * mm});
            skLineSegment(sketch, "E5214", {"start": v(2261.55, 1091) * mm, "end": v(2248.06, 1069.51) * mm});
            skLineSegment(sketch, "E5215", {"start": v(2248.06, 1069.51) * mm, "end": v(2234.58, 1046.96) * mm});
            skLineSegment(sketch, "E5216", {"start": v(2234.58, 1046.96) * mm, "end": v(2221.15, 1023.34) * mm});
            skLineSegment(sketch, "E5217", {"start": v(2221.15, 1023.34) * mm, "end": v(2214.06, 1001.9) * mm});
            skLineSegment(sketch, "E5218", {"start": v(2214.06, 1001.9) * mm, "end": v(2278.34, 886.67) * mm});
            skLineSegment(sketch, "E5219", {"start": v(2278.34, 886.67) * mm, "end": v(2300.3, 881.43) * mm});
            skLineSegment(sketch, "E5220", {"start": v(2300.3, 881.43) * mm, "end": v(2327.46, 880.45) * mm});
            skLineSegment(sketch, "E5221", {"start": v(2327.46, 880.45) * mm, "end": v(2353.73, 880.07) * mm});
            skLineSegment(sketch, "E5222", {"start": v(2353.73, 880.07) * mm, "end": v(2379.1, 880.26) * mm});
            skLineSegment(sketch, "E5223", {"start": v(2379.1, 880.26) * mm, "end": v(2403.57, 880.98) * mm});
            skLineSegment(sketch, "E5224", {"start": v(2403.57, 880.98) * mm, "end": v(2427.12, 882.18) * mm});
            skLineSegment(sketch, "E5225", {"start": v(2427.12, 882.18) * mm, "end": v(2449.75, 883.83) * mm});
            skLineSegment(sketch, "E5226", {"start": v(2449.75, 883.83) * mm, "end": v(2471.44, 885.9) * mm});
            skLineSegment(sketch, "E5227", {"start": v(2471.44, 885.9) * mm, "end": v(2492.2, 888.32) * mm});
            skLineSegment(sketch, "E5228", {"start": v(2492.2, 888.32) * mm, "end": v(2512, 891.08) * mm});
            skLineSegment(sketch, "E5229", {"start": v(2512, 891.08) * mm, "end": v(2530.86, 894.12) * mm});
            skLineSegment(sketch, "E5230", {"start": v(2530.86, 894.12) * mm, "end": v(2548.76, 897.42) * mm});
            skLineSegment(sketch, "E5231", {"start": v(2548.76, 897.42) * mm, "end": v(2565.7, 900.92) * mm});
            skLineSegment(sketch, "E5232", {"start": v(2565.7, 900.92) * mm, "end": v(2581.7, 904.59) * mm});
            skLineSegment(sketch, "E5233", {"start": v(2581.7, 904.59) * mm, "end": v(2596.74, 908.39) * mm});
            skLineSegment(sketch, "E5234", {"start": v(2596.74, 908.39) * mm, "end": v(2610.83, 912.27) * mm});
            skLineSegment(sketch, "E5235", {"start": v(2610.83, 912.27) * mm, "end": v(2623.98, 916.21) * mm});
            skLineSegment(sketch, "E5236", {"start": v(2623.98, 916.21) * mm, "end": v(2636.18, 920.16) * mm});
            skLineSegment(sketch, "E5237", {"start": v(2636.18, 920.16) * mm, "end": v(2647.44, 924.07) * mm});
            skLineSegment(sketch, "E5238", {"start": v(2647.44, 924.07) * mm, "end": v(2657.78, 927.92) * mm});
            skLineSegment(sketch, "E5239", {"start": v(2657.78, 927.92) * mm, "end": v(2667.2, 931.66) * mm});
            skLineSegment(sketch, "E5240", {"start": v(2667.2, 931.66) * mm, "end": v(2675.7, 935.26) * mm});
            skLineSegment(sketch, "E5241", {"start": v(2675.7, 935.26) * mm, "end": v(2683.31, 938.67) * mm});
            skLineSegment(sketch, "E5242", {"start": v(2683.31, 938.67) * mm, "end": v(2690.04, 941.87) * mm});
            skLineSegment(sketch, "E5243", {"start": v(2690.04, 941.87) * mm, "end": v(2695.89, 944.8) * mm});
            skLineSegment(sketch, "E5244", {"start": v(2695.89, 944.8) * mm, "end": v(2700.88, 947.45) * mm});
            skLineSegment(sketch, "E5245", {"start": v(2700.88, 947.45) * mm, "end": v(2705.03, 949.77) * mm});
            skLineSegment(sketch, "E5246", {"start": v(2705.03, 949.77) * mm, "end": v(2708.35, 951.72) * mm});
            skLineSegment(sketch, "E5247", {"start": v(2708.35, 951.72) * mm, "end": v(2710.87, 953.27) * mm});
            skLineSegment(sketch, "E5248", {"start": v(2710.87, 953.27) * mm, "end": v(2712.6, 954.4) * mm});
            skLineSegment(sketch, "E5249", {"start": v(2712.6, 954.4) * mm, "end": v(2713.57, 955.04) * mm});
            skLineSegment(sketch, "E5250", {"start": v(2713.57, 955.04) * mm, "end": v(2830.7, 1039.53) * mm});
            skLineSegment(sketch, "E5251", {"start": v(2830.7, 1039.53) * mm, "end": v(3011.5, 827.1) * mm});
            skLineSegment(sketch, "E5252", {"start": v(3011.5, 827.1) * mm, "end": v(2909.38, 724.98) * mm});
            skLineSegment(sketch, "E5253", {"start": v(2909.38, 724.98) * mm, "end": v(2908.58, 724.13) * mm});
            skLineSegment(sketch, "E5254", {"start": v(2908.58, 724.13) * mm, "end": v(2907.2, 722.6) * mm});
            skLineSegment(sketch, "E5255", {"start": v(2907.2, 722.6) * mm, "end": v(2905.27, 720.36) * mm});
            skLineSegment(sketch, "E5256", {"start": v(2905.27, 720.36) * mm, "end": v(2902.81, 717.39) * mm});
            skLineSegment(sketch, "E5257", {"start": v(2902.81, 717.39) * mm, "end": v(2899.86, 713.66) * mm});
            skLineSegment(sketch, "E5258", {"start": v(2899.86, 713.66) * mm, "end": v(2896.45, 709.16) * mm});
            skLineSegment(sketch, "E5259", {"start": v(2896.45, 709.16) * mm, "end": v(2892.62, 703.85) * mm});
            skLineSegment(sketch, "E5260", {"start": v(2892.62, 703.85) * mm, "end": v(2888.39, 697.73) * mm});
            skLineSegment(sketch, "E5261", {"start": v(2888.39, 697.73) * mm, "end": v(2883.8, 690.76) * mm});
            skLineSegment(sketch, "E5262", {"start": v(2883.8, 690.76) * mm, "end": v(2878.9, 682.94) * mm});
            skLineSegment(sketch, "E5263", {"start": v(2878.9, 682.94) * mm, "end": v(2873.7, 674.24) * mm});
            skLineSegment(sketch, "E5264", {"start": v(2873.7, 674.24) * mm, "end": v(2868.24, 664.65) * mm});
            skLineSegment(sketch, "E5265", {"start": v(2868.24, 664.65) * mm, "end": v(2862.58, 654.16) * mm});
            skLineSegment(sketch, "E5266", {"start": v(2862.58, 654.16) * mm, "end": v(2856.73, 642.75) * mm});
            skLineSegment(sketch, "E5267", {"start": v(2856.73, 642.75) * mm, "end": v(2850.75, 630.4) * mm});
            skLineSegment(sketch, "E5268", {"start": v(2850.75, 630.4) * mm, "end": v(2844.66, 617.11) * mm});
            skLineSegment(sketch, "E5269", {"start": v(2844.66, 617.11) * mm, "end": v(2838.5, 602.87) * mm});
            skLineSegment(sketch, "E5270", {"start": v(2838.5, 602.87) * mm, "end": v(2832.33, 587.67) * mm});
            skLineSegment(sketch, "E5271", {"start": v(2832.33, 587.67) * mm, "end": v(2826.16, 571.5) * mm});
            skLineSegment(sketch, "E5272", {"start": v(2826.16, 571.5) * mm, "end": v(2820.05, 554.35) * mm});
            skLineSegment(sketch, "E5273", {"start": v(2820.05, 554.35) * mm, "end": v(2814.03, 536.22) * mm});
            skLineSegment(sketch, "E5274", {"start": v(2814.03, 536.22) * mm, "end": v(2808.14, 517.11) * mm});
            skLineSegment(sketch, "E5275", {"start": v(2808.14, 517.11) * mm, "end": v(2802.43, 497.02) * mm});
            skLineSegment(sketch, "E5276", {"start": v(2802.43, 497.02) * mm, "end": v(2796.93, 475.93) * mm});
            skLineSegment(sketch, "E5277", {"start": v(2796.93, 475.93) * mm, "end": v(2791.68, 453.86) * mm});
            skLineSegment(sketch, "E5278", {"start": v(2791.68, 453.86) * mm, "end": v(2786.73, 430.8) * mm});
            skLineSegment(sketch, "E5279", {"start": v(2786.73, 430.8) * mm, "end": v(2782.11, 406.76) * mm});
            skLineSegment(sketch, "E5280", {"start": v(2782.11, 406.76) * mm, "end": v(2777.87, 381.74) * mm});
            skLineSegment(sketch, "E5281", {"start": v(2777.87, 381.74) * mm, "end": v(2774.05, 355.75) * mm});
            skLineSegment(sketch, "E5282", {"start": v(2774.05, 355.75) * mm, "end": v(2770.68, 328.79) * mm});
            skLineSegment(sketch, "E5283", {"start": v(2770.68, 328.79) * mm, "end": v(2772.34, 306.27) * mm});
            skLineSegment(sketch, "E5284", {"start": v(2772.34, 306.27) * mm, "end": v(2875.81, 224.4) * mm});
            skLineSegment(sketch, "E5285", {"start": v(2875.81, 224.4) * mm, "end": v(2898.11, 227.97) * mm});
            skLineSegment(sketch, "E5286", {"start": v(2898.11, 227.97) * mm, "end": v(2923.57, 237.45) * mm});
            skLineSegment(sketch, "E5287", {"start": v(2923.57, 237.45) * mm, "end": v(2947.99, 247.16) * mm});
            skLineSegment(sketch, "E5288", {"start": v(2947.99, 247.16) * mm, "end": v(2971.36, 257.04) * mm});
            skLineSegment(sketch, "E5289", {"start": v(2971.36, 257.04) * mm, "end": v(2993.7, 267.07) * mm});
            skLineSegment(sketch, "E5290", {"start": v(2993.7, 267.07) * mm, "end": v(3015, 277.2) * mm});
            skLineSegment(sketch, "E5291", {"start": v(3015, 277.2) * mm, "end": v(3035.27, 287.38) * mm});
            skLineSegment(sketch, "E5292", {"start": v(3035.27, 287.38) * mm, "end": v(3054.52, 297.58) * mm});
            skLineSegment(sketch, "E5293", {"start": v(3054.52, 297.58) * mm, "end": v(3072.76, 307.77) * mm});
            skLineSegment(sketch, "E5294", {"start": v(3072.76, 307.77) * mm, "end": v(3090, 317.9) * mm});
            skLineSegment(sketch, "E5295", {"start": v(3090, 317.9) * mm, "end": v(3106.26, 327.92) * mm});
            skLineSegment(sketch, "E5296", {"start": v(3106.26, 327.92) * mm, "end": v(3121.54, 337.82) * mm});
            skLineSegment(sketch, "E5297", {"start": v(3121.54, 337.82) * mm, "end": v(3135.86, 347.54) * mm});
            skLineSegment(sketch, "E5298", {"start": v(3135.86, 347.54) * mm, "end": v(3149.23, 357.05) * mm});
            skLineSegment(sketch, "E5299", {"start": v(3149.23, 357.05) * mm, "end": v(3161.67, 366.31) * mm});
            skLineSegment(sketch, "E5300", {"start": v(3161.67, 366.31) * mm, "end": v(3173.2, 375.3) * mm});
            skLineSegment(sketch, "E5301", {"start": v(3173.2, 375.3) * mm, "end": v(3183.84, 383.96) * mm});
            skLineSegment(sketch, "E5302", {"start": v(3183.84, 383.96) * mm, "end": v(3193.6, 392.28) * mm});
            skLineSegment(sketch, "E5303", {"start": v(3193.6, 392.28) * mm, "end": v(3202.51, 400.2) * mm});
            skLineSegment(sketch, "E5304", {"start": v(3202.51, 400.2) * mm, "end": v(3210.59, 407.72) * mm});
            skLineSegment(sketch, "E5305", {"start": v(3210.59, 407.72) * mm, "end": v(3217.86, 414.78) * mm});
            skLineSegment(sketch, "E5306", {"start": v(3217.86, 414.78) * mm, "end": v(3224.34, 421.36) * mm});
            skLineSegment(sketch, "E5307", {"start": v(3224.34, 421.36) * mm, "end": v(3230.06, 427.43) * mm});
            skLineSegment(sketch, "E5308", {"start": v(3230.06, 427.43) * mm, "end": v(3235.05, 432.95) * mm});
            skLineSegment(sketch, "E5309", {"start": v(3235.05, 432.95) * mm, "end": v(3239.33, 437.9) * mm});
            skLineSegment(sketch, "E5310", {"start": v(3239.33, 437.9) * mm, "end": v(3242.93, 442.25) * mm});
            skLineSegment(sketch, "E5311", {"start": v(3242.93, 442.25) * mm, "end": v(3245.88, 445.98) * mm});
            skLineSegment(sketch, "E5312", {"start": v(3245.88, 445.98) * mm, "end": v(3248.2, 449.06) * mm});
            skLineSegment(sketch, "E5313", {"start": v(3248.2, 449.06) * mm, "end": v(3249.94, 451.46) * mm});
            skLineSegment(sketch, "E5314", {"start": v(3249.94, 451.46) * mm, "end": v(3251.11, 453.15) * mm});
            skLineSegment(sketch, "E5315", {"start": v(3251.11, 453.15) * mm, "end": v(3251.75, 454.13) * mm});
            skLineSegment(sketch, "E5316", {"start": v(3251.75, 454.13) * mm, "end": v(3327.64, 577) * mm});
            skLineSegment(sketch, "E5317", {"start": v(3327.64, 577) * mm, "end": v(3575.97, 449.94) * mm});
            skLineSegment(sketch, "E5318", {"start": v(3575.97, 449.94) * mm, "end": v(3520.7, 316.51) * mm});
            skLineSegment(sketch, "E5319", {"start": v(3520.7, 316.51) * mm, "end": v(3520.3, 315.42) * mm});
            skLineSegment(sketch, "E5320", {"start": v(3520.3, 315.42) * mm, "end": v(3519.6, 313.48) * mm});
            skLineSegment(sketch, "E5321", {"start": v(3519.6, 313.48) * mm, "end": v(3518.67, 310.67) * mm});
            skLineSegment(sketch, "E5322", {"start": v(3518.67, 310.67) * mm, "end": v(3517.53, 306.98) * mm});
            skLineSegment(sketch, "E5323", {"start": v(3517.53, 306.98) * mm, "end": v(3516.23, 302.41) * mm});
            skLineSegment(sketch, "E5324", {"start": v(3516.23, 302.41) * mm, "end": v(3514.8, 296.94) * mm});
            skLineSegment(sketch, "E5325", {"start": v(3514.8, 296.94) * mm, "end": v(3513.3, 290.58) * mm});
            skLineSegment(sketch, "E5326", {"start": v(3513.3, 290.58) * mm, "end": v(3511.74, 283.3) * mm});
            skLineSegment(sketch, "E5327", {"start": v(3511.74, 283.3) * mm, "end": v(3510.16, 275.1) * mm});
            skLineSegment(sketch, "E5328", {"start": v(3510.16, 275.1) * mm, "end": v(3508.62, 266) * mm});
            skLineSegment(sketch, "E5329", {"start": v(3508.62, 266) * mm, "end": v(3507.15, 255.98) * mm});
            skLineSegment(sketch, "E5330", {"start": v(3507.15, 255.98) * mm, "end": v(3505.78, 245.03) * mm});
            skLineSegment(sketch, "E5331", {"start": v(3505.78, 245.03) * mm, "end": v(3504.56, 233.17) * mm});
            skLineSegment(sketch, "E5332", {"start": v(3504.56, 233.17) * mm, "end": v(3503.53, 220.39) * mm});
            skLineSegment(sketch, "E5333", {"start": v(3503.53, 220.39) * mm, "end": v(3502.72, 206.7) * mm});
            skLineSegment(sketch, "E5334", {"start": v(3502.72, 206.7) * mm, "end": v(3502.18, 192.09) * mm});
            skLineSegment(sketch, "E5335", {"start": v(3502.18, 192.09) * mm, "end": v(3501.95, 176.57) * mm});
            skLineSegment(sketch, "E5336", {"start": v(3501.95, 176.57) * mm, "end": v(3502.06, 160.16) * mm});
            skLineSegment(sketch, "E5337", {"start": v(3502.06, 160.16) * mm, "end": v(3502.55, 142.86) * mm});
            skLineSegment(sketch, "E5338", {"start": v(3502.55, 142.86) * mm, "end": v(3503.46, 124.68) * mm});
            skLineSegment(sketch, "E5339", {"start": v(3503.46, 124.68) * mm, "end": v(3504.84, 105.63) * mm});
            skLineSegment(sketch, "E5340", {"start": v(3504.84, 105.63) * mm, "end": v(3506.71, 85.72) * mm});
            skLineSegment(sketch, "E5341", {"start": v(3506.71, 85.72) * mm, "end": v(3509.13, 64.97) * mm});
            skLineSegment(sketch, "E5342", {"start": v(3509.13, 64.97) * mm, "end": v(3512.11, 43.39) * mm});
            skLineSegment(sketch, "E5343", {"start": v(3512.11, 43.39) * mm, "end": v(3515.71, 20.99) * mm});
            skLineSegment(sketch, "E5344", {"start": v(3515.71, 20.99) * mm, "end": v(3519.96, -2.21) * mm});
            skLineSegment(sketch, "E5345", {"start": v(3519.96, -2.21) * mm, "end": v(3524.9, -26.2) * mm});
            skLineSegment(sketch, "E5346", {"start": v(3524.9, -26.2) * mm, "end": v(3530.55, -50.93) * mm});
            skLineSegment(sketch, "E5347", {"start": v(3530.55, -50.93) * mm, "end": v(3536.97, -76.4) * mm});
            skLineSegment(sketch, "E5348", {"start": v(3536.97, -76.4) * mm, "end": v(3544.17, -102.6) * mm});
            skLineSegment(sketch, "E5349", {"start": v(3544.17, -102.6) * mm, "end": v(3554.32, -122.78) * mm});
            skLineSegment(sketch, "E5350", {"start": v(3554.32, -122.78) * mm, "end": v(3681.25, -158.8) * mm});
            skLineSegment(sketch, "E5351", {"start": v(3681.25, -158.8) * mm, "end": v(3700.49, -146.98) * mm});
            skLineSegment(sketch, "E5352", {"start": v(3700.49, -146.98) * mm, "end": v(3720.38, -128.48) * mm});
            skLineSegment(sketch, "E5353", {"start": v(3720.38, -128.48) * mm, "end": v(3739.22, -110.16) * mm});
            skLineSegment(sketch, "E5354", {"start": v(3739.22, -110.16) * mm, "end": v(3757.04, -92.09) * mm});
            skLineSegment(sketch, "E5355", {"start": v(3757.04, -92.09) * mm, "end": v(3773.83, -74.28) * mm});
            skLineSegment(sketch, "E5356", {"start": v(3773.83, -74.28) * mm, "end": v(3789.64, -56.77) * mm});
            skLineSegment(sketch, "E5357", {"start": v(3789.64, -56.77) * mm, "end": v(3804.47, -39.6) * mm});
            skLineSegment(sketch, "E5358", {"start": v(3804.47, -39.6) * mm, "end": v(3818.35, -22.81) * mm});
            skLineSegment(sketch, "E5359", {"start": v(3818.35, -22.81) * mm, "end": v(3831.3, -6.42) * mm});
            skLineSegment(sketch, "E5360", {"start": v(3831.3, -6.42) * mm, "end": v(3843.36, 9.53) * mm});
            skLineSegment(sketch, "E5361", {"start": v(3843.36, 9.53) * mm, "end": v(3854.54, 25.02) * mm});
            skLineSegment(sketch, "E5362", {"start": v(3854.54, 25.02) * mm, "end": v(3864.87, 40) * mm});
            skLineSegment(sketch, "E5363", {"start": v(3864.87, 40) * mm, "end": v(3874.38, 54.47) * mm});
            skLineSegment(sketch, "E5364", {"start": v(3874.38, 54.47) * mm, "end": v(3883.1, 68.37) * mm});
            skLineSegment(sketch, "E5365", {"start": v(3883.1, 68.37) * mm, "end": v(3891.04, 81.7) * mm});
            skLineSegment(sketch, "E5366", {"start": v(3891.04, 81.7) * mm, "end": v(3898.26, 94.4) * mm});
            skLineSegment(sketch, "E5367", {"start": v(3898.26, 94.4) * mm, "end": v(3904.77, 106.49) * mm});
            skLineSegment(sketch, "E5368", {"start": v(3904.77, 106.49) * mm, "end": v(3910.6, 117.9) * mm});
            skLineSegment(sketch, "E5369", {"start": v(3910.6, 117.9) * mm, "end": v(3915.8, 128.64) * mm});
            skLineSegment(sketch, "E5370", {"start": v(3915.8, 128.64) * mm, "end": v(3920.4, 138.67) * mm});
            skLineSegment(sketch, "E5371", {"start": v(3920.4, 138.67) * mm, "end": v(3924.4, 147.97) * mm});
            skLineSegment(sketch, "E5372", {"start": v(3924.4, 147.97) * mm, "end": v(3927.87, 156.53) * mm});
            skLineSegment(sketch, "E5373", {"start": v(3927.87, 156.53) * mm, "end": v(3930.84, 164.32) * mm});
            skLineSegment(sketch, "E5374", {"start": v(3930.84, 164.32) * mm, "end": v(3933.34, 171.34) * mm});
            skLineSegment(sketch, "E5375", {"start": v(3933.34, 171.34) * mm, "end": v(3935.4, 177.55) * mm});
            skLineSegment(sketch, "E5376", {"start": v(3935.4, 177.55) * mm, "end": v(3937.06, 182.95) * mm});
            skLineSegment(sketch, "E5377", {"start": v(3937.06, 182.95) * mm, "end": v(3938.35, 187.52) * mm});
            skLineSegment(sketch, "E5378", {"start": v(3938.35, 187.52) * mm, "end": v(3939.33, 191.25) * mm});
            skLineSegment(sketch, "E5379", {"start": v(3939.33, 191.25) * mm, "end": v(3940, 194.13) * mm});
            skLineSegment(sketch, "E5380", {"start": v(3940, 194.13) * mm, "end": v(3940.44, 196.15) * mm});
            skLineSegment(sketch, "E5381", {"start": v(3940.44, 196.15) * mm, "end": v(3940.66, 197.3) * mm});
            skLineSegment(sketch, "E5382", {"start": v(3940.66, 197.3) * mm, "end": v(3963.75, 339.86) * mm});
            skLineSegment(sketch, "E5383", {"start": v(3963.75, 339.86) * mm, "end": v(4241.8, 317.5) * mm});
            skLineSegment(sketch, "E5384", {"start": v(4241.8, 317.5) * mm, "end": v(4241.8, 173.08) * mm});
            skLineSegment(sketch, "E5385", {"start": v(4241.8, 173.08) * mm, "end": v(4241.84, 171.91) * mm});
            skLineSegment(sketch, "E5386", {"start": v(4241.84, 171.91) * mm, "end": v(4241.94, 169.85) * mm});
            skLineSegment(sketch, "E5387", {"start": v(4241.94, 169.85) * mm, "end": v(4242.16, 166.9) * mm});
            skLineSegment(sketch, "E5388", {"start": v(4242.16, 166.9) * mm, "end": v(4242.52, 163.06) * mm});
            skLineSegment(sketch, "E5389", {"start": v(4242.52, 163.06) * mm, "end": v(4243.07, 158.34) * mm});
            skLineSegment(sketch, "E5390", {"start": v(4243.07, 158.34) * mm, "end": v(4243.85, 152.74) * mm});
            skLineSegment(sketch, "E5391", {"start": v(4243.85, 152.74) * mm, "end": v(4244.89, 146.28) * mm});
            skLineSegment(sketch, "E5392", {"start": v(4244.89, 146.28) * mm, "end": v(4246.23, 138.96) * mm});
            skLineSegment(sketch, "E5393", {"start": v(4246.23, 138.96) * mm, "end": v(4247.91, 130.8) * mm});
            skLineSegment(sketch, "E5394", {"start": v(4247.91, 130.8) * mm, "end": v(4249.97, 121.79) * mm});
            skLineSegment(sketch, "E5395", {"start": v(4249.97, 121.79) * mm, "end": v(4252.44, 111.96) * mm});
            skLineSegment(sketch, "E5396", {"start": v(4252.44, 111.96) * mm, "end": v(4255.37, 101.33) * mm});
            skLineSegment(sketch, "E5397", {"start": v(4255.37, 101.33) * mm, "end": v(4258.78, 89.9) * mm});
            skLineSegment(sketch, "E5398", {"start": v(4258.78, 89.9) * mm, "end": v(4262.72, 77.7) * mm});
            skLineSegment(sketch, "E5399", {"start": v(4262.72, 77.7) * mm, "end": v(4267.22, 64.74) * mm});
            skLineSegment(sketch, "E5400", {"start": v(4267.22, 64.74) * mm, "end": v(4272.3, 51.03) * mm});
            skLineSegment(sketch, "E5401", {"start": v(4272.3, 51.03) * mm, "end": v(4278.03, 36.61) * mm});
            skLineSegment(sketch, "E5402", {"start": v(4278.03, 36.61) * mm, "end": v(4284.4, 21.5) * mm});
            skLineSegment(sketch, "E5403", {"start": v(4284.4, 21.5) * mm, "end": v(4291.48, 5.7) * mm});
            skLineSegment(sketch, "E5404", {"start": v(4291.48, 5.7) * mm, "end": v(4299.29, -10.75) * mm});
            skLineSegment(sketch, "E5405", {"start": v(4299.29, -10.75) * mm, "end": v(4307.85, -27.82) * mm});
            skLineSegment(sketch, "E5406", {"start": v(4307.85, -27.82) * mm, "end": v(4317.2, -45.5) * mm});
            skLineSegment(sketch, "E5407", {"start": v(4317.2, -45.5) * mm, "end": v(4327.37, -63.75) * mm});
            skLineSegment(sketch, "E5408", {"start": v(4327.37, -63.75) * mm, "end": v(4338.39, -82.55) * mm});
            skLineSegment(sketch, "E5409", {"start": v(4338.39, -82.55) * mm, "end": v(4350.28, -101.86) * mm});
            skLineSegment(sketch, "E5410", {"start": v(4350.28, -101.86) * mm, "end": v(4363.09, -121.67) * mm});
            skLineSegment(sketch, "E5411", {"start": v(4363.09, -121.67) * mm, "end": v(4376.82, -141.93) * mm});
            skLineSegment(sketch, "E5412", {"start": v(4376.82, -141.93) * mm, "end": v(4391.52, -162.62) * mm});
            skLineSegment(sketch, "E5413", {"start": v(4391.52, -162.62) * mm, "end": v(4407.2, -183.7) * mm});
            skLineSegment(sketch, "E5414", {"start": v(4407.2, -183.7) * mm, "end": v(4423.87, -205.15) * mm});
            skLineSegment(sketch, "E5415", {"start": v(4423.87, -205.15) * mm, "end": v(4440.97, -219.9) * mm});
            skLineSegment(sketch, "E5416", {"start": v(4440.97, -219.9) * mm, "end": v(4572.02, -204.62) * mm});
            skLineSegment(sketch, "E5417", {"start": v(4572.02, -204.62) * mm, "end": v(4585.27, -186.33) * mm});
            skLineSegment(sketch, "E5418", {"start": v(4585.27, -186.33) * mm, "end": v(4596.57, -161.62) * mm});
            skLineSegment(sketch, "E5419", {"start": v(4596.57, -161.62) * mm, "end": v(4606.97, -137.5) * mm});
            skLineSegment(sketch, "E5420", {"start": v(4606.97, -137.5) * mm, "end": v(4616.5, -113.98) * mm});
            skLineSegment(sketch, "E5421", {"start": v(4616.5, -113.98) * mm, "end": v(4625.21, -91.1) * mm});
            skLineSegment(sketch, "E5422", {"start": v(4625.21, -91.1) * mm, "end": v(4633.11, -68.88) * mm});
            skLineSegment(sketch, "E5423", {"start": v(4633.11, -68.88) * mm, "end": v(4640.25, -47.34) * mm});
            skLineSegment(sketch, "E5424", {"start": v(4640.25, -47.34) * mm, "end": v(4646.65, -26.51) * mm});
            skLineSegment(sketch, "E5425", {"start": v(4646.65, -26.51) * mm, "end": v(4652.34, -6.41) * mm});
            skLineSegment(sketch, "E5426", {"start": v(4652.34, -6.41) * mm, "end": v(4657.37, 12.94) * mm});
            skLineSegment(sketch, "E5427", {"start": v(4657.37, 12.94) * mm, "end": v(4661.78, 31.53) * mm});
            skLineSegment(sketch, "E5428", {"start": v(4661.78, 31.53) * mm, "end": v(4665.59, 49.33) * mm});
            skLineSegment(sketch, "E5429", {"start": v(4665.59, 49.33) * mm, "end": v(4668.84, 66.33) * mm});
            skLineSegment(sketch, "E5430", {"start": v(4668.84, 66.33) * mm, "end": v(4671.57, 82.5) * mm});
            skLineSegment(sketch, "E5431", {"start": v(4671.57, 82.5) * mm, "end": v(4673.81, 97.86) * mm});
            skLineSegment(sketch, "E5432", {"start": v(4673.81, 97.86) * mm, "end": v(4675.61, 112.36) * mm});
            skLineSegment(sketch, "E5433", {"start": v(4675.61, 112.36) * mm, "end": v(4677, 126.01) * mm});
            skLineSegment(sketch, "E5434", {"start": v(4677, 126.01) * mm, "end": v(4678.03, 138.8) * mm});
            skLineSegment(sketch, "E5435", {"start": v(4678.03, 138.8) * mm, "end": v(4678.72, 150.7) * mm});
            skLineSegment(sketch, "E5436", {"start": v(4678.72, 150.7) * mm, "end": v(4679.12, 161.72) * mm});
            skLineSegment(sketch, "E5437", {"start": v(4679.12, 161.72) * mm, "end": v(4679.27, 171.85) * mm});
            skLineSegment(sketch, "E5438", {"start": v(4679.27, 171.85) * mm, "end": v(4679.2, 181.1) * mm});
            skLineSegment(sketch, "E5439", {"start": v(4679.2, 181.1) * mm, "end": v(4678.96, 189.43) * mm});
            skLineSegment(sketch, "E5440", {"start": v(4678.96, 189.43) * mm, "end": v(4678.58, 196.86) * mm});
            skLineSegment(sketch, "E5441", {"start": v(4678.58, 196.86) * mm, "end": v(4678.1, 203.39) * mm});
            skLineSegment(sketch, "E5442", {"start": v(4678.1, 203.39) * mm, "end": v(4677.57, 209.01) * mm});
            skLineSegment(sketch, "E5443", {"start": v(4677.57, 209.01) * mm, "end": v(4677.02, 213.73) * mm});
            skLineSegment(sketch, "E5444", {"start": v(4677.02, 213.73) * mm, "end": v(4676.5, 217.55) * mm});
            skLineSegment(sketch, "E5445", {"start": v(4676.5, 217.55) * mm, "end": v(4676.02, 220.47) * mm});
            skLineSegment(sketch, "E5446", {"start": v(4676.02, 220.47) * mm, "end": v(4675.65, 222.5) * mm});
            skLineSegment(sketch, "E5447", {"start": v(4675.65, 222.5) * mm, "end": v(4675.42, 223.65) * mm});
            skLineSegment(sketch, "E5448", {"start": v(4675.42, 223.65) * mm, "end": v(4642.18, 364.2) * mm});
            skLineSegment(sketch, "E5449", {"start": v(4642.18, 364.2) * mm, "end": v(4907.63, 449.94) * mm});
            skLineSegment(sketch, "E5450", {"start": v(4907.63, 449.94) * mm, "end": v(4962.9, 316.51) * mm});
            skLineSegment(sketch, "E5451", {"start": v(4962.9, 316.51) * mm, "end": v(4963.38, 315.45) * mm});
            skLineSegment(sketch, "E5452", {"start": v(4963.38, 315.45) * mm, "end": v(4964.27, 313.59) * mm});
            skLineSegment(sketch, "E5453", {"start": v(4964.27, 313.59) * mm, "end": v(4965.6, 310.94) * mm});
            skLineSegment(sketch, "E5454", {"start": v(4965.6, 310.94) * mm, "end": v(4967.4, 307.53) * mm});
            skLineSegment(sketch, "E5455", {"start": v(4967.4, 307.53) * mm, "end": v(4969.71, 303.38) * mm});
            skLineSegment(sketch, "E5456", {"start": v(4969.71, 303.38) * mm, "end": v(4972.57, 298.51) * mm});
            skLineSegment(sketch, "E5457", {"start": v(4972.57, 298.51) * mm, "end": v(4976, 292.94) * mm});
            skLineSegment(sketch, "E5458", {"start": v(4976, 292.94) * mm, "end": v(4980.05, 286.69) * mm});
            skLineSegment(sketch, "E5459", {"start": v(4980.05, 286.69) * mm, "end": v(4984.73, 279.78) * mm});
            skLineSegment(sketch, "E5460", {"start": v(4984.73, 279.78) * mm, "end": v(4990.07, 272.25) * mm});
            skLineSegment(sketch, "E5461", {"start": v(4990.07, 272.25) * mm, "end": v(4996.12, 264.12) * mm});
            skLineSegment(sketch, "E5462", {"start": v(4996.12, 264.12) * mm, "end": v(5002.9, 255.42) * mm});
            skLineSegment(sketch, "E5463", {"start": v(5002.9, 255.42) * mm, "end": v(5010.42, 246.17) * mm});
            skLineSegment(sketch, "E5464", {"start": v(5010.42, 246.17) * mm, "end": v(5018.73, 236.4) * mm});
            skLineSegment(sketch, "E5465", {"start": v(5018.73, 236.4) * mm, "end": v(5027.84, 226.15) * mm});
            skLineSegment(sketch, "E5466", {"start": v(5027.84, 226.15) * mm, "end": v(5037.79, 215.43) * mm});
            skLineSegment(sketch, "E5467", {"start": v(5037.79, 215.43) * mm, "end": v(5048.6, 204.3) * mm});
            skLineSegment(sketch, "E5468", {"start": v(5048.6, 204.3) * mm, "end": v(5060.27, 192.77) * mm});
            skLineSegment(sketch, "E5469", {"start": v(5060.27, 192.77) * mm, "end": v(5072.85, 180.89) * mm});
            skLineSegment(sketch, "E5470", {"start": v(5072.85, 180.89) * mm, "end": v(5086.35, 168.68) * mm});
            skLineSegment(sketch, "E5471", {"start": v(5086.35, 168.68) * mm, "end": v(5100.8, 156.18) * mm});
            skLineSegment(sketch, "E5472", {"start": v(5100.8, 156.18) * mm, "end": v(5116.2, 143.43) * mm});
            skLineSegment(sketch, "E5473", {"start": v(5116.2, 143.43) * mm, "end": v(5132.58, 130.46) * mm});
            skLineSegment(sketch, "E5474", {"start": v(5132.58, 130.46) * mm, "end": v(5149.96, 117.3) * mm});
            skLineSegment(sketch, "E5475", {"start": v(5149.96, 117.3) * mm, "end": v(5168.34, 104.02) * mm});
            skLineSegment(sketch, "E5476", {"start": v(5168.34, 104.02) * mm, "end": v(5187.75, 90.62) * mm});
            skLineSegment(sketch, "E5477", {"start": v(5187.75, 90.62) * mm, "end": v(5208.2, 77.15) * mm});
            skLineSegment(sketch, "E5478", {"start": v(5208.2, 77.15) * mm, "end": v(5229.69, 63.66) * mm});
            skLineSegment(sketch, "E5479", {"start": v(5229.69, 63.66) * mm, "end": v(5252.24, 50.18) * mm});
            skLineSegment(sketch, "E5480", {"start": v(5252.24, 50.18) * mm, "end": v(5275.86, 36.75) * mm});
            skLineSegment(sketch, "E5481", {"start": v(5275.86, 36.75) * mm, "end": v(5297.3, 29.66) * mm});
            skLineSegment(sketch, "E5482", {"start": v(5297.3, 29.66) * mm, "end": v(5412.53, 93.94) * mm});
            skLineSegment(sketch, "E5483", {"start": v(5412.53, 93.94) * mm, "end": v(5417.77, 115.9) * mm});
            skLineSegment(sketch, "E5484", {"start": v(5417.77, 115.9) * mm, "end": v(5418.75, 143.05) * mm});
            skLineSegment(sketch, "E5485", {"start": v(5418.75, 143.05) * mm, "end": v(5419.13, 169.32) * mm});
            skLineSegment(sketch, "E5486", {"start": v(5419.13, 169.32) * mm, "end": v(5418.94, 194.7) * mm});
            skLineSegment(sketch, "E5487", {"start": v(5418.94, 194.7) * mm, "end": v(5418.22, 219.17) * mm});
            skLineSegment(sketch, "E5488", {"start": v(5418.22, 219.17) * mm, "end": v(5417.02, 242.72) * mm});
            skLineSegment(sketch, "E5489", {"start": v(5417.02, 242.72) * mm, "end": v(5415.37, 265.35) * mm});
            skLineSegment(sketch, "E5490", {"start": v(5415.37, 265.35) * mm, "end": v(5413.3, 287.04) * mm});
            skLineSegment(sketch, "E5491", {"start": v(5413.3, 287.04) * mm, "end": v(5410.88, 307.8) * mm});
            skLineSegment(sketch, "E5492", {"start": v(5410.88, 307.8) * mm, "end": v(5408.12, 327.6) * mm});
            skLineSegment(sketch, "E5493", {"start": v(5408.12, 327.6) * mm, "end": v(5405.08, 346.46) * mm});
            skLineSegment(sketch, "E5494", {"start": v(5405.08, 346.46) * mm, "end": v(5401.78, 364.36) * mm});
            skLineSegment(sketch, "E5495", {"start": v(5401.78, 364.36) * mm, "end": v(5398.28, 381.3) * mm});
            skLineSegment(sketch, "E5496", {"start": v(5398.28, 381.3) * mm, "end": v(5394.61, 397.3) * mm});
            skLineSegment(sketch, "E5497", {"start": v(5394.61, 397.3) * mm, "end": v(5390.81, 412.34) * mm});
            skLineSegment(sketch, "E5498", {"start": v(5390.81, 412.34) * mm, "end": v(5386.93, 426.43) * mm});
            skLineSegment(sketch, "E5499", {"start": v(5386.93, 426.43) * mm, "end": v(5382.99, 439.58) * mm});
            skLineSegment(sketch, "E5500", {"start": v(5382.99, 439.58) * mm, "end": v(5379.04, 451.78) * mm});
            skLineSegment(sketch, "E5501", {"start": v(5379.04, 451.78) * mm, "end": v(5375.13, 463.04) * mm});
            skLineSegment(sketch, "E5502", {"start": v(5375.13, 463.04) * mm, "end": v(5371.28, 473.38) * mm});
            skLineSegment(sketch, "E5503", {"start": v(5371.28, 473.38) * mm, "end": v(5367.54, 482.8) * mm});
            skLineSegment(sketch, "E5504", {"start": v(5367.54, 482.8) * mm, "end": v(5363.94, 491.3) * mm});
            skLineSegment(sketch, "E5505", {"start": v(5363.94, 491.3) * mm, "end": v(5360.53, 498.91) * mm});
            skLineSegment(sketch, "E5506", {"start": v(5360.53, 498.91) * mm, "end": v(5357.33, 505.63) * mm});
            skLineSegment(sketch, "E5507", {"start": v(5357.33, 505.63) * mm, "end": v(5354.4, 511.48) * mm});
            skLineSegment(sketch, "E5508", {"start": v(5354.4, 511.48) * mm, "end": v(5351.75, 516.48) * mm});
            skLineSegment(sketch, "E5509", {"start": v(5351.75, 516.48) * mm, "end": v(5349.43, 520.63) * mm});
            skLineSegment(sketch, "E5510", {"start": v(5349.43, 520.63) * mm, "end": v(5347.48, 523.95) * mm});
            skLineSegment(sketch, "E5511", {"start": v(5347.48, 523.95) * mm, "end": v(5345.93, 526.47) * mm});
            skLineSegment(sketch, "E5512", {"start": v(5345.93, 526.47) * mm, "end": v(5344.8, 528.2) * mm});
            skLineSegment(sketch, "E5513", {"start": v(5344.8, 528.2) * mm, "end": v(5344.16, 529.17) * mm});
            skLineSegment(sketch, "E5514", {"start": v(5344.16, 529.17) * mm, "end": v(5259.67, 646.3) * mm});
            skLineSegment(sketch, "E5515", {"start": v(5259.67, 646.3) * mm, "end": v(5472.1, 827.1) * mm});
            skLineSegment(sketch, "E5516", {"start": v(5472.1, 827.1) * mm, "end": v(5574.22, 724.98) * mm});
            skLineSegment(sketch, "E5517", {"start": v(5574.22, 724.98) * mm, "end": v(5575.07, 724.18) * mm});
            skLineSegment(sketch, "E5518", {"start": v(5575.07, 724.18) * mm, "end": v(5576.6, 722.8) * mm});
            skLineSegment(sketch, "E5519", {"start": v(5576.6, 722.8) * mm, "end": v(5578.84, 720.87) * mm});
            skLineSegment(sketch, "E5520", {"start": v(5578.84, 720.87) * mm, "end": v(5581.81, 718.4) * mm});
            skLineSegment(sketch, "E5521", {"start": v(5581.81, 718.4) * mm, "end": v(5585.54, 715.46) * mm});
            skLineSegment(sketch, "E5522", {"start": v(5585.54, 715.46) * mm, "end": v(5590.04, 712.05) * mm});
            skLineSegment(sketch, "E5523", {"start": v(5590.04, 712.05) * mm, "end": v(5595.35, 708.22) * mm});
            skLineSegment(sketch, "E5524", {"start": v(5595.35, 708.22) * mm, "end": v(5601.47, 703.99) * mm});
            skLineSegment(sketch, "E5525", {"start": v(5601.47, 703.99) * mm, "end": v(5608.44, 699.4) * mm});
            skLineSegment(sketch, "E5526", {"start": v(5608.44, 699.4) * mm, "end": v(5616.26, 694.5) * mm});
            skLineSegment(sketch, "E5527", {"start": v(5616.26, 694.5) * mm, "end": v(5624.96, 689.3) * mm});
            skLineSegment(sketch, "E5528", {"start": v(5624.96, 689.3) * mm, "end": v(5634.55, 683.84) * mm});
            skLineSegment(sketch, "E5529", {"start": v(5634.55, 683.84) * mm, "end": v(5645.04, 678.18) * mm});
            skLineSegment(sketch, "E5530", {"start": v(5645.04, 678.18) * mm, "end": v(5656.45, 672.33) * mm});
            skLineSegment(sketch, "E5531", {"start": v(5656.45, 672.33) * mm, "end": v(5668.8, 666.35) * mm});
            skLineSegment(sketch, "E5532", {"start": v(5668.8, 666.35) * mm, "end": v(5682.09, 660.26) * mm});
            skLineSegment(sketch, "E5533", {"start": v(5682.09, 660.26) * mm, "end": v(5696.33, 654.1) * mm});
            skLineSegment(sketch, "E5534", {"start": v(5696.33, 654.1) * mm, "end": v(5711.53, 647.93) * mm});
            skLineSegment(sketch, "E5535", {"start": v(5711.53, 647.93) * mm, "end": v(5727.7, 641.76) * mm});
            skLineSegment(sketch, "E5536", {"start": v(5727.7, 641.76) * mm, "end": v(5744.85, 635.65) * mm});
            skLineSegment(sketch, "E5537", {"start": v(5744.85, 635.65) * mm, "end": v(5762.98, 629.63) * mm});
            skLineSegment(sketch, "E5538", {"start": v(5762.98, 629.63) * mm, "end": v(5782.09, 623.74) * mm});
            skLineSegment(sketch, "E5539", {"start": v(5782.09, 623.74) * mm, "end": v(5802.18, 618.03) * mm});
            skLineSegment(sketch, "E5540", {"start": v(5802.18, 618.03) * mm, "end": v(5823.27, 612.53) * mm});
            skLineSegment(sketch, "E5541", {"start": v(5823.27, 612.53) * mm, "end": v(5845.34, 607.28) * mm});
            skLineSegment(sketch, "E5542", {"start": v(5845.34, 607.28) * mm, "end": v(5868.4, 602.33) * mm});
            skLineSegment(sketch, "E5543", {"start": v(5868.4, 602.33) * mm, "end": v(5892.44, 597.71) * mm});
            skLineSegment(sketch, "E5544", {"start": v(5892.44, 597.71) * mm, "end": v(5917.46, 593.47) * mm});
            skLineSegment(sketch, "E5545", {"start": v(5917.46, 593.47) * mm, "end": v(5943.45, 589.65) * mm});
            skLineSegment(sketch, "E5546", {"start": v(5943.45, 589.65) * mm, "end": v(5970.41, 586.28) * mm});
            skLineSegment(sketch, "E5547", {"start": v(5970.41, 586.28) * mm, "end": v(5992.94, 587.94) * mm});
            skLineSegment(sketch, "E5548", {"start": v(5992.94, 587.94) * mm, "end": v(6074.8, 691.41) * mm});
            skLineSegment(sketch, "E5549", {"start": v(6074.8, 691.41) * mm, "end": v(6071.23, 713.71) * mm});
            skLineSegment(sketch, "E5550", {"start": v(6071.23, 713.71) * mm, "end": v(6061.75, 739.17) * mm});
            skLineSegment(sketch, "E5551", {"start": v(6061.75, 739.17) * mm, "end": v(6052.04, 763.59) * mm});
            skLineSegment(sketch, "E5552", {"start": v(6052.04, 763.59) * mm, "end": v(6042.16, 786.96) * mm});
            skLineSegment(sketch, "E5553", {"start": v(6042.16, 786.96) * mm, "end": v(6032.13, 809.3) * mm});
            skLineSegment(sketch, "E5554", {"start": v(6032.13, 809.3) * mm, "end": v(6022, 830.6) * mm});
            skLineSegment(sketch, "E5555", {"start": v(6022, 830.6) * mm, "end": v(6011.82, 850.87) * mm});
            skLineSegment(sketch, "E5556", {"start": v(6011.82, 850.87) * mm, "end": v(6001.62, 870.12) * mm});
            skLineSegment(sketch, "E5557", {"start": v(6001.62, 870.12) * mm, "end": v(5991.43, 888.36) * mm});
            skLineSegment(sketch, "E5558", {"start": v(5991.43, 888.36) * mm, "end": v(5981.3, 905.6) * mm});
            skLineSegment(sketch, "E5559", {"start": v(5981.3, 905.6) * mm, "end": v(5971.28, 921.86) * mm});
            skLineSegment(sketch, "E5560", {"start": v(5971.28, 921.86) * mm, "end": v(5961.38, 937.14) * mm});
            skLineSegment(sketch, "E5561", {"start": v(5961.38, 937.14) * mm, "end": v(5951.66, 951.46) * mm});
            skLineSegment(sketch, "E5562", {"start": v(5951.66, 951.46) * mm, "end": v(5942.15, 964.83) * mm});
            skLineSegment(sketch, "E5563", {"start": v(5942.15, 964.83) * mm, "end": v(5932.89, 977.27) * mm});
            skLineSegment(sketch, "E5564", {"start": v(5932.89, 977.27) * mm, "end": v(5923.9, 988.8) * mm});
            skLineSegment(sketch, "E5565", {"start": v(5923.9, 988.8) * mm, "end": v(5915.24, 999.44) * mm});
            skLineSegment(sketch, "E5566", {"start": v(5915.24, 999.44) * mm, "end": v(5906.92, 1009.2) * mm});
            skLineSegment(sketch, "E5567", {"start": v(5906.92, 1009.2) * mm, "end": v(5899, 1018.11) * mm});
            skLineSegment(sketch, "E5568", {"start": v(5899, 1018.11) * mm, "end": v(5891.48, 1026.19) * mm});
            skLineSegment(sketch, "E5569", {"start": v(5891.48, 1026.19) * mm, "end": v(5884.42, 1033.46) * mm});
            skLineSegment(sketch, "E5570", {"start": v(5884.42, 1033.46) * mm, "end": v(5877.84, 1039.94) * mm});
            skLineSegment(sketch, "E5571", {"start": v(5877.84, 1039.94) * mm, "end": v(5871.78, 1045.66) * mm});
            skLineSegment(sketch, "E5572", {"start": v(5871.78, 1045.66) * mm, "end": v(5866.25, 1050.65) * mm});
            skLineSegment(sketch, "E5573", {"start": v(5866.25, 1050.65) * mm, "end": v(5861.3, 1054.93) * mm});
            skLineSegment(sketch, "E5574", {"start": v(5861.3, 1054.93) * mm, "end": v(5856.95, 1058.53) * mm});
            skLineSegment(sketch, "E5575", {"start": v(5856.95, 1058.53) * mm, "end": v(5853.22, 1061.48) * mm});
            skLineSegment(sketch, "E5576", {"start": v(5853.22, 1061.48) * mm, "end": v(5850.14, 1063.8) * mm});
            skLineSegment(sketch, "E5577", {"start": v(5850.14, 1063.8) * mm, "end": v(5847.74, 1065.54) * mm});
            skLineSegment(sketch, "E5578", {"start": v(5847.74, 1065.54) * mm, "end": v(5846.05, 1066.71) * mm});
            skLineSegment(sketch, "E5579", {"start": v(5846.05, 1066.71) * mm, "end": v(5845.07, 1067.35) * mm});
            skLineSegment(sketch, "E5580", {"start": v(5845.07, 1067.35) * mm, "end": v(5722.2, 1143.24) * mm});
            skLineSegment(sketch, "E5581", {"start": v(5722.2, 1143.24) * mm, "end": v(5849.26, 1391.57) * mm});
            skLineSegment(sketch, "E5582", {"start": v(5849.26, 1391.57) * mm, "end": v(5982.7, 1336.3) * mm});
            skLineSegment(sketch, "E5583", {"start": v(5982.7, 1336.3) * mm, "end": v(5983.78, 1335.89) * mm});
            skLineSegment(sketch, "E5584", {"start": v(5983.78, 1335.89) * mm, "end": v(5985.72, 1335.2) * mm});
            skLineSegment(sketch, "E5585", {"start": v(5985.72, 1335.2) * mm, "end": v(5988.53, 1334.27) * mm});
            skLineSegment(sketch, "E5586", {"start": v(5988.53, 1334.27) * mm, "end": v(5992.22, 1333.13) * mm});
            skLineSegment(sketch, "E5587", {"start": v(5992.22, 1333.13) * mm, "end": v(5996.8, 1331.83) * mm});
            skLineSegment(sketch, "E5588", {"start": v(5996.8, 1331.83) * mm, "end": v(6002.26, 1330.4) * mm});
            skLineSegment(sketch, "E5589", {"start": v(6002.26, 1330.4) * mm, "end": v(6008.62, 1328.9) * mm});
            skLineSegment(sketch, "E5590", {"start": v(6008.62, 1328.9) * mm, "end": v(6015.9, 1327.34) * mm});
            skLineSegment(sketch, "E5591", {"start": v(6015.9, 1327.34) * mm, "end": v(6024.1, 1325.76) * mm});
            skLineSegment(sketch, "E5592", {"start": v(6024.1, 1325.76) * mm, "end": v(6033.2, 1324.22) * mm});
            skLineSegment(sketch, "E5593", {"start": v(6033.2, 1324.22) * mm, "end": v(6043.22, 1322.75) * mm});
            skLineSegment(sketch, "E5594", {"start": v(6043.22, 1322.75) * mm, "end": v(6054.17, 1321.38) * mm});
            skLineSegment(sketch, "E5595", {"start": v(6054.17, 1321.38) * mm, "end": v(6066.03, 1320.16) * mm});
            skLineSegment(sketch, "E5596", {"start": v(6066.03, 1320.16) * mm, "end": v(6078.81, 1319.13) * mm});
            skLineSegment(sketch, "E5597", {"start": v(6078.81, 1319.13) * mm, "end": v(6092.5, 1318.32) * mm});
            skLineSegment(sketch, "E5598", {"start": v(6092.5, 1318.32) * mm, "end": v(6107.12, 1317.78) * mm});
            skLineSegment(sketch, "E5599", {"start": v(6107.12, 1317.78) * mm, "end": v(6122.63, 1317.55) * mm});
            skLineSegment(sketch, "E5600", {"start": v(6122.63, 1317.55) * mm, "end": v(6139.04, 1317.66) * mm});
            skLineSegment(sketch, "E5601", {"start": v(6139.04, 1317.66) * mm, "end": v(6156.34, 1318.15) * mm});
            skLineSegment(sketch, "E5602", {"start": v(6156.34, 1318.15) * mm, "end": v(6174.52, 1319.06) * mm});
            skLineSegment(sketch, "E5603", {"start": v(6174.52, 1319.06) * mm, "end": v(6193.57, 1320.44) * mm});
            skLineSegment(sketch, "E5604", {"start": v(6193.57, 1320.44) * mm, "end": v(6213.48, 1322.31) * mm});
            skLineSegment(sketch, "E5605", {"start": v(6213.48, 1322.31) * mm, "end": v(6234.23, 1324.73) * mm});
            skLineSegment(sketch, "E5606", {"start": v(6234.23, 1324.73) * mm, "end": v(6255.82, 1327.71) * mm});
            skLineSegment(sketch, "E5607", {"start": v(6255.82, 1327.71) * mm, "end": v(6278.21, 1331.31) * mm});
            skLineSegment(sketch, "E5608", {"start": v(6278.21, 1331.31) * mm, "end": v(6301.41, 1335.56) * mm});
            skLineSegment(sketch, "E5609", {"start": v(6301.41, 1335.56) * mm, "end": v(6325.4, 1340.5) * mm});
            skLineSegment(sketch, "E5610", {"start": v(6325.4, 1340.5) * mm, "end": v(6350.13, 1346.15) * mm});
            skLineSegment(sketch, "E5611", {"start": v(6350.13, 1346.15) * mm, "end": v(6375.6, 1352.57) * mm});
            skLineSegment(sketch, "E5612", {"start": v(6375.6, 1352.57) * mm, "end": v(6401.8, 1359.77) * mm});
            skLineSegment(sketch, "E5613", {"start": v(6401.8, 1359.77) * mm, "end": v(6421.98, 1369.92) * mm});
            skLineSegment(sketch, "E5614", {"start": v(6421.98, 1369.92) * mm, "end": v(6458, 1496.85) * mm});
            skLineSegment(sketch, "E5615", {"start": v(6458, 1496.85) * mm, "end": v(6446.18, 1516.09) * mm});
            skLineSegment(sketch, "E5616", {"start": v(6446.18, 1516.09) * mm, "end": v(6427.68, 1535.98) * mm});
            skLineSegment(sketch, "E5617", {"start": v(6427.68, 1535.98) * mm, "end": v(6409.37, 1554.82) * mm});
            skLineSegment(sketch, "E5618", {"start": v(6409.37, 1554.82) * mm, "end": v(6391.29, 1572.64) * mm});
            skLineSegment(sketch, "E5619", {"start": v(6391.29, 1572.64) * mm, "end": v(6373.48, 1589.43) * mm});
            skLineSegment(sketch, "E5620", {"start": v(6373.48, 1589.43) * mm, "end": v(6355.97, 1605.24) * mm});
            skLineSegment(sketch, "E5621", {"start": v(6355.97, 1605.24) * mm, "end": v(6338.8, 1620.07) * mm});
            skLineSegment(sketch, "E5622", {"start": v(6338.8, 1620.07) * mm, "end": v(6322.01, 1633.95) * mm});
            skLineSegment(sketch, "E5623", {"start": v(6322.01, 1633.95) * mm, "end": v(6305.62, 1646.9) * mm});
            skLineSegment(sketch, "E5624", {"start": v(6305.62, 1646.9) * mm, "end": v(6289.67, 1658.96) * mm});
            skLineSegment(sketch, "E5625", {"start": v(6289.67, 1658.96) * mm, "end": v(6274.18, 1670.14) * mm});
            skLineSegment(sketch, "E5626", {"start": v(6274.18, 1670.14) * mm, "end": v(6259.2, 1680.47) * mm});
            skLineSegment(sketch, "E5627", {"start": v(6259.2, 1680.47) * mm, "end": v(6244.73, 1689.98) * mm});
            skLineSegment(sketch, "E5628", {"start": v(6244.73, 1689.98) * mm, "end": v(6230.83, 1698.7) * mm});
            skLineSegment(sketch, "E5629", {"start": v(6230.83, 1698.7) * mm, "end": v(6217.5, 1706.64) * mm});
            skLineSegment(sketch, "E5630", {"start": v(6217.5, 1706.64) * mm, "end": v(6204.8, 1713.86) * mm});
            skLineSegment(sketch, "E5631", {"start": v(6204.8, 1713.86) * mm, "end": v(6192.72, 1720.37) * mm});
            skLineSegment(sketch, "E5632", {"start": v(6192.72, 1720.37) * mm, "end": v(6181.3, 1726.2) * mm});
            skLineSegment(sketch, "E5633", {"start": v(6181.3, 1726.2) * mm, "end": v(6170.56, 1731.4) * mm});
            skLineSegment(sketch, "E5634", {"start": v(6170.56, 1731.4) * mm, "end": v(6160.53, 1736) * mm});
            skLineSegment(sketch, "E5635", {"start": v(6160.53, 1736) * mm, "end": v(6151.23, 1740) * mm});
            skLineSegment(sketch, "E5636", {"start": v(6151.23, 1740) * mm, "end": v(6142.67, 1743.47) * mm});
            skLineSegment(sketch, "E5637", {"start": v(6142.67, 1743.47) * mm, "end": v(6134.88, 1746.44) * mm});
            skLineSegment(sketch, "E5638", {"start": v(6134.88, 1746.44) * mm, "end": v(6127.86, 1748.94) * mm});
            skLineSegment(sketch, "E5639", {"start": v(6127.86, 1748.94) * mm, "end": v(6121.65, 1751) * mm});
            skLineSegment(sketch, "E5640", {"start": v(6121.65, 1751) * mm, "end": v(6116.25, 1752.65) * mm});
            skLineSegment(sketch, "E5641", {"start": v(6116.25, 1752.65) * mm, "end": v(6111.68, 1753.95) * mm});
            skLineSegment(sketch, "E5642", {"start": v(6111.68, 1753.95) * mm, "end": v(6107.95, 1754.92) * mm});
            skLineSegment(sketch, "E5643", {"start": v(6107.95, 1754.92) * mm, "end": v(6105.07, 1755.6) * mm});
            skLineSegment(sketch, "E5644", {"start": v(6105.07, 1755.6) * mm, "end": v(6103.05, 1756.04) * mm});
            skLineSegment(sketch, "E5645", {"start": v(6103.05, 1756.04) * mm, "end": v(6101.9, 1756.26) * mm});
            skLineSegment(sketch, "E5646", {"start": v(6101.9, 1756.26) * mm, "end": v(5959.34, 1779.35) * mm});
            skLineSegment(sketch, "E5647", {"start": v(5959.34, 1779.35) * mm, "end": v(5981.7, 2057.4) * mm});
            skLineSegment(sketch, "E5648", {"start": v(5981.7, 2057.4) * mm, "end": v(6126.12, 2057.4) * mm});
            skLineSegment(sketch, "E5649", {"start": v(6126.12, 2057.4) * mm, "end": v(6127.29, 2057.44) * mm});
            skLineSegment(sketch, "E5650", {"start": v(6127.29, 2057.44) * mm, "end": v(6129.35, 2057.54) * mm});
            skLineSegment(sketch, "E5651", {"start": v(4445, 2057.4) * mm, "end": v(4038.6, 2057.4) * mm});
            skFitSpline(sketch, "E5652", {"points": [v(6359.82, 2292.78) * mm, v(6359.82, 2237.72) * mm, v(6315.18, 2193.09) * mm, v(6260.12, 2193.09) * mm]});
            skFitSpline(sketch, "E5653", {"points": [v(6260.12, 2193.09) * mm, v(6205.06, 2193.09) * mm, v(6160.43, 2237.72) * mm, v(6160.43, 2292.78) * mm]});
            skFitSpline(sketch, "E5654", {"points": [v(6160.43, 2292.78) * mm, v(6160.43, 2347.85) * mm, v(6205.06, 2392.48) * mm, v(6260.12, 2392.48) * mm]});
            skFitSpline(sketch, "E5655", {"points": [v(6260.12, 2392.48) * mm, v(6315.18, 2392.48) * mm, v(6359.82, 2347.85) * mm, v(6359.82, 2292.78) * mm]});
            skLineSegment(sketch, "E5656", {"start": v(4241.8, 1854.2) * mm, "end": v(4241.8, 2260.6) * mm});
            skLineSegment(sketch, "E5657", {"start": v(4331.82, 3489.76) * mm, "end": v(4301.54, 3491.18) * mm});
            skLineSegment(sketch, "E5658", {"start": v(4301.54, 3491.18) * mm, "end": v(4271.06, 3492.2) * mm});
            skLineSegment(sketch, "E5659", {"start": v(4271.06, 3492.2) * mm, "end": v(4240.58, 3492.4) * mm});
            skLineSegment(sketch, "E5660", {"start": v(4240.58, 3492.4) * mm, "end": v(4210.1, 3492.2) * mm});
            skLineSegment(sketch, "E5661", {"start": v(4269.84, 3431.24) * mm, "end": v(4272.28, 3553.16) * mm});
            skLineSegment(sketch, "E5662", {"start": v(4335.68, 3550.51) * mm, "end": v(4302.76, 3521.66) * mm});
            skLineSegment(sketch, "E5663", {"start": v(4302.76, 3521.66) * mm, "end": v(4271.06, 3492.2) * mm});
            skLineSegment(sketch, "E5664", {"start": v(4271.06, 3492.2) * mm, "end": v(4240.58, 3461.92) * mm});
            skLineSegment(sketch, "E5665", {"start": v(4240.58, 3461.92) * mm, "end": v(4211.32, 3431.24) * mm});
            skLineSegment(sketch, "E5666", {"start": v(4328.16, 3428.8) * mm, "end": v(4300.12, 3460.9) * mm});
            skLineSegment(sketch, "E5667", {"start": v(4300.12, 3460.9) * mm, "end": v(4271.06, 3492.2) * mm});
            skLineSegment(sketch, "E5668", {"start": v(4271.06, 3492.2) * mm, "end": v(4240.58, 3522.88) * mm});
            skLineSegment(sketch, "E5669", {"start": v(4240.58, 3522.88) * mm, "end": v(4208.68, 3553.16) * mm});
            skLineSegment(sketch, "E5670", {"start": v(4399.08, 3545.23) * mm, "end": v(4434.43, 3571.65) * mm});
            skLineSegment(sketch, "E5671", {"start": v(4434.43, 3571.65) * mm, "end": v(4466.54, 3567.38) * mm});
            skLineSegment(sketch, "E5672", {"start": v(4466.54, 3567.38) * mm, "end": v(4498.65, 3562.1) * mm});
            skLineSegment(sketch, "E5673", {"start": v(4498.65, 3562.1) * mm, "end": v(4524.65, 3526.54) * mm});
            skLineSegment(sketch, "E5674", {"start": v(4524.65, 3526.54) * mm, "end": v(4518.97, 3496.46) * mm});
            skLineSegment(sketch, "E5675", {"start": v(4518.97, 3496.46) * mm, "end": v(4483.2, 3472.08) * mm});
            skLineSegment(sketch, "E5676", {"start": v(4483.2, 3472.08) * mm, "end": v(4507.38, 3436.72) * mm});
            skLineSegment(sketch, "E5677", {"start": v(4507.38, 3436.72) * mm, "end": v(4501.7, 3406.65) * mm});
            skLineSegment(sketch, "E5678", {"start": v(4501.7, 3406.65) * mm, "end": v(4467.76, 3381.86) * mm});
            skLineSegment(sketch, "E5679", {"start": v(4467.76, 3381.86) * mm, "end": v(4439.72, 3386.33) * mm});
            skLineSegment(sketch, "E5680", {"start": v(4439.72, 3386.33) * mm, "end": v(4411.47, 3390.4) * mm});
            skLineSegment(sketch, "E5681", {"start": v(4411.47, 3390.4) * mm, "end": v(4386.28, 3423.92) * mm});
            skLineSegment(sketch, "E5682", {"start": v(4453.13, 3476.96) * mm, "end": v(4483.2, 3472.08) * mm});
            skLineSegment(sketch, "E5683", {"start": v(4869.69, 3448.91) * mm, "end": v(4794.5, 3282.09) * mm});
            skLineSegment(sketch, "E5684", {"start": v(4794.5, 3282.09) * mm, "end": v(4786.17, 3335.73) * mm});
            skLineSegment(sketch, "E5685", {"start": v(4786.17, 3335.73) * mm, "end": v(4776.01, 3389.38) * mm});
            skLineSegment(sketch, "E5686", {"start": v(4776.01, 3389.38) * mm, "end": v(4763.62, 3443.22) * mm});
            skLineSegment(sketch, "E5687", {"start": v(4763.62, 3443.22) * mm, "end": v(4749.4, 3497.07) * mm});
            skLineSegment(sketch, "E5688", {"start": v(4749.4, 3497.07) * mm, "end": v(4688.64, 3324.56) * mm});
            skLineSegment(sketch, "E5689", {"start": v(5009.5, 3305.86) * mm, "end": v(4982.87, 3321.91) * mm});
            skLineSegment(sketch, "E5690", {"start": v(4982.87, 3321.91) * mm, "end": v(4955.85, 3337.36) * mm});
            skLineSegment(sketch, "E5691", {"start": v(4955.85, 3337.36) * mm, "end": v(4928.41, 3352.2) * mm});
            skLineSegment(sketch, "E5692", {"start": v(4928.41, 3352.2) * mm, "end": v(4900.78, 3366.41) * mm});
            skLineSegment(sketch, "E5693", {"start": v(4977.59, 3253.84) * mm, "end": v(4951.98, 3269.28) * mm});
            skLineSegment(sketch, "E5694", {"start": v(4951.98, 3269.28) * mm, "end": v(4926.18, 3284.12) * mm});
            skLineSegment(sketch, "E5695", {"start": v(4926.18, 3284.12) * mm, "end": v(4899.97, 3298.34) * mm});
            skLineSegment(sketch, "E5696", {"start": v(4899.97, 3298.34) * mm, "end": v(4873.35, 3311.96) * mm});
            skLineSegment(sketch, "E5697", {"start": v(5078.78, 3297.33) * mm, "end": v(5122.67, 3304.24) * mm});
            skLineSegment(sketch, "E5698", {"start": v(5122.67, 3304.24) * mm, "end": v(5017, 3154.88) * mm});
            skLineSegment(sketch, "E5699", {"start": v(5040.17, 3138.02) * mm, "end": v(5017, 3154.88) * mm});
            skLineSegment(sketch, "E5700", {"start": v(5017, 3154.88) * mm, "end": v(4993.64, 3171.14) * mm});
            skLineSegment(sketch, "E5701", {"start": v(5142.79, 3174.4) * mm, "end": v(5166.36, 3155.09) * mm});
            skLineSegment(sketch, "E5702", {"start": v(5166.36, 3155.09) * mm, "end": v(5189.32, 3135.17) * mm});
            skLineSegment(sketch, "E5703", {"start": v(5189.32, 3135.17) * mm, "end": v(5212.08, 3114.85) * mm});
            skLineSegment(sketch, "E5704", {"start": v(5212.08, 3114.85) * mm, "end": v(5213.3, 3071.98) * mm});
            skLineSegment(sketch, "E5705", {"start": v(5213.3, 3071.98) * mm, "end": v(5192.17, 3049.83) * mm});
            skLineSegment(sketch, "E5706", {"start": v(5192.17, 3049.83) * mm, "end": v(5150.3, 3047.4) * mm});
            skLineSegment(sketch, "E5707", {"start": v(5150.3, 3047.4) * mm, "end": v(5128.97, 3066.5) * mm});
            skLineSegment(sketch, "E5708", {"start": v(5128.97, 3066.5) * mm, "end": v(5107.43, 3085.19) * mm});
            skLineSegment(sketch, "E5709", {"start": v(5107.43, 3085.19) * mm, "end": v(5104.59, 3127.04) * mm});
            skLineSegment(sketch, "E5710", {"start": v(5104.59, 3127.04) * mm, "end": v(5161.9, 3198.16) * mm});
            skLineSegment(sketch, "E5711", {"start": v(5161.9, 3198.16) * mm, "end": v(5205.58, 3201.62) * mm});
            skLineSegment(sketch, "E5712", {"start": v(5205.58, 3201.62) * mm, "end": v(5249.88, 3203.85) * mm});
            skLineSegment(sketch, "E5713", {"start": v(5249.88, 3203.85) * mm, "end": v(5273.85, 3182.11) * mm});
            skLineSegment(sketch, "E5714", {"start": v(5376.88, 2935.43) * mm, "end": v(5395.37, 2911.25) * mm});
            skLineSegment(sketch, "E5715", {"start": v(5395.37, 2911.25) * mm, "end": v(5413.25, 2886.46) * mm});
            skLineSegment(sketch, "E5716", {"start": v(5413.25, 2886.46) * mm, "end": v(5430.52, 2861.46) * mm});
            skLineSegment(sketch, "E5717", {"start": v(5430.52, 2861.46) * mm, "end": v(5472.99, 2852.52) * mm});
            skLineSegment(sketch, "E5718", {"start": v(5472.99, 2852.52) * mm, "end": v(5498.6, 2868.98) * mm});
            skLineSegment(sketch, "E5719", {"start": v(5498.6, 2868.98) * mm, "end": v(5506.31, 2912.67) * mm});
            skLineSegment(sketch, "E5720", {"start": v(5506.31, 2912.67) * mm, "end": v(5487.82, 2939.29) * mm});
            skLineSegment(sketch, "E5721", {"start": v(5487.82, 2939.29) * mm, "end": v(5468.72, 2965.5) * mm});
            skLineSegment(sketch, "E5722", {"start": v(5468.72, 2965.5) * mm, "end": v(5449.21, 2991.51) * mm});
            skLineSegment(sketch, "E5723", {"start": v(5449.21, 2991.51) * mm, "end": v(5304.54, 2879.55) * mm});
            skLineSegment(sketch, "E5724", {"start": v(5400.45, 2737.71) * mm, "end": v(5505.5, 2799.49) * mm});
            skLineSegment(sketch, "E5725", {"start": v(5531.92, 2814.93) * mm, "end": v(5558.13, 2830.37) * mm});
            skLineSegment(sketch, "E5726", {"start": v(5505.5, 2596.9) * mm, "end": v(5466.08, 2611.12) * mm});
            skLineSegment(sketch, "E5727", {"start": v(5466.08, 2611.12) * mm, "end": v(5481.52, 2650.13) * mm});
            skLineSegment(sketch, "E5728", {"start": v(5481.52, 2650.13) * mm, "end": v(5619.1, 2715.97) * mm});
            skLineSegment(sketch, "E5729", {"start": v(5589.63, 2632.86) * mm, "end": v(5577.23, 2661.31) * mm});
            skLineSegment(sketch, "E5730", {"start": v(5577.23, 2661.31) * mm, "end": v(5564.02, 2689.56) * mm});
            skLineSegment(sketch, "E5731", {"start": v(5564.02, 2689.56) * mm, "end": v(5550.2, 2717.6) * mm});
            skLineSegment(sketch, "E5732", {"start": v(5550.2, 2717.6) * mm, "end": v(5535.98, 2745.23) * mm});
            skLineSegment(sketch, "E5733", {"start": v(5534.56, 2423.77) * mm, "end": v(5526.43, 2451) * mm});
            skLineSegment(sketch, "E5734", {"start": v(5526.43, 2451) * mm, "end": v(5517.9, 2478.23) * mm});
            skLineSegment(sketch, "E5735", {"start": v(5517.9, 2478.23) * mm, "end": v(5508.55, 2505.25) * mm});
            skLineSegment(sketch, "E5736", {"start": v(5508.55, 2505.25) * mm, "end": v(5527.24, 2542.84) * mm});
            skLineSegment(sketch, "E5737", {"start": v(5527.24, 2542.84) * mm, "end": v(5584.34, 2564.38) * mm});
            skLineSegment(sketch, "E5738", {"start": v(5584.34, 2564.38) * mm, "end": v(5623.56, 2545.9) * mm});
            skLineSegment(sketch, "E5739", {"start": v(5623.56, 2545.9) * mm, "end": v(5633.72, 2516.43) * mm});
            skLineSegment(sketch, "E5740", {"start": v(5633.72, 2516.43) * mm, "end": v(5643.07, 2486.76) * mm});
            skLineSegment(sketch, "E5741", {"start": v(5643.07, 2486.76) * mm, "end": v(5651.8, 2456.9) * mm});
            skLineSegment(sketch, "E5742", {"start": v(5608.32, 2382.52) * mm, "end": v(5644.7, 2359.96) * mm});
            skLineSegment(sketch, "E5743", {"start": v(5644.7, 2359.96) * mm, "end": v(5680.66, 2335.78) * mm});
            skLineSegment(sketch, "E5744", {"start": v(5680.66, 2335.78) * mm, "end": v(5686.35, 2305.3) * mm});
            skLineSegment(sketch, "E5745", {"start": v(5686.35, 2305.3) * mm, "end": v(5661.15, 2269.95) * mm});
            skLineSegment(sketch, "E5746", {"start": v(5661.15, 2269.95) * mm, "end": v(5570.73, 2256.33) * mm});
            skLineSegment(sketch, "E5747", {"start": v(5548.99, 2368.5) * mm, "end": v(5726.79, 2410.76) * mm});
            skLineSegment(sketch, "E5748", {"start": v(5585.36, 2057.4) * mm, "end": v(5585.16, 2028.95) * mm});
            skLineSegment(sketch, "E5749", {"start": v(5585.16, 2028.95) * mm, "end": v(5584.34, 2000.3) * mm});
            skLineSegment(sketch, "E5750", {"start": v(5584.34, 2000.3) * mm, "end": v(5582.72, 1971.85) * mm});
            skLineSegment(sketch, "E5751", {"start": v(5582.72, 1971.85) * mm, "end": v(5610.96, 1940.76) * mm});
            skLineSegment(sketch, "E5752", {"start": v(5610.96, 1940.76) * mm, "end": v(5732.48, 1930.4) * mm});
            skLineSegment(sketch, "E5753", {"start": v(5732.48, 1930.4) * mm, "end": v(5765.2, 1960.27) * mm});
            skLineSegment(sketch, "E5754", {"start": v(5765.2, 1960.27) * mm, "end": v(5767.02, 1992.58) * mm});
            skLineSegment(sketch, "E5755", {"start": v(5767.02, 1992.58) * mm, "end": v(5768.04, 2024.89) * mm});
            skLineSegment(sketch, "E5756", {"start": v(5768.04, 2024.89) * mm, "end": v(5768.44, 2057.4) * mm});
            skLineSegment(sketch, "E5757", {"start": v(5768.04, 2024.89) * mm, "end": v(5585.16, 2028.95) * mm});
            skLineSegment(sketch, "E5758", {"start": v(5674.36, 1748.54) * mm, "end": v(5680.66, 1779.02) * mm});
            skLineSegment(sketch, "E5759", {"start": v(5680.66, 1779.02) * mm, "end": v(5686.35, 1809.5) * mm});
            skLineSegment(sketch, "E5760", {"start": v(5686.35, 1809.5) * mm, "end": v(5691.23, 1840.38) * mm});
            skLineSegment(sketch, "E5761", {"start": v(5691.23, 1840.38) * mm, "end": v(5695.5, 1871.07) * mm});
            skLineSegment(sketch, "E5762", {"start": v(5614.82, 1761.34) * mm, "end": v(5620.92, 1790.6) * mm});
            skLineSegment(sketch, "E5763", {"start": v(5620.92, 1790.6) * mm, "end": v(5626.2, 1819.86) * mm});
            skLineSegment(sketch, "E5764", {"start": v(5626.2, 1819.86) * mm, "end": v(5630.88, 1849.32) * mm});
            skLineSegment(sketch, "E5765", {"start": v(5630.88, 1849.32) * mm, "end": v(5634.94, 1878.79) * mm});
            skLineSegment(sketch, "E5766", {"start": v(5566.05, 1589.23) * mm, "end": v(5575.8, 1617.47) * mm});
            skLineSegment(sketch, "E5767", {"start": v(5575.8, 1617.47) * mm, "end": v(5584.75, 1645.92) * mm});
            skLineSegment(sketch, "E5768", {"start": v(5584.75, 1645.92) * mm, "end": v(5593.28, 1674.57) * mm});
            skLineSegment(sketch, "E5769", {"start": v(5593.28, 1674.57) * mm, "end": v(5601, 1703.22) * mm});
            skLineSegment(sketch, "E5770", {"start": v(5601, 1703.22) * mm, "end": v(5632.3, 1663.4) * mm});
            skLineSegment(sketch, "E5771", {"start": v(5632.3, 1663.4) * mm, "end": v(5662.57, 1622.15) * mm});
            skLineSegment(sketch, "E5772", {"start": v(5662.57, 1622.15) * mm, "end": v(5691.43, 1579.27) * mm});
            skLineSegment(sketch, "E5773", {"start": v(5691.43, 1579.27) * mm, "end": v(5517.9, 1636.57) * mm});
            skLineSegment(sketch, "E5774", {"start": v(5508.96, 1384) * mm, "end": v(5494.53, 1357.17) * mm});
            skLineSegment(sketch, "E5775", {"start": v(5494.53, 1357.17) * mm, "end": v(5479.29, 1330.76) * mm});
            skLineSegment(sketch, "E5776", {"start": v(5479.29, 1330.76) * mm, "end": v(5463.64, 1304.54) * mm});
            skLineSegment(sketch, "E5777", {"start": v(5463.64, 1304.54) * mm, "end": v(5472.99, 1262.28) * mm});
            skLineSegment(sketch, "E5778", {"start": v(5472.99, 1262.28) * mm, "end": v(5498.6, 1245.82) * mm});
            skLineSegment(sketch, "E5779", {"start": v(5498.6, 1245.82) * mm, "end": v(5541.47, 1256.59) * mm});
            skLineSegment(sketch, "E5780", {"start": v(5541.47, 1256.59) * mm, "end": v(5558.13, 1284.43) * mm});
            skLineSegment(sketch, "E5781", {"start": v(5558.13, 1284.43) * mm, "end": v(5574.18, 1312.47) * mm});
            skLineSegment(sketch, "E5782", {"start": v(5574.18, 1312.47) * mm, "end": v(5589.83, 1340.92) * mm});
            skLineSegment(sketch, "E5783", {"start": v(5589.83, 1340.92) * mm, "end": v(5428.29, 1426.87) * mm});
            skLineSegment(sketch, "E5784", {"start": v(5361.84, 1112.32) * mm, "end": v(5381.75, 1136.3) * mm});
            skLineSegment(sketch, "E5785", {"start": v(5381.75, 1136.3) * mm, "end": v(5401.06, 1160.68) * mm});
            skLineSegment(sketch, "E5786", {"start": v(5401.06, 1160.68) * mm, "end": v(5419.75, 1185.47) * mm});
            skLineSegment(sketch, "E5787", {"start": v(5419.75, 1185.47) * mm, "end": v(5438.04, 1210.67) * mm});
            skLineSegment(sketch, "E5788", {"start": v(5315.3, 1151.53) * mm, "end": v(5334.4, 1174.5) * mm});
            skLineSegment(sketch, "E5789", {"start": v(5334.4, 1174.5) * mm, "end": v(5352.9, 1198.07) * mm});
            skLineSegment(sketch, "E5790", {"start": v(5352.9, 1198.07) * mm, "end": v(5370.78, 1221.84) * mm});
            skLineSegment(sketch, "E5791", {"start": v(5370.78, 1221.84) * mm, "end": v(5388.25, 1246.02) * mm});
            skLineSegment(sketch, "E5792", {"start": v(5191.56, 1022.5) * mm, "end": v(5213.3, 1042.82) * mm});
            skLineSegment(sketch, "E5793", {"start": v(5213.3, 1042.82) * mm, "end": v(5234.64, 1063.75) * mm});
            skLineSegment(sketch, "E5794", {"start": v(5234.64, 1063.75) * mm, "end": v(5255.36, 1085.09) * mm});
            skLineSegment(sketch, "E5795", {"start": v(5255.36, 1085.09) * mm, "end": v(5275.89, 1106.83) * mm});
            skLineSegment(sketch, "E5796", {"start": v(5275.89, 1106.83) * mm, "end": v(5284.83, 1056.84) * mm});
            skLineSegment(sketch, "E5797", {"start": v(5284.83, 1056.84) * mm, "end": v(5291.94, 1006.25) * mm});
            skLineSegment(sketch, "E5798", {"start": v(5291.94, 1006.25) * mm, "end": v(5297.63, 954.84) * mm});
            skLineSegment(sketch, "E5799", {"start": v(5297.63, 954.84) * mm, "end": v(5171.03, 1086.92) * mm});
            skLineSegment(sketch, "E5800", {"start": v(5044.85, 867.87) * mm, "end": v(5019.24, 851.2) * mm});
            skLineSegment(sketch, "E5801", {"start": v(5019.24, 851.2) * mm, "end": v(4993.44, 834.95) * mm});
            skLineSegment(sketch, "E5802", {"start": v(4993.44, 834.95) * mm, "end": v(4967.43, 819.3) * mm});
            skLineSegment(sketch, "E5803", {"start": v(4967.43, 819.3) * mm, "end": v(4955.85, 777.44) * mm});
            skLineSegment(sketch, "E5804", {"start": v(4955.85, 777.44) * mm, "end": v(4970.68, 750.82) * mm});
            skLineSegment(sketch, "E5805", {"start": v(4970.68, 750.82) * mm, "end": v(5013.55, 740.26) * mm});
            skLineSegment(sketch, "E5806", {"start": v(5013.55, 740.26) * mm, "end": v(5041.4, 757.12) * mm});
            skLineSegment(sketch, "E5807", {"start": v(5041.4, 757.12) * mm, "end": v(5068.82, 774.4) * mm});
            skLineSegment(sketch, "E5808", {"start": v(5068.82, 774.4) * mm, "end": v(5095.85, 792.28) * mm});
            skLineSegment(sketch, "E5809", {"start": v(5095.85, 792.28) * mm, "end": v(4993.64, 943.66) * mm});
            skLineSegment(sketch, "E5810", {"start": v(4845.91, 857.3) * mm, "end": v(4873.35, 802.84) * mm});
            skLineSegment(sketch, "E5811", {"start": v(4873.35, 802.84) * mm, "end": v(4872.94, 734.57) * mm});
            skLineSegment(sketch, "E5812", {"start": v(4872.94, 734.57) * mm, "end": v(4869.69, 665.89) * mm});
            skLineSegment(sketch, "E5813", {"start": v(4869.69, 665.89) * mm, "end": v(4816.04, 708.96) * mm});
            skLineSegment(sketch, "E5814", {"start": v(4816.04, 708.96) * mm, "end": v(4764.63, 753.67) * mm});
            skLineSegment(sketch, "E5815", {"start": v(4764.63, 753.67) * mm, "end": v(4741.88, 810.36) * mm});
            skLineSegment(sketch, "E5816", {"start": v(4873.35, 802.84) * mm, "end": v(4846.52, 789.64) * mm});
            skLineSegment(sketch, "E5817", {"start": v(4846.52, 789.64) * mm, "end": v(4819.5, 777.04) * mm});
            skLineSegment(sketch, "E5818", {"start": v(4819.5, 777.04) * mm, "end": v(4792.27, 765.05) * mm});
            skLineSegment(sketch, "E5819", {"start": v(4792.27, 765.05) * mm, "end": v(4764.63, 753.67) * mm});
            skLineSegment(sketch, "E5820", {"start": v(4610, 638.86) * mm, "end": v(4640.07, 646.99) * mm});
            skLineSegment(sketch, "E5821", {"start": v(4640.07, 646.99) * mm, "end": v(4669.94, 655.73) * mm});
            skLineSegment(sketch, "E5822", {"start": v(4669.94, 655.73) * mm, "end": v(4699.61, 665.07) * mm});
            skLineSegment(sketch, "E5823", {"start": v(4699.61, 665.07) * mm, "end": v(4729.07, 675.23) * mm});
            skLineSegment(sketch, "E5824", {"start": v(4594.76, 697.79) * mm, "end": v(4623.61, 705.71) * mm});
            skLineSegment(sketch, "E5825", {"start": v(4623.61, 705.71) * mm, "end": v(4652.06, 714.04) * mm});
            skLineSegment(sketch, "E5826", {"start": v(4652.06, 714.04) * mm, "end": v(4680.5, 722.99) * mm});
            skLineSegment(sketch, "E5827", {"start": v(4680.5, 722.99) * mm, "end": v(4708.75, 732.74) * mm});
            skLineSegment(sketch, "E5828", {"start": v(4411.47, 724.4) * mm, "end": v(4439.72, 728.47) * mm});
            skLineSegment(sketch, "E5829", {"start": v(4439.72, 728.47) * mm, "end": v(4467.76, 732.94) * mm});
            skLineSegment(sketch, "E5830", {"start": v(4467.76, 732.94) * mm, "end": v(4496, 738.02) * mm});
            skLineSegment(sketch, "E5831", {"start": v(4496, 738.02) * mm, "end": v(4523.84, 743.71) * mm});
            skLineSegment(sketch, "E5832", {"start": v(4523.84, 743.71) * mm, "end": v(4536.64, 684.17) * mm});
            skLineSegment(sketch, "E5833", {"start": v(4536.64, 684.17) * mm, "end": v(4513.28, 648.2) * mm});
            skLineSegment(sketch, "E5834", {"start": v(4513.28, 648.2) * mm, "end": v(4483.2, 642.72) * mm});
            skLineSegment(sketch, "E5835", {"start": v(4483.2, 642.72) * mm, "end": v(4453.13, 637.84) * mm});
            skLineSegment(sketch, "E5836", {"start": v(4453.13, 637.84) * mm, "end": v(4426.71, 603.5) * mm});
            skLineSegment(sketch, "E5837", {"start": v(4426.71, 603.5) * mm, "end": v(4430.57, 573.23) * mm});
            skLineSegment(sketch, "E5838", {"start": v(4430.57, 573.23) * mm, "end": v(4466.54, 547.42) * mm});
            skLineSegment(sketch, "E5839", {"start": v(4466.54, 547.42) * mm, "end": v(4498.65, 552.7) * mm});
            skLineSegment(sketch, "E5840", {"start": v(4498.65, 552.7) * mm, "end": v(4530.55, 558.4) * mm});
            skLineSegment(sketch, "E5841", {"start": v(4530.55, 558.4) * mm, "end": v(4555.95, 594.77) * mm});
            skFitSpline(sketch, "E5842", {"points": [v(6273.8, 2057.4) * mm, v(6273.8, 935.16) * mm, v(5364.04, 25.4) * mm, v(4241.8, 25.4) * mm]});
            skFitSpline(sketch, "E5843", {"points": [v(4241.8, 25.4) * mm, v(3119.56, 25.4) * mm, v(2209.8, 935.16) * mm, v(2209.8, 2057.4) * mm]});
            skFitSpline(sketch, "E5844", {"points": [v(2209.8, 2057.4) * mm, v(2209.8, 3179.64) * mm, v(3119.56, 4089.4) * mm, v(4241.8, 4089.4) * mm]});
            skFitSpline(sketch, "E5845", {"points": [v(4241.8, 4089.4) * mm, v(5364.04, 4089.4) * mm, v(6273.8, 3179.64) * mm, v(6273.8, 2057.4) * mm]});
            skLineSegment(sketch, "E5846", {"start": v(4240.58, 713.84) * mm, "end": v(4269.23, 714.04) * mm});
            skLineSegment(sketch, "E5847", {"start": v(4269.23, 714.04) * mm, "end": v(4297.68, 714.86) * mm});
            skLineSegment(sketch, "E5848", {"start": v(4297.68, 714.86) * mm, "end": v(4326.13, 716.48) * mm});
            skLineSegment(sketch, "E5849", {"start": v(4326.13, 716.48) * mm, "end": v(4354.58, 718.52) * mm});
            skLineSegment(sketch, "E5850", {"start": v(4354.58, 718.52) * mm, "end": v(4359.66, 657.76) * mm});
            skLineSegment(sketch, "E5851", {"start": v(4359.66, 657.76) * mm, "end": v(4331.82, 625.04) * mm});
            skLineSegment(sketch, "E5852", {"start": v(4331.82, 625.04) * mm, "end": v(4301.54, 623.62) * mm});
            skLineSegment(sketch, "E5853", {"start": v(4301.54, 623.62) * mm, "end": v(4271.06, 622.6) * mm});
            skLineSegment(sketch, "E5854", {"start": v(4271.06, 622.6) * mm, "end": v(4240.58, 591.92) * mm});
            skLineSegment(sketch, "E5855", {"start": v(4240.58, 591.92) * mm, "end": v(4240.38, 561.44) * mm});
            skLineSegment(sketch, "E5856", {"start": v(4240.38, 561.44) * mm, "end": v(4272.9, 531.16) * mm});
            skLineSegment(sketch, "E5857", {"start": v(4272.9, 531.16) * mm, "end": v(4305.2, 532.18) * mm});
            skLineSegment(sketch, "E5858", {"start": v(4305.2, 532.18) * mm, "end": v(4337.71, 533.8) * mm});
            skLineSegment(sketch, "E5859", {"start": v(4337.71, 533.8) * mm, "end": v(4367.38, 566.72) * mm});
            skFitSpline(sketch, "E5860", {"points": [v(6527.8, 2057.4) * mm, v(6527.8, 794.88) * mm, v(5504.32, -228.6) * mm, v(4241.8, -228.6) * mm]});
            skFitSpline(sketch, "E5861", {"points": [v(4241.8, -228.6) * mm, v(2979.28, -228.6) * mm, v(1955.8, 794.88) * mm, v(1955.8, 2057.4) * mm]});
            skFitSpline(sketch, "E5862", {"points": [v(1955.8, 2057.4) * mm, v(1955.8, 3319.92) * mm, v(2979.28, 4343.4) * mm, v(4241.8, 4343.4) * mm]});
            skFitSpline(sketch, "E5863", {"points": [v(4241.8, 4343.4) * mm, v(5504.32, 4343.4) * mm, v(6527.8, 3319.92) * mm, v(6527.8, 2057.4) * mm]});
            skFitSpline(sketch, "E5864", {"points": [v(6125.87, 2057.4) * mm, v(6125.87, 1016.86) * mm, v(5282.34, 173.33) * mm, v(4241.8, 173.33) * mm]});
            skFitSpline(sketch, "E5865", {"points": [v(4241.8, 173.33) * mm, v(3201.26, 173.33) * mm, v(2357.73, 1016.86) * mm, v(2357.73, 2057.4) * mm]});
            skFitSpline(sketch, "E5866", {"points": [v(2357.73, 2057.4) * mm, v(2357.73, 3097.94) * mm, v(3201.26, 3941.47) * mm, v(4241.8, 3941.47) * mm]});
            skFitSpline(sketch, "E5867", {"points": [v(4241.8, 3941.47) * mm, v(5282.34, 3941.47) * mm, v(6125.87, 3097.94) * mm, v(6125.87, 2057.4) * mm]});
            skLineSegment(sketch, "E5868", {"start": v(10072.68, 2115.64) * mm, "end": v(10076.14, 2115.94) * mm});
            skLineSegment(sketch, "E5869", {"start": v(10076.14, 2115.94) * mm, "end": v(10080.7, 2116.45) * mm});
            skLineSegment(sketch, "E5870", {"start": v(10080.7, 2116.45) * mm, "end": v(10086.32, 2117.24) * mm});
            skLineSegment(sketch, "E5871", {"start": v(10086.32, 2117.24) * mm, "end": v(10093.02, 2118.35) * mm});
            skLineSegment(sketch, "E5872", {"start": v(10093.02, 2118.35) * mm, "end": v(10100.76, 2119.86) * mm});
            skLineSegment(sketch, "E5873", {"start": v(10100.76, 2119.86) * mm, "end": v(10109.54, 2121.82) * mm});
            skLineSegment(sketch, "E5874", {"start": v(10109.54, 2121.82) * mm, "end": v(10119.34, 2124.27) * mm});
            skLineSegment(sketch, "E5875", {"start": v(10119.34, 2124.27) * mm, "end": v(10130.13, 2127.3) * mm});
            skLineSegment(sketch, "E5876", {"start": v(10130.13, 2127.3) * mm, "end": v(10141.88, 2130.92) * mm});
            skLineSegment(sketch, "E5877", {"start": v(10141.88, 2130.92) * mm, "end": v(10154.58, 2135.22) * mm});
            skLineSegment(sketch, "E5878", {"start": v(10154.58, 2135.22) * mm, "end": v(10168.2, 2140.25) * mm});
            skLineSegment(sketch, "E5879", {"start": v(10168.2, 2140.25) * mm, "end": v(10182.7, 2146.04) * mm});
            skLineSegment(sketch, "E5880", {"start": v(10182.7, 2146.04) * mm, "end": v(10198.06, 2152.66) * mm});
            skLineSegment(sketch, "E5881", {"start": v(10198.06, 2152.66) * mm, "end": v(10214.23, 2160.15) * mm});
            skLineSegment(sketch, "E5882", {"start": v(10214.23, 2160.15) * mm, "end": v(10231.19, 2168.56) * mm});
            skLineSegment(sketch, "E5883", {"start": v(10231.19, 2168.56) * mm, "end": v(10248.88, 2177.94) * mm});
            skLineSegment(sketch, "E5884", {"start": v(10248.88, 2177.94) * mm, "end": v(10267.28, 2188.34) * mm});
            skLineSegment(sketch, "E5885", {"start": v(10267.28, 2188.34) * mm, "end": v(10286.34, 2199.8) * mm});
            skLineSegment(sketch, "E5886", {"start": v(10286.34, 2199.8) * mm, "end": v(10306.02, 2212.35) * mm});
            skLineSegment(sketch, "E5887", {"start": v(10306.02, 2212.35) * mm, "end": v(10326.27, 2226.05) * mm});
            skLineSegment(sketch, "E5888", {"start": v(10326.27, 2226.05) * mm, "end": v(10347.04, 2240.93) * mm});
            skLineSegment(sketch, "E5889", {"start": v(10347.04, 2240.93) * mm, "end": v(10368.28, 2257.03) * mm});
            skLineSegment(sketch, "E5890", {"start": v(10368.28, 2257.03) * mm, "end": v(10389.94, 2274.39) * mm});
            skLineSegment(sketch, "E5891", {"start": v(10389.94, 2274.39) * mm, "end": v(10411.97, 2293.03) * mm});
            skLineSegment(sketch, "E5892", {"start": v(10411.97, 2293.03) * mm, "end": v(10432.78, 2312.83) * mm});
            skLineSegment(sketch, "E5893", {"start": v(10432.78, 2312.83) * mm, "end": v(10413.92, 2447.23) * mm});
            skLineSegment(sketch, "E5894", {"start": v(10413.92, 2447.23) * mm, "end": v(10388.47, 2460.54) * mm});
            skLineSegment(sketch, "E5895", {"start": v(10388.47, 2460.54) * mm, "end": v(10362.15, 2472.4) * mm});
            skLineSegment(sketch, "E5896", {"start": v(10362.15, 2472.4) * mm, "end": v(10336.55, 2483.12) * mm});
            skLineSegment(sketch, "E5897", {"start": v(10336.55, 2483.12) * mm, "end": v(10311.7, 2492.75) * mm});
            skLineSegment(sketch, "E5898", {"start": v(10311.7, 2492.75) * mm, "end": v(10287.64, 2501.34) * mm});
            skLineSegment(sketch, "E5899", {"start": v(10287.64, 2501.34) * mm, "end": v(10264.4, 2508.94) * mm});
            skLineSegment(sketch, "E5900", {"start": v(10264.4, 2508.94) * mm, "end": v(10242.03, 2515.6) * mm});
            skLineSegment(sketch, "E5901", {"start": v(10242.03, 2515.6) * mm, "end": v(10220.55, 2521.36) * mm});
            skLineSegment(sketch, "E5902", {"start": v(10220.55, 2521.36) * mm, "end": v(10200, 2526.29) * mm});
            skLineSegment(sketch, "E5903", {"start": v(10200, 2526.29) * mm, "end": v(10180.4, 2530.44) * mm});
            skLineSegment(sketch, "E5904", {"start": v(10180.4, 2530.44) * mm, "end": v(10161.79, 2533.86) * mm});
            skLineSegment(sketch, "E5905", {"start": v(10161.79, 2533.86) * mm, "end": v(10144.18, 2536.61) * mm});
            skLineSegment(sketch, "E5906", {"start": v(10144.18, 2536.61) * mm, "end": v(10127.6, 2538.75) * mm});
            skLineSegment(sketch, "E5907", {"start": v(10127.6, 2538.75) * mm, "end": v(10112.06, 2540.33) * mm});
            skLineSegment(sketch, "E5908", {"start": v(10112.06, 2540.33) * mm, "end": v(10097.58, 2541.4) * mm});
            skLineSegment(sketch, "E5909", {"start": v(10097.58, 2541.4) * mm, "end": v(10084.19, 2542.04) * mm});
            skLineSegment(sketch, "E5910", {"start": v(10084.19, 2542.04) * mm, "end": v(10071.89, 2542.3) * mm});
            skLineSegment(sketch, "E5911", {"start": v(10071.89, 2542.3) * mm, "end": v(10060.69, 2542.23) * mm});
            skLineSegment(sketch, "E5912", {"start": v(10060.69, 2542.23) * mm, "end": v(10050.6, 2541.9) * mm});
            skLineSegment(sketch, "E5913", {"start": v(10050.6, 2541.9) * mm, "end": v(10041.61, 2541.36) * mm});
            skLineSegment(sketch, "E5914", {"start": v(10041.61, 2541.36) * mm, "end": v(10033.75, 2540.68) * mm});
            skLineSegment(sketch, "E5915", {"start": v(10033.75, 2540.68) * mm, "end": v(10027, 2539.9) * mm});
            skLineSegment(sketch, "E5916", {"start": v(10027, 2539.9) * mm, "end": v(10021.38, 2539.12) * mm});
            skLineSegment(sketch, "E5917", {"start": v(10021.38, 2539.12) * mm, "end": v(10016.86, 2538.35) * mm});
            skLineSegment(sketch, "E5918", {"start": v(10016.86, 2538.35) * mm, "end": v(10013.45, 2537.69) * mm});
            skLineSegment(sketch, "E5919", {"start": v(10013.45, 2537.69) * mm, "end": v(10011.14, 2537.17) * mm});
            skLineSegment(sketch, "E5920", {"start": v(10011.14, 2537.17) * mm, "end": v(10009.9, 2536.86) * mm});
            skLineSegment(sketch, "E5921", {"start": v(10009.9, 2536.86) * mm, "end": v(9844.44, 2489.49) * mm});
            skLineSegment(sketch, "E5922", {"start": v(9844.44, 2489.49) * mm, "end": v(9741.28, 2746.97) * mm});
            skLineSegment(sketch, "E5923", {"start": v(9741.28, 2746.97) * mm, "end": v(9893.67, 2826.96) * mm});
            skLineSegment(sketch, "E5924", {"start": v(9893.67, 2826.96) * mm, "end": v(9894.78, 2827.58) * mm});
            skLineSegment(sketch, "E5925", {"start": v(9894.78, 2827.58) * mm, "end": v(9896.8, 2828.8) * mm});
            skLineSegment(sketch, "E5926", {"start": v(9896.8, 2828.8) * mm, "end": v(9899.74, 2830.68) * mm});
            skLineSegment(sketch, "E5927", {"start": v(9899.74, 2830.68) * mm, "end": v(9903.53, 2833.25) * mm});
            skLineSegment(sketch, "E5928", {"start": v(9903.53, 2833.25) * mm, "end": v(9908.15, 2836.56) * mm});
            skLineSegment(sketch, "E5929", {"start": v(9908.15, 2836.56) * mm, "end": v(9913.56, 2840.66) * mm});
            skLineSegment(sketch, "E5930", {"start": v(9913.56, 2840.66) * mm, "end": v(9919.72, 2845.6) * mm});
            skLineSegment(sketch, "E5931", {"start": v(9919.72, 2845.6) * mm, "end": v(9926.58, 2851.4) * mm});
            skLineSegment(sketch, "E5932", {"start": v(9926.58, 2851.4) * mm, "end": v(9934.1, 2858.14) * mm});
            skLineSegment(sketch, "E5933", {"start": v(9934.1, 2858.14) * mm, "end": v(9942.26, 2865.82) * mm});
            skLineSegment(sketch, "E5934", {"start": v(9942.26, 2865.82) * mm, "end": v(9950.98, 2874.5) * mm});
            skLineSegment(sketch, "E5935", {"start": v(9950.98, 2874.5) * mm, "end": v(9960.23, 2884.21) * mm});
            skLineSegment(sketch, "E5936", {"start": v(9960.23, 2884.21) * mm, "end": v(9969.95, 2894.99) * mm});
            skLineSegment(sketch, "E5937", {"start": v(9969.95, 2894.99) * mm, "end": v(9980.1, 2906.85) * mm});
            skLineSegment(sketch, "E5938", {"start": v(9980.1, 2906.85) * mm, "end": v(9990.62, 2919.85) * mm});
            skLineSegment(sketch, "E5939", {"start": v(9990.62, 2919.85) * mm, "end": v(10001.46, 2934) * mm});
            skLineSegment(sketch, "E5940", {"start": v(10001.46, 2934) * mm, "end": v(10012.57, 2949.33) * mm});
            skLineSegment(sketch, "E5941", {"start": v(10012.57, 2949.33) * mm, "end": v(10023.88, 2965.86) * mm});
            skLineSegment(sketch, "E5942", {"start": v(10023.88, 2965.86) * mm, "end": v(10035.34, 2983.62) * mm});
            skLineSegment(sketch, "E5943", {"start": v(10035.34, 2983.62) * mm, "end": v(10046.9, 3002.62) * mm});
            skLineSegment(sketch, "E5944", {"start": v(10046.9, 3002.62) * mm, "end": v(10058.48, 3022.88) * mm});
            skLineSegment(sketch, "E5945", {"start": v(10058.48, 3022.88) * mm, "end": v(10070.04, 3044.42) * mm});
            skLineSegment(sketch, "E5946", {"start": v(10070.04, 3044.42) * mm, "end": v(10081.51, 3067.25) * mm});
            skLineSegment(sketch, "E5947", {"start": v(10081.51, 3067.25) * mm, "end": v(10092.84, 3091.38) * mm});
            skLineSegment(sketch, "E5948", {"start": v(10092.84, 3091.38) * mm, "end": v(10103.96, 3116.8) * mm});
            skLineSegment(sketch, "E5949", {"start": v(10103.96, 3116.8) * mm, "end": v(10114.8, 3143.55) * mm});
            skLineSegment(sketch, "E5950", {"start": v(10114.8, 3143.55) * mm, "end": v(10124.02, 3170.75) * mm});
            skLineSegment(sketch, "E5951", {"start": v(10124.02, 3170.75) * mm, "end": v(10044.86, 3281) * mm});
            skLineSegment(sketch, "E5952", {"start": v(10044.86, 3281) * mm, "end": v(10016.14, 3280.95) * mm});
            skLineSegment(sketch, "E5953", {"start": v(10016.14, 3280.95) * mm, "end": v(9987.33, 3279.23) * mm});
            skLineSegment(sketch, "E5954", {"start": v(9987.33, 3279.23) * mm, "end": v(9959.68, 3276.82) * mm});
            skLineSegment(sketch, "E5955", {"start": v(9959.68, 3276.82) * mm, "end": v(9933.2, 3273.8) * mm});
            skLineSegment(sketch, "E5956", {"start": v(9933.2, 3273.8) * mm, "end": v(9907.9, 3270.22) * mm});
            skLineSegment(sketch, "E5957", {"start": v(9907.9, 3270.22) * mm, "end": v(9883.8, 3266.15) * mm});
            skLineSegment(sketch, "E5958", {"start": v(9883.8, 3266.15) * mm, "end": v(9860.9, 3261.65) * mm});
            skLineSegment(sketch, "E5959", {"start": v(9860.9, 3261.65) * mm, "end": v(9839.2, 3256.77) * mm});
            skLineSegment(sketch, "E5960", {"start": v(9839.2, 3256.77) * mm, "end": v(9818.7, 3251.59) * mm});
            skLineSegment(sketch, "E5961", {"start": v(9818.7, 3251.59) * mm, "end": v(9799.43, 3246.15) * mm});
            skLineSegment(sketch, "E5962", {"start": v(9799.43, 3246.15) * mm, "end": v(9781.35, 3240.53) * mm});
            skLineSegment(sketch, "E5963", {"start": v(9781.35, 3240.53) * mm, "end": v(9764.48, 3234.78) * mm});
            skLineSegment(sketch, "E5964", {"start": v(9764.48, 3234.78) * mm, "end": v(9748.8, 3228.97) * mm});
            skLineSegment(sketch, "E5965", {"start": v(9748.8, 3228.97) * mm, "end": v(9734.32, 3223.15) * mm});
            skLineSegment(sketch, "E5966", {"start": v(9734.32, 3223.15) * mm, "end": v(9721, 3217.38) * mm});
            skLineSegment(sketch, "E5967", {"start": v(9721, 3217.38) * mm, "end": v(9708.84, 3211.72) * mm});
            skLineSegment(sketch, "E5968", {"start": v(9708.84, 3211.72) * mm, "end": v(9697.83, 3206.22) * mm});
            skLineSegment(sketch, "E5969", {"start": v(9697.83, 3206.22) * mm, "end": v(9687.94, 3200.96) * mm});
            skLineSegment(sketch, "E5970", {"start": v(9687.94, 3200.96) * mm, "end": v(9679.16, 3195.98) * mm});
            skLineSegment(sketch, "E5971", {"start": v(9679.16, 3195.98) * mm, "end": v(9671.46, 3191.33) * mm});
            skLineSegment(sketch, "E5972", {"start": v(9671.46, 3191.33) * mm, "end": v(9664.82, 3187.07) * mm});
            skLineSegment(sketch, "E5973", {"start": v(9664.82, 3187.07) * mm, "end": v(9659.2, 3183.25) * mm});
            skLineSegment(sketch, "E5974", {"start": v(9659.2, 3183.25) * mm, "end": v(9654.59, 3179.94) * mm});
            skLineSegment(sketch, "E5975", {"start": v(9654.59, 3179.94) * mm, "end": v(9650.94, 3177.16) * mm});
            skLineSegment(sketch, "E5976", {"start": v(9650.94, 3177.16) * mm, "end": v(9648.23, 3174.99) * mm});
            skLineSegment(sketch, "E5977", {"start": v(9648.23, 3174.99) * mm, "end": v(9646.42, 3173.45) * mm});
            skLineSegment(sketch, "E5978", {"start": v(9646.42, 3173.45) * mm, "end": v(9645.47, 3172.6) * mm});
            skLineSegment(sketch, "E5979", {"start": v(9645.47, 3172.6) * mm, "end": v(9520.98, 3053.77) * mm});
            skLineSegment(sketch, "E5980", {"start": v(9520.98, 3053.77) * mm, "end": v(9309.97, 3233.8) * mm});
            skLineSegment(sketch, "E5981", {"start": v(9309.97, 3233.8) * mm, "end": v(9407.74, 3375.46) * mm});
            skLineSegment(sketch, "E5982", {"start": v(9407.74, 3375.46) * mm, "end": v(9408.43, 3376.53) * mm});
            skLineSegment(sketch, "E5983", {"start": v(9408.43, 3376.53) * mm, "end": v(9409.66, 3378.55) * mm});
            skLineSegment(sketch, "E5984", {"start": v(9409.66, 3378.55) * mm, "end": v(9411.38, 3381.57) * mm});
            skLineSegment(sketch, "E5985", {"start": v(9411.38, 3381.57) * mm, "end": v(9413.55, 3385.6) * mm});
            skLineSegment(sketch, "E5986", {"start": v(9413.55, 3385.6) * mm, "end": v(9416.1, 3390.69) * mm});
            skLineSegment(sketch, "E5987", {"start": v(9416.1, 3390.69) * mm, "end": v(9418.98, 3396.83) * mm});
            skLineSegment(sketch, "E5988", {"start": v(9418.98, 3396.83) * mm, "end": v(9422.14, 3404.06) * mm});
            skLineSegment(sketch, "E5989", {"start": v(9422.14, 3404.06) * mm, "end": v(9425.52, 3412.4) * mm});
            skLineSegment(sketch, "E5990", {"start": v(9425.52, 3412.4) * mm, "end": v(9429.06, 3421.86) * mm});
            skLineSegment(sketch, "E5991", {"start": v(9429.06, 3421.86) * mm, "end": v(9432.7, 3432.45) * mm});
            skLineSegment(sketch, "E5992", {"start": v(9432.7, 3432.45) * mm, "end": v(9436.4, 3444.2) * mm});
            skLineSegment(sketch, "E5993", {"start": v(9436.4, 3444.2) * mm, "end": v(9440.07, 3457.09) * mm});
            skLineSegment(sketch, "E5994", {"start": v(9440.07, 3457.09) * mm, "end": v(9443.67, 3471.14) * mm});
            skLineSegment(sketch, "E5995", {"start": v(9443.67, 3471.14) * mm, "end": v(9447.14, 3486.37) * mm});
            skLineSegment(sketch, "E5996", {"start": v(9447.14, 3486.37) * mm, "end": v(9450.42, 3502.77) * mm});
            skLineSegment(sketch, "E5997", {"start": v(9450.42, 3502.77) * mm, "end": v(9453.44, 3520.33) * mm});
            skLineSegment(sketch, "E5998", {"start": v(9453.44, 3520.33) * mm, "end": v(9456.15, 3539.06) * mm});
            skLineSegment(sketch, "E5999", {"start": v(9456.15, 3539.06) * mm, "end": v(9458.48, 3558.96) * mm});
            skLineSegment(sketch, "E6000", {"start": v(9458.48, 3558.96) * mm, "end": v(9460.38, 3580) * mm});
            skLineSegment(sketch, "E6001", {"start": v(9460.38, 3580) * mm, "end": v(9461.78, 3602.2) * mm});
            skLineSegment(sketch, "E6002", {"start": v(9461.78, 3602.2) * mm, "end": v(9462.62, 3625.53) * mm});
            skLineSegment(sketch, "E6003", {"start": v(9462.62, 3625.53) * mm, "end": v(9462.85, 3649.97) * mm});
            skLineSegment(sketch, "E6004", {"start": v(9462.85, 3649.97) * mm, "end": v(9462.4, 3675.52) * mm});
            skLineSegment(sketch, "E6005", {"start": v(9462.4, 3675.52) * mm, "end": v(9461.21, 3702.15) * mm});
            skLineSegment(sketch, "E6006", {"start": v(9461.21, 3702.15) * mm, "end": v(9459.24, 3729.83) * mm});
            skLineSegment(sketch, "E6007", {"start": v(9459.24, 3729.83) * mm, "end": v(9456.41, 3758.55) * mm});
            skLineSegment(sketch, "E6008", {"start": v(9456.41, 3758.55) * mm, "end": v(9451.93, 3786.92) * mm});
            skLineSegment(sketch, "E6009", {"start": v(9451.93, 3786.92) * mm, "end": v(9330.61, 3847.75) * mm});
            skLineSegment(sketch, "E6010", {"start": v(9330.61, 3847.75) * mm, "end": v(9305.2, 3834.37) * mm});
            skLineSegment(sketch, "E6011", {"start": v(9305.2, 3834.37) * mm, "end": v(9280.5, 3819.45) * mm});
            skLineSegment(sketch, "E6012", {"start": v(9280.5, 3819.45) * mm, "end": v(9257.13, 3804.47) * mm});
            skLineSegment(sketch, "E6013", {"start": v(9257.13, 3804.47) * mm, "end": v(9235.08, 3789.49) * mm});
            skLineSegment(sketch, "E6014", {"start": v(9235.08, 3789.49) * mm, "end": v(9214.35, 3774.56) * mm});
            skLineSegment(sketch, "E6015", {"start": v(9214.35, 3774.56) * mm, "end": v(9194.9, 3759.76) * mm});
            skLineSegment(sketch, "E6016", {"start": v(9194.9, 3759.76) * mm, "end": v(9176.7, 3745.12) * mm});
            skLineSegment(sketch, "E6017", {"start": v(9176.7, 3745.12) * mm, "end": v(9159.76, 3730.72) * mm});
            skLineSegment(sketch, "E6018", {"start": v(9159.76, 3730.72) * mm, "end": v(9144.03, 3716.61) * mm});
            skLineSegment(sketch, "E6019", {"start": v(9144.03, 3716.61) * mm, "end": v(9129.48, 3702.84) * mm});
            skLineSegment(sketch, "E6020", {"start": v(9129.48, 3702.84) * mm, "end": v(9116.09, 3689.46) * mm});
            skLineSegment(sketch, "E6021", {"start": v(9116.09, 3689.46) * mm, "end": v(9103.82, 3676.53) * mm});
            skLineSegment(sketch, "E6022", {"start": v(9103.82, 3676.53) * mm, "end": v(9092.64, 3664.1) * mm});
            skLineSegment(sketch, "E6023", {"start": v(9092.64, 3664.1) * mm, "end": v(9082.52, 3652.21) * mm});
            skLineSegment(sketch, "E6024", {"start": v(9082.52, 3652.21) * mm, "end": v(9073.4, 3640.91) * mm});
            skLineSegment(sketch, "E6025", {"start": v(9073.4, 3640.91) * mm, "end": v(9065.28, 3630.25) * mm});
            skLineSegment(sketch, "E6026", {"start": v(9065.28, 3630.25) * mm, "end": v(9058.08, 3620.27) * mm});
            skLineSegment(sketch, "E6027", {"start": v(9058.08, 3620.27) * mm, "end": v(9051.77, 3611.01) * mm});
            skLineSegment(sketch, "E6028", {"start": v(9051.77, 3611.01) * mm, "end": v(9046.3, 3602.52) * mm});
            skLineSegment(sketch, "E6029", {"start": v(9046.3, 3602.52) * mm, "end": v(9041.65, 3594.82) * mm});
            skLineSegment(sketch, "E6030", {"start": v(9041.65, 3594.82) * mm, "end": v(9037.75, 3587.97) * mm});
            skLineSegment(sketch, "E6031", {"start": v(9037.75, 3587.97) * mm, "end": v(9034.55, 3581.98) * mm});
            skLineSegment(sketch, "E6032", {"start": v(9034.55, 3581.98) * mm, "end": v(9032, 3576.9) * mm});
            skLineSegment(sketch, "E6033", {"start": v(9032, 3576.9) * mm, "end": v(9030.07, 3572.75) * mm});
            skLineSegment(sketch, "E6034", {"start": v(9030.07, 3572.75) * mm, "end": v(9028.68, 3569.56) * mm});
            skLineSegment(sketch, "E6035", {"start": v(9028.68, 3569.56) * mm, "end": v(9027.79, 3567.36) * mm});
            skLineSegment(sketch, "E6036", {"start": v(9027.79, 3567.36) * mm, "end": v(9027.34, 3566.17) * mm});
            skLineSegment(sketch, "E6037", {"start": v(9027.34, 3566.17) * mm, "end": v(8972.33, 3403.09) * mm});
            skLineSegment(sketch, "E6038", {"start": v(8972.33, 3403.09) * mm, "end": v(8701.83, 3464.45) * mm});
            skLineSegment(sketch, "E6039", {"start": v(8701.83, 3464.45) * mm, "end": v(8722.57, 3635.3) * mm});
            skLineSegment(sketch, "E6040", {"start": v(8722.57, 3635.3) * mm, "end": v(8722.68, 3636.57) * mm});
            skLineSegment(sketch, "E6041", {"start": v(8722.68, 3636.57) * mm, "end": v(8722.83, 3638.94) * mm});
            skLineSegment(sketch, "E6042", {"start": v(8722.83, 3638.94) * mm, "end": v(8722.95, 3642.42) * mm});
            skLineSegment(sketch, "E6043", {"start": v(8722.95, 3642.42) * mm, "end": v(8723, 3647) * mm});
            skLineSegment(sketch, "E6044", {"start": v(8723, 3647) * mm, "end": v(8722.89, 3652.68) * mm});
            skLineSegment(sketch, "E6045", {"start": v(8722.89, 3652.68) * mm, "end": v(8722.59, 3659.46) * mm});
            skLineSegment(sketch, "E6046", {"start": v(8722.59, 3659.46) * mm, "end": v(8722.02, 3667.33) * mm});
            skLineSegment(sketch, "E6047", {"start": v(8722.02, 3667.33) * mm, "end": v(8721.14, 3676.28) * mm});
            skLineSegment(sketch, "E6048", {"start": v(8721.14, 3676.28) * mm, "end": v(8719.88, 3686.3) * mm});
            skLineSegment(sketch, "E6049", {"start": v(8719.88, 3686.3) * mm, "end": v(8718.19, 3697.37) * mm});
            skLineSegment(sketch, "E6050", {"start": v(8718.19, 3697.37) * mm, "end": v(8716, 3709.48) * mm});
            skLineSegment(sketch, "E6051", {"start": v(8716, 3709.48) * mm, "end": v(8713.26, 3722.6) * mm});
            skLineSegment(sketch, "E6052", {"start": v(8713.26, 3722.6) * mm, "end": v(8709.92, 3736.73) * mm});
            skLineSegment(sketch, "E6053", {"start": v(8709.92, 3736.73) * mm, "end": v(8705.91, 3751.83) * mm});
            skLineSegment(sketch, "E6054", {"start": v(8705.91, 3751.83) * mm, "end": v(8701.2, 3767.87) * mm});
            skLineSegment(sketch, "E6055", {"start": v(8701.2, 3767.87) * mm, "end": v(8695.7, 3784.82) * mm});
            skLineSegment(sketch, "E6056", {"start": v(8695.7, 3784.82) * mm, "end": v(8689.4, 3802.67) * mm});
            skLineSegment(sketch, "E6057", {"start": v(8689.4, 3802.67) * mm, "end": v(8682.22, 3821.37) * mm});
            skLineSegment(sketch, "E6058", {"start": v(8682.22, 3821.37) * mm, "end": v(8674.11, 3840.89) * mm});
            skLineSegment(sketch, "E6059", {"start": v(8674.11, 3840.89) * mm, "end": v(8665.04, 3861.2) * mm});
            skLineSegment(sketch, "E6060", {"start": v(8665.04, 3861.2) * mm, "end": v(8654.95, 3882.24) * mm});
            skLineSegment(sketch, "E6061", {"start": v(8654.95, 3882.24) * mm, "end": v(8643.79, 3903.99) * mm});
            skLineSegment(sketch, "E6062", {"start": v(8643.79, 3903.99) * mm, "end": v(8631.52, 3926.4) * mm});
            skLineSegment(sketch, "E6063", {"start": v(8631.52, 3926.4) * mm, "end": v(8618.1, 3949.43) * mm});
            skLineSegment(sketch, "E6064", {"start": v(8618.1, 3949.43) * mm, "end": v(8603.48, 3973.02) * mm});
            skLineSegment(sketch, "E6065", {"start": v(8603.48, 3973.02) * mm, "end": v(8587.63, 3997.14) * mm});
            skLineSegment(sketch, "E6066", {"start": v(8587.63, 3997.14) * mm, "end": v(8570.48, 4020.18) * mm});
            skLineSegment(sketch, "E6067", {"start": v(8570.48, 4020.18) * mm, "end": v(8434.79, 4017.66) * mm});
            skLineSegment(sketch, "E6068", {"start": v(8434.79, 4017.66) * mm, "end": v(8418.5, 3994) * mm});
            skLineSegment(sketch, "E6069", {"start": v(8418.5, 3994) * mm, "end": v(8403.56, 3969.3) * mm});
            skLineSegment(sketch, "E6070", {"start": v(8403.56, 3969.3) * mm, "end": v(8389.83, 3945.18) * mm});
            skLineSegment(sketch, "E6071", {"start": v(8389.83, 3945.18) * mm, "end": v(8377.28, 3921.67) * mm});
            skLineSegment(sketch, "E6072", {"start": v(8377.28, 3921.67) * mm, "end": v(8365.85, 3898.82) * mm});
            skLineSegment(sketch, "E6073", {"start": v(8365.85, 3898.82) * mm, "end": v(8355.51, 3876.67) * mm});
            skLineSegment(sketch, "E6074", {"start": v(8355.51, 3876.67) * mm, "end": v(8346.2, 3855.26) * mm});
            skLineSegment(sketch, "E6075", {"start": v(8346.2, 3855.26) * mm, "end": v(8337.9, 3834.64) * mm});
            skLineSegment(sketch, "E6076", {"start": v(8337.9, 3834.64) * mm, "end": v(8330.52, 3814.83) * mm});
            skLineSegment(sketch, "E6077", {"start": v(8330.52, 3814.83) * mm, "end": v(8324.04, 3795.88) * mm});
            skLineSegment(sketch, "E6078", {"start": v(8324.04, 3795.88) * mm, "end": v(8318.4, 3777.8) * mm});
            skLineSegment(sketch, "E6079", {"start": v(8318.4, 3777.8) * mm, "end": v(8313.55, 3760.66) * mm});
            skLineSegment(sketch, "E6080", {"start": v(8313.55, 3760.66) * mm, "end": v(8309.43, 3744.45) * mm});
            skLineSegment(sketch, "E6081", {"start": v(8309.43, 3744.45) * mm, "end": v(8305.99, 3729.22) * mm});
            skLineSegment(sketch, "E6082", {"start": v(8305.99, 3729.22) * mm, "end": v(8303.17, 3714.98) * mm});
            skLineSegment(sketch, "E6083", {"start": v(8303.17, 3714.98) * mm, "end": v(8300.92, 3701.76) * mm});
            skLineSegment(sketch, "E6084", {"start": v(8300.92, 3701.76) * mm, "end": v(8299.19, 3689.58) * mm});
            skLineSegment(sketch, "E6085", {"start": v(8299.19, 3689.58) * mm, "end": v(8297.9, 3678.45) * mm});
            skLineSegment(sketch, "E6086", {"start": v(8297.9, 3678.45) * mm, "end": v(8297.02, 3668.4) * mm});
            skLineSegment(sketch, "E6087", {"start": v(8297.02, 3668.4) * mm, "end": v(8296.47, 3659.42) * mm});
            skLineSegment(sketch, "E6088", {"start": v(8296.47, 3659.42) * mm, "end": v(8296.2, 3651.53) * mm});
            skLineSegment(sketch, "E6089", {"start": v(8296.2, 3651.53) * mm, "end": v(8296.15, 3644.74) * mm});
            skLineSegment(sketch, "E6090", {"start": v(8296.15, 3644.74) * mm, "end": v(8296.26, 3639.06) * mm});
            skLineSegment(sketch, "E6091", {"start": v(8296.26, 3639.06) * mm, "end": v(8296.47, 3634.48) * mm});
            skLineSegment(sketch, "E6092", {"start": v(8296.47, 3634.48) * mm, "end": v(8296.72, 3631.02) * mm});
            skLineSegment(sketch, "E6093", {"start": v(8296.72, 3631.02) * mm, "end": v(8296.96, 3628.66) * mm});
            skLineSegment(sketch, "E6094", {"start": v(8296.96, 3628.66) * mm, "end": v(8297.11, 3627.4) * mm});
            skLineSegment(sketch, "E6095", {"start": v(8297.11, 3627.4) * mm, "end": v(8324.2, 3457.43) * mm});
            skLineSegment(sketch, "E6096", {"start": v(8324.2, 3457.43) * mm, "end": v(8056.16, 3386.05) * mm});
            skLineSegment(sketch, "E6097", {"start": v(8056.16, 3386.05) * mm, "end": v(7995.12, 3546.98) * mm});
            skLineSegment(sketch, "E6098", {"start": v(7995.12, 3546.98) * mm, "end": v(7994.63, 3548.15) * mm});
            skLineSegment(sketch, "E6099", {"start": v(7994.63, 3548.15) * mm, "end": v(7993.66, 3550.32) * mm});
            skLineSegment(sketch, "E6100", {"start": v(7993.66, 3550.32) * mm, "end": v(7992.16, 3553.45) * mm});
            skLineSegment(sketch, "E6101", {"start": v(7992.16, 3553.45) * mm, "end": v(7990.07, 3557.52) * mm});
            skLineSegment(sketch, "E6102", {"start": v(7990.07, 3557.52) * mm, "end": v(7987.33, 3562.5) * mm});
            skLineSegment(sketch, "E6103", {"start": v(7987.33, 3562.5) * mm, "end": v(7983.91, 3568.37) * mm});
            skLineSegment(sketch, "E6104", {"start": v(7983.91, 3568.37) * mm, "end": v(7979.76, 3575.08) * mm});
            skLineSegment(sketch, "E6105", {"start": v(7979.76, 3575.08) * mm, "end": v(7974.81, 3582.6) * mm});
            skLineSegment(sketch, "E6106", {"start": v(7974.81, 3582.6) * mm, "end": v(7969.04, 3590.88) * mm});
            skLineSegment(sketch, "E6107", {"start": v(7969.04, 3590.88) * mm, "end": v(7962.4, 3599.9) * mm});
            skLineSegment(sketch, "E6108", {"start": v(7962.4, 3599.9) * mm, "end": v(7954.83, 3609.6) * mm});
            skLineSegment(sketch, "E6109", {"start": v(7954.83, 3609.6) * mm, "end": v(7946.3, 3619.95) * mm});
            skLineSegment(sketch, "E6110", {"start": v(7946.3, 3619.95) * mm, "end": v(7936.78, 3630.9) * mm});
            skLineSegment(sketch, "E6111", {"start": v(7936.78, 3630.9) * mm, "end": v(7926.22, 3642.4) * mm});
            skLineSegment(sketch, "E6112", {"start": v(7926.22, 3642.4) * mm, "end": v(7914.6, 3654.42) * mm});
            skLineSegment(sketch, "E6113", {"start": v(7914.6, 3654.42) * mm, "end": v(7901.85, 3666.89) * mm});
            skLineSegment(sketch, "E6114", {"start": v(7901.85, 3666.89) * mm, "end": v(7887.97, 3679.76) * mm});
            skLineSegment(sketch, "E6115", {"start": v(7887.97, 3679.76) * mm, "end": v(7872.92, 3692.98) * mm});
            skLineSegment(sketch, "E6116", {"start": v(7872.92, 3692.98) * mm, "end": v(7856.68, 3706.5) * mm});
            skLineSegment(sketch, "E6117", {"start": v(7856.68, 3706.5) * mm, "end": v(7839.2, 3720.25) * mm});
            skLineSegment(sketch, "E6118", {"start": v(7839.2, 3720.25) * mm, "end": v(7820.49, 3734.2) * mm});
            skLineSegment(sketch, "E6119", {"start": v(7820.49, 3734.2) * mm, "end": v(7800.5, 3748.27) * mm});
            skLineSegment(sketch, "E6120", {"start": v(7800.5, 3748.27) * mm, "end": v(7779.22, 3762.42) * mm});
            skLineSegment(sketch, "E6121", {"start": v(7779.22, 3762.42) * mm, "end": v(7756.64, 3776.57) * mm});
            skLineSegment(sketch, "E6122", {"start": v(7756.64, 3776.57) * mm, "end": v(7732.73, 3790.67) * mm});
            skLineSegment(sketch, "E6123", {"start": v(7732.73, 3790.67) * mm, "end": v(7707.49, 3804.66) * mm});
            skLineSegment(sketch, "E6124", {"start": v(7707.49, 3804.66) * mm, "end": v(7681.6, 3817.09) * mm});
            skLineSegment(sketch, "E6125", {"start": v(7681.6, 3817.09) * mm, "end": v(7562.62, 3751.8) * mm});
            skLineSegment(sketch, "E6126", {"start": v(7562.62, 3751.8) * mm, "end": v(7559.2, 3723.28) * mm});
            skLineSegment(sketch, "E6127", {"start": v(7559.2, 3723.28) * mm, "end": v(7557.44, 3694.47) * mm});
            skLineSegment(sketch, "E6128", {"start": v(7557.44, 3694.47) * mm, "end": v(7556.5, 3666.73) * mm});
            skLineSegment(sketch, "E6129", {"start": v(7556.5, 3666.73) * mm, "end": v(7556.3, 3640.08) * mm});
            skLineSegment(sketch, "E6130", {"start": v(7556.3, 3640.08) * mm, "end": v(7556.8, 3614.53) * mm});
            skLineSegment(sketch, "E6131", {"start": v(7556.8, 3614.53) * mm, "end": v(7557.94, 3590.11) * mm});
            skLineSegment(sketch, "E6132", {"start": v(7557.94, 3590.11) * mm, "end": v(7559.65, 3566.84) * mm});
            skLineSegment(sketch, "E6133", {"start": v(7559.65, 3566.84) * mm, "end": v(7561.87, 3544.7) * mm});
            skLineSegment(sketch, "E6134", {"start": v(7561.87, 3544.7) * mm, "end": v(7564.55, 3523.74) * mm});
            skLineSegment(sketch, "E6135", {"start": v(7564.55, 3523.74) * mm, "end": v(7567.62, 3503.95) * mm});
            skLineSegment(sketch, "E6136", {"start": v(7567.62, 3503.95) * mm, "end": v(7571.02, 3485.33) * mm});
            skLineSegment(sketch, "E6137", {"start": v(7571.02, 3485.33) * mm, "end": v(7574.7, 3467.89) * mm});
            skLineSegment(sketch, "E6138", {"start": v(7574.7, 3467.89) * mm, "end": v(7578.58, 3451.63) * mm});
            skLineSegment(sketch, "E6139", {"start": v(7578.58, 3451.63) * mm, "end": v(7582.61, 3436.54) * mm});
            skLineSegment(sketch, "E6140", {"start": v(7582.61, 3436.54) * mm, "end": v(7586.74, 3422.62) * mm});
            skLineSegment(sketch, "E6141", {"start": v(7586.74, 3422.62) * mm, "end": v(7590.89, 3409.87) * mm});
            skLineSegment(sketch, "E6142", {"start": v(7590.89, 3409.87) * mm, "end": v(7595.01, 3398.28) * mm});
            skLineSegment(sketch, "E6143", {"start": v(7595.01, 3398.28) * mm, "end": v(7599.05, 3387.83) * mm});
            skLineSegment(sketch, "E6144", {"start": v(7599.05, 3387.83) * mm, "end": v(7602.94, 3378.51) * mm});
            skLineSegment(sketch, "E6145", {"start": v(7602.94, 3378.51) * mm, "end": v(7606.62, 3370.3) * mm});
            skLineSegment(sketch, "E6146", {"start": v(7606.62, 3370.3) * mm, "end": v(7610.05, 3363.2) * mm});
            skLineSegment(sketch, "E6147", {"start": v(7610.05, 3363.2) * mm, "end": v(7613.16, 3357.16) * mm});
            skLineSegment(sketch, "E6148", {"start": v(7613.16, 3357.16) * mm, "end": v(7615.9, 3352.18) * mm});
            skLineSegment(sketch, "E6149", {"start": v(7615.9, 3352.18) * mm, "end": v(7618.2, 3348.23) * mm});
            skLineSegment(sketch, "E6150", {"start": v(7618.2, 3348.23) * mm, "end": v(7620.04, 3345.28) * mm});
            skLineSegment(sketch, "E6151", {"start": v(7620.04, 3345.28) * mm, "end": v(7621.35, 3343.3) * mm});
            skLineSegment(sketch, "E6152", {"start": v(7621.35, 3343.3) * mm, "end": v(7622.08, 3342.25) * mm});
            skLineSegment(sketch, "E6153", {"start": v(7622.08, 3342.25) * mm, "end": v(7725.04, 3204.34) * mm});
            skLineSegment(sketch, "E6154", {"start": v(7725.04, 3204.34) * mm, "end": v(7520.88, 3016.57) * mm});
            skLineSegment(sketch, "E6155", {"start": v(7520.88, 3016.57) * mm, "end": v(7392.05, 3130.7) * mm});
            skLineSegment(sketch, "E6156", {"start": v(7392.05, 3130.7) * mm, "end": v(7391.07, 3131.51) * mm});
            skLineSegment(sketch, "E6157", {"start": v(7391.07, 3131.51) * mm, "end": v(7389.2, 3132.98) * mm});
            skLineSegment(sketch, "E6158", {"start": v(7389.2, 3132.98) * mm, "end": v(7386.41, 3135.06) * mm});
            skLineSegment(sketch, "E6159", {"start": v(7386.41, 3135.06) * mm, "end": v(7382.67, 3137.7) * mm});
            skLineSegment(sketch, "E6160", {"start": v(7382.67, 3137.7) * mm, "end": v(7377.93, 3140.84) * mm});
            skLineSegment(sketch, "E6161", {"start": v(7377.93, 3140.84) * mm, "end": v(7372.18, 3144.44) * mm});
            skLineSegment(sketch, "E6162", {"start": v(7372.18, 3144.44) * mm, "end": v(7365.38, 3148.45) * mm});
            skLineSegment(sketch, "E6163", {"start": v(7365.38, 3148.45) * mm, "end": v(7357.52, 3152.8) * mm});
            skLineSegment(sketch, "E6164", {"start": v(7357.52, 3152.8) * mm, "end": v(7348.55, 3157.46) * mm});
            skLineSegment(sketch, "E6165", {"start": v(7348.55, 3157.46) * mm, "end": v(7338.48, 3162.35) * mm});
            skLineSegment(sketch, "E6166", {"start": v(7338.48, 3162.35) * mm, "end": v(7327.27, 3167.43) * mm});
            skLineSegment(sketch, "E6167", {"start": v(7327.27, 3167.43) * mm, "end": v(7314.91, 3172.64) * mm});
            skLineSegment(sketch, "E6168", {"start": v(7314.91, 3172.64) * mm, "end": v(7301.39, 3177.9) * mm});
            skLineSegment(sketch, "E6169", {"start": v(7301.39, 3177.9) * mm, "end": v(7286.7, 3183.19) * mm});
            skLineSegment(sketch, "E6170", {"start": v(7286.7, 3183.19) * mm, "end": v(7270.81, 3188.42) * mm});
            skLineSegment(sketch, "E6171", {"start": v(7270.81, 3188.42) * mm, "end": v(7253.74, 3193.53) * mm});
            skLineSegment(sketch, "E6172", {"start": v(7253.74, 3193.53) * mm, "end": v(7235.47, 3198.48) * mm});
            skLineSegment(sketch, "E6173", {"start": v(7235.47, 3198.48) * mm, "end": v(7216, 3203.2) * mm});
            skLineSegment(sketch, "E6174", {"start": v(7216, 3203.2) * mm, "end": v(7195.33, 3207.61) * mm});
            skLineSegment(sketch, "E6175", {"start": v(7195.33, 3207.61) * mm, "end": v(7173.47, 3211.68) * mm});
            skLineSegment(sketch, "E6176", {"start": v(7173.47, 3211.68) * mm, "end": v(7150.41, 3215.33) * mm});
            skLineSegment(sketch, "E6177", {"start": v(7150.41, 3215.33) * mm, "end": v(7126.17, 3218.5) * mm});
            skLineSegment(sketch, "E6178", {"start": v(7126.17, 3218.5) * mm, "end": v(7100.76, 3221.13) * mm});
            skLineSegment(sketch, "E6179", {"start": v(7100.76, 3221.13) * mm, "end": v(7074.19, 3223.17) * mm});
            skLineSegment(sketch, "E6180", {"start": v(7074.19, 3223.17) * mm, "end": v(7046.46, 3224.54) * mm});
            skLineSegment(sketch, "E6181", {"start": v(7046.46, 3224.54) * mm, "end": v(7017.61, 3225.2) * mm});
            skLineSegment(sketch, "E6182", {"start": v(7017.61, 3225.2) * mm, "end": v(6988.9, 3224.17) * mm});
            skLineSegment(sketch, "E6183", {"start": v(6988.9, 3224.17) * mm, "end": v(6913.9, 3111.06) * mm});
            skLineSegment(sketch, "E6184", {"start": v(6913.9, 3111.06) * mm, "end": v(6924.12, 3084.23) * mm});
            skLineSegment(sketch, "E6185", {"start": v(6924.12, 3084.23) * mm, "end": v(6935.95, 3057.9) * mm});
            skLineSegment(sketch, "E6186", {"start": v(6935.95, 3057.9) * mm, "end": v(6948.01, 3032.9) * mm});
            skLineSegment(sketch, "E6187", {"start": v(6948.01, 3032.9) * mm, "end": v(6960.23, 3009.21) * mm});
            skLineSegment(sketch, "E6188", {"start": v(6960.23, 3009.21) * mm, "end": v(6972.54, 2986.83) * mm});
            skLineSegment(sketch, "E6189", {"start": v(6972.54, 2986.83) * mm, "end": v(6984.9, 2965.73) * mm});
            skLineSegment(sketch, "E6190", {"start": v(6984.9, 2965.73) * mm, "end": v(6997.23, 2945.91) * mm});
            skLineSegment(sketch, "E6191", {"start": v(6997.23, 2945.91) * mm, "end": v(7009.48, 2927.35) * mm});
            skLineSegment(sketch, "E6192", {"start": v(7009.48, 2927.35) * mm, "end": v(7021.6, 2910.03) * mm});
            skLineSegment(sketch, "E6193", {"start": v(7021.6, 2910.03) * mm, "end": v(7033.51, 2893.93) * mm});
            skLineSegment(sketch, "E6194", {"start": v(7033.51, 2893.93) * mm, "end": v(7045.17, 2879.03) * mm});
            skLineSegment(sketch, "E6195", {"start": v(7045.17, 2879.03) * mm, "end": v(7056.53, 2865.3) * mm});
            skLineSegment(sketch, "E6196", {"start": v(7056.53, 2865.3) * mm, "end": v(7067.53, 2852.7) * mm});
            skLineSegment(sketch, "E6197", {"start": v(7067.53, 2852.7) * mm, "end": v(7078.11, 2841.21) * mm});
            skLineSegment(sketch, "E6198", {"start": v(7078.11, 2841.21) * mm, "end": v(7088.23, 2830.8) * mm});
            skLineSegment(sketch, "E6199", {"start": v(7088.23, 2830.8) * mm, "end": v(7097.83, 2821.45) * mm});
            skLineSegment(sketch, "E6200", {"start": v(7097.83, 2821.45) * mm, "end": v(7106.87, 2813.1) * mm});
            skLineSegment(sketch, "E6201", {"start": v(7106.87, 2813.1) * mm, "end": v(7115.3, 2805.72) * mm});
            skLineSegment(sketch, "E6202", {"start": v(7115.3, 2805.72) * mm, "end": v(7123.08, 2799.28) * mm});
            skLineSegment(sketch, "E6203", {"start": v(7123.08, 2799.28) * mm, "end": v(7130.15, 2793.73) * mm});
            skLineSegment(sketch, "E6204", {"start": v(7130.15, 2793.73) * mm, "end": v(7136.49, 2789.02) * mm});
            skLineSegment(sketch, "E6205", {"start": v(7136.49, 2789.02) * mm, "end": v(7142.05, 2785.13) * mm});
            skLineSegment(sketch, "E6206", {"start": v(7142.05, 2785.13) * mm, "end": v(7146.79, 2781.99) * mm});
            skLineSegment(sketch, "E6207", {"start": v(7146.79, 2781.99) * mm, "end": v(7150.67, 2779.56) * mm});
            skLineSegment(sketch, "E6208", {"start": v(7150.67, 2779.56) * mm, "end": v(7153.67, 2777.8) * mm});
            skLineSegment(sketch, "E6209", {"start": v(7153.67, 2777.8) * mm, "end": v(7155.74, 2776.65) * mm});
            skLineSegment(sketch, "E6210", {"start": v(7155.74, 2776.65) * mm, "end": v(7156.87, 2776.07) * mm});
            skLineSegment(sketch, "E6211", {"start": v(7156.87, 2776.07) * mm, "end": v(7312.14, 2701.8) * mm});
            skLineSegment(sketch, "E6212", {"start": v(7312.14, 2701.8) * mm, "end": v(7218.62, 2440.66) * mm});
            skLineSegment(sketch, "E6213", {"start": v(7218.62, 2440.66) * mm, "end": v(7051.5, 2481.85) * mm});
            skLineSegment(sketch, "E6214", {"start": v(7051.5, 2481.85) * mm, "end": v(7050.26, 2482.11) * mm});
            skLineSegment(sketch, "E6215", {"start": v(7050.26, 2482.11) * mm, "end": v(7047.93, 2482.54) * mm});
            skLineSegment(sketch, "E6216", {"start": v(7047.93, 2482.54) * mm, "end": v(7044.5, 2483.09) * mm});
            skLineSegment(sketch, "E6217", {"start": v(7044.5, 2483.09) * mm, "end": v(7039.95, 2483.68) * mm});
            skLineSegment(sketch, "E6218", {"start": v(7039.95, 2483.68) * mm, "end": v(7034.3, 2484.26) * mm});
            skLineSegment(sketch, "E6219", {"start": v(7034.3, 2484.26) * mm, "end": v(7027.53, 2484.78) * mm});
            skLineSegment(sketch, "E6220", {"start": v(7027.53, 2484.78) * mm, "end": v(7019.65, 2485.17) * mm});
            skLineSegment(sketch, "E6221", {"start": v(7019.65, 2485.17) * mm, "end": v(7010.66, 2485.37) * mm});
            skLineSegment(sketch, "E6222", {"start": v(7010.66, 2485.37) * mm, "end": v(7000.56, 2485.33) * mm});
            skLineSegment(sketch, "E6223", {"start": v(7000.56, 2485.33) * mm, "end": v(6989.36, 2484.98) * mm});
            skLineSegment(sketch, "E6224", {"start": v(6989.36, 2484.98) * mm, "end": v(6977.08, 2484.27) * mm});
            skLineSegment(sketch, "E6225", {"start": v(6977.08, 2484.27) * mm, "end": v(6963.72, 2483.13) * mm});
            skLineSegment(sketch, "E6226", {"start": v(6963.72, 2483.13) * mm, "end": v(6949.3, 2481.52) * mm});
            skLineSegment(sketch, "E6227", {"start": v(6949.3, 2481.52) * mm, "end": v(6933.83, 2479.36) * mm});
            skLineSegment(sketch, "E6228", {"start": v(6933.83, 2479.36) * mm, "end": v(6917.33, 2476.6) * mm});
            skLineSegment(sketch, "E6229", {"start": v(6917.33, 2476.6) * mm, "end": v(6899.84, 2473.2) * mm});
            skLineSegment(sketch, "E6230", {"start": v(6899.84, 2473.2) * mm, "end": v(6881.36, 2469.1) * mm});
            skLineSegment(sketch, "E6231", {"start": v(6881.36, 2469.1) * mm, "end": v(6861.93, 2464.22) * mm});
            skLineSegment(sketch, "E6232", {"start": v(6861.93, 2464.22) * mm, "end": v(6841.58, 2458.53) * mm});
            skLineSegment(sketch, "E6233", {"start": v(6841.58, 2458.53) * mm, "end": v(6820.33, 2451.97) * mm});
            skLineSegment(sketch, "E6234", {"start": v(6820.33, 2451.97) * mm, "end": v(6798.22, 2444.48) * mm});
            skLineSegment(sketch, "E6235", {"start": v(6798.22, 2444.48) * mm, "end": v(6775.28, 2436.03) * mm});
            skLineSegment(sketch, "E6236", {"start": v(6775.28, 2436.03) * mm, "end": v(6751.56, 2426.55) * mm});
            skLineSegment(sketch, "E6237", {"start": v(6751.56, 2426.55) * mm, "end": v(6727.08, 2416) * mm});
            skLineSegment(sketch, "E6238", {"start": v(6727.08, 2416) * mm, "end": v(6701.9, 2404.34) * mm});
            skLineSegment(sketch, "E6239", {"start": v(6701.9, 2404.34) * mm, "end": v(6676.04, 2391.51) * mm});
            skLineSegment(sketch, "E6240", {"start": v(6676.04, 2391.51) * mm, "end": v(6651.1, 2377.26) * mm});
            skLineSegment(sketch, "E6241", {"start": v(6651.1, 2377.26) * mm, "end": v(6637.25, 2242.25) * mm});
            skLineSegment(sketch, "E6242", {"start": v(6637.25, 2242.25) * mm, "end": v(6658.78, 2223.24) * mm});
            skLineSegment(sketch, "E6243", {"start": v(6658.78, 2223.24) * mm, "end": v(6681.49, 2205.43) * mm});
            skLineSegment(sketch, "E6244", {"start": v(6681.49, 2205.43) * mm, "end": v(6703.78, 2188.9) * mm});
            skLineSegment(sketch, "E6245", {"start": v(6703.78, 2188.9) * mm, "end": v(6725.6, 2173.6) * mm});
            skLineSegment(sketch, "E6246", {"start": v(6725.6, 2173.6) * mm, "end": v(6746.91, 2159.5) * mm});
            skLineSegment(sketch, "E6247", {"start": v(6746.91, 2159.5) * mm, "end": v(6767.65, 2146.56) * mm});
            skLineSegment(sketch, "E6248", {"start": v(6767.65, 2146.56) * mm, "end": v(6787.79, 2134.74) * mm});
            skLineSegment(sketch, "E6249", {"start": v(6787.79, 2134.74) * mm, "end": v(6807.26, 2124) * mm});
            skLineSegment(sketch, "E6250", {"start": v(6807.26, 2124) * mm, "end": v(6826.03, 2114.3) * mm});
            skLineSegment(sketch, "E6251", {"start": v(6826.03, 2114.3) * mm, "end": v(6844.07, 2105.58) * mm});
            skLineSegment(sketch, "E6252", {"start": v(6844.07, 2105.58) * mm, "end": v(6861.32, 2097.8) * mm});
            skLineSegment(sketch, "E6253", {"start": v(6861.32, 2097.8) * mm, "end": v(6877.76, 2090.92) * mm});
            skLineSegment(sketch, "E6254", {"start": v(6877.76, 2090.92) * mm, "end": v(6893.35, 2084.88) * mm});
            skLineSegment(sketch, "E6255", {"start": v(6893.35, 2084.88) * mm, "end": v(6908.06, 2079.62) * mm});
            skLineSegment(sketch, "E6256", {"start": v(6908.06, 2079.62) * mm, "end": v(6921.85, 2075.11) * mm});
            skLineSegment(sketch, "E6257", {"start": v(6921.85, 2075.11) * mm, "end": v(6934.7, 2071.29) * mm});
            skLineSegment(sketch, "E6258", {"start": v(6934.7, 2071.29) * mm, "end": v(6946.6, 2068.1) * mm});
            skLineSegment(sketch, "E6259", {"start": v(6946.6, 2068.1) * mm, "end": v(6957.48, 2065.48) * mm});
            skLineSegment(sketch, "E6260", {"start": v(6957.48, 2065.48) * mm, "end": v(6967.36, 2063.39) * mm});
            skLineSegment(sketch, "E6261", {"start": v(6967.36, 2063.39) * mm, "end": v(6976.2, 2061.76) * mm});
            skLineSegment(sketch, "E6262", {"start": v(6976.2, 2061.76) * mm, "end": v(6984, 2060.54) * mm});
            skLineSegment(sketch, "E6263", {"start": v(6984, 2060.54) * mm, "end": v(6990.74, 2059.67) * mm});
            skLineSegment(sketch, "E6264", {"start": v(6990.74, 2059.67) * mm, "end": v(6996.4, 2059.1) * mm});
            skLineSegment(sketch, "E6265", {"start": v(6996.4, 2059.1) * mm, "end": v(7000.96, 2058.76) * mm});
            skLineSegment(sketch, "E6266", {"start": v(7000.96, 2058.76) * mm, "end": v(7004.43, 2058.59) * mm});
            skLineSegment(sketch, "E6267", {"start": v(7004.43, 2058.59) * mm, "end": v(7006.8, 2058.54) * mm});
            skLineSegment(sketch, "E6268", {"start": v(7006.8, 2058.54) * mm, "end": v(7008.07, 2058.54) * mm});
            skLineSegment(sketch, "E6269", {"start": v(7008.07, 2058.54) * mm, "end": v(7180.07, 2064.94) * mm});
            skLineSegment(sketch, "E6270", {"start": v(7180.07, 2064.94) * mm, "end": v(7218.62, 1790.25) * mm});
            skLineSegment(sketch, "E6271", {"start": v(7218.62, 1790.25) * mm, "end": v(7051.5, 1749.06) * mm});
            skLineSegment(sketch, "E6272", {"start": v(7051.5, 1749.06) * mm, "end": v(7050.28, 1748.72) * mm});
            skLineSegment(sketch, "E6273", {"start": v(7050.28, 1748.72) * mm, "end": v(7048.02, 1748.01) * mm});
            skLineSegment(sketch, "E6274", {"start": v(7048.02, 1748.01) * mm, "end": v(7044.72, 1746.9) * mm});
            skLineSegment(sketch, "E6275", {"start": v(7044.72, 1746.9) * mm, "end": v(7040.43, 1745.31) * mm});
            skLineSegment(sketch, "E6276", {"start": v(7040.43, 1745.31) * mm, "end": v(7035.15, 1743.2) * mm});
            skLineSegment(sketch, "E6277", {"start": v(7035.15, 1743.2) * mm, "end": v(7028.92, 1740.51) * mm});
            skLineSegment(sketch, "E6278", {"start": v(7028.92, 1740.51) * mm, "end": v(7021.76, 1737.2) * mm});
            skLineSegment(sketch, "E6279", {"start": v(7021.76, 1737.2) * mm, "end": v(7013.7, 1733.2) * mm});
            skLineSegment(sketch, "E6280", {"start": v(7013.7, 1733.2) * mm, "end": v(7004.78, 1728.46) * mm});
            skLineSegment(sketch, "E6281", {"start": v(7004.78, 1728.46) * mm, "end": v(6995.03, 1722.95) * mm});
            skLineSegment(sketch, "E6282", {"start": v(6995.03, 1722.95) * mm, "end": v(6984.48, 1716.61) * mm});
            skLineSegment(sketch, "E6283", {"start": v(6984.48, 1716.61) * mm, "end": v(6973.18, 1709.4) * mm});
            skLineSegment(sketch, "E6284", {"start": v(6973.18, 1709.4) * mm, "end": v(6961.16, 1701.26) * mm});
            skLineSegment(sketch, "E6285", {"start": v(6961.16, 1701.26) * mm, "end": v(6948.46, 1692.17) * mm});
            skLineSegment(sketch, "E6286", {"start": v(6948.46, 1692.17) * mm, "end": v(6935.14, 1682.07) * mm});
            skLineSegment(sketch, "E6287", {"start": v(6935.14, 1682.07) * mm, "end": v(6921.23, 1670.92) * mm});
            skLineSegment(sketch, "E6288", {"start": v(6921.23, 1670.92) * mm, "end": v(6906.78, 1658.7) * mm});
            skLineSegment(sketch, "E6289", {"start": v(6906.78, 1658.7) * mm, "end": v(6891.84, 1645.35) * mm});
            skLineSegment(sketch, "E6290", {"start": v(6891.84, 1645.35) * mm, "end": v(6876.46, 1630.85) * mm});
            skLineSegment(sketch, "E6291", {"start": v(6876.46, 1630.85) * mm, "end": v(6860.7, 1615.17) * mm});
            skLineSegment(sketch, "E6292", {"start": v(6860.7, 1615.17) * mm, "end": v(6844.6, 1598.27) * mm});
            skLineSegment(sketch, "E6293", {"start": v(6844.6, 1598.27) * mm, "end": v(6828.22, 1580.12) * mm});
            skLineSegment(sketch, "E6294", {"start": v(6828.22, 1580.12) * mm, "end": v(6811.61, 1560.7) * mm});
            skLineSegment(sketch, "E6295", {"start": v(6811.61, 1560.7) * mm, "end": v(6794.84, 1539.99) * mm});
            skLineSegment(sketch, "E6296", {"start": v(6794.84, 1539.99) * mm, "end": v(6777.96, 1517.95) * mm});
            skLineSegment(sketch, "E6297", {"start": v(6777.96, 1517.95) * mm, "end": v(6761.03, 1494.58) * mm});
            skLineSegment(sketch, "E6298", {"start": v(6761.03, 1494.58) * mm, "end": v(6745.57, 1470.38) * mm});
            skLineSegment(sketch, "E6299", {"start": v(6745.57, 1470.38) * mm, "end": v(6796.05, 1344.4) * mm});
            skLineSegment(sketch, "E6300", {"start": v(6796.05, 1344.4) * mm, "end": v(6823.95, 1337.56) * mm});
            skLineSegment(sketch, "E6301", {"start": v(6823.95, 1337.56) * mm, "end": v(6852.33, 1332.35) * mm});
            skLineSegment(sketch, "E6302", {"start": v(6852.33, 1332.35) * mm, "end": v(6879.76, 1328.07) * mm});
            skLineSegment(sketch, "E6303", {"start": v(6879.76, 1328.07) * mm, "end": v(6906.2, 1324.66) * mm});
            skLineSegment(sketch, "E6304", {"start": v(6906.2, 1324.66) * mm, "end": v(6931.6, 1322.08) * mm});
            skLineSegment(sketch, "E6305", {"start": v(6931.6, 1322.08) * mm, "end": v(6955.99, 1320.26) * mm});
            skLineSegment(sketch, "E6306", {"start": v(6955.99, 1320.26) * mm, "end": v(6979.3, 1319.15) * mm});
            skLineSegment(sketch, "E6307", {"start": v(6979.3, 1319.15) * mm, "end": v(7001.54, 1318.7) * mm});
            skLineSegment(sketch, "E6308", {"start": v(7001.54, 1318.7) * mm, "end": v(7022.67, 1318.83) * mm});
            skLineSegment(sketch, "E6309", {"start": v(7022.67, 1318.83) * mm, "end": v(7042.69, 1319.49) * mm});
            skLineSegment(sketch, "E6310", {"start": v(7042.69, 1319.49) * mm, "end": v(7061.58, 1320.62) * mm});
            skLineSegment(sketch, "E6311", {"start": v(7061.58, 1320.62) * mm, "end": v(7079.34, 1322.16) * mm});
            skLineSegment(sketch, "E6312", {"start": v(7079.34, 1322.16) * mm, "end": v(7095.95, 1324.06) * mm});
            skLineSegment(sketch, "E6313", {"start": v(7095.95, 1324.06) * mm, "end": v(7111.42, 1326.24) * mm});
            skLineSegment(sketch, "E6314", {"start": v(7111.42, 1326.24) * mm, "end": v(7125.73, 1328.66) * mm});
            skLineSegment(sketch, "E6315", {"start": v(7125.73, 1328.66) * mm, "end": v(7138.88, 1331.25) * mm});
            skLineSegment(sketch, "E6316", {"start": v(7138.88, 1331.25) * mm, "end": v(7150.89, 1333.94) * mm});
            skLineSegment(sketch, "E6317", {"start": v(7150.89, 1333.94) * mm, "end": v(7161.75, 1336.7) * mm});
            skLineSegment(sketch, "E6318", {"start": v(7161.75, 1336.7) * mm, "end": v(7171.47, 1339.43) * mm});
            skLineSegment(sketch, "E6319", {"start": v(7171.47, 1339.43) * mm, "end": v(7180.06, 1342.1) * mm});
            skLineSegment(sketch, "E6320", {"start": v(7180.06, 1342.1) * mm, "end": v(7187.53, 1344.64) * mm});
            skLineSegment(sketch, "E6321", {"start": v(7187.53, 1344.64) * mm, "end": v(7193.9, 1347) * mm});
            skLineSegment(sketch, "E6322", {"start": v(7193.9, 1347) * mm, "end": v(7199.17, 1349.12) * mm});
            skLineSegment(sketch, "E6323", {"start": v(7199.17, 1349.12) * mm, "end": v(7203.37, 1350.94) * mm});
            skLineSegment(sketch, "E6324", {"start": v(7203.37, 1350.94) * mm, "end": v(7206.52, 1352.4) * mm});
            skLineSegment(sketch, "E6325", {"start": v(7206.52, 1352.4) * mm, "end": v(7208.65, 1353.46) * mm});
            skLineSegment(sketch, "E6326", {"start": v(7208.65, 1353.46) * mm, "end": v(7209.77, 1354.06) * mm});
            skLineSegment(sketch, "E6327", {"start": v(7209.77, 1354.06) * mm, "end": v(7359.1, 1439.65) * mm});
            skLineSegment(sketch, "E6328", {"start": v(7359.1, 1439.65) * mm, "end": v(7520.88, 1214.34) * mm});
            skLineSegment(sketch, "E6329", {"start": v(7520.88, 1214.34) * mm, "end": v(7392.05, 1100.2) * mm});
            skLineSegment(sketch, "E6330", {"start": v(7392.05, 1100.2) * mm, "end": v(7391.13, 1099.33) * mm});
            skLineSegment(sketch, "E6331", {"start": v(7391.13, 1099.33) * mm, "end": v(7389.45, 1097.66) * mm});
            skLineSegment(sketch, "E6332", {"start": v(7389.45, 1097.66) * mm, "end": v(7387.05, 1095.14) * mm});
            skLineSegment(sketch, "E6333", {"start": v(7387.05, 1095.14) * mm, "end": v(7383.98, 1091.74) * mm});
            skLineSegment(sketch, "E6334", {"start": v(7383.98, 1091.74) * mm, "end": v(7380.3, 1087.42) * mm});
            skLineSegment(sketch, "E6335", {"start": v(7380.3, 1087.42) * mm, "end": v(7376.02, 1082.14) * mm});
            skLineSegment(sketch, "E6336", {"start": v(7376.02, 1082.14) * mm, "end": v(7371.22, 1075.88) * mm});
            skLineSegment(sketch, "E6337", {"start": v(7371.22, 1075.88) * mm, "end": v(7365.95, 1068.6) * mm});
            skLineSegment(sketch, "E6338", {"start": v(7365.95, 1068.6) * mm, "end": v(7360.25, 1060.26) * mm});
            skLineSegment(sketch, "E6339", {"start": v(7360.25, 1060.26) * mm, "end": v(7354.18, 1050.84) * mm});
            skLineSegment(sketch, "E6340", {"start": v(7354.18, 1050.84) * mm, "end": v(7347.78, 1040.33) * mm});
            skLineSegment(sketch, "E6341", {"start": v(7347.78, 1040.33) * mm, "end": v(7341.13, 1028.69) * mm});
            skLineSegment(sketch, "E6342", {"start": v(7341.13, 1028.69) * mm, "end": v(7334.26, 1015.9) * mm});
            skLineSegment(sketch, "E6343", {"start": v(7334.26, 1015.9) * mm, "end": v(7327.25, 1001.95) * mm});
            skLineSegment(sketch, "E6344", {"start": v(7327.25, 1001.95) * mm, "end": v(7320.15, 986.8) * mm});
            skLineSegment(sketch, "E6345", {"start": v(7320.15, 986.8) * mm, "end": v(7313, 970.48) * mm});
            skLineSegment(sketch, "E6346", {"start": v(7313, 970.48) * mm, "end": v(7305.9, 952.94) * mm});
            skLineSegment(sketch, "E6347", {"start": v(7305.9, 952.94) * mm, "end": v(7298.87, 934.18) * mm});
            skLineSegment(sketch, "E6348", {"start": v(7298.87, 934.18) * mm, "end": v(7292, 914.2) * mm});
            skLineSegment(sketch, "E6349", {"start": v(7292, 914.2) * mm, "end": v(7285.32, 892.98) * mm});
            skLineSegment(sketch, "E6350", {"start": v(7285.32, 892.98) * mm, "end": v(7278.92, 870.53) * mm});
            skLineSegment(sketch, "E6351", {"start": v(7278.92, 870.53) * mm, "end": v(7272.85, 846.85) * mm});
            skLineSegment(sketch, "E6352", {"start": v(7272.85, 846.85) * mm, "end": v(7267.17, 821.94) * mm});
            skLineSegment(sketch, "E6353", {"start": v(7267.17, 821.94) * mm, "end": v(7261.95, 795.8) * mm});
            skLineSegment(sketch, "E6354", {"start": v(7261.95, 795.8) * mm, "end": v(7257.24, 768.45) * mm});
            skLineSegment(sketch, "E6355", {"start": v(7257.24, 768.45) * mm, "end": v(7253.11, 739.89) * mm});
            skLineSegment(sketch, "E6356", {"start": v(7253.11, 739.89) * mm, "end": v(7250.67, 711.27) * mm});
            skLineSegment(sketch, "E6357", {"start": v(7250.67, 711.27) * mm, "end": v(7353.91, 623.18) * mm});
            skLineSegment(sketch, "E6358", {"start": v(7353.91, 623.18) * mm, "end": v(7381.79, 630.1) * mm});
            skLineSegment(sketch, "E6359", {"start": v(7381.79, 630.1) * mm, "end": v(7409.35, 638.66) * mm});
            skLineSegment(sketch, "E6360", {"start": v(7409.35, 638.66) * mm, "end": v(7435.62, 647.62) * mm});
            skLineSegment(sketch, "E6361", {"start": v(7435.62, 647.62) * mm, "end": v(7460.6, 656.89) * mm});
            skLineSegment(sketch, "E6362", {"start": v(7460.6, 656.89) * mm, "end": v(7484.31, 666.42) * mm});
            skLineSegment(sketch, "E6363", {"start": v(7484.31, 666.42) * mm, "end": v(7506.74, 676.14) * mm});
            skLineSegment(sketch, "E6364", {"start": v(7506.74, 676.14) * mm, "end": v(7527.9, 686) * mm});
            skLineSegment(sketch, "E6365", {"start": v(7527.9, 686) * mm, "end": v(7547.8, 695.92) * mm});
            skLineSegment(sketch, "E6366", {"start": v(7547.8, 695.92) * mm, "end": v(7566.46, 705.85) * mm});
            skLineSegment(sketch, "E6367", {"start": v(7566.46, 705.85) * mm, "end": v(7583.88, 715.74) * mm});
            skLineSegment(sketch, "E6368", {"start": v(7583.88, 715.74) * mm, "end": v(7600.08, 725.53) * mm});
            skLineSegment(sketch, "E6369", {"start": v(7600.08, 725.53) * mm, "end": v(7615.09, 735.15) * mm});
            skLineSegment(sketch, "E6370", {"start": v(7615.09, 735.15) * mm, "end": v(7628.92, 744.54) * mm});
            skLineSegment(sketch, "E6371", {"start": v(7628.92, 744.54) * mm, "end": v(7641.6, 753.67) * mm});
            skLineSegment(sketch, "E6372", {"start": v(7641.6, 753.67) * mm, "end": v(7653.14, 762.45) * mm});
            skLineSegment(sketch, "E6373", {"start": v(7653.14, 762.45) * mm, "end": v(7663.59, 770.86) * mm});
            skLineSegment(sketch, "E6374", {"start": v(7663.59, 770.86) * mm, "end": v(7672.97, 778.83) * mm});
            skLineSegment(sketch, "E6375", {"start": v(7672.97, 778.83) * mm, "end": v(7681.3, 786.3) * mm});
            skLineSegment(sketch, "E6376", {"start": v(7681.3, 786.3) * mm, "end": v(7688.64, 793.25) * mm});
            skLineSegment(sketch, "E6377", {"start": v(7688.64, 793.25) * mm, "end": v(7695, 799.6) * mm});
            skLineSegment(sketch, "E6378", {"start": v(7695, 799.6) * mm, "end": v(7700.44, 805.33) * mm});
            skLineSegment(sketch, "E6379", {"start": v(7700.44, 805.33) * mm, "end": v(7704.98, 810.37) * mm});
            skLineSegment(sketch, "E6380", {"start": v(7704.98, 810.37) * mm, "end": v(7708.66, 814.7) * mm});
            skLineSegment(sketch, "E6381", {"start": v(7708.66, 814.7) * mm, "end": v(7711.54, 818.26) * mm});
            skLineSegment(sketch, "E6382", {"start": v(7711.54, 818.26) * mm, "end": v(7713.65, 821.03) * mm});
            skLineSegment(sketch, "E6383", {"start": v(7713.65, 821.03) * mm, "end": v(7715.04, 822.95) * mm});
            skLineSegment(sketch, "E6384", {"start": v(7715.04, 822.95) * mm, "end": v(7715.75, 824) * mm});
            skLineSegment(sketch, "E6385", {"start": v(7715.75, 824) * mm, "end": v(7808.2, 969.18) * mm});
            skLineSegment(sketch, "E6386", {"start": v(7808.2, 969.18) * mm, "end": v(8056.16, 844.86) * mm});
            skLineSegment(sketch, "E6387", {"start": v(8056.16, 844.86) * mm, "end": v(7995.13, 683.93) * mm});
            skLineSegment(sketch, "E6388", {"start": v(7995.13, 683.93) * mm, "end": v(7994.71, 682.73) * mm});
            skLineSegment(sketch, "E6389", {"start": v(7994.71, 682.73) * mm, "end": v(7994, 680.47) * mm});
            skLineSegment(sketch, "E6390", {"start": v(7994, 680.47) * mm, "end": v(7993.05, 677.12) * mm});
            skLineSegment(sketch, "E6391", {"start": v(7993.05, 677.12) * mm, "end": v(7991.92, 672.69) * mm});
            skLineSegment(sketch, "E6392", {"start": v(7991.92, 672.69) * mm, "end": v(7990.66, 667.15) * mm});
            skLineSegment(sketch, "E6393", {"start": v(7990.66, 667.15) * mm, "end": v(7989.33, 660.5) * mm});
            skLineSegment(sketch, "E6394", {"start": v(7989.33, 660.5) * mm, "end": v(7988, 652.71) * mm});
            skLineSegment(sketch, "E6395", {"start": v(7988, 652.71) * mm, "end": v(7986.7, 643.8) * mm});
            skLineSegment(sketch, "E6396", {"start": v(7986.7, 643.8) * mm, "end": v(7985.53, 633.78) * mm});
            skLineSegment(sketch, "E6397", {"start": v(7985.53, 633.78) * mm, "end": v(7984.53, 622.62) * mm});
            skLineSegment(sketch, "E6398", {"start": v(7984.53, 622.62) * mm, "end": v(7983.76, 610.34) * mm});
            skLineSegment(sketch, "E6399", {"start": v(7983.76, 610.34) * mm, "end": v(7983.27, 596.94) * mm});
            skLineSegment(sketch, "E6400", {"start": v(7983.27, 596.94) * mm, "end": v(7983.14, 582.43) * mm});
            skLineSegment(sketch, "E6401", {"start": v(7983.14, 582.43) * mm, "end": v(7983.41, 566.82) * mm});
            skLineSegment(sketch, "E6402", {"start": v(7983.41, 566.82) * mm, "end": v(7984.16, 550.11) * mm});
            skLineSegment(sketch, "E6403", {"start": v(7984.16, 550.11) * mm, "end": v(7985.43, 532.33) * mm});
            skLineSegment(sketch, "E6404", {"start": v(7985.43, 532.33) * mm, "end": v(7987.28, 513.5) * mm});
            skLineSegment(sketch, "E6405", {"start": v(7987.28, 513.5) * mm, "end": v(7989.78, 493.62) * mm});
            skLineSegment(sketch, "E6406", {"start": v(7989.78, 493.62) * mm, "end": v(7992.97, 472.73) * mm});
            skLineSegment(sketch, "E6407", {"start": v(7992.97, 472.73) * mm, "end": v(7996.93, 450.85) * mm});
            skLineSegment(sketch, "E6408", {"start": v(7996.93, 450.85) * mm, "end": v(8001.7, 428) * mm});
            skLineSegment(sketch, "E6409", {"start": v(8001.7, 428) * mm, "end": v(8007.32, 404.2) * mm});
            skLineSegment(sketch, "E6410", {"start": v(8007.32, 404.2) * mm, "end": v(8013.87, 379.51) * mm});
            skLineSegment(sketch, "E6411", {"start": v(8013.87, 379.51) * mm, "end": v(8021.39, 353.94) * mm});
            skLineSegment(sketch, "E6412", {"start": v(8021.39, 353.94) * mm, "end": v(8029.93, 327.53) * mm});
            skLineSegment(sketch, "E6413", {"start": v(8029.93, 327.53) * mm, "end": v(8039.55, 300.32) * mm});
            skLineSegment(sketch, "E6414", {"start": v(8039.55, 300.32) * mm, "end": v(8050.69, 273.85) * mm});
            skLineSegment(sketch, "E6415", {"start": v(8050.69, 273.85) * mm, "end": v(8183.04, 243.82) * mm});
            skLineSegment(sketch, "E6416", {"start": v(8183.04, 243.82) * mm, "end": v(8204.51, 262.9) * mm});
            skLineSegment(sketch, "E6417", {"start": v(8204.51, 262.9) * mm, "end": v(8224.93, 283.3) * mm});
            skLineSegment(sketch, "E6418", {"start": v(8224.93, 283.3) * mm, "end": v(8244.03, 303.44) * mm});
            skLineSegment(sketch, "E6419", {"start": v(8244.03, 303.44) * mm, "end": v(8261.85, 323.26) * mm});
            skLineSegment(sketch, "E6420", {"start": v(8261.85, 323.26) * mm, "end": v(8278.41, 342.7) * mm});
            skLineSegment(sketch, "E6421", {"start": v(8278.41, 342.7) * mm, "end": v(8293.76, 361.74) * mm});
            skLineSegment(sketch, "E6422", {"start": v(8293.76, 361.74) * mm, "end": v(8307.91, 380.3) * mm});
            skLineSegment(sketch, "E6423", {"start": v(8307.91, 380.3) * mm, "end": v(8320.92, 398.34) * mm});
            skLineSegment(sketch, "E6424", {"start": v(8320.92, 398.34) * mm, "end": v(8332.82, 415.8) * mm});
            skLineSegment(sketch, "E6425", {"start": v(8332.82, 415.8) * mm, "end": v(8343.65, 432.66) * mm});
            skLineSegment(sketch, "E6426", {"start": v(8343.65, 432.66) * mm, "end": v(8353.45, 448.85) * mm});
            skLineSegment(sketch, "E6427", {"start": v(8353.45, 448.85) * mm, "end": v(8362.27, 464.34) * mm});
            skLineSegment(sketch, "E6428", {"start": v(8362.27, 464.34) * mm, "end": v(8370.14, 479.09) * mm});
            skLineSegment(sketch, "E6429", {"start": v(8370.14, 479.09) * mm, "end": v(8377.13, 493.06) * mm});
            skLineSegment(sketch, "E6430", {"start": v(8377.13, 493.06) * mm, "end": v(8383.27, 506.2) * mm});
            skLineSegment(sketch, "E6431", {"start": v(8383.27, 506.2) * mm, "end": v(8388.62, 518.5) * mm});
            skLineSegment(sketch, "E6432", {"start": v(8388.62, 518.5) * mm, "end": v(8393.22, 529.91) * mm});
            skLineSegment(sketch, "E6433", {"start": v(8393.22, 529.91) * mm, "end": v(8397.13, 540.41) * mm});
            skLineSegment(sketch, "E6434", {"start": v(8397.13, 540.41) * mm, "end": v(8400.4, 549.97) * mm});
            skLineSegment(sketch, "E6435", {"start": v(8400.4, 549.97) * mm, "end": v(8403.08, 558.55) * mm});
            skLineSegment(sketch, "E6436", {"start": v(8403.08, 558.55) * mm, "end": v(8405.23, 566.15) * mm});
            skLineSegment(sketch, "E6437", {"start": v(8405.23, 566.15) * mm, "end": v(8406.9, 572.72) * mm});
            skLineSegment(sketch, "E6438", {"start": v(8406.9, 572.72) * mm, "end": v(8408.15, 578.27) * mm});
            skLineSegment(sketch, "E6439", {"start": v(8408.15, 578.27) * mm, "end": v(8409.04, 582.76) * mm});
            skLineSegment(sketch, "E6440", {"start": v(8409.04, 582.76) * mm, "end": v(8409.63, 586.19) * mm});
            skLineSegment(sketch, "E6441", {"start": v(8409.63, 586.19) * mm, "end": v(8409.96, 588.54) * mm});
            skLineSegment(sketch, "E6442", {"start": v(8409.96, 588.54) * mm, "end": v(8410.11, 589.8) * mm});
            skLineSegment(sketch, "E6443", {"start": v(8410.11, 589.8) * mm, "end": v(8424.5, 761.3) * mm});
            skLineSegment(sketch, "E6444", {"start": v(8424.5, 761.3) * mm, "end": v(8701.83, 766.47) * mm});
            skLineSegment(sketch, "E6445", {"start": v(8701.83, 766.47) * mm, "end": v(8722.57, 595.6) * mm});
            skLineSegment(sketch, "E6446", {"start": v(8722.57, 595.6) * mm, "end": v(8722.77, 594.35) * mm});
            skLineSegment(sketch, "E6447", {"start": v(8722.77, 594.35) * mm, "end": v(8723.2, 592.02) * mm});
            skLineSegment(sketch, "E6448", {"start": v(8723.2, 592.02) * mm, "end": v(8723.9, 588.61) * mm});
            skLineSegment(sketch, "E6449", {"start": v(8723.9, 588.61) * mm, "end": v(8724.96, 584.16) * mm});
            skLineSegment(sketch, "E6450", {"start": v(8724.96, 584.16) * mm, "end": v(8726.42, 578.67) * mm});
            skLineSegment(sketch, "E6451", {"start": v(8726.42, 578.67) * mm, "end": v(8728.34, 572.15) * mm});
            skLineSegment(sketch, "E6452", {"start": v(8728.34, 572.15) * mm, "end": v(8730.77, 564.65) * mm});
            skLineSegment(sketch, "E6453", {"start": v(8730.77, 564.65) * mm, "end": v(8733.77, 556.17) * mm});
            skLineSegment(sketch, "E6454", {"start": v(8733.77, 556.17) * mm, "end": v(8737.39, 546.74) * mm});
            skLineSegment(sketch, "E6455", {"start": v(8737.39, 546.74) * mm, "end": v(8741.68, 536.4) * mm});
            skLineSegment(sketch, "E6456", {"start": v(8741.68, 536.4) * mm, "end": v(8746.7, 525.16) * mm});
            skLineSegment(sketch, "E6457", {"start": v(8746.7, 525.16) * mm, "end": v(8752.5, 513.07) * mm});
            skLineSegment(sketch, "E6458", {"start": v(8752.5, 513.07) * mm, "end": v(8759.13, 500.16) * mm});
            skLineSegment(sketch, "E6459", {"start": v(8759.13, 500.16) * mm, "end": v(8766.63, 486.46) * mm});
            skLineSegment(sketch, "E6460", {"start": v(8766.63, 486.46) * mm, "end": v(8775.05, 472.01) * mm});
            skLineSegment(sketch, "E6461", {"start": v(8775.05, 472.01) * mm, "end": v(8784.44, 456.86) * mm});
            skLineSegment(sketch, "E6462", {"start": v(8784.44, 456.86) * mm, "end": v(8794.83, 441.05) * mm});
            skLineSegment(sketch, "E6463", {"start": v(8794.83, 441.05) * mm, "end": v(8806.28, 424.6) * mm});
            skLineSegment(sketch, "E6464", {"start": v(8806.28, 424.6) * mm, "end": v(8818.82, 407.6) * mm});
            skLineSegment(sketch, "E6465", {"start": v(8818.82, 407.6) * mm, "end": v(8832.49, 390.05) * mm});
            skLineSegment(sketch, "E6466", {"start": v(8832.49, 390.05) * mm, "end": v(8847.33, 372.03) * mm});
            skLineSegment(sketch, "E6467", {"start": v(8847.33, 372.03) * mm, "end": v(8863.37, 353.59) * mm});
            skLineSegment(sketch, "E6468", {"start": v(8863.37, 353.59) * mm, "end": v(8880.64, 334.76) * mm});
            skLineSegment(sketch, "E6469", {"start": v(8880.64, 334.76) * mm, "end": v(8899.18, 315.62) * mm});
            skLineSegment(sketch, "E6470", {"start": v(8899.18, 315.62) * mm, "end": v(8919.02, 296.2) * mm});
            skLineSegment(sketch, "E6471", {"start": v(8919.02, 296.2) * mm, "end": v(8940.18, 276.58) * mm});
            skLineSegment(sketch, "E6472", {"start": v(8940.18, 276.58) * mm, "end": v(8962.35, 258.31) * mm});
            skLineSegment(sketch, "E6473", {"start": v(8962.35, 258.31) * mm, "end": v(9093.5, 293.24) * mm});
            skLineSegment(sketch, "E6474", {"start": v(9093.5, 293.24) * mm, "end": v(9103.64, 320.1) * mm});
            skLineSegment(sketch, "E6475", {"start": v(9103.64, 320.1) * mm, "end": v(9112.24, 347.66) * mm});
            skLineSegment(sketch, "E6476", {"start": v(9112.24, 347.66) * mm, "end": v(9119.8, 374.36) * mm});
            skLineSegment(sketch, "E6477", {"start": v(9119.8, 374.36) * mm, "end": v(9126.36, 400.2) * mm});
            skLineSegment(sketch, "E6478", {"start": v(9126.36, 400.2) * mm, "end": v(9131.99, 425.12) * mm});
            skLineSegment(sketch, "E6479", {"start": v(9131.99, 425.12) * mm, "end": v(9136.73, 449.1) * mm});
            skLineSegment(sketch, "E6480", {"start": v(9136.73, 449.1) * mm, "end": v(9140.64, 472.11) * mm});
            skLineSegment(sketch, "E6481", {"start": v(9140.64, 472.11) * mm, "end": v(9143.78, 494.13) * mm});
            skLineSegment(sketch, "E6482", {"start": v(9143.78, 494.13) * mm, "end": v(9146.2, 515.13) * mm});
            skLineSegment(sketch, "E6483", {"start": v(9146.2, 515.13) * mm, "end": v(9147.95, 535.08) * mm});
            skLineSegment(sketch, "E6484", {"start": v(9147.95, 535.08) * mm, "end": v(9149.1, 553.97) * mm});
            skLineSegment(sketch, "E6485", {"start": v(9149.1, 553.97) * mm, "end": v(9149.71, 571.78) * mm});
            skLineSegment(sketch, "E6486", {"start": v(9149.71, 571.78) * mm, "end": v(9149.83, 588.5) * mm});
            skLineSegment(sketch, "E6487", {"start": v(9149.83, 588.5) * mm, "end": v(9149.53, 604.12) * mm});
            skLineSegment(sketch, "E6488", {"start": v(9149.53, 604.12) * mm, "end": v(9148.85, 618.61) * mm});
            skLineSegment(sketch, "E6489", {"start": v(9148.85, 618.61) * mm, "end": v(9147.87, 631.99) * mm});
            skLineSegment(sketch, "E6490", {"start": v(9147.87, 631.99) * mm, "end": v(9146.64, 644.23) * mm});
            skLineSegment(sketch, "E6491", {"start": v(9146.64, 644.23) * mm, "end": v(9145.22, 655.34) * mm});
            skLineSegment(sketch, "E6492", {"start": v(9145.22, 655.34) * mm, "end": v(9143.68, 665.32) * mm});
            skLineSegment(sketch, "E6493", {"start": v(9143.68, 665.32) * mm, "end": v(9142.06, 674.17) * mm});
            skLineSegment(sketch, "E6494", {"start": v(9142.06, 674.17) * mm, "end": v(9140.44, 681.9) * mm});
            skLineSegment(sketch, "E6495", {"start": v(9140.44, 681.9) * mm, "end": v(9138.86, 688.5) * mm});
            skLineSegment(sketch, "E6496", {"start": v(9138.86, 688.5) * mm, "end": v(9137.4, 693.99) * mm});
            skLineSegment(sketch, "E6497", {"start": v(9137.4, 693.99) * mm, "end": v(9136.1, 698.38) * mm});
            skLineSegment(sketch, "E6498", {"start": v(9136.1, 698.38) * mm, "end": v(9135.02, 701.69) * mm});
            skLineSegment(sketch, "E6499", {"start": v(9135.02, 701.69) * mm, "end": v(9134.23, 703.92) * mm});
            skLineSegment(sketch, "E6500", {"start": v(9134.23, 703.92) * mm, "end": v(9133.77, 705.1) * mm});
            skLineSegment(sketch, "E6501", {"start": v(9133.77, 705.1) * mm, "end": v(9066.8, 863.66) * mm});
            skLineSegment(sketch, "E6502", {"start": v(9066.8, 863.66) * mm, "end": v(9309.97, 997.1) * mm});
            skLineSegment(sketch, "E6503", {"start": v(9309.97, 997.1) * mm, "end": v(9407.74, 855.46) * mm});
            skLineSegment(sketch, "E6504", {"start": v(9407.74, 855.46) * mm, "end": v(9408.5, 854.44) * mm});
            skLineSegment(sketch, "E6505", {"start": v(9408.5, 854.44) * mm, "end": v(9409.96, 852.57) * mm});
            skLineSegment(sketch, "E6506", {"start": v(9409.96, 852.57) * mm, "end": v(9412.17, 849.89) * mm});
            skLineSegment(sketch, "E6507", {"start": v(9412.17, 849.89) * mm, "end": v(9415.18, 846.43) * mm});
            skLineSegment(sketch, "E6508", {"start": v(9415.18, 846.43) * mm, "end": v(9419.02, 842.24) * mm});
            skLineSegment(sketch, "E6509", {"start": v(9419.02, 842.24) * mm, "end": v(9423.75, 837.37) * mm});
            skLineSegment(sketch, "E6510", {"start": v(9423.75, 837.37) * mm, "end": v(9429.39, 831.85) * mm});
            skLineSegment(sketch, "E6511", {"start": v(9429.39, 831.85) * mm, "end": v(9435.98, 825.74) * mm});
            skLineSegment(sketch, "E6512", {"start": v(9435.98, 825.74) * mm, "end": v(9443.57, 819.07) * mm});
            skLineSegment(sketch, "E6513", {"start": v(9443.57, 819.07) * mm, "end": v(9452.18, 811.9) * mm});
            skLineSegment(sketch, "E6514", {"start": v(9452.18, 811.9) * mm, "end": v(9461.85, 804.3) * mm});
            skLineSegment(sketch, "E6515", {"start": v(9461.85, 804.3) * mm, "end": v(9472.6, 796.29) * mm});
            skLineSegment(sketch, "E6516", {"start": v(9472.6, 796.29) * mm, "end": v(9484.47, 787.93) * mm});
            skLineSegment(sketch, "E6517", {"start": v(9484.47, 787.93) * mm, "end": v(9497.48, 779.29) * mm});
            skLineSegment(sketch, "E6518", {"start": v(9497.48, 779.29) * mm, "end": v(9511.65, 770.41) * mm});
            skLineSegment(sketch, "E6519", {"start": v(9511.65, 770.41) * mm, "end": v(9527, 761.36) * mm});
            skLineSegment(sketch, "E6520", {"start": v(9527, 761.36) * mm, "end": v(9543.56, 752.18) * mm});
            skLineSegment(sketch, "E6521", {"start": v(9543.56, 752.18) * mm, "end": v(9561.33, 742.95) * mm});
            skLineSegment(sketch, "E6522", {"start": v(9561.33, 742.95) * mm, "end": v(9580.34, 733.71) * mm});
            skLineSegment(sketch, "E6523", {"start": v(9580.34, 733.71) * mm, "end": v(9600.6, 724.53) * mm});
            skLineSegment(sketch, "E6524", {"start": v(9600.6, 724.53) * mm, "end": v(9622.1, 715.47) * mm});
            skLineSegment(sketch, "E6525", {"start": v(9622.1, 715.47) * mm, "end": v(9644.88, 706.6) * mm});
            skLineSegment(sketch, "E6526", {"start": v(9644.88, 706.6) * mm, "end": v(9668.93, 697.95) * mm});
            skLineSegment(sketch, "E6527", {"start": v(9668.93, 697.95) * mm, "end": v(9694.24, 689.61) * mm});
            skLineSegment(sketch, "E6528", {"start": v(9694.24, 689.61) * mm, "end": v(9720.83, 681.65) * mm});
            skLineSegment(sketch, "E6529", {"start": v(9720.83, 681.65) * mm, "end": v(9748.69, 674.1) * mm});
            skLineSegment(sketch, "E6530", {"start": v(9748.69, 674.1) * mm, "end": v(9776.8, 668.23) * mm});
            skLineSegment(sketch, "E6531", {"start": v(9776.8, 668.23) * mm, "end": v(9876.7, 760.1) * mm});
            skLineSegment(sketch, "E6532", {"start": v(9876.7, 760.1) * mm, "end": v(9873.2, 788.6) * mm});
            skLineSegment(sketch, "E6533", {"start": v(9873.2, 788.6) * mm, "end": v(9868, 817) * mm});
            skLineSegment(sketch, "E6534", {"start": v(9868, 817) * mm, "end": v(9862.28, 844.16) * mm});
            skLineSegment(sketch, "E6535", {"start": v(9862.28, 844.16) * mm, "end": v(9856.1, 870.08) * mm});
            skLineSegment(sketch, "E6536", {"start": v(9856.1, 870.08) * mm, "end": v(9849.5, 894.76) * mm});
            skLineSegment(sketch, "E6537", {"start": v(9849.5, 894.76) * mm, "end": v(9842.55, 918.2) * mm});
            skLineSegment(sketch, "E6538", {"start": v(9842.55, 918.2) * mm, "end": v(9835.31, 940.4) * mm});
            skLineSegment(sketch, "E6539", {"start": v(9835.31, 940.4) * mm, "end": v(9827.86, 961.35) * mm});
            skLineSegment(sketch, "E6540", {"start": v(9827.86, 961.35) * mm, "end": v(9820.24, 981.06) * mm});
            skLineSegment(sketch, "E6541", {"start": v(9820.24, 981.06) * mm, "end": v(9812.53, 999.55) * mm});
            skLineSegment(sketch, "E6542", {"start": v(9812.53, 999.55) * mm, "end": v(9804.77, 1016.8) * mm});
            skLineSegment(sketch, "E6543", {"start": v(9804.77, 1016.8) * mm, "end": v(9797.03, 1032.87) * mm});
            skLineSegment(sketch, "E6544", {"start": v(9797.03, 1032.87) * mm, "end": v(9789.36, 1047.73) * mm});
            skLineSegment(sketch, "E6545", {"start": v(9789.36, 1047.73) * mm, "end": v(9781.84, 1061.41) * mm});
            skLineSegment(sketch, "E6546", {"start": v(9781.84, 1061.41) * mm, "end": v(9774.5, 1073.93) * mm});
            skLineSegment(sketch, "E6547", {"start": v(9774.5, 1073.93) * mm, "end": v(9767.42, 1085.32) * mm});
            skLineSegment(sketch, "E6548", {"start": v(9767.42, 1085.32) * mm, "end": v(9760.64, 1095.59) * mm});
            skLineSegment(sketch, "E6549", {"start": v(9760.64, 1095.59) * mm, "end": v(9754.22, 1104.77) * mm});
            skLineSegment(sketch, "E6550", {"start": v(9754.22, 1104.77) * mm, "end": v(9748.22, 1112.89) * mm});
            skLineSegment(sketch, "E6551", {"start": v(9748.22, 1112.89) * mm, "end": v(9742.67, 1119.97) * mm});
            skLineSegment(sketch, "E6552", {"start": v(9742.67, 1119.97) * mm, "end": v(9737.65, 1126.05) * mm});
            skLineSegment(sketch, "E6553", {"start": v(9737.65, 1126.05) * mm, "end": v(9733.18, 1131.17) * mm});
            skLineSegment(sketch, "E6554", {"start": v(9733.18, 1131.17) * mm, "end": v(9729.33, 1135.35) * mm});
            skLineSegment(sketch, "E6555", {"start": v(9729.33, 1135.35) * mm, "end": v(9726.14, 1138.63) * mm});
            skLineSegment(sketch, "E6556", {"start": v(9726.14, 1138.63) * mm, "end": v(9723.65, 1141.06) * mm});
            skLineSegment(sketch, "E6557", {"start": v(9723.65, 1141.06) * mm, "end": v(9721.91, 1142.67) * mm});
            skLineSegment(sketch, "E6558", {"start": v(9721.91, 1142.67) * mm, "end": v(9720.96, 1143.5) * mm});
            skLineSegment(sketch, "E6559", {"start": v(9720.96, 1143.5) * mm, "end": v(9587.98, 1252.78) * mm});
            skLineSegment(sketch, "E6560", {"start": v(9587.98, 1252.78) * mm, "end": v(9741.28, 1483.94) * mm});
            skLineSegment(sketch, "E6561", {"start": v(9741.28, 1483.94) * mm, "end": v(9893.68, 1403.96) * mm});
            skLineSegment(sketch, "E6562", {"start": v(9893.68, 1403.96) * mm, "end": v(9894.82, 1403.4) * mm});
            skLineSegment(sketch, "E6563", {"start": v(9894.82, 1403.4) * mm, "end": v(9896.98, 1402.43) * mm});
            skLineSegment(sketch, "E6564", {"start": v(9896.98, 1402.43) * mm, "end": v(9900.18, 1401.09) * mm});
            skLineSegment(sketch, "E6565", {"start": v(9900.18, 1401.09) * mm, "end": v(9904.45, 1399.42) * mm});
            skLineSegment(sketch, "E6566", {"start": v(9904.45, 1399.42) * mm, "end": v(9909.8, 1397.5) * mm});
            skLineSegment(sketch, "E6567", {"start": v(9909.8, 1397.5) * mm, "end": v(9916.25, 1395.38) * mm});
            skLineSegment(sketch, "E6568", {"start": v(9916.25, 1395.38) * mm, "end": v(9923.8, 1393.12) * mm});
            skLineSegment(sketch, "E6569", {"start": v(9923.8, 1393.12) * mm, "end": v(9932.5, 1390.77) * mm});
            skLineSegment(sketch, "E6570", {"start": v(9932.5, 1390.77) * mm, "end": v(9942.3, 1388.4) * mm});
            skLineSegment(sketch, "E6571", {"start": v(9942.3, 1388.4) * mm, "end": v(9953.26, 1386.05) * mm});
            skLineSegment(sketch, "E6572", {"start": v(9953.26, 1386.05) * mm, "end": v(9965.36, 1383.8) * mm});
            skLineSegment(sketch, "E6573", {"start": v(9965.36, 1383.8) * mm, "end": v(9978.6, 1381.7) * mm});
            skLineSegment(sketch, "E6574", {"start": v(9978.6, 1381.7) * mm, "end": v(9993, 1379.83) * mm});
            skLineSegment(sketch, "E6575", {"start": v(9993, 1379.83) * mm, "end": v(10008.53, 1378.22) * mm});
            skLineSegment(sketch, "E6576", {"start": v(10008.53, 1378.22) * mm, "end": v(10025.2, 1376.94) * mm});
            skLineSegment(sketch, "E6577", {"start": v(10025.2, 1376.94) * mm, "end": v(10043, 1376.06) * mm});
            skLineSegment(sketch, "E6578", {"start": v(10043, 1376.06) * mm, "end": v(10061.92, 1375.63) * mm});
            skLineSegment(sketch, "E6579", {"start": v(10061.92, 1375.63) * mm, "end": v(10081.95, 1375.71) * mm});
            skLineSegment(sketch, "E6580", {"start": v(10081.95, 1375.71) * mm, "end": v(10103.08, 1376.37) * mm});
            skLineSegment(sketch, "E6581", {"start": v(10103.08, 1376.37) * mm, "end": v(10125.28, 1377.65) * mm});
            skLineSegment(sketch, "E6582", {"start": v(10125.28, 1377.65) * mm, "end": v(10148.54, 1379.63) * mm});
            skLineSegment(sketch, "E6583", {"start": v(10148.54, 1379.63) * mm, "end": v(10172.83, 1382.35) * mm});
            skLineSegment(sketch, "E6584", {"start": v(10172.83, 1382.35) * mm, "end": v(10198.14, 1385.87) * mm});
            skLineSegment(sketch, "E6585", {"start": v(10198.14, 1385.87) * mm, "end": v(10224.43, 1390.26) * mm});
            skLineSegment(sketch, "E6586", {"start": v(10224.43, 1390.26) * mm, "end": v(10251.67, 1395.56) * mm});
            skLineSegment(sketch, "E6587", {"start": v(10251.67, 1395.56) * mm, "end": v(10279.84, 1401.82) * mm});
            skLineSegment(sketch, "E6588", {"start": v(10279.84, 1401.82) * mm, "end": v(10307.47, 1409.69) * mm});
            skLineSegment(sketch, "E6589", {"start": v(10307.47, 1409.69) * mm, "end": v(10353.23, 1537.46) * mm});
            skLineSegment(sketch, "E6590", {"start": v(10353.23, 1537.46) * mm, "end": v(10336.88, 1561.07) * mm});
            skLineSegment(sketch, "E6591", {"start": v(10336.88, 1561.07) * mm, "end": v(10319.09, 1583.8) * mm});
            skLineSegment(sketch, "E6592", {"start": v(10319.09, 1583.8) * mm, "end": v(10301.4, 1605.2) * mm});
            skLineSegment(sketch, "E6593", {"start": v(10301.4, 1605.2) * mm, "end": v(10283.87, 1625.27) * mm});
            skLineSegment(sketch, "E6594", {"start": v(10283.87, 1625.27) * mm, "end": v(10266.56, 1644.06) * mm});
            skLineSegment(sketch, "E6595", {"start": v(10266.56, 1644.06) * mm, "end": v(10249.51, 1661.58) * mm});
            skLineSegment(sketch, "E6596", {"start": v(10249.51, 1661.58) * mm, "end": v(10232.8, 1677.87) * mm});
            skLineSegment(sketch, "E6597", {"start": v(10232.8, 1677.87) * mm, "end": v(10216.46, 1692.96) * mm});
            skLineSegment(sketch, "E6598", {"start": v(10216.46, 1692.96) * mm, "end": v(10200.55, 1706.87) * mm});
            skLineSegment(sketch, "E6599", {"start": v(10200.55, 1706.87) * mm, "end": v(10185.13, 1719.66) * mm});
            skLineSegment(sketch, "E6600", {"start": v(10185.13, 1719.66) * mm, "end": v(10170.24, 1731.34) * mm});
            skLineSegment(sketch, "E6601", {"start": v(10170.24, 1731.34) * mm, "end": v(10155.92, 1741.96) * mm});
            skLineSegment(sketch, "E6602", {"start": v(10155.92, 1741.96) * mm, "end": v(10142.23, 1751.55) * mm});
            skLineSegment(sketch, "E6603", {"start": v(10142.23, 1751.55) * mm, "end": v(10129.2, 1760.17) * mm});
            skLineSegment(sketch, "E6604", {"start": v(10129.2, 1760.17) * mm, "end": v(10116.9, 1767.85) * mm});
            skLineSegment(sketch, "E6605", {"start": v(10116.9, 1767.85) * mm, "end": v(10105.33, 1774.64) * mm});
            skLineSegment(sketch, "E6606", {"start": v(10105.33, 1774.64) * mm, "end": v(10094.55, 1780.59) * mm});
            skLineSegment(sketch, "E6607", {"start": v(10094.55, 1780.59) * mm, "end": v(10084.6, 1785.73) * mm});
            skLineSegment(sketch, "E6608", {"start": v(10084.6, 1785.73) * mm, "end": v(10075.51, 1790.13) * mm});
            skLineSegment(sketch, "E6609", {"start": v(10075.51, 1790.13) * mm, "end": v(10067.31, 1793.82) * mm});
            skLineSegment(sketch, "E6610", {"start": v(10067.31, 1793.82) * mm, "end": v(10060.04, 1796.87) * mm});
            skLineSegment(sketch, "E6611", {"start": v(10060.04, 1796.87) * mm, "end": v(10053.7, 1799.33) * mm});
            skLineSegment(sketch, "E6612", {"start": v(10053.7, 1799.33) * mm, "end": v(10048.36, 1801.24) * mm});
            skLineSegment(sketch, "E6613", {"start": v(10048.36, 1801.24) * mm, "end": v(10044, 1802.67) * mm});
            skLineSegment(sketch, "E6614", {"start": v(10044, 1802.67) * mm, "end": v(10040.67, 1803.66) * mm});
            skLineSegment(sketch, "E6615", {"start": v(10040.67, 1803.66) * mm, "end": v(10038.38, 1804.28) * mm});
            skLineSegment(sketch, "E6616", {"start": v(10038.38, 1804.28) * mm, "end": v(10037.15, 1804.58) * mm});
            skLineSegment(sketch, "E6617", {"start": v(10037.15, 1804.58) * mm, "end": v(9868.62, 1839.53) * mm});
            skLineSegment(sketch, "E6618", {"start": v(9868.62, 1839.53) * mm, "end": v(9896.93, 2115.46) * mm});
            skLineSegment(sketch, "E6619", {"start": v(9896.93, 2115.46) * mm, "end": v(10069.04, 2115.46) * mm});
            skLineSegment(sketch, "E6620", {"start": v(10069.04, 2115.46) * mm, "end": v(10070.31, 2115.5) * mm});
            skLineSegment(sketch, "E6621", {"start": v(10070.31, 2115.5) * mm, "end": v(10072.68, 2115.64) * mm});
            skLineSegment(sketch, "E6622", {"start": v(8741.23, 2115.46) * mm, "end": v(8334.83, 2115.46) * mm});
            skFitSpline(sketch, "E6623", {"points": [v(10272.7, 2344.9) * mm, v(10272.7, 2289.84) * mm, v(10228.07, 2245.2) * mm, v(10173, 2245.2) * mm]});
            skFitSpline(sketch, "E6624", {"points": [v(10173, 2245.2) * mm, v(10117.95, 2245.2) * mm, v(10073.31, 2289.84) * mm, v(10073.31, 2344.9) * mm]});
            skFitSpline(sketch, "E6625", {"points": [v(10073.31, 2344.9) * mm, v(10073.31, 2399.96) * mm, v(10117.95, 2444.6) * mm, v(10173, 2444.6) * mm]});
            skFitSpline(sketch, "E6626", {"points": [v(10173, 2444.6) * mm, v(10228.07, 2444.6) * mm, v(10272.7, 2399.96) * mm, v(10272.7, 2344.9) * mm]});
            skLineSegment(sketch, "E6627", {"start": v(8538.03, 1912.26) * mm, "end": v(8538.03, 2318.66) * mm});
            skLineSegment(sketch, "E6628", {"start": v(7871.53, 2932.12) * mm, "end": v(7848.16, 2912.4) * mm});
            skLineSegment(sketch, "E6629", {"start": v(7848.16, 2912.4) * mm, "end": v(7825.4, 2892.09) * mm});
            skLineSegment(sketch, "E6630", {"start": v(7825.4, 2892.09) * mm, "end": v(7803.26, 2871.16) * mm});
            skLineSegment(sketch, "E6631", {"start": v(7803.26, 2871.16) * mm, "end": v(7781.72, 2849.62) * mm});
            skLineSegment(sketch, "E6632", {"start": v(7866.66, 2847.18) * mm, "end": v(7784.16, 2937) * mm});
            skLineSegment(sketch, "E6633", {"start": v(7832.92, 2979.26) * mm, "end": v(7828.25, 2935.37) * mm});
            skLineSegment(sketch, "E6634", {"start": v(7828.25, 2935.37) * mm, "end": v(7825.4, 2892.09) * mm});
            skLineSegment(sketch, "E6635", {"start": v(7825.4, 2892.09) * mm, "end": v(7824.4, 2849.42) * mm});
            skLineSegment(sketch, "E6636", {"start": v(7824.4, 2849.42) * mm, "end": v(7825.4, 2807.15) * mm});
            skLineSegment(sketch, "E6637", {"start": v(7909.94, 2884.77) * mm, "end": v(7868.08, 2889.45) * mm});
            skLineSegment(sketch, "E6638", {"start": v(7868.08, 2889.45) * mm, "end": v(7825.4, 2892.09) * mm});
            skLineSegment(sketch, "E6639", {"start": v(7825.4, 2892.09) * mm, "end": v(7781.92, 2893.1) * mm});
            skLineSegment(sketch, "E6640", {"start": v(7781.92, 2893.1) * mm, "end": v(7737.83, 2892.09) * mm});
            skLineSegment(sketch, "E6641", {"start": v(8067.21, 2955.08) * mm, "end": v(8043.03, 2941.06) * mm});
            skLineSegment(sketch, "E6642", {"start": v(8043.03, 2941.06) * mm, "end": v(8019.46, 2926.43) * mm});
            skLineSegment(sketch, "E6643", {"start": v(8019.46, 2926.43) * mm, "end": v(7996.1, 2911.19) * mm});
            skLineSegment(sketch, "E6644", {"start": v(7996.1, 2911.19) * mm, "end": v(7973.34, 2895.14) * mm});
            skLineSegment(sketch, "E6645", {"start": v(7973.34, 2895.14) * mm, "end": v(7937.57, 2944.51) * mm});
            skLineSegment(sketch, "E6646", {"start": v(7937.57, 2944.51) * mm, "end": v(7944.68, 2986.78) * mm});
            skLineSegment(sketch, "E6647", {"start": v(7944.68, 2986.78) * mm, "end": v(7970.08, 3003.44) * mm});
            skLineSegment(sketch, "E6648", {"start": v(7970.08, 3003.44) * mm, "end": v(7996.1, 3019.5) * mm});
            skLineSegment(sketch, "E6649", {"start": v(7996.1, 3019.5) * mm, "end": v(8007.47, 3061.35) * mm});
            skLineSegment(sketch, "E6650", {"start": v(8007.47, 3061.35) * mm, "end": v(7992.64, 3087.97) * mm});
            skLineSegment(sketch, "E6651", {"start": v(7992.64, 3087.97) * mm, "end": v(7948.95, 3097.93) * mm});
            skLineSegment(sketch, "E6652", {"start": v(7948.95, 3097.93) * mm, "end": v(7920.91, 3080.45) * mm});
            skLineSegment(sketch, "E6653", {"start": v(7920.91, 3080.45) * mm, "end": v(7893.27, 3062.37) * mm});
            skLineSegment(sketch, "E6654", {"start": v(7893.27, 3062.37) * mm, "end": v(7883.93, 3018.48) * mm});
            skLineSegment(sketch, "E6655", {"start": v(8318.17, 3239.76) * mm, "end": v(8353.32, 3060.13) * mm});
            skLineSegment(sketch, "E6656", {"start": v(8353.32, 3060.13) * mm, "end": v(8315.93, 3099.15) * mm});
            skLineSegment(sketch, "E6657", {"start": v(8315.93, 3099.15) * mm, "end": v(8276.3, 3136.54) * mm});
            skLineSegment(sketch, "E6658", {"start": v(8276.3, 3136.54) * mm, "end": v(8234.24, 3172.5) * mm});
            skLineSegment(sketch, "E6659", {"start": v(8234.24, 3172.5) * mm, "end": v(8189.95, 3206.84) * mm});
            skLineSegment(sketch, "E6660", {"start": v(8189.95, 3206.84) * mm, "end": v(8245.62, 3032.7) * mm});
            skLineSegment(sketch, "E6661", {"start": v(8516.9, 3199.73) * mm, "end": v(8485.4, 3198.72) * mm});
            skLineSegment(sketch, "E6662", {"start": v(8485.4, 3198.72) * mm, "end": v(8454.1, 3196.89) * mm});
            skLineSegment(sketch, "E6663", {"start": v(8454.1, 3196.89) * mm, "end": v(8423.02, 3193.84) * mm});
            skLineSegment(sketch, "E6664", {"start": v(8423.02, 3193.84) * mm, "end": v(8391.72, 3190.18) * mm});
            skLineSegment(sketch, "E6665", {"start": v(8517.91, 3138.98) * mm, "end": v(8488.45, 3137.96) * mm});
            skLineSegment(sketch, "E6666", {"start": v(8488.45, 3137.96) * mm, "end": v(8458.98, 3135.93) * mm});
            skLineSegment(sketch, "E6667", {"start": v(8458.98, 3135.93) * mm, "end": v(8429.32, 3133.29) * mm});
            skLineSegment(sketch, "E6668", {"start": v(8429.32, 3133.29) * mm, "end": v(8400.06, 3129.83) * mm});
            skLineSegment(sketch, "E6669", {"start": v(8580.7, 3229.6) * mm, "end": v(8614.84, 3258.46) * mm});
            skLineSegment(sketch, "E6670", {"start": v(8614.84, 3258.46) * mm, "end": v(8602.65, 3075.98) * mm});
            skLineSegment(sketch, "E6671", {"start": v(8630.48, 3073.75) * mm, "end": v(8602.65, 3075.98) * mm});
            skLineSegment(sketch, "E6672", {"start": v(8602.65, 3075.98) * mm, "end": v(8574.8, 3077.4) * mm});
            skLineSegment(sketch, "E6673", {"start": v(8708.92, 3217.41) * mm, "end": v(8746.3, 3242) * mm});
            skLineSegment(sketch, "E6674", {"start": v(8746.3, 3242) * mm, "end": v(8778.82, 3235.5) * mm});
            skLineSegment(sketch, "E6675", {"start": v(8778.82, 3235.5) * mm, "end": v(8811.13, 3227.98) * mm});
            skLineSegment(sketch, "E6676", {"start": v(8811.13, 3227.98) * mm, "end": v(8835.1, 3190.18) * mm});
            skLineSegment(sketch, "E6677", {"start": v(8835.1, 3190.18) * mm, "end": v(8826.98, 3160.92) * mm});
            skLineSegment(sketch, "E6678", {"start": v(8826.98, 3160.92) * mm, "end": v(8789.18, 3139.18) * mm});
            skLineSegment(sketch, "E6679", {"start": v(8789.18, 3139.18) * mm, "end": v(8810.72, 3102.2) * mm});
            skLineSegment(sketch, "E6680", {"start": v(8810.72, 3102.2) * mm, "end": v(8802.6, 3072.73) * mm});
            skLineSegment(sketch, "E6681", {"start": v(8802.6, 3072.73) * mm, "end": v(8767.44, 3050.38) * mm});
            skLineSegment(sketch, "E6682", {"start": v(8767.44, 3050.38) * mm, "end": v(8740.42, 3056.68) * mm});
            skLineSegment(sketch, "E6683", {"start": v(8740.42, 3056.68) * mm, "end": v(8712.98, 3062.17) * mm});
            skLineSegment(sketch, "E6684", {"start": v(8712.98, 3062.17) * mm, "end": v(8690.23, 3096.91) * mm});
            skLineSegment(sketch, "E6685", {"start": v(8759.52, 3146.09) * mm, "end": v(8789.18, 3139.18) * mm});
            skLineSegment(sketch, "E6686", {"start": v(9017.38, 3054.24) * mm, "end": v(9044.2, 3040.02) * mm});
            skLineSegment(sketch, "E6687", {"start": v(9044.2, 3040.02) * mm, "end": v(9070.82, 3024.98) * mm});
            skLineSegment(sketch, "E6688", {"start": v(9070.82, 3024.98) * mm, "end": v(9096.83, 3009.33) * mm});
            skLineSegment(sketch, "E6689", {"start": v(9096.83, 3009.33) * mm, "end": v(9139.3, 3018.07) * mm});
            skLineSegment(sketch, "E6690", {"start": v(9139.3, 3018.07) * mm, "end": v(9156.16, 3043.47) * mm});
            skLineSegment(sketch, "E6691", {"start": v(9156.16, 3043.47) * mm, "end": v(9145.4, 3086.75) * mm});
            skLineSegment(sketch, "E6692", {"start": v(9145.4, 3086.75) * mm, "end": v(9116.95, 3104.03) * mm});
            skLineSegment(sketch, "E6693", {"start": v(9116.95, 3104.03) * mm, "end": v(9088.1, 3120.28) * mm});
            skLineSegment(sketch, "E6694", {"start": v(9088.1, 3120.28) * mm, "end": v(9058.83, 3135.72) * mm});
            skLineSegment(sketch, "E6695", {"start": v(9058.83, 3135.72) * mm, "end": v(8975.72, 2972.96) * mm});
            skLineSegment(sketch, "E6696", {"start": v(9117.15, 2884.37) * mm, "end": v(9190.5, 2981.9) * mm});
            skLineSegment(sketch, "E6697", {"start": v(9208.8, 3006.08) * mm, "end": v(9227.08, 3030.47) * mm});
            skLineSegment(sketch, "E6698", {"start": v(9263.45, 2793.74) * mm, "end": v(9222, 2792.93) * mm});
            skLineSegment(sketch, "E6699", {"start": v(9222, 2792.93) * mm, "end": v(9223.02, 2834.58) * mm});
            skLineSegment(sketch, "E6700", {"start": v(9223.02, 2834.58) * mm, "end": v(9328.27, 2944.92) * mm});
            skLineSegment(sketch, "E6701", {"start": v(9330.3, 2856.12) * mm, "end": v(9308.56, 2878.68) * mm});
            skLineSegment(sketch, "E6702", {"start": v(9308.56, 2878.68) * mm, "end": v(9286.21, 2900.83) * mm});
            skLineSegment(sketch, "E6703", {"start": v(9286.21, 2900.83) * mm, "end": v(9263.05, 2921.96) * mm});
            skLineSegment(sketch, "E6704", {"start": v(9263.05, 2921.96) * mm, "end": v(9239.47, 2942.68) * mm});
            skLineSegment(sketch, "E6705", {"start": v(9344.12, 2641.75) * mm, "end": v(9328.68, 2664.7) * mm});
            skLineSegment(sketch, "E6706", {"start": v(9328.68, 2664.7) * mm, "end": v(9312.42, 2687.47) * mm});
            skLineSegment(sketch, "E6707", {"start": v(9312.42, 2687.47) * mm, "end": v(9295.56, 2709.61) * mm});
            skLineSegment(sketch, "E6708", {"start": v(9295.56, 2709.61) * mm, "end": v(9301.45, 2750.66) * mm});
            skLineSegment(sketch, "E6709", {"start": v(9301.45, 2750.66) * mm, "end": v(9348.4, 2789.67) * mm});
            skLineSegment(sketch, "E6710", {"start": v(9348.4, 2789.67) * mm, "end": v(9391.47, 2784.8) * mm});
            skLineSegment(sketch, "E6711", {"start": v(9391.47, 2784.8) * mm, "end": v(9410.37, 2759.8) * mm});
            skLineSegment(sketch, "E6712", {"start": v(9410.37, 2759.8) * mm, "end": v(9428.65, 2734.4) * mm});
            skLineSegment(sketch, "E6713", {"start": v(9428.65, 2734.4) * mm, "end": v(9446.33, 2708.4) * mm});
            skLineSegment(sketch, "E6714", {"start": v(9426.01, 2624.47) * mm, "end": v(9467.26, 2613.1) * mm});
            skLineSegment(sketch, "E6715", {"start": v(9467.26, 2613.1) * mm, "end": v(9508.51, 2599.48) * mm});
            skLineSegment(sketch, "E6716", {"start": v(9508.51, 2599.48) * mm, "end": v(9522.13, 2571.23) * mm});
            skLineSegment(sketch, "E6717", {"start": v(9522.13, 2571.23) * mm, "end": v(9506.89, 2530.6) * mm});
            skLineSegment(sketch, "E6718", {"start": v(9506.89, 2530.6) * mm, "end": v(9422.96, 2494.63) * mm});
            skLineSegment(sketch, "E6719", {"start": v(9373.18, 2594.2) * mm, "end": v(9531.88, 2685.23) * mm});
            skLineSegment(sketch, "E6720", {"start": v(9481.08, 2308.9) * mm, "end": v(9486.16, 2281.67) * mm});
            skLineSegment(sketch, "E6721", {"start": v(9486.16, 2281.67) * mm, "end": v(9490.63, 2254.24) * mm});
            skLineSegment(sketch, "E6722", {"start": v(9490.63, 2254.24) * mm, "end": v(9494.29, 2226.6) * mm});
            skLineSegment(sketch, "E6723", {"start": v(9494.29, 2226.6) * mm, "end": v(9527.4, 2201.41) * mm});
            skLineSegment(sketch, "E6724", {"start": v(9527.4, 2201.41) * mm, "end": v(9648.92, 2211.98) * mm});
            skLineSegment(sketch, "E6725", {"start": v(9648.92, 2211.98) * mm, "end": v(9675.95, 2247.74) * mm});
            skLineSegment(sketch, "E6726", {"start": v(9675.95, 2247.74) * mm, "end": v(9671.68, 2280.46) * mm});
            skLineSegment(sketch, "E6727", {"start": v(9671.68, 2280.46) * mm, "end": v(9666.4, 2313.17) * mm});
            skLineSegment(sketch, "E6728", {"start": v(9666.4, 2313.17) * mm, "end": v(9660.1, 2345.68) * mm});
            skLineSegment(sketch, "E6729", {"start": v(9666.4, 2313.17) * mm, "end": v(9486.16, 2281.67) * mm});
            skLineSegment(sketch, "E6730", {"start": v(9618.44, 2021.58) * mm, "end": v(9620.88, 2052.67) * mm});
            skLineSegment(sketch, "E6731", {"start": v(9620.88, 2052.67) * mm, "end": v(9622.1, 2084.16) * mm});
            skLineSegment(sketch, "E6732", {"start": v(9622.1, 2084.16) * mm, "end": v(9622.5, 2115.46) * mm});
            skLineSegment(sketch, "E6733", {"start": v(9622.5, 2115.46) * mm, "end": v(9622.1, 2146.75) * mm});
            skLineSegment(sketch, "E6734", {"start": v(9557.89, 2026.86) * mm, "end": v(9559.92, 2056.33) * mm});
            skLineSegment(sketch, "E6735", {"start": v(9559.92, 2056.33) * mm, "end": v(9561.14, 2085.79) * mm});
            skLineSegment(sketch, "E6736", {"start": v(9561.14, 2085.79) * mm, "end": v(9561.55, 2115.46) * mm});
            skLineSegment(sketch, "E6737", {"start": v(9561.55, 2115.46) * mm, "end": v(9561.14, 2145.12) * mm});
            skLineSegment(sketch, "E6738", {"start": v(9641.4, 1954.73) * mm, "end": v(9666.4, 1917.74) * mm});
            skLineSegment(sketch, "E6739", {"start": v(9666.4, 1917.74) * mm, "end": v(9660.1, 1885.23) * mm});
            skLineSegment(sketch, "E6740", {"start": v(9660.1, 1885.23) * mm, "end": v(9652.99, 1852.92) * mm});
            skLineSegment(sketch, "E6741", {"start": v(9652.99, 1852.92) * mm, "end": v(9615.6, 1828.54) * mm});
            skLineSegment(sketch, "E6742", {"start": v(9615.6, 1828.54) * mm, "end": v(9586.13, 1836.46) * mm});
            skLineSegment(sketch, "E6743", {"start": v(9586.13, 1836.46) * mm, "end": v(9563.99, 1873.85) * mm});
            skLineSegment(sketch, "E6744", {"start": v(9563.99, 1873.85) * mm, "end": v(9527.2, 1852.1) * mm});
            skLineSegment(sketch, "E6745", {"start": v(9527.2, 1852.1) * mm, "end": v(9497.74, 1859.83) * mm});
            skLineSegment(sketch, "E6746", {"start": v(9497.74, 1859.83) * mm, "end": v(9474.98, 1894.78) * mm});
            skLineSegment(sketch, "E6747", {"start": v(9474.98, 1894.78) * mm, "end": v(9481.08, 1922.01) * mm});
            skLineSegment(sketch, "E6748", {"start": v(9481.08, 1922.01) * mm, "end": v(9486.16, 1949.24) * mm});
            skLineSegment(sketch, "E6749", {"start": v(9486.16, 1949.24) * mm, "end": v(9520.9, 1972.4) * mm});
            skLineSegment(sketch, "E6750", {"start": v(9570.7, 1903.52) * mm, "end": v(9563.99, 1873.85) * mm});
            skLineSegment(sketch, "E6751", {"start": v(9481.28, 1804.97) * mm, "end": v(9452.43, 1814.31) * mm});
            skLineSegment(sketch, "E6752", {"start": v(9386.8, 1661.1) * mm, "end": v(9399.4, 1685.9) * mm});
            skLineSegment(sketch, "E6753", {"start": v(9399.4, 1685.9) * mm, "end": v(9411.59, 1710.89) * mm});
            skLineSegment(sketch, "E6754", {"start": v(9411.59, 1710.89) * mm, "end": v(9422.96, 1736.29) * mm});
            skLineSegment(sketch, "E6755", {"start": v(9422.96, 1736.29) * mm, "end": v(9433.53, 1762.1) * mm});
            skLineSegment(sketch, "E6756", {"start": v(9433.53, 1762.1) * mm, "end": v(9490.22, 1739.74) * mm});
            skLineSegment(sketch, "E6757", {"start": v(9490.22, 1739.74) * mm, "end": v(9506.89, 1700.32) * mm});
            skLineSegment(sketch, "E6758", {"start": v(9506.89, 1700.32) * mm, "end": v(9494.5, 1672.48) * mm});
            skLineSegment(sketch, "E6759", {"start": v(9494.5, 1672.48) * mm, "end": v(9481.28, 1645.05) * mm});
            skLineSegment(sketch, "E6760", {"start": v(9481.28, 1645.05) * mm, "end": v(9494.29, 1603.6) * mm});
            skLineSegment(sketch, "E6761", {"start": v(9494.29, 1603.6) * mm, "end": v(9521.11, 1589.17) * mm});
            skLineSegment(sketch, "E6762", {"start": v(9521.11, 1589.17) * mm, "end": v(9563.17, 1604.2) * mm});
            skLineSegment(sketch, "E6763", {"start": v(9563.17, 1604.2) * mm, "end": v(9577.4, 1634.08) * mm});
            skLineSegment(sketch, "E6764", {"start": v(9577.4, 1634.08) * mm, "end": v(9591.01, 1664.35) * mm});
            skLineSegment(sketch, "E6765", {"start": v(9591.01, 1664.35) * mm, "end": v(9575.16, 1706) * mm});
            skLineSegment(sketch, "E6766", {"start": v(9439.42, 1408.52) * mm, "end": v(9459.54, 1434.94) * mm});
            skLineSegment(sketch, "E6767", {"start": v(9459.54, 1434.94) * mm, "end": v(9478.84, 1461.76) * mm});
            skLineSegment(sketch, "E6768", {"start": v(9478.84, 1461.76) * mm, "end": v(9497.34, 1489.2) * mm});
            skLineSegment(sketch, "E6769", {"start": v(9497.34, 1489.2) * mm, "end": v(9515.01, 1517.24) * mm});
            skLineSegment(sketch, "E6770", {"start": v(9515.01, 1517.24) * mm, "end": v(9463, 1549.14) * mm});
            skLineSegment(sketch, "E6771", {"start": v(9463, 1549.14) * mm, "end": v(9446.33, 1522.52) * mm});
            skLineSegment(sketch, "E6772", {"start": v(9446.33, 1522.52) * mm, "end": v(9428.65, 1496.5) * mm});
            skLineSegment(sketch, "E6773", {"start": v(9428.65, 1496.5) * mm, "end": v(9410.37, 1471.1) * mm});
            skLineSegment(sketch, "E6774", {"start": v(9410.37, 1471.1) * mm, "end": v(9367.5, 1465.01) * mm});
            skLineSegment(sketch, "E6775", {"start": v(9367.5, 1465.01) * mm, "end": v(9319.54, 1502.6) * mm});
            skLineSegment(sketch, "E6776", {"start": v(9319.54, 1502.6) * mm, "end": v(9312.42, 1543.45) * mm});
            skLineSegment(sketch, "E6777", {"start": v(9312.42, 1543.45) * mm, "end": v(9328.68, 1566.2) * mm});
            skLineSegment(sketch, "E6778", {"start": v(9328.68, 1566.2) * mm, "end": v(9344.12, 1589.17) * mm});
            skLineSegment(sketch, "E6779", {"start": v(9344.12, 1589.17) * mm, "end": v(9384.97, 1596.9) * mm});
            skLineSegment(sketch, "E6780", {"start": v(9219.76, 1311.6) * mm, "end": v(9196.2, 1292.1) * mm});
            skLineSegment(sketch, "E6781", {"start": v(9196.2, 1292.1) * mm, "end": v(9172.22, 1273.4) * mm});
            skLineSegment(sketch, "E6782", {"start": v(9172.22, 1273.4) * mm, "end": v(9147.63, 1255.51) * mm});
            skLineSegment(sketch, "E6783", {"start": v(9147.63, 1255.51) * mm, "end": v(9139.3, 1212.84) * mm});
            skLineSegment(sketch, "E6784", {"start": v(9139.3, 1212.84) * mm, "end": v(9156.16, 1187.44) * mm});
            skLineSegment(sketch, "E6785", {"start": v(9156.16, 1187.44) * mm, "end": v(9200.46, 1180.94) * mm});
            skLineSegment(sketch, "E6786", {"start": v(9200.46, 1180.94) * mm, "end": v(9227.08, 1200.45) * mm});
            skLineSegment(sketch, "E6787", {"start": v(9227.08, 1200.45) * mm, "end": v(9253.3, 1220.77) * mm});
            skLineSegment(sketch, "E6788", {"start": v(9253.3, 1220.77) * mm, "end": v(9278.9, 1241.7) * mm});
            skLineSegment(sketch, "E6789", {"start": v(9278.9, 1241.7) * mm, "end": v(9160.63, 1381.3) * mm});
            skLineSegment(sketch, "E6790", {"start": v(8974.5, 1122.62) * mm, "end": v(9002.95, 1135.63) * mm});
            skLineSegment(sketch, "E6791", {"start": v(9002.95, 1135.63) * mm, "end": v(9031.2, 1149.44) * mm});
            skLineSegment(sketch, "E6792", {"start": v(9031.2, 1149.44) * mm, "end": v(9058.83, 1164.07) * mm});
            skLineSegment(sketch, "E6793", {"start": v(9058.83, 1164.07) * mm, "end": v(9086.26, 1179.52) * mm});
            skLineSegment(sketch, "E6794", {"start": v(8949.91, 1178.3) * mm, "end": v(8976.94, 1190.7) * mm});
            skLineSegment(sketch, "E6795", {"start": v(8976.94, 1190.7) * mm, "end": v(9003.36, 1203.7) * mm});
            skLineSegment(sketch, "E6796", {"start": v(9003.36, 1203.7) * mm, "end": v(9029.57, 1217.52) * mm});
            skLineSegment(sketch, "E6797", {"start": v(9029.57, 1217.52) * mm, "end": v(9055.38, 1232.15) * mm});
            skLineSegment(sketch, "E6798", {"start": v(8782.07, 1121.4) * mm, "end": v(8810.72, 1128.72) * mm});
            skLineSegment(sketch, "E6799", {"start": v(8810.72, 1128.72) * mm, "end": v(8838.97, 1137.05) * mm});
            skLineSegment(sketch, "E6800", {"start": v(8838.97, 1137.05) * mm, "end": v(8867.21, 1146.2) * mm});
            skLineSegment(sketch, "E6801", {"start": v(8867.21, 1146.2) * mm, "end": v(8895.05, 1156.15) * mm});
            skLineSegment(sketch, "E6802", {"start": v(8895.05, 1156.15) * mm, "end": v(8880.22, 1107.79) * mm});
            skLineSegment(sketch, "E6803", {"start": v(8880.22, 1107.79) * mm, "end": v(8862.95, 1059.43) * mm});
            skLineSegment(sketch, "E6804", {"start": v(8862.95, 1059.43) * mm, "end": v(8843.03, 1011.27) * mm});
            skLineSegment(sketch, "E6805", {"start": v(8843.03, 1011.27) * mm, "end": v(8794.47, 1187.65) * mm});
            skLineSegment(sketch, "E6806", {"start": v(8578.26, 1062.07) * mm, "end": v(8547.99, 1061.46) * mm});
            skLineSegment(sketch, "E6807", {"start": v(8547.99, 1061.46) * mm, "end": v(8517.5, 1061.46) * mm});
            skLineSegment(sketch, "E6808", {"start": v(8517.5, 1061.46) * mm, "end": v(8487.03, 1062.68) * mm});
            skLineSegment(sketch, "E6809", {"start": v(8487.03, 1062.68) * mm, "end": v(8454.1, 1034.03) * mm});
            skLineSegment(sketch, "E6810", {"start": v(8454.1, 1034.03) * mm, "end": v(8451.87, 1003.75) * mm});
            skLineSegment(sketch, "E6811", {"start": v(8451.87, 1003.75) * mm, "end": v(8482.55, 971.24) * mm});
            skLineSegment(sketch, "E6812", {"start": v(8482.55, 971.24) * mm, "end": v(8515.68, 970.22) * mm});
            skLineSegment(sketch, "E6813", {"start": v(8515.68, 970.22) * mm, "end": v(8548.8, 970.02) * mm});
            skLineSegment(sketch, "E6814", {"start": v(8548.8, 970.02) * mm, "end": v(8581.92, 970.83) * mm});
            skLineSegment(sketch, "E6815", {"start": v(8581.92, 970.83) * mm, "end": v(8574.8, 1153.5) * mm});
            skLineSegment(sketch, "E6816", {"start": v(8408.18, 1161.64) * mm, "end": v(8400.06, 1101.08) * mm});
            skLineSegment(sketch, "E6817", {"start": v(8400.06, 1101.08) * mm, "end": v(8360.84, 1045.4) * mm});
            skLineSegment(sketch, "E6818", {"start": v(8360.84, 1045.4) * mm, "end": v(8318.17, 991.15) * mm});
            skLineSegment(sketch, "E6819", {"start": v(8318.17, 991.15) * mm, "end": v(8299.27, 1057.4) * mm});
            skLineSegment(sketch, "E6820", {"start": v(8299.27, 1057.4) * mm, "end": v(8283.83, 1123.84) * mm});
            skLineSegment(sketch, "E6821", {"start": v(8283.83, 1123.84) * mm, "end": v(8299.07, 1182.97) * mm});
            skLineSegment(sketch, "E6822", {"start": v(8400.06, 1101.08) * mm, "end": v(8370.8, 1105.55) * mm});
            skLineSegment(sketch, "E6823", {"start": v(8370.8, 1105.55) * mm, "end": v(8341.53, 1110.84) * mm});
            skLineSegment(sketch, "E6824", {"start": v(8341.53, 1110.84) * mm, "end": v(8312.68, 1116.93) * mm});
            skLineSegment(sketch, "E6825", {"start": v(8312.68, 1116.93) * mm, "end": v(8283.83, 1123.84) * mm});
            skLineSegment(sketch, "E6826", {"start": v(8091.4, 1127.1) * mm, "end": v(8120.25, 1114.5) * mm});
            skLineSegment(sketch, "E6827", {"start": v(8120.25, 1114.5) * mm, "end": v(8149.3, 1102.91) * mm});
            skLineSegment(sketch, "E6828", {"start": v(8149.3, 1102.91) * mm, "end": v(8178.77, 1092.14) * mm});
            skLineSegment(sketch, "E6829", {"start": v(8178.77, 1092.14) * mm, "end": v(8208.44, 1082.19) * mm});
            skLineSegment(sketch, "E6830", {"start": v(8116.6, 1182.57) * mm, "end": v(8143.62, 1170.78) * mm});
            skLineSegment(sketch, "E6831", {"start": v(8143.62, 1170.78) * mm, "end": v(8171.25, 1159.8) * mm});
            skLineSegment(sketch, "E6832", {"start": v(8171.25, 1159.8) * mm, "end": v(8198.89, 1149.65) * mm});
            skLineSegment(sketch, "E6833", {"start": v(8198.89, 1149.65) * mm, "end": v(8226.93, 1140.3) * mm});
            skLineSegment(sketch, "E6834", {"start": v(7996.1, 1319.73) * mm, "end": v(8019.46, 1304.49) * mm});
            skLineSegment(sketch, "E6835", {"start": v(8019.46, 1304.49) * mm, "end": v(8043.03, 1289.86) * mm});
            skLineSegment(sketch, "E6836", {"start": v(8043.03, 1289.86) * mm, "end": v(8067.21, 1275.83) * mm});
            skLineSegment(sketch, "E6837", {"start": v(8067.21, 1275.83) * mm, "end": v(8091.6, 1262.63) * mm});
            skLineSegment(sketch, "E6838", {"start": v(8091.6, 1262.63) * mm, "end": v(8063.35, 1208.58) * mm});
            skLineSegment(sketch, "E6839", {"start": v(8063.35, 1208.58) * mm, "end": v(8022.3, 1196.18) * mm});
            skLineSegment(sketch, "E6840", {"start": v(8022.3, 1196.18) * mm, "end": v(7996.1, 1211.42) * mm});
            skLineSegment(sketch, "E6841", {"start": v(7996.1, 1211.42) * mm, "end": v(7970.08, 1227.47) * mm});
            skLineSegment(sketch, "E6842", {"start": v(7970.08, 1227.47) * mm, "end": v(7927.62, 1218.94) * mm});
            skLineSegment(sketch, "E6843", {"start": v(7927.62, 1218.94) * mm, "end": v(7910.34, 1193.74) * mm});
            skLineSegment(sketch, "E6844", {"start": v(7910.34, 1193.74) * mm, "end": v(7920.91, 1150.46) * mm});
            skLineSegment(sketch, "E6845", {"start": v(7920.91, 1150.46) * mm, "end": v(7948.95, 1132.99) * mm});
            skLineSegment(sketch, "E6846", {"start": v(7948.95, 1132.99) * mm, "end": v(7977.6, 1116.32) * mm});
            skLineSegment(sketch, "E6847", {"start": v(7977.6, 1116.32) * mm, "end": v(8020.88, 1127.5) * mm});
            skFitSpline(sketch, "E6848", {"points": [v(10189.03, 2115.46) * mm, v(10189.03, 1203.64) * mm, v(9449.85, 464.46) * mm, v(8538.03, 464.46) * mm]});
            skFitSpline(sketch, "E6849", {"points": [v(8538.03, 464.46) * mm, v(7626.2, 464.46) * mm, v(6887.03, 1203.64) * mm, v(6887.03, 2115.46) * mm]});
            skFitSpline(sketch, "E6850", {"points": [v(6887.03, 2115.46) * mm, v(6887.03, 3027.28) * mm, v(7626.2, 3766.46) * mm, v(8538.03, 3766.46) * mm]});
            skFitSpline(sketch, "E6851", {"points": [v(8538.03, 3766.46) * mm, v(9449.85, 3766.46) * mm, v(10189.03, 3027.28) * mm, v(10189.03, 2115.46) * mm]});
            skLineSegment(sketch, "E6852", {"start": v(7866.86, 1425.19) * mm, "end": v(7887.18, 1406.09) * mm});
            skLineSegment(sketch, "E6853", {"start": v(7887.18, 1406.09) * mm, "end": v(7907.9, 1387.6) * mm});
            skLineSegment(sketch, "E6854", {"start": v(7907.9, 1387.6) * mm, "end": v(7929.24, 1369.71) * mm});
            skLineSegment(sketch, "E6855", {"start": v(7929.24, 1369.71) * mm, "end": v(7950.98, 1352.44) * mm});
            skLineSegment(sketch, "E6856", {"start": v(7950.98, 1352.44) * mm, "end": v(7914, 1304.08) * mm});
            skLineSegment(sketch, "E6857", {"start": v(7914, 1304.08) * mm, "end": v(7871.53, 1298.8) * mm});
            skLineSegment(sketch, "E6858", {"start": v(7871.53, 1298.8) * mm, "end": v(7848.16, 1318.5) * mm});
            skLineSegment(sketch, "E6859", {"start": v(7848.16, 1318.5) * mm, "end": v(7825.4, 1338.83) * mm});
            skLineSegment(sketch, "E6860", {"start": v(7825.4, 1338.83) * mm, "end": v(7781.92, 1337.81) * mm});
            skLineSegment(sketch, "E6861", {"start": v(7781.92, 1337.81) * mm, "end": v(7760.79, 1316.07) * mm});
            skLineSegment(sketch, "E6862", {"start": v(7760.79, 1316.07) * mm, "end": v(7763.43, 1271.36) * mm});
            skLineSegment(sketch, "E6863", {"start": v(7763.43, 1271.36) * mm, "end": v(7788.22, 1249.42) * mm});
            skLineSegment(sketch, "E6864", {"start": v(7788.22, 1249.42) * mm, "end": v(7813.62, 1228.08) * mm});
            skLineSegment(sketch, "E6865", {"start": v(7813.62, 1228.08) * mm, "end": v(7858.12, 1231.74) * mm});
            skFitSpline(sketch, "E6866", {"points": [v(10443.03, 2115.46) * mm, v(10443.03, 1063.35) * mm, v(9590.13, 210.46) * mm, v(8538.03, 210.46) * mm]});
            skFitSpline(sketch, "E6867", {"points": [v(8538.03, 210.46) * mm, v(7485.93, 210.46) * mm, v(6633.03, 1063.35) * mm, v(6633.03, 2115.46) * mm]});
            skFitSpline(sketch, "E6868", {"points": [v(6633.03, 2115.46) * mm, v(6633.03, 3167.56) * mm, v(7485.93, 4020.46) * mm, v(8538.03, 4020.46) * mm]});
            skFitSpline(sketch, "E6869", {"points": [v(8538.03, 4020.46) * mm, v(9590.13, 4020.46) * mm, v(10443.03, 3167.56) * mm, v(10443.03, 2115.46) * mm]});
            skFitSpline(sketch, "E6870", {"points": [v(10068.73, 2115.46) * mm, v(10068.73, 1270.07) * mm, v(9383.41, 584.75) * mm, v(8538.03, 584.75) * mm]});
            skFitSpline(sketch, "E6871", {"points": [v(8538.03, 584.75) * mm, v(7692.64, 584.75) * mm, v(7007.32, 1270.07) * mm, v(7007.32, 2115.46) * mm]});
            skFitSpline(sketch, "E6872", {"points": [v(7007.32, 2115.46) * mm, v(7007.32, 2960.84) * mm, v(7692.64, 3646.16) * mm, v(8538.03, 3646.16) * mm]});
            skFitSpline(sketch, "E6873", {"points": [v(8538.03, 3646.16) * mm, v(9383.41, 3646.16) * mm, v(10068.73, 2960.84) * mm, v(10068.73, 2115.46) * mm]});
            skLineSegment(sketch, "E6874", {"start": v(14020.57, 2347.87) * mm, "end": v(14024.03, 2348.17) * mm});
            skLineSegment(sketch, "E6875", {"start": v(14024.03, 2348.17) * mm, "end": v(14028.58, 2348.68) * mm});
            skLineSegment(sketch, "E6876", {"start": v(14028.58, 2348.68) * mm, "end": v(14034.2, 2349.46) * mm});
            skLineSegment(sketch, "E6877", {"start": v(14034.2, 2349.46) * mm, "end": v(14040.9, 2350.58) * mm});
            skLineSegment(sketch, "E6878", {"start": v(14040.9, 2350.58) * mm, "end": v(14048.65, 2352.09) * mm});
            skLineSegment(sketch, "E6879", {"start": v(14048.65, 2352.09) * mm, "end": v(14057.43, 2354.04) * mm});
            skLineSegment(sketch, "E6880", {"start": v(14057.43, 2354.04) * mm, "end": v(14067.22, 2356.5) * mm});
            skLineSegment(sketch, "E6881", {"start": v(14067.22, 2356.5) * mm, "end": v(14078.01, 2359.52) * mm});
            skLineSegment(sketch, "E6882", {"start": v(14078.01, 2359.52) * mm, "end": v(14089.77, 2363.15) * mm});
            skLineSegment(sketch, "E6883", {"start": v(14089.77, 2363.15) * mm, "end": v(14102.47, 2367.45) * mm});
            skLineSegment(sketch, "E6884", {"start": v(14102.47, 2367.45) * mm, "end": v(14116.09, 2372.47) * mm});
            skLineSegment(sketch, "E6885", {"start": v(14116.09, 2372.47) * mm, "end": v(14130.59, 2378.27) * mm});
            skLineSegment(sketch, "E6886", {"start": v(14130.59, 2378.27) * mm, "end": v(14145.94, 2384.89) * mm});
            skLineSegment(sketch, "E6887", {"start": v(14145.94, 2384.89) * mm, "end": v(14162.12, 2392.38) * mm});
            skLineSegment(sketch, "E6888", {"start": v(14162.12, 2392.38) * mm, "end": v(14179.07, 2400.8) * mm});
            skLineSegment(sketch, "E6889", {"start": v(14179.07, 2400.8) * mm, "end": v(14196.77, 2410.17) * mm});
            skLineSegment(sketch, "E6890", {"start": v(14196.77, 2410.17) * mm, "end": v(14215.17, 2420.57) * mm});
            skLineSegment(sketch, "E6891", {"start": v(14215.17, 2420.57) * mm, "end": v(14234.23, 2432.03) * mm});
            skLineSegment(sketch, "E6892", {"start": v(14234.23, 2432.03) * mm, "end": v(14253.9, 2444.58) * mm});
            skLineSegment(sketch, "E6893", {"start": v(14253.9, 2444.58) * mm, "end": v(14274.15, 2458.28) * mm});
            skLineSegment(sketch, "E6894", {"start": v(14274.15, 2458.28) * mm, "end": v(14294.92, 2473.16) * mm});
            skLineSegment(sketch, "E6895", {"start": v(14294.92, 2473.16) * mm, "end": v(14316.16, 2489.26) * mm});
            skLineSegment(sketch, "E6896", {"start": v(14316.16, 2489.26) * mm, "end": v(14337.83, 2506.61) * mm});
            skLineSegment(sketch, "E6897", {"start": v(14337.83, 2506.61) * mm, "end": v(14359.86, 2525.26) * mm});
            skLineSegment(sketch, "E6898", {"start": v(14359.86, 2525.26) * mm, "end": v(14380.66, 2545.06) * mm});
            skLineSegment(sketch, "E6899", {"start": v(14380.66, 2545.06) * mm, "end": v(14361.8, 2679.46) * mm});
            skLineSegment(sketch, "E6900", {"start": v(14361.8, 2679.46) * mm, "end": v(14336.35, 2692.77) * mm});
            skLineSegment(sketch, "E6901", {"start": v(14336.35, 2692.77) * mm, "end": v(14310.04, 2704.63) * mm});
            skLineSegment(sketch, "E6902", {"start": v(14310.04, 2704.63) * mm, "end": v(14284.44, 2715.35) * mm});
            skLineSegment(sketch, "E6903", {"start": v(14284.44, 2715.35) * mm, "end": v(14259.58, 2724.98) * mm});
            skLineSegment(sketch, "E6904", {"start": v(14259.58, 2724.98) * mm, "end": v(14235.52, 2733.57) * mm});
            skLineSegment(sketch, "E6905", {"start": v(14235.52, 2733.57) * mm, "end": v(14212.29, 2741.16) * mm});
            skLineSegment(sketch, "E6906", {"start": v(14212.29, 2741.16) * mm, "end": v(14189.91, 2747.82) * mm});
            skLineSegment(sketch, "E6907", {"start": v(14189.91, 2747.82) * mm, "end": v(14168.44, 2753.59) * mm});
            skLineSegment(sketch, "E6908", {"start": v(14168.44, 2753.59) * mm, "end": v(14147.88, 2758.52) * mm});
            skLineSegment(sketch, "E6909", {"start": v(14147.88, 2758.52) * mm, "end": v(14128.29, 2762.67) * mm});
            skLineSegment(sketch, "E6910", {"start": v(14128.29, 2762.67) * mm, "end": v(14109.67, 2766.09) * mm});
            skLineSegment(sketch, "E6911", {"start": v(14109.67, 2766.09) * mm, "end": v(14092.06, 2768.84) * mm});
            skLineSegment(sketch, "E6912", {"start": v(14092.06, 2768.84) * mm, "end": v(14075.48, 2770.98) * mm});
            skLineSegment(sketch, "E6913", {"start": v(14075.48, 2770.98) * mm, "end": v(14059.94, 2772.55) * mm});
            skLineSegment(sketch, "E6914", {"start": v(14059.94, 2772.55) * mm, "end": v(14045.47, 2773.63) * mm});
            skLineSegment(sketch, "E6915", {"start": v(14045.47, 2773.63) * mm, "end": v(14032.07, 2774.27) * mm});
            skLineSegment(sketch, "E6916", {"start": v(14032.07, 2774.27) * mm, "end": v(14019.77, 2774.53) * mm});
            skLineSegment(sketch, "E6917", {"start": v(14019.77, 2774.53) * mm, "end": v(14008.57, 2774.46) * mm});
            skLineSegment(sketch, "E6918", {"start": v(14008.57, 2774.46) * mm, "end": v(13998.48, 2774.13) * mm});
            skLineSegment(sketch, "E6919", {"start": v(13998.48, 2774.13) * mm, "end": v(13989.5, 2773.59) * mm});
            skLineSegment(sketch, "E6920", {"start": v(13989.5, 2773.59) * mm, "end": v(13981.64, 2772.9) * mm});
            skLineSegment(sketch, "E6921", {"start": v(13981.64, 2772.9) * mm, "end": v(13974.9, 2772.14) * mm});
            skLineSegment(sketch, "E6922", {"start": v(13974.9, 2772.14) * mm, "end": v(13969.27, 2771.35) * mm});
            skLineSegment(sketch, "E6923", {"start": v(13969.27, 2771.35) * mm, "end": v(13964.75, 2770.58) * mm});
            skLineSegment(sketch, "E6924", {"start": v(13964.75, 2770.58) * mm, "end": v(13961.34, 2769.92) * mm});
            skLineSegment(sketch, "E6925", {"start": v(13961.34, 2769.92) * mm, "end": v(13959.02, 2769.4) * mm});
            skLineSegment(sketch, "E6926", {"start": v(13959.02, 2769.4) * mm, "end": v(13957.8, 2769.09) * mm});
            skLineSegment(sketch, "E6927", {"start": v(13957.8, 2769.09) * mm, "end": v(13792.33, 2721.72) * mm});
            skLineSegment(sketch, "E6928", {"start": v(13792.33, 2721.72) * mm, "end": v(13689.16, 2979.2) * mm});
            skLineSegment(sketch, "E6929", {"start": v(13689.16, 2979.2) * mm, "end": v(13841.56, 3059.19) * mm});
            skLineSegment(sketch, "E6930", {"start": v(13841.56, 3059.19) * mm, "end": v(13842.66, 3059.81) * mm});
            skLineSegment(sketch, "E6931", {"start": v(13842.66, 3059.81) * mm, "end": v(13844.7, 3061.04) * mm});
            skLineSegment(sketch, "E6932", {"start": v(13844.7, 3061.04) * mm, "end": v(13847.62, 3062.9) * mm});
            skLineSegment(sketch, "E6933", {"start": v(13847.62, 3062.9) * mm, "end": v(13851.42, 3065.48) * mm});
            skLineSegment(sketch, "E6934", {"start": v(13851.42, 3065.48) * mm, "end": v(13856.03, 3068.79) * mm});
            skLineSegment(sketch, "E6935", {"start": v(13856.03, 3068.79) * mm, "end": v(13861.44, 3072.9) * mm});
            skLineSegment(sketch, "E6936", {"start": v(13861.44, 3072.9) * mm, "end": v(13867.6, 3077.82) * mm});
            skLineSegment(sketch, "E6937", {"start": v(13867.6, 3077.82) * mm, "end": v(13874.47, 3083.64) * mm});
            skLineSegment(sketch, "E6938", {"start": v(13874.47, 3083.64) * mm, "end": v(13882, 3090.37) * mm});
            skLineSegment(sketch, "E6939", {"start": v(13882, 3090.37) * mm, "end": v(13890.15, 3098.05) * mm});
            skLineSegment(sketch, "E6940", {"start": v(13890.15, 3098.05) * mm, "end": v(13898.87, 3106.73) * mm});
            skLineSegment(sketch, "E6941", {"start": v(13898.87, 3106.73) * mm, "end": v(13908.12, 3116.44) * mm});
            skLineSegment(sketch, "E6942", {"start": v(13908.12, 3116.44) * mm, "end": v(13917.84, 3127.21) * mm});
            skLineSegment(sketch, "E6943", {"start": v(13917.84, 3127.21) * mm, "end": v(13927.99, 3139.08) * mm});
            skLineSegment(sketch, "E6944", {"start": v(13927.99, 3139.08) * mm, "end": v(13938.5, 3152.08) * mm});
            skLineSegment(sketch, "E6945", {"start": v(13938.5, 3152.08) * mm, "end": v(13949.35, 3166.23) * mm});
            skLineSegment(sketch, "E6946", {"start": v(13949.35, 3166.23) * mm, "end": v(13960.45, 3181.56) * mm});
            skLineSegment(sketch, "E6947", {"start": v(13960.45, 3181.56) * mm, "end": v(13971.76, 3198.09) * mm});
            skLineSegment(sketch, "E6948", {"start": v(13971.76, 3198.09) * mm, "end": v(13983.22, 3215.85) * mm});
            skLineSegment(sketch, "E6949", {"start": v(13983.22, 3215.85) * mm, "end": v(13994.78, 3234.85) * mm});
            skLineSegment(sketch, "E6950", {"start": v(13994.78, 3234.85) * mm, "end": v(14006.36, 3255.1) * mm});
            skLineSegment(sketch, "E6951", {"start": v(14006.36, 3255.1) * mm, "end": v(14017.92, 3276.65) * mm});
            skLineSegment(sketch, "E6952", {"start": v(14017.92, 3276.65) * mm, "end": v(14029.4, 3299.48) * mm});
            skLineSegment(sketch, "E6953", {"start": v(14029.4, 3299.48) * mm, "end": v(14040.73, 3323.6) * mm});
            skLineSegment(sketch, "E6954", {"start": v(14040.73, 3323.6) * mm, "end": v(14051.84, 3349.04) * mm});
            skLineSegment(sketch, "E6955", {"start": v(14051.84, 3349.04) * mm, "end": v(14062.69, 3375.78) * mm});
            skLineSegment(sketch, "E6956", {"start": v(14062.69, 3375.78) * mm, "end": v(14071.9, 3402.98) * mm});
            skLineSegment(sketch, "E6957", {"start": v(14071.9, 3402.98) * mm, "end": v(13992.75, 3513.22) * mm});
            skLineSegment(sketch, "E6958", {"start": v(13992.75, 3513.22) * mm, "end": v(13964.03, 3513.18) * mm});
            skLineSegment(sketch, "E6959", {"start": v(13964.03, 3513.18) * mm, "end": v(13935.22, 3511.45) * mm});
            skLineSegment(sketch, "E6960", {"start": v(13935.22, 3511.45) * mm, "end": v(13907.57, 3509.05) * mm});
            skLineSegment(sketch, "E6961", {"start": v(13907.57, 3509.05) * mm, "end": v(13881.09, 3506.03) * mm});
            skLineSegment(sketch, "E6962", {"start": v(13881.09, 3506.03) * mm, "end": v(13855.79, 3502.45) * mm});
            skLineSegment(sketch, "E6963", {"start": v(13855.79, 3502.45) * mm, "end": v(13831.68, 3498.38) * mm});
            skLineSegment(sketch, "E6964", {"start": v(13831.68, 3498.38) * mm, "end": v(13808.78, 3493.88) * mm});
            skLineSegment(sketch, "E6965", {"start": v(13808.78, 3493.88) * mm, "end": v(13787.08, 3489) * mm});
            skLineSegment(sketch, "E6966", {"start": v(13787.08, 3489) * mm, "end": v(13766.6, 3483.82) * mm});
            skLineSegment(sketch, "E6967", {"start": v(13766.6, 3483.82) * mm, "end": v(13747.31, 3478.38) * mm});
            skLineSegment(sketch, "E6968", {"start": v(13747.31, 3478.38) * mm, "end": v(13729.24, 3472.76) * mm});
            skLineSegment(sketch, "E6969", {"start": v(13729.24, 3472.76) * mm, "end": v(13712.37, 3467.01) * mm});
            skLineSegment(sketch, "E6970", {"start": v(13712.37, 3467.01) * mm, "end": v(13696.7, 3461.2) * mm});
            skLineSegment(sketch, "E6971", {"start": v(13696.7, 3461.2) * mm, "end": v(13682.2, 3455.38) * mm});
            skLineSegment(sketch, "E6972", {"start": v(13682.2, 3455.38) * mm, "end": v(13668.88, 3449.6) * mm});
            skLineSegment(sketch, "E6973", {"start": v(13668.88, 3449.6) * mm, "end": v(13656.73, 3443.95) * mm});
            skLineSegment(sketch, "E6974", {"start": v(13656.73, 3443.95) * mm, "end": v(13645.72, 3438.45) * mm});
            skLineSegment(sketch, "E6975", {"start": v(13645.72, 3438.45) * mm, "end": v(13635.83, 3433.19) * mm});
            skLineSegment(sketch, "E6976", {"start": v(13635.83, 3433.19) * mm, "end": v(13627.05, 3428.2) * mm});
            skLineSegment(sketch, "E6977", {"start": v(13627.05, 3428.2) * mm, "end": v(13619.35, 3423.55) * mm});
            skLineSegment(sketch, "E6978", {"start": v(13619.35, 3423.55) * mm, "end": v(13612.7, 3419.3) * mm});
            skLineSegment(sketch, "E6979", {"start": v(13612.7, 3419.3) * mm, "end": v(13607.09, 3415.48) * mm});
            skLineSegment(sketch, "E6980", {"start": v(13607.09, 3415.48) * mm, "end": v(13602.47, 3412.17) * mm});
            skLineSegment(sketch, "E6981", {"start": v(13602.47, 3412.17) * mm, "end": v(13598.83, 3409.4) * mm});
            skLineSegment(sketch, "E6982", {"start": v(13598.83, 3409.4) * mm, "end": v(13596.12, 3407.22) * mm});
            skLineSegment(sketch, "E6983", {"start": v(13596.12, 3407.22) * mm, "end": v(13594.3, 3405.68) * mm});
            skLineSegment(sketch, "E6984", {"start": v(13594.3, 3405.68) * mm, "end": v(13593.36, 3404.83) * mm});
            skLineSegment(sketch, "E6985", {"start": v(13593.36, 3404.83) * mm, "end": v(13468.86, 3286) * mm});
            skLineSegment(sketch, "E6986", {"start": v(13468.86, 3286) * mm, "end": v(13257.86, 3466.04) * mm});
            skLineSegment(sketch, "E6987", {"start": v(13257.86, 3466.04) * mm, "end": v(13355.63, 3607.69) * mm});
            skLineSegment(sketch, "E6988", {"start": v(13355.63, 3607.69) * mm, "end": v(13356.31, 3608.76) * mm});
            skLineSegment(sketch, "E6989", {"start": v(13356.31, 3608.76) * mm, "end": v(13357.54, 3610.78) * mm});
            skLineSegment(sketch, "E6990", {"start": v(13357.54, 3610.78) * mm, "end": v(13359.27, 3613.8) * mm});
            skLineSegment(sketch, "E6991", {"start": v(13359.27, 3613.8) * mm, "end": v(13361.43, 3617.84) * mm});
            skLineSegment(sketch, "E6992", {"start": v(13361.43, 3617.84) * mm, "end": v(13363.98, 3622.92) * mm});
            skLineSegment(sketch, "E6993", {"start": v(13363.98, 3622.92) * mm, "end": v(13366.87, 3629.06) * mm});
            skLineSegment(sketch, "E6994", {"start": v(13366.87, 3629.06) * mm, "end": v(13370.02, 3636.3) * mm});
            skLineSegment(sketch, "E6995", {"start": v(13370.02, 3636.3) * mm, "end": v(13373.4, 3644.63) * mm});
            skLineSegment(sketch, "E6996", {"start": v(13373.4, 3644.63) * mm, "end": v(13376.94, 3654.09) * mm});
            skLineSegment(sketch, "E6997", {"start": v(13376.94, 3654.09) * mm, "end": v(13380.59, 3664.68) * mm});
            skLineSegment(sketch, "E6998", {"start": v(13380.59, 3664.68) * mm, "end": v(13384.28, 3676.42) * mm});
            skLineSegment(sketch, "E6999", {"start": v(13384.28, 3676.42) * mm, "end": v(13387.96, 3689.31) * mm});
            skLineSegment(sketch, "E7000", {"start": v(13387.96, 3689.31) * mm, "end": v(13391.56, 3703.37) * mm});
            skLineSegment(sketch, "E7001", {"start": v(13391.56, 3703.37) * mm, "end": v(13395.03, 3718.6) * mm});
            skLineSegment(sketch, "E7002", {"start": v(13395.03, 3718.6) * mm, "end": v(13398.3, 3735) * mm});
            skLineSegment(sketch, "E7003", {"start": v(13398.3, 3735) * mm, "end": v(13401.33, 3752.56) * mm});
            skLineSegment(sketch, "E7004", {"start": v(13401.33, 3752.56) * mm, "end": v(13404.03, 3771.3) * mm});
            skLineSegment(sketch, "E7005", {"start": v(13404.03, 3771.3) * mm, "end": v(13406.37, 3791.19) * mm});
            skLineSegment(sketch, "E7006", {"start": v(13406.37, 3791.19) * mm, "end": v(13408.26, 3812.24) * mm});
            skLineSegment(sketch, "E7007", {"start": v(13408.26, 3812.24) * mm, "end": v(13409.66, 3834.43) * mm});
            skLineSegment(sketch, "E7008", {"start": v(13409.66, 3834.43) * mm, "end": v(13410.5, 3857.76) * mm});
            skLineSegment(sketch, "E7009", {"start": v(13410.5, 3857.76) * mm, "end": v(13410.73, 3882.2) * mm});
            skLineSegment(sketch, "E7010", {"start": v(13410.73, 3882.2) * mm, "end": v(13410.28, 3907.75) * mm});
            skLineSegment(sketch, "E7011", {"start": v(13410.28, 3907.75) * mm, "end": v(13409.1, 3934.37) * mm});
            skLineSegment(sketch, "E7012", {"start": v(13409.1, 3934.37) * mm, "end": v(13407.12, 3962.06) * mm});
            skLineSegment(sketch, "E7013", {"start": v(13407.12, 3962.06) * mm, "end": v(13404.3, 3990.78) * mm});
            skLineSegment(sketch, "E7014", {"start": v(13404.3, 3990.78) * mm, "end": v(13399.82, 4019.15) * mm});
            skLineSegment(sketch, "E7015", {"start": v(13399.82, 4019.15) * mm, "end": v(13278.5, 4079.98) * mm});
            skLineSegment(sketch, "E7016", {"start": v(13278.5, 4079.98) * mm, "end": v(13253.08, 4066.6) * mm});
            skLineSegment(sketch, "E7017", {"start": v(13253.08, 4066.6) * mm, "end": v(13228.38, 4051.68) * mm});
            skLineSegment(sketch, "E7018", {"start": v(13228.38, 4051.68) * mm, "end": v(13205.01, 4036.7) * mm});
            skLineSegment(sketch, "E7019", {"start": v(13205.01, 4036.7) * mm, "end": v(13182.97, 4021.71) * mm});
            skLineSegment(sketch, "E7020", {"start": v(13182.97, 4021.71) * mm, "end": v(13162.23, 4006.8) * mm});
            skLineSegment(sketch, "E7021", {"start": v(13162.23, 4006.8) * mm, "end": v(13142.78, 3991.98) * mm});
            skLineSegment(sketch, "E7022", {"start": v(13142.78, 3991.98) * mm, "end": v(13124.6, 3977.35) * mm});
            skLineSegment(sketch, "E7023", {"start": v(13124.6, 3977.35) * mm, "end": v(13107.64, 3962.95) * mm});
            skLineSegment(sketch, "E7024", {"start": v(13107.64, 3962.95) * mm, "end": v(13091.91, 3948.84) * mm});
            skLineSegment(sketch, "E7025", {"start": v(13091.91, 3948.84) * mm, "end": v(13077.37, 3935.07) * mm});
            skLineSegment(sketch, "E7026", {"start": v(13077.37, 3935.07) * mm, "end": v(13063.98, 3921.7) * mm});
            skLineSegment(sketch, "E7027", {"start": v(13063.98, 3921.7) * mm, "end": v(13051.7, 3908.76) * mm});
            skLineSegment(sketch, "E7028", {"start": v(13051.7, 3908.76) * mm, "end": v(13040.53, 3896.33) * mm});
            skLineSegment(sketch, "E7029", {"start": v(13040.53, 3896.33) * mm, "end": v(13030.4, 3884.44) * mm});
            skLineSegment(sketch, "E7030", {"start": v(13030.4, 3884.44) * mm, "end": v(13021.3, 3873.14) * mm});
            skLineSegment(sketch, "E7031", {"start": v(13021.3, 3873.14) * mm, "end": v(13013.16, 3862.48) * mm});
            skLineSegment(sketch, "E7032", {"start": v(13013.16, 3862.48) * mm, "end": v(13005.96, 3852.5) * mm});
            skLineSegment(sketch, "E7033", {"start": v(13005.96, 3852.5) * mm, "end": v(12999.65, 3843.24) * mm});
            skLineSegment(sketch, "E7034", {"start": v(12999.65, 3843.24) * mm, "end": v(12994.2, 3834.75) * mm});
            skLineSegment(sketch, "E7035", {"start": v(12994.2, 3834.75) * mm, "end": v(12989.54, 3827.05) * mm});
            skLineSegment(sketch, "E7036", {"start": v(12989.54, 3827.05) * mm, "end": v(12985.63, 3820.2) * mm});
            skLineSegment(sketch, "E7037", {"start": v(12985.63, 3820.2) * mm, "end": v(12982.43, 3814.2) * mm});
            skLineSegment(sketch, "E7038", {"start": v(12982.43, 3814.2) * mm, "end": v(12979.89, 3809.13) * mm});
            skLineSegment(sketch, "E7039", {"start": v(12979.89, 3809.13) * mm, "end": v(12977.95, 3804.98) * mm});
            skLineSegment(sketch, "E7040", {"start": v(12977.95, 3804.98) * mm, "end": v(12976.56, 3801.79) * mm});
            skLineSegment(sketch, "E7041", {"start": v(12976.56, 3801.79) * mm, "end": v(12975.67, 3799.6) * mm});
            skLineSegment(sketch, "E7042", {"start": v(12975.67, 3799.6) * mm, "end": v(12975.23, 3798.4) * mm});
            skLineSegment(sketch, "E7043", {"start": v(12975.23, 3798.4) * mm, "end": v(12920.22, 3635.32) * mm});
            skLineSegment(sketch, "E7044", {"start": v(12920.22, 3635.32) * mm, "end": v(12649.71, 3696.68) * mm});
            skLineSegment(sketch, "E7045", {"start": v(12649.71, 3696.68) * mm, "end": v(12670.45, 3867.54) * mm});
            skLineSegment(sketch, "E7046", {"start": v(12670.45, 3867.54) * mm, "end": v(12670.57, 3868.8) * mm});
            skLineSegment(sketch, "E7047", {"start": v(12670.57, 3868.8) * mm, "end": v(12670.71, 3871.17) * mm});
            skLineSegment(sketch, "E7048", {"start": v(12670.71, 3871.17) * mm, "end": v(12670.84, 3874.64) * mm});
            skLineSegment(sketch, "E7049", {"start": v(12670.84, 3874.64) * mm, "end": v(12670.88, 3879.22) * mm});
            skLineSegment(sketch, "E7050", {"start": v(12670.88, 3879.22) * mm, "end": v(12670.78, 3884.9) * mm});
            skLineSegment(sketch, "E7051", {"start": v(12670.78, 3884.9) * mm, "end": v(12670.47, 3891.69) * mm});
            skLineSegment(sketch, "E7052", {"start": v(12670.47, 3891.69) * mm, "end": v(12669.9, 3899.56) * mm});
            skLineSegment(sketch, "E7053", {"start": v(12669.9, 3899.56) * mm, "end": v(12669.03, 3908.5) * mm});
            skLineSegment(sketch, "E7054", {"start": v(12669.03, 3908.5) * mm, "end": v(12667.77, 3918.53) * mm});
            skLineSegment(sketch, "E7055", {"start": v(12667.77, 3918.53) * mm, "end": v(12666.07, 3929.6) * mm});
            skLineSegment(sketch, "E7056", {"start": v(12666.07, 3929.6) * mm, "end": v(12663.88, 3941.71) * mm});
            skLineSegment(sketch, "E7057", {"start": v(12663.88, 3941.71) * mm, "end": v(12661.15, 3954.84) * mm});
            skLineSegment(sketch, "E7058", {"start": v(12661.15, 3954.84) * mm, "end": v(12657.8, 3968.96) * mm});
            skLineSegment(sketch, "E7059", {"start": v(12657.8, 3968.96) * mm, "end": v(12653.8, 3984.06) * mm});
            skLineSegment(sketch, "E7060", {"start": v(12653.8, 3984.06) * mm, "end": v(12649.08, 4000.1) * mm});
            skLineSegment(sketch, "E7061", {"start": v(12649.08, 4000.1) * mm, "end": v(12643.6, 4017.05) * mm});
            skLineSegment(sketch, "E7062", {"start": v(12643.6, 4017.05) * mm, "end": v(12637.28, 4034.9) * mm});
            skLineSegment(sketch, "E7063", {"start": v(12637.28, 4034.9) * mm, "end": v(12630.1, 4053.6) * mm});
            skLineSegment(sketch, "E7064", {"start": v(12630.1, 4053.6) * mm, "end": v(12622, 4073.12) * mm});
            skLineSegment(sketch, "E7065", {"start": v(12622, 4073.12) * mm, "end": v(12612.93, 4093.42) * mm});
            skLineSegment(sketch, "E7066", {"start": v(12612.93, 4093.42) * mm, "end": v(12602.83, 4114.47) * mm});
            skLineSegment(sketch, "E7067", {"start": v(12602.83, 4114.47) * mm, "end": v(12591.67, 4136.22) * mm});
            skLineSegment(sketch, "E7068", {"start": v(12591.67, 4136.22) * mm, "end": v(12579.4, 4158.63) * mm});
            skLineSegment(sketch, "E7069", {"start": v(12579.4, 4158.63) * mm, "end": v(12565.98, 4181.66) * mm});
            skLineSegment(sketch, "E7070", {"start": v(12565.98, 4181.66) * mm, "end": v(12551.37, 4205.25) * mm});
            skLineSegment(sketch, "E7071", {"start": v(12551.37, 4205.25) * mm, "end": v(12535.52, 4229.37) * mm});
            skLineSegment(sketch, "E7072", {"start": v(12535.52, 4229.37) * mm, "end": v(12518.37, 4252.4) * mm});
            skLineSegment(sketch, "E7073", {"start": v(12518.37, 4252.4) * mm, "end": v(12382.67, 4249.89) * mm});
            skLineSegment(sketch, "E7074", {"start": v(12382.67, 4249.89) * mm, "end": v(12366.4, 4226.23) * mm});
            skLineSegment(sketch, "E7075", {"start": v(12366.4, 4226.23) * mm, "end": v(12351.45, 4201.53) * mm});
            skLineSegment(sketch, "E7076", {"start": v(12351.45, 4201.53) * mm, "end": v(12337.72, 4177.41) * mm});
            skLineSegment(sketch, "E7077", {"start": v(12337.72, 4177.41) * mm, "end": v(12325.16, 4153.9) * mm});
            skLineSegment(sketch, "E7078", {"start": v(12325.16, 4153.9) * mm, "end": v(12313.74, 4131.05) * mm});
            skLineSegment(sketch, "E7079", {"start": v(12313.74, 4131.05) * mm, "end": v(12303.4, 4108.9) * mm});
            skLineSegment(sketch, "E7080", {"start": v(12303.4, 4108.9) * mm, "end": v(12294.1, 4087.5) * mm});
            skLineSegment(sketch, "E7081", {"start": v(12294.1, 4087.5) * mm, "end": v(12285.78, 4066.87) * mm});
            skLineSegment(sketch, "E7082", {"start": v(12285.78, 4066.87) * mm, "end": v(12278.4, 4047.06) * mm});
            skLineSegment(sketch, "E7083", {"start": v(12278.4, 4047.06) * mm, "end": v(12271.92, 4028.1) * mm});
            skLineSegment(sketch, "E7084", {"start": v(12271.92, 4028.1) * mm, "end": v(12266.28, 4010.04) * mm});
            skLineSegment(sketch, "E7085", {"start": v(12266.28, 4010.04) * mm, "end": v(12261.43, 3992.89) * mm});
            skLineSegment(sketch, "E7086", {"start": v(12261.43, 3992.89) * mm, "end": v(12257.31, 3976.68) * mm});
            skLineSegment(sketch, "E7087", {"start": v(12257.31, 3976.68) * mm, "end": v(12253.87, 3961.45) * mm});
            skLineSegment(sketch, "E7088", {"start": v(12253.87, 3961.45) * mm, "end": v(12251.06, 3947.21) * mm});
            skLineSegment(sketch, "E7089", {"start": v(12251.06, 3947.21) * mm, "end": v(12248.8, 3934) * mm});
            skLineSegment(sketch, "E7090", {"start": v(12248.8, 3934) * mm, "end": v(12247.07, 3921.81) * mm});
            skLineSegment(sketch, "E7091", {"start": v(12247.07, 3921.81) * mm, "end": v(12245.8, 3910.68) * mm});
            skLineSegment(sketch, "E7092", {"start": v(12245.8, 3910.68) * mm, "end": v(12244.9, 3900.62) * mm});
            skLineSegment(sketch, "E7093", {"start": v(12244.9, 3900.62) * mm, "end": v(12244.35, 3891.65) * mm});
            skLineSegment(sketch, "E7094", {"start": v(12244.35, 3891.65) * mm, "end": v(12244.08, 3883.76) * mm});
            skLineSegment(sketch, "E7095", {"start": v(12244.08, 3883.76) * mm, "end": v(12244.03, 3876.97) * mm});
            skLineSegment(sketch, "E7096", {"start": v(12244.03, 3876.97) * mm, "end": v(12244.14, 3871.29) * mm});
            skLineSegment(sketch, "E7097", {"start": v(12244.14, 3871.29) * mm, "end": v(12244.35, 3866.71) * mm});
            skLineSegment(sketch, "E7098", {"start": v(12244.35, 3866.71) * mm, "end": v(12244.6, 3863.25) * mm});
            skLineSegment(sketch, "E7099", {"start": v(12244.6, 3863.25) * mm, "end": v(12244.84, 3860.89) * mm});
            skLineSegment(sketch, "E7100", {"start": v(12244.84, 3860.89) * mm, "end": v(12245, 3859.63) * mm});
            skLineSegment(sketch, "E7101", {"start": v(12245, 3859.63) * mm, "end": v(12272.08, 3689.66) * mm});
            skLineSegment(sketch, "E7102", {"start": v(12272.08, 3689.66) * mm, "end": v(12004.04, 3618.28) * mm});
            skLineSegment(sketch, "E7103", {"start": v(12004.04, 3618.28) * mm, "end": v(11943, 3779.2) * mm});
            skLineSegment(sketch, "E7104", {"start": v(11943, 3779.2) * mm, "end": v(11942.52, 3780.38) * mm});
            skLineSegment(sketch, "E7105", {"start": v(11942.52, 3780.38) * mm, "end": v(11941.55, 3782.54) * mm});
            skLineSegment(sketch, "E7106", {"start": v(11941.55, 3782.54) * mm, "end": v(11940.04, 3785.68) * mm});
            skLineSegment(sketch, "E7107", {"start": v(11940.04, 3785.68) * mm, "end": v(11937.95, 3789.75) * mm});
            skLineSegment(sketch, "E7108", {"start": v(11937.95, 3789.75) * mm, "end": v(11935.22, 3794.74) * mm});
            skLineSegment(sketch, "E7109", {"start": v(11935.22, 3794.74) * mm, "end": v(11931.8, 3800.6) * mm});
            skLineSegment(sketch, "E7110", {"start": v(11931.8, 3800.6) * mm, "end": v(11927.64, 3807.3) * mm});
            skLineSegment(sketch, "E7111", {"start": v(11927.64, 3807.3) * mm, "end": v(11922.7, 3814.82) * mm});
            skLineSegment(sketch, "E7112", {"start": v(11922.7, 3814.82) * mm, "end": v(11916.93, 3823.1) * mm});
            skLineSegment(sketch, "E7113", {"start": v(11916.93, 3823.1) * mm, "end": v(11910.28, 3832.13) * mm});
            skLineSegment(sketch, "E7114", {"start": v(11910.28, 3832.13) * mm, "end": v(11902.72, 3841.83) * mm});
            skLineSegment(sketch, "E7115", {"start": v(11902.72, 3841.83) * mm, "end": v(11894.2, 3852.18) * mm});
            skLineSegment(sketch, "E7116", {"start": v(11894.2, 3852.18) * mm, "end": v(11884.67, 3863.13) * mm});
            skLineSegment(sketch, "E7117", {"start": v(11884.67, 3863.13) * mm, "end": v(11874.1, 3874.64) * mm});
            skLineSegment(sketch, "E7118", {"start": v(11874.1, 3874.64) * mm, "end": v(11862.48, 3886.65) * mm});
            skLineSegment(sketch, "E7119", {"start": v(11862.48, 3886.65) * mm, "end": v(11849.74, 3899.11) * mm});
            skLineSegment(sketch, "E7120", {"start": v(11849.74, 3899.11) * mm, "end": v(11835.86, 3911.98) * mm});
            skLineSegment(sketch, "E7121", {"start": v(11835.86, 3911.98) * mm, "end": v(11820.8, 3925.2) * mm});
            skLineSegment(sketch, "E7122", {"start": v(11820.8, 3925.2) * mm, "end": v(11804.56, 3938.72) * mm});
            skLineSegment(sketch, "E7123", {"start": v(11804.56, 3938.72) * mm, "end": v(11787.1, 3952.48) * mm});
            skLineSegment(sketch, "E7124", {"start": v(11787.1, 3952.48) * mm, "end": v(11768.37, 3966.43) * mm});
            skLineSegment(sketch, "E7125", {"start": v(11768.37, 3966.43) * mm, "end": v(11748.39, 3980.5) * mm});
            skLineSegment(sketch, "E7126", {"start": v(11748.39, 3980.5) * mm, "end": v(11727.1, 3994.64) * mm});
            skLineSegment(sketch, "E7127", {"start": v(11727.1, 3994.64) * mm, "end": v(11704.52, 4008.8) * mm});
            skLineSegment(sketch, "E7128", {"start": v(11704.52, 4008.8) * mm, "end": v(11680.62, 4022.9) * mm});
            skLineSegment(sketch, "E7129", {"start": v(11680.62, 4022.9) * mm, "end": v(11655.37, 4036.89) * mm});
            skLineSegment(sketch, "E7130", {"start": v(11655.37, 4036.89) * mm, "end": v(11629.48, 4049.32) * mm});
            skLineSegment(sketch, "E7131", {"start": v(11629.48, 4049.32) * mm, "end": v(11510.5, 3984.02) * mm});
            skLineSegment(sketch, "E7132", {"start": v(11510.5, 3984.02) * mm, "end": v(11507.08, 3955.5) * mm});
            skLineSegment(sketch, "E7133", {"start": v(11507.08, 3955.5) * mm, "end": v(11505.33, 3926.7) * mm});
            skLineSegment(sketch, "E7134", {"start": v(11505.33, 3926.7) * mm, "end": v(11504.38, 3898.96) * mm});
            skLineSegment(sketch, "E7135", {"start": v(11504.38, 3898.96) * mm, "end": v(11504.19, 3872.3) * mm});
            skLineSegment(sketch, "E7136", {"start": v(11504.19, 3872.3) * mm, "end": v(11504.69, 3846.76) * mm});
            skLineSegment(sketch, "E7137", {"start": v(11504.69, 3846.76) * mm, "end": v(11505.83, 3822.34) * mm});
            skLineSegment(sketch, "E7138", {"start": v(11505.83, 3822.34) * mm, "end": v(11507.53, 3799.06) * mm});
            skLineSegment(sketch, "E7139", {"start": v(11507.53, 3799.06) * mm, "end": v(11509.76, 3776.94) * mm});
            skLineSegment(sketch, "E7140", {"start": v(11509.76, 3776.94) * mm, "end": v(11512.44, 3755.97) * mm});
            skLineSegment(sketch, "E7141", {"start": v(11512.44, 3755.97) * mm, "end": v(11515.5, 3736.18) * mm});
            skLineSegment(sketch, "E7142", {"start": v(11515.5, 3736.18) * mm, "end": v(11518.9, 3717.56) * mm});
            skLineSegment(sketch, "E7143", {"start": v(11518.9, 3717.56) * mm, "end": v(11522.58, 3700.12) * mm});
            skLineSegment(sketch, "E7144", {"start": v(11522.58, 3700.12) * mm, "end": v(11526.46, 3683.85) * mm});
            skLineSegment(sketch, "E7145", {"start": v(11526.46, 3683.85) * mm, "end": v(11530.5, 3668.77) * mm});
            skLineSegment(sketch, "E7146", {"start": v(11530.5, 3668.77) * mm, "end": v(11534.62, 3654.85) * mm});
            skLineSegment(sketch, "E7147", {"start": v(11534.62, 3654.85) * mm, "end": v(11538.77, 3642.1) * mm});
            skLineSegment(sketch, "E7148", {"start": v(11538.77, 3642.1) * mm, "end": v(11542.9, 3630.5) * mm});
            skLineSegment(sketch, "E7149", {"start": v(11542.9, 3630.5) * mm, "end": v(11546.93, 3620.06) * mm});
            skLineSegment(sketch, "E7150", {"start": v(11546.93, 3620.06) * mm, "end": v(11550.82, 3610.74) * mm});
            skLineSegment(sketch, "E7151", {"start": v(11550.82, 3610.74) * mm, "end": v(11554.51, 3602.54) * mm});
            skLineSegment(sketch, "E7152", {"start": v(11554.51, 3602.54) * mm, "end": v(11557.93, 3595.43) * mm});
            skLineSegment(sketch, "E7153", {"start": v(11557.93, 3595.43) * mm, "end": v(11561.04, 3589.4) * mm});
            skLineSegment(sketch, "E7154", {"start": v(11561.04, 3589.4) * mm, "end": v(11563.78, 3584.41) * mm});
            skLineSegment(sketch, "E7155", {"start": v(11563.78, 3584.41) * mm, "end": v(11566.1, 3580.46) * mm});
            skLineSegment(sketch, "E7156", {"start": v(11566.1, 3580.46) * mm, "end": v(11567.93, 3577.5) * mm});
            skLineSegment(sketch, "E7157", {"start": v(11567.93, 3577.5) * mm, "end": v(11569.24, 3575.53) * mm});
            skLineSegment(sketch, "E7158", {"start": v(11569.24, 3575.53) * mm, "end": v(11569.96, 3574.48) * mm});
            skLineSegment(sketch, "E7159", {"start": v(11569.96, 3574.48) * mm, "end": v(11672.93, 3436.57) * mm});
            skLineSegment(sketch, "E7160", {"start": v(11672.93, 3436.57) * mm, "end": v(11468.76, 3248.8) * mm});
            skLineSegment(sketch, "E7161", {"start": v(11468.76, 3248.8) * mm, "end": v(11339.93, 3362.93) * mm});
            skLineSegment(sketch, "E7162", {"start": v(11339.93, 3362.93) * mm, "end": v(11338.96, 3363.74) * mm});
            skLineSegment(sketch, "E7163", {"start": v(11338.96, 3363.74) * mm, "end": v(11337.1, 3365.2) * mm});
            skLineSegment(sketch, "E7164", {"start": v(11337.1, 3365.2) * mm, "end": v(11334.3, 3367.28) * mm});
            skLineSegment(sketch, "E7165", {"start": v(11334.3, 3367.28) * mm, "end": v(11330.55, 3369.92) * mm});
            skLineSegment(sketch, "E7166", {"start": v(11330.55, 3369.92) * mm, "end": v(11325.82, 3373.07) * mm});
            skLineSegment(sketch, "E7167", {"start": v(11325.82, 3373.07) * mm, "end": v(11320.07, 3376.67) * mm});
            skLineSegment(sketch, "E7168", {"start": v(11320.07, 3376.67) * mm, "end": v(11313.27, 3380.68) * mm});
            skLineSegment(sketch, "E7169", {"start": v(11313.27, 3380.68) * mm, "end": v(11305.4, 3385.03) * mm});
            skLineSegment(sketch, "E7170", {"start": v(11305.4, 3385.03) * mm, "end": v(11296.44, 3389.69) * mm});
            skLineSegment(sketch, "E7171", {"start": v(11296.44, 3389.69) * mm, "end": v(11286.36, 3394.58) * mm});
            skLineSegment(sketch, "E7172", {"start": v(11286.36, 3394.58) * mm, "end": v(11275.15, 3399.66) * mm});
            skLineSegment(sketch, "E7173", {"start": v(11275.15, 3399.66) * mm, "end": v(11262.8, 3404.86) * mm});
            skLineSegment(sketch, "E7174", {"start": v(11262.8, 3404.86) * mm, "end": v(11249.28, 3410.14) * mm});
            skLineSegment(sketch, "E7175", {"start": v(11249.28, 3410.14) * mm, "end": v(11234.58, 3415.42) * mm});
            skLineSegment(sketch, "E7176", {"start": v(11234.58, 3415.42) * mm, "end": v(11218.7, 3420.64) * mm});
            skLineSegment(sketch, "E7177", {"start": v(11218.7, 3420.64) * mm, "end": v(11201.62, 3425.76) * mm});
            skLineSegment(sketch, "E7178", {"start": v(11201.62, 3425.76) * mm, "end": v(11183.35, 3430.7) * mm});
            skLineSegment(sketch, "E7179", {"start": v(11183.35, 3430.7) * mm, "end": v(11163.88, 3435.42) * mm});
            skLineSegment(sketch, "E7180", {"start": v(11163.88, 3435.42) * mm, "end": v(11143.22, 3439.84) * mm});
            skLineSegment(sketch, "E7181", {"start": v(11143.22, 3439.84) * mm, "end": v(11121.35, 3443.9) * mm});
            skLineSegment(sketch, "E7182", {"start": v(11121.35, 3443.9) * mm, "end": v(11098.3, 3447.55) * mm});
            skLineSegment(sketch, "E7183", {"start": v(11098.3, 3447.55) * mm, "end": v(11074.06, 3450.73) * mm});
            skLineSegment(sketch, "E7184", {"start": v(11074.06, 3450.73) * mm, "end": v(11048.65, 3453.36) * mm});
            skLineSegment(sketch, "E7185", {"start": v(11048.65, 3453.36) * mm, "end": v(11022.07, 3455.4) * mm});
            skLineSegment(sketch, "E7186", {"start": v(11022.07, 3455.4) * mm, "end": v(10994.35, 3456.77) * mm});
            skLineSegment(sketch, "E7187", {"start": v(10994.35, 3456.77) * mm, "end": v(10965.5, 3457.43) * mm});
            skLineSegment(sketch, "E7188", {"start": v(10965.5, 3457.43) * mm, "end": v(10936.8, 3456.4) * mm});
            skLineSegment(sketch, "E7189", {"start": v(10936.8, 3456.4) * mm, "end": v(10861.79, 3343.3) * mm});
            skLineSegment(sketch, "E7190", {"start": v(10861.79, 3343.3) * mm, "end": v(10872.01, 3316.45) * mm});
            skLineSegment(sketch, "E7191", {"start": v(10872.01, 3316.45) * mm, "end": v(10883.84, 3290.13) * mm});
            skLineSegment(sketch, "E7192", {"start": v(10883.84, 3290.13) * mm, "end": v(10895.9, 3265.13) * mm});
            skLineSegment(sketch, "E7193", {"start": v(10895.9, 3265.13) * mm, "end": v(10908.11, 3241.44) * mm});
            skLineSegment(sketch, "E7194", {"start": v(10908.11, 3241.44) * mm, "end": v(10920.43, 3219.05) * mm});
            skLineSegment(sketch, "E7195", {"start": v(10920.43, 3219.05) * mm, "end": v(10932.78, 3197.96) * mm});
            skLineSegment(sketch, "E7196", {"start": v(10932.78, 3197.96) * mm, "end": v(10945.11, 3178.14) * mm});
            skLineSegment(sketch, "E7197", {"start": v(10945.11, 3178.14) * mm, "end": v(10957.37, 3159.58) * mm});
            skLineSegment(sketch, "E7198", {"start": v(10957.37, 3159.58) * mm, "end": v(10969.48, 3142.26) * mm});
            skLineSegment(sketch, "E7199", {"start": v(10969.48, 3142.26) * mm, "end": v(10981.4, 3126.16) * mm});
            skLineSegment(sketch, "E7200", {"start": v(10981.4, 3126.16) * mm, "end": v(10993.06, 3111.26) * mm});
            skLineSegment(sketch, "E7201", {"start": v(10993.06, 3111.26) * mm, "end": v(11004.42, 3097.52) * mm});
            skLineSegment(sketch, "E7202", {"start": v(11004.42, 3097.52) * mm, "end": v(11015.41, 3084.93) * mm});
            skLineSegment(sketch, "E7203", {"start": v(11015.41, 3084.93) * mm, "end": v(11026, 3073.44) * mm});
            skLineSegment(sketch, "E7204", {"start": v(11026, 3073.44) * mm, "end": v(11036.11, 3063.04) * mm});
            skLineSegment(sketch, "E7205", {"start": v(11036.11, 3063.04) * mm, "end": v(11045.72, 3053.68) * mm});
            skLineSegment(sketch, "E7206", {"start": v(11045.72, 3053.68) * mm, "end": v(11054.76, 3045.33) * mm});
            skLineSegment(sketch, "E7207", {"start": v(11054.76, 3045.33) * mm, "end": v(11063.19, 3037.95) * mm});
            skLineSegment(sketch, "E7208", {"start": v(11063.19, 3037.95) * mm, "end": v(11070.96, 3031.5) * mm});
            skLineSegment(sketch, "E7209", {"start": v(11070.96, 3031.5) * mm, "end": v(11078.04, 3025.96) * mm});
            skLineSegment(sketch, "E7210", {"start": v(11078.04, 3025.96) * mm, "end": v(11084.37, 3021.25) * mm});
            skLineSegment(sketch, "E7211", {"start": v(11084.37, 3021.25) * mm, "end": v(11089.93, 3017.35) * mm});
            skLineSegment(sketch, "E7212", {"start": v(11089.93, 3017.35) * mm, "end": v(11094.67, 3014.22) * mm});
            skLineSegment(sketch, "E7213", {"start": v(11094.67, 3014.22) * mm, "end": v(11098.56, 3011.8) * mm});
            skLineSegment(sketch, "E7214", {"start": v(11098.56, 3011.8) * mm, "end": v(11101.55, 3010.03) * mm});
            skLineSegment(sketch, "E7215", {"start": v(11101.55, 3010.03) * mm, "end": v(11103.63, 3008.88) * mm});
            skLineSegment(sketch, "E7216", {"start": v(11103.63, 3008.88) * mm, "end": v(11104.76, 3008.3) * mm});
            skLineSegment(sketch, "E7217", {"start": v(11104.76, 3008.3) * mm, "end": v(11260.02, 2934.03) * mm});
            skLineSegment(sketch, "E7218", {"start": v(11260.02, 2934.03) * mm, "end": v(11166.5, 2672.9) * mm});
            skLineSegment(sketch, "E7219", {"start": v(11166.5, 2672.9) * mm, "end": v(10999.39, 2714.08) * mm});
            skLineSegment(sketch, "E7220", {"start": v(10999.39, 2714.08) * mm, "end": v(10998.15, 2714.34) * mm});
            skLineSegment(sketch, "E7221", {"start": v(10998.15, 2714.34) * mm, "end": v(10995.81, 2714.77) * mm});
            skLineSegment(sketch, "E7222", {"start": v(10995.81, 2714.77) * mm, "end": v(10992.38, 2715.32) * mm});
            skLineSegment(sketch, "E7223", {"start": v(10992.38, 2715.32) * mm, "end": v(10987.84, 2715.9) * mm});
            skLineSegment(sketch, "E7224", {"start": v(10987.84, 2715.9) * mm, "end": v(10982.18, 2716.5) * mm});
            skLineSegment(sketch, "E7225", {"start": v(10982.18, 2716.5) * mm, "end": v(10975.42, 2717) * mm});
            skLineSegment(sketch, "E7226", {"start": v(10975.42, 2717) * mm, "end": v(10967.53, 2717.4) * mm});
            skLineSegment(sketch, "E7227", {"start": v(10967.53, 2717.4) * mm, "end": v(10958.54, 2717.6) * mm});
            skLineSegment(sketch, "E7228", {"start": v(10958.54, 2717.6) * mm, "end": v(10948.44, 2717.56) * mm});
            skLineSegment(sketch, "E7229", {"start": v(10948.44, 2717.56) * mm, "end": v(10937.25, 2717.2) * mm});
            skLineSegment(sketch, "E7230", {"start": v(10937.25, 2717.2) * mm, "end": v(10924.96, 2716.5) * mm});
            skLineSegment(sketch, "E7231", {"start": v(10924.96, 2716.5) * mm, "end": v(10911.6, 2715.36) * mm});
            skLineSegment(sketch, "E7232", {"start": v(10911.6, 2715.36) * mm, "end": v(10897.18, 2713.74) * mm});
            skLineSegment(sketch, "E7233", {"start": v(10897.18, 2713.74) * mm, "end": v(10881.71, 2711.59) * mm});
            skLineSegment(sketch, "E7234", {"start": v(10881.71, 2711.59) * mm, "end": v(10865.22, 2708.84) * mm});
            skLineSegment(sketch, "E7235", {"start": v(10865.22, 2708.84) * mm, "end": v(10847.72, 2705.44) * mm});
            skLineSegment(sketch, "E7236", {"start": v(10847.72, 2705.44) * mm, "end": v(10829.25, 2701.32) * mm});
            skLineSegment(sketch, "E7237", {"start": v(10829.25, 2701.32) * mm, "end": v(10809.82, 2696.45) * mm});
            skLineSegment(sketch, "E7238", {"start": v(10809.82, 2696.45) * mm, "end": v(10789.46, 2690.76) * mm});
            skLineSegment(sketch, "E7239", {"start": v(10789.46, 2690.76) * mm, "end": v(10768.22, 2684.2) * mm});
            skLineSegment(sketch, "E7240", {"start": v(10768.22, 2684.2) * mm, "end": v(10746.1, 2676.71) * mm});
            skLineSegment(sketch, "E7241", {"start": v(10746.1, 2676.71) * mm, "end": v(10723.17, 2668.26) * mm});
            skLineSegment(sketch, "E7242", {"start": v(10723.17, 2668.26) * mm, "end": v(10699.44, 2658.78) * mm});
            skLineSegment(sketch, "E7243", {"start": v(10699.44, 2658.78) * mm, "end": v(10674.97, 2648.23) * mm});
            skLineSegment(sketch, "E7244", {"start": v(10674.97, 2648.23) * mm, "end": v(10649.78, 2636.57) * mm});
            skLineSegment(sketch, "E7245", {"start": v(10649.78, 2636.57) * mm, "end": v(10623.93, 2623.74) * mm});
            skLineSegment(sketch, "E7246", {"start": v(10623.93, 2623.74) * mm, "end": v(10599, 2609.5) * mm});
            skLineSegment(sketch, "E7247", {"start": v(10599, 2609.5) * mm, "end": v(10585.14, 2474.48) * mm});
            skLineSegment(sketch, "E7248", {"start": v(10585.14, 2474.48) * mm, "end": v(10606.66, 2455.47) * mm});
            skLineSegment(sketch, "E7249", {"start": v(10606.66, 2455.47) * mm, "end": v(10629.37, 2437.66) * mm});
            skLineSegment(sketch, "E7250", {"start": v(10629.37, 2437.66) * mm, "end": v(10651.67, 2421.12) * mm});
            skLineSegment(sketch, "E7251", {"start": v(10651.67, 2421.12) * mm, "end": v(10673.5, 2405.82) * mm});
            skLineSegment(sketch, "E7252", {"start": v(10673.5, 2405.82) * mm, "end": v(10694.8, 2391.73) * mm});
            skLineSegment(sketch, "E7253", {"start": v(10694.8, 2391.73) * mm, "end": v(10715.54, 2378.79) * mm});
            skLineSegment(sketch, "E7254", {"start": v(10715.54, 2378.79) * mm, "end": v(10735.67, 2366.97) * mm});
            skLineSegment(sketch, "E7255", {"start": v(10735.67, 2366.97) * mm, "end": v(10755.14, 2356.23) * mm});
            skLineSegment(sketch, "E7256", {"start": v(10755.14, 2356.23) * mm, "end": v(10773.92, 2346.53) * mm});
            skLineSegment(sketch, "E7257", {"start": v(10773.92, 2346.53) * mm, "end": v(10791.95, 2337.8) * mm});
            skLineSegment(sketch, "E7258", {"start": v(10791.95, 2337.8) * mm, "end": v(10809.2, 2330.03) * mm});
            skLineSegment(sketch, "E7259", {"start": v(10809.2, 2330.03) * mm, "end": v(10825.65, 2323.15) * mm});
            skLineSegment(sketch, "E7260", {"start": v(10825.65, 2323.15) * mm, "end": v(10841.24, 2317.1) * mm});
            skLineSegment(sketch, "E7261", {"start": v(10841.24, 2317.1) * mm, "end": v(10855.95, 2311.85) * mm});
            skLineSegment(sketch, "E7262", {"start": v(10855.95, 2311.85) * mm, "end": v(10869.74, 2307.34) * mm});
            skLineSegment(sketch, "E7263", {"start": v(10869.74, 2307.34) * mm, "end": v(10882.6, 2303.52) * mm});
            skLineSegment(sketch, "E7264", {"start": v(10882.6, 2303.52) * mm, "end": v(10894.48, 2300.33) * mm});
            skLineSegment(sketch, "E7265", {"start": v(10894.48, 2300.33) * mm, "end": v(10905.37, 2297.71) * mm});
            skLineSegment(sketch, "E7266", {"start": v(10905.37, 2297.71) * mm, "end": v(10915.25, 2295.62) * mm});
            skLineSegment(sketch, "E7267", {"start": v(10915.25, 2295.62) * mm, "end": v(10924.1, 2294) * mm});
            skLineSegment(sketch, "E7268", {"start": v(10924.1, 2294) * mm, "end": v(10931.9, 2292.77) * mm});
            skLineSegment(sketch, "E7269", {"start": v(10931.9, 2292.77) * mm, "end": v(10938.62, 2291.9) * mm});
            skLineSegment(sketch, "E7270", {"start": v(10938.62, 2291.9) * mm, "end": v(10944.28, 2291.33) * mm});
            skLineSegment(sketch, "E7271", {"start": v(10944.28, 2291.33) * mm, "end": v(10948.84, 2290.98) * mm});
            skLineSegment(sketch, "E7272", {"start": v(10948.84, 2290.98) * mm, "end": v(10952.32, 2290.82) * mm});
            skLineSegment(sketch, "E7273", {"start": v(10952.32, 2290.82) * mm, "end": v(10954.7, 2290.77) * mm});
            skLineSegment(sketch, "E7274", {"start": v(10954.7, 2290.77) * mm, "end": v(10955.96, 2290.77) * mm});
            skLineSegment(sketch, "E7275", {"start": v(10955.96, 2290.77) * mm, "end": v(11127.95, 2297.17) * mm});
            skLineSegment(sketch, "E7276", {"start": v(11127.95, 2297.17) * mm, "end": v(11166.5, 2022.48) * mm});
            skLineSegment(sketch, "E7277", {"start": v(11166.5, 2022.48) * mm, "end": v(10999.4, 1981.29) * mm});
            skLineSegment(sketch, "E7278", {"start": v(10999.4, 1981.29) * mm, "end": v(10998.17, 1980.94) * mm});
            skLineSegment(sketch, "E7279", {"start": v(10998.17, 1980.94) * mm, "end": v(10995.9, 1980.24) * mm});
            skLineSegment(sketch, "E7280", {"start": v(10995.9, 1980.24) * mm, "end": v(10992.6, 1979.13) * mm});
            skLineSegment(sketch, "E7281", {"start": v(10992.6, 1979.13) * mm, "end": v(10988.31, 1977.54) * mm});
            skLineSegment(sketch, "E7282", {"start": v(10988.31, 1977.54) * mm, "end": v(10983.03, 1975.43) * mm});
            skLineSegment(sketch, "E7283", {"start": v(10983.03, 1975.43) * mm, "end": v(10976.8, 1972.74) * mm});
            skLineSegment(sketch, "E7284", {"start": v(10976.8, 1972.74) * mm, "end": v(10969.64, 1969.42) * mm});
            skLineSegment(sketch, "E7285", {"start": v(10969.64, 1969.42) * mm, "end": v(10961.59, 1965.42) * mm});
            skLineSegment(sketch, "E7286", {"start": v(10961.59, 1965.42) * mm, "end": v(10952.66, 1960.7) * mm});
            skLineSegment(sketch, "E7287", {"start": v(10952.66, 1960.7) * mm, "end": v(10942.91, 1955.18) * mm});
            skLineSegment(sketch, "E7288", {"start": v(10942.91, 1955.18) * mm, "end": v(10932.36, 1948.84) * mm});
            skLineSegment(sketch, "E7289", {"start": v(10932.36, 1948.84) * mm, "end": v(10921.06, 1941.63) * mm});
            skLineSegment(sketch, "E7290", {"start": v(10921.06, 1941.63) * mm, "end": v(10909.04, 1933.5) * mm});
            skLineSegment(sketch, "E7291", {"start": v(10909.04, 1933.5) * mm, "end": v(10896.35, 1924.4) * mm});
            skLineSegment(sketch, "E7292", {"start": v(10896.35, 1924.4) * mm, "end": v(10883.02, 1914.3) * mm});
            skLineSegment(sketch, "E7293", {"start": v(10883.02, 1914.3) * mm, "end": v(10869.11, 1903.15) * mm});
            skLineSegment(sketch, "E7294", {"start": v(10869.11, 1903.15) * mm, "end": v(10854.66, 1890.92) * mm});
            skLineSegment(sketch, "E7295", {"start": v(10854.66, 1890.92) * mm, "end": v(10839.73, 1877.58) * mm});
            skLineSegment(sketch, "E7296", {"start": v(10839.73, 1877.58) * mm, "end": v(10824.35, 1863.08) * mm});
            skLineSegment(sketch, "E7297", {"start": v(10824.35, 1863.08) * mm, "end": v(10808.59, 1847.4) * mm});
            skLineSegment(sketch, "E7298", {"start": v(10808.59, 1847.4) * mm, "end": v(10792.48, 1830.5) * mm});
            skLineSegment(sketch, "E7299", {"start": v(10792.48, 1830.5) * mm, "end": v(10776.1, 1812.35) * mm});
            skLineSegment(sketch, "E7300", {"start": v(10776.1, 1812.35) * mm, "end": v(10759.5, 1792.93) * mm});
            skLineSegment(sketch, "E7301", {"start": v(10759.5, 1792.93) * mm, "end": v(10742.73, 1772.22) * mm});
            skLineSegment(sketch, "E7302", {"start": v(10742.73, 1772.22) * mm, "end": v(10725.85, 1750.18) * mm});
            skLineSegment(sketch, "E7303", {"start": v(10725.85, 1750.18) * mm, "end": v(10708.92, 1726.81) * mm});
            skLineSegment(sketch, "E7304", {"start": v(10708.92, 1726.81) * mm, "end": v(10693.46, 1702.6) * mm});
            skLineSegment(sketch, "E7305", {"start": v(10693.46, 1702.6) * mm, "end": v(10743.94, 1576.62) * mm});
            skLineSegment(sketch, "E7306", {"start": v(10743.94, 1576.62) * mm, "end": v(10771.83, 1569.8) * mm});
            skLineSegment(sketch, "E7307", {"start": v(10771.83, 1569.8) * mm, "end": v(10800.22, 1564.58) * mm});
            skLineSegment(sketch, "E7308", {"start": v(10800.22, 1564.58) * mm, "end": v(10827.64, 1560.3) * mm});
            skLineSegment(sketch, "E7309", {"start": v(10827.64, 1560.3) * mm, "end": v(10854.08, 1556.9) * mm});
            skLineSegment(sketch, "E7310", {"start": v(10854.08, 1556.9) * mm, "end": v(10879.5, 1554.3) * mm});
            skLineSegment(sketch, "E7311", {"start": v(10879.5, 1554.3) * mm, "end": v(10903.87, 1552.5) * mm});
            skLineSegment(sketch, "E7312", {"start": v(10903.87, 1552.5) * mm, "end": v(10927.19, 1551.38) * mm});
            skLineSegment(sketch, "E7313", {"start": v(10927.19, 1551.38) * mm, "end": v(10949.42, 1550.92) * mm});
            skLineSegment(sketch, "E7314", {"start": v(10949.42, 1550.92) * mm, "end": v(10970.56, 1551.06) * mm});
            skLineSegment(sketch, "E7315", {"start": v(10970.56, 1551.06) * mm, "end": v(10990.58, 1551.72) * mm});
            skLineSegment(sketch, "E7316", {"start": v(10990.58, 1551.72) * mm, "end": v(11009.47, 1552.85) * mm});
            skLineSegment(sketch, "E7317", {"start": v(11009.47, 1552.85) * mm, "end": v(11027.23, 1554.4) * mm});
            skLineSegment(sketch, "E7318", {"start": v(11027.23, 1554.4) * mm, "end": v(11043.84, 1556.29) * mm});
            skLineSegment(sketch, "E7319", {"start": v(11043.84, 1556.29) * mm, "end": v(11059.3, 1558.47) * mm});
            skLineSegment(sketch, "E7320", {"start": v(11059.3, 1558.47) * mm, "end": v(11073.61, 1560.89) * mm});
            skLineSegment(sketch, "E7321", {"start": v(11073.61, 1560.89) * mm, "end": v(11086.77, 1563.48) * mm});
            skLineSegment(sketch, "E7322", {"start": v(11086.77, 1563.48) * mm, "end": v(11098.78, 1566.17) * mm});
            skLineSegment(sketch, "E7323", {"start": v(11098.78, 1566.17) * mm, "end": v(11109.64, 1568.92) * mm});
            skLineSegment(sketch, "E7324", {"start": v(11109.64, 1568.92) * mm, "end": v(11119.36, 1571.66) * mm});
            skLineSegment(sketch, "E7325", {"start": v(11119.36, 1571.66) * mm, "end": v(11127.94, 1574.33) * mm});
            skLineSegment(sketch, "E7326", {"start": v(11127.94, 1574.33) * mm, "end": v(11135.41, 1576.87) * mm});
            skLineSegment(sketch, "E7327", {"start": v(11135.41, 1576.87) * mm, "end": v(11141.78, 1579.23) * mm});
            skLineSegment(sketch, "E7328", {"start": v(11141.78, 1579.23) * mm, "end": v(11147.05, 1581.35) * mm});
            skLineSegment(sketch, "E7329", {"start": v(11147.05, 1581.35) * mm, "end": v(11151.26, 1583.17) * mm});
            skLineSegment(sketch, "E7330", {"start": v(11151.26, 1583.17) * mm, "end": v(11154.4, 1584.63) * mm});
            skLineSegment(sketch, "E7331", {"start": v(11154.4, 1584.63) * mm, "end": v(11156.53, 1585.69) * mm});
            skLineSegment(sketch, "E7332", {"start": v(11156.53, 1585.69) * mm, "end": v(11157.65, 1586.29) * mm});
            skLineSegment(sketch, "E7333", {"start": v(11157.65, 1586.29) * mm, "end": v(11306.98, 1671.88) * mm});
            skLineSegment(sketch, "E7334", {"start": v(11306.98, 1671.88) * mm, "end": v(11468.76, 1446.57) * mm});
            skLineSegment(sketch, "E7335", {"start": v(11468.76, 1446.57) * mm, "end": v(11339.93, 1332.43) * mm});
            skLineSegment(sketch, "E7336", {"start": v(11339.93, 1332.43) * mm, "end": v(11339.01, 1331.56) * mm});
            skLineSegment(sketch, "E7337", {"start": v(11339.01, 1331.56) * mm, "end": v(11337.33, 1329.89) * mm});
            skLineSegment(sketch, "E7338", {"start": v(11337.33, 1329.89) * mm, "end": v(11334.94, 1327.37) * mm});
            skLineSegment(sketch, "E7339", {"start": v(11334.94, 1327.37) * mm, "end": v(11331.87, 1323.97) * mm});
            skLineSegment(sketch, "E7340", {"start": v(11331.87, 1323.97) * mm, "end": v(11328.18, 1319.65) * mm});
            skLineSegment(sketch, "E7341", {"start": v(11328.18, 1319.65) * mm, "end": v(11323.9, 1314.37) * mm});
            skLineSegment(sketch, "E7342", {"start": v(11323.9, 1314.37) * mm, "end": v(11319.1, 1308.1) * mm});
            skLineSegment(sketch, "E7343", {"start": v(11319.1, 1308.1) * mm, "end": v(11313.83, 1300.82) * mm});
            skLineSegment(sketch, "E7344", {"start": v(11313.83, 1300.82) * mm, "end": v(11308.13, 1292.48) * mm});
            skLineSegment(sketch, "E7345", {"start": v(11308.13, 1292.48) * mm, "end": v(11302.06, 1283.07) * mm});
            skLineSegment(sketch, "E7346", {"start": v(11302.06, 1283.07) * mm, "end": v(11295.67, 1272.56) * mm});
            skLineSegment(sketch, "E7347", {"start": v(11295.67, 1272.56) * mm, "end": v(11289.01, 1260.92) * mm});
            skLineSegment(sketch, "E7348", {"start": v(11289.01, 1260.92) * mm, "end": v(11282.15, 1248.13) * mm});
            skLineSegment(sketch, "E7349", {"start": v(11282.15, 1248.13) * mm, "end": v(11275.14, 1234.17) * mm});
            skLineSegment(sketch, "E7350", {"start": v(11275.14, 1234.17) * mm, "end": v(11268.03, 1219.04) * mm});
            skLineSegment(sketch, "E7351", {"start": v(11268.03, 1219.04) * mm, "end": v(11260.9, 1202.7) * mm});
            skLineSegment(sketch, "E7352", {"start": v(11260.9, 1202.7) * mm, "end": v(11253.78, 1185.17) * mm});
            skLineSegment(sketch, "E7353", {"start": v(11253.78, 1185.17) * mm, "end": v(11246.76, 1166.4) * mm});
            skLineSegment(sketch, "E7354", {"start": v(11246.76, 1166.4) * mm, "end": v(11239.88, 1146.42) * mm});
            skLineSegment(sketch, "E7355", {"start": v(11239.88, 1146.42) * mm, "end": v(11233.2, 1125.2) * mm});
            skLineSegment(sketch, "E7356", {"start": v(11233.2, 1125.2) * mm, "end": v(11226.8, 1102.76) * mm});
            skLineSegment(sketch, "E7357", {"start": v(11226.8, 1102.76) * mm, "end": v(11220.74, 1079.08) * mm});
            skLineSegment(sketch, "E7358", {"start": v(11220.74, 1079.08) * mm, "end": v(11215.06, 1054.17) * mm});
            skLineSegment(sketch, "E7359", {"start": v(11215.06, 1054.17) * mm, "end": v(11209.83, 1028.04) * mm});
            skLineSegment(sketch, "E7360", {"start": v(11209.83, 1028.04) * mm, "end": v(11205.13, 1000.68) * mm});
            skLineSegment(sketch, "E7361", {"start": v(11205.13, 1000.68) * mm, "end": v(11201, 972.12) * mm});
            skLineSegment(sketch, "E7362", {"start": v(11201, 972.12) * mm, "end": v(11198.56, 943.5) * mm});
            skLineSegment(sketch, "E7363", {"start": v(11198.56, 943.5) * mm, "end": v(11301.8, 855.4) * mm});
            skLineSegment(sketch, "E7364", {"start": v(11301.8, 855.4) * mm, "end": v(11329.68, 862.32) * mm});
            skLineSegment(sketch, "E7365", {"start": v(11329.68, 862.32) * mm, "end": v(11357.23, 870.9) * mm});
            skLineSegment(sketch, "E7366", {"start": v(11357.23, 870.9) * mm, "end": v(11383.5, 879.85) * mm});
            skLineSegment(sketch, "E7367", {"start": v(11383.5, 879.85) * mm, "end": v(11408.5, 889.12) * mm});
            skLineSegment(sketch, "E7368", {"start": v(11408.5, 889.12) * mm, "end": v(11432.2, 898.64) * mm});
            skLineSegment(sketch, "E7369", {"start": v(11432.2, 898.64) * mm, "end": v(11454.63, 908.37) * mm});
            skLineSegment(sketch, "E7370", {"start": v(11454.63, 908.37) * mm, "end": v(11475.8, 918.22) * mm});
            skLineSegment(sketch, "E7371", {"start": v(11475.8, 918.22) * mm, "end": v(11495.69, 928.14) * mm});
            skLineSegment(sketch, "E7372", {"start": v(11495.69, 928.14) * mm, "end": v(11514.34, 938.08) * mm});
            skLineSegment(sketch, "E7373", {"start": v(11514.34, 938.08) * mm, "end": v(11531.76, 947.97) * mm});
            skLineSegment(sketch, "E7374", {"start": v(11531.76, 947.97) * mm, "end": v(11547.97, 957.76) * mm});
            skLineSegment(sketch, "E7375", {"start": v(11547.97, 957.76) * mm, "end": v(11562.97, 967.37) * mm});
            skLineSegment(sketch, "E7376", {"start": v(11562.97, 967.37) * mm, "end": v(11576.8, 976.77) * mm});
            skLineSegment(sketch, "E7377", {"start": v(11576.8, 976.77) * mm, "end": v(11589.48, 985.9) * mm});
            skLineSegment(sketch, "E7378", {"start": v(11589.48, 985.9) * mm, "end": v(11601.02, 994.68) * mm});
            skLineSegment(sketch, "E7379", {"start": v(11601.02, 994.68) * mm, "end": v(11611.47, 1003.09) * mm});
            skLineSegment(sketch, "E7380", {"start": v(11611.47, 1003.09) * mm, "end": v(11620.85, 1011.05) * mm});
            skLineSegment(sketch, "E7381", {"start": v(11620.85, 1011.05) * mm, "end": v(11629.2, 1018.53) * mm});
            skLineSegment(sketch, "E7382", {"start": v(11629.2, 1018.53) * mm, "end": v(11636.53, 1025.48) * mm});
            skLineSegment(sketch, "E7383", {"start": v(11636.53, 1025.48) * mm, "end": v(11642.89, 1031.83) * mm});
            skLineSegment(sketch, "E7384", {"start": v(11642.89, 1031.83) * mm, "end": v(11648.32, 1037.56) * mm});
            skLineSegment(sketch, "E7385", {"start": v(11648.32, 1037.56) * mm, "end": v(11652.86, 1042.6) * mm});
            skLineSegment(sketch, "E7386", {"start": v(11652.86, 1042.6) * mm, "end": v(11656.55, 1046.93) * mm});
            skLineSegment(sketch, "E7387", {"start": v(11656.55, 1046.93) * mm, "end": v(11659.42, 1050.5) * mm});
            skLineSegment(sketch, "E7388", {"start": v(11659.42, 1050.5) * mm, "end": v(11661.53, 1053.25) * mm});
            skLineSegment(sketch, "E7389", {"start": v(11661.53, 1053.25) * mm, "end": v(11662.92, 1055.18) * mm});
            skLineSegment(sketch, "E7390", {"start": v(11662.92, 1055.18) * mm, "end": v(11663.64, 1056.23) * mm});
            skLineSegment(sketch, "E7391", {"start": v(11663.64, 1056.23) * mm, "end": v(11756.08, 1201.4) * mm});
            skLineSegment(sketch, "E7392", {"start": v(11756.08, 1201.4) * mm, "end": v(12004.04, 1077.1) * mm});
            skLineSegment(sketch, "E7393", {"start": v(12004.04, 1077.1) * mm, "end": v(11943.01, 916.16) * mm});
            skLineSegment(sketch, "E7394", {"start": v(11943.01, 916.16) * mm, "end": v(11942.6, 914.96) * mm});
            skLineSegment(sketch, "E7395", {"start": v(11942.6, 914.96) * mm, "end": v(11941.9, 912.7) * mm});
            skLineSegment(sketch, "E7396", {"start": v(11941.9, 912.7) * mm, "end": v(11940.94, 909.35) * mm});
            skLineSegment(sketch, "E7397", {"start": v(11940.94, 909.35) * mm, "end": v(11939.8, 904.92) * mm});
            skLineSegment(sketch, "E7398", {"start": v(11939.8, 904.92) * mm, "end": v(11938.54, 899.37) * mm});
            skLineSegment(sketch, "E7399", {"start": v(11938.54, 899.37) * mm, "end": v(11937.21, 892.72) * mm});
            skLineSegment(sketch, "E7400", {"start": v(11937.21, 892.72) * mm, "end": v(11935.88, 884.94) * mm});
            skLineSegment(sketch, "E7401", {"start": v(11935.88, 884.94) * mm, "end": v(11934.6, 876.04) * mm});
            skLineSegment(sketch, "E7402", {"start": v(11934.6, 876.04) * mm, "end": v(11933.42, 866) * mm});
            skLineSegment(sketch, "E7403", {"start": v(11933.42, 866) * mm, "end": v(11932.42, 854.85) * mm});
            skLineSegment(sketch, "E7404", {"start": v(11932.42, 854.85) * mm, "end": v(11931.64, 842.57) * mm});
            skLineSegment(sketch, "E7405", {"start": v(11931.64, 842.57) * mm, "end": v(11931.16, 829.17) * mm});
            skLineSegment(sketch, "E7406", {"start": v(11931.16, 829.17) * mm, "end": v(11931.02, 814.66) * mm});
            skLineSegment(sketch, "E7407", {"start": v(11931.02, 814.66) * mm, "end": v(11931.3, 799.04) * mm});
            skLineSegment(sketch, "E7408", {"start": v(11931.3, 799.04) * mm, "end": v(11932.04, 782.34) * mm});
            skLineSegment(sketch, "E7409", {"start": v(11932.04, 782.34) * mm, "end": v(11933.31, 764.56) * mm});
            skLineSegment(sketch, "E7410", {"start": v(11933.31, 764.56) * mm, "end": v(11935.17, 745.73) * mm});
            skLineSegment(sketch, "E7411", {"start": v(11935.17, 745.73) * mm, "end": v(11937.66, 725.85) * mm});
            skLineSegment(sketch, "E7412", {"start": v(11937.66, 725.85) * mm, "end": v(11940.86, 704.96) * mm});
            skLineSegment(sketch, "E7413", {"start": v(11940.86, 704.96) * mm, "end": v(11944.81, 683.08) * mm});
            skLineSegment(sketch, "E7414", {"start": v(11944.81, 683.08) * mm, "end": v(11949.58, 660.22) * mm});
            skLineSegment(sketch, "E7415", {"start": v(11949.58, 660.22) * mm, "end": v(11955.2, 636.43) * mm});
            skLineSegment(sketch, "E7416", {"start": v(11955.2, 636.43) * mm, "end": v(11961.75, 611.74) * mm});
            skLineSegment(sketch, "E7417", {"start": v(11961.75, 611.74) * mm, "end": v(11969.27, 586.17) * mm});
            skLineSegment(sketch, "E7418", {"start": v(11969.27, 586.17) * mm, "end": v(11977.82, 559.76) * mm});
            skLineSegment(sketch, "E7419", {"start": v(11977.82, 559.76) * mm, "end": v(11987.44, 532.55) * mm});
            skLineSegment(sketch, "E7420", {"start": v(11987.44, 532.55) * mm, "end": v(11998.57, 506.08) * mm});
            skLineSegment(sketch, "E7421", {"start": v(11998.57, 506.08) * mm, "end": v(12130.93, 476.05) * mm});
            skLineSegment(sketch, "E7422", {"start": v(12130.93, 476.05) * mm, "end": v(12152.4, 495.13) * mm});
            skLineSegment(sketch, "E7423", {"start": v(12152.4, 495.13) * mm, "end": v(12172.82, 515.53) * mm});
            skLineSegment(sketch, "E7424", {"start": v(12172.82, 515.53) * mm, "end": v(12191.92, 535.66) * mm});
            skLineSegment(sketch, "E7425", {"start": v(12191.92, 535.66) * mm, "end": v(12209.74, 555.49) * mm});
            skLineSegment(sketch, "E7426", {"start": v(12209.74, 555.49) * mm, "end": v(12226.3, 574.94) * mm});
            skLineSegment(sketch, "E7427", {"start": v(12226.3, 574.94) * mm, "end": v(12241.64, 593.97) * mm});
            skLineSegment(sketch, "E7428", {"start": v(12241.64, 593.97) * mm, "end": v(12255.8, 612.53) * mm});
            skLineSegment(sketch, "E7429", {"start": v(12255.8, 612.53) * mm, "end": v(12268.8, 630.57) * mm});
            skLineSegment(sketch, "E7430", {"start": v(12268.8, 630.57) * mm, "end": v(12280.7, 648.03) * mm});
            skLineSegment(sketch, "E7431", {"start": v(12280.7, 648.03) * mm, "end": v(12291.53, 664.88) * mm});
            skLineSegment(sketch, "E7432", {"start": v(12291.53, 664.88) * mm, "end": v(12301.34, 681.08) * mm});
            skLineSegment(sketch, "E7433", {"start": v(12301.34, 681.08) * mm, "end": v(12310.15, 696.57) * mm});
            skLineSegment(sketch, "E7434", {"start": v(12310.15, 696.57) * mm, "end": v(12318.03, 711.32) * mm});
            skLineSegment(sketch, "E7435", {"start": v(12318.03, 711.32) * mm, "end": v(12325.01, 725.28) * mm});
            skLineSegment(sketch, "E7436", {"start": v(12325.01, 725.28) * mm, "end": v(12331.15, 738.43) * mm});
            skLineSegment(sketch, "E7437", {"start": v(12331.15, 738.43) * mm, "end": v(12336.5, 750.73) * mm});
            skLineSegment(sketch, "E7438", {"start": v(12336.5, 750.73) * mm, "end": v(12341.1, 762.14) * mm});
            skLineSegment(sketch, "E7439", {"start": v(12341.1, 762.14) * mm, "end": v(12345.01, 772.64) * mm});
            skLineSegment(sketch, "E7440", {"start": v(12345.01, 772.64) * mm, "end": v(12348.28, 782.2) * mm});
            skLineSegment(sketch, "E7441", {"start": v(12348.28, 782.2) * mm, "end": v(12350.96, 790.78) * mm});
            skLineSegment(sketch, "E7442", {"start": v(12350.96, 790.78) * mm, "end": v(12353.11, 798.38) * mm});
            skLineSegment(sketch, "E7443", {"start": v(12353.11, 798.38) * mm, "end": v(12354.78, 804.95) * mm});
            skLineSegment(sketch, "E7444", {"start": v(12354.78, 804.95) * mm, "end": v(12356.04, 810.5) * mm});
            skLineSegment(sketch, "E7445", {"start": v(12356.04, 810.5) * mm, "end": v(12356.93, 814.99) * mm});
            skLineSegment(sketch, "E7446", {"start": v(12356.93, 814.99) * mm, "end": v(12357.51, 818.42) * mm});
            skLineSegment(sketch, "E7447", {"start": v(12357.51, 818.42) * mm, "end": v(12357.85, 820.76) * mm});
            skLineSegment(sketch, "E7448", {"start": v(12357.85, 820.76) * mm, "end": v(12358, 822.03) * mm});
            skLineSegment(sketch, "E7449", {"start": v(12358, 822.03) * mm, "end": v(12372.38, 993.54) * mm});
            skLineSegment(sketch, "E7450", {"start": v(12372.38, 993.54) * mm, "end": v(12649.71, 998.7) * mm});
            skLineSegment(sketch, "E7451", {"start": v(12649.71, 998.7) * mm, "end": v(12670.46, 827.84) * mm});
            skLineSegment(sketch, "E7452", {"start": v(12670.46, 827.84) * mm, "end": v(12670.65, 826.58) * mm});
            skLineSegment(sketch, "E7453", {"start": v(12670.65, 826.58) * mm, "end": v(12671.08, 824.25) * mm});
            skLineSegment(sketch, "E7454", {"start": v(12671.08, 824.25) * mm, "end": v(12671.79, 820.84) * mm});
            skLineSegment(sketch, "E7455", {"start": v(12671.79, 820.84) * mm, "end": v(12672.85, 816.39) * mm});
            skLineSegment(sketch, "E7456", {"start": v(12672.85, 816.39) * mm, "end": v(12674.3, 810.9) * mm});
            skLineSegment(sketch, "E7457", {"start": v(12674.3, 810.9) * mm, "end": v(12676.22, 804.38) * mm});
            skLineSegment(sketch, "E7458", {"start": v(12676.22, 804.38) * mm, "end": v(12678.65, 796.88) * mm});
            skLineSegment(sketch, "E7459", {"start": v(12678.65, 796.88) * mm, "end": v(12681.65, 788.4) * mm});
            skLineSegment(sketch, "E7460", {"start": v(12681.65, 788.4) * mm, "end": v(12685.27, 778.97) * mm});
            skLineSegment(sketch, "E7461", {"start": v(12685.27, 778.97) * mm, "end": v(12689.57, 768.62) * mm});
            skLineSegment(sketch, "E7462", {"start": v(12689.57, 768.62) * mm, "end": v(12694.6, 757.39) * mm});
            skLineSegment(sketch, "E7463", {"start": v(12694.6, 757.39) * mm, "end": v(12700.4, 745.3) * mm});
            skLineSegment(sketch, "E7464", {"start": v(12700.4, 745.3) * mm, "end": v(12707.02, 732.39) * mm});
            skLineSegment(sketch, "E7465", {"start": v(12707.02, 732.39) * mm, "end": v(12714.52, 718.69) * mm});
            skLineSegment(sketch, "E7466", {"start": v(12714.52, 718.69) * mm, "end": v(12722.94, 704.24) * mm});
            skLineSegment(sketch, "E7467", {"start": v(12722.94, 704.24) * mm, "end": v(12732.32, 689.1) * mm});
            skLineSegment(sketch, "E7468", {"start": v(12732.32, 689.1) * mm, "end": v(12742.72, 673.28) * mm});
            skLineSegment(sketch, "E7469", {"start": v(12742.72, 673.28) * mm, "end": v(12754.17, 656.84) * mm});
            skLineSegment(sketch, "E7470", {"start": v(12754.17, 656.84) * mm, "end": v(12766.7, 639.82) * mm});
            skLineSegment(sketch, "E7471", {"start": v(12766.7, 639.82) * mm, "end": v(12780.38, 622.28) * mm});
            skLineSegment(sketch, "E7472", {"start": v(12780.38, 622.28) * mm, "end": v(12795.21, 604.26) * mm});
            skLineSegment(sketch, "E7473", {"start": v(12795.21, 604.26) * mm, "end": v(12811.25, 585.82) * mm});
            skLineSegment(sketch, "E7474", {"start": v(12811.25, 585.82) * mm, "end": v(12828.53, 567) * mm});
            skLineSegment(sketch, "E7475", {"start": v(12828.53, 567) * mm, "end": v(12847.07, 547.85) * mm});
            skLineSegment(sketch, "E7476", {"start": v(12847.07, 547.85) * mm, "end": v(12866.9, 528.43) * mm});
            skLineSegment(sketch, "E7477", {"start": v(12866.9, 528.43) * mm, "end": v(12888.07, 508.8) * mm});
            skLineSegment(sketch, "E7478", {"start": v(12888.07, 508.8) * mm, "end": v(12910.23, 490.54) * mm});
            skLineSegment(sketch, "E7479", {"start": v(12910.23, 490.54) * mm, "end": v(13041.38, 525.47) * mm});
            skLineSegment(sketch, "E7480", {"start": v(13041.38, 525.47) * mm, "end": v(13051.53, 552.34) * mm});
            skLineSegment(sketch, "E7481", {"start": v(13051.53, 552.34) * mm, "end": v(13060.13, 579.88) * mm});
            skLineSegment(sketch, "E7482", {"start": v(13060.13, 579.88) * mm, "end": v(13067.68, 606.6) * mm});
            skLineSegment(sketch, "E7483", {"start": v(13067.68, 606.6) * mm, "end": v(13074.25, 632.43) * mm});
            skLineSegment(sketch, "E7484", {"start": v(13074.25, 632.43) * mm, "end": v(13079.87, 657.35) * mm});
            skLineSegment(sketch, "E7485", {"start": v(13079.87, 657.35) * mm, "end": v(13084.61, 681.33) * mm});
            skLineSegment(sketch, "E7486", {"start": v(13084.61, 681.33) * mm, "end": v(13088.53, 704.34) * mm});
            skLineSegment(sketch, "E7487", {"start": v(13088.53, 704.34) * mm, "end": v(13091.66, 726.36) * mm});
            skLineSegment(sketch, "E7488", {"start": v(13091.66, 726.36) * mm, "end": v(13094.08, 747.35) * mm});
            skLineSegment(sketch, "E7489", {"start": v(13094.08, 747.35) * mm, "end": v(13095.83, 767.3) * mm});
            skLineSegment(sketch, "E7490", {"start": v(13095.83, 767.3) * mm, "end": v(13096.99, 786.2) * mm});
            skLineSegment(sketch, "E7491", {"start": v(13096.99, 786.2) * mm, "end": v(13097.6, 804.01) * mm});
            skLineSegment(sketch, "E7492", {"start": v(13097.6, 804.01) * mm, "end": v(13097.72, 820.73) * mm});
            skLineSegment(sketch, "E7493", {"start": v(13097.72, 820.73) * mm, "end": v(13097.41, 836.35) * mm});
            skLineSegment(sketch, "E7494", {"start": v(13097.41, 836.35) * mm, "end": v(13096.74, 850.84) * mm});
            skLineSegment(sketch, "E7495", {"start": v(13096.74, 850.84) * mm, "end": v(13095.76, 864.22) * mm});
            skLineSegment(sketch, "E7496", {"start": v(13095.76, 864.22) * mm, "end": v(13094.53, 876.46) * mm});
            skLineSegment(sketch, "E7497", {"start": v(13094.53, 876.46) * mm, "end": v(13093.11, 887.57) * mm});
            skLineSegment(sketch, "E7498", {"start": v(13093.11, 887.57) * mm, "end": v(13091.56, 897.55) * mm});
            skLineSegment(sketch, "E7499", {"start": v(13091.56, 897.55) * mm, "end": v(13089.95, 906.4) * mm});
            skLineSegment(sketch, "E7500", {"start": v(13089.95, 906.4) * mm, "end": v(13088.32, 914.12) * mm});
            skLineSegment(sketch, "E7501", {"start": v(13088.32, 914.12) * mm, "end": v(13086.75, 920.72) * mm});
            skLineSegment(sketch, "E7502", {"start": v(13086.75, 920.72) * mm, "end": v(13085.28, 926.22) * mm});
            skLineSegment(sketch, "E7503", {"start": v(13085.28, 926.22) * mm, "end": v(13083.98, 930.6) * mm});
            skLineSegment(sketch, "E7504", {"start": v(13083.98, 930.6) * mm, "end": v(13082.9, 933.91) * mm});
            skLineSegment(sketch, "E7505", {"start": v(13082.9, 933.91) * mm, "end": v(13082.11, 936.15) * mm});
            skLineSegment(sketch, "E7506", {"start": v(13082.11, 936.15) * mm, "end": v(13081.66, 937.34) * mm});
            skLineSegment(sketch, "E7507", {"start": v(13081.66, 937.34) * mm, "end": v(13014.69, 1095.88) * mm});
            skLineSegment(sketch, "E7508", {"start": v(13014.69, 1095.88) * mm, "end": v(13257.86, 1229.33) * mm});
            skLineSegment(sketch, "E7509", {"start": v(13257.86, 1229.33) * mm, "end": v(13355.63, 1087.69) * mm});
            skLineSegment(sketch, "E7510", {"start": v(13355.63, 1087.69) * mm, "end": v(13356.39, 1086.67) * mm});
            skLineSegment(sketch, "E7511", {"start": v(13356.39, 1086.67) * mm, "end": v(13357.85, 1084.8) * mm});
            skLineSegment(sketch, "E7512", {"start": v(13357.85, 1084.8) * mm, "end": v(13360.06, 1082.12) * mm});
            skLineSegment(sketch, "E7513", {"start": v(13360.06, 1082.12) * mm, "end": v(13363.07, 1078.66) * mm});
            skLineSegment(sketch, "E7514", {"start": v(13363.07, 1078.66) * mm, "end": v(13366.9, 1074.47) * mm});
            skLineSegment(sketch, "E7515", {"start": v(13366.9, 1074.47) * mm, "end": v(13371.63, 1069.6) * mm});
            skLineSegment(sketch, "E7516", {"start": v(13371.63, 1069.6) * mm, "end": v(13377.27, 1064.08) * mm});
            skLineSegment(sketch, "E7517", {"start": v(13377.27, 1064.08) * mm, "end": v(13383.87, 1057.97) * mm});
            skLineSegment(sketch, "E7518", {"start": v(13383.87, 1057.97) * mm, "end": v(13391.46, 1051.3) * mm});
            skLineSegment(sketch, "E7519", {"start": v(13391.46, 1051.3) * mm, "end": v(13400.07, 1044.14) * mm});
            skLineSegment(sketch, "E7520", {"start": v(13400.07, 1044.14) * mm, "end": v(13409.74, 1036.53) * mm});
            skLineSegment(sketch, "E7521", {"start": v(13409.74, 1036.53) * mm, "end": v(13420.49, 1028.52) * mm});
            skLineSegment(sketch, "E7522", {"start": v(13420.49, 1028.52) * mm, "end": v(13432.36, 1020.16) * mm});
            skLineSegment(sketch, "E7523", {"start": v(13432.36, 1020.16) * mm, "end": v(13445.36, 1011.52) * mm});
            skLineSegment(sketch, "E7524", {"start": v(13445.36, 1011.52) * mm, "end": v(13459.53, 1002.64) * mm});
            skLineSegment(sketch, "E7525", {"start": v(13459.53, 1002.64) * mm, "end": v(13474.89, 993.59) * mm});
            skLineSegment(sketch, "E7526", {"start": v(13474.89, 993.59) * mm, "end": v(13491.44, 984.41) * mm});
            skLineSegment(sketch, "E7527", {"start": v(13491.44, 984.41) * mm, "end": v(13509.22, 975.18) * mm});
            skLineSegment(sketch, "E7528", {"start": v(13509.22, 975.18) * mm, "end": v(13528.23, 965.94) * mm});
            skLineSegment(sketch, "E7529", {"start": v(13528.23, 965.94) * mm, "end": v(13548.48, 956.76) * mm});
            skLineSegment(sketch, "E7530", {"start": v(13548.48, 956.76) * mm, "end": v(13570, 947.7) * mm});
            skLineSegment(sketch, "E7531", {"start": v(13570, 947.7) * mm, "end": v(13592.77, 938.82) * mm});
            skLineSegment(sketch, "E7532", {"start": v(13592.77, 938.82) * mm, "end": v(13616.81, 930.18) * mm});
            skLineSegment(sketch, "E7533", {"start": v(13616.81, 930.18) * mm, "end": v(13642.13, 921.84) * mm});
            skLineSegment(sketch, "E7534", {"start": v(13642.13, 921.84) * mm, "end": v(13668.72, 913.87) * mm});
            skLineSegment(sketch, "E7535", {"start": v(13668.72, 913.87) * mm, "end": v(13696.57, 906.33) * mm});
            skLineSegment(sketch, "E7536", {"start": v(13696.57, 906.33) * mm, "end": v(13724.69, 900.46) * mm});
            skLineSegment(sketch, "E7537", {"start": v(13724.69, 900.46) * mm, "end": v(13824.58, 992.33) * mm});
            skLineSegment(sketch, "E7538", {"start": v(13824.58, 992.33) * mm, "end": v(13821.08, 1020.84) * mm});
            skLineSegment(sketch, "E7539", {"start": v(13821.08, 1020.84) * mm, "end": v(13815.9, 1049.23) * mm});
            skLineSegment(sketch, "E7540", {"start": v(13815.9, 1049.23) * mm, "end": v(13810.17, 1076.39) * mm});
            skLineSegment(sketch, "E7541", {"start": v(13810.17, 1076.39) * mm, "end": v(13803.98, 1102.3) * mm});
            skLineSegment(sketch, "E7542", {"start": v(13803.98, 1102.3) * mm, "end": v(13797.38, 1127) * mm});
            skLineSegment(sketch, "E7543", {"start": v(13797.38, 1127) * mm, "end": v(13790.43, 1150.43) * mm});
            skLineSegment(sketch, "E7544", {"start": v(13790.43, 1150.43) * mm, "end": v(13783.2, 1172.62) * mm});
            skLineSegment(sketch, "E7545", {"start": v(13783.2, 1172.62) * mm, "end": v(13775.75, 1193.57) * mm});
            skLineSegment(sketch, "E7546", {"start": v(13775.75, 1193.57) * mm, "end": v(13768.13, 1213.29) * mm});
            skLineSegment(sketch, "E7547", {"start": v(13768.13, 1213.29) * mm, "end": v(13760.41, 1231.77) * mm});
            skLineSegment(sketch, "E7548", {"start": v(13760.41, 1231.77) * mm, "end": v(13752.65, 1249.04) * mm});
            skLineSegment(sketch, "E7549", {"start": v(13752.65, 1249.04) * mm, "end": v(13744.91, 1265.1) * mm});
            skLineSegment(sketch, "E7550", {"start": v(13744.91, 1265.1) * mm, "end": v(13737.25, 1279.96) * mm});
            skLineSegment(sketch, "E7551", {"start": v(13737.25, 1279.96) * mm, "end": v(13729.72, 1293.64) * mm});
            skLineSegment(sketch, "E7552", {"start": v(13729.72, 1293.64) * mm, "end": v(13722.39, 1306.16) * mm});
            skLineSegment(sketch, "E7553", {"start": v(13722.39, 1306.16) * mm, "end": v(13715.3, 1317.55) * mm});
            skLineSegment(sketch, "E7554", {"start": v(13715.3, 1317.55) * mm, "end": v(13708.53, 1327.82) * mm});
            skLineSegment(sketch, "E7555", {"start": v(13708.53, 1327.82) * mm, "end": v(13702.1, 1337) * mm});
            skLineSegment(sketch, "E7556", {"start": v(13702.1, 1337) * mm, "end": v(13696.1, 1345.12) * mm});
            skLineSegment(sketch, "E7557", {"start": v(13696.1, 1345.12) * mm, "end": v(13690.56, 1352.2) * mm});
            skLineSegment(sketch, "E7558", {"start": v(13690.56, 1352.2) * mm, "end": v(13685.53, 1358.28) * mm});
            skLineSegment(sketch, "E7559", {"start": v(13685.53, 1358.28) * mm, "end": v(13681.07, 1363.4) * mm});
            skLineSegment(sketch, "E7560", {"start": v(13681.07, 1363.4) * mm, "end": v(13677.22, 1367.58) * mm});
            skLineSegment(sketch, "E7561", {"start": v(13677.22, 1367.58) * mm, "end": v(13674.03, 1370.86) * mm});
            skLineSegment(sketch, "E7562", {"start": v(13674.03, 1370.86) * mm, "end": v(13671.54, 1373.29) * mm});
            skLineSegment(sketch, "E7563", {"start": v(13671.54, 1373.29) * mm, "end": v(13669.8, 1374.9) * mm});
            skLineSegment(sketch, "E7564", {"start": v(13669.8, 1374.9) * mm, "end": v(13668.84, 1375.74) * mm});
            skLineSegment(sketch, "E7565", {"start": v(13668.84, 1375.74) * mm, "end": v(13535.86, 1485) * mm});
            skLineSegment(sketch, "E7566", {"start": v(13535.86, 1485) * mm, "end": v(13689.16, 1716.17) * mm});
            skLineSegment(sketch, "E7567", {"start": v(13689.16, 1716.17) * mm, "end": v(13841.56, 1636.2) * mm});
            skLineSegment(sketch, "E7568", {"start": v(13841.56, 1636.2) * mm, "end": v(13842.7, 1635.64) * mm});
            skLineSegment(sketch, "E7569", {"start": v(13842.7, 1635.64) * mm, "end": v(13844.86, 1634.66) * mm});
            skLineSegment(sketch, "E7570", {"start": v(13844.86, 1634.66) * mm, "end": v(13848.07, 1633.31) * mm});
            skLineSegment(sketch, "E7571", {"start": v(13848.07, 1633.31) * mm, "end": v(13852.34, 1631.65) * mm});
            skLineSegment(sketch, "E7572", {"start": v(13852.34, 1631.65) * mm, "end": v(13857.69, 1629.73) * mm});
            skLineSegment(sketch, "E7573", {"start": v(13857.69, 1629.73) * mm, "end": v(13864.13, 1627.6) * mm});
            skLineSegment(sketch, "E7574", {"start": v(13864.13, 1627.6) * mm, "end": v(13871.7, 1625.35) * mm});
            skLineSegment(sketch, "E7575", {"start": v(13871.7, 1625.35) * mm, "end": v(13880.38, 1623) * mm});
            skLineSegment(sketch, "E7576", {"start": v(13880.38, 1623) * mm, "end": v(13890.2, 1620.62) * mm});
            skLineSegment(sketch, "E7577", {"start": v(13890.2, 1620.62) * mm, "end": v(13901.15, 1618.28) * mm});
            skLineSegment(sketch, "E7578", {"start": v(13901.15, 1618.28) * mm, "end": v(13913.25, 1616.03) * mm});
            skLineSegment(sketch, "E7579", {"start": v(13913.25, 1616.03) * mm, "end": v(13926.5, 1613.94) * mm});
            skLineSegment(sketch, "E7580", {"start": v(13926.5, 1613.94) * mm, "end": v(13940.88, 1612.05) * mm});
            skLineSegment(sketch, "E7581", {"start": v(13940.88, 1612.05) * mm, "end": v(13956.41, 1610.45) * mm});
            skLineSegment(sketch, "E7582", {"start": v(13956.41, 1610.45) * mm, "end": v(13973.08, 1609.17) * mm});
            skLineSegment(sketch, "E7583", {"start": v(13973.08, 1609.17) * mm, "end": v(13990.89, 1608.29) * mm});
            skLineSegment(sketch, "E7584", {"start": v(13990.89, 1608.29) * mm, "end": v(14009.8, 1607.86) * mm});
            skLineSegment(sketch, "E7585", {"start": v(14009.8, 1607.86) * mm, "end": v(14029.84, 1607.94) * mm});
            skLineSegment(sketch, "E7586", {"start": v(14029.84, 1607.94) * mm, "end": v(14050.96, 1608.6) * mm});
            skLineSegment(sketch, "E7587", {"start": v(14050.96, 1608.6) * mm, "end": v(14073.17, 1609.88) * mm});
            skLineSegment(sketch, "E7588", {"start": v(14073.17, 1609.88) * mm, "end": v(14096.42, 1611.86) * mm});
            skLineSegment(sketch, "E7589", {"start": v(14096.42, 1611.86) * mm, "end": v(14120.72, 1614.58) * mm});
            skLineSegment(sketch, "E7590", {"start": v(14120.72, 1614.58) * mm, "end": v(14146.02, 1618.1) * mm});
            skLineSegment(sketch, "E7591", {"start": v(14146.02, 1618.1) * mm, "end": v(14172.31, 1622.49) * mm});
            skLineSegment(sketch, "E7592", {"start": v(14172.31, 1622.49) * mm, "end": v(14199.56, 1627.78) * mm});
            skLineSegment(sketch, "E7593", {"start": v(14199.56, 1627.78) * mm, "end": v(14227.73, 1634.05) * mm});
            skLineSegment(sketch, "E7594", {"start": v(14227.73, 1634.05) * mm, "end": v(14255.35, 1641.92) * mm});
            skLineSegment(sketch, "E7595", {"start": v(14255.35, 1641.92) * mm, "end": v(14301.11, 1769.69) * mm});
            skLineSegment(sketch, "E7596", {"start": v(14301.11, 1769.69) * mm, "end": v(14284.76, 1793.3) * mm});
            skLineSegment(sketch, "E7597", {"start": v(14284.76, 1793.3) * mm, "end": v(14266.97, 1816.03) * mm});
            skLineSegment(sketch, "E7598", {"start": v(14266.97, 1816.03) * mm, "end": v(14249.29, 1837.42) * mm});
            skLineSegment(sketch, "E7599", {"start": v(14249.29, 1837.42) * mm, "end": v(14231.76, 1857.5) * mm});
            skLineSegment(sketch, "E7600", {"start": v(14231.76, 1857.5) * mm, "end": v(14214.44, 1876.28) * mm});
            skLineSegment(sketch, "E7601", {"start": v(14214.44, 1876.28) * mm, "end": v(14197.4, 1893.8) * mm});
            skLineSegment(sketch, "E7602", {"start": v(14197.4, 1893.8) * mm, "end": v(14180.68, 1910.1) * mm});
            skLineSegment(sketch, "E7603", {"start": v(14180.68, 1910.1) * mm, "end": v(14164.35, 1925.19) * mm});
            skLineSegment(sketch, "E7604", {"start": v(14164.35, 1925.19) * mm, "end": v(14148.44, 1939.1) * mm});
            skLineSegment(sketch, "E7605", {"start": v(14148.44, 1939.1) * mm, "end": v(14133.01, 1951.88) * mm});
            skLineSegment(sketch, "E7606", {"start": v(14133.01, 1951.88) * mm, "end": v(14118.12, 1963.56) * mm});
            skLineSegment(sketch, "E7607", {"start": v(14118.12, 1963.56) * mm, "end": v(14103.8, 1974.18) * mm});
            skLineSegment(sketch, "E7608", {"start": v(14103.8, 1974.18) * mm, "end": v(14090.12, 1983.78) * mm});
            skLineSegment(sketch, "E7609", {"start": v(14090.12, 1983.78) * mm, "end": v(14077.1, 1992.4) * mm});
            skLineSegment(sketch, "E7610", {"start": v(14077.1, 1992.4) * mm, "end": v(14064.78, 2000.08) * mm});
            skLineSegment(sketch, "E7611", {"start": v(14064.78, 2000.08) * mm, "end": v(14053.22, 2006.87) * mm});
            skLineSegment(sketch, "E7612", {"start": v(14053.22, 2006.87) * mm, "end": v(14042.44, 2012.81) * mm});
            skLineSegment(sketch, "E7613", {"start": v(14042.44, 2012.81) * mm, "end": v(14032.49, 2017.96) * mm});
            skLineSegment(sketch, "E7614", {"start": v(14032.49, 2017.96) * mm, "end": v(14023.4, 2022.36) * mm});
            skLineSegment(sketch, "E7615", {"start": v(14023.4, 2022.36) * mm, "end": v(14015.2, 2026.05) * mm});
            skLineSegment(sketch, "E7616", {"start": v(14015.2, 2026.05) * mm, "end": v(14007.92, 2029.1) * mm});
            skLineSegment(sketch, "E7617", {"start": v(14007.92, 2029.1) * mm, "end": v(14001.6, 2031.56) * mm});
            skLineSegment(sketch, "E7618", {"start": v(14001.6, 2031.56) * mm, "end": v(13996.24, 2033.47) * mm});
            skLineSegment(sketch, "E7619", {"start": v(13996.24, 2033.47) * mm, "end": v(13991.89, 2034.9) * mm});
            skLineSegment(sketch, "E7620", {"start": v(13991.89, 2034.9) * mm, "end": v(13988.56, 2035.89) * mm});
            skLineSegment(sketch, "E7621", {"start": v(13988.56, 2035.89) * mm, "end": v(13986.27, 2036.5) * mm});
            skLineSegment(sketch, "E7622", {"start": v(13986.27, 2036.5) * mm, "end": v(13985.03, 2036.8) * mm});
            skLineSegment(sketch, "E7623", {"start": v(13985.03, 2036.8) * mm, "end": v(13816.5, 2071.75) * mm});
            skLineSegment(sketch, "E7624", {"start": v(13816.5, 2071.75) * mm, "end": v(13844.81, 2347.69) * mm});
            skLineSegment(sketch, "E7625", {"start": v(13844.81, 2347.69) * mm, "end": v(14016.93, 2347.69) * mm});
            skLineSegment(sketch, "E7626", {"start": v(14016.93, 2347.69) * mm, "end": v(14018.2, 2347.73) * mm});
            skLineSegment(sketch, "E7627", {"start": v(14018.2, 2347.73) * mm, "end": v(14020.57, 2347.87) * mm});
            skLineSegment(sketch, "E7628", {"start": v(12689.11, 2347.69) * mm, "end": v(12282.71, 2347.69) * mm});
            skFitSpline(sketch, "E7629", {"points": [v(14220.59, 2577.13) * mm, v(14220.59, 2522.07) * mm, v(14175.95, 2477.43) * mm, v(14120.9, 2477.43) * mm]});
            skFitSpline(sketch, "E7630", {"points": [v(14120.9, 2477.43) * mm, v(14065.83, 2477.43) * mm, v(14021.2, 2522.07) * mm, v(14021.2, 2577.13) * mm]});
            skFitSpline(sketch, "E7631", {"points": [v(14021.2, 2577.13) * mm, v(14021.2, 2632.19) * mm, v(14065.83, 2676.82) * mm, v(14120.9, 2676.82) * mm]});
            skFitSpline(sketch, "E7632", {"points": [v(14120.9, 2676.82) * mm, v(14175.95, 2676.82) * mm, v(14220.59, 2632.19) * mm, v(14220.59, 2577.13) * mm]});
            skLineSegment(sketch, "E7633", {"start": v(12485.91, 2144.49) * mm, "end": v(12485.91, 2550.89) * mm});
            skLineSegment(sketch, "E7634", {"start": v(11819.42, 3164.35) * mm, "end": v(11796.05, 3144.64) * mm});
            skLineSegment(sketch, "E7635", {"start": v(11796.05, 3144.64) * mm, "end": v(11773.3, 3124.32) * mm});
            skLineSegment(sketch, "E7636", {"start": v(11773.3, 3124.32) * mm, "end": v(11751.14, 3103.39) * mm});
            skLineSegment(sketch, "E7637", {"start": v(11751.14, 3103.39) * mm, "end": v(11729.6, 3081.85) * mm});
            skLineSegment(sketch, "E7638", {"start": v(11814.54, 3079.4) * mm, "end": v(11732.04, 3169.22) * mm});
            skLineSegment(sketch, "E7639", {"start": v(11780.8, 3211.49) * mm, "end": v(11776.14, 3167.6) * mm});
            skLineSegment(sketch, "E7640", {"start": v(11776.14, 3167.6) * mm, "end": v(11773.3, 3124.32) * mm});
            skLineSegment(sketch, "E7641", {"start": v(11773.3, 3124.32) * mm, "end": v(11772.28, 3081.64) * mm});
            skLineSegment(sketch, "E7642", {"start": v(11772.28, 3081.64) * mm, "end": v(11773.3, 3039.38) * mm});
            skLineSegment(sketch, "E7643", {"start": v(11857.82, 3117) * mm, "end": v(11815.96, 3121.67) * mm});
            skLineSegment(sketch, "E7644", {"start": v(11815.96, 3121.67) * mm, "end": v(11773.3, 3124.32) * mm});
            skLineSegment(sketch, "E7645", {"start": v(11773.3, 3124.32) * mm, "end": v(11729.8, 3125.33) * mm});
            skLineSegment(sketch, "E7646", {"start": v(11729.8, 3125.33) * mm, "end": v(11685.71, 3124.32) * mm});
            skLineSegment(sketch, "E7647", {"start": v(12015.1, 3187.3) * mm, "end": v(11990.92, 3173.29) * mm});
            skLineSegment(sketch, "E7648", {"start": v(11990.92, 3173.29) * mm, "end": v(11967.35, 3158.66) * mm});
            skLineSegment(sketch, "E7649", {"start": v(11967.35, 3158.66) * mm, "end": v(11943.98, 3143.42) * mm});
            skLineSegment(sketch, "E7650", {"start": v(11943.98, 3143.42) * mm, "end": v(11921.22, 3127.36) * mm});
            skLineSegment(sketch, "E7651", {"start": v(11921.22, 3127.36) * mm, "end": v(11885.46, 3176.74) * mm});
            skLineSegment(sketch, "E7652", {"start": v(11885.46, 3176.74) * mm, "end": v(11892.57, 3219) * mm});
            skLineSegment(sketch, "E7653", {"start": v(11892.57, 3219) * mm, "end": v(11917.97, 3235.67) * mm});
            skLineSegment(sketch, "E7654", {"start": v(11917.97, 3235.67) * mm, "end": v(11943.98, 3251.72) * mm});
            skLineSegment(sketch, "E7655", {"start": v(11943.98, 3251.72) * mm, "end": v(11955.36, 3293.58) * mm});
            skLineSegment(sketch, "E7656", {"start": v(11955.36, 3293.58) * mm, "end": v(11940.53, 3320.2) * mm});
            skLineSegment(sketch, "E7657", {"start": v(11940.53, 3320.2) * mm, "end": v(11896.84, 3330.16) * mm});
            skLineSegment(sketch, "E7658", {"start": v(11896.84, 3330.16) * mm, "end": v(11868.8, 3312.68) * mm});
            skLineSegment(sketch, "E7659", {"start": v(11868.8, 3312.68) * mm, "end": v(11841.16, 3294.6) * mm});
            skLineSegment(sketch, "E7660", {"start": v(11841.16, 3294.6) * mm, "end": v(11831.81, 3250.7) * mm});
            skLineSegment(sketch, "E7661", {"start": v(12266.05, 3472) * mm, "end": v(12301.2, 3292.36) * mm});
            skLineSegment(sketch, "E7662", {"start": v(12301.2, 3292.36) * mm, "end": v(12263.82, 3331.38) * mm});
            skLineSegment(sketch, "E7663", {"start": v(12263.82, 3331.38) * mm, "end": v(12224.2, 3368.77) * mm});
            skLineSegment(sketch, "E7664", {"start": v(12224.2, 3368.77) * mm, "end": v(12182.13, 3404.73) * mm});
            skLineSegment(sketch, "E7665", {"start": v(12182.13, 3404.73) * mm, "end": v(12137.83, 3439.07) * mm});
            skLineSegment(sketch, "E7666", {"start": v(12137.83, 3439.07) * mm, "end": v(12193.5, 3264.93) * mm});
            skLineSegment(sketch, "E7667", {"start": v(12464.78, 3431.96) * mm, "end": v(12433.29, 3430.94) * mm});
            skLineSegment(sketch, "E7668", {"start": v(12433.29, 3430.94) * mm, "end": v(12402, 3429.12) * mm});
            skLineSegment(sketch, "E7669", {"start": v(12402, 3429.12) * mm, "end": v(12370.9, 3426.07) * mm});
            skLineSegment(sketch, "E7670", {"start": v(12370.9, 3426.07) * mm, "end": v(12339.6, 3422.41) * mm});
            skLineSegment(sketch, "E7671", {"start": v(12465.8, 3371.2) * mm, "end": v(12436.33, 3370.19) * mm});
            skLineSegment(sketch, "E7672", {"start": v(12436.33, 3370.19) * mm, "end": v(12406.87, 3368.16) * mm});
            skLineSegment(sketch, "E7673", {"start": v(12406.87, 3368.16) * mm, "end": v(12377.2, 3365.51) * mm});
            skLineSegment(sketch, "E7674", {"start": v(12377.2, 3365.51) * mm, "end": v(12347.94, 3362.06) * mm});
            skLineSegment(sketch, "E7675", {"start": v(12528.59, 3461.83) * mm, "end": v(12562.72, 3490.69) * mm});
            skLineSegment(sketch, "E7676", {"start": v(12562.72, 3490.69) * mm, "end": v(12550.53, 3308.21) * mm});
            skLineSegment(sketch, "E7677", {"start": v(12578.37, 3305.98) * mm, "end": v(12550.53, 3308.21) * mm});
            skLineSegment(sketch, "E7678", {"start": v(12550.53, 3308.21) * mm, "end": v(12522.7, 3309.63) * mm});
            skLineSegment(sketch, "E7679", {"start": v(12656.8, 3449.64) * mm, "end": v(12694.2, 3474.23) * mm});
            skLineSegment(sketch, "E7680", {"start": v(12694.2, 3474.23) * mm, "end": v(12726.7, 3467.72) * mm});
            skLineSegment(sketch, "E7681", {"start": v(12726.7, 3467.72) * mm, "end": v(12759.01, 3460.2) * mm});
            skLineSegment(sketch, "E7682", {"start": v(12759.01, 3460.2) * mm, "end": v(12783, 3422.41) * mm});
            skLineSegment(sketch, "E7683", {"start": v(12783, 3422.41) * mm, "end": v(12774.86, 3393.15) * mm});
            skLineSegment(sketch, "E7684", {"start": v(12774.86, 3393.15) * mm, "end": v(12737.07, 3371.4) * mm});
            skLineSegment(sketch, "E7685", {"start": v(12737.07, 3371.4) * mm, "end": v(12758.6, 3334.42) * mm});
            skLineSegment(sketch, "E7686", {"start": v(12758.6, 3334.42) * mm, "end": v(12750.48, 3304.96) * mm});
            skLineSegment(sketch, "E7687", {"start": v(12750.48, 3304.96) * mm, "end": v(12715.33, 3282.6) * mm});
            skLineSegment(sketch, "E7688", {"start": v(12715.33, 3282.6) * mm, "end": v(12688.3, 3288.9) * mm});
            skLineSegment(sketch, "E7689", {"start": v(12688.3, 3288.9) * mm, "end": v(12660.87, 3294.4) * mm});
            skLineSegment(sketch, "E7690", {"start": v(12660.87, 3294.4) * mm, "end": v(12638.11, 3329.14) * mm});
            skLineSegment(sketch, "E7691", {"start": v(12707.4, 3378.32) * mm, "end": v(12737.07, 3371.4) * mm});
            skLineSegment(sketch, "E7692", {"start": v(12965.26, 3286.47) * mm, "end": v(12992.09, 3272.25) * mm});
            skLineSegment(sketch, "E7693", {"start": v(12992.09, 3272.25) * mm, "end": v(13018.7, 3257.2) * mm});
            skLineSegment(sketch, "E7694", {"start": v(13018.7, 3257.2) * mm, "end": v(13044.71, 3241.56) * mm});
            skLineSegment(sketch, "E7695", {"start": v(13044.71, 3241.56) * mm, "end": v(13087.18, 3250.3) * mm});
            skLineSegment(sketch, "E7696", {"start": v(13087.18, 3250.3) * mm, "end": v(13104.05, 3275.7) * mm});
            skLineSegment(sketch, "E7697", {"start": v(13104.05, 3275.7) * mm, "end": v(13093.28, 3318.98) * mm});
            skLineSegment(sketch, "E7698", {"start": v(13093.28, 3318.98) * mm, "end": v(13064.83, 3336.25) * mm});
            skLineSegment(sketch, "E7699", {"start": v(13064.83, 3336.25) * mm, "end": v(13035.98, 3352.5) * mm});
            skLineSegment(sketch, "E7700", {"start": v(13035.98, 3352.5) * mm, "end": v(13006.72, 3367.95) * mm});
            skLineSegment(sketch, "E7701", {"start": v(13006.72, 3367.95) * mm, "end": v(12923.6, 3205.19) * mm});
            skLineSegment(sketch, "E7702", {"start": v(13065.03, 3116.6) * mm, "end": v(13138.39, 3214.13) * mm});
            skLineSegment(sketch, "E7703", {"start": v(13156.68, 3238.31) * mm, "end": v(13174.97, 3262.7) * mm});
            skLineSegment(sketch, "E7704", {"start": v(13211.34, 3025.97) * mm, "end": v(13169.89, 3025.15) * mm});
            skLineSegment(sketch, "E7705", {"start": v(13169.89, 3025.15) * mm, "end": v(13170.9, 3066.81) * mm});
            skLineSegment(sketch, "E7706", {"start": v(13170.9, 3066.81) * mm, "end": v(13276.16, 3177.15) * mm});
            skLineSegment(sketch, "E7707", {"start": v(13278.2, 3088.35) * mm, "end": v(13256.45, 3110.9) * mm});
            skLineSegment(sketch, "E7708", {"start": v(13256.45, 3110.9) * mm, "end": v(13234.1, 3133.05) * mm});
            skLineSegment(sketch, "E7709", {"start": v(13234.1, 3133.05) * mm, "end": v(13210.93, 3154.19) * mm});
            skLineSegment(sketch, "E7710", {"start": v(13210.93, 3154.19) * mm, "end": v(13187.36, 3174.91) * mm});
            skLineSegment(sketch, "E7711", {"start": v(13292, 2873.97) * mm, "end": v(13276.57, 2896.94) * mm});
            skLineSegment(sketch, "E7712", {"start": v(13276.57, 2896.94) * mm, "end": v(13260.3, 2919.7) * mm});
            skLineSegment(sketch, "E7713", {"start": v(13260.3, 2919.7) * mm, "end": v(13243.44, 2941.84) * mm});
            skLineSegment(sketch, "E7714", {"start": v(13243.44, 2941.84) * mm, "end": v(13249.34, 2982.89) * mm});
            skLineSegment(sketch, "E7715", {"start": v(13249.34, 2982.89) * mm, "end": v(13296.28, 3021.9) * mm});
            skLineSegment(sketch, "E7716", {"start": v(13296.28, 3021.9) * mm, "end": v(13339.35, 3017.03) * mm});
            skLineSegment(sketch, "E7717", {"start": v(13339.35, 3017.03) * mm, "end": v(13358.25, 2992.03) * mm});
            skLineSegment(sketch, "E7718", {"start": v(13358.25, 2992.03) * mm, "end": v(13376.54, 2966.63) * mm});
            skLineSegment(sketch, "E7719", {"start": v(13376.54, 2966.63) * mm, "end": v(13394.22, 2940.62) * mm});
            skLineSegment(sketch, "E7720", {"start": v(13373.9, 2856.7) * mm, "end": v(13415.15, 2845.32) * mm});
            skLineSegment(sketch, "E7721", {"start": v(13415.15, 2845.32) * mm, "end": v(13456.4, 2831.7) * mm});
            skLineSegment(sketch, "E7722", {"start": v(13456.4, 2831.7) * mm, "end": v(13470.01, 2803.46) * mm});
            skLineSegment(sketch, "E7723", {"start": v(13470.01, 2803.46) * mm, "end": v(13454.77, 2762.82) * mm});
            skLineSegment(sketch, "E7724", {"start": v(13454.77, 2762.82) * mm, "end": v(13370.85, 2726.86) * mm});
            skLineSegment(sketch, "E7725", {"start": v(13321.07, 2826.42) * mm, "end": v(13479.77, 2917.46) * mm});
            skLineSegment(sketch, "E7726", {"start": v(13428.97, 2541.13) * mm, "end": v(13434.05, 2513.9) * mm});
            skLineSegment(sketch, "E7727", {"start": v(13434.05, 2513.9) * mm, "end": v(13438.52, 2486.47) * mm});
            skLineSegment(sketch, "E7728", {"start": v(13438.52, 2486.47) * mm, "end": v(13442.17, 2458.84) * mm});
            skLineSegment(sketch, "E7729", {"start": v(13442.17, 2458.84) * mm, "end": v(13475.3, 2433.64) * mm});
            skLineSegment(sketch, "E7730", {"start": v(13475.3, 2433.64) * mm, "end": v(13596.8, 2444.2) * mm});
            skLineSegment(sketch, "E7731", {"start": v(13596.8, 2444.2) * mm, "end": v(13623.83, 2479.97) * mm});
            skLineSegment(sketch, "E7732", {"start": v(13623.83, 2479.97) * mm, "end": v(13619.57, 2512.68) * mm});
            skLineSegment(sketch, "E7733", {"start": v(13619.57, 2512.68) * mm, "end": v(13614.28, 2545.4) * mm});
            skLineSegment(sketch, "E7734", {"start": v(13614.28, 2545.4) * mm, "end": v(13607.98, 2577.91) * mm});
            skLineSegment(sketch, "E7735", {"start": v(13614.28, 2545.4) * mm, "end": v(13434.05, 2513.9) * mm});
            skLineSegment(sketch, "E7736", {"start": v(13566.33, 2253.8) * mm, "end": v(13568.77, 2284.9) * mm});
            skLineSegment(sketch, "E7737", {"start": v(13568.77, 2284.9) * mm, "end": v(13569.99, 2316.4) * mm});
            skLineSegment(sketch, "E7738", {"start": v(13569.99, 2316.4) * mm, "end": v(13570.4, 2347.69) * mm});
            skLineSegment(sketch, "E7739", {"start": v(13570.4, 2347.69) * mm, "end": v(13569.99, 2378.98) * mm});
            skLineSegment(sketch, "E7740", {"start": v(13505.77, 2259.1) * mm, "end": v(13507.8, 2288.55) * mm});
            skLineSegment(sketch, "E7741", {"start": v(13507.8, 2288.55) * mm, "end": v(13509.03, 2318.02) * mm});
            skLineSegment(sketch, "E7742", {"start": v(13509.03, 2318.02) * mm, "end": v(13509.43, 2347.69) * mm});
            skLineSegment(sketch, "E7743", {"start": v(13509.43, 2347.69) * mm, "end": v(13509.03, 2377.35) * mm});
            skLineSegment(sketch, "E7744", {"start": v(13589.29, 2186.95) * mm, "end": v(13614.28, 2149.97) * mm});
            skLineSegment(sketch, "E7745", {"start": v(13614.28, 2149.97) * mm, "end": v(13607.98, 2117.46) * mm});
            skLineSegment(sketch, "E7746", {"start": v(13607.98, 2117.46) * mm, "end": v(13600.87, 2085.15) * mm});
            skLineSegment(sketch, "E7747", {"start": v(13600.87, 2085.15) * mm, "end": v(13563.48, 2060.77) * mm});
            skLineSegment(sketch, "E7748", {"start": v(13563.48, 2060.77) * mm, "end": v(13534.02, 2068.7) * mm});
            skLineSegment(sketch, "E7749", {"start": v(13534.02, 2068.7) * mm, "end": v(13511.87, 2106.08) * mm});
            skLineSegment(sketch, "E7750", {"start": v(13511.87, 2106.08) * mm, "end": v(13475.1, 2084.34) * mm});
            skLineSegment(sketch, "E7751", {"start": v(13475.1, 2084.34) * mm, "end": v(13445.63, 2092.06) * mm});
            skLineSegment(sketch, "E7752", {"start": v(13445.63, 2092.06) * mm, "end": v(13422.87, 2127.01) * mm});
            skLineSegment(sketch, "E7753", {"start": v(13422.87, 2127.01) * mm, "end": v(13428.97, 2154.24) * mm});
            skLineSegment(sketch, "E7754", {"start": v(13428.97, 2154.24) * mm, "end": v(13434.05, 2181.47) * mm});
            skLineSegment(sketch, "E7755", {"start": v(13434.05, 2181.47) * mm, "end": v(13468.8, 2204.63) * mm});
            skLineSegment(sketch, "E7756", {"start": v(13518.58, 2135.75) * mm, "end": v(13511.87, 2106.08) * mm});
            skLineSegment(sketch, "E7757", {"start": v(13429.17, 2037.2) * mm, "end": v(13400.31, 2046.54) * mm});
            skLineSegment(sketch, "E7758", {"start": v(13334.68, 1893.33) * mm, "end": v(13347.28, 1918.12) * mm});
            skLineSegment(sketch, "E7759", {"start": v(13347.28, 1918.12) * mm, "end": v(13359.47, 1943.11) * mm});
            skLineSegment(sketch, "E7760", {"start": v(13359.47, 1943.11) * mm, "end": v(13370.85, 1968.51) * mm});
            skLineSegment(sketch, "E7761", {"start": v(13370.85, 1968.51) * mm, "end": v(13381.42, 1994.32) * mm});
            skLineSegment(sketch, "E7762", {"start": v(13381.42, 1994.32) * mm, "end": v(13438.1, 1971.97) * mm});
            skLineSegment(sketch, "E7763", {"start": v(13438.1, 1971.97) * mm, "end": v(13454.77, 1932.55) * mm});
            skLineSegment(sketch, "E7764", {"start": v(13454.77, 1932.55) * mm, "end": v(13442.38, 1904.7) * mm});
            skLineSegment(sketch, "E7765", {"start": v(13442.38, 1904.7) * mm, "end": v(13429.17, 1877.28) * mm});
            skLineSegment(sketch, "E7766", {"start": v(13429.17, 1877.28) * mm, "end": v(13442.17, 1835.82) * mm});
            skLineSegment(sketch, "E7767", {"start": v(13442.17, 1835.82) * mm, "end": v(13469, 1821.4) * mm});
            skLineSegment(sketch, "E7768", {"start": v(13469, 1821.4) * mm, "end": v(13511.06, 1836.43) * mm});
            skLineSegment(sketch, "E7769", {"start": v(13511.06, 1836.43) * mm, "end": v(13525.28, 1866.3) * mm});
            skLineSegment(sketch, "E7770", {"start": v(13525.28, 1866.3) * mm, "end": v(13538.9, 1896.58) * mm});
            skLineSegment(sketch, "E7771", {"start": v(13538.9, 1896.58) * mm, "end": v(13523.05, 1938.24) * mm});
            skLineSegment(sketch, "E7772", {"start": v(13387.3, 1640.75) * mm, "end": v(13407.43, 1667.17) * mm});
            skLineSegment(sketch, "E7773", {"start": v(13407.43, 1667.17) * mm, "end": v(13426.73, 1694) * mm});
            skLineSegment(sketch, "E7774", {"start": v(13426.73, 1694) * mm, "end": v(13445.22, 1721.42) * mm});
            skLineSegment(sketch, "E7775", {"start": v(13445.22, 1721.42) * mm, "end": v(13462.9, 1749.46) * mm});
            skLineSegment(sketch, "E7776", {"start": v(13462.9, 1749.46) * mm, "end": v(13410.88, 1781.37) * mm});
            skLineSegment(sketch, "E7777", {"start": v(13410.88, 1781.37) * mm, "end": v(13394.22, 1754.75) * mm});
            skLineSegment(sketch, "E7778", {"start": v(13394.22, 1754.75) * mm, "end": v(13376.54, 1728.74) * mm});
            skLineSegment(sketch, "E7779", {"start": v(13376.54, 1728.74) * mm, "end": v(13358.25, 1703.34) * mm});
            skLineSegment(sketch, "E7780", {"start": v(13358.25, 1703.34) * mm, "end": v(13315.38, 1697.24) * mm});
            skLineSegment(sketch, "E7781", {"start": v(13315.38, 1697.24) * mm, "end": v(13267.42, 1734.83) * mm});
            skLineSegment(sketch, "E7782", {"start": v(13267.42, 1734.83) * mm, "end": v(13260.3, 1775.68) * mm});
            skLineSegment(sketch, "E7783", {"start": v(13260.3, 1775.68) * mm, "end": v(13276.57, 1798.44) * mm});
            skLineSegment(sketch, "E7784", {"start": v(13276.57, 1798.44) * mm, "end": v(13292, 1821.4) * mm});
            skLineSegment(sketch, "E7785", {"start": v(13292, 1821.4) * mm, "end": v(13332.85, 1829.12) * mm});
            skLineSegment(sketch, "E7786", {"start": v(13167.65, 1543.83) * mm, "end": v(13144.08, 1524.32) * mm});
            skLineSegment(sketch, "E7787", {"start": v(13144.08, 1524.32) * mm, "end": v(13120.1, 1505.62) * mm});
            skLineSegment(sketch, "E7788", {"start": v(13120.1, 1505.62) * mm, "end": v(13095.51, 1487.74) * mm});
            skLineSegment(sketch, "E7789", {"start": v(13095.51, 1487.74) * mm, "end": v(13087.18, 1445.07) * mm});
            skLineSegment(sketch, "E7790", {"start": v(13087.18, 1445.07) * mm, "end": v(13104.05, 1419.67) * mm});
            skLineSegment(sketch, "E7791", {"start": v(13104.05, 1419.67) * mm, "end": v(13148.35, 1413.17) * mm});
            skLineSegment(sketch, "E7792", {"start": v(13148.35, 1413.17) * mm, "end": v(13174.97, 1432.68) * mm});
            skLineSegment(sketch, "E7793", {"start": v(13174.97, 1432.68) * mm, "end": v(13201.18, 1453) * mm});
            skLineSegment(sketch, "E7794", {"start": v(13201.18, 1453) * mm, "end": v(13226.78, 1473.93) * mm});
            skLineSegment(sketch, "E7795", {"start": v(13226.78, 1473.93) * mm, "end": v(13108.52, 1613.52) * mm});
            skLineSegment(sketch, "E7796", {"start": v(12922.39, 1354.85) * mm, "end": v(12950.84, 1367.86) * mm});
            skLineSegment(sketch, "E7797", {"start": v(12950.84, 1367.86) * mm, "end": v(12979.08, 1381.67) * mm});
            skLineSegment(sketch, "E7798", {"start": v(12979.08, 1381.67) * mm, "end": v(13006.72, 1396.3) * mm});
            skLineSegment(sketch, "E7799", {"start": v(13006.72, 1396.3) * mm, "end": v(13034.15, 1411.75) * mm});
            skLineSegment(sketch, "E7800", {"start": v(12897.8, 1410.53) * mm, "end": v(12924.83, 1422.92) * mm});
            skLineSegment(sketch, "E7801", {"start": v(12924.83, 1422.92) * mm, "end": v(12951.24, 1435.93) * mm});
            skLineSegment(sketch, "E7802", {"start": v(12951.24, 1435.93) * mm, "end": v(12977.45, 1449.74) * mm});
            skLineSegment(sketch, "E7803", {"start": v(12977.45, 1449.74) * mm, "end": v(13003.26, 1464.38) * mm});
            skLineSegment(sketch, "E7804", {"start": v(12729.96, 1353.63) * mm, "end": v(12758.6, 1360.95) * mm});
            skLineSegment(sketch, "E7805", {"start": v(12758.6, 1360.95) * mm, "end": v(12786.85, 1369.28) * mm});
            skLineSegment(sketch, "E7806", {"start": v(12786.85, 1369.28) * mm, "end": v(12815.1, 1378.42) * mm});
            skLineSegment(sketch, "E7807", {"start": v(12815.1, 1378.42) * mm, "end": v(12842.94, 1388.38) * mm});
            skLineSegment(sketch, "E7808", {"start": v(12842.94, 1388.38) * mm, "end": v(12828.1, 1340.02) * mm});
            skLineSegment(sketch, "E7809", {"start": v(12828.1, 1340.02) * mm, "end": v(12810.83, 1291.66) * mm});
            skLineSegment(sketch, "E7810", {"start": v(12810.83, 1291.66) * mm, "end": v(12790.92, 1243.5) * mm});
            skLineSegment(sketch, "E7811", {"start": v(12790.92, 1243.5) * mm, "end": v(12742.35, 1419.87) * mm});
            skLineSegment(sketch, "E7812", {"start": v(12526.15, 1294.3) * mm, "end": v(12495.87, 1293.69) * mm});
            skLineSegment(sketch, "E7813", {"start": v(12495.87, 1293.69) * mm, "end": v(12465.4, 1293.69) * mm});
            skLineSegment(sketch, "E7814", {"start": v(12465.4, 1293.69) * mm, "end": v(12434.91, 1294.9) * mm});
            skLineSegment(sketch, "E7815", {"start": v(12434.91, 1294.9) * mm, "end": v(12402, 1266.26) * mm});
            skLineSegment(sketch, "E7816", {"start": v(12402, 1266.26) * mm, "end": v(12399.76, 1235.98) * mm});
            skLineSegment(sketch, "E7817", {"start": v(12399.76, 1235.98) * mm, "end": v(12430.44, 1203.47) * mm});
            skLineSegment(sketch, "E7818", {"start": v(12430.44, 1203.47) * mm, "end": v(12463.56, 1202.45) * mm});
            skLineSegment(sketch, "E7819", {"start": v(12463.56, 1202.45) * mm, "end": v(12496.68, 1202.25) * mm});
            skLineSegment(sketch, "E7820", {"start": v(12496.68, 1202.25) * mm, "end": v(12529.8, 1203.06) * mm});
            skLineSegment(sketch, "E7821", {"start": v(12529.8, 1203.06) * mm, "end": v(12522.7, 1385.74) * mm});
            skLineSegment(sketch, "E7822", {"start": v(12356.07, 1393.86) * mm, "end": v(12347.94, 1333.31) * mm});
            skLineSegment(sketch, "E7823", {"start": v(12347.94, 1333.31) * mm, "end": v(12308.72, 1277.63) * mm});
            skLineSegment(sketch, "E7824", {"start": v(12308.72, 1277.63) * mm, "end": v(12266.05, 1223.38) * mm});
            skLineSegment(sketch, "E7825", {"start": v(12266.05, 1223.38) * mm, "end": v(12247.15, 1289.62) * mm});
            skLineSegment(sketch, "E7826", {"start": v(12247.15, 1289.62) * mm, "end": v(12231.71, 1356.07) * mm});
            skLineSegment(sketch, "E7827", {"start": v(12231.71, 1356.07) * mm, "end": v(12246.95, 1415.2) * mm});
            skLineSegment(sketch, "E7828", {"start": v(12347.94, 1333.31) * mm, "end": v(12318.68, 1337.78) * mm});
            skLineSegment(sketch, "E7829", {"start": v(12318.68, 1337.78) * mm, "end": v(12289.42, 1343.06) * mm});
            skLineSegment(sketch, "E7830", {"start": v(12289.42, 1343.06) * mm, "end": v(12260.57, 1349.16) * mm});
            skLineSegment(sketch, "E7831", {"start": v(12260.57, 1349.16) * mm, "end": v(12231.71, 1356.07) * mm});
            skLineSegment(sketch, "E7832", {"start": v(12039.28, 1359.32) * mm, "end": v(12068.13, 1346.72) * mm});
            skLineSegment(sketch, "E7833", {"start": v(12068.13, 1346.72) * mm, "end": v(12097.2, 1335.14) * mm});
            skLineSegment(sketch, "E7834", {"start": v(12097.2, 1335.14) * mm, "end": v(12126.66, 1324.37) * mm});
            skLineSegment(sketch, "E7835", {"start": v(12126.66, 1324.37) * mm, "end": v(12156.32, 1314.41) * mm});
            skLineSegment(sketch, "E7836", {"start": v(12064.48, 1414.8) * mm, "end": v(12091.5, 1403) * mm});
            skLineSegment(sketch, "E7837", {"start": v(12091.5, 1403) * mm, "end": v(12119.14, 1392.04) * mm});
            skLineSegment(sketch, "E7838", {"start": v(12119.14, 1392.04) * mm, "end": v(12146.77, 1381.88) * mm});
            skLineSegment(sketch, "E7839", {"start": v(12146.77, 1381.88) * mm, "end": v(12174.81, 1372.53) * mm});
            skLineSegment(sketch, "E7840", {"start": v(11943.98, 1551.95) * mm, "end": v(11967.35, 1536.71) * mm});
            skLineSegment(sketch, "E7841", {"start": v(11967.35, 1536.71) * mm, "end": v(11990.92, 1522.08) * mm});
            skLineSegment(sketch, "E7842", {"start": v(11990.92, 1522.08) * mm, "end": v(12015.1, 1508.06) * mm});
            skLineSegment(sketch, "E7843", {"start": v(12015.1, 1508.06) * mm, "end": v(12039.48, 1494.86) * mm});
            skLineSegment(sketch, "E7844", {"start": v(12039.48, 1494.86) * mm, "end": v(12011.24, 1440.8) * mm});
            skLineSegment(sketch, "E7845", {"start": v(12011.24, 1440.8) * mm, "end": v(11970.2, 1428.4) * mm});
            skLineSegment(sketch, "E7846", {"start": v(11970.2, 1428.4) * mm, "end": v(11943.98, 1443.65) * mm});
            skLineSegment(sketch, "E7847", {"start": v(11943.98, 1443.65) * mm, "end": v(11917.97, 1459.7) * mm});
            skLineSegment(sketch, "E7848", {"start": v(11917.97, 1459.7) * mm, "end": v(11875.5, 1451.17) * mm});
            skLineSegment(sketch, "E7849", {"start": v(11875.5, 1451.17) * mm, "end": v(11858.23, 1425.97) * mm});
            skLineSegment(sketch, "E7850", {"start": v(11858.23, 1425.97) * mm, "end": v(11868.8, 1382.69) * mm});
            skLineSegment(sketch, "E7851", {"start": v(11868.8, 1382.69) * mm, "end": v(11896.84, 1365.21) * mm});
            skLineSegment(sketch, "E7852", {"start": v(11896.84, 1365.21) * mm, "end": v(11925.49, 1348.55) * mm});
            skLineSegment(sketch, "E7853", {"start": v(11925.49, 1348.55) * mm, "end": v(11968.77, 1359.73) * mm});
            skFitSpline(sketch, "E7854", {"points": [v(14136.91, 2347.69) * mm, v(14136.91, 1435.86) * mm, v(13397.74, 696.69) * mm, v(12485.91, 696.69) * mm]});
            skFitSpline(sketch, "E7855", {"points": [v(12485.91, 696.69) * mm, v(11574.1, 696.69) * mm, v(10834.91, 1435.86) * mm, v(10834.91, 2347.69) * mm]});
            skFitSpline(sketch, "E7856", {"points": [v(10834.91, 2347.69) * mm, v(10834.91, 3259.5) * mm, v(11574.1, 3998.69) * mm, v(12485.91, 3998.69) * mm]});
            skFitSpline(sketch, "E7857", {"points": [v(12485.91, 3998.69) * mm, v(13397.74, 3998.69) * mm, v(14136.91, 3259.5) * mm, v(14136.91, 2347.69) * mm]});
            skLineSegment(sketch, "E7858", {"start": v(11814.74, 1657.42) * mm, "end": v(11835.06, 1638.31) * mm});
            skLineSegment(sketch, "E7859", {"start": v(11835.06, 1638.31) * mm, "end": v(11855.8, 1619.82) * mm});
            skLineSegment(sketch, "E7860", {"start": v(11855.8, 1619.82) * mm, "end": v(11877.13, 1601.94) * mm});
            skLineSegment(sketch, "E7861", {"start": v(11877.13, 1601.94) * mm, "end": v(11898.87, 1584.67) * mm});
            skLineSegment(sketch, "E7862", {"start": v(11898.87, 1584.67) * mm, "end": v(11861.89, 1536.3) * mm});
            skLineSegment(sketch, "E7863", {"start": v(11861.89, 1536.3) * mm, "end": v(11819.42, 1531.02) * mm});
            skLineSegment(sketch, "E7864", {"start": v(11819.42, 1531.02) * mm, "end": v(11796.05, 1550.74) * mm});
            skLineSegment(sketch, "E7865", {"start": v(11796.05, 1550.74) * mm, "end": v(11773.3, 1571.06) * mm});
            skLineSegment(sketch, "E7866", {"start": v(11773.3, 1571.06) * mm, "end": v(11729.8, 1570.04) * mm});
            skLineSegment(sketch, "E7867", {"start": v(11729.8, 1570.04) * mm, "end": v(11708.67, 1548.3) * mm});
            skLineSegment(sketch, "E7868", {"start": v(11708.67, 1548.3) * mm, "end": v(11711.32, 1503.6) * mm});
            skLineSegment(sketch, "E7869", {"start": v(11711.32, 1503.6) * mm, "end": v(11736.1, 1481.65) * mm});
            skLineSegment(sketch, "E7870", {"start": v(11736.1, 1481.65) * mm, "end": v(11761.5, 1460.31) * mm});
            skLineSegment(sketch, "E7871", {"start": v(11761.5, 1460.31) * mm, "end": v(11806, 1463.97) * mm});
            skFitSpline(sketch, "E7872", {"points": [v(14390.91, 2347.69) * mm, v(14390.91, 1295.58) * mm, v(13538.02, 442.69) * mm, v(12485.91, 442.69) * mm]});
            skFitSpline(sketch, "E7873", {"points": [v(12485.91, 442.69) * mm, v(11433.81, 442.69) * mm, v(10580.91, 1295.58) * mm, v(10580.91, 2347.69) * mm]});
            skFitSpline(sketch, "E7874", {"points": [v(10580.91, 2347.69) * mm, v(10580.91, 3399.79) * mm, v(11433.81, 4252.69) * mm, v(12485.91, 4252.69) * mm]});
            skFitSpline(sketch, "E7875", {"points": [v(12485.91, 4252.69) * mm, v(13538.02, 4252.69) * mm, v(14390.91, 3399.79) * mm, v(14390.91, 2347.69) * mm]});
            skFitSpline(sketch, "E7876", {"points": [v(14016.62, 2347.69) * mm, v(14016.62, 1502.3) * mm, v(13331.3, 816.98) * mm, v(12485.91, 816.98) * mm]});
            skFitSpline(sketch, "E7877", {"points": [v(12485.91, 816.98) * mm, v(11640.53, 816.98) * mm, v(10955.2, 1502.3) * mm, v(10955.2, 2347.69) * mm]});
            skFitSpline(sketch, "E7878", {"points": [v(10955.2, 2347.69) * mm, v(10955.2, 3193.07) * mm, v(11640.53, 3878.4) * mm, v(12485.91, 3878.4) * mm]});
            skFitSpline(sketch, "E7879", {"points": [v(12485.91, 3878.4) * mm, v(13331.3, 3878.4) * mm, v(14016.62, 3193.07) * mm, v(14016.62, 2347.69) * mm]});
            skLineSegment(sketch, "E7880", {"start": v(11807.48, -438.7) * mm, "end": v(11812.64, -438.04) * mm});
            skLineSegment(sketch, "E7881", {"start": v(11812.64, -438.04) * mm, "end": v(11819.53, -436.84) * mm});
            skLineSegment(sketch, "E7882", {"start": v(11819.53, -436.84) * mm, "end": v(11828.12, -434.97) * mm});
            skLineSegment(sketch, "E7883", {"start": v(11828.12, -434.97) * mm, "end": v(11838.35, -432.27) * mm});
            skLineSegment(sketch, "E7884", {"start": v(11838.35, -432.27) * mm, "end": v(11850.17, -428.6) * mm});
            skLineSegment(sketch, "E7885", {"start": v(11850.17, -428.6) * mm, "end": v(11863.5, -423.8) * mm});
            skLineSegment(sketch, "E7886", {"start": v(11863.5, -423.8) * mm, "end": v(11878.27, -417.75) * mm});
            skLineSegment(sketch, "E7887", {"start": v(11878.27, -417.75) * mm, "end": v(11894.39, -410.31) * mm});
            skLineSegment(sketch, "E7888", {"start": v(11894.39, -410.31) * mm, "end": v(11911.76, -401.36) * mm});
            skLineSegment(sketch, "E7889", {"start": v(11911.76, -401.36) * mm, "end": v(11930.29, -390.76) * mm});
            skLineSegment(sketch, "E7890", {"start": v(11930.29, -390.76) * mm, "end": v(11949.85, -378.41) * mm});
            skLineSegment(sketch, "E7891", {"start": v(11949.85, -378.41) * mm, "end": v(11970.33, -364.2) * mm});
            skLineSegment(sketch, "E7892", {"start": v(11970.33, -364.2) * mm, "end": v(11991.6, -348.02) * mm});
            skLineSegment(sketch, "E7893", {"start": v(11991.6, -348.02) * mm, "end": v(12013.51, -329.78) * mm});
            skLineSegment(sketch, "E7894", {"start": v(12013.51, -329.78) * mm, "end": v(12035.94, -309.4) * mm});
            skLineSegment(sketch, "E7895", {"start": v(12035.94, -309.4) * mm, "end": v(12058.73, -286.8) * mm});
            skLineSegment(sketch, "E7896", {"start": v(12058.73, -286.8) * mm, "end": v(12081.73, -261.9) * mm});
            skLineSegment(sketch, "E7897", {"start": v(12081.73, -261.9) * mm, "end": v(12104.79, -234.66) * mm});
            skLineSegment(sketch, "E7898", {"start": v(12104.79, -234.66) * mm, "end": v(12109.2, -208.44) * mm});
            skLineSegment(sketch, "E7899", {"start": v(12109.2, -208.44) * mm, "end": v(12093.76, -136.55) * mm});
            skLineSegment(sketch, "E7900", {"start": v(12093.76, -136.55) * mm, "end": v(12078.97, -114.45) * mm});
            skLineSegment(sketch, "E7901", {"start": v(12078.97, -114.45) * mm, "end": v(12046.77, -99.08) * mm});
            skLineSegment(sketch, "E7902", {"start": v(12046.77, -99.08) * mm, "end": v(12015.57, -85.82) * mm});
            skLineSegment(sketch, "E7903", {"start": v(12015.57, -85.82) * mm, "end": v(11985.5, -74.57) * mm});
            skLineSegment(sketch, "E7904", {"start": v(11985.5, -74.57) * mm, "end": v(11956.69, -65.2) * mm});
            skLineSegment(sketch, "E7905", {"start": v(11956.69, -65.2) * mm, "end": v(11929.21, -57.57) * mm});
            skLineSegment(sketch, "E7906", {"start": v(11929.21, -57.57) * mm, "end": v(11903.18, -51.55) * mm});
            skLineSegment(sketch, "E7907", {"start": v(11903.18, -51.55) * mm, "end": v(11878.67, -47) * mm});
            skLineSegment(sketch, "E7908", {"start": v(11878.67, -47) * mm, "end": v(11855.76, -43.77) * mm});
            skLineSegment(sketch, "E7909", {"start": v(11855.76, -43.77) * mm, "end": v(11834.52, -41.7) * mm});
            skLineSegment(sketch, "E7910", {"start": v(11834.52, -41.7) * mm, "end": v(11815, -40.68) * mm});
            skLineSegment(sketch, "E7911", {"start": v(11815, -40.68) * mm, "end": v(11797.25, -40.51) * mm});
            skLineSegment(sketch, "E7912", {"start": v(11797.25, -40.51) * mm, "end": v(11781.3, -41.06) * mm});
            skLineSegment(sketch, "E7913", {"start": v(11781.3, -41.06) * mm, "end": v(11767.17, -42.16) * mm});
            skLineSegment(sketch, "E7914", {"start": v(11767.17, -42.16) * mm, "end": v(11754.89, -43.67) * mm});
            skLineSegment(sketch, "E7915", {"start": v(11754.89, -43.67) * mm, "end": v(11744.45, -45.4) * mm});
            skLineSegment(sketch, "E7916", {"start": v(11744.45, -45.4) * mm, "end": v(11735.86, -47.22) * mm});
            skLineSegment(sketch, "E7917", {"start": v(11735.86, -47.22) * mm, "end": v(11729.08, -48.97) * mm});
            skLineSegment(sketch, "E7918", {"start": v(11729.08, -48.97) * mm, "end": v(11724.1, -50.48) * mm});
            skLineSegment(sketch, "E7919", {"start": v(11724.1, -50.48) * mm, "end": v(11720.9, -51.61) * mm});
            skLineSegment(sketch, "E7920", {"start": v(11720.9, -51.61) * mm, "end": v(11719.4, -52.21) * mm});
            skLineSegment(sketch, "E7921", {"start": v(11719.4, -52.21) * mm, "end": v(11520.38, -141.83) * mm});
            skLineSegment(sketch, "E7922", {"start": v(11520.38, -141.83) * mm, "end": v(11372.19, 72.82) * mm});
            skLineSegment(sketch, "E7923", {"start": v(11372.19, 72.82) * mm, "end": v(11526.52, 227.15) * mm});
            skLineSegment(sketch, "E7924", {"start": v(11526.52, 227.15) * mm, "end": v(11527.61, 228.34) * mm});
            skLineSegment(sketch, "E7925", {"start": v(11527.61, 228.34) * mm, "end": v(11529.8, 230.95) * mm});
            skLineSegment(sketch, "E7926", {"start": v(11529.8, 230.95) * mm, "end": v(11532.99, 235.06) * mm});
            skLineSegment(sketch, "E7927", {"start": v(11532.99, 235.06) * mm, "end": v(11537.02, 240.78) * mm});
            skLineSegment(sketch, "E7928", {"start": v(11537.02, 240.78) * mm, "end": v(11541.77, 248.17) * mm});
            skLineSegment(sketch, "E7929", {"start": v(11541.77, 248.17) * mm, "end": v(11547.1, 257.32) * mm});
            skLineSegment(sketch, "E7930", {"start": v(11547.1, 257.32) * mm, "end": v(11552.85, 268.27) * mm});
            skLineSegment(sketch, "E7931", {"start": v(11552.85, 268.27) * mm, "end": v(11558.88, 281.09) * mm});
            skLineSegment(sketch, "E7932", {"start": v(11558.88, 281.09) * mm, "end": v(11565.05, 295.8) * mm});
            skLineSegment(sketch, "E7933", {"start": v(11565.05, 295.8) * mm, "end": v(11571.2, 312.47) * mm});
            skLineSegment(sketch, "E7934", {"start": v(11571.2, 312.47) * mm, "end": v(11577.14, 331.09) * mm});
            skLineSegment(sketch, "E7935", {"start": v(11577.14, 331.09) * mm, "end": v(11582.75, 351.68) * mm});
            skLineSegment(sketch, "E7936", {"start": v(11582.75, 351.68) * mm, "end": v(11587.85, 374.24) * mm});
            skLineSegment(sketch, "E7937", {"start": v(11587.85, 374.24) * mm, "end": v(11592.28, 398.77) * mm});
            skLineSegment(sketch, "E7938", {"start": v(11592.28, 398.77) * mm, "end": v(11595.88, 425.25) * mm});
            skLineSegment(sketch, "E7939", {"start": v(11595.88, 425.25) * mm, "end": v(11598.48, 453.65) * mm});
            skLineSegment(sketch, "E7940", {"start": v(11598.48, 453.65) * mm, "end": v(11599.93, 483.92) * mm});
            skLineSegment(sketch, "E7941", {"start": v(11599.93, 483.92) * mm, "end": v(11600.06, 516.02) * mm});
            skLineSegment(sketch, "E7942", {"start": v(11600.06, 516.02) * mm, "end": v(11598.72, 549.88) * mm});
            skLineSegment(sketch, "E7943", {"start": v(11598.72, 549.88) * mm, "end": v(11595.76, 585.45) * mm});
            skLineSegment(sketch, "E7944", {"start": v(11595.76, 585.45) * mm, "end": v(11580.34, 607.1) * mm});
            skLineSegment(sketch, "E7945", {"start": v(11580.34, 607.1) * mm, "end": v(11518.58, 647.03) * mm});
            skLineSegment(sketch, "E7946", {"start": v(11518.58, 647.03) * mm, "end": v(11492.5, 652.2) * mm});
            skLineSegment(sketch, "E7947", {"start": v(11492.5, 652.2) * mm, "end": v(11458.86, 640.3) * mm});
            skLineSegment(sketch, "E7948", {"start": v(11458.86, 640.3) * mm, "end": v(11427.43, 627.6) * mm});
            skLineSegment(sketch, "E7949", {"start": v(11427.43, 627.6) * mm, "end": v(11398.22, 614.3) * mm});
            skLineSegment(sketch, "E7950", {"start": v(11398.22, 614.3) * mm, "end": v(11371.2, 600.55) * mm});
            skLineSegment(sketch, "E7951", {"start": v(11371.2, 600.55) * mm, "end": v(11346.38, 586.52) * mm});
            skLineSegment(sketch, "E7952", {"start": v(11346.38, 586.52) * mm, "end": v(11323.72, 572.37) * mm});
            skLineSegment(sketch, "E7953", {"start": v(11323.72, 572.37) * mm, "end": v(11303.17, 558.26) * mm});
            skLineSegment(sketch, "E7954", {"start": v(11303.17, 558.26) * mm, "end": v(11284.69, 544.35) * mm});
            skLineSegment(sketch, "E7955", {"start": v(11284.69, 544.35) * mm, "end": v(11268.22, 530.78) * mm});
            skLineSegment(sketch, "E7956", {"start": v(11268.22, 530.78) * mm, "end": v(11253.68, 517.7) * mm});
            skLineSegment(sketch, "E7957", {"start": v(11253.68, 517.7) * mm, "end": v(11241.01, 505.27) * mm});
            skLineSegment(sketch, "E7958", {"start": v(11241.01, 505.27) * mm, "end": v(11230.12, 493.6) * mm});
            skLineSegment(sketch, "E7959", {"start": v(11230.12, 493.6) * mm, "end": v(11220.91, 482.83) * mm});
            skLineSegment(sketch, "E7960", {"start": v(11220.91, 482.83) * mm, "end": v(11213.3, 473.09) * mm});
            skLineSegment(sketch, "E7961", {"start": v(11213.3, 473.09) * mm, "end": v(11207.14, 464.48) * mm});
            skLineSegment(sketch, "E7962", {"start": v(11207.14, 464.48) * mm, "end": v(11202.35, 457.11) * mm});
            skLineSegment(sketch, "E7963", {"start": v(11202.35, 457.11) * mm, "end": v(11198.8, 451.1) * mm});
            skLineSegment(sketch, "E7964", {"start": v(11198.8, 451.1) * mm, "end": v(11196.34, 446.5) * mm});
            skLineSegment(sketch, "E7965", {"start": v(11196.34, 446.5) * mm, "end": v(11194.87, 443.43) * mm});
            skLineSegment(sketch, "E7966", {"start": v(11194.87, 443.43) * mm, "end": v(11194.23, 441.95) * mm});
            skLineSegment(sketch, "E7967", {"start": v(11194.23, 441.95) * mm, "end": v(11116.88, 237.85) * mm});
            skLineSegment(sketch, "E7968", {"start": v(11116.88, 237.85) * mm, "end": v(10860.31, 284.84) * mm});
            skLineSegment(sketch, "E7969", {"start": v(10860.31, 284.84) * mm, "end": v(10860.31, 503.1) * mm});
            skLineSegment(sketch, "E7970", {"start": v(10860.31, 503.1) * mm, "end": v(10860.24, 504.72) * mm});
            skLineSegment(sketch, "E7971", {"start": v(10860.24, 504.72) * mm, "end": v(10859.95, 508.11) * mm});
            skLineSegment(sketch, "E7972", {"start": v(10859.95, 508.11) * mm, "end": v(10859.3, 513.27) * mm});
            skLineSegment(sketch, "E7973", {"start": v(10859.3, 513.27) * mm, "end": v(10858.1, 520.16) * mm});
            skLineSegment(sketch, "E7974", {"start": v(10858.1, 520.16) * mm, "end": v(10856.23, 528.75) * mm});
            skLineSegment(sketch, "E7975", {"start": v(10856.23, 528.75) * mm, "end": v(10853.53, 538.98) * mm});
            skLineSegment(sketch, "E7976", {"start": v(10853.53, 538.98) * mm, "end": v(10849.85, 550.8) * mm});
            skLineSegment(sketch, "E7977", {"start": v(10849.85, 550.8) * mm, "end": v(10845.06, 564.13) * mm});
            skLineSegment(sketch, "E7978", {"start": v(10845.06, 564.13) * mm, "end": v(10839.01, 578.9) * mm});
            skLineSegment(sketch, "E7979", {"start": v(10839.01, 578.9) * mm, "end": v(10831.57, 595.02) * mm});
            skLineSegment(sketch, "E7980", {"start": v(10831.57, 595.02) * mm, "end": v(10822.62, 612.4) * mm});
            skLineSegment(sketch, "E7981", {"start": v(10822.62, 612.4) * mm, "end": v(10812.02, 630.91) * mm});
            skLineSegment(sketch, "E7982", {"start": v(10812.02, 630.91) * mm, "end": v(10799.67, 650.48) * mm});
            skLineSegment(sketch, "E7983", {"start": v(10799.67, 650.48) * mm, "end": v(10785.46, 670.96) * mm});
            skLineSegment(sketch, "E7984", {"start": v(10785.46, 670.96) * mm, "end": v(10769.28, 692.22) * mm});
            skLineSegment(sketch, "E7985", {"start": v(10769.28, 692.22) * mm, "end": v(10751.04, 714.14) * mm});
            skLineSegment(sketch, "E7986", {"start": v(10751.04, 714.14) * mm, "end": v(10730.66, 736.57) * mm});
            skLineSegment(sketch, "E7987", {"start": v(10730.66, 736.57) * mm, "end": v(10708.05, 759.36) * mm});
            skLineSegment(sketch, "E7988", {"start": v(10708.05, 759.36) * mm, "end": v(10683.16, 782.36) * mm});
            skLineSegment(sketch, "E7989", {"start": v(10683.16, 782.36) * mm, "end": v(10655.92, 805.42) * mm});
            skLineSegment(sketch, "E7990", {"start": v(10655.92, 805.42) * mm, "end": v(10629.7, 809.83) * mm});
            skLineSegment(sketch, "E7991", {"start": v(10629.7, 809.83) * mm, "end": v(10557.8, 794.39) * mm});
            skLineSegment(sketch, "E7992", {"start": v(10557.8, 794.39) * mm, "end": v(10535.7, 779.6) * mm});
            skLineSegment(sketch, "E7993", {"start": v(10535.7, 779.6) * mm, "end": v(10520.34, 747.4) * mm});
            skLineSegment(sketch, "E7994", {"start": v(10520.34, 747.4) * mm, "end": v(10507.08, 716.2) * mm});
            skLineSegment(sketch, "E7995", {"start": v(10507.08, 716.2) * mm, "end": v(10495.83, 686.14) * mm});
            skLineSegment(sketch, "E7996", {"start": v(10495.83, 686.14) * mm, "end": v(10486.45, 657.31) * mm});
            skLineSegment(sketch, "E7997", {"start": v(10486.45, 657.31) * mm, "end": v(10478.82, 629.84) * mm});
            skLineSegment(sketch, "E7998", {"start": v(10478.82, 629.84) * mm, "end": v(10472.8, 603.8) * mm});
            skLineSegment(sketch, "E7999", {"start": v(10472.8, 603.8) * mm, "end": v(10468.25, 579.3) * mm});
            skLineSegment(sketch, "E8000", {"start": v(10468.25, 579.3) * mm, "end": v(10465.02, 556.4) * mm});
            skLineSegment(sketch, "E8001", {"start": v(10465.02, 556.4) * mm, "end": v(10462.97, 535.15) * mm});
            skLineSegment(sketch, "E8002", {"start": v(10462.97, 535.15) * mm, "end": v(10461.93, 515.63) * mm});
            skLineSegment(sketch, "E8003", {"start": v(10461.93, 515.63) * mm, "end": v(10461.77, 497.88) * mm});
            skLineSegment(sketch, "E8004", {"start": v(10461.77, 497.88) * mm, "end": v(10462.32, 481.93) * mm});
            skLineSegment(sketch, "E8005", {"start": v(10462.32, 481.93) * mm, "end": v(10463.42, 467.8) * mm});
            skLineSegment(sketch, "E8006", {"start": v(10463.42, 467.8) * mm, "end": v(10464.92, 455.52) * mm});
            skLineSegment(sketch, "E8007", {"start": v(10464.92, 455.52) * mm, "end": v(10466.66, 445.08) * mm});
            skLineSegment(sketch, "E8008", {"start": v(10466.66, 445.08) * mm, "end": v(10468.48, 436.48) * mm});
            skLineSegment(sketch, "E8009", {"start": v(10468.48, 436.48) * mm, "end": v(10470.22, 429.71) * mm});
            skLineSegment(sketch, "E8010", {"start": v(10470.22, 429.71) * mm, "end": v(10471.74, 424.74) * mm});
            skLineSegment(sketch, "E8011", {"start": v(10471.74, 424.74) * mm, "end": v(10472.87, 421.52) * mm});
            skLineSegment(sketch, "E8012", {"start": v(10472.87, 421.52) * mm, "end": v(10473.47, 420.02) * mm});
            skLineSegment(sketch, "E8013", {"start": v(10473.47, 420.02) * mm, "end": v(10563.08, 221) * mm});
            skLineSegment(sketch, "E8014", {"start": v(10563.08, 221) * mm, "end": v(10348.44, 72.82) * mm});
            skLineSegment(sketch, "E8015", {"start": v(10348.44, 72.82) * mm, "end": v(10194.1, 227.15) * mm});
            skLineSegment(sketch, "E8016", {"start": v(10194.1, 227.15) * mm, "end": v(10192.91, 228.24) * mm});
            skLineSegment(sketch, "E8017", {"start": v(10192.91, 228.24) * mm, "end": v(10190.3, 230.44) * mm});
            skLineSegment(sketch, "E8018", {"start": v(10190.3, 230.44) * mm, "end": v(10186.2, 233.62) * mm});
            skLineSegment(sketch, "E8019", {"start": v(10186.2, 233.62) * mm, "end": v(10180.48, 237.65) * mm});
            skLineSegment(sketch, "E8020", {"start": v(10180.48, 237.65) * mm, "end": v(10173.08, 242.4) * mm});
            skLineSegment(sketch, "E8021", {"start": v(10173.08, 242.4) * mm, "end": v(10163.94, 247.72) * mm});
            skLineSegment(sketch, "E8022", {"start": v(10163.94, 247.72) * mm, "end": v(10152.99, 253.48) * mm});
            skLineSegment(sketch, "E8023", {"start": v(10152.99, 253.48) * mm, "end": v(10140.17, 259.51) * mm});
            skLineSegment(sketch, "E8024", {"start": v(10140.17, 259.51) * mm, "end": v(10125.45, 265.68) * mm});
            skLineSegment(sketch, "E8025", {"start": v(10125.45, 265.68) * mm, "end": v(10108.79, 271.82) * mm});
            skLineSegment(sketch, "E8026", {"start": v(10108.79, 271.82) * mm, "end": v(10090.17, 277.77) * mm});
            skLineSegment(sketch, "E8027", {"start": v(10090.17, 277.77) * mm, "end": v(10069.58, 283.38) * mm});
            skLineSegment(sketch, "E8028", {"start": v(10069.58, 283.38) * mm, "end": v(10047.02, 288.48) * mm});
            skLineSegment(sketch, "E8029", {"start": v(10047.02, 288.48) * mm, "end": v(10022.48, 292.9) * mm});
            skLineSegment(sketch, "E8030", {"start": v(10022.48, 292.9) * mm, "end": v(9996, 296.5) * mm});
            skLineSegment(sketch, "E8031", {"start": v(9996, 296.5) * mm, "end": v(9967.61, 299.1) * mm});
            skLineSegment(sketch, "E8032", {"start": v(9967.61, 299.1) * mm, "end": v(9937.34, 300.55) * mm});
            skLineSegment(sketch, "E8033", {"start": v(9937.34, 300.55) * mm, "end": v(9905.24, 300.69) * mm});
            skLineSegment(sketch, "E8034", {"start": v(9905.24, 300.69) * mm, "end": v(9871.37, 299.35) * mm});
            skLineSegment(sketch, "E8035", {"start": v(9871.37, 299.35) * mm, "end": v(9835.8, 296.39) * mm});
            skLineSegment(sketch, "E8036", {"start": v(9835.8, 296.39) * mm, "end": v(9814.15, 280.97) * mm});
            skLineSegment(sketch, "E8037", {"start": v(9814.15, 280.97) * mm, "end": v(9774.23, 219.21) * mm});
            skLineSegment(sketch, "E8038", {"start": v(9774.23, 219.21) * mm, "end": v(9769.06, 193.13) * mm});
            skLineSegment(sketch, "E8039", {"start": v(9769.06, 193.13) * mm, "end": v(9780.96, 159.49) * mm});
            skLineSegment(sketch, "E8040", {"start": v(9780.96, 159.49) * mm, "end": v(9793.65, 128.06) * mm});
            skLineSegment(sketch, "E8041", {"start": v(9793.65, 128.06) * mm, "end": v(9806.95, 98.85) * mm});
            skLineSegment(sketch, "E8042", {"start": v(9806.95, 98.85) * mm, "end": v(9820.7, 71.84) * mm});
            skLineSegment(sketch, "E8043", {"start": v(9820.7, 71.84) * mm, "end": v(9834.74, 47.01) * mm});
            skLineSegment(sketch, "E8044", {"start": v(9834.74, 47.01) * mm, "end": v(9848.89, 24.35) * mm});
            skLineSegment(sketch, "E8045", {"start": v(9848.89, 24.35) * mm, "end": v(9863, 3.8) * mm});
            skLineSegment(sketch, "E8046", {"start": v(9863, 3.8) * mm, "end": v(9876.91, -14.68) * mm});
            skLineSegment(sketch, "E8047", {"start": v(9876.91, -14.68) * mm, "end": v(9890.48, -31.16) * mm});
            skLineSegment(sketch, "E8048", {"start": v(9890.48, -31.16) * mm, "end": v(9903.55, -45.69) * mm});
            skLineSegment(sketch, "E8049", {"start": v(9903.55, -45.69) * mm, "end": v(9915.99, -58.36) * mm});
            skLineSegment(sketch, "E8050", {"start": v(9915.99, -58.36) * mm, "end": v(9927.66, -69.25) * mm});
            skLineSegment(sketch, "E8051", {"start": v(9927.66, -69.25) * mm, "end": v(9938.42, -78.46) * mm});
            skLineSegment(sketch, "E8052", {"start": v(9938.42, -78.46) * mm, "end": v(9948.17, -86.08) * mm});
            skLineSegment(sketch, "E8053", {"start": v(9948.17, -86.08) * mm, "end": v(9956.78, -92.23) * mm});
            skLineSegment(sketch, "E8054", {"start": v(9956.78, -92.23) * mm, "end": v(9964.14, -97.02) * mm});
            skLineSegment(sketch, "E8055", {"start": v(9964.14, -97.02) * mm, "end": v(9970.17, -100.58) * mm});
            skLineSegment(sketch, "E8056", {"start": v(9970.17, -100.58) * mm, "end": v(9974.75, -103.03) * mm});
            skLineSegment(sketch, "E8057", {"start": v(9974.75, -103.03) * mm, "end": v(9977.83, -104.5) * mm});
            skLineSegment(sketch, "E8058", {"start": v(9977.83, -104.5) * mm, "end": v(9979.3, -105.14) * mm});
            skLineSegment(sketch, "E8059", {"start": v(9979.3, -105.14) * mm, "end": v(10183.4, -182.5) * mm});
            skLineSegment(sketch, "E8060", {"start": v(10183.4, -182.5) * mm, "end": v(10136.41, -439.06) * mm});
            skLineSegment(sketch, "E8061", {"start": v(10136.41, -439.06) * mm, "end": v(9918.15, -439.06) * mm});
            skLineSegment(sketch, "E8062", {"start": v(9918.15, -439.06) * mm, "end": v(9916.54, -439.13) * mm});
            skLineSegment(sketch, "E8063", {"start": v(9916.54, -439.13) * mm, "end": v(9913.14, -439.42) * mm});
            skLineSegment(sketch, "E8064", {"start": v(9913.14, -439.42) * mm, "end": v(9907.99, -440.08) * mm});
            skLineSegment(sketch, "E8065", {"start": v(9907.99, -440.08) * mm, "end": v(9901.1, -441.27) * mm});
            skLineSegment(sketch, "E8066", {"start": v(9901.1, -441.27) * mm, "end": v(9892.5, -443.14) * mm});
            skLineSegment(sketch, "E8067", {"start": v(9892.5, -443.14) * mm, "end": v(9882.28, -445.84) * mm});
            skLineSegment(sketch, "E8068", {"start": v(9882.28, -445.84) * mm, "end": v(9870.46, -449.52) * mm});
            skLineSegment(sketch, "E8069", {"start": v(9870.46, -449.52) * mm, "end": v(9857.13, -454.31) * mm});
            skLineSegment(sketch, "E8070", {"start": v(9857.13, -454.31) * mm, "end": v(9842.36, -460.36) * mm});
            skLineSegment(sketch, "E8071", {"start": v(9842.36, -460.36) * mm, "end": v(9826.24, -467.8) * mm});
            skLineSegment(sketch, "E8072", {"start": v(9826.24, -467.8) * mm, "end": v(9808.87, -476.75) * mm});
            skLineSegment(sketch, "E8073", {"start": v(9808.87, -476.75) * mm, "end": v(9790.34, -487.35) * mm});
            skLineSegment(sketch, "E8074", {"start": v(9790.34, -487.35) * mm, "end": v(9770.78, -499.7) * mm});
            skLineSegment(sketch, "E8075", {"start": v(9770.78, -499.7) * mm, "end": v(9750.3, -513.91) * mm});
            skLineSegment(sketch, "E8076", {"start": v(9750.3, -513.91) * mm, "end": v(9729.04, -530.1) * mm});
            skLineSegment(sketch, "E8077", {"start": v(9729.04, -530.1) * mm, "end": v(9707.12, -548.33) * mm});
            skLineSegment(sketch, "E8078", {"start": v(9707.12, -548.33) * mm, "end": v(9684.69, -568.71) * mm});
            skLineSegment(sketch, "E8079", {"start": v(9684.69, -568.71) * mm, "end": v(9661.9, -591.32) * mm});
            skLineSegment(sketch, "E8080", {"start": v(9661.9, -591.32) * mm, "end": v(9638.9, -616.21) * mm});
            skLineSegment(sketch, "E8081", {"start": v(9638.9, -616.21) * mm, "end": v(9615.84, -643.45) * mm});
            skLineSegment(sketch, "E8082", {"start": v(9615.84, -643.45) * mm, "end": v(9611.43, -669.67) * mm});
            skLineSegment(sketch, "E8083", {"start": v(9611.43, -669.67) * mm, "end": v(9626.87, -741.57) * mm});
            skLineSegment(sketch, "E8084", {"start": v(9626.87, -741.57) * mm, "end": v(9641.66, -763.66) * mm});
            skLineSegment(sketch, "E8085", {"start": v(9641.66, -763.66) * mm, "end": v(9673.86, -779.04) * mm});
            skLineSegment(sketch, "E8086", {"start": v(9673.86, -779.04) * mm, "end": v(9705.06, -792.29) * mm});
            skLineSegment(sketch, "E8087", {"start": v(9705.06, -792.29) * mm, "end": v(9735.12, -803.54) * mm});
            skLineSegment(sketch, "E8088", {"start": v(9735.12, -803.54) * mm, "end": v(9763.94, -812.92) * mm});
            skLineSegment(sketch, "E8089", {"start": v(9763.94, -812.92) * mm, "end": v(9791.42, -820.55) * mm});
            skLineSegment(sketch, "E8090", {"start": v(9791.42, -820.55) * mm, "end": v(9817.45, -826.57) * mm});
            skLineSegment(sketch, "E8091", {"start": v(9817.45, -826.57) * mm, "end": v(9841.96, -831.12) * mm});
            skLineSegment(sketch, "E8092", {"start": v(9841.96, -831.12) * mm, "end": v(9864.87, -834.35) * mm});
            skLineSegment(sketch, "E8093", {"start": v(9864.87, -834.35) * mm, "end": v(9886.1, -836.4) * mm});
            skLineSegment(sketch, "E8094", {"start": v(9886.1, -836.4) * mm, "end": v(9905.63, -837.44) * mm});
            skLineSegment(sketch, "E8095", {"start": v(9905.63, -837.44) * mm, "end": v(9923.38, -837.6) * mm});
            skLineSegment(sketch, "E8096", {"start": v(9923.38, -837.6) * mm, "end": v(9939.33, -837.05) * mm});
            skLineSegment(sketch, "E8097", {"start": v(9939.33, -837.05) * mm, "end": v(9953.45, -835.95) * mm});
            skLineSegment(sketch, "E8098", {"start": v(9953.45, -835.95) * mm, "end": v(9965.74, -834.45) * mm});
            skLineSegment(sketch, "E8099", {"start": v(9965.74, -834.45) * mm, "end": v(9976.17, -832.71) * mm});
            skLineSegment(sketch, "E8100", {"start": v(9976.17, -832.71) * mm, "end": v(9984.77, -830.89) * mm});
            skLineSegment(sketch, "E8101", {"start": v(9984.77, -830.89) * mm, "end": v(9991.54, -829.15) * mm});
            skLineSegment(sketch, "E8102", {"start": v(9991.54, -829.15) * mm, "end": v(9996.52, -827.63) * mm});
            skLineSegment(sketch, "E8103", {"start": v(9996.52, -827.63) * mm, "end": v(9999.73, -826.5) * mm});
            skLineSegment(sketch, "E8104", {"start": v(9999.73, -826.5) * mm, "end": v(10001.23, -825.9) * mm});
            skLineSegment(sketch, "E8105", {"start": v(10001.23, -825.9) * mm, "end": v(10200.25, -736.29) * mm});
            skLineSegment(sketch, "E8106", {"start": v(10200.25, -736.29) * mm, "end": v(10348.44, -950.93) * mm});
            skLineSegment(sketch, "E8107", {"start": v(10348.44, -950.93) * mm, "end": v(10194.1, -1105.27) * mm});
            skLineSegment(sketch, "E8108", {"start": v(10194.1, -1105.27) * mm, "end": v(10193.02, -1106.46) * mm});
            skLineSegment(sketch, "E8109", {"start": v(10193.02, -1106.46) * mm, "end": v(10190.82, -1109.06) * mm});
            skLineSegment(sketch, "E8110", {"start": v(10190.82, -1109.06) * mm, "end": v(10187.64, -1113.18) * mm});
            skLineSegment(sketch, "E8111", {"start": v(10187.64, -1113.18) * mm, "end": v(10183.6, -1118.9) * mm});
            skLineSegment(sketch, "E8112", {"start": v(10183.6, -1118.9) * mm, "end": v(10178.86, -1126.29) * mm});
            skLineSegment(sketch, "E8113", {"start": v(10178.86, -1126.29) * mm, "end": v(10173.54, -1135.43) * mm});
            skLineSegment(sketch, "E8114", {"start": v(10173.54, -1135.43) * mm, "end": v(10167.78, -1146.38) * mm});
            skLineSegment(sketch, "E8115", {"start": v(10167.78, -1146.38) * mm, "end": v(10161.74, -1159.2) * mm});
            skLineSegment(sketch, "E8116", {"start": v(10161.74, -1159.2) * mm, "end": v(10155.58, -1173.92) * mm});
            skLineSegment(sketch, "E8117", {"start": v(10155.58, -1173.92) * mm, "end": v(10149.44, -1190.58) * mm});
            skLineSegment(sketch, "E8118", {"start": v(10149.44, -1190.58) * mm, "end": v(10143.49, -1209.2) * mm});
            skLineSegment(sketch, "E8119", {"start": v(10143.49, -1209.2) * mm, "end": v(10137.88, -1229.8) * mm});
            skLineSegment(sketch, "E8120", {"start": v(10137.88, -1229.8) * mm, "end": v(10132.78, -1252.36) * mm});
            skLineSegment(sketch, "E8121", {"start": v(10132.78, -1252.36) * mm, "end": v(10128.35, -1276.89) * mm});
            skLineSegment(sketch, "E8122", {"start": v(10128.35, -1276.89) * mm, "end": v(10124.75, -1303.36) * mm});
            skLineSegment(sketch, "E8123", {"start": v(10124.75, -1303.36) * mm, "end": v(10122.15, -1331.76) * mm});
            skLineSegment(sketch, "E8124", {"start": v(10122.15, -1331.76) * mm, "end": v(10120.7, -1362.03) * mm});
            skLineSegment(sketch, "E8125", {"start": v(10120.7, -1362.03) * mm, "end": v(10120.57, -1394.13) * mm});
            skLineSegment(sketch, "E8126", {"start": v(10120.57, -1394.13) * mm, "end": v(10121.9, -1428) * mm});
            skLineSegment(sketch, "E8127", {"start": v(10121.9, -1428) * mm, "end": v(10124.87, -1463.56) * mm});
            skLineSegment(sketch, "E8128", {"start": v(10124.87, -1463.56) * mm, "end": v(10140.29, -1485.22) * mm});
            skLineSegment(sketch, "E8129", {"start": v(10140.29, -1485.22) * mm, "end": v(10202.04, -1525.14) * mm});
            skLineSegment(sketch, "E8130", {"start": v(10202.04, -1525.14) * mm, "end": v(10228.12, -1530.3) * mm});
            skLineSegment(sketch, "E8131", {"start": v(10228.12, -1530.3) * mm, "end": v(10261.77, -1518.4) * mm});
            skLineSegment(sketch, "E8132", {"start": v(10261.77, -1518.4) * mm, "end": v(10293.2, -1505.72) * mm});
            skLineSegment(sketch, "E8133", {"start": v(10293.2, -1505.72) * mm, "end": v(10322.41, -1492.42) * mm});
            skLineSegment(sketch, "E8134", {"start": v(10322.41, -1492.42) * mm, "end": v(10349.42, -1478.67) * mm});
            skLineSegment(sketch, "E8135", {"start": v(10349.42, -1478.67) * mm, "end": v(10374.24, -1464.64) * mm});
            skLineSegment(sketch, "E8136", {"start": v(10374.24, -1464.64) * mm, "end": v(10396.9, -1450.49) * mm});
            skLineSegment(sketch, "E8137", {"start": v(10396.9, -1450.49) * mm, "end": v(10417.46, -1436.37) * mm});
            skLineSegment(sketch, "E8138", {"start": v(10417.46, -1436.37) * mm, "end": v(10435.94, -1422.46) * mm});
            skLineSegment(sketch, "E8139", {"start": v(10435.94, -1422.46) * mm, "end": v(10452.41, -1408.9) * mm});
            skLineSegment(sketch, "E8140", {"start": v(10452.41, -1408.9) * mm, "end": v(10466.95, -1395.82) * mm});
            skLineSegment(sketch, "E8141", {"start": v(10466.95, -1395.82) * mm, "end": v(10479.61, -1383.38) * mm});
            skLineSegment(sketch, "E8142", {"start": v(10479.61, -1383.38) * mm, "end": v(10490.5, -1371.71) * mm});
            skLineSegment(sketch, "E8143", {"start": v(10490.5, -1371.71) * mm, "end": v(10499.71, -1360.95) * mm});
            skLineSegment(sketch, "E8144", {"start": v(10499.71, -1360.95) * mm, "end": v(10507.34, -1351.2) * mm});
            skLineSegment(sketch, "E8145", {"start": v(10507.34, -1351.2) * mm, "end": v(10513.49, -1342.6) * mm});
            skLineSegment(sketch, "E8146", {"start": v(10513.49, -1342.6) * mm, "end": v(10518.28, -1335.23) * mm});
            skLineSegment(sketch, "E8147", {"start": v(10518.28, -1335.23) * mm, "end": v(10521.84, -1329.2) * mm});
            skLineSegment(sketch, "E8148", {"start": v(10521.84, -1329.2) * mm, "end": v(10524.28, -1324.62) * mm});
            skLineSegment(sketch, "E8149", {"start": v(10524.28, -1324.62) * mm, "end": v(10525.76, -1321.54) * mm});
            skLineSegment(sketch, "E8150", {"start": v(10525.76, -1321.54) * mm, "end": v(10526.4, -1320.06) * mm});
            skLineSegment(sketch, "E8151", {"start": v(10526.4, -1320.06) * mm, "end": v(10603.75, -1115.97) * mm});
            skLineSegment(sketch, "E8152", {"start": v(10603.75, -1115.97) * mm, "end": v(10860.31, -1162.96) * mm});
            skLineSegment(sketch, "E8153", {"start": v(10860.31, -1162.96) * mm, "end": v(10860.32, -1381.22) * mm});
            skLineSegment(sketch, "E8154", {"start": v(10860.32, -1381.22) * mm, "end": v(10860.38, -1382.83) * mm});
            skLineSegment(sketch, "E8155", {"start": v(10860.38, -1382.83) * mm, "end": v(10860.67, -1386.23) * mm});
            skLineSegment(sketch, "E8156", {"start": v(10860.67, -1386.23) * mm, "end": v(10861.34, -1391.38) * mm});
            skLineSegment(sketch, "E8157", {"start": v(10861.34, -1391.38) * mm, "end": v(10862.53, -1398.28) * mm});
            skLineSegment(sketch, "E8158", {"start": v(10862.53, -1398.28) * mm, "end": v(10864.4, -1406.86) * mm});
            skLineSegment(sketch, "E8159", {"start": v(10864.4, -1406.86) * mm, "end": v(10867.1, -1417.1) * mm});
            skLineSegment(sketch, "E8160", {"start": v(10867.1, -1417.1) * mm, "end": v(10870.77, -1428.9) * mm});
            skLineSegment(sketch, "E8161", {"start": v(10870.77, -1428.9) * mm, "end": v(10875.57, -1442.24) * mm});
            skLineSegment(sketch, "E8162", {"start": v(10875.57, -1442.24) * mm, "end": v(10881.62, -1457) * mm});
            skLineSegment(sketch, "E8163", {"start": v(10881.62, -1457) * mm, "end": v(10889.06, -1473.13) * mm});
            skLineSegment(sketch, "E8164", {"start": v(10889.06, -1473.13) * mm, "end": v(10898.01, -1490.5) * mm});
            skLineSegment(sketch, "E8165", {"start": v(10898.01, -1490.5) * mm, "end": v(10908.6, -1509.03) * mm});
            skLineSegment(sketch, "E8166", {"start": v(10908.6, -1509.03) * mm, "end": v(10920.96, -1528.6) * mm});
            skLineSegment(sketch, "E8167", {"start": v(10920.96, -1528.6) * mm, "end": v(10935.17, -1549.07) * mm});
            skLineSegment(sketch, "E8168", {"start": v(10935.17, -1549.07) * mm, "end": v(10951.35, -1570.33) * mm});
            skLineSegment(sketch, "E8169", {"start": v(10951.35, -1570.33) * mm, "end": v(10969.59, -1592.25) * mm});
            skLineSegment(sketch, "E8170", {"start": v(10969.59, -1592.25) * mm, "end": v(10989.97, -1614.68) * mm});
            skLineSegment(sketch, "E8171", {"start": v(10989.97, -1614.68) * mm, "end": v(11012.57, -1637.48) * mm});
            skLineSegment(sketch, "E8172", {"start": v(11012.57, -1637.48) * mm, "end": v(11037.47, -1660.48) * mm});
            skLineSegment(sketch, "E8173", {"start": v(11037.47, -1660.48) * mm, "end": v(11064.71, -1683.53) * mm});
            skLineSegment(sketch, "E8174", {"start": v(11064.71, -1683.53) * mm, "end": v(11090.93, -1687.94) * mm});
            skLineSegment(sketch, "E8175", {"start": v(11090.93, -1687.94) * mm, "end": v(11162.82, -1672.5) * mm});
            skLineSegment(sketch, "E8176", {"start": v(11162.82, -1672.5) * mm, "end": v(11184.92, -1657.71) * mm});
            skLineSegment(sketch, "E8177", {"start": v(11184.92, -1657.71) * mm, "end": v(11200.3, -1625.5) * mm});
            skLineSegment(sketch, "E8178", {"start": v(11200.3, -1625.5) * mm, "end": v(11213.55, -1594.31) * mm});
            skLineSegment(sketch, "E8179", {"start": v(11213.55, -1594.31) * mm, "end": v(11224.8, -1564.25) * mm});
            skLineSegment(sketch, "E8180", {"start": v(11224.8, -1564.25) * mm, "end": v(11234.17, -1535.43) * mm});
            skLineSegment(sketch, "E8181", {"start": v(11234.17, -1535.43) * mm, "end": v(11241.8, -1507.95) * mm});
            skLineSegment(sketch, "E8182", {"start": v(11241.8, -1507.95) * mm, "end": v(11247.82, -1481.92) * mm});
            skLineSegment(sketch, "E8183", {"start": v(11247.82, -1481.92) * mm, "end": v(11252.38, -1457.41) * mm});
            skLineSegment(sketch, "E8184", {"start": v(11252.38, -1457.41) * mm, "end": v(11255.6, -1434.5) * mm});
            skLineSegment(sketch, "E8185", {"start": v(11255.6, -1434.5) * mm, "end": v(11257.66, -1413.27) * mm});
            skLineSegment(sketch, "E8186", {"start": v(11257.66, -1413.27) * mm, "end": v(11258.7, -1393.74) * mm});
            skLineSegment(sketch, "E8187", {"start": v(11258.7, -1393.74) * mm, "end": v(11258.86, -1376) * mm});
            skLineSegment(sketch, "E8188", {"start": v(11258.86, -1376) * mm, "end": v(11258.3, -1360.04) * mm});
            skLineSegment(sketch, "E8189", {"start": v(11258.3, -1360.04) * mm, "end": v(11257.2, -1345.92) * mm});
            skLineSegment(sketch, "E8190", {"start": v(11257.2, -1345.92) * mm, "end": v(11255.7, -1333.63) * mm});
            skLineSegment(sketch, "E8191", {"start": v(11255.7, -1333.63) * mm, "end": v(11253.97, -1323.2) * mm});
            skLineSegment(sketch, "E8192", {"start": v(11253.97, -1323.2) * mm, "end": v(11252.15, -1314.6) * mm});
            skLineSegment(sketch, "E8193", {"start": v(11252.15, -1314.6) * mm, "end": v(11250.4, -1307.83) * mm});
            skLineSegment(sketch, "E8194", {"start": v(11250.4, -1307.83) * mm, "end": v(11248.89, -1302.85) * mm});
            skLineSegment(sketch, "E8195", {"start": v(11248.89, -1302.85) * mm, "end": v(11247.76, -1299.64) * mm});
            skLineSegment(sketch, "E8196", {"start": v(11247.76, -1299.64) * mm, "end": v(11247.16, -1298.14) * mm});
            skLineSegment(sketch, "E8197", {"start": v(11247.16, -1298.14) * mm, "end": v(11157.54, -1099.12) * mm});
            skLineSegment(sketch, "E8198", {"start": v(11157.54, -1099.12) * mm, "end": v(11372.19, -950.93) * mm});
            skLineSegment(sketch, "E8199", {"start": v(11372.19, -950.93) * mm, "end": v(11526.53, -1105.26) * mm});
            skLineSegment(sketch, "E8200", {"start": v(11526.53, -1105.26) * mm, "end": v(11527.71, -1106.36) * mm});
            skLineSegment(sketch, "E8201", {"start": v(11527.71, -1106.36) * mm, "end": v(11530.32, -1108.55) * mm});
            skLineSegment(sketch, "E8202", {"start": v(11530.32, -1108.55) * mm, "end": v(11534.43, -1111.73) * mm});
            skLineSegment(sketch, "E8203", {"start": v(11534.43, -1111.73) * mm, "end": v(11540.15, -1115.76) * mm});
            skLineSegment(sketch, "E8204", {"start": v(11540.15, -1115.76) * mm, "end": v(11547.54, -1120.51) * mm});
            skLineSegment(sketch, "E8205", {"start": v(11547.54, -1120.51) * mm, "end": v(11556.69, -1125.83) * mm});
            skLineSegment(sketch, "E8206", {"start": v(11556.69, -1125.83) * mm, "end": v(11567.64, -1131.6) * mm});
            skLineSegment(sketch, "E8207", {"start": v(11567.64, -1131.6) * mm, "end": v(11580.46, -1137.63) * mm});
            skLineSegment(sketch, "E8208", {"start": v(11580.46, -1137.63) * mm, "end": v(11595.18, -1143.8) * mm});
            skLineSegment(sketch, "E8209", {"start": v(11595.18, -1143.8) * mm, "end": v(11611.84, -1149.93) * mm});
            skLineSegment(sketch, "E8210", {"start": v(11611.84, -1149.93) * mm, "end": v(11630.46, -1155.89) * mm});
            skLineSegment(sketch, "E8211", {"start": v(11630.46, -1155.89) * mm, "end": v(11651.05, -1161.5) * mm});
            skLineSegment(sketch, "E8212", {"start": v(11651.05, -1161.5) * mm, "end": v(11673.61, -1166.6) * mm});
            skLineSegment(sketch, "E8213", {"start": v(11673.61, -1166.6) * mm, "end": v(11698.14, -1171.02) * mm});
            skLineSegment(sketch, "E8214", {"start": v(11698.14, -1171.02) * mm, "end": v(11724.62, -1174.62) * mm});
            skLineSegment(sketch, "E8215", {"start": v(11724.62, -1174.62) * mm, "end": v(11753.02, -1177.22) * mm});
            skLineSegment(sketch, "E8216", {"start": v(11753.02, -1177.22) * mm, "end": v(11783.29, -1178.67) * mm});
            skLineSegment(sketch, "E8217", {"start": v(11783.29, -1178.67) * mm, "end": v(11815.39, -1178.8) * mm});
            skLineSegment(sketch, "E8218", {"start": v(11815.39, -1178.8) * mm, "end": v(11849.26, -1177.47) * mm});
            skLineSegment(sketch, "E8219", {"start": v(11849.26, -1177.47) * mm, "end": v(11884.82, -1174.5) * mm});
            skLineSegment(sketch, "E8220", {"start": v(11884.82, -1174.5) * mm, "end": v(11906.48, -1159.08) * mm});
            skLineSegment(sketch, "E8221", {"start": v(11906.48, -1159.08) * mm, "end": v(11946.4, -1097.33) * mm});
            skLineSegment(sketch, "E8222", {"start": v(11946.4, -1097.33) * mm, "end": v(11951.56, -1071.25) * mm});
            skLineSegment(sketch, "E8223", {"start": v(11951.56, -1071.25) * mm, "end": v(11939.66, -1037.6) * mm});
            skLineSegment(sketch, "E8224", {"start": v(11939.66, -1037.6) * mm, "end": v(11926.98, -1006.17) * mm});
            skLineSegment(sketch, "E8225", {"start": v(11926.98, -1006.17) * mm, "end": v(11913.67, -976.96) * mm});
            skLineSegment(sketch, "E8226", {"start": v(11913.67, -976.96) * mm, "end": v(11899.93, -949.95) * mm});
            skLineSegment(sketch, "E8227", {"start": v(11899.93, -949.95) * mm, "end": v(11885.9, -925.13) * mm});
            skLineSegment(sketch, "E8228", {"start": v(11885.9, -925.13) * mm, "end": v(11871.74, -902.46) * mm});
            skLineSegment(sketch, "E8229", {"start": v(11871.74, -902.46) * mm, "end": v(11857.63, -881.91) * mm});
            skLineSegment(sketch, "E8230", {"start": v(11857.63, -881.91) * mm, "end": v(11843.72, -863.43) * mm});
            skLineSegment(sketch, "E8231", {"start": v(11843.72, -863.43) * mm, "end": v(11830.15, -846.96) * mm});
            skLineSegment(sketch, "E8232", {"start": v(11830.15, -846.96) * mm, "end": v(11817.08, -832.43) * mm});
            skLineSegment(sketch, "E8233", {"start": v(11817.08, -832.43) * mm, "end": v(11804.64, -819.76) * mm});
            skLineSegment(sketch, "E8234", {"start": v(11804.64, -819.76) * mm, "end": v(11792.97, -808.87) * mm});
            skLineSegment(sketch, "E8235", {"start": v(11792.97, -808.87) * mm, "end": v(11782.2, -799.66) * mm});
            skLineSegment(sketch, "E8236", {"start": v(11782.2, -799.66) * mm, "end": v(11772.46, -792.03) * mm});
            skLineSegment(sketch, "E8237", {"start": v(11772.46, -792.03) * mm, "end": v(11763.85, -785.88) * mm});
            skLineSegment(sketch, "E8238", {"start": v(11763.85, -785.88) * mm, "end": v(11756.48, -781.1) * mm});
            skLineSegment(sketch, "E8239", {"start": v(11756.48, -781.1) * mm, "end": v(11750.46, -777.54) * mm});
            skLineSegment(sketch, "E8240", {"start": v(11750.46, -777.54) * mm, "end": v(11745.87, -775.09) * mm});
            skLineSegment(sketch, "E8241", {"start": v(11745.87, -775.09) * mm, "end": v(11742.8, -773.61) * mm});
            skLineSegment(sketch, "E8242", {"start": v(11742.8, -773.61) * mm, "end": v(11741.32, -772.98) * mm});
            skLineSegment(sketch, "E8243", {"start": v(11741.32, -772.98) * mm, "end": v(11537.22, -695.62) * mm});
            skLineSegment(sketch, "E8244", {"start": v(11537.22, -695.62) * mm, "end": v(11584.21, -439.06) * mm});
            skLineSegment(sketch, "E8245", {"start": v(11584.21, -439.06) * mm, "end": v(11802.48, -439.06) * mm});
            skLineSegment(sketch, "E8246", {"start": v(11802.48, -439.06) * mm, "end": v(11804.09, -438.99) * mm});
            skLineSegment(sketch, "E8247", {"start": v(11804.09, -438.99) * mm, "end": v(11807.48, -438.7) * mm});
            skLineSegment(sketch, "E8248", {"start": v(11063.51, -439.06) * mm, "end": v(10657.11, -439.06) * mm});
            skFitSpline(sketch, "E8249", {"points": [v(11953.36, -225.72) * mm, v(11953.36, -280.78) * mm, v(11908.72, -325.41) * mm, v(11853.66, -325.41) * mm]});
            skFitSpline(sketch, "E8250", {"points": [v(11853.66, -325.41) * mm, v(11798.6, -325.41) * mm, v(11753.97, -280.78) * mm, v(11753.97, -225.72) * mm]});
            skFitSpline(sketch, "E8251", {"points": [v(11753.97, -225.72) * mm, v(11753.97, -170.66) * mm, v(11798.6, -126.02) * mm, v(11853.66, -126.02) * mm]});
            skFitSpline(sketch, "E8252", {"points": [v(11853.66, -126.02) * mm, v(11908.72, -126.02) * mm, v(11953.36, -170.66) * mm, v(11953.36, -225.72) * mm]});
            skLineSegment(sketch, "E8253", {"start": v(10860.31, -642.26) * mm, "end": v(10860.31, -235.86) * mm});
            skLineSegment(sketch, "E8254", {"start": v(10562.83, 25.25) * mm, "end": v(10548.4, 15.9) * mm});
            skLineSegment(sketch, "E8255", {"start": v(10548.4, 15.9) * mm, "end": v(10534.38, 5.75) * mm});
            skLineSegment(sketch, "E8256", {"start": v(10534.38, 5.75) * mm, "end": v(10520.56, -4.62) * mm});
            skLineSegment(sketch, "E8257", {"start": v(10520.56, -4.62) * mm, "end": v(10507.15, -15.39) * mm});
            skLineSegment(sketch, "E8258", {"start": v(10554.7, -21.89) * mm, "end": v(10514.06, 33.59) * mm});
            skLineSegment(sketch, "E8259", {"start": v(10544.13, 54.31) * mm, "end": v(10538.65, 29.93) * mm});
            skLineSegment(sketch, "E8260", {"start": v(10538.65, 29.93) * mm, "end": v(10534.38, 5.75) * mm});
            skLineSegment(sketch, "E8261", {"start": v(10534.38, 5.75) * mm, "end": v(10531.13, -18.23) * mm});
            skLineSegment(sketch, "E8262", {"start": v(10531.13, -18.23) * mm, "end": v(10529.3, -41.8) * mm});
            skLineSegment(sketch, "E8263", {"start": v(10581.32, -3.6) * mm, "end": v(10558.16, 1.68) * mm});
            skLineSegment(sketch, "E8264", {"start": v(10558.16, 1.68) * mm, "end": v(10534.38, 5.75) * mm});
            skLineSegment(sketch, "E8265", {"start": v(10534.38, 5.75) * mm, "end": v(10510, 9) * mm});
            skLineSegment(sketch, "E8266", {"start": v(10510, 9) * mm, "end": v(10485.2, 11.03) * mm});
            skLineSegment(sketch, "E8267", {"start": v(10652.44, 34.4) * mm, "end": v(10645.33, 12.05) * mm});
            skLineSegment(sketch, "E8268", {"start": v(10645.33, 12.05) * mm, "end": v(10631.3, 5.14) * mm});
            skLineSegment(sketch, "E8269", {"start": v(10631.3, 5.14) * mm, "end": v(10609.16, 12.86) * mm});
            skLineSegment(sketch, "E8270", {"start": v(10609.16, 12.86) * mm, "end": v(10575.63, 73.21) * mm});
            skLineSegment(sketch, "E8271", {"start": v(10575.63, 73.21) * mm, "end": v(10583.76, 97.19) * mm});
            skLineSegment(sketch, "E8272", {"start": v(10583.76, 97.19) * mm, "end": v(10600.83, 105.52) * mm});
            skLineSegment(sketch, "E8273", {"start": v(10600.83, 105.52) * mm, "end": v(10624.8, 97.6) * mm});
            skLineSegment(sketch, "E8274", {"start": v(10624.8, 97.6) * mm, "end": v(10652.44, 34.4) * mm});
            skLineSegment(sketch, "E8275", {"start": v(10818.25, 162.82) * mm, "end": v(10825.36, 59.6) * mm});
            skLineSegment(sketch, "E8276", {"start": v(10825.36, 59.6) * mm, "end": v(10807.28, 83.98) * mm});
            skLineSegment(sketch, "E8277", {"start": v(10807.28, 83.98) * mm, "end": v(10787.57, 107.75) * mm});
            skLineSegment(sketch, "E8278", {"start": v(10787.57, 107.75) * mm, "end": v(10766.23, 130.72) * mm});
            skLineSegment(sketch, "E8279", {"start": v(10766.23, 130.72) * mm, "end": v(10743.47, 152.86) * mm});
            skLineSegment(sketch, "E8280", {"start": v(10743.47, 152.86) * mm, "end": v(10763.6, 51.26) * mm});
            skLineSegment(sketch, "E8281", {"start": v(10927.17, 125.84) * mm, "end": v(10909.49, 127.67) * mm});
            skLineSegment(sketch, "E8282", {"start": v(10909.49, 127.67) * mm, "end": v(10891.6, 128.89) * mm});
            skLineSegment(sketch, "E8283", {"start": v(10891.6, 128.89) * mm, "end": v(10873.93, 129.5) * mm});
            skLineSegment(sketch, "E8284", {"start": v(10873.93, 129.5) * mm, "end": v(10856.05, 129.7) * mm});
            skLineSegment(sketch, "E8285", {"start": v(10923.1, 91.5) * mm, "end": v(10906.44, 93.33) * mm});
            skLineSegment(sketch, "E8286", {"start": v(10906.44, 93.33) * mm, "end": v(10889.78, 94.34) * mm});
            skLineSegment(sketch, "E8287", {"start": v(10889.78, 94.34) * mm, "end": v(10873.12, 95.16) * mm});
            skLineSegment(sketch, "E8288", {"start": v(10873.12, 95.16) * mm, "end": v(10856.45, 95.16) * mm});
            skLineSegment(sketch, "E8289", {"start": v(10976.14, 100.24) * mm, "end": v(10956.02, 86.62) * mm});
            skLineSegment(sketch, "E8290", {"start": v(10956.02, 86.62) * mm, "end": v(10952.97, 69.55) * mm});
            skLineSegment(sketch, "E8291", {"start": v(10952.97, 69.55) * mm, "end": v(10965.17, 49.64) * mm});
            skLineSegment(sketch, "E8292", {"start": v(10965.17, 49.64) * mm, "end": v(10980.4, 46.18) * mm});
            skLineSegment(sketch, "E8293", {"start": v(10980.4, 46.18) * mm, "end": v(10995.44, 42.12) * mm});
            skLineSegment(sketch, "E8294", {"start": v(10995.44, 42.12) * mm, "end": v(11015.76, 54.1) * mm});
            skLineSegment(sketch, "E8295", {"start": v(11015.76, 54.1) * mm, "end": v(11020.84, 70.57) * mm});
            skLineSegment(sketch, "E8296", {"start": v(11020.84, 70.57) * mm, "end": v(11009.46, 91.9) * mm});
            skLineSegment(sketch, "E8297", {"start": v(11009.46, 91.9) * mm, "end": v(10992.8, 96.37) * mm});
            skLineSegment(sketch, "E8298", {"start": v(10992.8, 96.37) * mm, "end": v(10976.14, 100.24) * mm});
            skLineSegment(sketch, "E8299", {"start": v(10976.14, 100.24) * mm, "end": v(10962.32, 120.56) * mm});
            skLineSegment(sketch, "E8300", {"start": v(10962.32, 120.56) * mm, "end": v(10965.37, 137.42) * mm});
            skLineSegment(sketch, "E8301", {"start": v(10965.37, 137.42) * mm, "end": v(10986.9, 150.83) * mm});
            skLineSegment(sketch, "E8302", {"start": v(10986.9, 150.83) * mm, "end": v(11005.2, 146.57) * mm});
            skLineSegment(sketch, "E8303", {"start": v(11005.2, 146.57) * mm, "end": v(11023.48, 141.69) * mm});
            skLineSegment(sketch, "E8304", {"start": v(11023.48, 141.69) * mm, "end": v(11036.29, 119.95) * mm});
            skLineSegment(sketch, "E8305", {"start": v(11036.29, 119.95) * mm, "end": v(11031.2, 103.49) * mm});
            skLineSegment(sketch, "E8306", {"start": v(11031.2, 103.49) * mm, "end": v(11009.46, 91.9) * mm});
            skLineSegment(sketch, "E8307", {"start": v(11136.26, 38.46) * mm, "end": v(11151.1, 29.73) * mm});
            skLineSegment(sketch, "E8308", {"start": v(11151.1, 29.73) * mm, "end": v(11165.52, 20.38) * mm});
            skLineSegment(sketch, "E8309", {"start": v(11165.52, 20.38) * mm, "end": v(11179.74, 10.62) * mm});
            skLineSegment(sketch, "E8310", {"start": v(11179.74, 10.62) * mm, "end": v(11204.13, 14.08) * mm});
            skLineSegment(sketch, "E8311", {"start": v(11204.13, 14.08) * mm, "end": v(11214.5, 27.9) * mm});
            skLineSegment(sketch, "E8312", {"start": v(11214.5, 27.9) * mm, "end": v(11209.61, 52.69) * mm});
            skLineSegment(sketch, "E8313", {"start": v(11209.61, 52.69) * mm, "end": v(11194.17, 63.46) * mm});
            skLineSegment(sketch, "E8314", {"start": v(11194.17, 63.46) * mm, "end": v(11178.32, 73.62) * mm});
            skLineSegment(sketch, "E8315", {"start": v(11178.32, 73.62) * mm, "end": v(11162.07, 83.37) * mm});
            skLineSegment(sketch, "E8316", {"start": v(11162.07, 83.37) * mm, "end": v(11110.45, -6.24) * mm});
            skLineSegment(sketch, "E8317", {"start": v(11186.65, -60.5) * mm, "end": v(11231.76, -8.27) * mm});
            skLineSegment(sketch, "E8318", {"start": v(11242.94, 4.73) * mm, "end": v(11254.12, 17.94) * mm});
            skLineSegment(sketch, "E8319", {"start": v(11265.09, -117.19) * mm, "end": v(11241.52, -115.77) * mm});
            skLineSegment(sketch, "E8320", {"start": v(11241.52, -115.77) * mm, "end": v(11244.16, -92.6) * mm});
            skLineSegment(sketch, "E8321", {"start": v(11244.16, -92.6) * mm, "end": v(11308.17, -34.9) * mm});
            skLineSegment(sketch, "E8322", {"start": v(11305.53, -85.08) * mm, "end": v(11294.15, -71.27) * mm});
            skLineSegment(sketch, "E8323", {"start": v(11294.15, -71.27) * mm, "end": v(11282.56, -57.85) * mm});
            skLineSegment(sketch, "E8324", {"start": v(11282.56, -57.85) * mm, "end": v(11270.37, -44.85) * mm});
            skLineSegment(sketch, "E8325", {"start": v(11270.37, -44.85) * mm, "end": v(11257.77, -32.25) * mm});
            skLineSegment(sketch, "E8326", {"start": v(11302.68, -206.4) * mm, "end": v(11295.16, -192.58) * mm});
            skLineSegment(sketch, "E8327", {"start": v(11295.16, -192.58) * mm, "end": v(11287.24, -179.16) * mm});
            skLineSegment(sketch, "E8328", {"start": v(11287.24, -179.16) * mm, "end": v(11278.9, -165.96) * mm});
            skLineSegment(sketch, "E8329", {"start": v(11278.9, -165.96) * mm, "end": v(11284.4, -143.2) * mm});
            skLineSegment(sketch, "E8330", {"start": v(11284.4, -143.2) * mm, "end": v(11312.64, -123.28) * mm});
            skLineSegment(sketch, "E8331", {"start": v(11312.64, -123.28) * mm, "end": v(11336.61, -128.16) * mm});
            skLineSegment(sketch, "E8332", {"start": v(11336.61, -128.16) * mm, "end": v(11346.17, -143.2) * mm});
            skLineSegment(sketch, "E8333", {"start": v(11346.17, -143.2) * mm, "end": v(11355.1, -158.64) * mm});
            skLineSegment(sketch, "E8334", {"start": v(11355.1, -158.64) * mm, "end": v(11363.64, -174.29) * mm});
            skLineSegment(sketch, "E8335", {"start": v(11347.8, -220.21) * mm, "end": v(11370.35, -228.95) * mm});
            skLineSegment(sketch, "E8336", {"start": v(11370.35, -228.95) * mm, "end": v(11392.7, -239.1) * mm});
            skLineSegment(sketch, "E8337", {"start": v(11392.7, -239.1) * mm, "end": v(11398.8, -255.77) * mm});
            skLineSegment(sketch, "E8338", {"start": v(11398.8, -255.77) * mm, "end": v(11387.82, -277.72) * mm});
            skLineSegment(sketch, "E8339", {"start": v(11387.82, -277.72) * mm, "end": v(11338.24, -292.75) * mm});
            skLineSegment(sketch, "E8340", {"start": v(11316.3, -234.43) * mm, "end": v(11410.58, -191.97) * mm});
            skLineSegment(sketch, "E8341", {"start": v(11358.56, -400.04) * mm, "end": v(11359.58, -415.69) * mm});
            skLineSegment(sketch, "E8342", {"start": v(11359.58, -415.69) * mm, "end": v(11360.19, -431.34) * mm});
            skLineSegment(sketch, "E8343", {"start": v(11360.19, -431.34) * mm, "end": v(11360.19, -446.78) * mm});
            skLineSegment(sketch, "E8344", {"start": v(11360.19, -446.78) * mm, "end": v(11376.85, -463.24) * mm});
            skLineSegment(sketch, "E8345", {"start": v(11376.85, -463.24) * mm, "end": v(11445.73, -466.49) * mm});
            skLineSegment(sketch, "E8346", {"start": v(11445.73, -466.49) * mm, "end": v(11463.41, -448.4) * mm});
            skLineSegment(sketch, "E8347", {"start": v(11463.41, -448.4) * mm, "end": v(11463.41, -429.7) * mm});
            skLineSegment(sketch, "E8348", {"start": v(11463.41, -429.7) * mm, "end": v(11462.8, -410.81) * mm});
            skLineSegment(sketch, "E8349", {"start": v(11462.8, -410.81) * mm, "end": v(11461.79, -391.91) * mm});
            skLineSegment(sketch, "E8350", {"start": v(11462.8, -410.81) * mm, "end": v(11359.58, -415.69) * mm});
            skLineSegment(sketch, "E8351", {"start": v(11413.63, -571.14) * mm, "end": v(11417.49, -553.87) * mm});
            skLineSegment(sketch, "E8352", {"start": v(11417.49, -553.87) * mm, "end": v(11420.74, -536.39) * mm});
            skLineSegment(sketch, "E8353", {"start": v(11420.74, -536.39) * mm, "end": v(11423.38, -518.71) * mm});
            skLineSegment(sketch, "E8354", {"start": v(11423.38, -518.71) * mm, "end": v(11425.62, -501.24) * mm});
            skLineSegment(sketch, "E8355", {"start": v(11380.1, -563.21) * mm, "end": v(11383.55, -546.75) * mm});
            skLineSegment(sketch, "E8356", {"start": v(11383.55, -546.75) * mm, "end": v(11386.8, -530.5) * mm});
            skLineSegment(sketch, "E8357", {"start": v(11386.8, -530.5) * mm, "end": v(11389.45, -514.04) * mm});
            skLineSegment(sketch, "E8358", {"start": v(11389.45, -514.04) * mm, "end": v(11391.48, -497.38) * mm});
            skLineSegment(sketch, "E8359", {"start": v(11316.3, -643.68) * mm, "end": v(11322.6, -629.46) * mm});
            skLineSegment(sketch, "E8360", {"start": v(11322.6, -629.46) * mm, "end": v(11328.28, -614.83) * mm});
            skLineSegment(sketch, "E8361", {"start": v(11328.28, -614.83) * mm, "end": v(11333.57, -600.2) * mm});
            skLineSegment(sketch, "E8362", {"start": v(11333.57, -600.2) * mm, "end": v(11338.24, -585.36) * mm});
            skLineSegment(sketch, "E8363", {"start": v(11338.24, -585.36) * mm, "end": v(11371.16, -595.32) * mm});
            skLineSegment(sketch, "E8364", {"start": v(11371.16, -595.32) * mm, "end": v(11382.33, -616.86) * mm});
            skLineSegment(sketch, "E8365", {"start": v(11382.33, -616.86) * mm, "end": v(11376.65, -633.11) * mm});
            skLineSegment(sketch, "E8366", {"start": v(11376.65, -633.11) * mm, "end": v(11370.35, -649.17) * mm});
            skLineSegment(sketch, "E8367", {"start": v(11370.35, -649.17) * mm, "end": v(11379.29, -671.92) * mm});
            skLineSegment(sketch, "E8368", {"start": v(11379.29, -671.92) * mm, "end": v(11394.93, -679.04) * mm});
            skLineSegment(sketch, "E8369", {"start": v(11394.93, -679.04) * mm, "end": v(11418.1, -668.67) * mm});
            skLineSegment(sketch, "E8370", {"start": v(11418.1, -668.67) * mm, "end": v(11425, -651.2) * mm});
            skLineSegment(sketch, "E8371", {"start": v(11425, -651.2) * mm, "end": v(11431.3, -633.52) * mm});
            skLineSegment(sketch, "E8372", {"start": v(11431.3, -633.52) * mm, "end": v(11420.74, -610.56) * mm});
            skLineSegment(sketch, "E8373", {"start": v(11302.48, -768.65) * mm, "end": v(11291.91, -782.47) * mm});
            skLineSegment(sketch, "E8374", {"start": v(11291.91, -782.47) * mm, "end": v(11281.14, -795.67) * mm});
            skLineSegment(sketch, "E8375", {"start": v(11281.14, -795.67) * mm, "end": v(11269.76, -808.68) * mm});
            skLineSegment(sketch, "E8376", {"start": v(11269.76, -808.68) * mm, "end": v(11270.37, -833.27) * mm});
            skLineSegment(sketch, "E8377", {"start": v(11270.37, -833.27) * mm, "end": v(11282.77, -845.25) * mm});
            skLineSegment(sketch, "E8378", {"start": v(11282.77, -845.25) * mm, "end": v(11308.17, -843.22) * mm});
            skLineSegment(sketch, "E8379", {"start": v(11308.17, -843.22) * mm, "end": v(11320.56, -829.2) * mm});
            skLineSegment(sketch, "E8380", {"start": v(11320.56, -829.2) * mm, "end": v(11332.55, -814.57) * mm});
            skLineSegment(sketch, "E8381", {"start": v(11332.55, -814.57) * mm, "end": v(11343.93, -799.53) * mm});
            skLineSegment(sketch, "E8382", {"start": v(11343.93, -799.53) * mm, "end": v(11261.02, -737.76) * mm});
            skLineSegment(sketch, "E8383", {"start": v(11189.7, -902.76) * mm, "end": v(11204.13, -892.2) * mm});
            skLineSegment(sketch, "E8384", {"start": v(11204.13, -892.2) * mm, "end": v(11217.95, -881.22) * mm});
            skLineSegment(sketch, "E8385", {"start": v(11217.95, -881.22) * mm, "end": v(11231.76, -869.84) * mm});
            skLineSegment(sketch, "E8386", {"start": v(11231.76, -869.84) * mm, "end": v(11244.97, -858.06) * mm});
            skLineSegment(sketch, "E8387", {"start": v(11169.79, -874.72) * mm, "end": v(11183.2, -864.76) * mm});
            skLineSegment(sketch, "E8388", {"start": v(11183.2, -864.76) * mm, "end": v(11196.4, -854.4) * mm});
            skLineSegment(sketch, "E8389", {"start": v(11196.4, -854.4) * mm, "end": v(11209.2, -843.83) * mm});
            skLineSegment(sketch, "E8390", {"start": v(11209.2, -843.83) * mm, "end": v(11221.6, -832.66) * mm});
            skLineSegment(sketch, "E8391", {"start": v(11083.22, -924.7) * mm, "end": v(11098.26, -917.39) * mm});
            skLineSegment(sketch, "E8392", {"start": v(11098.26, -917.39) * mm, "end": v(11113.1, -909.87) * mm});
            skLineSegment(sketch, "E8393", {"start": v(11113.1, -909.87) * mm, "end": v(11127.52, -901.74) * mm});
            skLineSegment(sketch, "E8394", {"start": v(11127.52, -901.74) * mm, "end": v(11141.95, -893.2) * mm});
            skLineSegment(sketch, "E8395", {"start": v(11141.95, -893.2) * mm, "end": v(11139.1, -921.66) * mm});
            skLineSegment(sketch, "E8396", {"start": v(11139.1, -921.66) * mm, "end": v(11134.84, -950.3) * mm});
            skLineSegment(sketch, "E8397", {"start": v(11134.84, -950.3) * mm, "end": v(11128.94, -979.16) * mm});
            skLineSegment(sketch, "E8398", {"start": v(11128.94, -979.16) * mm, "end": v(11082.82, -886.7) * mm});
            skLineSegment(sketch, "E8399", {"start": v(10976.14, -978.35) * mm, "end": v(10959.07, -981.6) * mm});
            skLineSegment(sketch, "E8400", {"start": v(10959.07, -981.6) * mm, "end": v(10942.2, -984.45) * mm});
            skLineSegment(sketch, "E8401", {"start": v(10942.2, -984.45) * mm, "end": v(10925.13, -986.88) * mm});
            skLineSegment(sketch, "E8402", {"start": v(10925.13, -986.88) * mm, "end": v(10909.49, -1005.78) * mm});
            skLineSegment(sketch, "E8403", {"start": v(10909.49, -1005.78) * mm, "end": v(10910.91, -1022.85) * mm});
            skLineSegment(sketch, "E8404", {"start": v(10910.91, -1022.85) * mm, "end": v(10931.23, -1038.1) * mm});
            skLineSegment(sketch, "E8405", {"start": v(10931.23, -1038.1) * mm, "end": v(10949.72, -1035.65) * mm});
            skLineSegment(sketch, "E8406", {"start": v(10949.72, -1035.65) * mm, "end": v(10968.42, -1032.6) * mm});
            skLineSegment(sketch, "E8407", {"start": v(10968.42, -1032.6) * mm, "end": v(10986.9, -1028.95) * mm});
            skLineSegment(sketch, "E8408", {"start": v(10986.9, -1028.95) * mm, "end": v(10965.17, -927.75) * mm});
            skLineSegment(sketch, "E8409", {"start": v(10872.3, -938.73) * mm, "end": v(10873.12, -973.27) * mm});
            skLineSegment(sketch, "E8410", {"start": v(10873.12, -973.27) * mm, "end": v(10856.05, -1007.81) * mm});
            skLineSegment(sketch, "E8411", {"start": v(10856.05, -1007.81) * mm, "end": v(10836.95, -1041.95) * mm});
            skLineSegment(sketch, "E8412", {"start": v(10836.95, -1041.95) * mm, "end": v(10820.69, -1006.4) * mm});
            skLineSegment(sketch, "E8413", {"start": v(10820.69, -1006.4) * mm, "end": v(10806.47, -970.63) * mm});
            skLineSegment(sketch, "E8414", {"start": v(10806.47, -970.63) * mm, "end": v(10809.92, -936.29) * mm});
            skLineSegment(sketch, "E8415", {"start": v(10873.12, -973.27) * mm, "end": v(10856.45, -973.27) * mm});
            skLineSegment(sketch, "E8416", {"start": v(10856.45, -973.27) * mm, "end": v(10839.8, -973.07) * mm});
            skLineSegment(sketch, "E8417", {"start": v(10839.8, -973.07) * mm, "end": v(10823.13, -972.05) * mm});
            skLineSegment(sketch, "E8418", {"start": v(10823.13, -972.05) * mm, "end": v(10806.47, -970.63) * mm});
            skLineSegment(sketch, "E8419", {"start": v(10698.36, -984.24) * mm, "end": v(10715.64, -989.12) * mm});
            skLineSegment(sketch, "E8420", {"start": v(10715.64, -989.12) * mm, "end": v(10732.9, -993.39) * mm});
            skLineSegment(sketch, "E8421", {"start": v(10732.9, -993.39) * mm, "end": v(10750.18, -997.04) * mm});
            skLineSegment(sketch, "E8422", {"start": v(10750.18, -997.04) * mm, "end": v(10767.65, -1000.3) * mm});
            skLineSegment(sketch, "E8423", {"start": v(10708.32, -951.32) * mm, "end": v(10724.37, -955.8) * mm});
            skLineSegment(sketch, "E8424", {"start": v(10724.37, -955.8) * mm, "end": v(10740.63, -959.86) * mm});
            skLineSegment(sketch, "E8425", {"start": v(10740.63, -959.86) * mm, "end": v(10756.89, -963.31) * mm});
            skLineSegment(sketch, "E8426", {"start": v(10756.89, -963.31) * mm, "end": v(10773.34, -966.16) * mm});
            skLineSegment(sketch, "E8427", {"start": v(10631.3, -883.25) * mm, "end": v(10645.33, -890.16) * mm});
            skLineSegment(sketch, "E8428", {"start": v(10645.33, -890.16) * mm, "end": v(10659.35, -896.66) * mm});
            skLineSegment(sketch, "E8429", {"start": v(10659.35, -896.66) * mm, "end": v(10673.78, -902.76) * mm});
            skLineSegment(sketch, "E8430", {"start": v(10673.78, -902.76) * mm, "end": v(10688.4, -908.45) * mm});
            skLineSegment(sketch, "E8431", {"start": v(10688.4, -908.45) * mm, "end": v(10676.62, -940.76) * mm});
            skLineSegment(sketch, "E8432", {"start": v(10676.62, -940.76) * mm, "end": v(10654.47, -950.71) * mm});
            skLineSegment(sketch, "E8433", {"start": v(10654.47, -950.71) * mm, "end": v(10638.62, -944) * mm});
            skLineSegment(sketch, "E8434", {"start": v(10638.62, -944) * mm, "end": v(10622.98, -936.9) * mm});
            skLineSegment(sketch, "E8435", {"start": v(10622.98, -936.9) * mm, "end": v(10599.6, -944.62) * mm});
            skLineSegment(sketch, "E8436", {"start": v(10599.6, -944.62) * mm, "end": v(10591.68, -959.86) * mm});
            skLineSegment(sketch, "E8437", {"start": v(10591.68, -959.86) * mm, "end": v(10600.83, -983.63) * mm});
            skLineSegment(sketch, "E8438", {"start": v(10600.83, -983.63) * mm, "end": v(10617.9, -991.35) * mm});
            skLineSegment(sketch, "E8439", {"start": v(10617.9, -991.35) * mm, "end": v(10635.17, -998.67) * mm});
            skLineSegment(sketch, "E8440", {"start": v(10635.17, -998.67) * mm, "end": v(10658.74, -989.32) * mm});
            skFitSpline(sketch, "E8441", {"points": [v(11876.31, -439.06) * mm, v(11876.31, -1000.18) * mm, v(11421.44, -1455.06) * mm, v(10860.31, -1455.06) * mm]});
            skFitSpline(sketch, "E8442", {"points": [v(10860.31, -1455.06) * mm, v(10299.2, -1455.06) * mm, v(9844.31, -1000.18) * mm, v(9844.31, -439.06) * mm]});
            skFitSpline(sketch, "E8443", {"points": [v(9844.31, -439.06) * mm, v(9844.31, 122.06) * mm, v(10299.2, 576.94) * mm, v(10860.31, 576.94) * mm]});
            skFitSpline(sketch, "E8444", {"points": [v(10860.31, 576.94) * mm, v(11421.44, 576.94) * mm, v(11876.31, 122.06) * mm, v(11876.31, -439.06) * mm]});
            skLineSegment(sketch, "E8445", {"start": v(10552.47, -832.86) * mm, "end": v(10564.86, -842.2) * mm});
            skLineSegment(sketch, "E8446", {"start": v(10564.86, -842.2) * mm, "end": v(10577.66, -851.35) * mm});
            skLineSegment(sketch, "E8447", {"start": v(10577.66, -851.35) * mm, "end": v(10590.67, -859.88) * mm});
            skLineSegment(sketch, "E8448", {"start": v(10590.67, -859.88) * mm, "end": v(10603.88, -868.22) * mm});
            skLineSegment(sketch, "E8449", {"start": v(10603.88, -868.22) * mm, "end": v(10586.2, -897.68) * mm});
            skLineSegment(sketch, "E8450", {"start": v(10586.2, -897.68) * mm, "end": v(10562.83, -903.37) * mm});
            skLineSegment(sketch, "E8451", {"start": v(10562.83, -903.37) * mm, "end": v(10548.4, -894.02) * mm});
            skLineSegment(sketch, "E8452", {"start": v(10548.4, -894.02) * mm, "end": v(10534.38, -883.86) * mm});
            skLineSegment(sketch, "E8453", {"start": v(10534.38, -883.86) * mm, "end": v(10510, -887.11) * mm});
            skLineSegment(sketch, "E8454", {"start": v(10510, -887.11) * mm, "end": v(10499.43, -900.73) * mm});
            skLineSegment(sketch, "E8455", {"start": v(10499.43, -900.73) * mm, "end": v(10503.7, -925.72) * mm});
            skLineSegment(sketch, "E8456", {"start": v(10503.7, -925.72) * mm, "end": v(10519.14, -936.5) * mm});
            skLineSegment(sketch, "E8457", {"start": v(10519.14, -936.5) * mm, "end": v(10534.79, -947.06) * mm});
            skLineSegment(sketch, "E8458", {"start": v(10534.79, -947.06) * mm, "end": v(10559.78, -942.18) * mm});
            skFitSpline(sketch, "E8459", {"points": [v(12130.31, -439.06) * mm, v(12130.31, -1140.46) * mm, v(11561.72, -1709.06) * mm, v(10860.31, -1709.06) * mm]});
            skFitSpline(sketch, "E8460", {"points": [v(10860.31, -1709.06) * mm, v(10158.91, -1709.06) * mm, v(9590.31, -1140.46) * mm, v(9590.31, -439.06) * mm]});
            skFitSpline(sketch, "E8461", {"points": [v(9590.31, -439.06) * mm, v(9590.31, 262.34) * mm, v(10158.91, 830.94) * mm, v(10860.31, 830.94) * mm]});
            skFitSpline(sketch, "E8462", {"points": [v(10860.31, 830.94) * mm, v(11561.72, 830.94) * mm, v(12130.31, 262.34) * mm, v(12130.31, -439.06) * mm]});
            skFitSpline(sketch, "E8463", {"points": [v(11802.35, -439.06) * mm, v(11802.35, -959.33) * mm, v(11380.59, -1381.1) * mm, v(10860.31, -1381.1) * mm]});
            skFitSpline(sketch, "E8464", {"points": [v(10860.31, -1381.1) * mm, v(10340.04, -1381.1) * mm, v(9918.28, -959.33) * mm, v(9918.28, -439.06) * mm]});
            skFitSpline(sketch, "E8465", {"points": [v(9918.28, -439.06) * mm, v(9918.28, 81.21) * mm, v(10340.04, 502.98) * mm, v(10860.31, 502.98) * mm]});
            skFitSpline(sketch, "E8466", {"points": [v(10860.31, 502.98) * mm, v(11380.59, 502.98) * mm, v(11802.35, 81.21) * mm, v(11802.35, -439.06) * mm]});
            skLineSegment(sketch, "E8467", {"start": v(10188.8, -2761.16) * mm, "end": v(10192.26, -2760.86) * mm});
            skLineSegment(sketch, "E8468", {"start": v(10192.26, -2760.86) * mm, "end": v(10196.8, -2760.35) * mm});
            skLineSegment(sketch, "E8469", {"start": v(10196.8, -2760.35) * mm, "end": v(10202.44, -2759.56) * mm});
            skLineSegment(sketch, "E8470", {"start": v(10202.44, -2759.56) * mm, "end": v(10209.13, -2758.45) * mm});
            skLineSegment(sketch, "E8471", {"start": v(10209.13, -2758.45) * mm, "end": v(10216.88, -2756.94) * mm});
            skLineSegment(sketch, "E8472", {"start": v(10216.88, -2756.94) * mm, "end": v(10225.66, -2754.98) * mm});
            skLineSegment(sketch, "E8473", {"start": v(10225.66, -2754.98) * mm, "end": v(10235.45, -2752.53) * mm});
            skLineSegment(sketch, "E8474", {"start": v(10235.45, -2752.53) * mm, "end": v(10246.24, -2749.5) * mm});
            skLineSegment(sketch, "E8475", {"start": v(10246.24, -2749.5) * mm, "end": v(10258, -2745.88) * mm});
            skLineSegment(sketch, "E8476", {"start": v(10258, -2745.88) * mm, "end": v(10270.7, -2741.58) * mm});
            skLineSegment(sketch, "E8477", {"start": v(10270.7, -2741.58) * mm, "end": v(10284.32, -2736.55) * mm});
            skLineSegment(sketch, "E8478", {"start": v(10284.32, -2736.55) * mm, "end": v(10298.82, -2730.76) * mm});
            skLineSegment(sketch, "E8479", {"start": v(10298.82, -2730.76) * mm, "end": v(10314.17, -2724.14) * mm});
            skLineSegment(sketch, "E8480", {"start": v(10314.17, -2724.14) * mm, "end": v(10330.35, -2716.65) * mm});
            skLineSegment(sketch, "E8481", {"start": v(10330.35, -2716.65) * mm, "end": v(10347.3, -2708.24) * mm});
            skLineSegment(sketch, "E8482", {"start": v(10347.3, -2708.24) * mm, "end": v(10365, -2698.86) * mm});
            skLineSegment(sketch, "E8483", {"start": v(10365, -2698.86) * mm, "end": v(10383.4, -2688.46) * mm});
            skLineSegment(sketch, "E8484", {"start": v(10383.4, -2688.46) * mm, "end": v(10402.46, -2677) * mm});
            skLineSegment(sketch, "E8485", {"start": v(10402.46, -2677) * mm, "end": v(10422.14, -2664.45) * mm});
            skLineSegment(sketch, "E8486", {"start": v(10422.14, -2664.45) * mm, "end": v(10442.38, -2650.75) * mm});
            skLineSegment(sketch, "E8487", {"start": v(10442.38, -2650.75) * mm, "end": v(10463.15, -2635.87) * mm});
            skLineSegment(sketch, "E8488", {"start": v(10463.15, -2635.87) * mm, "end": v(10484.4, -2619.77) * mm});
            skLineSegment(sketch, "E8489", {"start": v(10484.4, -2619.77) * mm, "end": v(10506.05, -2602.41) * mm});
            skLineSegment(sketch, "E8490", {"start": v(10506.05, -2602.41) * mm, "end": v(10528.09, -2583.77) * mm});
            skLineSegment(sketch, "E8491", {"start": v(10528.09, -2583.77) * mm, "end": v(10548.9, -2563.97) * mm});
            skLineSegment(sketch, "E8492", {"start": v(10548.9, -2563.97) * mm, "end": v(10530.03, -2429.57) * mm});
            skLineSegment(sketch, "E8493", {"start": v(10530.03, -2429.57) * mm, "end": v(10504.58, -2416.26) * mm});
            skLineSegment(sketch, "E8494", {"start": v(10504.58, -2416.26) * mm, "end": v(10478.27, -2404.4) * mm});
            skLineSegment(sketch, "E8495", {"start": v(10478.27, -2404.4) * mm, "end": v(10452.66, -2393.68) * mm});
            skLineSegment(sketch, "E8496", {"start": v(10452.66, -2393.68) * mm, "end": v(10427.81, -2384.05) * mm});
            skLineSegment(sketch, "E8497", {"start": v(10427.81, -2384.05) * mm, "end": v(10403.75, -2375.46) * mm});
            skLineSegment(sketch, "E8498", {"start": v(10403.75, -2375.46) * mm, "end": v(10380.52, -2367.86) * mm});
            skLineSegment(sketch, "E8499", {"start": v(10380.52, -2367.86) * mm, "end": v(10358.14, -2361.2) * mm});
            skLineSegment(sketch, "E8500", {"start": v(10358.14, -2361.2) * mm, "end": v(10336.67, -2355.44) * mm});
            skLineSegment(sketch, "E8501", {"start": v(10336.67, -2355.44) * mm, "end": v(10316.11, -2350.51) * mm});
            skLineSegment(sketch, "E8502", {"start": v(10316.11, -2350.51) * mm, "end": v(10296.52, -2346.36) * mm});
            skLineSegment(sketch, "E8503", {"start": v(10296.52, -2346.36) * mm, "end": v(10277.9, -2342.94) * mm});
            skLineSegment(sketch, "E8504", {"start": v(10277.9, -2342.94) * mm, "end": v(10260.3, -2340.19) * mm});
            skLineSegment(sketch, "E8505", {"start": v(10260.3, -2340.19) * mm, "end": v(10243.7, -2338.05) * mm});
            skLineSegment(sketch, "E8506", {"start": v(10243.7, -2338.05) * mm, "end": v(10228.17, -2336.47) * mm});
            skLineSegment(sketch, "E8507", {"start": v(10228.17, -2336.47) * mm, "end": v(10213.7, -2335.4) * mm});
            skLineSegment(sketch, "E8508", {"start": v(10213.7, -2335.4) * mm, "end": v(10200.3, -2334.76) * mm});
            skLineSegment(sketch, "E8509", {"start": v(10200.3, -2334.76) * mm, "end": v(10188, -2334.5) * mm});
            skLineSegment(sketch, "E8510", {"start": v(10188, -2334.5) * mm, "end": v(10176.8, -2334.57) * mm});
            skLineSegment(sketch, "E8511", {"start": v(10176.8, -2334.57) * mm, "end": v(10166.7, -2334.9) * mm});
            skLineSegment(sketch, "E8512", {"start": v(10166.7, -2334.9) * mm, "end": v(10157.73, -2335.44) * mm});
            skLineSegment(sketch, "E8513", {"start": v(10157.73, -2335.44) * mm, "end": v(10149.87, -2336.12) * mm});
            skLineSegment(sketch, "E8514", {"start": v(10149.87, -2336.12) * mm, "end": v(10143.12, -2336.9) * mm});
            skLineSegment(sketch, "E8515", {"start": v(10143.12, -2336.9) * mm, "end": v(10137.5, -2337.68) * mm});
            skLineSegment(sketch, "E8516", {"start": v(10137.5, -2337.68) * mm, "end": v(10132.98, -2338.45) * mm});
            skLineSegment(sketch, "E8517", {"start": v(10132.98, -2338.45) * mm, "end": v(10129.57, -2339.11) * mm});
            skLineSegment(sketch, "E8518", {"start": v(10129.57, -2339.11) * mm, "end": v(10127.25, -2339.63) * mm});
            skLineSegment(sketch, "E8519", {"start": v(10127.25, -2339.63) * mm, "end": v(10126.02, -2339.94) * mm});
            skLineSegment(sketch, "E8520", {"start": v(10126.02, -2339.94) * mm, "end": v(9960.55, -2387.31) * mm});
            skLineSegment(sketch, "E8521", {"start": v(9960.55, -2387.31) * mm, "end": v(9857.39, -2129.83) * mm});
            skLineSegment(sketch, "E8522", {"start": v(9857.39, -2129.83) * mm, "end": v(10009.79, -2049.84) * mm});
            skLineSegment(sketch, "E8523", {"start": v(10009.79, -2049.84) * mm, "end": v(10010.9, -2049.22) * mm});
            skLineSegment(sketch, "E8524", {"start": v(10010.9, -2049.22) * mm, "end": v(10012.92, -2048) * mm});
            skLineSegment(sketch, "E8525", {"start": v(10012.92, -2048) * mm, "end": v(10015.85, -2046.12) * mm});
            skLineSegment(sketch, "E8526", {"start": v(10015.85, -2046.12) * mm, "end": v(10019.64, -2043.55) * mm});
            skLineSegment(sketch, "E8527", {"start": v(10019.64, -2043.55) * mm, "end": v(10024.26, -2040.24) * mm});
            skLineSegment(sketch, "E8528", {"start": v(10024.26, -2040.24) * mm, "end": v(10029.67, -2036.14) * mm});
            skLineSegment(sketch, "E8529", {"start": v(10029.67, -2036.14) * mm, "end": v(10035.83, -2031.2) * mm});
            skLineSegment(sketch, "E8530", {"start": v(10035.83, -2031.2) * mm, "end": v(10042.7, -2025.4) * mm});
            skLineSegment(sketch, "E8531", {"start": v(10042.7, -2025.4) * mm, "end": v(10050.22, -2018.66) * mm});
            skLineSegment(sketch, "E8532", {"start": v(10050.22, -2018.66) * mm, "end": v(10058.37, -2010.98) * mm});
            skLineSegment(sketch, "E8533", {"start": v(10058.37, -2010.98) * mm, "end": v(10067.1, -2002.3) * mm});
            skLineSegment(sketch, "E8534", {"start": v(10067.1, -2002.3) * mm, "end": v(10076.35, -1992.59) * mm});
            skLineSegment(sketch, "E8535", {"start": v(10076.35, -1992.59) * mm, "end": v(10086.07, -1981.81) * mm});
            skLineSegment(sketch, "E8536", {"start": v(10086.07, -1981.81) * mm, "end": v(10096.22, -1969.95) * mm});
            skLineSegment(sketch, "E8537", {"start": v(10096.22, -1969.95) * mm, "end": v(10106.74, -1956.95) * mm});
            skLineSegment(sketch, "E8538", {"start": v(10106.74, -1956.95) * mm, "end": v(10117.58, -1942.8) * mm});
            skLineSegment(sketch, "E8539", {"start": v(10117.58, -1942.8) * mm, "end": v(10128.68, -1927.47) * mm});
            skLineSegment(sketch, "E8540", {"start": v(10128.68, -1927.47) * mm, "end": v(10140, -1910.94) * mm});
            skLineSegment(sketch, "E8541", {"start": v(10140, -1910.94) * mm, "end": v(10151.45, -1893.18) * mm});
            skLineSegment(sketch, "E8542", {"start": v(10151.45, -1893.18) * mm, "end": v(10163, -1874.18) * mm});
            skLineSegment(sketch, "E8543", {"start": v(10163, -1874.18) * mm, "end": v(10174.6, -1853.92) * mm});
            skLineSegment(sketch, "E8544", {"start": v(10174.6, -1853.92) * mm, "end": v(10186.15, -1832.38) * mm});
            skLineSegment(sketch, "E8545", {"start": v(10186.15, -1832.38) * mm, "end": v(10197.63, -1809.55) * mm});
            skLineSegment(sketch, "E8546", {"start": v(10197.63, -1809.55) * mm, "end": v(10208.95, -1785.42) * mm});
            skLineSegment(sketch, "E8547", {"start": v(10208.95, -1785.42) * mm, "end": v(10220.07, -1760) * mm});
            skLineSegment(sketch, "E8548", {"start": v(10220.07, -1760) * mm, "end": v(10230.92, -1733.25) * mm});
            skLineSegment(sketch, "E8549", {"start": v(10230.92, -1733.25) * mm, "end": v(10240.14, -1706.05) * mm});
            skLineSegment(sketch, "E8550", {"start": v(10240.14, -1706.05) * mm, "end": v(10160.97, -1595.8) * mm});
            skLineSegment(sketch, "E8551", {"start": v(10160.97, -1595.8) * mm, "end": v(10132.25, -1595.85) * mm});
            skLineSegment(sketch, "E8552", {"start": v(10132.25, -1595.85) * mm, "end": v(10103.45, -1597.57) * mm});
            skLineSegment(sketch, "E8553", {"start": v(10103.45, -1597.57) * mm, "end": v(10075.8, -1599.98) * mm});
            skLineSegment(sketch, "E8554", {"start": v(10075.8, -1599.98) * mm, "end": v(10049.31, -1603) * mm});
            skLineSegment(sketch, "E8555", {"start": v(10049.31, -1603) * mm, "end": v(10024.02, -1606.58) * mm});
            skLineSegment(sketch, "E8556", {"start": v(10024.02, -1606.58) * mm, "end": v(9999.91, -1610.65) * mm});
            skLineSegment(sketch, "E8557", {"start": v(9999.91, -1610.65) * mm, "end": v(9977, -1615.15) * mm});
            skLineSegment(sketch, "E8558", {"start": v(9977, -1615.15) * mm, "end": v(9955.3, -1620.03) * mm});
            skLineSegment(sketch, "E8559", {"start": v(9955.3, -1620.03) * mm, "end": v(9934.82, -1625.21) * mm});
            skLineSegment(sketch, "E8560", {"start": v(9934.82, -1625.21) * mm, "end": v(9915.54, -1630.65) * mm});
            skLineSegment(sketch, "E8561", {"start": v(9915.54, -1630.65) * mm, "end": v(9897.47, -1636.27) * mm});
            skLineSegment(sketch, "E8562", {"start": v(9897.47, -1636.27) * mm, "end": v(9880.6, -1642.02) * mm});
            skLineSegment(sketch, "E8563", {"start": v(9880.6, -1642.02) * mm, "end": v(9864.92, -1647.83) * mm});
            skLineSegment(sketch, "E8564", {"start": v(9864.92, -1647.83) * mm, "end": v(9850.43, -1653.65) * mm});
            skLineSegment(sketch, "E8565", {"start": v(9850.43, -1653.65) * mm, "end": v(9837.11, -1659.42) * mm});
            skLineSegment(sketch, "E8566", {"start": v(9837.11, -1659.42) * mm, "end": v(9824.96, -1665.08) * mm});
            skLineSegment(sketch, "E8567", {"start": v(9824.96, -1665.08) * mm, "end": v(9813.95, -1670.58) * mm});
            skLineSegment(sketch, "E8568", {"start": v(9813.95, -1670.58) * mm, "end": v(9804.06, -1675.84) * mm});
            skLineSegment(sketch, "E8569", {"start": v(9804.06, -1675.84) * mm, "end": v(9795.28, -1680.82) * mm});
            skLineSegment(sketch, "E8570", {"start": v(9795.28, -1680.82) * mm, "end": v(9787.57, -1685.47) * mm});
            skLineSegment(sketch, "E8571", {"start": v(9787.57, -1685.47) * mm, "end": v(9780.93, -1689.73) * mm});
            skLineSegment(sketch, "E8572", {"start": v(9780.93, -1689.73) * mm, "end": v(9775.32, -1693.55) * mm});
            skLineSegment(sketch, "E8573", {"start": v(9775.32, -1693.55) * mm, "end": v(9770.7, -1696.86) * mm});
            skLineSegment(sketch, "E8574", {"start": v(9770.7, -1696.86) * mm, "end": v(9767.06, -1699.64) * mm});
            skLineSegment(sketch, "E8575", {"start": v(9767.06, -1699.64) * mm, "end": v(9764.35, -1701.81) * mm});
            skLineSegment(sketch, "E8576", {"start": v(9764.35, -1701.81) * mm, "end": v(9762.54, -1703.35) * mm});
            skLineSegment(sketch, "E8577", {"start": v(9762.54, -1703.35) * mm, "end": v(9761.59, -1704.2) * mm});
            skLineSegment(sketch, "E8578", {"start": v(9761.59, -1704.2) * mm, "end": v(9637.1, -1823.03) * mm});
            skLineSegment(sketch, "E8579", {"start": v(9637.1, -1823.03) * mm, "end": v(9426.09, -1643) * mm});
            skLineSegment(sketch, "E8580", {"start": v(9426.09, -1643) * mm, "end": v(9523.86, -1501.34) * mm});
            skLineSegment(sketch, "E8581", {"start": v(9523.86, -1501.34) * mm, "end": v(9524.54, -1500.27) * mm});
            skLineSegment(sketch, "E8582", {"start": v(9524.54, -1500.27) * mm, "end": v(9525.77, -1498.25) * mm});
            skLineSegment(sketch, "E8583", {"start": v(9525.77, -1498.25) * mm, "end": v(9527.5, -1495.23) * mm});
            skLineSegment(sketch, "E8584", {"start": v(9527.5, -1495.23) * mm, "end": v(9529.66, -1491.2) * mm});
            skLineSegment(sketch, "E8585", {"start": v(9529.66, -1491.2) * mm, "end": v(9532.21, -1486.11) * mm});
            skLineSegment(sketch, "E8586", {"start": v(9532.21, -1486.11) * mm, "end": v(9535.1, -1479.97) * mm});
            skLineSegment(sketch, "E8587", {"start": v(9535.1, -1479.97) * mm, "end": v(9538.25, -1472.74) * mm});
            skLineSegment(sketch, "E8588", {"start": v(9538.25, -1472.74) * mm, "end": v(9541.63, -1464.4) * mm});
            skLineSegment(sketch, "E8589", {"start": v(9541.63, -1464.4) * mm, "end": v(9545.17, -1454.94) * mm});
            skLineSegment(sketch, "E8590", {"start": v(9545.17, -1454.94) * mm, "end": v(9548.82, -1444.35) * mm});
            skLineSegment(sketch, "E8591", {"start": v(9548.82, -1444.35) * mm, "end": v(9552.5, -1432.6) * mm});
            skLineSegment(sketch, "E8592", {"start": v(9552.5, -1432.6) * mm, "end": v(9556.18, -1419.71) * mm});
            skLineSegment(sketch, "E8593", {"start": v(9556.18, -1419.71) * mm, "end": v(9559.79, -1405.66) * mm});
            skLineSegment(sketch, "E8594", {"start": v(9559.79, -1405.66) * mm, "end": v(9563.26, -1390.43) * mm});
            skLineSegment(sketch, "E8595", {"start": v(9563.26, -1390.43) * mm, "end": v(9566.53, -1374.03) * mm});
            skLineSegment(sketch, "E8596", {"start": v(9566.53, -1374.03) * mm, "end": v(9569.55, -1356.47) * mm});
            skLineSegment(sketch, "E8597", {"start": v(9569.55, -1356.47) * mm, "end": v(9572.26, -1337.74) * mm});
            skLineSegment(sketch, "E8598", {"start": v(9572.26, -1337.74) * mm, "end": v(9574.6, -1317.84) * mm});
            skLineSegment(sketch, "E8599", {"start": v(9574.6, -1317.84) * mm, "end": v(9576.5, -1296.8) * mm});
            skLineSegment(sketch, "E8600", {"start": v(9576.5, -1296.8) * mm, "end": v(9577.9, -1274.6) * mm});
            skLineSegment(sketch, "E8601", {"start": v(9577.9, -1274.6) * mm, "end": v(9578.73, -1251.27) * mm});
            skLineSegment(sketch, "E8602", {"start": v(9578.73, -1251.27) * mm, "end": v(9578.96, -1226.83) * mm});
            skLineSegment(sketch, "E8603", {"start": v(9578.96, -1226.83) * mm, "end": v(9578.51, -1201.28) * mm});
            skLineSegment(sketch, "E8604", {"start": v(9578.51, -1201.28) * mm, "end": v(9577.33, -1174.65) * mm});
            skLineSegment(sketch, "E8605", {"start": v(9577.33, -1174.65) * mm, "end": v(9575.35, -1146.97) * mm});
            skLineSegment(sketch, "E8606", {"start": v(9575.35, -1146.97) * mm, "end": v(9572.53, -1118.25) * mm});
            skLineSegment(sketch, "E8607", {"start": v(9572.53, -1118.25) * mm, "end": v(9568.05, -1089.88) * mm});
            skLineSegment(sketch, "E8608", {"start": v(9568.05, -1089.88) * mm, "end": v(9446.72, -1029.05) * mm});
            skLineSegment(sketch, "E8609", {"start": v(9446.72, -1029.05) * mm, "end": v(9421.31, -1042.43) * mm});
            skLineSegment(sketch, "E8610", {"start": v(9421.31, -1042.43) * mm, "end": v(9396.6, -1057.35) * mm});
            skLineSegment(sketch, "E8611", {"start": v(9396.6, -1057.35) * mm, "end": v(9373.24, -1072.33) * mm});
            skLineSegment(sketch, "E8612", {"start": v(9373.24, -1072.33) * mm, "end": v(9351.2, -1087.31) * mm});
            skLineSegment(sketch, "E8613", {"start": v(9351.2, -1087.31) * mm, "end": v(9330.46, -1102.24) * mm});
            skLineSegment(sketch, "E8614", {"start": v(9330.46, -1102.24) * mm, "end": v(9311, -1117.04) * mm});
            skLineSegment(sketch, "E8615", {"start": v(9311, -1117.04) * mm, "end": v(9292.82, -1131.68) * mm});
            skLineSegment(sketch, "E8616", {"start": v(9292.82, -1131.68) * mm, "end": v(9275.87, -1146.08) * mm});
            skLineSegment(sketch, "E8617", {"start": v(9275.87, -1146.08) * mm, "end": v(9260.14, -1160.19) * mm});
            skLineSegment(sketch, "E8618", {"start": v(9260.14, -1160.19) * mm, "end": v(9245.6, -1173.96) * mm});
            skLineSegment(sketch, "E8619", {"start": v(9245.6, -1173.96) * mm, "end": v(9232.2, -1187.34) * mm});
            skLineSegment(sketch, "E8620", {"start": v(9232.2, -1187.34) * mm, "end": v(9219.94, -1200.27) * mm});
            skLineSegment(sketch, "E8621", {"start": v(9219.94, -1200.27) * mm, "end": v(9208.76, -1212.7) * mm});
            skLineSegment(sketch, "E8622", {"start": v(9208.76, -1212.7) * mm, "end": v(9198.63, -1224.59) * mm});
            skLineSegment(sketch, "E8623", {"start": v(9198.63, -1224.59) * mm, "end": v(9189.52, -1235.89) * mm});
            skLineSegment(sketch, "E8624", {"start": v(9189.52, -1235.89) * mm, "end": v(9181.4, -1246.55) * mm});
            skLineSegment(sketch, "E8625", {"start": v(9181.4, -1246.55) * mm, "end": v(9174.2, -1256.53) * mm});
            skLineSegment(sketch, "E8626", {"start": v(9174.2, -1256.53) * mm, "end": v(9167.88, -1265.79) * mm});
            skLineSegment(sketch, "E8627", {"start": v(9167.88, -1265.79) * mm, "end": v(9162.42, -1274.28) * mm});
            skLineSegment(sketch, "E8628", {"start": v(9162.42, -1274.28) * mm, "end": v(9157.77, -1281.98) * mm});
            skLineSegment(sketch, "E8629", {"start": v(9157.77, -1281.98) * mm, "end": v(9153.86, -1288.83) * mm});
            skLineSegment(sketch, "E8630", {"start": v(9153.86, -1288.83) * mm, "end": v(9150.66, -1294.82) * mm});
            skLineSegment(sketch, "E8631", {"start": v(9150.66, -1294.82) * mm, "end": v(9148.12, -1299.9) * mm});
            skLineSegment(sketch, "E8632", {"start": v(9148.12, -1299.9) * mm, "end": v(9146.18, -1304.05) * mm});
            skLineSegment(sketch, "E8633", {"start": v(9146.18, -1304.05) * mm, "end": v(9144.8, -1307.24) * mm});
            skLineSegment(sketch, "E8634", {"start": v(9144.8, -1307.24) * mm, "end": v(9143.9, -1309.44) * mm});
            skLineSegment(sketch, "E8635", {"start": v(9143.9, -1309.44) * mm, "end": v(9143.46, -1310.63) * mm});
            skLineSegment(sketch, "E8636", {"start": v(9143.46, -1310.63) * mm, "end": v(9088.45, -1473.71) * mm});
            skLineSegment(sketch, "E8637", {"start": v(9088.45, -1473.71) * mm, "end": v(8817.94, -1412.35) * mm});
            skLineSegment(sketch, "E8638", {"start": v(8817.94, -1412.35) * mm, "end": v(8838.68, -1241.5) * mm});
            skLineSegment(sketch, "E8639", {"start": v(8838.68, -1241.5) * mm, "end": v(8838.8, -1240.23) * mm});
            skLineSegment(sketch, "E8640", {"start": v(8838.8, -1240.23) * mm, "end": v(8838.94, -1237.86) * mm});
            skLineSegment(sketch, "E8641", {"start": v(8838.94, -1237.86) * mm, "end": v(8839.07, -1234.38) * mm});
            skLineSegment(sketch, "E8642", {"start": v(8839.07, -1234.38) * mm, "end": v(8839.1, -1229.8) * mm});
            skLineSegment(sketch, "E8643", {"start": v(8839.1, -1229.8) * mm, "end": v(8839, -1224.12) * mm});
            skLineSegment(sketch, "E8644", {"start": v(8839, -1224.12) * mm, "end": v(8838.7, -1217.34) * mm});
            skLineSegment(sketch, "E8645", {"start": v(8838.7, -1217.34) * mm, "end": v(8838.14, -1209.47) * mm});
            skLineSegment(sketch, "E8646", {"start": v(8838.14, -1209.47) * mm, "end": v(8837.25, -1200.52) * mm});
            skLineSegment(sketch, "E8647", {"start": v(8837.25, -1200.52) * mm, "end": v(8836, -1190.5) * mm});
            skLineSegment(sketch, "E8648", {"start": v(8836, -1190.5) * mm, "end": v(8834.3, -1179.43) * mm});
            skLineSegment(sketch, "E8649", {"start": v(8834.3, -1179.43) * mm, "end": v(8832.11, -1167.32) * mm});
            skLineSegment(sketch, "E8650", {"start": v(8832.11, -1167.32) * mm, "end": v(8829.37, -1154.2) * mm});
            skLineSegment(sketch, "E8651", {"start": v(8829.37, -1154.2) * mm, "end": v(8826.03, -1140.07) * mm});
            skLineSegment(sketch, "E8652", {"start": v(8826.03, -1140.07) * mm, "end": v(8822.03, -1124.97) * mm});
            skLineSegment(sketch, "E8653", {"start": v(8822.03, -1124.97) * mm, "end": v(8817.3, -1108.93) * mm});
            skLineSegment(sketch, "E8654", {"start": v(8817.3, -1108.93) * mm, "end": v(8811.82, -1091.98) * mm});
            skLineSegment(sketch, "E8655", {"start": v(8811.82, -1091.98) * mm, "end": v(8805.51, -1074.13) * mm});
            skLineSegment(sketch, "E8656", {"start": v(8805.51, -1074.13) * mm, "end": v(8798.33, -1055.43) * mm});
            skLineSegment(sketch, "E8657", {"start": v(8798.33, -1055.43) * mm, "end": v(8790.23, -1035.91) * mm});
            skLineSegment(sketch, "E8658", {"start": v(8790.23, -1035.91) * mm, "end": v(8781.16, -1015.6) * mm});
            skLineSegment(sketch, "E8659", {"start": v(8781.16, -1015.6) * mm, "end": v(8771.06, -994.56) * mm});
            skLineSegment(sketch, "E8660", {"start": v(8771.06, -994.56) * mm, "end": v(8759.9, -972.81) * mm});
            skLineSegment(sketch, "E8661", {"start": v(8759.9, -972.81) * mm, "end": v(8747.63, -950.4) * mm});
            skLineSegment(sketch, "E8662", {"start": v(8747.63, -950.4) * mm, "end": v(8734.21, -927.37) * mm});
            skLineSegment(sketch, "E8663", {"start": v(8734.21, -927.37) * mm, "end": v(8719.6, -903.78) * mm});
            skLineSegment(sketch, "E8664", {"start": v(8719.6, -903.78) * mm, "end": v(8703.75, -879.66) * mm});
            skLineSegment(sketch, "E8665", {"start": v(8703.75, -879.66) * mm, "end": v(8686.6, -856.62) * mm});
            skLineSegment(sketch, "E8666", {"start": v(8686.6, -856.62) * mm, "end": v(8550.9, -859.14) * mm});
            skLineSegment(sketch, "E8667", {"start": v(8550.9, -859.14) * mm, "end": v(8534.62, -882.8) * mm});
            skLineSegment(sketch, "E8668", {"start": v(8534.62, -882.8) * mm, "end": v(8519.68, -907.5) * mm});
            skLineSegment(sketch, "E8669", {"start": v(8519.68, -907.5) * mm, "end": v(8505.95, -931.62) * mm});
            skLineSegment(sketch, "E8670", {"start": v(8505.95, -931.62) * mm, "end": v(8493.4, -955.13) * mm});
            skLineSegment(sketch, "E8671", {"start": v(8493.4, -955.13) * mm, "end": v(8481.97, -977.98) * mm});
            skLineSegment(sketch, "E8672", {"start": v(8481.97, -977.98) * mm, "end": v(8471.62, -1000.13) * mm});
            skLineSegment(sketch, "E8673", {"start": v(8471.62, -1000.13) * mm, "end": v(8462.32, -1021.54) * mm});
            skLineSegment(sketch, "E8674", {"start": v(8462.32, -1021.54) * mm, "end": v(8454, -1042.16) * mm});
            skLineSegment(sketch, "E8675", {"start": v(8454, -1042.16) * mm, "end": v(8446.64, -1061.97) * mm});
            skLineSegment(sketch, "E8676", {"start": v(8446.64, -1061.97) * mm, "end": v(8440.15, -1080.92) * mm});
            skLineSegment(sketch, "E8677", {"start": v(8440.15, -1080.92) * mm, "end": v(8434.51, -1099) * mm});
            skLineSegment(sketch, "E8678", {"start": v(8434.51, -1099) * mm, "end": v(8429.66, -1116.14) * mm});
            skLineSegment(sketch, "E8679", {"start": v(8429.66, -1116.14) * mm, "end": v(8425.54, -1132.35) * mm});
            skLineSegment(sketch, "E8680", {"start": v(8425.54, -1132.35) * mm, "end": v(8422.1, -1147.58) * mm});
            skLineSegment(sketch, "E8681", {"start": v(8422.1, -1147.58) * mm, "end": v(8419.28, -1161.82) * mm});
            skLineSegment(sketch, "E8682", {"start": v(8419.28, -1161.82) * mm, "end": v(8417.04, -1175.04) * mm});
            skLineSegment(sketch, "E8683", {"start": v(8417.04, -1175.04) * mm, "end": v(8415.3, -1187.22) * mm});
            skLineSegment(sketch, "E8684", {"start": v(8415.3, -1187.22) * mm, "end": v(8414.02, -1198.35) * mm});
            skLineSegment(sketch, "E8685", {"start": v(8414.02, -1198.35) * mm, "end": v(8413.13, -1208.4) * mm});
            skLineSegment(sketch, "E8686", {"start": v(8413.13, -1208.4) * mm, "end": v(8412.58, -1217.38) * mm});
            skLineSegment(sketch, "E8687", {"start": v(8412.58, -1217.38) * mm, "end": v(8412.31, -1225.27) * mm});
            skLineSegment(sketch, "E8688", {"start": v(8412.31, -1225.27) * mm, "end": v(8412.26, -1232.06) * mm});
            skLineSegment(sketch, "E8689", {"start": v(8412.26, -1232.06) * mm, "end": v(8412.37, -1237.74) * mm});
            skLineSegment(sketch, "E8690", {"start": v(8412.37, -1237.74) * mm, "end": v(8412.58, -1242.32) * mm});
            skLineSegment(sketch, "E8691", {"start": v(8412.58, -1242.32) * mm, "end": v(8412.83, -1245.78) * mm});
            skLineSegment(sketch, "E8692", {"start": v(8412.83, -1245.78) * mm, "end": v(8413.07, -1248.14) * mm});
            skLineSegment(sketch, "E8693", {"start": v(8413.07, -1248.14) * mm, "end": v(8413.23, -1249.4) * mm});
            skLineSegment(sketch, "E8694", {"start": v(8413.23, -1249.4) * mm, "end": v(8440.3, -1419.37) * mm});
            skLineSegment(sketch, "E8695", {"start": v(8440.3, -1419.37) * mm, "end": v(8172.27, -1490.75) * mm});
            skLineSegment(sketch, "E8696", {"start": v(8172.27, -1490.75) * mm, "end": v(8111.24, -1329.82) * mm});
            skLineSegment(sketch, "E8697", {"start": v(8111.24, -1329.82) * mm, "end": v(8110.75, -1328.65) * mm});
            skLineSegment(sketch, "E8698", {"start": v(8110.75, -1328.65) * mm, "end": v(8109.78, -1326.48) * mm});
            skLineSegment(sketch, "E8699", {"start": v(8109.78, -1326.48) * mm, "end": v(8108.27, -1323.35) * mm});
            skLineSegment(sketch, "E8700", {"start": v(8108.27, -1323.35) * mm, "end": v(8106.18, -1319.28) * mm});
            skLineSegment(sketch, "E8701", {"start": v(8106.18, -1319.28) * mm, "end": v(8103.45, -1314.3) * mm});
            skLineSegment(sketch, "E8702", {"start": v(8103.45, -1314.3) * mm, "end": v(8100.03, -1308.43) * mm});
            skLineSegment(sketch, "E8703", {"start": v(8100.03, -1308.43) * mm, "end": v(8095.87, -1301.72) * mm});
            skLineSegment(sketch, "E8704", {"start": v(8095.87, -1301.72) * mm, "end": v(8090.93, -1294.2) * mm});
            skLineSegment(sketch, "E8705", {"start": v(8090.93, -1294.2) * mm, "end": v(8085.16, -1285.92) * mm});
            skLineSegment(sketch, "E8706", {"start": v(8085.16, -1285.92) * mm, "end": v(8078.51, -1276.9) * mm});
            skLineSegment(sketch, "E8707", {"start": v(8078.51, -1276.9) * mm, "end": v(8070.95, -1267.2) * mm});
            skLineSegment(sketch, "E8708", {"start": v(8070.95, -1267.2) * mm, "end": v(8062.42, -1256.85) * mm});
            skLineSegment(sketch, "E8709", {"start": v(8062.42, -1256.85) * mm, "end": v(8052.9, -1245.9) * mm});
            skLineSegment(sketch, "E8710", {"start": v(8052.9, -1245.9) * mm, "end": v(8042.34, -1234.4) * mm});
            skLineSegment(sketch, "E8711", {"start": v(8042.34, -1234.4) * mm, "end": v(8030.7, -1222.38) * mm});
            skLineSegment(sketch, "E8712", {"start": v(8030.7, -1222.38) * mm, "end": v(8017.97, -1209.91) * mm});
            skLineSegment(sketch, "E8713", {"start": v(8017.97, -1209.91) * mm, "end": v(8004.09, -1197.04) * mm});
            skLineSegment(sketch, "E8714", {"start": v(8004.09, -1197.04) * mm, "end": v(7989.04, -1183.82) * mm});
            skLineSegment(sketch, "E8715", {"start": v(7989.04, -1183.82) * mm, "end": v(7972.8, -1170.3) * mm});
            skLineSegment(sketch, "E8716", {"start": v(7972.8, -1170.3) * mm, "end": v(7955.32, -1156.55) * mm});
            skLineSegment(sketch, "E8717", {"start": v(7955.32, -1156.55) * mm, "end": v(7936.6, -1142.6) * mm});
            skLineSegment(sketch, "E8718", {"start": v(7936.6, -1142.6) * mm, "end": v(7916.62, -1128.53) * mm});
            skLineSegment(sketch, "E8719", {"start": v(7916.62, -1128.53) * mm, "end": v(7895.34, -1114.38) * mm});
            skLineSegment(sketch, "E8720", {"start": v(7895.34, -1114.38) * mm, "end": v(7872.75, -1100.23) * mm});
            skLineSegment(sketch, "E8721", {"start": v(7872.75, -1100.23) * mm, "end": v(7848.85, -1086.13) * mm});
            skLineSegment(sketch, "E8722", {"start": v(7848.85, -1086.13) * mm, "end": v(7823.6, -1072.14) * mm});
            skLineSegment(sketch, "E8723", {"start": v(7823.6, -1072.14) * mm, "end": v(7797.7, -1059.71) * mm});
            skLineSegment(sketch, "E8724", {"start": v(7797.7, -1059.71) * mm, "end": v(7678.73, -1125) * mm});
            skLineSegment(sketch, "E8725", {"start": v(7678.73, -1125) * mm, "end": v(7675.31, -1153.52) * mm});
            skLineSegment(sketch, "E8726", {"start": v(7675.31, -1153.52) * mm, "end": v(7673.55, -1182.33) * mm});
            skLineSegment(sketch, "E8727", {"start": v(7673.55, -1182.33) * mm, "end": v(7672.6, -1210.07) * mm});
            skLineSegment(sketch, "E8728", {"start": v(7672.6, -1210.07) * mm, "end": v(7672.42, -1236.72) * mm});
            skLineSegment(sketch, "E8729", {"start": v(7672.42, -1236.72) * mm, "end": v(7672.92, -1262.27) * mm});
            skLineSegment(sketch, "E8730", {"start": v(7672.92, -1262.27) * mm, "end": v(7674.05, -1286.69) * mm});
            skLineSegment(sketch, "E8731", {"start": v(7674.05, -1286.69) * mm, "end": v(7675.76, -1309.96) * mm});
            skLineSegment(sketch, "E8732", {"start": v(7675.76, -1309.96) * mm, "end": v(7677.99, -1332.1) * mm});
            skLineSegment(sketch, "E8733", {"start": v(7677.99, -1332.1) * mm, "end": v(7680.66, -1353.06) * mm});
            skLineSegment(sketch, "E8734", {"start": v(7680.66, -1353.06) * mm, "end": v(7683.74, -1372.85) * mm});
            skLineSegment(sketch, "E8735", {"start": v(7683.74, -1372.85) * mm, "end": v(7687.14, -1391.47) * mm});
            skLineSegment(sketch, "E8736", {"start": v(7687.14, -1391.47) * mm, "end": v(7690.81, -1408.91) * mm});
            skLineSegment(sketch, "E8737", {"start": v(7690.81, -1408.91) * mm, "end": v(7694.7, -1425.17) * mm});
            skLineSegment(sketch, "E8738", {"start": v(7694.7, -1425.17) * mm, "end": v(7698.73, -1440.26) * mm});
            skLineSegment(sketch, "E8739", {"start": v(7698.73, -1440.26) * mm, "end": v(7702.85, -1454.18) * mm});
            skLineSegment(sketch, "E8740", {"start": v(7702.85, -1454.18) * mm, "end": v(7707, -1466.93) * mm});
            skLineSegment(sketch, "E8741", {"start": v(7707, -1466.93) * mm, "end": v(7711.13, -1478.52) * mm});
            skLineSegment(sketch, "E8742", {"start": v(7711.13, -1478.52) * mm, "end": v(7715.16, -1488.97) * mm});
            skLineSegment(sketch, "E8743", {"start": v(7715.16, -1488.97) * mm, "end": v(7719.05, -1498.29) * mm});
            skLineSegment(sketch, "E8744", {"start": v(7719.05, -1498.29) * mm, "end": v(7722.74, -1506.5) * mm});
            skLineSegment(sketch, "E8745", {"start": v(7722.74, -1506.5) * mm, "end": v(7726.16, -1513.6) * mm});
            skLineSegment(sketch, "E8746", {"start": v(7726.16, -1513.6) * mm, "end": v(7729.27, -1519.64) * mm});
            skLineSegment(sketch, "E8747", {"start": v(7729.27, -1519.64) * mm, "end": v(7732.01, -1524.62) * mm});
            skLineSegment(sketch, "E8748", {"start": v(7732.01, -1524.62) * mm, "end": v(7734.32, -1528.57) * mm});
            skLineSegment(sketch, "E8749", {"start": v(7734.32, -1528.57) * mm, "end": v(7736.16, -1531.52) * mm});
            skLineSegment(sketch, "E8750", {"start": v(7736.16, -1531.52) * mm, "end": v(7737.47, -1533.5) * mm});
            skLineSegment(sketch, "E8751", {"start": v(7737.47, -1533.5) * mm, "end": v(7738.2, -1534.55) * mm});
            skLineSegment(sketch, "E8752", {"start": v(7738.2, -1534.55) * mm, "end": v(7841.16, -1672.46) * mm});
            skLineSegment(sketch, "E8753", {"start": v(7841.16, -1672.46) * mm, "end": v(7637, -1860.23) * mm});
            skLineSegment(sketch, "E8754", {"start": v(7637, -1860.23) * mm, "end": v(7508.16, -1746.1) * mm});
            skLineSegment(sketch, "E8755", {"start": v(7508.16, -1746.1) * mm, "end": v(7507.18, -1745.29) * mm});
            skLineSegment(sketch, "E8756", {"start": v(7507.18, -1745.29) * mm, "end": v(7505.32, -1743.82) * mm});
            skLineSegment(sketch, "E8757", {"start": v(7505.32, -1743.82) * mm, "end": v(7502.53, -1741.74) * mm});
            skLineSegment(sketch, "E8758", {"start": v(7502.53, -1741.74) * mm, "end": v(7498.78, -1739.1) * mm});
            skLineSegment(sketch, "E8759", {"start": v(7498.78, -1739.1) * mm, "end": v(7494.05, -1735.96) * mm});
            skLineSegment(sketch, "E8760", {"start": v(7494.05, -1735.96) * mm, "end": v(7488.3, -1732.36) * mm});
            skLineSegment(sketch, "E8761", {"start": v(7488.3, -1732.36) * mm, "end": v(7481.5, -1728.35) * mm});
            skLineSegment(sketch, "E8762", {"start": v(7481.5, -1728.35) * mm, "end": v(7473.63, -1724) * mm});
            skLineSegment(sketch, "E8763", {"start": v(7473.63, -1724) * mm, "end": v(7464.67, -1719.34) * mm});
            skLineSegment(sketch, "E8764", {"start": v(7464.67, -1719.34) * mm, "end": v(7454.6, -1714.45) * mm});
            skLineSegment(sketch, "E8765", {"start": v(7454.6, -1714.45) * mm, "end": v(7443.38, -1709.37) * mm});
            skLineSegment(sketch, "E8766", {"start": v(7443.38, -1709.37) * mm, "end": v(7431.03, -1704.16) * mm});
            skLineSegment(sketch, "E8767", {"start": v(7431.03, -1704.16) * mm, "end": v(7417.5, -1698.9) * mm});
            skLineSegment(sketch, "E8768", {"start": v(7417.5, -1698.9) * mm, "end": v(7402.8, -1693.61) * mm});
            skLineSegment(sketch, "E8769", {"start": v(7402.8, -1693.61) * mm, "end": v(7386.92, -1688.38) * mm});
            skLineSegment(sketch, "E8770", {"start": v(7386.92, -1688.38) * mm, "end": v(7369.85, -1683.27) * mm});
            skLineSegment(sketch, "E8771", {"start": v(7369.85, -1683.27) * mm, "end": v(7351.58, -1678.32) * mm});
            skLineSegment(sketch, "E8772", {"start": v(7351.58, -1678.32) * mm, "end": v(7332.11, -1673.6) * mm});
            skLineSegment(sketch, "E8773", {"start": v(7332.11, -1673.6) * mm, "end": v(7311.45, -1669.19) * mm});
            skLineSegment(sketch, "E8774", {"start": v(7311.45, -1669.19) * mm, "end": v(7289.58, -1665.12) * mm});
            skLineSegment(sketch, "E8775", {"start": v(7289.58, -1665.12) * mm, "end": v(7266.53, -1661.47) * mm});
            skLineSegment(sketch, "E8776", {"start": v(7266.53, -1661.47) * mm, "end": v(7242.29, -1658.3) * mm});
            skLineSegment(sketch, "E8777", {"start": v(7242.29, -1658.3) * mm, "end": v(7216.87, -1655.67) * mm});
            skLineSegment(sketch, "E8778", {"start": v(7216.87, -1655.67) * mm, "end": v(7190.3, -1653.63) * mm});
            skLineSegment(sketch, "E8779", {"start": v(7190.3, -1653.63) * mm, "end": v(7162.58, -1652.26) * mm});
            skLineSegment(sketch, "E8780", {"start": v(7162.58, -1652.26) * mm, "end": v(7133.73, -1651.6) * mm});
            skLineSegment(sketch, "E8781", {"start": v(7133.73, -1651.6) * mm, "end": v(7105.02, -1652.63) * mm});
            skLineSegment(sketch, "E8782", {"start": v(7105.02, -1652.63) * mm, "end": v(7030.01, -1765.74) * mm});
            skLineSegment(sketch, "E8783", {"start": v(7030.01, -1765.74) * mm, "end": v(7040.24, -1792.57) * mm});
            skLineSegment(sketch, "E8784", {"start": v(7040.24, -1792.57) * mm, "end": v(7052.07, -1818.9) * mm});
            skLineSegment(sketch, "E8785", {"start": v(7052.07, -1818.9) * mm, "end": v(7064.13, -1843.9) * mm});
            skLineSegment(sketch, "E8786", {"start": v(7064.13, -1843.9) * mm, "end": v(7076.34, -1867.59) * mm});
            skLineSegment(sketch, "E8787", {"start": v(7076.34, -1867.59) * mm, "end": v(7088.66, -1889.97) * mm});
            skLineSegment(sketch, "E8788", {"start": v(7088.66, -1889.97) * mm, "end": v(7101.01, -1911.07) * mm});
            skLineSegment(sketch, "E8789", {"start": v(7101.01, -1911.07) * mm, "end": v(7113.34, -1930.89) * mm});
            skLineSegment(sketch, "E8790", {"start": v(7113.34, -1930.89) * mm, "end": v(7125.6, -1949.45) * mm});
            skLineSegment(sketch, "E8791", {"start": v(7125.6, -1949.45) * mm, "end": v(7137.7, -1966.77) * mm});
            skLineSegment(sketch, "E8792", {"start": v(7137.7, -1966.77) * mm, "end": v(7149.63, -1982.87) * mm});
            skLineSegment(sketch, "E8793", {"start": v(7149.63, -1982.87) * mm, "end": v(7161.29, -1997.77) * mm});
            skLineSegment(sketch, "E8794", {"start": v(7161.29, -1997.77) * mm, "end": v(7172.65, -2011.5) * mm});
            skLineSegment(sketch, "E8795", {"start": v(7172.65, -2011.5) * mm, "end": v(7183.64, -2024.1) * mm});
            skLineSegment(sketch, "E8796", {"start": v(7183.64, -2024.1) * mm, "end": v(7194.23, -2035.59) * mm});
            skLineSegment(sketch, "E8797", {"start": v(7194.23, -2035.59) * mm, "end": v(7204.34, -2046) * mm});
            skLineSegment(sketch, "E8798", {"start": v(7204.34, -2046) * mm, "end": v(7213.95, -2055.35) * mm});
            skLineSegment(sketch, "E8799", {"start": v(7213.95, -2055.35) * mm, "end": v(7222.99, -2063.7) * mm});
            skLineSegment(sketch, "E8800", {"start": v(7222.99, -2063.7) * mm, "end": v(7231.42, -2071.08) * mm});
            skLineSegment(sketch, "E8801", {"start": v(7231.42, -2071.08) * mm, "end": v(7239.2, -2077.52) * mm});
            skLineSegment(sketch, "E8802", {"start": v(7239.2, -2077.52) * mm, "end": v(7246.27, -2083.07) * mm});
            skLineSegment(sketch, "E8803", {"start": v(7246.27, -2083.07) * mm, "end": v(7252.6, -2087.78) * mm});
            skLineSegment(sketch, "E8804", {"start": v(7252.6, -2087.78) * mm, "end": v(7258.16, -2091.67) * mm});
            skLineSegment(sketch, "E8805", {"start": v(7258.16, -2091.67) * mm, "end": v(7262.9, -2094.81) * mm});
            skLineSegment(sketch, "E8806", {"start": v(7262.9, -2094.81) * mm, "end": v(7266.78, -2097.24) * mm});
            skLineSegment(sketch, "E8807", {"start": v(7266.78, -2097.24) * mm, "end": v(7269.78, -2099) * mm});
            skLineSegment(sketch, "E8808", {"start": v(7269.78, -2099) * mm, "end": v(7271.86, -2100.15) * mm});
            skLineSegment(sketch, "E8809", {"start": v(7271.86, -2100.15) * mm, "end": v(7272.98, -2100.73) * mm});
            skLineSegment(sketch, "E8810", {"start": v(7272.98, -2100.73) * mm, "end": v(7428.25, -2175) * mm});
            skLineSegment(sketch, "E8811", {"start": v(7428.25, -2175) * mm, "end": v(7334.73, -2436.14) * mm});
            skLineSegment(sketch, "E8812", {"start": v(7334.73, -2436.14) * mm, "end": v(7167.62, -2394.95) * mm});
            skLineSegment(sketch, "E8813", {"start": v(7167.62, -2394.95) * mm, "end": v(7166.38, -2394.69) * mm});
            skLineSegment(sketch, "E8814", {"start": v(7166.38, -2394.69) * mm, "end": v(7164.04, -2394.26) * mm});
            skLineSegment(sketch, "E8815", {"start": v(7164.04, -2394.26) * mm, "end": v(7160.6, -2393.71) * mm});
            skLineSegment(sketch, "E8816", {"start": v(7160.6, -2393.71) * mm, "end": v(7156.07, -2393.12) * mm});
            skLineSegment(sketch, "E8817", {"start": v(7156.07, -2393.12) * mm, "end": v(7150.41, -2392.54) * mm});
            skLineSegment(sketch, "E8818", {"start": v(7150.41, -2392.54) * mm, "end": v(7143.65, -2392.02) * mm});
            skLineSegment(sketch, "E8819", {"start": v(7143.65, -2392.02) * mm, "end": v(7135.76, -2391.63) * mm});
            skLineSegment(sketch, "E8820", {"start": v(7135.76, -2391.63) * mm, "end": v(7126.77, -2391.43) * mm});
            skLineSegment(sketch, "E8821", {"start": v(7126.77, -2391.43) * mm, "end": v(7116.67, -2391.47) * mm});
            skLineSegment(sketch, "E8822", {"start": v(7116.67, -2391.47) * mm, "end": v(7105.48, -2391.82) * mm});
            skLineSegment(sketch, "E8823", {"start": v(7105.48, -2391.82) * mm, "end": v(7093.2, -2392.53) * mm});
            skLineSegment(sketch, "E8824", {"start": v(7093.2, -2392.53) * mm, "end": v(7079.83, -2393.67) * mm});
            skLineSegment(sketch, "E8825", {"start": v(7079.83, -2393.67) * mm, "end": v(7065.4, -2395.28) * mm});
            skLineSegment(sketch, "E8826", {"start": v(7065.4, -2395.28) * mm, "end": v(7049.94, -2397.44) * mm});
            skLineSegment(sketch, "E8827", {"start": v(7049.94, -2397.44) * mm, "end": v(7033.45, -2400.2) * mm});
            skLineSegment(sketch, "E8828", {"start": v(7033.45, -2400.2) * mm, "end": v(7015.95, -2403.6) * mm});
            skLineSegment(sketch, "E8829", {"start": v(7015.95, -2403.6) * mm, "end": v(6997.48, -2407.7) * mm});
            skLineSegment(sketch, "E8830", {"start": v(6997.48, -2407.7) * mm, "end": v(6978.05, -2412.58) * mm});
            skLineSegment(sketch, "E8831", {"start": v(6978.05, -2412.58) * mm, "end": v(6957.7, -2418.27) * mm});
            skLineSegment(sketch, "E8832", {"start": v(6957.7, -2418.27) * mm, "end": v(6936.45, -2424.83) * mm});
            skLineSegment(sketch, "E8833", {"start": v(6936.45, -2424.83) * mm, "end": v(6914.34, -2432.32) * mm});
            skLineSegment(sketch, "E8834", {"start": v(6914.34, -2432.32) * mm, "end": v(6891.4, -2440.77) * mm});
            skLineSegment(sketch, "E8835", {"start": v(6891.4, -2440.77) * mm, "end": v(6867.67, -2450.25) * mm});
            skLineSegment(sketch, "E8836", {"start": v(6867.67, -2450.25) * mm, "end": v(6843.2, -2460.8) * mm});
            skLineSegment(sketch, "E8837", {"start": v(6843.2, -2460.8) * mm, "end": v(6818, -2472.46) * mm});
            skLineSegment(sketch, "E8838", {"start": v(6818, -2472.46) * mm, "end": v(6792.16, -2485.29) * mm});
            skLineSegment(sketch, "E8839", {"start": v(6792.16, -2485.29) * mm, "end": v(6767.22, -2499.54) * mm});
            skLineSegment(sketch, "E8840", {"start": v(6767.22, -2499.54) * mm, "end": v(6753.37, -2634.55) * mm});
            skLineSegment(sketch, "E8841", {"start": v(6753.37, -2634.55) * mm, "end": v(6774.9, -2653.56) * mm});
            skLineSegment(sketch, "E8842", {"start": v(6774.9, -2653.56) * mm, "end": v(6797.6, -2671.37) * mm});
            skLineSegment(sketch, "E8843", {"start": v(6797.6, -2671.37) * mm, "end": v(6819.9, -2687.9) * mm});
            skLineSegment(sketch, "E8844", {"start": v(6819.9, -2687.9) * mm, "end": v(6841.72, -2703.2) * mm});
            skLineSegment(sketch, "E8845", {"start": v(6841.72, -2703.2) * mm, "end": v(6863.03, -2717.3) * mm});
            skLineSegment(sketch, "E8846", {"start": v(6863.03, -2717.3) * mm, "end": v(6883.77, -2730.24) * mm});
            skLineSegment(sketch, "E8847", {"start": v(6883.77, -2730.24) * mm, "end": v(6903.9, -2742.06) * mm});
            skLineSegment(sketch, "E8848", {"start": v(6903.9, -2742.06) * mm, "end": v(6923.37, -2752.8) * mm});
            skLineSegment(sketch, "E8849", {"start": v(6923.37, -2752.8) * mm, "end": v(6942.15, -2762.5) * mm});
            skLineSegment(sketch, "E8850", {"start": v(6942.15, -2762.5) * mm, "end": v(6960.18, -2771.22) * mm});
            skLineSegment(sketch, "E8851", {"start": v(6960.18, -2771.22) * mm, "end": v(6977.44, -2779) * mm});
            skLineSegment(sketch, "E8852", {"start": v(6977.44, -2779) * mm, "end": v(6993.88, -2785.88) * mm});
            skLineSegment(sketch, "E8853", {"start": v(6993.88, -2785.88) * mm, "end": v(7009.47, -2791.92) * mm});
            skLineSegment(sketch, "E8854", {"start": v(7009.47, -2791.92) * mm, "end": v(7024.18, -2797.18) * mm});
            skLineSegment(sketch, "E8855", {"start": v(7024.18, -2797.18) * mm, "end": v(7037.97, -2801.69) * mm});
            skLineSegment(sketch, "E8856", {"start": v(7037.97, -2801.69) * mm, "end": v(7050.82, -2805.51) * mm});
            skLineSegment(sketch, "E8857", {"start": v(7050.82, -2805.51) * mm, "end": v(7062.7, -2808.7) * mm});
            skLineSegment(sketch, "E8858", {"start": v(7062.7, -2808.7) * mm, "end": v(7073.6, -2811.32) * mm});
            skLineSegment(sketch, "E8859", {"start": v(7073.6, -2811.32) * mm, "end": v(7083.48, -2813.41) * mm});
            skLineSegment(sketch, "E8860", {"start": v(7083.48, -2813.41) * mm, "end": v(7092.32, -2815.04) * mm});
            skLineSegment(sketch, "E8861", {"start": v(7092.32, -2815.04) * mm, "end": v(7100.12, -2816.26) * mm});
            skLineSegment(sketch, "E8862", {"start": v(7100.12, -2816.26) * mm, "end": v(7106.85, -2817.13) * mm});
            skLineSegment(sketch, "E8863", {"start": v(7106.85, -2817.13) * mm, "end": v(7112.5, -2817.7) * mm});
            skLineSegment(sketch, "E8864", {"start": v(7112.5, -2817.7) * mm, "end": v(7117.07, -2818.04) * mm});
            skLineSegment(sketch, "E8865", {"start": v(7117.07, -2818.04) * mm, "end": v(7120.55, -2818.21) * mm});
            skLineSegment(sketch, "E8866", {"start": v(7120.55, -2818.21) * mm, "end": v(7122.92, -2818.26) * mm});
            skLineSegment(sketch, "E8867", {"start": v(7122.92, -2818.26) * mm, "end": v(7124.19, -2818.26) * mm});
            skLineSegment(sketch, "E8868", {"start": v(7124.19, -2818.26) * mm, "end": v(7296.18, -2811.86) * mm});
            skLineSegment(sketch, "E8869", {"start": v(7296.18, -2811.86) * mm, "end": v(7334.73, -3086.55) * mm});
            skLineSegment(sketch, "E8870", {"start": v(7334.73, -3086.55) * mm, "end": v(7167.62, -3127.74) * mm});
            skLineSegment(sketch, "E8871", {"start": v(7167.62, -3127.74) * mm, "end": v(7166.4, -3128.08) * mm});
            skLineSegment(sketch, "E8872", {"start": v(7166.4, -3128.08) * mm, "end": v(7164.13, -3128.79) * mm});
            skLineSegment(sketch, "E8873", {"start": v(7164.13, -3128.79) * mm, "end": v(7160.84, -3129.9) * mm});
            skLineSegment(sketch, "E8874", {"start": v(7160.84, -3129.9) * mm, "end": v(7156.54, -3131.49) * mm});
            skLineSegment(sketch, "E8875", {"start": v(7156.54, -3131.49) * mm, "end": v(7151.26, -3133.6) * mm});
            skLineSegment(sketch, "E8876", {"start": v(7151.26, -3133.6) * mm, "end": v(7145.03, -3136.29) * mm});
            skLineSegment(sketch, "E8877", {"start": v(7145.03, -3136.29) * mm, "end": v(7137.87, -3139.6) * mm});
            skLineSegment(sketch, "E8878", {"start": v(7137.87, -3139.6) * mm, "end": v(7129.82, -3143.6) * mm});
            skLineSegment(sketch, "E8879", {"start": v(7129.82, -3143.6) * mm, "end": v(7120.9, -3148.34) * mm});
            skLineSegment(sketch, "E8880", {"start": v(7120.9, -3148.34) * mm, "end": v(7111.14, -3153.85) * mm});
            skLineSegment(sketch, "E8881", {"start": v(7111.14, -3153.85) * mm, "end": v(7100.6, -3160.19) * mm});
            skLineSegment(sketch, "E8882", {"start": v(7100.6, -3160.19) * mm, "end": v(7089.3, -3167.4) * mm});
            skLineSegment(sketch, "E8883", {"start": v(7089.3, -3167.4) * mm, "end": v(7077.27, -3175.54) * mm});
            skLineSegment(sketch, "E8884", {"start": v(7077.27, -3175.54) * mm, "end": v(7064.58, -3184.63) * mm});
            skLineSegment(sketch, "E8885", {"start": v(7064.58, -3184.63) * mm, "end": v(7051.25, -3194.73) * mm});
            skLineSegment(sketch, "E8886", {"start": v(7051.25, -3194.73) * mm, "end": v(7037.34, -3205.88) * mm});
            skLineSegment(sketch, "E8887", {"start": v(7037.34, -3205.88) * mm, "end": v(7022.9, -3218.1) * mm});
            skLineSegment(sketch, "E8888", {"start": v(7022.9, -3218.1) * mm, "end": v(7007.96, -3231.45) * mm});
            skLineSegment(sketch, "E8889", {"start": v(7007.96, -3231.45) * mm, "end": v(6992.58, -3245.95) * mm});
            skLineSegment(sketch, "E8890", {"start": v(6992.58, -3245.95) * mm, "end": v(6976.81, -3261.63) * mm});
            skLineSegment(sketch, "E8891", {"start": v(6976.81, -3261.63) * mm, "end": v(6960.71, -3278.53) * mm});
            skLineSegment(sketch, "E8892", {"start": v(6960.71, -3278.53) * mm, "end": v(6944.33, -3296.68) * mm});
            skLineSegment(sketch, "E8893", {"start": v(6944.33, -3296.68) * mm, "end": v(6927.73, -3316.1) * mm});
            skLineSegment(sketch, "E8894", {"start": v(6927.73, -3316.1) * mm, "end": v(6910.96, -3336.81) * mm});
            skLineSegment(sketch, "E8895", {"start": v(6910.96, -3336.81) * mm, "end": v(6894.08, -3358.85) * mm});
            skLineSegment(sketch, "E8896", {"start": v(6894.08, -3358.85) * mm, "end": v(6877.15, -3382.22) * mm});
            skLineSegment(sketch, "E8897", {"start": v(6877.15, -3382.22) * mm, "end": v(6861.69, -3406.42) * mm});
            skLineSegment(sketch, "E8898", {"start": v(6861.69, -3406.42) * mm, "end": v(6912.16, -3532.4) * mm});
            skLineSegment(sketch, "E8899", {"start": v(6912.16, -3532.4) * mm, "end": v(6940.06, -3539.24) * mm});
            skLineSegment(sketch, "E8900", {"start": v(6940.06, -3539.24) * mm, "end": v(6968.44, -3544.45) * mm});
            skLineSegment(sketch, "E8901", {"start": v(6968.44, -3544.45) * mm, "end": v(6995.87, -3548.73) * mm});
            skLineSegment(sketch, "E8902", {"start": v(6995.87, -3548.73) * mm, "end": v(7022.3, -3552.14) * mm});
            skLineSegment(sketch, "E8903", {"start": v(7022.3, -3552.14) * mm, "end": v(7047.72, -3554.72) * mm});
            skLineSegment(sketch, "E8904", {"start": v(7047.72, -3554.72) * mm, "end": v(7072.1, -3556.54) * mm});
            skLineSegment(sketch, "E8905", {"start": v(7072.1, -3556.54) * mm, "end": v(7095.42, -3557.65) * mm});
            skLineSegment(sketch, "E8906", {"start": v(7095.42, -3557.65) * mm, "end": v(7117.65, -3558.1) * mm});
            skLineSegment(sketch, "E8907", {"start": v(7117.65, -3558.1) * mm, "end": v(7138.79, -3557.97) * mm});
            skLineSegment(sketch, "E8908", {"start": v(7138.79, -3557.97) * mm, "end": v(7158.8, -3557.31) * mm});
            skLineSegment(sketch, "E8909", {"start": v(7158.8, -3557.31) * mm, "end": v(7177.7, -3556.18) * mm});
            skLineSegment(sketch, "E8910", {"start": v(7177.7, -3556.18) * mm, "end": v(7195.46, -3554.64) * mm});
            skLineSegment(sketch, "E8911", {"start": v(7195.46, -3554.64) * mm, "end": v(7212.07, -3552.74) * mm});
            skLineSegment(sketch, "E8912", {"start": v(7212.07, -3552.74) * mm, "end": v(7227.53, -3550.56) * mm});
            skLineSegment(sketch, "E8913", {"start": v(7227.53, -3550.56) * mm, "end": v(7241.84, -3548.14) * mm});
            skLineSegment(sketch, "E8914", {"start": v(7241.84, -3548.14) * mm, "end": v(7255, -3545.55) * mm});
            skLineSegment(sketch, "E8915", {"start": v(7255, -3545.55) * mm, "end": v(7267, -3542.86) * mm});
            skLineSegment(sketch, "E8916", {"start": v(7267, -3542.86) * mm, "end": v(7277.87, -3540.1) * mm});
            skLineSegment(sketch, "E8917", {"start": v(7277.87, -3540.1) * mm, "end": v(7287.58, -3537.37) * mm});
            skLineSegment(sketch, "E8918", {"start": v(7287.58, -3537.37) * mm, "end": v(7296.17, -3534.7) * mm});
            skLineSegment(sketch, "E8919", {"start": v(7296.17, -3534.7) * mm, "end": v(7303.64, -3532.16) * mm});
            skLineSegment(sketch, "E8920", {"start": v(7303.64, -3532.16) * mm, "end": v(7310, -3529.8) * mm});
            skLineSegment(sketch, "E8921", {"start": v(7310, -3529.8) * mm, "end": v(7315.28, -3527.68) * mm});
            skLineSegment(sketch, "E8922", {"start": v(7315.28, -3527.68) * mm, "end": v(7319.49, -3525.86) * mm});
            skLineSegment(sketch, "E8923", {"start": v(7319.49, -3525.86) * mm, "end": v(7322.64, -3524.4) * mm});
            skLineSegment(sketch, "E8924", {"start": v(7322.64, -3524.4) * mm, "end": v(7324.76, -3523.34) * mm});
            skLineSegment(sketch, "E8925", {"start": v(7324.76, -3523.34) * mm, "end": v(7325.88, -3522.74) * mm});
            skLineSegment(sketch, "E8926", {"start": v(7325.88, -3522.74) * mm, "end": v(7475.2, -3437.15) * mm});
            skLineSegment(sketch, "E8927", {"start": v(7475.2, -3437.15) * mm, "end": v(7637, -3662.46) * mm});
            skLineSegment(sketch, "E8928", {"start": v(7637, -3662.46) * mm, "end": v(7508.16, -3776.6) * mm});
            skLineSegment(sketch, "E8929", {"start": v(7508.16, -3776.6) * mm, "end": v(7507.24, -3777.47) * mm});
            skLineSegment(sketch, "E8930", {"start": v(7507.24, -3777.47) * mm, "end": v(7505.56, -3779.14) * mm});
            skLineSegment(sketch, "E8931", {"start": v(7505.56, -3779.14) * mm, "end": v(7503.17, -3781.66) * mm});
            skLineSegment(sketch, "E8932", {"start": v(7503.17, -3781.66) * mm, "end": v(7500.1, -3785.06) * mm});
            skLineSegment(sketch, "E8933", {"start": v(7500.1, -3785.06) * mm, "end": v(7496.4, -3789.38) * mm});
            skLineSegment(sketch, "E8934", {"start": v(7496.4, -3789.38) * mm, "end": v(7492.14, -3794.66) * mm});
            skLineSegment(sketch, "E8935", {"start": v(7492.14, -3794.66) * mm, "end": v(7487.34, -3800.92) * mm});
            skLineSegment(sketch, "E8936", {"start": v(7487.34, -3800.92) * mm, "end": v(7482.06, -3808.2) * mm});
            skLineSegment(sketch, "E8937", {"start": v(7482.06, -3808.2) * mm, "end": v(7476.36, -3816.54) * mm});
            skLineSegment(sketch, "E8938", {"start": v(7476.36, -3816.54) * mm, "end": v(7470.29, -3825.96) * mm});
            skLineSegment(sketch, "E8939", {"start": v(7470.29, -3825.96) * mm, "end": v(7463.9, -3836.47) * mm});
            skLineSegment(sketch, "E8940", {"start": v(7463.9, -3836.47) * mm, "end": v(7457.24, -3848.11) * mm});
            skLineSegment(sketch, "E8941", {"start": v(7457.24, -3848.11) * mm, "end": v(7450.38, -3860.9) * mm});
            skLineSegment(sketch, "E8942", {"start": v(7450.38, -3860.9) * mm, "end": v(7443.37, -3874.85) * mm});
            skLineSegment(sketch, "E8943", {"start": v(7443.37, -3874.85) * mm, "end": v(7436.26, -3890) * mm});
            skLineSegment(sketch, "E8944", {"start": v(7436.26, -3890) * mm, "end": v(7429.12, -3906.32) * mm});
            skLineSegment(sketch, "E8945", {"start": v(7429.12, -3906.32) * mm, "end": v(7422.01, -3923.86) * mm});
            skLineSegment(sketch, "E8946", {"start": v(7422.01, -3923.86) * mm, "end": v(7414.99, -3942.62) * mm});
            skLineSegment(sketch, "E8947", {"start": v(7414.99, -3942.62) * mm, "end": v(7408.1, -3962.6) * mm});
            skLineSegment(sketch, "E8948", {"start": v(7408.1, -3962.6) * mm, "end": v(7401.44, -3983.82) * mm});
            skLineSegment(sketch, "E8949", {"start": v(7401.44, -3983.82) * mm, "end": v(7395.04, -4006.27) * mm});
            skLineSegment(sketch, "E8950", {"start": v(7395.04, -4006.27) * mm, "end": v(7388.96, -4029.95) * mm});
            skLineSegment(sketch, "E8951", {"start": v(7388.96, -4029.95) * mm, "end": v(7383.29, -4054.86) * mm});
            skLineSegment(sketch, "E8952", {"start": v(7383.29, -4054.86) * mm, "end": v(7378.06, -4081) * mm});
            skLineSegment(sketch, "E8953", {"start": v(7378.06, -4081) * mm, "end": v(7373.36, -4108.35) * mm});
            skLineSegment(sketch, "E8954", {"start": v(7373.36, -4108.35) * mm, "end": v(7369.23, -4136.91) * mm});
            skLineSegment(sketch, "E8955", {"start": v(7369.23, -4136.91) * mm, "end": v(7366.79, -4165.53) * mm});
            skLineSegment(sketch, "E8956", {"start": v(7366.79, -4165.53) * mm, "end": v(7470.03, -4253.62) * mm});
            skLineSegment(sketch, "E8957", {"start": v(7470.03, -4253.62) * mm, "end": v(7497.9, -4246.7) * mm});
            skLineSegment(sketch, "E8958", {"start": v(7497.9, -4246.7) * mm, "end": v(7525.46, -4238.14) * mm});
            skLineSegment(sketch, "E8959", {"start": v(7525.46, -4238.14) * mm, "end": v(7551.73, -4229.18) * mm});
            skLineSegment(sketch, "E8960", {"start": v(7551.73, -4229.18) * mm, "end": v(7576.72, -4219.91) * mm});
            skLineSegment(sketch, "E8961", {"start": v(7576.72, -4219.91) * mm, "end": v(7600.43, -4210.38) * mm});
            skLineSegment(sketch, "E8962", {"start": v(7600.43, -4210.38) * mm, "end": v(7622.86, -4200.66) * mm});
            skLineSegment(sketch, "E8963", {"start": v(7622.86, -4200.66) * mm, "end": v(7644.02, -4190.8) * mm});
            skLineSegment(sketch, "E8964", {"start": v(7644.02, -4190.8) * mm, "end": v(7663.92, -4180.88) * mm});
            skLineSegment(sketch, "E8965", {"start": v(7663.92, -4180.88) * mm, "end": v(7682.57, -4170.95) * mm});
            skLineSegment(sketch, "E8966", {"start": v(7682.57, -4170.95) * mm, "end": v(7700, -4161.06) * mm});
            skLineSegment(sketch, "E8967", {"start": v(7700, -4161.06) * mm, "end": v(7716.2, -4151.27) * mm});
            skLineSegment(sketch, "E8968", {"start": v(7716.2, -4151.27) * mm, "end": v(7731.2, -4141.65) * mm});
            skLineSegment(sketch, "E8969", {"start": v(7731.2, -4141.65) * mm, "end": v(7745.03, -4132.26) * mm});
            skLineSegment(sketch, "E8970", {"start": v(7745.03, -4132.26) * mm, "end": v(7757.7, -4123.13) * mm});
            skLineSegment(sketch, "E8971", {"start": v(7757.7, -4123.13) * mm, "end": v(7769.25, -4114.35) * mm});
            skLineSegment(sketch, "E8972", {"start": v(7769.25, -4114.35) * mm, "end": v(7779.7, -4105.94) * mm});
            skLineSegment(sketch, "E8973", {"start": v(7779.7, -4105.94) * mm, "end": v(7789.08, -4097.97) * mm});
            skLineSegment(sketch, "E8974", {"start": v(7789.08, -4097.97) * mm, "end": v(7797.42, -4090.5) * mm});
            skLineSegment(sketch, "E8975", {"start": v(7797.42, -4090.5) * mm, "end": v(7804.75, -4083.55) * mm});
            skLineSegment(sketch, "E8976", {"start": v(7804.75, -4083.55) * mm, "end": v(7811.12, -4077.2) * mm});
            skLineSegment(sketch, "E8977", {"start": v(7811.12, -4077.2) * mm, "end": v(7816.55, -4071.47) * mm});
            skLineSegment(sketch, "E8978", {"start": v(7816.55, -4071.47) * mm, "end": v(7821.1, -4066.43) * mm});
            skLineSegment(sketch, "E8979", {"start": v(7821.1, -4066.43) * mm, "end": v(7824.78, -4062.1) * mm});
            skLineSegment(sketch, "E8980", {"start": v(7824.78, -4062.1) * mm, "end": v(7827.65, -4058.54) * mm});
            skLineSegment(sketch, "E8981", {"start": v(7827.65, -4058.54) * mm, "end": v(7829.76, -4055.77) * mm});
            skLineSegment(sketch, "E8982", {"start": v(7829.76, -4055.77) * mm, "end": v(7831.15, -4053.85) * mm});
            skLineSegment(sketch, "E8983", {"start": v(7831.15, -4053.85) * mm, "end": v(7831.87, -4052.8) * mm});
            skLineSegment(sketch, "E8984", {"start": v(7831.87, -4052.8) * mm, "end": v(7924.3, -3907.62) * mm});
            skLineSegment(sketch, "E8985", {"start": v(7924.3, -3907.62) * mm, "end": v(8172.27, -4031.94) * mm});
            skLineSegment(sketch, "E8986", {"start": v(8172.27, -4031.94) * mm, "end": v(8111.24, -4192.87) * mm});
            skLineSegment(sketch, "E8987", {"start": v(8111.24, -4192.87) * mm, "end": v(8110.83, -4194.07) * mm});
            skLineSegment(sketch, "E8988", {"start": v(8110.83, -4194.07) * mm, "end": v(8110.12, -4196.33) * mm});
            skLineSegment(sketch, "E8989", {"start": v(8110.12, -4196.33) * mm, "end": v(8109.17, -4199.68) * mm});
            skLineSegment(sketch, "E8990", {"start": v(8109.17, -4199.68) * mm, "end": v(8108.03, -4204.11) * mm});
            skLineSegment(sketch, "E8991", {"start": v(8108.03, -4204.11) * mm, "end": v(8106.77, -4209.65) * mm});
            skLineSegment(sketch, "E8992", {"start": v(8106.77, -4209.65) * mm, "end": v(8105.44, -4216.3) * mm});
            skLineSegment(sketch, "E8993", {"start": v(8105.44, -4216.3) * mm, "end": v(8104.1, -4224.09) * mm});
            skLineSegment(sketch, "E8994", {"start": v(8104.1, -4224.09) * mm, "end": v(8102.82, -4233) * mm});
            skLineSegment(sketch, "E8995", {"start": v(8102.82, -4233) * mm, "end": v(8101.65, -4243.02) * mm});
            skLineSegment(sketch, "E8996", {"start": v(8101.65, -4243.02) * mm, "end": v(8100.64, -4254.18) * mm});
            skLineSegment(sketch, "E8997", {"start": v(8100.64, -4254.18) * mm, "end": v(8099.87, -4266.46) * mm});
            skLineSegment(sketch, "E8998", {"start": v(8099.87, -4266.46) * mm, "end": v(8099.39, -4279.86) * mm});
            skLineSegment(sketch, "E8999", {"start": v(8099.39, -4279.86) * mm, "end": v(8099.25, -4294.37) * mm});
            skLineSegment(sketch, "E9000", {"start": v(8099.25, -4294.37) * mm, "end": v(8099.53, -4309.98) * mm});
            skLineSegment(sketch, "E9001", {"start": v(8099.53, -4309.98) * mm, "end": v(8100.27, -4326.69) * mm});
            skLineSegment(sketch, "E9002", {"start": v(8100.27, -4326.69) * mm, "end": v(8101.54, -4344.47) * mm});
            skLineSegment(sketch, "E9003", {"start": v(8101.54, -4344.47) * mm, "end": v(8103.4, -4363.3) * mm});
            skLineSegment(sketch, "E9004", {"start": v(8103.4, -4363.3) * mm, "end": v(8105.9, -4383.18) * mm});
            skLineSegment(sketch, "E9005", {"start": v(8105.9, -4383.18) * mm, "end": v(8109.09, -4404.07) * mm});
            skLineSegment(sketch, "E9006", {"start": v(8109.09, -4404.07) * mm, "end": v(8113.04, -4425.95) * mm});
            skLineSegment(sketch, "E9007", {"start": v(8113.04, -4425.95) * mm, "end": v(8117.8, -4448.8) * mm});
            skLineSegment(sketch, "E9008", {"start": v(8117.8, -4448.8) * mm, "end": v(8123.43, -4472.6) * mm});
            skLineSegment(sketch, "E9009", {"start": v(8123.43, -4472.6) * mm, "end": v(8129.98, -4497.29) * mm});
            skLineSegment(sketch, "E9010", {"start": v(8129.98, -4497.29) * mm, "end": v(8137.5, -4522.86) * mm});
            skLineSegment(sketch, "E9011", {"start": v(8137.5, -4522.86) * mm, "end": v(8146.05, -4549.27) * mm});
            skLineSegment(sketch, "E9012", {"start": v(8146.05, -4549.27) * mm, "end": v(8155.66, -4576.48) * mm});
            skLineSegment(sketch, "E9013", {"start": v(8155.66, -4576.48) * mm, "end": v(8166.8, -4602.95) * mm});
            skLineSegment(sketch, "E9014", {"start": v(8166.8, -4602.95) * mm, "end": v(8299.16, -4632.98) * mm});
            skLineSegment(sketch, "E9015", {"start": v(8299.16, -4632.98) * mm, "end": v(8320.63, -4613.9) * mm});
            skLineSegment(sketch, "E9016", {"start": v(8320.63, -4613.9) * mm, "end": v(8341.04, -4593.5) * mm});
            skLineSegment(sketch, "E9017", {"start": v(8341.04, -4593.5) * mm, "end": v(8360.15, -4573.36) * mm});
            skLineSegment(sketch, "E9018", {"start": v(8360.15, -4573.36) * mm, "end": v(8377.97, -4553.54) * mm});
            skLineSegment(sketch, "E9019", {"start": v(8377.97, -4553.54) * mm, "end": v(8394.53, -4534.1) * mm});
            skLineSegment(sketch, "E9020", {"start": v(8394.53, -4534.1) * mm, "end": v(8409.87, -4515.06) * mm});
            skLineSegment(sketch, "E9021", {"start": v(8409.87, -4515.06) * mm, "end": v(8424.03, -4496.5) * mm});
            skLineSegment(sketch, "E9022", {"start": v(8424.03, -4496.5) * mm, "end": v(8437.04, -4478.46) * mm});
            skLineSegment(sketch, "E9023", {"start": v(8437.04, -4478.46) * mm, "end": v(8448.94, -4461) * mm});
            skLineSegment(sketch, "E9024", {"start": v(8448.94, -4461) * mm, "end": v(8459.76, -4444.14) * mm});
            skLineSegment(sketch, "E9025", {"start": v(8459.76, -4444.14) * mm, "end": v(8469.56, -4427.95) * mm});
            skLineSegment(sketch, "E9026", {"start": v(8469.56, -4427.95) * mm, "end": v(8478.38, -4412.46) * mm});
            skLineSegment(sketch, "E9027", {"start": v(8478.38, -4412.46) * mm, "end": v(8486.26, -4397.71) * mm});
            skLineSegment(sketch, "E9028", {"start": v(8486.26, -4397.71) * mm, "end": v(8493.24, -4383.74) * mm});
            skLineSegment(sketch, "E9029", {"start": v(8493.24, -4383.74) * mm, "end": v(8499.38, -4370.6) * mm});
            skLineSegment(sketch, "E9030", {"start": v(8499.38, -4370.6) * mm, "end": v(8504.73, -4358.3) * mm});
            skLineSegment(sketch, "E9031", {"start": v(8504.73, -4358.3) * mm, "end": v(8509.33, -4346.89) * mm});
            skLineSegment(sketch, "E9032", {"start": v(8509.33, -4346.89) * mm, "end": v(8513.24, -4336.39) * mm});
            skLineSegment(sketch, "E9033", {"start": v(8513.24, -4336.39) * mm, "end": v(8516.5, -4326.83) * mm});
            skLineSegment(sketch, "E9034", {"start": v(8516.5, -4326.83) * mm, "end": v(8519.19, -4318.25) * mm});
            skLineSegment(sketch, "E9035", {"start": v(8519.19, -4318.25) * mm, "end": v(8521.34, -4310.65) * mm});
            skLineSegment(sketch, "E9036", {"start": v(8521.34, -4310.65) * mm, "end": v(8523.01, -4304.08) * mm});
            skLineSegment(sketch, "E9037", {"start": v(8523.01, -4304.08) * mm, "end": v(8524.27, -4298.53) * mm});
            skLineSegment(sketch, "E9038", {"start": v(8524.27, -4298.53) * mm, "end": v(8525.16, -4294.04) * mm});
            skLineSegment(sketch, "E9039", {"start": v(8525.16, -4294.04) * mm, "end": v(8525.74, -4290.61) * mm});
            skLineSegment(sketch, "E9040", {"start": v(8525.74, -4290.61) * mm, "end": v(8526.08, -4288.26) * mm});
            skLineSegment(sketch, "E9041", {"start": v(8526.08, -4288.26) * mm, "end": v(8526.23, -4287) * mm});
            skLineSegment(sketch, "E9042", {"start": v(8526.23, -4287) * mm, "end": v(8540.6, -4115.5) * mm});
            skLineSegment(sketch, "E9043", {"start": v(8540.6, -4115.5) * mm, "end": v(8817.94, -4110.33) * mm});
            skLineSegment(sketch, "E9044", {"start": v(8817.94, -4110.33) * mm, "end": v(8838.69, -4281.2) * mm});
            skLineSegment(sketch, "E9045", {"start": v(8838.69, -4281.2) * mm, "end": v(8838.88, -4282.45) * mm});
            skLineSegment(sketch, "E9046", {"start": v(8838.88, -4282.45) * mm, "end": v(8839.3, -4284.78) * mm});
            skLineSegment(sketch, "E9047", {"start": v(8839.3, -4284.78) * mm, "end": v(8840.02, -4288.19) * mm});
            skLineSegment(sketch, "E9048", {"start": v(8840.02, -4288.19) * mm, "end": v(8841.07, -4292.64) * mm});
            skLineSegment(sketch, "E9049", {"start": v(8841.07, -4292.64) * mm, "end": v(8842.53, -4298.13) * mm});
            skLineSegment(sketch, "E9050", {"start": v(8842.53, -4298.13) * mm, "end": v(8844.45, -4304.65) * mm});
            skLineSegment(sketch, "E9051", {"start": v(8844.45, -4304.65) * mm, "end": v(8846.88, -4312.15) * mm});
            skLineSegment(sketch, "E9052", {"start": v(8846.88, -4312.15) * mm, "end": v(8849.88, -4320.63) * mm});
            skLineSegment(sketch, "E9053", {"start": v(8849.88, -4320.63) * mm, "end": v(8853.5, -4330.06) * mm});
            skLineSegment(sketch, "E9054", {"start": v(8853.5, -4330.06) * mm, "end": v(8857.8, -4340.4) * mm});
            skLineSegment(sketch, "E9055", {"start": v(8857.8, -4340.4) * mm, "end": v(8862.82, -4351.64) * mm});
            skLineSegment(sketch, "E9056", {"start": v(8862.82, -4351.64) * mm, "end": v(8868.62, -4363.73) * mm});
            skLineSegment(sketch, "E9057", {"start": v(8868.62, -4363.73) * mm, "end": v(8875.24, -4376.64) * mm});
            skLineSegment(sketch, "E9058", {"start": v(8875.24, -4376.64) * mm, "end": v(8882.75, -4390.34) * mm});
            skLineSegment(sketch, "E9059", {"start": v(8882.75, -4390.34) * mm, "end": v(8891.17, -4404.79) * mm});
            skLineSegment(sketch, "E9060", {"start": v(8891.17, -4404.79) * mm, "end": v(8900.55, -4419.94) * mm});
            skLineSegment(sketch, "E9061", {"start": v(8900.55, -4419.94) * mm, "end": v(8910.95, -4435.75) * mm});
            skLineSegment(sketch, "E9062", {"start": v(8910.95, -4435.75) * mm, "end": v(8922.4, -4452.2) * mm});
            skLineSegment(sketch, "E9063", {"start": v(8922.4, -4452.2) * mm, "end": v(8934.93, -4469.2) * mm});
            skLineSegment(sketch, "E9064", {"start": v(8934.93, -4469.2) * mm, "end": v(8948.6, -4486.75) * mm});
            skLineSegment(sketch, "E9065", {"start": v(8948.6, -4486.75) * mm, "end": v(8963.44, -4504.77) * mm});
            skLineSegment(sketch, "E9066", {"start": v(8963.44, -4504.77) * mm, "end": v(8979.48, -4523.21) * mm});
            skLineSegment(sketch, "E9067", {"start": v(8979.48, -4523.21) * mm, "end": v(8996.76, -4542.04) * mm});
            skLineSegment(sketch, "E9068", {"start": v(8996.76, -4542.04) * mm, "end": v(9015.3, -4561.18) * mm});
            skLineSegment(sketch, "E9069", {"start": v(9015.3, -4561.18) * mm, "end": v(9035.14, -4580.6) * mm});
            skLineSegment(sketch, "E9070", {"start": v(9035.14, -4580.6) * mm, "end": v(9056.3, -4600.22) * mm});
            skLineSegment(sketch, "E9071", {"start": v(9056.3, -4600.22) * mm, "end": v(9078.46, -4618.49) * mm});
            skLineSegment(sketch, "E9072", {"start": v(9078.46, -4618.49) * mm, "end": v(9209.61, -4583.56) * mm});
            skLineSegment(sketch, "E9073", {"start": v(9209.61, -4583.56) * mm, "end": v(9219.76, -4556.7) * mm});
            skLineSegment(sketch, "E9074", {"start": v(9219.76, -4556.7) * mm, "end": v(9228.36, -4529.14) * mm});
            skLineSegment(sketch, "E9075", {"start": v(9228.36, -4529.14) * mm, "end": v(9235.91, -4502.44) * mm});
            skLineSegment(sketch, "E9076", {"start": v(9235.91, -4502.44) * mm, "end": v(9242.48, -4476.6) * mm});
            skLineSegment(sketch, "E9077", {"start": v(9242.48, -4476.6) * mm, "end": v(9248.1, -4451.68) * mm});
            skLineSegment(sketch, "E9078", {"start": v(9248.1, -4451.68) * mm, "end": v(9252.84, -4427.7) * mm});
            skLineSegment(sketch, "E9079", {"start": v(9252.84, -4427.7) * mm, "end": v(9256.75, -4404.69) * mm});
            skLineSegment(sketch, "E9080", {"start": v(9256.75, -4404.69) * mm, "end": v(9259.9, -4382.67) * mm});
            skLineSegment(sketch, "E9081", {"start": v(9259.9, -4382.67) * mm, "end": v(9262.3, -4361.67) * mm});
            skLineSegment(sketch, "E9082", {"start": v(9262.3, -4361.67) * mm, "end": v(9264.06, -4341.72) * mm});
            skLineSegment(sketch, "E9083", {"start": v(9264.06, -4341.72) * mm, "end": v(9265.22, -4322.83) * mm});
            skLineSegment(sketch, "E9084", {"start": v(9265.22, -4322.83) * mm, "end": v(9265.83, -4305.02) * mm});
            skLineSegment(sketch, "E9085", {"start": v(9265.83, -4305.02) * mm, "end": v(9265.95, -4288.3) * mm});
            skLineSegment(sketch, "E9086", {"start": v(9265.95, -4288.3) * mm, "end": v(9265.64, -4272.68) * mm});
            skLineSegment(sketch, "E9087", {"start": v(9265.64, -4272.68) * mm, "end": v(9264.97, -4258.19) * mm});
            skLineSegment(sketch, "E9088", {"start": v(9264.97, -4258.19) * mm, "end": v(9263.99, -4244.81) * mm});
            skLineSegment(sketch, "E9089", {"start": v(9263.99, -4244.81) * mm, "end": v(9262.76, -4232.57) * mm});
            skLineSegment(sketch, "E9090", {"start": v(9262.76, -4232.57) * mm, "end": v(9261.34, -4221.46) * mm});
            skLineSegment(sketch, "E9091", {"start": v(9261.34, -4221.46) * mm, "end": v(9259.8, -4211.48) * mm});
            skLineSegment(sketch, "E9092", {"start": v(9259.8, -4211.48) * mm, "end": v(9258.18, -4202.63) * mm});
            skLineSegment(sketch, "E9093", {"start": v(9258.18, -4202.63) * mm, "end": v(9256.55, -4194.9) * mm});
            skLineSegment(sketch, "E9094", {"start": v(9256.55, -4194.9) * mm, "end": v(9254.98, -4188.3) * mm});
            skLineSegment(sketch, "E9095", {"start": v(9254.98, -4188.3) * mm, "end": v(9253.51, -4182.81) * mm});
            skLineSegment(sketch, "E9096", {"start": v(9253.51, -4182.81) * mm, "end": v(9252.21, -4178.42) * mm});
            skLineSegment(sketch, "E9097", {"start": v(9252.21, -4178.42) * mm, "end": v(9251.14, -4175.11) * mm});
            skLineSegment(sketch, "E9098", {"start": v(9251.14, -4175.11) * mm, "end": v(9250.34, -4172.88) * mm});
            skLineSegment(sketch, "E9099", {"start": v(9250.34, -4172.88) * mm, "end": v(9249.89, -4171.7) * mm});
            skLineSegment(sketch, "E9100", {"start": v(9249.89, -4171.7) * mm, "end": v(9182.92, -4013.14) * mm});
            skLineSegment(sketch, "E9101", {"start": v(9182.92, -4013.14) * mm, "end": v(9426.09, -3879.7) * mm});
            skLineSegment(sketch, "E9102", {"start": v(9426.09, -3879.7) * mm, "end": v(9523.86, -4021.34) * mm});
            skLineSegment(sketch, "E9103", {"start": v(9523.86, -4021.34) * mm, "end": v(9524.62, -4022.36) * mm});
            skLineSegment(sketch, "E9104", {"start": v(9524.62, -4022.36) * mm, "end": v(9526.08, -4024.23) * mm});
            skLineSegment(sketch, "E9105", {"start": v(9526.08, -4024.23) * mm, "end": v(9528.29, -4026.91) * mm});
            skLineSegment(sketch, "E9106", {"start": v(9528.29, -4026.91) * mm, "end": v(9531.3, -4030.37) * mm});
            skLineSegment(sketch, "E9107", {"start": v(9531.3, -4030.37) * mm, "end": v(9535.14, -4034.56) * mm});
            skLineSegment(sketch, "E9108", {"start": v(9535.14, -4034.56) * mm, "end": v(9539.86, -4039.43) * mm});
            skLineSegment(sketch, "E9109", {"start": v(9539.86, -4039.43) * mm, "end": v(9545.5, -4044.95) * mm});
            skLineSegment(sketch, "E9110", {"start": v(9545.5, -4044.95) * mm, "end": v(9552.1, -4051.06) * mm});
            skLineSegment(sketch, "E9111", {"start": v(9552.1, -4051.06) * mm, "end": v(9559.69, -4057.73) * mm});
            skLineSegment(sketch, "E9112", {"start": v(9559.69, -4057.73) * mm, "end": v(9568.3, -4064.9) * mm});
            skLineSegment(sketch, "E9113", {"start": v(9568.3, -4064.9) * mm, "end": v(9577.97, -4072.5) * mm});
            skLineSegment(sketch, "E9114", {"start": v(9577.97, -4072.5) * mm, "end": v(9588.72, -4080.51) * mm});
            skLineSegment(sketch, "E9115", {"start": v(9588.72, -4080.51) * mm, "end": v(9600.59, -4088.87) * mm});
            skLineSegment(sketch, "E9116", {"start": v(9600.59, -4088.87) * mm, "end": v(9613.6, -4097.51) * mm});
            skLineSegment(sketch, "E9117", {"start": v(9613.6, -4097.51) * mm, "end": v(9627.76, -4106.39) * mm});
            skLineSegment(sketch, "E9118", {"start": v(9627.76, -4106.39) * mm, "end": v(9643.12, -4115.44) * mm});
            skLineSegment(sketch, "E9119", {"start": v(9643.12, -4115.44) * mm, "end": v(9659.67, -4124.62) * mm});
            skLineSegment(sketch, "E9120", {"start": v(9659.67, -4124.62) * mm, "end": v(9677.45, -4133.85) * mm});
            skLineSegment(sketch, "E9121", {"start": v(9677.45, -4133.85) * mm, "end": v(9696.46, -4143.09) * mm});
            skLineSegment(sketch, "E9122", {"start": v(9696.46, -4143.09) * mm, "end": v(9716.71, -4152.27) * mm});
            skLineSegment(sketch, "E9123", {"start": v(9716.71, -4152.27) * mm, "end": v(9738.22, -4161.33) * mm});
            skLineSegment(sketch, "E9124", {"start": v(9738.22, -4161.33) * mm, "end": v(9761, -4170.2) * mm});
            skLineSegment(sketch, "E9125", {"start": v(9761, -4170.2) * mm, "end": v(9785.04, -4178.85) * mm});
            skLineSegment(sketch, "E9126", {"start": v(9785.04, -4178.85) * mm, "end": v(9810.36, -4187.19) * mm});
            skLineSegment(sketch, "E9127", {"start": v(9810.36, -4187.19) * mm, "end": v(9836.95, -4195.15) * mm});
            skLineSegment(sketch, "E9128", {"start": v(9836.95, -4195.15) * mm, "end": v(9864.8, -4202.7) * mm});
            skLineSegment(sketch, "E9129", {"start": v(9864.8, -4202.7) * mm, "end": v(9892.92, -4208.57) * mm});
            skLineSegment(sketch, "E9130", {"start": v(9892.92, -4208.57) * mm, "end": v(9992.81, -4116.7) * mm});
            skLineSegment(sketch, "E9131", {"start": v(9992.81, -4116.7) * mm, "end": v(9989.3, -4088.2) * mm});
            skLineSegment(sketch, "E9132", {"start": v(9989.3, -4088.2) * mm, "end": v(9984.12, -4059.8) * mm});
            skLineSegment(sketch, "E9133", {"start": v(9984.12, -4059.8) * mm, "end": v(9978.4, -4032.64) * mm});
            skLineSegment(sketch, "E9134", {"start": v(9978.4, -4032.64) * mm, "end": v(9972.2, -4006.72) * mm});
            skLineSegment(sketch, "E9135", {"start": v(9972.2, -4006.72) * mm, "end": v(9965.6, -3982.04) * mm});
            skLineSegment(sketch, "E9136", {"start": v(9965.6, -3982.04) * mm, "end": v(9958.66, -3958.6) * mm});
            skLineSegment(sketch, "E9137", {"start": v(9958.66, -3958.6) * mm, "end": v(9951.43, -3936.4) * mm});
            skLineSegment(sketch, "E9138", {"start": v(9951.43, -3936.4) * mm, "end": v(9943.98, -3915.45) * mm});
            skLineSegment(sketch, "E9139", {"start": v(9943.98, -3915.45) * mm, "end": v(9936.36, -3895.74) * mm});
            skLineSegment(sketch, "E9140", {"start": v(9936.36, -3895.74) * mm, "end": v(9928.64, -3877.25) * mm});
            skLineSegment(sketch, "E9141", {"start": v(9928.64, -3877.25) * mm, "end": v(9920.88, -3860) * mm});
            skLineSegment(sketch, "E9142", {"start": v(9920.88, -3860) * mm, "end": v(9913.14, -3843.93) * mm});
            skLineSegment(sketch, "E9143", {"start": v(9913.14, -3843.93) * mm, "end": v(9905.48, -3829.07) * mm});
            skLineSegment(sketch, "E9144", {"start": v(9905.48, -3829.07) * mm, "end": v(9897.95, -3815.39) * mm});
            skLineSegment(sketch, "E9145", {"start": v(9897.95, -3815.39) * mm, "end": v(9890.62, -3802.87) * mm});
            skLineSegment(sketch, "E9146", {"start": v(9890.62, -3802.87) * mm, "end": v(9883.54, -3791.48) * mm});
            skLineSegment(sketch, "E9147", {"start": v(9883.54, -3791.48) * mm, "end": v(9876.76, -3781.21) * mm});
            skLineSegment(sketch, "E9148", {"start": v(9876.76, -3781.21) * mm, "end": v(9870.34, -3772.03) * mm});
            skLineSegment(sketch, "E9149", {"start": v(9870.34, -3772.03) * mm, "end": v(9864.33, -3763.91) * mm});
            skLineSegment(sketch, "E9150", {"start": v(9864.33, -3763.91) * mm, "end": v(9858.79, -3756.83) * mm});
            skLineSegment(sketch, "E9151", {"start": v(9858.79, -3756.83) * mm, "end": v(9853.76, -3750.75) * mm});
            skLineSegment(sketch, "E9152", {"start": v(9853.76, -3750.75) * mm, "end": v(9849.3, -3745.63) * mm});
            skLineSegment(sketch, "E9153", {"start": v(9849.3, -3745.63) * mm, "end": v(9845.45, -3741.45) * mm});
            skLineSegment(sketch, "E9154", {"start": v(9845.45, -3741.45) * mm, "end": v(9842.26, -3738.17) * mm});
            skLineSegment(sketch, "E9155", {"start": v(9842.26, -3738.17) * mm, "end": v(9839.77, -3735.74) * mm});
            skLineSegment(sketch, "E9156", {"start": v(9839.77, -3735.74) * mm, "end": v(9838.02, -3734.13) * mm});
            skLineSegment(sketch, "E9157", {"start": v(9838.02, -3734.13) * mm, "end": v(9837.07, -3733.3) * mm});
            skLineSegment(sketch, "E9158", {"start": v(9837.07, -3733.3) * mm, "end": v(9704.1, -3624.02) * mm});
            skLineSegment(sketch, "E9159", {"start": v(9704.1, -3624.02) * mm, "end": v(9857.39, -3392.86) * mm});
            skLineSegment(sketch, "E9160", {"start": v(9857.39, -3392.86) * mm, "end": v(10009.79, -3472.84) * mm});
            skLineSegment(sketch, "E9161", {"start": v(10009.79, -3472.84) * mm, "end": v(10010.93, -3473.4) * mm});
            skLineSegment(sketch, "E9162", {"start": v(10010.93, -3473.4) * mm, "end": v(10013.1, -3474.37) * mm});
            skLineSegment(sketch, "E9163", {"start": v(10013.1, -3474.37) * mm, "end": v(10016.3, -3475.71) * mm});
            skLineSegment(sketch, "E9164", {"start": v(10016.3, -3475.71) * mm, "end": v(10020.57, -3477.38) * mm});
            skLineSegment(sketch, "E9165", {"start": v(10020.57, -3477.38) * mm, "end": v(10025.92, -3479.3) * mm});
            skLineSegment(sketch, "E9166", {"start": v(10025.92, -3479.3) * mm, "end": v(10032.36, -3481.42) * mm});
            skLineSegment(sketch, "E9167", {"start": v(10032.36, -3481.42) * mm, "end": v(10039.92, -3483.68) * mm});
            skLineSegment(sketch, "E9168", {"start": v(10039.92, -3483.68) * mm, "end": v(10048.6, -3486.03) * mm});
            skLineSegment(sketch, "E9169", {"start": v(10048.6, -3486.03) * mm, "end": v(10058.42, -3488.4) * mm});
            skLineSegment(sketch, "E9170", {"start": v(10058.42, -3488.4) * mm, "end": v(10069.38, -3490.75) * mm});
            skLineSegment(sketch, "E9171", {"start": v(10069.38, -3490.75) * mm, "end": v(10081.47, -3493) * mm});
            skLineSegment(sketch, "E9172", {"start": v(10081.47, -3493) * mm, "end": v(10094.72, -3495.1) * mm});
            skLineSegment(sketch, "E9173", {"start": v(10094.72, -3495.1) * mm, "end": v(10109.1, -3496.97) * mm});
            skLineSegment(sketch, "E9174", {"start": v(10109.1, -3496.97) * mm, "end": v(10124.64, -3498.58) * mm});
            skLineSegment(sketch, "E9175", {"start": v(10124.64, -3498.58) * mm, "end": v(10141.31, -3499.86) * mm});
            skLineSegment(sketch, "E9176", {"start": v(10141.31, -3499.86) * mm, "end": v(10159.12, -3500.74) * mm});
            skLineSegment(sketch, "E9177", {"start": v(10159.12, -3500.74) * mm, "end": v(10178.04, -3501.17) * mm});
            skLineSegment(sketch, "E9178", {"start": v(10178.04, -3501.17) * mm, "end": v(10198.07, -3501.09) * mm});
            skLineSegment(sketch, "E9179", {"start": v(10198.07, -3501.09) * mm, "end": v(10219.2, -3500.43) * mm});
            skLineSegment(sketch, "E9180", {"start": v(10219.2, -3500.43) * mm, "end": v(10241.4, -3499.15) * mm});
            skLineSegment(sketch, "E9181", {"start": v(10241.4, -3499.15) * mm, "end": v(10264.65, -3497.17) * mm});
            skLineSegment(sketch, "E9182", {"start": v(10264.65, -3497.17) * mm, "end": v(10288.95, -3494.45) * mm});
            skLineSegment(sketch, "E9183", {"start": v(10288.95, -3494.45) * mm, "end": v(10314.25, -3490.93) * mm});
            skLineSegment(sketch, "E9184", {"start": v(10314.25, -3490.93) * mm, "end": v(10340.54, -3486.54) * mm});
            skLineSegment(sketch, "E9185", {"start": v(10340.54, -3486.54) * mm, "end": v(10367.79, -3481.24) * mm});
            skLineSegment(sketch, "E9186", {"start": v(10367.79, -3481.24) * mm, "end": v(10395.96, -3474.98) * mm});
            skLineSegment(sketch, "E9187", {"start": v(10395.96, -3474.98) * mm, "end": v(10423.58, -3467.11) * mm});
            skLineSegment(sketch, "E9188", {"start": v(10423.58, -3467.11) * mm, "end": v(10469.34, -3339.34) * mm});
            skLineSegment(sketch, "E9189", {"start": v(10469.34, -3339.34) * mm, "end": v(10453, -3315.73) * mm});
            skLineSegment(sketch, "E9190", {"start": v(10453, -3315.73) * mm, "end": v(10435.2, -3293) * mm});
            skLineSegment(sketch, "E9191", {"start": v(10435.2, -3293) * mm, "end": v(10417.52, -3271.6) * mm});
            skLineSegment(sketch, "E9192", {"start": v(10417.52, -3271.6) * mm, "end": v(10399.99, -3251.53) * mm});
            skLineSegment(sketch, "E9193", {"start": v(10399.99, -3251.53) * mm, "end": v(10382.67, -3232.74) * mm});
            skLineSegment(sketch, "E9194", {"start": v(10382.67, -3232.74) * mm, "end": v(10365.63, -3215.22) * mm});
            skLineSegment(sketch, "E9195", {"start": v(10365.63, -3215.22) * mm, "end": v(10348.91, -3198.93) * mm});
            skLineSegment(sketch, "E9196", {"start": v(10348.91, -3198.93) * mm, "end": v(10332.58, -3183.84) * mm});
            skLineSegment(sketch, "E9197", {"start": v(10332.58, -3183.84) * mm, "end": v(10316.67, -3169.93) * mm});
            skLineSegment(sketch, "E9198", {"start": v(10316.67, -3169.93) * mm, "end": v(10301.24, -3157.14) * mm});
            skLineSegment(sketch, "E9199", {"start": v(10301.24, -3157.14) * mm, "end": v(10286.35, -3145.46) * mm});
            skLineSegment(sketch, "E9200", {"start": v(10286.35, -3145.46) * mm, "end": v(10272.04, -3134.84) * mm});
            skLineSegment(sketch, "E9201", {"start": v(10272.04, -3134.84) * mm, "end": v(10258.35, -3125.25) * mm});
            skLineSegment(sketch, "E9202", {"start": v(10258.35, -3125.25) * mm, "end": v(10245.32, -3116.63) * mm});
            skLineSegment(sketch, "E9203", {"start": v(10245.32, -3116.63) * mm, "end": v(10233, -3108.95) * mm});
            skLineSegment(sketch, "E9204", {"start": v(10233, -3108.95) * mm, "end": v(10221.44, -3102.16) * mm});
            skLineSegment(sketch, "E9205", {"start": v(10221.44, -3102.16) * mm, "end": v(10210.67, -3096.21) * mm});
            skLineSegment(sketch, "E9206", {"start": v(10210.67, -3096.21) * mm, "end": v(10200.72, -3091.07) * mm});
            skLineSegment(sketch, "E9207", {"start": v(10200.72, -3091.07) * mm, "end": v(10191.63, -3086.67) * mm});
            skLineSegment(sketch, "E9208", {"start": v(10191.63, -3086.67) * mm, "end": v(10183.43, -3082.98) * mm});
            skLineSegment(sketch, "E9209", {"start": v(10183.43, -3082.98) * mm, "end": v(10176.15, -3079.93) * mm});
            skLineSegment(sketch, "E9210", {"start": v(10176.15, -3079.93) * mm, "end": v(10169.82, -3077.47) * mm});
            skLineSegment(sketch, "E9211", {"start": v(10169.82, -3077.47) * mm, "end": v(10164.47, -3075.56) * mm});
            skLineSegment(sketch, "E9212", {"start": v(10164.47, -3075.56) * mm, "end": v(10160.12, -3074.13) * mm});
            skLineSegment(sketch, "E9213", {"start": v(10160.12, -3074.13) * mm, "end": v(10156.79, -3073.14) * mm});
            skLineSegment(sketch, "E9214", {"start": v(10156.79, -3073.14) * mm, "end": v(10154.5, -3072.52) * mm});
            skLineSegment(sketch, "E9215", {"start": v(10154.5, -3072.52) * mm, "end": v(10153.26, -3072.22) * mm});
            skLineSegment(sketch, "E9216", {"start": v(10153.26, -3072.22) * mm, "end": v(9984.73, -3037.27) * mm});
            skLineSegment(sketch, "E9217", {"start": v(9984.73, -3037.27) * mm, "end": v(10013.04, -2761.34) * mm});
            skLineSegment(sketch, "E9218", {"start": v(10013.04, -2761.34) * mm, "end": v(10185.16, -2761.34) * mm});
            skLineSegment(sketch, "E9219", {"start": v(10185.16, -2761.34) * mm, "end": v(10186.43, -2761.3) * mm});
            skLineSegment(sketch, "E9220", {"start": v(10186.43, -2761.3) * mm, "end": v(10188.8, -2761.16) * mm});
            skLineSegment(sketch, "E9221", {"start": v(8857.34, -2761.34) * mm, "end": v(8450.94, -2761.34) * mm});
            skFitSpline(sketch, "E9222", {"points": [v(10388.82, -2531.9) * mm, v(10388.82, -2586.96) * mm, v(10344.18, -2631.6) * mm, v(10289.12, -2631.6) * mm]});
            skFitSpline(sketch, "E9223", {"points": [v(10289.12, -2631.6) * mm, v(10234.06, -2631.6) * mm, v(10189.43, -2586.96) * mm, v(10189.43, -2531.9) * mm]});
            skFitSpline(sketch, "E9224", {"points": [v(10189.43, -2531.9) * mm, v(10189.43, -2476.84) * mm, v(10234.06, -2432.2) * mm, v(10289.12, -2432.2) * mm]});
            skFitSpline(sketch, "E9225", {"points": [v(10289.12, -2432.2) * mm, v(10344.18, -2432.2) * mm, v(10388.82, -2476.84) * mm, v(10388.82, -2531.9) * mm]});
            skLineSegment(sketch, "E9226", {"start": v(8654.14, -2964.54) * mm, "end": v(8654.14, -2558.14) * mm});
            skLineSegment(sketch, "E9227", {"start": v(8011.42, -1925.78) * mm, "end": v(7987.65, -1944.68) * mm});
            skLineSegment(sketch, "E9228", {"start": v(7987.65, -1944.68) * mm, "end": v(7964.28, -1964.4) * mm});
            skLineSegment(sketch, "E9229", {"start": v(7964.28, -1964.4) * mm, "end": v(7941.52, -1984.71) * mm});
            skLineSegment(sketch, "E9230", {"start": v(7941.52, -1984.71) * mm, "end": v(7919.37, -2005.64) * mm});
            skLineSegment(sketch, "E9231", {"start": v(8004.1, -2010.52) * mm, "end": v(7924.25, -1918.27) * mm});
            skLineSegment(sketch, "E9232", {"start": v(7974.24, -1877.63) * mm, "end": v(7968.34, -1921.11) * mm});
            skLineSegment(sketch, "E9233", {"start": v(7968.34, -1921.11) * mm, "end": v(7964.28, -1964.4) * mm});
            skLineSegment(sketch, "E9234", {"start": v(7964.28, -1964.4) * mm, "end": v(7962.04, -2007.06) * mm});
            skLineSegment(sketch, "E9235", {"start": v(7962.04, -2007.06) * mm, "end": v(7961.84, -2049.33) * mm});
            skLineSegment(sketch, "E9236", {"start": v(8048.6, -1974.15) * mm, "end": v(8006.75, -1968.46) * mm});
            skLineSegment(sketch, "E9237", {"start": v(8006.75, -1968.46) * mm, "end": v(7964.28, -1964.4) * mm});
            skLineSegment(sketch, "E9238", {"start": v(7964.28, -1964.4) * mm, "end": v(7920.8, -1962.16) * mm});
            skLineSegment(sketch, "E9239", {"start": v(7920.8, -1962.16) * mm, "end": v(7876.9, -1961.95) * mm});
            skLineSegment(sketch, "E9240", {"start": v(8026.46, -1839.63) * mm, "end": v(8037.02, -1796.35) * mm});
            skLineSegment(sketch, "E9241", {"start": v(8037.02, -1796.35) * mm, "end": v(8135.58, -1950.37) * mm});
            skLineSegment(sketch, "E9242", {"start": v(8159.15, -1935.74) * mm, "end": v(8135.58, -1950.37) * mm});
            skLineSegment(sketch, "E9243", {"start": v(8135.58, -1950.37) * mm, "end": v(8112.2, -1965.61) * mm});
            skLineSegment(sketch, "E9244", {"start": v(8401.97, -1643.95) * mm, "end": v(8442.2, -1822.36) * mm});
            skLineSegment(sketch, "E9245", {"start": v(8442.2, -1822.36) * mm, "end": v(8403.8, -1784.56) * mm});
            skLineSegment(sketch, "E9246", {"start": v(8403.8, -1784.56) * mm, "end": v(8362.96, -1748.19) * mm});
            skLineSegment(sketch, "E9247", {"start": v(8362.96, -1748.19) * mm, "end": v(8319.88, -1713.44) * mm});
            skLineSegment(sketch, "E9248", {"start": v(8319.88, -1713.44) * mm, "end": v(8274.77, -1680.52) * mm});
            skLineSegment(sketch, "E9249", {"start": v(8274.77, -1680.52) * mm, "end": v(8335.32, -1853.04) * mm});
            skLineSegment(sketch, "E9250", {"start": v(8601.51, -1678.08) * mm, "end": v(8570.22, -1679.91) * mm});
            skLineSegment(sketch, "E9251", {"start": v(8570.22, -1679.91) * mm, "end": v(8539.13, -1682.96) * mm});
            skLineSegment(sketch, "E9252", {"start": v(8539.13, -1682.96) * mm, "end": v(8507.84, -1686.62) * mm});
            skLineSegment(sketch, "E9253", {"start": v(8507.84, -1686.62) * mm, "end": v(8476.95, -1691.3) * mm});
            skLineSegment(sketch, "E9254", {"start": v(8604.56, -1738.84) * mm, "end": v(8575.1, -1740.87) * mm});
            skLineSegment(sketch, "E9255", {"start": v(8575.1, -1740.87) * mm, "end": v(8545.43, -1743.51) * mm});
            skLineSegment(sketch, "E9256", {"start": v(8545.43, -1743.51) * mm, "end": v(8516.17, -1746.97) * mm});
            skLineSegment(sketch, "E9257", {"start": v(8516.17, -1746.97) * mm, "end": v(8486.9, -1751.44) * mm});
            skLineSegment(sketch, "E9258", {"start": v(8664.5, -1646.38) * mm, "end": v(8698.03, -1616.72) * mm});
            skLineSegment(sketch, "E9259", {"start": v(8698.03, -1616.72) * mm, "end": v(8690.92, -1799.4) * mm});
            skLineSegment(sketch, "E9260", {"start": v(8718.76, -1800.82) * mm, "end": v(8690.92, -1799.4) * mm});
            skLineSegment(sketch, "E9261", {"start": v(8690.92, -1799.4) * mm, "end": v(8663.08, -1798.78) * mm});
            skLineSegment(sketch, "E9262", {"start": v(8793.13, -1654.92) * mm, "end": v(8829.7, -1629.32) * mm});
            skLineSegment(sketch, "E9263", {"start": v(8829.7, -1629.32) * mm, "end": v(8862.42, -1634.8) * mm});
            skLineSegment(sketch, "E9264", {"start": v(8862.42, -1634.8) * mm, "end": v(8894.94, -1641.3) * mm});
            skLineSegment(sketch, "E9265", {"start": v(8894.94, -1641.3) * mm, "end": v(8919.93, -1678.5) * mm});
            skLineSegment(sketch, "E9266", {"start": v(8919.93, -1678.5) * mm, "end": v(8912.61, -1707.95) * mm});
            skLineSegment(sketch, "E9267", {"start": v(8912.61, -1707.95) * mm, "end": v(8875.63, -1730.71) * mm});
            skLineSegment(sketch, "E9268", {"start": v(8875.63, -1730.71) * mm, "end": v(8898.19, -1767.29) * mm});
            skLineSegment(sketch, "E9269", {"start": v(8898.19, -1767.29) * mm, "end": v(8890.87, -1796.75) * mm});
            skLineSegment(sketch, "E9270", {"start": v(8890.87, -1796.75) * mm, "end": v(8856.53, -1820.12) * mm});
            skLineSegment(sketch, "E9271", {"start": v(8856.53, -1820.12) * mm, "end": v(8829.1, -1814.63) * mm});
            skLineSegment(sketch, "E9272", {"start": v(8829.1, -1814.63) * mm, "end": v(8801.67, -1810.16) * mm});
            skLineSegment(sketch, "E9273", {"start": v(8801.67, -1810.16) * mm, "end": v(8777.9, -1776.03) * mm});
            skLineSegment(sketch, "E9274", {"start": v(8845.76, -1724.82) * mm, "end": v(8875.63, -1730.71) * mm});
            skLineSegment(sketch, "E9275", {"start": v(9106.06, -1808.94) * mm, "end": v(9133.5, -1822.56) * mm});
            skLineSegment(sketch, "E9276", {"start": v(9133.5, -1822.56) * mm, "end": v(9160.31, -1836.78) * mm});
            skLineSegment(sketch, "E9277", {"start": v(9160.31, -1836.78) * mm, "end": v(9186.93, -1851.82) * mm});
            skLineSegment(sketch, "E9278", {"start": v(9186.93, -1851.82) * mm, "end": v(9229.2, -1841.66) * mm});
            skLineSegment(sketch, "E9279", {"start": v(9229.2, -1841.66) * mm, "end": v(9245.25, -1815.85) * mm});
            skLineSegment(sketch, "E9280", {"start": v(9245.25, -1815.85) * mm, "end": v(9233.06, -1772.77) * mm});
            skLineSegment(sketch, "E9281", {"start": v(9233.06, -1772.77) * mm, "end": v(9204.2, -1756.52) * mm});
            skLineSegment(sketch, "E9282", {"start": v(9204.2, -1756.52) * mm, "end": v(9174.94, -1741.08) * mm});
            skLineSegment(sketch, "E9283", {"start": v(9174.94, -1741.08) * mm, "end": v(9145.28, -1726.45) * mm});
            skLineSegment(sketch, "E9284", {"start": v(9145.28, -1726.45) * mm, "end": v(9066.84, -1891.65) * mm});
            skLineSegment(sketch, "E9285", {"start": v(9210.7, -1975.97) * mm, "end": v(9281.22, -1876.4) * mm});
            skLineSegment(sketch, "E9286", {"start": v(9298.9, -1851.62) * mm, "end": v(9316.58, -1826.83) * mm});
            skLineSegment(sketch, "E9287", {"start": v(9359.65, -2062.33) * mm, "end": v(9318.2, -2064.37) * mm});
            skLineSegment(sketch, "E9288", {"start": v(9318.2, -2064.37) * mm, "end": v(9318, -2022.71) * mm});
            skLineSegment(sketch, "E9289", {"start": v(9318, -2022.71) * mm, "end": v(9420, -1909.53) * mm});
            skLineSegment(sketch, "E9290", {"start": v(9424.68, -1998.12) * mm, "end": v(9402.33, -1975.97) * mm});
            skLineSegment(sketch, "E9291", {"start": v(9402.33, -1975.97) * mm, "end": v(9379.16, -1954.84) * mm});
            skLineSegment(sketch, "E9292", {"start": v(9379.16, -1954.84) * mm, "end": v(9355.59, -1934.12) * mm});
            skLineSegment(sketch, "E9293", {"start": v(9355.59, -1934.12) * mm, "end": v(9331.4, -1914.2) * mm});
            skLineSegment(sketch, "E9294", {"start": v(9444.8, -2212.1) * mm, "end": v(9428.54, -2189.33) * mm});
            skLineSegment(sketch, "E9295", {"start": v(9428.54, -2189.33) * mm, "end": v(9411.67, -2167.19) * mm});
            skLineSegment(sketch, "E9296", {"start": v(9411.67, -2167.19) * mm, "end": v(9394.2, -2145.65) * mm});
            skLineSegment(sketch, "E9297", {"start": v(9394.2, -2145.65) * mm, "end": v(9398.87, -2104.4) * mm});
            skLineSegment(sketch, "E9298", {"start": v(9398.87, -2104.4) * mm, "end": v(9444.6, -2063.96) * mm});
            skLineSegment(sketch, "E9299", {"start": v(9444.6, -2063.96) * mm, "end": v(9487.87, -2067.62) * mm});
            skLineSegment(sketch, "E9300", {"start": v(9487.87, -2067.62) * mm, "end": v(9507.58, -2092) * mm});
            skLineSegment(sketch, "E9301", {"start": v(9507.58, -2092) * mm, "end": v(9526.48, -2117) * mm});
            skLineSegment(sketch, "E9302", {"start": v(9526.48, -2117) * mm, "end": v(9544.77, -2142.4) * mm});
            skLineSegment(sketch, "E9303", {"start": v(9527.1, -2226.93) * mm, "end": v(9568.75, -2237.09) * mm});
            skLineSegment(sketch, "E9304", {"start": v(9568.75, -2237.09) * mm, "end": v(9610.4, -2249.48) * mm});
            skLineSegment(sketch, "E9305", {"start": v(9610.4, -2249.48) * mm, "end": v(9624.63, -2277.32) * mm});
            skLineSegment(sketch, "E9306", {"start": v(9624.63, -2277.32) * mm, "end": v(9610.6, -2318.37) * mm});
            skLineSegment(sketch, "E9307", {"start": v(9610.6, -2318.37) * mm, "end": v(9527.7, -2356.77) * mm});
            skLineSegment(sketch, "E9308", {"start": v(9475.07, -2258.63) * mm, "end": v(9631.13, -2163.12) * mm});
            skLineSegment(sketch, "E9309", {"start": v(9591.1, -2540.67) * mm, "end": v(9597.2, -2567.9) * mm});
            skLineSegment(sketch, "E9310", {"start": v(9597.2, -2567.9) * mm, "end": v(9602.27, -2595.13) * mm});
            skLineSegment(sketch, "E9311", {"start": v(9602.27, -2595.13) * mm, "end": v(9606.74, -2622.56) * mm});
            skLineSegment(sketch, "E9312", {"start": v(9606.74, -2622.56) * mm, "end": v(9640.68, -2646.74) * mm});
            skLineSegment(sketch, "E9313", {"start": v(9640.68, -2646.74) * mm, "end": v(9761.79, -2632.72) * mm});
            skLineSegment(sketch, "E9314", {"start": v(9761.79, -2632.72) * mm, "end": v(9787.8, -2596.34) * mm});
            skLineSegment(sketch, "E9315", {"start": v(9787.8, -2596.34) * mm, "end": v(9782.51, -2563.63) * mm});
            skLineSegment(sketch, "E9316", {"start": v(9782.51, -2563.63) * mm, "end": v(9776.21, -2531.12) * mm});
            skLineSegment(sketch, "E9317", {"start": v(9776.21, -2531.12) * mm, "end": v(9769.1, -2498.8) * mm});
            skLineSegment(sketch, "E9318", {"start": v(9776.21, -2531.12) * mm, "end": v(9597.2, -2567.9) * mm});
            skLineSegment(sketch, "E9319", {"start": v(9737, -2824.13) * mm, "end": v(9738.22, -2792.64) * mm});
            skLineSegment(sketch, "E9320", {"start": v(9738.22, -2792.64) * mm, "end": v(9738.62, -2761.34) * mm});
            skLineSegment(sketch, "E9321", {"start": v(9738.62, -2761.34) * mm, "end": v(9738.22, -2730.05) * mm});
            skLineSegment(sketch, "E9322", {"start": v(9738.22, -2730.05) * mm, "end": v(9737, -2698.55) * mm});
            skLineSegment(sketch, "E9323", {"start": v(9676.04, -2820.47) * mm, "end": v(9677.26, -2791.01) * mm});
            skLineSegment(sketch, "E9324", {"start": v(9677.26, -2791.01) * mm, "end": v(9677.66, -2761.34) * mm});
            skLineSegment(sketch, "E9325", {"start": v(9677.66, -2761.34) * mm, "end": v(9677.26, -2731.68) * mm});
            skLineSegment(sketch, "E9326", {"start": v(9677.26, -2731.68) * mm, "end": v(9676.04, -2702.21) * mm});
            skLineSegment(sketch, "E9327", {"start": v(9761.79, -2889.97) * mm, "end": v(9787.8, -2926.34) * mm});
            skLineSegment(sketch, "E9328", {"start": v(9787.8, -2926.34) * mm, "end": v(9782.51, -2959.06) * mm});
            skLineSegment(sketch, "E9329", {"start": v(9782.51, -2959.06) * mm, "end": v(9776.21, -2991.57) * mm});
            skLineSegment(sketch, "E9330", {"start": v(9776.21, -2991.57) * mm, "end": v(9739.43, -3016.97) * mm});
            skLineSegment(sketch, "E9331", {"start": v(9739.43, -3016.97) * mm, "end": v(9709.77, -3010.06) * mm});
            skLineSegment(sketch, "E9332", {"start": v(9709.77, -3010.06) * mm, "end": v(9686.8, -2973.28) * mm});
            skLineSegment(sketch, "E9333", {"start": v(9686.8, -2973.28) * mm, "end": v(9650.43, -2996.04) * mm});
            skLineSegment(sketch, "E9334", {"start": v(9650.43, -2996.04) * mm, "end": v(9620.77, -2989.13) * mm});
            skLineSegment(sketch, "E9335", {"start": v(9620.77, -2989.13) * mm, "end": v(9597.2, -2954.79) * mm});
            skLineSegment(sketch, "E9336", {"start": v(9597.2, -2954.79) * mm, "end": v(9602.27, -2927.56) * mm});
            skLineSegment(sketch, "E9337", {"start": v(9602.27, -2927.56) * mm, "end": v(9606.74, -2900.13) * mm});
            skLineSegment(sketch, "E9338", {"start": v(9606.74, -2900.13) * mm, "end": v(9640.68, -2875.95) * mm});
            skLineSegment(sketch, "E9339", {"start": v(9692.5, -2943.2) * mm, "end": v(9686.8, -2973.28) * mm});
            skLineSegment(sketch, "E9340", {"start": v(9606.14, -3044.6) * mm, "end": v(9576.87, -3035.87) * mm});
            skLineSegment(sketch, "E9341", {"start": v(9515.5, -3190.9) * mm, "end": v(9527.7, -3165.91) * mm});
            skLineSegment(sketch, "E9342", {"start": v(9527.7, -3165.91) * mm, "end": v(9539.08, -3140.51) * mm});
            skLineSegment(sketch, "E9343", {"start": v(9539.08, -3140.51) * mm, "end": v(9549.65, -3114.7) * mm});
            skLineSegment(sketch, "E9344", {"start": v(9549.65, -3114.7) * mm, "end": v(9559.4, -3088.7) * mm});
            skLineSegment(sketch, "E9345", {"start": v(9559.4, -3088.7) * mm, "end": v(9616.7, -3109.42) * mm});
            skLineSegment(sketch, "E9346", {"start": v(9616.7, -3109.42) * mm, "end": v(9634.58, -3148.24) * mm});
            skLineSegment(sketch, "E9347", {"start": v(9634.58, -3148.24) * mm, "end": v(9623, -3176.48) * mm});
            skLineSegment(sketch, "E9348", {"start": v(9623, -3176.48) * mm, "end": v(9610.6, -3204.32) * mm});
            skLineSegment(sketch, "E9349", {"start": v(9610.6, -3204.32) * mm, "end": v(9624.63, -3245.37) * mm});
            skLineSegment(sketch, "E9350", {"start": v(9624.63, -3245.37) * mm, "end": v(9652.06, -3258.98) * mm});
            skLineSegment(sketch, "E9351", {"start": v(9652.06, -3258.98) * mm, "end": v(9693.51, -3242.72) * mm});
            skLineSegment(sketch, "E9352", {"start": v(9693.51, -3242.72) * mm, "end": v(9707.13, -3212.45) * mm});
            skLineSegment(sketch, "E9353", {"start": v(9707.13, -3212.45) * mm, "end": v(9719.72, -3181.97) * mm});
            skLineSegment(sketch, "E9354", {"start": v(9719.72, -3181.97) * mm, "end": v(9702.66, -3140.51) * mm});
            skLineSegment(sketch, "E9355", {"start": v(9575.66, -3441.86) * mm, "end": v(9594.96, -3415.04) * mm});
            skLineSegment(sketch, "E9356", {"start": v(9594.96, -3415.04) * mm, "end": v(9613.45, -3387.6) * mm});
            skLineSegment(sketch, "E9357", {"start": v(9613.45, -3387.6) * mm, "end": v(9631.13, -3359.56) * mm});
            skLineSegment(sketch, "E9358", {"start": v(9631.13, -3359.56) * mm, "end": v(9648, -3331.12) * mm});
            skLineSegment(sketch, "E9359", {"start": v(9648, -3331.12) * mm, "end": v(9595.16, -3300.64) * mm});
            skLineSegment(sketch, "E9360", {"start": v(9595.16, -3300.64) * mm, "end": v(9579.1, -3327.66) * mm});
            skLineSegment(sketch, "E9361", {"start": v(9579.1, -3327.66) * mm, "end": v(9562.45, -3354.28) * mm});
            skLineSegment(sketch, "E9362", {"start": v(9562.45, -3354.28) * mm, "end": v(9544.77, -3380.3) * mm});
            skLineSegment(sketch, "E9363", {"start": v(9544.77, -3380.3) * mm, "end": v(9502.1, -3387.6) * mm});
            skLineSegment(sketch, "E9364", {"start": v(9502.1, -3387.6) * mm, "end": v(9452.92, -3351.44) * mm});
            skLineSegment(sketch, "E9365", {"start": v(9452.92, -3351.44) * mm, "end": v(9444.8, -3310.6) * mm});
            skLineSegment(sketch, "E9366", {"start": v(9444.8, -3310.6) * mm, "end": v(9460.24, -3287.63) * mm});
            skLineSegment(sketch, "E9367", {"start": v(9460.24, -3287.63) * mm, "end": v(9475.07, -3264.06) * mm});
            skLineSegment(sketch, "E9368", {"start": v(9475.07, -3264.06) * mm, "end": v(9515.71, -3255.32) * mm});
            skLineSegment(sketch, "E9369", {"start": v(9358.84, -3545.29) * mm, "end": v(9335.88, -3565.2) * mm});
            skLineSegment(sketch, "E9370", {"start": v(9335.88, -3565.2) * mm, "end": v(9312.3, -3584.7) * mm});
            skLineSegment(sketch, "E9371", {"start": v(9312.3, -3584.7) * mm, "end": v(9288.33, -3603.4) * mm});
            skLineSegment(sketch, "E9372", {"start": v(9288.33, -3603.4) * mm, "end": v(9281.22, -3646.28) * mm});
            skLineSegment(sketch, "E9373", {"start": v(9281.22, -3646.28) * mm, "end": v(9298.9, -3671.07) * mm});
            skLineSegment(sketch, "E9374", {"start": v(9298.9, -3671.07) * mm, "end": v(9343.2, -3676.35) * mm});
            skLineSegment(sketch, "E9375", {"start": v(9343.2, -3676.35) * mm, "end": v(9369.4, -3656.03) * mm});
            skLineSegment(sketch, "E9376", {"start": v(9369.4, -3656.03) * mm, "end": v(9395.01, -3635.1) * mm});
            skLineSegment(sketch, "E9377", {"start": v(9395.01, -3635.1) * mm, "end": v(9420, -3613.16) * mm});
            skLineSegment(sketch, "E9378", {"start": v(9420, -3613.16) * mm, "end": v(9297.68, -3477.22) * mm});
            skLineSegment(sketch, "E9379", {"start": v(9119.06, -3741.17) * mm, "end": v(9147.3, -3727.36) * mm});
            skLineSegment(sketch, "E9380", {"start": v(9147.3, -3727.36) * mm, "end": v(9174.94, -3712.73) * mm});
            skLineSegment(sketch, "E9381", {"start": v(9174.94, -3712.73) * mm, "end": v(9202.38, -3697.28) * mm});
            skLineSegment(sketch, "E9382", {"start": v(9202.38, -3697.28) * mm, "end": v(9229.2, -3681.03) * mm});
            skLineSegment(sketch, "E9383", {"start": v(9093.06, -3686.1) * mm, "end": v(9119.47, -3673.1) * mm});
            skLineSegment(sketch, "E9384", {"start": v(9119.47, -3673.1) * mm, "end": v(9145.68, -3659.28) * mm});
            skLineSegment(sketch, "E9385", {"start": v(9145.68, -3659.28) * mm, "end": v(9171.5, -3644.65) * mm});
            skLineSegment(sketch, "E9386", {"start": v(9171.5, -3644.65) * mm, "end": v(9196.9, -3629.21) * mm});
            skLineSegment(sketch, "E9387", {"start": v(8926.84, -3748.08) * mm, "end": v(8955.08, -3739.75) * mm});
            skLineSegment(sketch, "E9388", {"start": v(8955.08, -3739.75) * mm, "end": v(8983.33, -3730.6) * mm});
            skLineSegment(sketch, "E9389", {"start": v(8983.33, -3730.6) * mm, "end": v(9011.17, -3720.65) * mm});
            skLineSegment(sketch, "E9390", {"start": v(9011.17, -3720.65) * mm, "end": v(9038.8, -3709.88) * mm});
            skLineSegment(sketch, "E9391", {"start": v(9038.8, -3709.88) * mm, "end": v(9025.39, -3758.65) * mm});
            skLineSegment(sketch, "E9392", {"start": v(9025.39, -3758.65) * mm, "end": v(9009.54, -3807.62) * mm});
            skLineSegment(sketch, "E9393", {"start": v(9009.54, -3807.62) * mm, "end": v(8991.05, -3856.18) * mm});
            skLineSegment(sketch, "E9394", {"start": v(8991.05, -3856.18) * mm, "end": v(8937.2, -3681.43) * mm});
            skLineSegment(sketch, "E9395", {"start": v(8724.86, -3813.1) * mm, "end": v(8694.38, -3814.73) * mm});
            skLineSegment(sketch, "E9396", {"start": v(8694.38, -3814.73) * mm, "end": v(8664.1, -3815.34) * mm});
            skLineSegment(sketch, "E9397", {"start": v(8664.1, -3815.34) * mm, "end": v(8633.62, -3815.34) * mm});
            skLineSegment(sketch, "E9398", {"start": v(8633.62, -3815.34) * mm, "end": v(8601.51, -3844.6) * mm});
            skLineSegment(sketch, "E9399", {"start": v(8601.51, -3844.6) * mm, "end": v(8600.1, -3875.08) * mm});
            skLineSegment(sketch, "E9400", {"start": v(8600.1, -3875.08) * mm, "end": v(8631.8, -3906.58) * mm});
            skLineSegment(sketch, "E9401", {"start": v(8631.8, -3906.58) * mm, "end": v(8664.91, -3906.78) * mm});
            skLineSegment(sketch, "E9402", {"start": v(8664.91, -3906.78) * mm, "end": v(8698.03, -3905.97) * mm});
            skLineSegment(sketch, "E9403", {"start": v(8698.03, -3905.97) * mm, "end": v(8730.95, -3904.34) * mm});
            skLineSegment(sketch, "E9404", {"start": v(8730.95, -3904.34) * mm, "end": v(8718.76, -3721.87) * mm});
            skLineSegment(sketch, "E9405", {"start": v(8551.93, -3718.62) * mm, "end": v(8545.43, -3779.17) * mm});
            skLineSegment(sketch, "E9406", {"start": v(8545.43, -3779.17) * mm, "end": v(8507.84, -3836.07) * mm});
            skLineSegment(sketch, "E9407", {"start": v(8507.84, -3836.07) * mm, "end": v(8467, -3891.54) * mm});
            skLineSegment(sketch, "E9408", {"start": v(8467, -3891.54) * mm, "end": v(8446.07, -3825.7) * mm});
            skLineSegment(sketch, "E9409", {"start": v(8446.07, -3825.7) * mm, "end": v(8428.8, -3759.87) * mm});
            skLineSegment(sketch, "E9410", {"start": v(8428.8, -3759.87) * mm, "end": v(8442.2, -3700.33) * mm});
            skLineSegment(sketch, "E9411", {"start": v(8545.43, -3779.17) * mm, "end": v(8516.17, -3775.72) * mm});
            skLineSegment(sketch, "E9412", {"start": v(8516.17, -3775.72) * mm, "end": v(8486.9, -3771.25) * mm});
            skLineSegment(sketch, "E9413", {"start": v(8486.9, -3771.25) * mm, "end": v(8457.65, -3765.96) * mm});
            skLineSegment(sketch, "E9414", {"start": v(8457.65, -3765.96) * mm, "end": v(8428.8, -3759.87) * mm});
            skLineSegment(sketch, "E9415", {"start": v(8236.36, -3762.3) * mm, "end": v(8265.42, -3773.89) * mm});
            skLineSegment(sketch, "E9416", {"start": v(8265.42, -3773.89) * mm, "end": v(8294.89, -3784.66) * mm});
            skLineSegment(sketch, "E9417", {"start": v(8294.89, -3784.66) * mm, "end": v(8324.55, -3794.61) * mm});
            skLineSegment(sketch, "E9418", {"start": v(8324.55, -3794.61) * mm, "end": v(8354.63, -3803.76) * mm});
            skLineSegment(sketch, "E9419", {"start": v(8259.73, -3706.02) * mm, "end": v(8287.37, -3717) * mm});
            skLineSegment(sketch, "E9420", {"start": v(8287.37, -3717) * mm, "end": v(8315, -3727.15) * mm});
            skLineSegment(sketch, "E9421", {"start": v(8315, -3727.15) * mm, "end": v(8343.04, -3736.5) * mm});
            skLineSegment(sketch, "E9422", {"start": v(8343.04, -3736.5) * mm, "end": v(8371.5, -3745.24) * mm});
            skLineSegment(sketch, "E9423", {"start": v(8135.58, -3572.31) * mm, "end": v(8159.15, -3586.94) * mm});
            skLineSegment(sketch, "E9424", {"start": v(8159.15, -3586.94) * mm, "end": v(8183.33, -3600.97) * mm});
            skLineSegment(sketch, "E9425", {"start": v(8183.33, -3600.97) * mm, "end": v(8207.71, -3614.17) * mm});
            skLineSegment(sketch, "E9426", {"start": v(8207.71, -3614.17) * mm, "end": v(8232.5, -3626.77) * mm});
            skLineSegment(sketch, "E9427", {"start": v(8232.5, -3626.77) * mm, "end": v(8205.88, -3681.64) * mm});
            skLineSegment(sketch, "E9428", {"start": v(8205.88, -3681.64) * mm, "end": v(8165.24, -3695.25) * mm});
            skLineSegment(sketch, "E9429", {"start": v(8165.24, -3695.25) * mm, "end": v(8138.42, -3680.62) * mm});
            skLineSegment(sketch, "E9430", {"start": v(8138.42, -3680.62) * mm, "end": v(8112.2, -3665.38) * mm});
            skLineSegment(sketch, "E9431", {"start": v(8112.2, -3665.38) * mm, "end": v(8069.74, -3675.13) * mm});
            skLineSegment(sketch, "E9432", {"start": v(8069.74, -3675.13) * mm, "end": v(8053.48, -3700.74) * mm});
            skLineSegment(sketch, "E9433", {"start": v(8053.48, -3700.74) * mm, "end": v(8065.07, -3743.81) * mm});
            skLineSegment(sketch, "E9434", {"start": v(8065.07, -3743.81) * mm, "end": v(8093.72, -3760.48) * mm});
            skLineSegment(sketch, "E9435", {"start": v(8093.72, -3760.48) * mm, "end": v(8122.98, -3776.33) * mm});
            skLineSegment(sketch, "E9436", {"start": v(8122.98, -3776.33) * mm, "end": v(8165.85, -3763.73) * mm});
            skFitSpline(sketch, "E9437", {"points": [v(10305.14, -2761.34) * mm, v(10305.14, -3673.16) * mm, v(9565.97, -4412.34) * mm, v(8654.14, -4412.34) * mm]});
            skFitSpline(sketch, "E9438", {"points": [v(8654.14, -4412.34) * mm, v(7742.32, -4412.34) * mm, v(7003.14, -3673.16) * mm, v(7003.14, -2761.34) * mm]});
            skFitSpline(sketch, "E9439", {"points": [v(7003.14, -2761.34) * mm, v(7003.14, -1849.52) * mm, v(7742.32, -1110.34) * mm, v(8654.14, -1110.34) * mm]});
            skFitSpline(sketch, "E9440", {"points": [v(8654.14, -1110.34) * mm, v(9565.97, -1110.34) * mm, v(10305.14, -1849.52) * mm, v(10305.14, -2761.34) * mm]});
            skLineSegment(sketch, "E9441", {"start": v(8003.3, -3470.71) * mm, "end": v(8024.02, -3489.2) * mm});
            skLineSegment(sketch, "E9442", {"start": v(8024.02, -3489.2) * mm, "end": v(8045.36, -3507.09) * mm});
            skLineSegment(sketch, "E9443", {"start": v(8045.36, -3507.09) * mm, "end": v(8067.1, -3524.36) * mm});
            skLineSegment(sketch, "E9444", {"start": v(8067.1, -3524.36) * mm, "end": v(8089.45, -3541.02) * mm});
            skLineSegment(sketch, "E9445", {"start": v(8089.45, -3541.02) * mm, "end": v(8053.69, -3590.4) * mm});
            skLineSegment(sketch, "E9446", {"start": v(8053.69, -3590.4) * mm, "end": v(8011.42, -3596.9) * mm});
            skLineSegment(sketch, "E9447", {"start": v(8011.42, -3596.9) * mm, "end": v(7987.65, -3578) * mm});
            skLineSegment(sketch, "E9448", {"start": v(7987.65, -3578) * mm, "end": v(7964.28, -3558.3) * mm});
            skLineSegment(sketch, "E9449", {"start": v(7964.28, -3558.3) * mm, "end": v(7920.8, -3560.53) * mm});
            skLineSegment(sketch, "E9450", {"start": v(7920.8, -3560.53) * mm, "end": v(7900.27, -3582.88) * mm});
            skLineSegment(sketch, "E9451", {"start": v(7900.27, -3582.88) * mm, "end": v(7904.34, -3627.38) * mm});
            skLineSegment(sketch, "E9452", {"start": v(7904.34, -3627.38) * mm, "end": v(7929.74, -3648.72) * mm});
            skLineSegment(sketch, "E9453", {"start": v(7929.74, -3648.72) * mm, "end": v(7955.74, -3669.24) * mm});
            skLineSegment(sketch, "E9454", {"start": v(7955.74, -3669.24) * mm, "end": v(8000.04, -3664.36) * mm});
            skFitSpline(sketch, "E9455", {"points": [v(10559.14, -2761.34) * mm, v(10559.14, -3813.45) * mm, v(9706.25, -4666.34) * mm, v(8654.14, -4666.34) * mm]});
            skFitSpline(sketch, "E9456", {"points": [v(8654.14, -4666.34) * mm, v(7602.04, -4666.34) * mm, v(6749.14, -3813.45) * mm, v(6749.14, -2761.34) * mm]});
            skFitSpline(sketch, "E9457", {"points": [v(6749.14, -2761.34) * mm, v(6749.14, -1709.24) * mm, v(7602.04, -856.34) * mm, v(8654.14, -856.34) * mm]});
            skFitSpline(sketch, "E9458", {"points": [v(8654.14, -856.34) * mm, v(9706.25, -856.34) * mm, v(10559.14, -1709.24) * mm, v(10559.14, -2761.34) * mm]});
            skFitSpline(sketch, "E9459", {"points": [v(10184.85, -2761.34) * mm, v(10184.85, -3606.73) * mm, v(9499.53, -4292.05) * mm, v(8654.14, -4292.05) * mm]});
            skFitSpline(sketch, "E9460", {"points": [v(8654.14, -4292.05) * mm, v(7808.76, -4292.05) * mm, v(7123.44, -3606.73) * mm, v(7123.44, -2761.34) * mm]});
            skFitSpline(sketch, "E9461", {"points": [v(7123.44, -2761.34) * mm, v(7123.44, -1915.96) * mm, v(7808.76, -1230.64) * mm, v(8654.14, -1230.64) * mm]});
            skFitSpline(sketch, "E9462", {"points": [v(8654.14, -1230.64) * mm, v(9499.53, -1230.64) * mm, v(10184.85, -1915.96) * mm, v(10184.85, -2761.34) * mm]});
            skSolve(sketch);
        }
        {
            var Q0;
            {var subQ78=sQuery(id+"F0.wireOp",EDGE,"E70");Q0=makeQuery(id+"F0.imprint","IMPRINT",FACE,{"disambiguationData":[TD([[makeQuery(id+"F0.imprint","IMPRINT",EDGE,{"derivedFrom":subQ78}),1.0]])]});}
            var Q1;
            {var subQ11=sQuery(id+"F0.wireOp",EDGE,"E517");Q1=makeQuery(id+"F0.imprint","IMPRINT",FACE,{"disambiguationData":[TD([[makeQuery(id+"F0.imprint","IMPRINT",EDGE,{"derivedFrom":subQ11}),1.0]])]});}
            var Q2;
            {var subQ5=sQuery(id+"F0.wireOp",EDGE,"E539");Q2=makeQuery(id+"F0.imprint","IMPRINT",FACE,{"disambiguationData":[TD([[makeQuery(id+"F0.imprint","IMPRINT",EDGE,{"derivedFrom":subQ5}),1.0]])]});}
            var Q3;
            {var subQ0=sQuery(id+"F0.wireOp",EDGE,"E465");Q3=makeQuery(id+"F0.imprint","IMPRINT",FACE,{"disambiguationData":[TD([[makeQuery(id+"F0.imprint","IMPRINT",EDGE,{"derivedFrom":subQ0}),1.0]])]});}
            var Q4;
            {var subQ10=sQuery(id+"F0.wireOp",EDGE,"E444");Q4=makeQuery(id+"F0.imprint","IMPRINT",FACE,{"disambiguationData":[TD([[makeQuery(id+"F0.imprint","IMPRINT",EDGE,{"derivedFrom":subQ10}),1.0]])]});}
            var Q5;
            {var subQ0=sQuery(id+"F0.wireOp",EDGE,"E391");Q5=makeQuery(id+"F0.imprint","IMPRINT",FACE,{"disambiguationData":[TD([[makeQuery(id+"F0.imprint","IMPRINT",EDGE,{"derivedFrom":subQ0}),1.0]])]});}
            var Q6;
            {var subQ13=sQuery(id+"F0.wireOp",EDGE,"E369");Q6=makeQuery(id+"F0.imprint","IMPRINT",FACE,{"disambiguationData":[TD([[makeQuery(id+"F0.imprint","IMPRINT",EDGE,{"derivedFrom":subQ13}),1.0]])]});}
            var Q7;
            {var subQ5=sQuery(id+"F0.wireOp",EDGE,"E317");Q7=makeQuery(id+"F0.imprint","IMPRINT",FACE,{"disambiguationData":[TD([[makeQuery(id+"F0.imprint","IMPRINT",EDGE,{"derivedFrom":subQ5}),1.0]])]});}
            var Q8;
            {var subQ12=sQuery(id+"F0.wireOp",EDGE,"E296");Q8=makeQuery(id+"F0.imprint","IMPRINT",FACE,{"disambiguationData":[TD([[makeQuery(id+"F0.imprint","IMPRINT",EDGE,{"derivedFrom":subQ12}),1.0]])]});}
            var Q9;
            {var subQ11=sQuery(id+"F0.wireOp",EDGE,"E221");Q9=makeQuery(id+"F0.imprint","IMPRINT",FACE,{"disambiguationData":[TD([[makeQuery(id+"F0.imprint","IMPRINT",EDGE,{"derivedFrom":subQ11}),1.0]])]});}
            var Q10;
            {var subQ0=sQuery(id+"F0.wireOp",EDGE,"E243");Q10=makeQuery(id+"F0.imprint","IMPRINT",FACE,{"disambiguationData":[TD([[makeQuery(id+"F0.imprint","IMPRINT",EDGE,{"derivedFrom":subQ0}),1.0]])]});}
            var Q11;
            {var subQ5=sQuery(id+"F0.wireOp",EDGE,"E169");Q11=makeQuery(id+"F0.imprint","IMPRINT",FACE,{"disambiguationData":[TD([[makeQuery(id+"F0.imprint","IMPRINT",EDGE,{"derivedFrom":subQ5}),1.0]])]});}
            var Q12;
            {var subQ11=sQuery(id+"F0.wireOp",EDGE,"E147");Q12=makeQuery(id+"F0.imprint","IMPRINT",FACE,{"disambiguationData":[TD([[makeQuery(id+"F0.imprint","IMPRINT",EDGE,{"derivedFrom":subQ11}),1.0]])]});}
            var Q13;
            {var subQ12=sQuery(id+"F0.wireOp",EDGE,"E74");Q13=makeQuery(id+"F0.imprint","IMPRINT",FACE,{"disambiguationData":[TD([[makeQuery(id+"F0.imprint","IMPRINT",EDGE,{"derivedFrom":subQ12}),1.0]])]});}
            var Q14;
            {var subQ0=sQuery(id+"F0.wireOp",EDGE,"E95");Q14=makeQuery(id+"F0.imprint","IMPRINT",FACE,{"disambiguationData":[TD([[makeQuery(id+"F0.imprint","IMPRINT",EDGE,{"derivedFrom":subQ0}),1.0]])]});}
            var Q15;
            {var subQ8=sQuery(id+"F0.wireOp",EDGE,"E1332");Q15=makeQuery(id+"F0.imprint","IMPRINT",FACE,{"disambiguationData":[TD([[makeQuery(id+"F0.imprint","IMPRINT",EDGE,{"derivedFrom":subQ8}),1.0]])]});}
            var Q16;
            {var subQ0=sQuery(id+"F0.wireOp",EDGE,"E1353");Q16=makeQuery(id+"F0.imprint","IMPRINT",FACE,{"disambiguationData":[TD([[makeQuery(id+"F0.imprint","IMPRINT",EDGE,{"derivedFrom":subQ0}),1.0]])]});}
            var Q17;
            {var subQ0=sQuery(id+"F0.wireOp",EDGE,"E761");Q17=makeQuery(id+"F0.imprint","IMPRINT",FACE,{"disambiguationData":[TD([[makeQuery(id+"F0.imprint","IMPRINT",EDGE,{"derivedFrom":subQ0}),1.0]])]});}
            var Q18;
            {var subQ11=sQuery(id+"F0.wireOp",EDGE,"E739");Q18=makeQuery(id+"F0.imprint","IMPRINT",FACE,{"disambiguationData":[TD([[makeQuery(id+"F0.imprint","IMPRINT",EDGE,{"derivedFrom":subQ11}),1.0]])]});}
            var Q19;
            {var subQ12=sQuery(id+"F0.wireOp",EDGE,"E665");Q19=makeQuery(id+"F0.imprint","IMPRINT",FACE,{"disambiguationData":[TD([[makeQuery(id+"F0.imprint","IMPRINT",EDGE,{"derivedFrom":subQ12}),1.0]])]});}
            var Q20;
            {var subQ0=sQuery(id+"F0.wireOp",EDGE,"E687");Q20=makeQuery(id+"F0.imprint","IMPRINT",FACE,{"disambiguationData":[TD([[makeQuery(id+"F0.imprint","IMPRINT",EDGE,{"derivedFrom":subQ0}),1.0]])]});}
            var Q21;
            {var subQ0=sQuery(id+"F0.wireOp",EDGE,"E613");Q21=makeQuery(id+"F0.imprint","IMPRINT",FACE,{"disambiguationData":[TD([[makeQuery(id+"F0.imprint","IMPRINT",EDGE,{"derivedFrom":subQ0}),1.0]])]});}
            var Q22;
            {var subQ4=sQuery(id+"F0.wireOp",EDGE,"E592");Q22=makeQuery(id+"F0.imprint","IMPRINT",FACE,{"disambiguationData":[TD([[makeQuery(id+"F0.imprint","IMPRINT",EDGE,{"derivedFrom":subQ4}),1.0]])]});}
            var Q23;
            Q23=makeQuery(id+"F0.imprint","IMPRINT",FACE,{"disambiguationData":[TD([[makeQuery(id+"F0.imprint","IMPRINT",EDGE,{"derivedFrom":sQuery(id+"F0.wireOp",EDGE,"E1497")}),1.0]])]});
            var Q24;
            {var subQ0=sQuery(id+"F0.wireOp",EDGE,"E1515");Q24=makeQuery(id+"F0.imprint","IMPRINT",FACE,{"disambiguationData":[TD([[makeQuery(id+"F0.imprint","IMPRINT",EDGE,{"derivedFrom":subQ0}),-1.0]])]});}
            var Q25;
            {var subQ0=sQuery(id+"F0.wireOp",EDGE,"E1450");Q25=makeQuery(id+"F0.imprint","IMPRINT",FACE,{"disambiguationData":[TD([[makeQuery(id+"F0.imprint","IMPRINT",EDGE,{"derivedFrom":subQ0}),-1.0]])]});}
            var Q26;
            Q26=makeQuery(id+"F0.imprint","IMPRINT",FACE,{"disambiguationData":[TD([[makeQuery(id+"F0.imprint","IMPRINT",EDGE,{"derivedFrom":sQuery(id+"F0.wireOp",EDGE,"E0")}),1.0]])]});
            var Q27;
            {var subQ10=sQuery(id+"F0.wireOp",EDGE,"E21");Q27=makeQuery(id+"F0.imprint","IMPRINT",FACE,{"disambiguationData":[TD([[makeQuery(id+"F0.imprint","IMPRINT",EDGE,{"derivedFrom":subQ10}),1.0]])]});}
            var Q28;
            {var subQ0=sQuery(id+"F0.wireOp",EDGE,"E1408");Q28=makeQuery(id+"F0.imprint","IMPRINT",FACE,{"disambiguationData":[TD([[makeQuery(id+"F0.imprint","IMPRINT",EDGE,{"derivedFrom":subQ0}),-1.0]])]});}
            var Q29;
            {var subQ0=sQuery(id+"F0.wireOp",EDGE,"E1410");Q29=makeQuery(id+"F0.imprint","IMPRINT",FACE,{"disambiguationData":[TD([[makeQuery(id+"F0.imprint","IMPRINT",EDGE,{"derivedFrom":subQ0}),-1.0]])]});}
            var Q30;
            {var subQ11=sQuery(id+"F0.wireOp",EDGE,"E1257");Q30=makeQuery(id+"F0.imprint","IMPRINT",FACE,{"disambiguationData":[TD([[makeQuery(id+"F0.imprint","IMPRINT",EDGE,{"derivedFrom":subQ11}),1.0]])]});}
            var Q31;
            {var subQ5=sQuery(id+"F0.wireOp",EDGE,"E1279");Q31=makeQuery(id+"F0.imprint","IMPRINT",FACE,{"disambiguationData":[TD([[makeQuery(id+"F0.imprint","IMPRINT",EDGE,{"derivedFrom":subQ5}),1.0]])]});}
            var Q32;
            {var subQ11=sQuery(id+"F0.wireOp",EDGE,"E1183");Q32=makeQuery(id+"F0.imprint","IMPRINT",FACE,{"disambiguationData":[TD([[makeQuery(id+"F0.imprint","IMPRINT",EDGE,{"derivedFrom":subQ11}),1.0]])]});}
            var Q33;
            {var subQ0=sQuery(id+"F0.wireOp",EDGE,"E1205");Q33=makeQuery(id+"F0.imprint","IMPRINT",FACE,{"disambiguationData":[TD([[makeQuery(id+"F0.imprint","IMPRINT",EDGE,{"derivedFrom":subQ0}),1.0]])]});}
            var Q34;
            {var subQ0=sQuery(id+"F0.wireOp",EDGE,"E1563");Q34=makeQuery(id+"F0.imprint","IMPRINT",FACE,{"disambiguationData":[TD([[makeQuery(id+"F0.imprint","IMPRINT",EDGE,{"derivedFrom":subQ0}),-1.0]])]});}
            var Q35;
            {var subQ0=sQuery(id+"F0.wireOp",EDGE,"E1570");Q35=makeQuery(id+"F0.imprint","IMPRINT",FACE,{"disambiguationData":[TD([[makeQuery(id+"F0.imprint","IMPRINT",EDGE,{"derivedFrom":subQ0}),1.0]])]});}
            var Q36;
            Q36=makeQuery(id+"F0.imprint","IMPRINT",FACE,{"disambiguationData":[TD([[makeQuery(id+"F0.imprint","IMPRINT",EDGE,{"derivedFrom":sQuery(id+"F0.wireOp",EDGE,"E1580")}),-1.0]])]});
            var Q37;
            {var subQ9=sQuery(id+"F0.wireOp",EDGE,"E1110");Q37=makeQuery(id+"F0.imprint","IMPRINT",FACE,{"disambiguationData":[TD([[makeQuery(id+"F0.imprint","IMPRINT",EDGE,{"derivedFrom":subQ9}),1.0]])]});}
            var Q38;
            {var subQ0=sQuery(id+"F0.wireOp",EDGE,"E1131");Q38=makeQuery(id+"F0.imprint","IMPRINT",FACE,{"disambiguationData":[TD([[makeQuery(id+"F0.imprint","IMPRINT",EDGE,{"derivedFrom":subQ0}),1.0]])]});}
            var Q39;
            {var subQ7=sQuery(id+"F0.wireOp",EDGE,"E1057");Q39=makeQuery(id+"F0.imprint","IMPRINT",FACE,{"disambiguationData":[TD([[makeQuery(id+"F0.imprint","IMPRINT",EDGE,{"derivedFrom":subQ7}),1.0]])]});}
            var Q40;
            {var subQ12=sQuery(id+"F0.wireOp",EDGE,"E1035");Q40=makeQuery(id+"F0.imprint","IMPRINT",FACE,{"disambiguationData":[TD([[makeQuery(id+"F0.imprint","IMPRINT",EDGE,{"derivedFrom":subQ12}),1.0]])]});}
            var Q41;
            {var subQ4=sQuery(id+"F0.wireOp",EDGE,"E962");Q41=makeQuery(id+"F0.imprint","IMPRINT",FACE,{"disambiguationData":[TD([[makeQuery(id+"F0.imprint","IMPRINT",EDGE,{"derivedFrom":subQ4}),1.0]])]});}
            var Q42;
            {var subQ0=sQuery(id+"F0.wireOp",EDGE,"E983");Q42=makeQuery(id+"F0.imprint","IMPRINT",FACE,{"disambiguationData":[TD([[makeQuery(id+"F0.imprint","IMPRINT",EDGE,{"derivedFrom":subQ0}),1.0]])]});}
            var Q43;
            {var subQ0=sQuery(id+"F0.wireOp",EDGE,"E909");Q43=makeQuery(id+"F0.imprint","IMPRINT",FACE,{"disambiguationData":[TD([[makeQuery(id+"F0.imprint","IMPRINT",EDGE,{"derivedFrom":subQ0}),1.0]])]});}
            var Q44;
            {var subQ11=sQuery(id+"F0.wireOp",EDGE,"E887");Q44=makeQuery(id+"F0.imprint","IMPRINT",FACE,{"disambiguationData":[TD([[makeQuery(id+"F0.imprint","IMPRINT",EDGE,{"derivedFrom":subQ11}),1.0]])]});}
            var Q45;
            {var subQ10=sQuery(id+"F0.wireOp",EDGE,"E814");Q45=makeQuery(id+"F0.imprint","IMPRINT",FACE,{"disambiguationData":[TD([[makeQuery(id+"F0.imprint","IMPRINT",EDGE,{"derivedFrom":subQ10}),1.0]])]});}
            var Q46;
            {var subQ0=sQuery(id+"F0.wireOp",EDGE,"E835");Q46=makeQuery(id+"F0.imprint","IMPRINT",FACE,{"disambiguationData":[TD([[makeQuery(id+"F0.imprint","IMPRINT",EDGE,{"derivedFrom":subQ0}),1.0]])]});}
            extrude(context, id + "F1", {"entities" : qUnion([Q0, Q1, Q2, Q3, Q4, Q5, Q6, Q7, Q8, Q9, Q10, Q11, Q12, Q13, Q14, Q15, Q16, Q17, Q18, Q19, Q20, Q21, Q22, Q23, Q24, Q25, Q26, Q27, Q28, Q29, Q30, Q31, Q32, Q33, Q34, Q35, Q36, Q37, Q38, Q39, Q40, Q41, Q42, Q43, Q44, Q45, Q46]), "depth" : 508 * mm, "offsetDistance" : 25.4 * mm});
        }
    });
